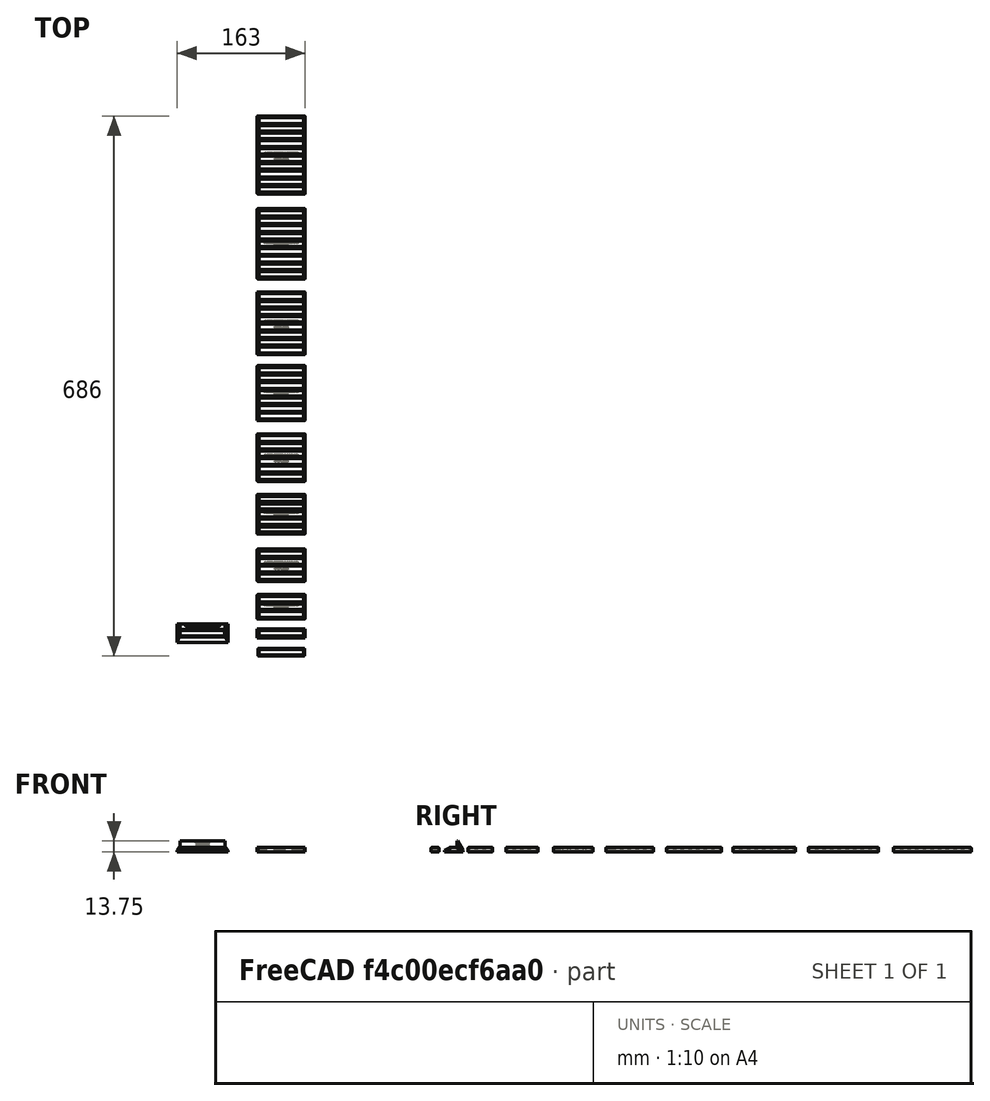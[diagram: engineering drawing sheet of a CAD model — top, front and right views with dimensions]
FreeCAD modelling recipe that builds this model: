
FCSTD DOCUMENT  (FreeCAD 0.21R33771 (Git))
Label: Game Boy Game Shelves
License: All rights reserved
LicenseURL: http://en.wikipedia.org/wiki/All_rights_reserved
objects: Sketcher::SketchObject×35, PartDesign::Pad×24, PartDesign::Pocket×14, PartDesign::Body×12, PartDesign::Chamfer×11, PartDesign::FeatureBase×11, PartDesign::Fillet×9, App::Part×3, PartDesign::ShapeBinder×1
note: 175 computed .brp shape members not serialized (recipe doc carries the construction recipe); baked Part::Feature solids carry a one-line shape summary decoded from their .brp

FEATURE [Sketcher::SketchObject] Sketch
  FullyConstrained = true
  MapMode = 5
  Support = -> [XY_Plane]
  sketch-geometry (16):
    g0: LineSegment StartX=0 StartY=0 StartZ=0 EndX=61 EndY=0 EndZ=0
    g1: LineSegment StartX=61 StartY=0 StartZ=0 EndX=61 EndY=11.7 EndZ=0
    g2: LineSegment StartX=61 StartY=11.7 StartZ=0 EndX=0 EndY=11.7 EndZ=0
    g3: LineSegment StartX=0 StartY=11.7 StartZ=0 EndX=0 EndY=0 EndZ=0
    g4: LineSegment StartX=0 StartY=0 StartZ=0 EndX=2 EndY=0 EndZ=0
    g5: LineSegment StartX=2 StartY=0 StartZ=0 EndX=2 EndY=2 EndZ=0
    g6: LineSegment StartX=2 StartY=2 StartZ=0 EndX=0 EndY=2 EndZ=0
    g7: LineSegment StartX=0 StartY=2 StartZ=0 EndX=0 EndY=0 EndZ=0
    g8: LineSegment StartX=61 StartY=11.7 StartZ=0 EndX=59 EndY=11.7 EndZ=0
    g9: LineSegment StartX=59 StartY=11.7 StartZ=0 EndX=59 EndY=9.7 EndZ=0
    g10: LineSegment StartX=59 StartY=9.7 StartZ=0 EndX=61 EndY=9.7 EndZ=0
    g11: LineSegment StartX=61 StartY=9.7 StartZ=0 EndX=61 EndY=11.7 EndZ=0
    g12: LineSegment StartX=2 StartY=2 StartZ=0 EndX=59 EndY=2 EndZ=0
    g13: LineSegment StartX=59 StartY=2 StartZ=0 EndX=59 EndY=9.7 EndZ=0
    g14: LineSegment StartX=59 StartY=9.7 StartZ=0 EndX=2 EndY=9.7 EndZ=0
    g15: LineSegment StartX=2 StartY=9.7 StartZ=0 EndX=2 EndY=2 EndZ=0
  constraints (43):
    c: Coincident(g0,g1)
    c: Coincident(g1,g2)
    c: Coincident(g2,g3)
    c: Coincident(g3,g0)
    c: Horizontal(g0)
    c: Horizontal(g2)
    c: Vertical(g1)
    c: Vertical(g3)
    c: Coincident(g0,g-1)
    c: Coincident(g4,g5)
    c: Coincident(g5,g6)
    c: Coincident(g6,g7)
    c: Coincident(g7,g4)
    c: Horizontal(g4)
    c: Horizontal(g6)
    c: Vertical(g5)
    c: Vertical(g7)
    c: Coincident(g4,g0)
    c: Coincident(g8,g9)
    c: Coincident(g9,g10)
    c: Coincident(g10,g11)
    c: Coincident(g11,g8)
    c: Horizontal(g8)
    c: Horizontal(g10)
    c: Vertical(g9)
    c: Vertical(g11)
    c: Coincident(g8,g1)
    c: Equal(g9,g10)
    c: Equal(g10,g5)
    c: Equal(g6,g5)
    c: Coincident(g12,g13)
    c: Coincident(g13,g14)
    c: Coincident(g14,g15)
    c: Coincident(g15,g12)
    c: Horizontal(g12)
    c: Horizontal(g14)
    c: Vertical(g13)
    c: Vertical(g15)
    c: Coincident(g12,g5)
    c: Coincident(g13,g9)
    c: Distance(g12) = 57
    c: Distance(g13) = 7.7
    c: Distance(g10) = 2
FEATURE [PartDesign::Pad] Pad
  Direction = (0,0,1)
  Length = 3.5
  Length2 = 10
  Profile = -> Sketch
  ReferenceAxis = -> Sketch [N_Axis]
  Type = 0
FEATURE [Sketcher::SketchObject] Sketch001
  ExternalGeometry = -> [Pad]
  FullyConstrained = true
  MapMode = 5
  Placement = pos=(0,0,0) rot=(1,0,0;3.14159rad)
  Support = -> [Pad]
  sketch-geometry (4):
    g0: LineSegment StartX=0 StartY=0 StartZ=0 EndX=61 EndY=0 EndZ=0
    g1: LineSegment StartX=61 StartY=0 StartZ=0 EndX=61 EndY=-11.7 EndZ=0
    g2: LineSegment StartX=61 StartY=-11.7 StartZ=0 EndX=0 EndY=-11.7 EndZ=0
    g3: LineSegment StartX=0 StartY=-11.7 StartZ=0 EndX=0 EndY=0 EndZ=0
  constraints (10):
    c: Coincident(g0,g1)
    c: Coincident(g1,g2)
    c: Coincident(g2,g3)
    c: Coincident(g3,g0)
    c: Horizontal(g0)
    c: Horizontal(g2)
    c: Vertical(g1)
    c: Vertical(g3)
    c: Coincident(g0,g-1)
    c: Coincident(g1,g-3)
FEATURE [PartDesign::Pad] Pad001
  BaseFeature = -> Pad
  Direction = (0,0,-1)
  Length = 2
  Length2 = 10
  Profile = -> Sketch001
  ReferenceAxis = -> Sketch001 [N_Axis]
  Refine = true
  Type = 0
FEATURE [PartDesign::Chamfer] Chamfer
  Angle = 45
  Base = -> Pad001 [Face8]
  BaseFeature = -> Pad001
  ChamferType = 1
  FlipDirection = false
  Size = 0.25
  Size2 = 3.49
  SupportTransform = false
  UseAllEdges = false
FEATURE [PartDesign::Body] Body  label="Shelf template"
  Group = -> [Sketch,Pad,Sketch001,Pad001,Chamfer]
  Origin = -> Origin
  Tip = -> Chamfer
FEATURE [PartDesign::ShapeBinder] ShapeBinder
  Support = -> [Pad001]
  TraceSupport = false
FEATURE [PartDesign::FeatureBase] Clone
  BaseFeature = -> ShapeBinder
FEATURE [PartDesign::FeatureBase] Clone001
  BaseFeature = -> ShapeBinder
FEATURE [PartDesign::FeatureBase] Clone002
  BaseFeature = -> ShapeBinder
  Placement = pos=(0,175,0) rot=(0,0,1;0rad)
FEATURE [PartDesign::FeatureBase] Clone003
  BaseFeature = -> ShapeBinder
FEATURE [PartDesign::FeatureBase] Clone004
  BaseFeature = -> ShapeBinder
FEATURE [PartDesign::FeatureBase] Clone005
  BaseFeature = -> ShapeBinder
FEATURE [PartDesign::FeatureBase] Clone006
  BaseFeature = -> ShapeBinder
FEATURE [PartDesign::FeatureBase] Clone007
  BaseFeature = -> ShapeBinder
FEATURE [Sketcher::SketchObject] Sketch002
  ExternalGeometry = -> [Clone007]
  FullyConstrained = true
  MapMode = 5
  Placement = pos=(0,0,-2) rot=(1,0,0;3.14159rad)
  Support = -> [Clone007]
  sketch-geometry (7):
    g0: LineSegment StartX=0 StartY=0 StartZ=0 EndX=61 EndY=0 EndZ=0
    g1: LineSegment StartX=61 StartY=0 StartZ=0 EndX=61 EndY=-31.1 EndZ=0
    g2: LineSegment StartX=61 StartY=-31.1 StartZ=0 EndX=0 EndY=-31.1 EndZ=0
    g3: LineSegment StartX=0 StartY=-31.1 StartZ=0 EndX=0 EndY=0 EndZ=0
    g4: LineSegment StartX=2 StartY=-2 StartZ=0 EndX=2 EndY=-11.7 EndZ=0
    g5: LineSegment StartX=2 StartY=-11.7 StartZ=0 EndX=2 EndY=-21.4 EndZ=0
    g6: LineSegment StartX=2 StartY=-21.4 StartZ=0 EndX=2 EndY=-31.1 EndZ=0
  constraints (19):
    c: Coincident(g0,g1)
    c: Coincident(g1,g2)
    c: Coincident(g2,g3)
    c: Coincident(g3,g0)
    c: Horizontal(g2)
    c: Vertical(g1)
    c: Vertical(g3)
    c: Coincident(g0,g-3)
    c: Coincident(g0,g-3)
    c: Coincident(g4,g-5)
    c: PointOnObject(g4,g-4)
    c: Vertical(g4)
    c: Coincident(g5,g4)
    c: Vertical(g5)
    c: Coincident(g6,g5)
    c: PointOnObject(g6,g2)
    c: Vertical(g6)
    c: Equal(g4,g5)
    c: Equal(g5,g6)
FEATURE [PartDesign::Pad] Pad002
  BaseFeature = -> Clone007
  Direction = (0,0,-1)
  Length = 2
  Length2 = 10
  Profile = -> Sketch002
  ReferenceAxis = -> Sketch002 [N_Axis]
  Reversed = true
  Type = 0
FEATURE [Sketcher::SketchObject] Sketch003
  ExternalGeometry = -> [Clone]
  FullyConstrained = true
  MapMode = 5
  Placement = pos=(0,0,-2) rot=(1,0,0;3.14159rad)
  Support = -> [Clone]
  sketch-geometry (8):
    g0: LineSegment StartX=0 StartY=0 StartZ=0 EndX=61 EndY=0 EndZ=0
    g1: LineSegment StartX=61 StartY=0 StartZ=0 EndX=61 EndY=-40.8 EndZ=0
    g2: LineSegment StartX=61 StartY=-40.8 StartZ=0 EndX=0 EndY=-40.8 EndZ=0
    g3: LineSegment StartX=0 StartY=-40.8 StartZ=0 EndX=0 EndY=0 EndZ=0
    g4: LineSegment StartX=2 StartY=-2 StartZ=0 EndX=2 EndY=-11.7 EndZ=0
    g5: LineSegment StartX=2 StartY=-11.7 StartZ=0 EndX=2 EndY=-21.4 EndZ=0
    g6: LineSegment StartX=2 StartY=-21.4 StartZ=0 EndX=2 EndY=-31.1 EndZ=0
    g7: LineSegment StartX=2 StartY=-31.1 StartZ=0 EndX=2 EndY=-40.8 EndZ=0
  constraints (22):
    c: Coincident(g0,g1)
    c: Coincident(g1,g2)
    c: Coincident(g2,g3)
    c: Coincident(g3,g0)
    c: Horizontal(g2)
    c: Vertical(g1)
    c: Vertical(g3)
    c: Coincident(g0,g-3)
    c: Coincident(g0,g-3)
    c: Coincident(g4,g-5)
    c: PointOnObject(g4,g-4)
    c: Vertical(g4)
    c: Coincident(g5,g4)
    c: Vertical(g5)
    c: Coincident(g6,g5)
    c: Vertical(g6)
    c: Coincident(g7,g6)
    c: PointOnObject(g7,g2)
    c: Vertical(g7)
    c: Equal(g7,g6)
    c: Equal(g6,g5)
    c: Equal(g5,g4)
FEATURE [PartDesign::Pad] Pad003
  BaseFeature = -> Clone
  Direction = (0,0,-1)
  Length = 2
  Length2 = 10
  Profile = -> Sketch003
  ReferenceAxis = -> Sketch003 [N_Axis]
  Reversed = true
  Type = 0
FEATURE [Sketcher::SketchObject] Sketch004
  ExternalGeometry = -> [Clone001]
  FullyConstrained = true
  MapMode = 5
  Placement = pos=(0,0,-2) rot=(1,0,0;3.14159rad)
  Support = -> [Clone001]
  sketch-geometry (9):
    g0: LineSegment StartX=2 StartY=-2 StartZ=0 EndX=2 EndY=-11.7 EndZ=0
    g1: LineSegment StartX=2 StartY=-11.7 StartZ=0 EndX=2 EndY=-21.4 EndZ=0
    g2: LineSegment StartX=2 StartY=-21.4 StartZ=0 EndX=2 EndY=-31.1 EndZ=0
    g3: LineSegment StartX=2 StartY=-31.1 StartZ=0 EndX=2 EndY=-40.8 EndZ=0
    g4: LineSegment StartX=2 StartY=-40.8 StartZ=0 EndX=2 EndY=-50.5 EndZ=0
    g5: LineSegment StartX=61 StartY=0 StartZ=0 EndX=0 EndY=0 EndZ=0
    g6: LineSegment StartX=0 StartY=0 StartZ=0 EndX=0 EndY=-50.5 EndZ=0
    g7: LineSegment StartX=0 StartY=-50.5 StartZ=0 EndX=61 EndY=-50.5 EndZ=0
    g8: LineSegment StartX=61 StartY=-50.5 StartZ=0 EndX=61 EndY=0 EndZ=0
  constraints (26):
    c: Coincident(g0,g-5)
    c: PointOnObject(g0,g-4)
    c: Vertical(g0)
    c: Coincident(g1,g0)
    c: Vertical(g1)
    c: Coincident(g2,g1)
    c: Vertical(g2)
    c: Coincident(g3,g2)
    c: Vertical(g3)
    c: Coincident(g4,g3)
    c: Vertical(g4)
    c: Equal(g0,g1)
    c: Equal(g1,g2)
    c: Equal(g2,g3)
    c: Equal(g3,g4)
    c: Coincident(g5,g6)
    c: Coincident(g6,g7)
    c: Coincident(g7,g8)
    c: Coincident(g8,g5)
    c: Horizontal(g5)
    c: Horizontal(g7)
    c: Vertical(g6)
    c: Vertical(g8)
    c: Coincident(g5,g-3)
    c: PointOnObject(g6,g-2)
    c: PointOnObject(g4,g7)
FEATURE [PartDesign::Pad] Pad004
  BaseFeature = -> Clone001
  Direction = (0,0,-1)
  Length = 2
  Length2 = 10
  Profile = -> Sketch004
  ReferenceAxis = -> Sketch004 [N_Axis]
  Reversed = true
  Type = 0
FEATURE [Sketcher::SketchObject] Sketch005
  ExternalGeometry = -> [Clone002]
  FullyConstrained = true
  MapMode = 5
  Placement = pos=(0,175,-2) rot=(1,0,0;3.14159rad)
  Support = -> [Clone002]
  sketch-geometry (10):
    g0: LineSegment StartX=61 StartY=0 StartZ=0 EndX=0 EndY=0 EndZ=0
    g1: LineSegment StartX=0 StartY=0 StartZ=0 EndX=0 EndY=-60.2 EndZ=0
    g2: LineSegment StartX=0 StartY=-60.2 StartZ=0 EndX=61 EndY=-60.2 EndZ=0
    g3: LineSegment StartX=61 StartY=-60.2 StartZ=0 EndX=61 EndY=0 EndZ=0
    g4: LineSegment StartX=2 StartY=-2 StartZ=0 EndX=2 EndY=-11.7 EndZ=0
    g5: LineSegment StartX=2 StartY=-11.7 StartZ=0 EndX=2 EndY=-21.4 EndZ=0
    g6: LineSegment StartX=2 StartY=-21.4 StartZ=0 EndX=2 EndY=-31.1 EndZ=0
    g7: LineSegment StartX=2 StartY=-31.1 StartZ=0 EndX=2 EndY=-40.8 EndZ=0
    g8: LineSegment StartX=2 StartY=-40.8 StartZ=0 EndX=2 EndY=-50.5 EndZ=0
    g9: LineSegment StartX=2 StartY=-50.5 StartZ=0 EndX=2 EndY=-60.2 EndZ=0
  constraints (29):
    c: Coincident(g0,g1)
    c: Coincident(g1,g2)
    c: Coincident(g2,g3)
    c: Coincident(g3,g0)
    c: Horizontal(g0)
    c: Horizontal(g2)
    c: Vertical(g1)
    c: Vertical(g3)
    c: Coincident(g0,g-3)
    c: PointOnObject(g1,g-2)
    c: Coincident(g4,g-5)
    c: PointOnObject(g4,g-4)
    c: Coincident(g5,g4)
    c: Vertical(g5)
    c: Coincident(g6,g5)
    c: Vertical(g6)
    c: Coincident(g7,g6)
    c: Vertical(g7)
    c: Coincident(g8,g7)
    c: Vertical(g8)
    c: Coincident(g9,g8)
    c: PointOnObject(g9,g2)
    c: Vertical(g9)
    c: Vertical(g4)
    c: Equal(g9,g8)
    c: Equal(g8,g7)
    c: Equal(g7,g6)
    c: Equal(g6,g5)
    c: Equal(g5,g4)
FEATURE [PartDesign::Pad] Pad005
  BaseFeature = -> Clone002
  Direction = (0,0,-1)
  Length = 2
  Length2 = 10
  Placement = pos=(0,175,0) rot=(0,0,1;0rad)
  Profile = -> Sketch005
  ReferenceAxis = -> Sketch005 [N_Axis]
  Reversed = true
  Type = 0
FEATURE [Sketcher::SketchObject] Sketch006
  ExternalGeometry = -> [Clone003]
  FullyConstrained = true
  MapMode = 5
  Placement = pos=(0,0,-2) rot=(1,0,0;3.14159rad)
  Support = -> [Clone003]
  sketch-geometry (11):
    g0: LineSegment StartX=61 StartY=0 StartZ=0 EndX=0 EndY=0 EndZ=0
    g1: LineSegment StartX=0 StartY=0 StartZ=0 EndX=0 EndY=-69.9 EndZ=0
    g2: LineSegment StartX=0 StartY=-69.9 StartZ=0 EndX=61 EndY=-69.9 EndZ=0
    g3: LineSegment StartX=61 StartY=-69.9 StartZ=0 EndX=61 EndY=0 EndZ=0
    g4: LineSegment StartX=2 StartY=-2 StartZ=0 EndX=2 EndY=-11.7 EndZ=0
    g5: LineSegment StartX=2 StartY=-11.7 StartZ=0 EndX=2 EndY=-21.4 EndZ=0
    g6: LineSegment StartX=2 StartY=-21.4 StartZ=0 EndX=2 EndY=-31.1 EndZ=0
    g7: LineSegment StartX=2 StartY=-31.1 StartZ=0 EndX=2 EndY=-40.8 EndZ=0
    g8: LineSegment StartX=2 StartY=-40.8 StartZ=0 EndX=2 EndY=-50.5 EndZ=0
    g9: LineSegment StartX=2 StartY=-50.5 StartZ=0 EndX=2 EndY=-60.2 EndZ=0
    g10: LineSegment StartX=2 StartY=-60.2 StartZ=0 EndX=2 EndY=-69.9 EndZ=0
  constraints (31):
    c: Coincident(g0,g1)
    c: Coincident(g1,g2)
    c: Coincident(g2,g3)
    c: Coincident(g3,g0)
    c: Horizontal(g2)
    c: Vertical(g1)
    c: Vertical(g3)
    c: Coincident(g0,g-3)
    c: Coincident(g-3,g0)
    c: Coincident(g4,g-5)
    c: PointOnObject(g4,g-4)
    c: Vertical(g4)
    c: Coincident(g5,g4)
    c: Vertical(g5)
    c: Coincident(g6,g5)
    c: Coincident(g7,g6)
    c: Coincident(g8,g7)
    c: Vertical(g8)
    c: Coincident(g9,g8)
    c: Vertical(g9)
    c: PointOnObject(g10,g2)
    c: Vertical(g10)
    c: Coincident(g10,g9)
    c: Vertical(g7)
    c: Vertical(g6)
    c: Equal(g4,g5)
    c: Equal(g5,g6)
    c: Equal(g6,g7)
    c: Equal(g8,g7)
    c: Equal(g9,g8)
    c: Equal(g9,g10)
FEATURE [PartDesign::Pad] Pad006
  BaseFeature = -> Clone003
  Direction = (0,0,-1)
  Length = 2
  Length2 = 10
  Profile = -> Sketch006
  ReferenceAxis = -> Sketch006 [N_Axis]
  Reversed = true
  Type = 0
FEATURE [Sketcher::SketchObject] Sketch007
  ExternalGeometry = -> [Clone004]
  FullyConstrained = true
  MapMode = 5
  Placement = pos=(0,0,-2) rot=(1,0,0;3.14159rad)
  Support = -> [Clone004]
  sketch-geometry (12):
    g0: LineSegment StartX=61 StartY=0 StartZ=0 EndX=0 EndY=0 EndZ=0
    g1: LineSegment StartX=0 StartY=0 StartZ=0 EndX=0 EndY=-79.6 EndZ=0
    g2: LineSegment StartX=0 StartY=-79.6 StartZ=0 EndX=61 EndY=-79.6 EndZ=0
    g3: LineSegment StartX=61 StartY=-79.6 StartZ=0 EndX=61 EndY=0 EndZ=0
    g4: LineSegment StartX=2 StartY=-2 StartZ=0 EndX=2 EndY=-11.7 EndZ=0
    g5: LineSegment StartX=2 StartY=-11.7 StartZ=0 EndX=2 EndY=-21.4 EndZ=0
    g6: LineSegment StartX=2 StartY=-21.4 StartZ=0 EndX=2 EndY=-31.1 EndZ=0
    g7: LineSegment StartX=2 StartY=-31.1 StartZ=0 EndX=2 EndY=-40.8 EndZ=0
    g8: LineSegment StartX=2 StartY=-40.8 StartZ=0 EndX=2 EndY=-50.5 EndZ=0
    g9: LineSegment StartX=2 StartY=-50.5 StartZ=0 EndX=2 EndY=-60.2 EndZ=0
    g10: LineSegment StartX=2 StartY=-60.2 StartZ=0 EndX=2 EndY=-69.9 EndZ=0
    g11: LineSegment StartX=2 StartY=-69.9 StartZ=0 EndX=2 EndY=-79.6 EndZ=0
  constraints (34):
    c: Coincident(g0,g1)
    c: Coincident(g1,g2)
    c: Coincident(g2,g3)
    c: Coincident(g3,g0)
    c: Horizontal(g2)
    c: Vertical(g1)
    c: Vertical(g3)
    c: Coincident(g0,g-3)
    c: Coincident(g4,g-5)
    c: PointOnObject(g4,g-4)
    c: Vertical(g4)
    c: Coincident(g5,g4)
    c: Vertical(g5)
    c: Coincident(g6,g5)
    c: Vertical(g6)
    c: Coincident(g7,g6)
    c: Vertical(g7)
    c: Coincident(g8,g7)
    c: Vertical(g8)
    c: Coincident(g9,g8)
    c: Vertical(g9)
    c: Coincident(g10,g9)
    c: Vertical(g10)
    c: Coincident(g11,g10)
    c: PointOnObject(g11,g2)
    c: Vertical(g11)
    c: Coincident(g0,g-3)
    c: Equal(g11,g10)
    c: Equal(g10,g9)
    c: Equal(g9,g8)
    c: Equal(g8,g7)
    c: Equal(g6,g5)
    c: Equal(g5,g7)
    c: Equal(g5,g4)
FEATURE [PartDesign::Pad] Pad007
  BaseFeature = -> Clone004
  Direction = (0,0,-1)
  Length = 2
  Length2 = 10
  Profile = -> Sketch007
  ReferenceAxis = -> Sketch007 [N_Axis]
  Reversed = true
  Type = 0
FEATURE [Sketcher::SketchObject] Sketch008
  ExternalGeometry = -> [Clone004]
  FullyConstrained = true
  MapMode = 5
  Placement = pos=(0,0,3.5) rot=(0,0,1;0rad)
  Support = -> [Clone004]
  sketch-geometry (44):
    g0: LineSegment StartX=0 StartY=0 StartZ=0 EndX=61 EndY=0 EndZ=0
    g1: LineSegment StartX=61 StartY=0 StartZ=0 EndX=61 EndY=79.6 EndZ=0
    g2: LineSegment StartX=61 StartY=79.6 StartZ=0 EndX=0 EndY=79.6 EndZ=0
    g3: LineSegment StartX=0 StartY=79.6 StartZ=0 EndX=0 EndY=0 EndZ=0
    g4: LineSegment StartX=59 StartY=2 StartZ=0 EndX=59 EndY=11.7 EndZ=0
    g5: LineSegment StartX=59 StartY=11.7 StartZ=0 EndX=59 EndY=21.4 EndZ=0
    g6: LineSegment StartX=59 StartY=21.4 StartZ=0 EndX=59 EndY=31.1 EndZ=0
    g7: LineSegment StartX=59 StartY=31.1 StartZ=0 EndX=59 EndY=40.8 EndZ=0
    g8: LineSegment StartX=59 StartY=40.8 StartZ=0 EndX=59 EndY=50.5 EndZ=0
    g9: LineSegment StartX=59 StartY=50.5 StartZ=0 EndX=59 EndY=60.2 EndZ=0
    g10: LineSegment StartX=59 StartY=60.2 StartZ=0 EndX=59 EndY=69.9 EndZ=0
    g11: LineSegment StartX=59 StartY=2 StartZ=0 EndX=2 EndY=2 EndZ=0
    g12: LineSegment StartX=2 StartY=2 StartZ=0 EndX=2 EndY=9.7 EndZ=0
    g13: LineSegment StartX=2 StartY=9.7 StartZ=0 EndX=59 EndY=9.7 EndZ=0
    g14: LineSegment StartX=59 StartY=9.7 StartZ=0 EndX=59 EndY=2 EndZ=0
    g15: LineSegment StartX=59 StartY=11.7 StartZ=0 EndX=2 EndY=11.7 EndZ=0
    g16: LineSegment StartX=2 StartY=11.7 StartZ=0 EndX=2 EndY=19.4 EndZ=0
    g17: LineSegment StartX=2 StartY=19.4 StartZ=0 EndX=59 EndY=19.4 EndZ=0
    g18: LineSegment StartX=59 StartY=19.4 StartZ=0 EndX=59 EndY=11.7 EndZ=0
    g19: LineSegment StartX=59 StartY=21.4 StartZ=0 EndX=2 EndY=21.4 EndZ=0
    g20: LineSegment StartX=2 StartY=21.4 StartZ=0 EndX=2 EndY=29.1 EndZ=0
    g21: LineSegment StartX=2 StartY=29.1 StartZ=0 EndX=59 EndY=29.1 EndZ=0
    g22: LineSegment StartX=59 StartY=29.1 StartZ=0 EndX=59 EndY=21.4 EndZ=0
    g23: LineSegment StartX=59 StartY=31.1 StartZ=0 EndX=2 EndY=31.1 EndZ=0
    g24: LineSegment StartX=2 StartY=31.1 StartZ=0 EndX=2 EndY=38.8 EndZ=0
    g25: LineSegment StartX=2 StartY=38.8 StartZ=0 EndX=59 EndY=38.8 EndZ=0
    g26: LineSegment StartX=59 StartY=38.8 StartZ=0 EndX=59 EndY=31.1 EndZ=0
    g27: LineSegment StartX=59 StartY=40.8 StartZ=0 EndX=2 EndY=40.8 EndZ=0
    g28: LineSegment StartX=2 StartY=40.8 StartZ=0 EndX=2 EndY=48.5 EndZ=0
    g29: LineSegment StartX=2 StartY=48.5 StartZ=0 EndX=59 EndY=48.5 EndZ=0
    g30: LineSegment StartX=59 StartY=48.5 StartZ=0 EndX=59 EndY=40.8 EndZ=0
    g31: LineSegment StartX=59 StartY=50.5 StartZ=0 EndX=2 EndY=50.5 EndZ=0
    g32: LineSegment StartX=2 StartY=50.5 StartZ=0 EndX=2 EndY=58.2 EndZ=0
    g33: LineSegment StartX=2 StartY=58.2 StartZ=0 EndX=59 EndY=58.2 EndZ=0
    g34: LineSegment StartX=59 StartY=58.2 StartZ=0 EndX=59 EndY=50.5 EndZ=0
    g35: LineSegment StartX=59 StartY=60.2 StartZ=0 EndX=2 EndY=60.2 EndZ=0
    g36: LineSegment StartX=2 StartY=60.2 StartZ=0 EndX=2 EndY=67.9 EndZ=0
    g37: LineSegment StartX=2 StartY=67.9 StartZ=0 EndX=59 EndY=67.9 EndZ=0
    g38: LineSegment StartX=59 StartY=67.9 StartZ=0 EndX=59 EndY=60.2 EndZ=0
    g39: LineSegment StartX=59 StartY=69.9 StartZ=0 EndX=59 EndY=79.6 EndZ=0
    g40: LineSegment StartX=59 StartY=69.9 StartZ=0 EndX=2 EndY=69.9 EndZ=0
    g41: LineSegment StartX=2 StartY=69.9 StartZ=0 EndX=2 EndY=77.6 EndZ=0
    g42: LineSegment StartX=2 StartY=77.6 StartZ=0 EndX=59 EndY=77.6 EndZ=0
    g43: LineSegment StartX=59 StartY=77.6 StartZ=0 EndX=59 EndY=69.9 EndZ=0
  constraints (121):
    c: Coincident(g0,g1)
    c: Coincident(g1,g2)
    c: Coincident(g2,g3)
    c: Coincident(g3,g0)
    c: Horizontal(g2)
    c: Vertical(g1)
    c: Vertical(g3)
    c: Coincident(g0,g-3)
    c: Coincident(g-3,g0)
    c: Coincident(g4,g-4)
    c: Vertical(g4)
    c: Coincident(g5,g4)
    c: Vertical(g5)
    c: Coincident(g6,g5)
    c: Vertical(g6)
    c: Coincident(g7,g6)
    c: Vertical(g7)
    c: Coincident(g8,g7)
    c: Vertical(g8)
    c: Coincident(g9,g8)
    c: Vertical(g9)
    c: Coincident(g10,g9)
    c: Vertical(g10)
    c: Equal(g10,g9)
    c: Equal(g9,g8)
    c: Equal(g8,g7)
    c: Equal(g7,g6)
    c: Equal(g6,g5)
    c: Equal(g5,g4)
    c: PointOnObject(g4,g-5)
    c: Coincident(g11,g12)
    c: Coincident(g12,g13)
    c: Coincident(g13,g14)
    c: Coincident(g14,g11)
    c: Horizontal(g11)
    c: Horizontal(g13)
    c: Vertical(g12)
    c: Vertical(g14)
    c: Coincident(g11,g4)
    c: Coincident(g12,g-6)
    c: Coincident(g15,g16)
    c: Coincident(g16,g17)
    c: Coincident(g17,g18)
    c: Coincident(g18,g15)
    c: Horizontal(g15)
    c: Horizontal(g17)
    c: Vertical(g16)
    c: Vertical(g18)
    c: Coincident(g15,g4)
    c: Coincident(g19,g20)
    c: Coincident(g20,g21)
    c: Coincident(g21,g22)
    c: Coincident(g22,g19)
    c: Horizontal(g19)
    c: Horizontal(g21)
    c: Vertical(g20)
    c: Vertical(g22)
    c: Coincident(g19,g5)
    c: Coincident(g23,g24)
    c: Coincident(g24,g25)
    c: Coincident(g25,g26)
    c: Coincident(g26,g23)
    c: Horizontal(g23)
    c: Horizontal(g25)
    c: Vertical(g24)
    c: Vertical(g26)
    c: Coincident(g23,g6)
    c: Coincident(g27,g28)
    c: Coincident(g28,g29)
    c: Coincident(g29,g30)
    c: Coincident(g30,g27)
    c: Horizontal(g27)
    c: Horizontal(g29)
    c: Vertical(g28)
    c: Vertical(g30)
    c: Coincident(g27,g7)
    c: Coincident(g31,g32)
    c: Coincident(g32,g33)
    c: Coincident(g33,g34)
    c: Coincident(g34,g31)
    c: Horizontal(g31)
    c: Horizontal(g33)
    c: Vertical(g32)
    c: Vertical(g34)
    c: Coincident(g31,g8)
    c: Coincident(g35,g36)
    c: Coincident(g36,g37)
    c: Coincident(g37,g38)
    c: Coincident(g38,g35)
    c: Horizontal(g35)
    c: Horizontal(g37)
    c: Vertical(g36)
    c: Vertical(g38)
    c: Coincident(g35,g9)
    c: Equal(g36,g32)
    c: Equal(g32,g28)
    c: Equal(g28,g24)
    c: Equal(g20,g24)
    c: Equal(g20,g16)
    c: Equal(g16,g12)
    c: Equal(g13,g15)
    c: Equal(g17,g19)
    c: Equal(g21,g23)
    c: Equal(g25,g27)
    c: Equal(g29,g31)
    c: Equal(g33,g35)
    c: Coincident(g39,g10)
    c: Vertical(g39)
    c: Equal(g39,g10)
    c: PointOnObject(g39,g2)
    c: Coincident(g40,g41)
    c: Coincident(g41,g42)
    c: Coincident(g42,g43)
    c: Coincident(g43,g40)
    c: Horizontal(g40)
    c: Horizontal(g42)
    c: Vertical(g41)
    c: Vertical(g43)
    c: Coincident(g40,g10)
    c: Equal(g41,g36)
    c: Equal(g40,g37)
FEATURE [PartDesign::Pad] Pad008
  BaseFeature = -> Pad007
  Direction = (0,0,1)
  Length = 10
  Length2 = 10
  Profile = -> Sketch008
  ReferenceAxis = -> Sketch008 [N_Axis]
  Refine = true
  Type = 3
  UpToFace = -> Pad007 [Face6]
FEATURE [Sketcher::SketchObject] Sketch009
  ExternalGeometry = -> [Clone005]
  FullyConstrained = true
  MapMode = 5
  Placement = pos=(0,0,-2) rot=(1,0,0;3.14159rad)
  Support = -> [Clone005]
  sketch-geometry (13):
    g0: LineSegment StartX=61 StartY=0 StartZ=0 EndX=0 EndY=0 EndZ=0
    g1: LineSegment StartX=0 StartY=0 StartZ=0 EndX=0 EndY=-89.3 EndZ=0
    g2: LineSegment StartX=0 StartY=-89.3 StartZ=0 EndX=61 EndY=-89.3 EndZ=0
    g3: LineSegment StartX=61 StartY=-89.3 StartZ=0 EndX=61 EndY=0 EndZ=0
    g4: LineSegment StartX=2 StartY=-2 StartZ=0 EndX=2 EndY=-11.7 EndZ=0
    g5: LineSegment StartX=2 StartY=-11.7 StartZ=0 EndX=2 EndY=-21.4 EndZ=0
    g6: LineSegment StartX=2 StartY=-21.4 StartZ=0 EndX=2 EndY=-31.1 EndZ=0
    g7: LineSegment StartX=2 StartY=-31.1 StartZ=0 EndX=2 EndY=-40.8 EndZ=0
    g8: LineSegment StartX=2 StartY=-40.8 StartZ=0 EndX=2 EndY=-50.5 EndZ=0
    g9: LineSegment StartX=2 StartY=-50.5 StartZ=0 EndX=2 EndY=-60.2 EndZ=0
    g10: LineSegment StartX=2 StartY=-60.2 StartZ=0 EndX=2 EndY=-69.9 EndZ=0
    g11: LineSegment StartX=2 StartY=-69.9 StartZ=0 EndX=2 EndY=-79.6 EndZ=0
    g12: LineSegment StartX=2 StartY=-79.6 StartZ=0 EndX=2 EndY=-89.3 EndZ=0
  constraints (38):
    c: Coincident(g0,g1)
    c: Coincident(g1,g2)
    c: Coincident(g2,g3)
    c: Coincident(g3,g0)
    c: Horizontal(g0)
    c: Horizontal(g2)
    c: Vertical(g1)
    c: Vertical(g3)
    c: Coincident(g0,g-3)
    c: PointOnObject(g1,g-2)
    c: Coincident(g4,g-5)
    c: PointOnObject(g4,g-4)
    c: Vertical(g4)
    c: Coincident(g5,g4)
    c: Vertical(g5)
    c: Coincident(g6,g5)
    c: Vertical(g6)
    c: Coincident(g7,g6)
    c: Vertical(g7)
    c: Coincident(g8,g7)
    c: Coincident(g9,g8)
    c: Vertical(g9)
    c: Coincident(g10,g9)
    c: Vertical(g10)
    c: Coincident(g11,g10)
    c: Vertical(g11)
    c: Coincident(g12,g11)
    c: PointOnObject(g12,g2)
    c: Vertical(g12)
    c: Vertical(g8)
    c: Equal(g11,g12)
    c: Equal(g11,g10)
    c: Equal(g10,g9)
    c: Equal(g9,g8)
    c: Equal(g8,g7)
    c: Equal(g7,g6)
    c: Equal(g5,g6)
    c: Equal(g5,g4)
FEATURE [PartDesign::Pad] Pad009
  BaseFeature = -> Clone005
  Direction = (0,0,-1)
  Length = 2
  Length2 = 10
  Profile = -> Sketch009
  ReferenceAxis = -> Sketch009 [N_Axis]
  Reversed = true
  Type = 0
FEATURE [Sketcher::SketchObject] Sketch010
  ExternalGeometry = -> [Clone006]
  FullyConstrained = true
  MapMode = 5
  Placement = pos=(0,0,-2) rot=(1,0,0;3.14159rad)
  Support = -> [Clone006]
  sketch-geometry (14):
    g0: LineSegment StartX=61 StartY=0 StartZ=0 EndX=0 EndY=0 EndZ=0
    g1: LineSegment StartX=0 StartY=0 StartZ=0 EndX=0 EndY=-99 EndZ=0
    g2: LineSegment StartX=0 StartY=-99 StartZ=0 EndX=61 EndY=-99 EndZ=0
    g3: LineSegment StartX=61 StartY=-99 StartZ=0 EndX=61 EndY=0 EndZ=0
    g4: LineSegment StartX=2 StartY=-2 StartZ=0 EndX=2 EndY=-11.7 EndZ=0
    g5: LineSegment StartX=2 StartY=-11.7 StartZ=0 EndX=2 EndY=-21.4 EndZ=0
    g6: LineSegment StartX=2 StartY=-21.4 StartZ=0 EndX=2 EndY=-31.1 EndZ=0
    g7: LineSegment StartX=2 StartY=-31.1 StartZ=0 EndX=2 EndY=-40.8 EndZ=0
    g8: LineSegment StartX=2 StartY=-40.8 StartZ=0 EndX=2 EndY=-50.5 EndZ=0
    g9: LineSegment StartX=2 StartY=-50.5 StartZ=0 EndX=2 EndY=-60.2 EndZ=0
    g10: LineSegment StartX=2 StartY=-60.2 StartZ=0 EndX=2 EndY=-69.9 EndZ=0
    g11: LineSegment StartX=2 StartY=-69.9 StartZ=0 EndX=2 EndY=-79.6 EndZ=0
    g12: LineSegment StartX=2 StartY=-79.6 StartZ=0 EndX=2 EndY=-89.3 EndZ=0
    g13: LineSegment StartX=2 StartY=-89.3 StartZ=0 EndX=2 EndY=-99 EndZ=0
  constraints (41):
    c: Coincident(g0,g1)
    c: Coincident(g1,g2)
    c: Coincident(g2,g3)
    c: Coincident(g3,g0)
    c: Horizontal(g0)
    c: Horizontal(g2)
    c: Vertical(g1)
    c: Vertical(g3)
    c: Coincident(g0,g-3)
    c: PointOnObject(g1,g-2)
    c: Coincident(g4,g-5)
    c: PointOnObject(g4,g-4)
    c: Vertical(g4)
    c: Coincident(g5,g4)
    c: Vertical(g5)
    c: Coincident(g6,g5)
    c: Vertical(g6)
    c: Coincident(g7,g6)
    c: Vertical(g7)
    c: Coincident(g8,g7)
    c: Vertical(g8)
    c: Coincident(g9,g8)
    c: Vertical(g9)
    c: Coincident(g10,g9)
    c: Vertical(g10)
    c: Coincident(g11,g10)
    c: Vertical(g11)
    c: Coincident(g12,g11)
    c: Vertical(g12)
    c: Coincident(g13,g12)
    c: PointOnObject(g13,g2)
    c: Vertical(g13)
    c: Equal(g13,g12)
    c: Equal(g12,g11)
    c: Equal(g11,g10)
    c: Equal(g10,g9)
    c: Equal(g8,g9)
    c: Equal(g7,g8)
    c: Equal(g6,g7)
    c: Equal(g5,g6)
    c: Equal(g5,g4)
FEATURE [PartDesign::Pad] Pad010
  BaseFeature = -> Clone006
  Direction = (0,0,-1)
  Length = 2
  Length2 = 10
  Profile = -> Sketch010
  ReferenceAxis = -> Sketch010 [N_Axis]
  Reversed = true
  Type = 0
FEATURE [Sketcher::SketchObject] Sketch011
  ExternalGeometry = -> [Clone007]
  FullyConstrained = true
  MapMode = 5
  Placement = pos=(0,0,3.5) rot=(0,0,1;0rad)
  Support = -> [Clone007]
  sketch-geometry (19):
    g0: LineSegment StartX=59 StartY=2 StartZ=0 EndX=59 EndY=11.7 EndZ=0
    g1: LineSegment StartX=59 StartY=11.7 StartZ=0 EndX=59 EndY=21.4 EndZ=0
    g2: LineSegment StartX=59 StartY=21.4 StartZ=0 EndX=59 EndY=31.1 EndZ=0
    g3: LineSegment StartX=0 StartY=0 StartZ=0 EndX=61 EndY=0 EndZ=0
    g4: LineSegment StartX=61 StartY=0 StartZ=0 EndX=61 EndY=31.1 EndZ=0
    g5: LineSegment StartX=61 StartY=31.1 StartZ=0 EndX=0 EndY=31.1 EndZ=0
    g6: LineSegment StartX=0 StartY=31.1 StartZ=0 EndX=0 EndY=0 EndZ=0
    g7: LineSegment StartX=59 StartY=2 StartZ=0 EndX=2 EndY=2 EndZ=0
    g8: LineSegment StartX=2 StartY=2 StartZ=0 EndX=2 EndY=9.7 EndZ=0
    g9: LineSegment StartX=2 StartY=9.7 StartZ=0 EndX=59 EndY=9.7 EndZ=0
    g10: LineSegment StartX=59 StartY=9.7 StartZ=0 EndX=59 EndY=2 EndZ=0
    g11: LineSegment StartX=59 StartY=11.7 StartZ=0 EndX=2 EndY=11.7 EndZ=0
    g12: LineSegment StartX=2 StartY=11.7 StartZ=0 EndX=2 EndY=19.4 EndZ=0
    g13: LineSegment StartX=2 StartY=19.4 StartZ=0 EndX=59 EndY=19.4 EndZ=0
    g14: LineSegment StartX=59 StartY=19.4 StartZ=0 EndX=59 EndY=11.7 EndZ=0
    g15: LineSegment StartX=59 StartY=21.4 StartZ=0 EndX=2 EndY=21.4 EndZ=0
    g16: LineSegment StartX=2 StartY=21.4 StartZ=0 EndX=2 EndY=29.1 EndZ=0
    g17: LineSegment StartX=2 StartY=29.1 StartZ=0 EndX=59 EndY=29.1 EndZ=0
    g18: LineSegment StartX=59 StartY=29.1 StartZ=0 EndX=59 EndY=21.4 EndZ=0
  constraints (51):
    c: Coincident(g0,g-4)
    c: PointOnObject(g0,g-5)
    c: Vertical(g0)
    c: Coincident(g1,g0)
    c: Vertical(g1)
    c: Coincident(g2,g1)
    c: Vertical(g2)
    c: Equal(g2,g1)
    c: Equal(g1,g0)
    c: Coincident(g3,g4)
    c: Coincident(g4,g5)
    c: Coincident(g5,g6)
    c: Coincident(g6,g3)
    c: Horizontal(g5)
    c: Vertical(g4)
    c: Vertical(g6)
    c: Coincident(g3,g-3)
    c: Coincident(g-3,g3)
    c: PointOnObject(g2,g5)
    c: Coincident(g7,g8)
    c: Coincident(g8,g9)
    c: Coincident(g9,g10)
    c: Coincident(g10,g7)
    c: Horizontal(g7)
    c: Horizontal(g9)
    c: Vertical(g8)
    c: Vertical(g10)
    c: Coincident(g7,g0)
    c: Coincident(g8,g-6)
    c: Coincident(g11,g12)
    c: Coincident(g12,g13)
    c: Coincident(g13,g14)
    c: Coincident(g14,g11)
    c: Horizontal(g11)
    c: Horizontal(g13)
    c: Vertical(g12)
    c: Vertical(g14)
    c: Coincident(g11,g0)
    c: Coincident(g15,g16)
    c: Coincident(g16,g17)
    c: Coincident(g17,g18)
    c: Coincident(g18,g15)
    c: Horizontal(g15)
    c: Horizontal(g17)
    c: Vertical(g16)
    c: Vertical(g18)
    c: Coincident(g15,g1)
    c: Equal(g15,g13)
    c: Equal(g11,g9)
    c: Equal(g8,g12)
    c: Equal(g12,g16)
FEATURE [PartDesign::Pad] Pad011
  BaseFeature = -> Pad002
  Direction = (0,0,1)
  Length = 10
  Length2 = 10
  Profile = -> Sketch011
  ReferenceAxis = -> Sketch011 [N_Axis]
  Refine = true
  Type = 3
  UpToFace = -> Pad002 [Face6]
FEATURE [Sketcher::SketchObject] Sketch012
  ExternalGeometry = -> [Clone]
  FullyConstrained = true
  MapMode = 5
  Placement = pos=(0,0,3.5) rot=(0,0,1;0rad)
  Support = -> [Clone]
  sketch-geometry (24):
    g0: LineSegment StartX=59 StartY=2 StartZ=0 EndX=2 EndY=2 EndZ=0
    g1: LineSegment StartX=2 StartY=2 StartZ=0 EndX=2 EndY=9.7 EndZ=0
    g2: LineSegment StartX=2 StartY=9.7 StartZ=0 EndX=59 EndY=9.7 EndZ=0
    g3: LineSegment StartX=59 StartY=9.7 StartZ=0 EndX=59 EndY=2 EndZ=0
    g4: LineSegment StartX=59 StartY=2 StartZ=0 EndX=59 EndY=11.7 EndZ=0
    g5: LineSegment StartX=59 StartY=11.7 StartZ=0 EndX=59 EndY=21.4 EndZ=0
    g6: LineSegment StartX=59 StartY=21.4 StartZ=0 EndX=59 EndY=31.1 EndZ=0
    g7: LineSegment StartX=59 StartY=31.1 StartZ=0 EndX=59 EndY=40.8 EndZ=0
    g8: LineSegment StartX=0 StartY=0 StartZ=0 EndX=61 EndY=0 EndZ=0
    g9: LineSegment StartX=61 StartY=0 StartZ=0 EndX=61 EndY=40.8 EndZ=0
    g10: LineSegment StartX=61 StartY=40.8 StartZ=0 EndX=0 EndY=40.8 EndZ=0
    g11: LineSegment StartX=0 StartY=40.8 StartZ=0 EndX=0 EndY=0 EndZ=0
    g12: LineSegment StartX=59 StartY=11.7 StartZ=0 EndX=2 EndY=11.7 EndZ=0
    g13: LineSegment StartX=2 StartY=11.7 StartZ=0 EndX=2 EndY=19.4 EndZ=0
    g14: LineSegment StartX=2 StartY=19.4 StartZ=0 EndX=59 EndY=19.4 EndZ=0
    g15: LineSegment StartX=59 StartY=19.4 StartZ=0 EndX=59 EndY=11.7 EndZ=0
    g16: LineSegment StartX=59 StartY=31.1 StartZ=0 EndX=2 EndY=31.1 EndZ=0
    g17: LineSegment StartX=2 StartY=31.1 StartZ=0 EndX=2 EndY=38.8 EndZ=0
    g18: LineSegment StartX=2 StartY=38.8 StartZ=0 EndX=59 EndY=38.8 EndZ=0
    g19: LineSegment StartX=59 StartY=38.8 StartZ=0 EndX=59 EndY=31.1 EndZ=0
    g20: LineSegment StartX=59 StartY=21.4 StartZ=0 EndX=2 EndY=21.4 EndZ=0
    g21: LineSegment StartX=2 StartY=21.4 StartZ=0 EndX=2 EndY=29.1 EndZ=0
    g22: LineSegment StartX=2 StartY=29.1 StartZ=0 EndX=59 EndY=29.1 EndZ=0
    g23: LineSegment StartX=59 StartY=29.1 StartZ=0 EndX=59 EndY=21.4 EndZ=0
  constraints (65):
    c: Coincident(g0,g1)
    c: Coincident(g1,g2)
    c: Coincident(g2,g3)
    c: Coincident(g3,g0)
    c: Horizontal(g0)
    c: Horizontal(g2)
    c: Vertical(g1)
    c: Vertical(g3)
    c: Coincident(g0,g-3)
    c: Coincident(g1,g-4)
    c: Coincident(g4,g0)
    c: PointOnObject(g4,g-5)
    c: Vertical(g4)
    c: Coincident(g5,g4)
    c: Vertical(g5)
    c: Coincident(g6,g5)
    c: Vertical(g6)
    c: Coincident(g7,g6)
    c: Vertical(g7)
    c: Equal(g7,g6)
    c: Equal(g6,g5)
    c: Equal(g5,g4)
    c: Coincident(g8,g9)
    c: Coincident(g9,g10)
    c: Coincident(g10,g11)
    c: Coincident(g11,g8)
    c: Horizontal(g10)
    c: Vertical(g9)
    c: Vertical(g11)
    c: Coincident(g8,g-6)
    c: Coincident(g-6,g8)
    c: PointOnObject(g7,g10)
    c: Coincident(g12,g13)
    c: Coincident(g13,g14)
    c: Coincident(g14,g15)
    c: Coincident(g15,g12)
    c: Horizontal(g12)
    c: Horizontal(g14)
    c: Vertical(g13)
    c: Vertical(g15)
    c: Coincident(g12,g4)
    c: Coincident(g16,g17)
    c: Coincident(g17,g18)
    c: Coincident(g18,g19)
    c: Coincident(g19,g16)
    c: Horizontal(g16)
    c: Horizontal(g18)
    c: Vertical(g17)
    c: Vertical(g19)
    c: Coincident(g16,g6)
    c: Coincident(g20,g21)
    c: Coincident(g21,g22)
    c: Coincident(g22,g23)
    c: Coincident(g23,g20)
    c: Horizontal(g20)
    c: Horizontal(g22)
    c: Vertical(g21)
    c: Vertical(g23)
    c: Coincident(g20,g5)
    c: Equal(g16,g22)
    c: Equal(g20,g14)
    c: Equal(g12,g2)
    c: Equal(g1,g13)
    c: Equal(g13,g21)
    c: Equal(g21,g17)
FEATURE [PartDesign::Pad] Pad012
  BaseFeature = -> Pad003
  Direction = (0,0,1)
  Length = 10
  Length2 = 10
  Profile = -> Sketch012
  ReferenceAxis = -> Sketch012 [N_Axis]
  Refine = true
  Type = 3
  UpToFace = -> Pad003 [Face6]
FEATURE [Sketcher::SketchObject] Sketch013
  ExternalGeometry = -> [Clone001]
  FullyConstrained = true
  MapMode = 5
  Placement = pos=(0,0,3.5) rot=(0,0,1;0rad)
  Support = -> [Clone001]
  sketch-geometry (29):
    g0: LineSegment StartX=59 StartY=2 StartZ=0 EndX=59 EndY=11.7 EndZ=0
    g1: LineSegment StartX=59 StartY=11.7 StartZ=0 EndX=59 EndY=21.4 EndZ=0
    g2: LineSegment StartX=59 StartY=21.4 StartZ=0 EndX=59 EndY=31.1 EndZ=0
    g3: LineSegment StartX=59 StartY=31.1 StartZ=0 EndX=59 EndY=40.8 EndZ=0
    g4: LineSegment StartX=59 StartY=40.8 StartZ=0 EndX=59 EndY=50.5 EndZ=0
    g5: LineSegment StartX=0 StartY=0 StartZ=0 EndX=61 EndY=0 EndZ=0
    g6: LineSegment StartX=61 StartY=0 StartZ=0 EndX=61 EndY=50.5 EndZ=0
    g7: LineSegment StartX=61 StartY=50.5 StartZ=0 EndX=0 EndY=50.5 EndZ=0
    g8: LineSegment StartX=0 StartY=50.5 StartZ=0 EndX=0 EndY=0 EndZ=0
    g9: LineSegment StartX=2 StartY=9.7 StartZ=0 EndX=59 EndY=9.7 EndZ=0
    g10: LineSegment StartX=59 StartY=9.7 StartZ=0 EndX=59 EndY=2 EndZ=0
    g11: LineSegment StartX=59 StartY=2 StartZ=0 EndX=2 EndY=2 EndZ=0
    g12: LineSegment StartX=2 StartY=2 StartZ=0 EndX=2 EndY=9.7 EndZ=0
    g13: LineSegment StartX=59 StartY=11.7 StartZ=0 EndX=2 EndY=11.7 EndZ=0
    g14: LineSegment StartX=2 StartY=11.7 StartZ=0 EndX=2 EndY=19.4 EndZ=0
    g15: LineSegment StartX=2 StartY=19.4 StartZ=0 EndX=59 EndY=19.4 EndZ=0
    g16: LineSegment StartX=59 StartY=19.4 StartZ=0 EndX=59 EndY=11.7 EndZ=0
    g17: LineSegment StartX=59 StartY=21.4 StartZ=0 EndX=2 EndY=21.4 EndZ=0
    g18: LineSegment StartX=2 StartY=21.4 StartZ=0 EndX=2 EndY=29.1 EndZ=0
    g19: LineSegment StartX=2 StartY=29.1 StartZ=0 EndX=59 EndY=29.1 EndZ=0
    g20: LineSegment StartX=59 StartY=29.1 StartZ=0 EndX=59 EndY=21.4 EndZ=0
    g21: LineSegment StartX=59 StartY=31.1 StartZ=0 EndX=2 EndY=31.1 EndZ=0
    g22: LineSegment StartX=2 StartY=31.1 StartZ=0 EndX=2 EndY=38.8 EndZ=0
    g23: LineSegment StartX=2 StartY=38.8 StartZ=0 EndX=59 EndY=38.8 EndZ=0
    g24: LineSegment StartX=59 StartY=38.8 StartZ=0 EndX=59 EndY=31.1 EndZ=0
    g25: LineSegment StartX=59 StartY=40.8 StartZ=0 EndX=2 EndY=40.8 EndZ=0
    g26: LineSegment StartX=2 StartY=40.8 StartZ=0 EndX=2 EndY=48.5 EndZ=0
    g27: LineSegment StartX=2 StartY=48.5 StartZ=0 EndX=59 EndY=48.5 EndZ=0
    g28: LineSegment StartX=59 StartY=48.5 StartZ=0 EndX=59 EndY=40.8 EndZ=0
  constraints (79):
    c: Coincident(g0,g-4)
    c: PointOnObject(g0,g-6)
    c: Vertical(g0)
    c: Coincident(g1,g0)
    c: Vertical(g1)
    c: Coincident(g2,g1)
    c: Vertical(g2)
    c: Coincident(g3,g2)
    c: Vertical(g3)
    c: Coincident(g4,g3)
    c: Vertical(g4)
    c: Coincident(g5,g6)
    c: Coincident(g6,g7)
    c: Coincident(g7,g8)
    c: Coincident(g8,g5)
    c: Horizontal(g7)
    c: Vertical(g6)
    c: Vertical(g8)
    c: Coincident(g5,g-3)
    c: Coincident(g9,g10)
    c: Coincident(g10,g11)
    c: Coincident(g11,g12)
    c: Coincident(g12,g9)
    c: Horizontal(g9)
    c: Horizontal(g11)
    c: Vertical(g10)
    c: Vertical(g12)
    c: Coincident(g9,g-5)
    c: Coincident(g10,g0)
    c: PointOnObject(g4,g7)
    c: Equal(g4,g3)
    c: Equal(g3,g2)
    c: Equal(g2,g1)
    c: Equal(g1,g0)
    c: Coincident(g-3,g5)
    c: Coincident(g13,g14)
    c: Coincident(g14,g15)
    c: Coincident(g15,g16)
    c: Coincident(g16,g13)
    c: Horizontal(g13)
    c: Horizontal(g15)
    c: Vertical(g14)
    c: Vertical(g16)
    c: Coincident(g13,g0)
    c: Coincident(g17,g18)
    c: Coincident(g18,g19)
    c: Coincident(g19,g20)
    c: Coincident(g20,g17)
    c: Horizontal(g17)
    c: Horizontal(g19)
    c: Vertical(g18)
    c: Vertical(g20)
    c: Coincident(g17,g1)
    c: Coincident(g21,g22)
    c: Coincident(g22,g23)
    c: Coincident(g23,g24)
    c: Coincident(g24,g21)
    c: Horizontal(g21)
    c: Horizontal(g23)
    c: Vertical(g22)
    c: Vertical(g24)
    c: Coincident(g21,g2)
    c: Coincident(g25,g26)
    c: Coincident(g26,g27)
    c: Coincident(g27,g28)
    c: Coincident(g28,g25)
    c: Horizontal(g25)
    c: Horizontal(g27)
    c: Vertical(g26)
    c: Vertical(g28)
    c: Coincident(g25,g3)
    c: Equal(g25,g23)
    c: Equal(g21,g19)
    c: Equal(g17,g15)
    c: Equal(g13,g9)
    c: Equal(g12,g14)
    c: Equal(g14,g18)
    c: Equal(g18,g22)
    c: Equal(g22,g26)
FEATURE [PartDesign::Pad] Pad013
  BaseFeature = -> Pad004
  Direction = (0,0,1)
  Length = 10
  Length2 = 10
  Profile = -> Sketch013
  ReferenceAxis = -> Sketch013 [N_Axis]
  Refine = true
  Type = 3
  UpToFace = -> Pad004 [Face6]
FEATURE [PartDesign::Chamfer] Chamfer002
  Angle = 45
  Base = -> Pad011 [Face18,Face17,Face16]
  BaseFeature = -> Pad011
  ChamferType = 1
  FlipDirection = false
  Size = 0.25
  Size2 = 3.49
  SupportTransform = false
  UseAllEdges = false
FEATURE [PartDesign::Chamfer] Chamfer003
  Angle = 45
  Base = -> Pad012 [Face21,Face22,Face23,Face20]
  BaseFeature = -> Pad012
  ChamferType = 1
  FlipDirection = false
  Size = 0.25
  Size2 = 3.49
  SupportTransform = false
  UseAllEdges = false
FEATURE [PartDesign::Chamfer] Chamfer004
  Angle = 45
  Base = -> Pad013 [Face26,Face25,Face24,Face23,Face22]
  BaseFeature = -> Pad013
  ChamferType = 1
  FlipDirection = false
  Size = 0.25
  Size2 = 3.49
  SupportTransform = false
  UseAllEdges = false
FEATURE [PartDesign::FeatureBase] Clone008
  BaseFeature = -> Chamfer
FEATURE [Sketcher::SketchObject] Sketch014
  ExternalGeometry = -> [Clone008]
  FullyConstrained = true
  MapMode = 5
  Placement = pos=(0,0,3.5) rot=(0,0,1;0rad)
  Support = -> [Clone008]
  sketch-geometry (16):
    g0: LineSegment StartX=0 StartY=0 StartZ=0 EndX=1 EndY=0 EndZ=0
    g1: LineSegment StartX=1 StartY=0 StartZ=0 EndX=1 EndY=1 EndZ=0
    g2: LineSegment StartX=1 StartY=1 StartZ=0 EndX=0 EndY=1 EndZ=0
    g3: LineSegment StartX=0 StartY=1 StartZ=0 EndX=0 EndY=0 EndZ=0
    g4: LineSegment StartX=61 StartY=11.7 StartZ=0 EndX=60 EndY=11.7 EndZ=0
    g5: LineSegment StartX=60 StartY=11.7 StartZ=0 EndX=60 EndY=10.7 EndZ=0
    g6: LineSegment StartX=60 StartY=10.7 StartZ=0 EndX=61 EndY=10.7 EndZ=0
    g7: LineSegment StartX=61 StartY=10.7 StartZ=0 EndX=61 EndY=11.7 EndZ=0
    g8: LineSegment StartX=1 StartY=1 StartZ=0 EndX=60 EndY=1 EndZ=0
    g9: LineSegment StartX=60 StartY=1 StartZ=0 EndX=60 EndY=10.7 EndZ=0
    g10: LineSegment StartX=60 StartY=10.7 StartZ=0 EndX=1 EndY=10.7 EndZ=0
    g11: LineSegment StartX=1 StartY=10.7 StartZ=0 EndX=1 EndY=1 EndZ=0
    g12: LineSegment StartX=61 StartY=11.7 StartZ=0 EndX=0 EndY=11.7 EndZ=0
    g13: LineSegment StartX=0 StartY=11.7 StartZ=0 EndX=0 EndY=0 EndZ=0
    g14: LineSegment StartX=0 StartY=0 StartZ=0 EndX=61 EndY=0 EndZ=0
    g15: LineSegment StartX=61 StartY=0 StartZ=0 EndX=61 EndY=11.7 EndZ=0
  constraints (42):
    c: Coincident(g0,g1)
    c: Coincident(g1,g2)
    c: Coincident(g2,g3)
    c: Coincident(g3,g0)
    c: Horizontal(g0)
    c: Horizontal(g2)
    c: Vertical(g1)
    c: Vertical(g3)
    c: Coincident(g0,g-1)
    c: Coincident(g4,g5)
    c: Coincident(g5,g6)
    c: Coincident(g6,g7)
    c: Coincident(g7,g4)
    c: Horizontal(g4)
    c: Horizontal(g6)
    c: Vertical(g5)
    c: Vertical(g7)
    c: Coincident(g4,g-3)
    c: Coincident(g8,g9)
    c: Coincident(g9,g10)
    c: Coincident(g10,g11)
    c: Coincident(g11,g8)
    c: Horizontal(g8)
    c: Horizontal(g10)
    c: Vertical(g9)
    c: Vertical(g11)
    c: Coincident(g8,g1)
    c: Coincident(g9,g5)
    c: Coincident(g12,g13)
    c: Coincident(g13,g14)
    c: Coincident(g14,g15)
    c: Coincident(g15,g12)
    c: Horizontal(g12)
    c: Horizontal(g14)
    c: Vertical(g13)
    c: Vertical(g15)
    c: Coincident(g12,g4)
    c: Coincident(g13,g0)
    c: Equal(g2,g1)
    c: Equal(g1,g6)
    c: Equal(g6,g5)
    c: Distance(g2) = 1
FEATURE [PartDesign::Pocket] Pocket
  BaseFeature = -> Clone008
  Direction = (0,0,-1)
  Length = 10
  Length2 = 5
  Profile = -> Sketch014
  ReferenceAxis = -> Sketch014 [N_Axis]
  Type = 0
FEATURE [PartDesign::Fillet] Fillet
  Base = -> Pocket [Face12,Face13,Face15,Face11,Face10]
  BaseFeature = -> Pocket
  Radius = 0.5
  SupportTransform = false
  UseAllEdges = false
FEATURE [PartDesign::Body] Body010  label="Dust Cover"
  BaseFeature = -> Chamfer
  Group = -> [Clone008,Sketch014,Pocket,Fillet]
  Origin = -> Origin013
  Placement = pos=(0,-24,0) rot=(0,0,1;0rad)
  Tip = -> Fillet
FEATURE [Sketcher::SketchObject] Sketch015
  ExternalGeometry = -> [Clone002]
  FullyConstrained = true
  MapMode = 5
  Placement = pos=(0,175,3.5) rot=(0,0,1;0rad)
  Support = -> [Clone002]
  sketch-geometry (34):
    g0: LineSegment StartX=2 StartY=9.7 StartZ=0 EndX=59 EndY=9.7 EndZ=0
    g1: LineSegment StartX=59 StartY=9.7 StartZ=0 EndX=59 EndY=2 EndZ=0
    g2: LineSegment StartX=59 StartY=2 StartZ=0 EndX=2 EndY=2 EndZ=0
    g3: LineSegment StartX=2 StartY=2 StartZ=0 EndX=2 EndY=9.7 EndZ=0
    g4: LineSegment StartX=0 StartY=0 StartZ=0 EndX=61 EndY=0 EndZ=0
    g5: LineSegment StartX=61 StartY=0 StartZ=0 EndX=61 EndY=60.2 EndZ=0
    g6: LineSegment StartX=61 StartY=60.2 StartZ=0 EndX=0 EndY=60.2 EndZ=0
    g7: LineSegment StartX=0 StartY=60.2 StartZ=0 EndX=0 EndY=0 EndZ=0
    g8: LineSegment StartX=59 StartY=2 StartZ=0 EndX=59 EndY=11.7 EndZ=0
    g9: LineSegment StartX=59 StartY=11.7 StartZ=0 EndX=59 EndY=21.4 EndZ=0
    g10: LineSegment StartX=59 StartY=21.4 StartZ=0 EndX=59 EndY=31.1 EndZ=0
    g11: LineSegment StartX=59 StartY=31.1 StartZ=0 EndX=59 EndY=40.8 EndZ=0
    g12: LineSegment StartX=59 StartY=40.8 StartZ=0 EndX=59 EndY=50.5 EndZ=0
    g13: LineSegment StartX=59 StartY=50.5 StartZ=0 EndX=59 EndY=60.2 EndZ=0
    g14: LineSegment StartX=59 StartY=11.7 StartZ=0 EndX=2 EndY=11.7 EndZ=0
    g15: LineSegment StartX=2 StartY=11.7 StartZ=0 EndX=2 EndY=19.4 EndZ=0
    g16: LineSegment StartX=2 StartY=19.4 StartZ=0 EndX=59 EndY=19.4 EndZ=0
    g17: LineSegment StartX=59 StartY=19.4 StartZ=0 EndX=59 EndY=11.7 EndZ=0
    g18: LineSegment StartX=59 StartY=21.4 StartZ=0 EndX=2 EndY=21.4 EndZ=0
    g19: LineSegment StartX=2 StartY=21.4 StartZ=0 EndX=2 EndY=29.1 EndZ=0
    g20: LineSegment StartX=2 StartY=29.1 StartZ=0 EndX=59 EndY=29.1 EndZ=0
    g21: LineSegment StartX=59 StartY=29.1 StartZ=0 EndX=59 EndY=21.4 EndZ=0
    g22: LineSegment StartX=59 StartY=31.1 StartZ=0 EndX=2 EndY=31.1 EndZ=0
    g23: LineSegment StartX=2 StartY=31.1 StartZ=0 EndX=2 EndY=38.8 EndZ=0
    g24: LineSegment StartX=2 StartY=38.8 StartZ=0 EndX=59 EndY=38.8 EndZ=0
    g25: LineSegment StartX=59 StartY=38.8 StartZ=0 EndX=59 EndY=31.1 EndZ=0
    g26: LineSegment StartX=59 StartY=40.8 StartZ=0 EndX=2 EndY=40.8 EndZ=0
    g27: LineSegment StartX=2 StartY=40.8 StartZ=0 EndX=2 EndY=48.5 EndZ=0
    g28: LineSegment StartX=2 StartY=48.5 StartZ=0 EndX=59 EndY=48.5 EndZ=0
    g29: LineSegment StartX=59 StartY=48.5 StartZ=0 EndX=59 EndY=40.8 EndZ=0
    g30: LineSegment StartX=59 StartY=50.5 StartZ=0 EndX=2 EndY=50.5 EndZ=0
    g31: LineSegment StartX=2 StartY=50.5 StartZ=0 EndX=2 EndY=58.2 EndZ=0
    g32: LineSegment StartX=2 StartY=58.2 StartZ=0 EndX=59 EndY=58.2 EndZ=0
    g33: LineSegment StartX=59 StartY=58.2 StartZ=0 EndX=59 EndY=50.5 EndZ=0
  constraints (93):
    c: Coincident(g0,g1)
    c: Coincident(g1,g2)
    c: Coincident(g2,g3)
    c: Coincident(g3,g0)
    c: Horizontal(g0)
    c: Horizontal(g2)
    c: Vertical(g1)
    c: Vertical(g3)
    c: Coincident(g0,g-5)
    c: Coincident(g1,g-4)
    c: Coincident(g4,g5)
    c: Coincident(g5,g6)
    c: Coincident(g6,g7)
    c: Coincident(g7,g4)
    c: Horizontal(g6)
    c: Vertical(g5)
    c: Vertical(g7)
    c: Coincident(g4,g-3)
    c: Coincident(g8,g1)
    c: PointOnObject(g8,g-6)
    c: Vertical(g8)
    c: Coincident(g9,g8)
    c: Vertical(g9)
    c: Coincident(g10,g9)
    c: Vertical(g10)
    c: Coincident(g11,g10)
    c: Vertical(g11)
    c: Coincident(g12,g11)
    c: Vertical(g12)
    c: Coincident(g13,g12)
    c: Vertical(g13)
    c: PointOnObject(g13,g6)
    c: Coincident(g-3,g4)
    c: Equal(g8,g9)
    c: Equal(g9,g10)
    c: Equal(g10,g11)
    c: Equal(g11,g12)
    c: Equal(g12,g13)
    c: Coincident(g14,g15)
    c: Coincident(g15,g16)
    c: Coincident(g16,g17)
    c: Coincident(g17,g14)
    c: Horizontal(g14)
    c: Horizontal(g16)
    c: Vertical(g15)
    c: Vertical(g17)
    c: Coincident(g14,g8)
    c: Coincident(g18,g19)
    c: Coincident(g19,g20)
    c: Coincident(g20,g21)
    c: Coincident(g21,g18)
    c: Horizontal(g18)
    c: Horizontal(g20)
    c: Vertical(g19)
    c: Vertical(g21)
    c: Coincident(g18,g9)
    c: Coincident(g22,g23)
    c: Coincident(g23,g24)
    c: Coincident(g24,g25)
    c: Coincident(g25,g22)
    c: Horizontal(g22)
    c: Horizontal(g24)
    c: Vertical(g23)
    c: Vertical(g25)
    c: Coincident(g22,g10)
    c: Coincident(g26,g27)
    c: Coincident(g27,g28)
    c: Coincident(g28,g29)
    c: Coincident(g29,g26)
    c: Horizontal(g26)
    c: Horizontal(g28)
    c: Vertical(g27)
    c: Vertical(g29)
    c: Coincident(g26,g11)
    c: Coincident(g30,g31)
    c: Coincident(g31,g32)
    c: Coincident(g32,g33)
    c: Coincident(g33,g30)
    c: Horizontal(g30)
    c: Horizontal(g32)
    c: Vertical(g31)
    c: Vertical(g33)
    c: Coincident(g30,g12)
    c: Equal(g30,g28)
    c: Equal(g26,g24)
    c: Equal(g18,g16)
    c: Equal(g22,g20)
    c: Equal(g14,g0)
    c: Equal(g15,g3)
    c: Equal(g15,g19)
    c: Equal(g19,g23)
    c: Equal(g23,g27)
    c: Equal(g27,g31)
FEATURE [PartDesign::Pad] Pad014
  BaseFeature = -> Pad005
  Direction = (0,0,1)
  Length = 10
  Length2 = 10
  Placement = pos=(0,175,0) rot=(0,0,1;0rad)
  Profile = -> Sketch015
  ReferenceAxis = -> Sketch015 [N_Axis]
  Refine = true
  Type = 3
  UpToFace = -> Pad005 [Face6]
FEATURE [Sketcher::SketchObject] Sketch016
  ExternalGeometry = -> [Clone003]
  FullyConstrained = true
  MapMode = 5
  Placement = pos=(0,0,3.5) rot=(0,0,1;0rad)
  Support = -> [Clone003]
  sketch-geometry (39):
    g0: LineSegment StartX=0 StartY=0 StartZ=0 EndX=61 EndY=0 EndZ=0
    g1: LineSegment StartX=61 StartY=0 StartZ=0 EndX=61 EndY=69.9 EndZ=0
    g2: LineSegment StartX=61 StartY=69.9 StartZ=0 EndX=0 EndY=69.9 EndZ=0
    g3: LineSegment StartX=0 StartY=69.9 StartZ=0 EndX=0 EndY=0 EndZ=0
    g4: LineSegment StartX=59 StartY=2 StartZ=0 EndX=59 EndY=11.7 EndZ=0
    g5: LineSegment StartX=59 StartY=11.7 StartZ=0 EndX=59 EndY=21.4 EndZ=0
    g6: LineSegment StartX=59 StartY=21.4 StartZ=0 EndX=59 EndY=31.1 EndZ=0
    g7: LineSegment StartX=59 StartY=31.1 StartZ=0 EndX=59 EndY=40.8 EndZ=0
    g8: LineSegment StartX=59 StartY=40.8 StartZ=0 EndX=59 EndY=50.5 EndZ=0
    g9: LineSegment StartX=59 StartY=50.5 StartZ=0 EndX=59 EndY=60.2 EndZ=0
    g10: LineSegment StartX=59 StartY=60.2 StartZ=0 EndX=59 EndY=69.9 EndZ=0
    g11: LineSegment StartX=59 StartY=2 StartZ=0 EndX=2 EndY=2 EndZ=0
    g12: LineSegment StartX=2 StartY=2 StartZ=0 EndX=2 EndY=9.7 EndZ=0
    g13: LineSegment StartX=2 StartY=9.7 StartZ=0 EndX=59 EndY=9.7 EndZ=0
    g14: LineSegment StartX=59 StartY=9.7 StartZ=0 EndX=59 EndY=2 EndZ=0
    g15: LineSegment StartX=59 StartY=11.7 StartZ=0 EndX=2 EndY=11.7 EndZ=0
    g16: LineSegment StartX=2 StartY=11.7 StartZ=0 EndX=2 EndY=19.4 EndZ=0
    g17: LineSegment StartX=2 StartY=19.4 StartZ=0 EndX=59 EndY=19.4 EndZ=0
    g18: LineSegment StartX=59 StartY=19.4 StartZ=0 EndX=59 EndY=11.7 EndZ=0
    g19: LineSegment StartX=59 StartY=21.4 StartZ=0 EndX=2 EndY=21.4 EndZ=0
    g20: LineSegment StartX=2 StartY=21.4 StartZ=0 EndX=2 EndY=29.1 EndZ=0
    g21: LineSegment StartX=2 StartY=29.1 StartZ=0 EndX=59 EndY=29.1 EndZ=0
    g22: LineSegment StartX=59 StartY=29.1 StartZ=0 EndX=59 EndY=21.4 EndZ=0
    g23: LineSegment StartX=59 StartY=31.1 StartZ=0 EndX=2 EndY=31.1 EndZ=0
    g24: LineSegment StartX=2 StartY=31.1 StartZ=0 EndX=2 EndY=38.8 EndZ=0
    g25: LineSegment StartX=2 StartY=38.8 StartZ=0 EndX=59 EndY=38.8 EndZ=0
    g26: LineSegment StartX=59 StartY=38.8 StartZ=0 EndX=59 EndY=31.1 EndZ=0
    g27: LineSegment StartX=59 StartY=40.8 StartZ=0 EndX=2 EndY=40.8 EndZ=0
    g28: LineSegment StartX=2 StartY=40.8 StartZ=0 EndX=2 EndY=48.5 EndZ=0
    g29: LineSegment StartX=2 StartY=48.5 StartZ=0 EndX=59 EndY=48.5 EndZ=0
    g30: LineSegment StartX=59 StartY=48.5 StartZ=0 EndX=59 EndY=40.8 EndZ=0
    g31: LineSegment StartX=59 StartY=50.5 StartZ=0 EndX=2 EndY=50.5 EndZ=0
    g32: LineSegment StartX=2 StartY=50.5 StartZ=0 EndX=2 EndY=58.2 EndZ=0
    g33: LineSegment StartX=2 StartY=58.2 StartZ=0 EndX=59 EndY=58.2 EndZ=0
    g34: LineSegment StartX=59 StartY=58.2 StartZ=0 EndX=59 EndY=50.5 EndZ=0
    g35: LineSegment StartX=59 StartY=60.2 StartZ=0 EndX=2 EndY=60.2 EndZ=0
    g36: LineSegment StartX=2 StartY=60.2 StartZ=0 EndX=2 EndY=67.9 EndZ=0
    g37: LineSegment StartX=2 StartY=67.9 StartZ=0 EndX=59 EndY=67.9 EndZ=0
    g38: LineSegment StartX=59 StartY=67.9 StartZ=0 EndX=59 EndY=60.2 EndZ=0
  constraints (107):
    c: Coincident(g0,g1)
    c: Coincident(g1,g2)
    c: Coincident(g2,g3)
    c: Coincident(g3,g0)
    c: Horizontal(g2)
    c: Vertical(g1)
    c: Vertical(g3)
    c: Coincident(g0,g-3)
    c: Coincident(g0,g-3)
    c: Coincident(g4,g-4)
    c: PointOnObject(g4,g-6)
    c: Vertical(g4)
    c: Coincident(g5,g4)
    c: Vertical(g5)
    c: Coincident(g6,g5)
    c: Vertical(g6)
    c: Coincident(g7,g6)
    c: Vertical(g7)
    c: Coincident(g8,g7)
    c: Vertical(g8)
    c: Coincident(g9,g8)
    c: Vertical(g9)
    c: Equal(g4,g5)
    c: Equal(g5,g6)
    c: Equal(g6,g7)
    c: Equal(g9,g8)
    c: Equal(g8,g7)
    c: Coincident(g10,g9)
    c: PointOnObject(g10,g2)
    c: Vertical(g10)
    c: Equal(g10,g9)
    c: Coincident(g11,g12)
    c: Coincident(g12,g13)
    c: Coincident(g13,g14)
    c: Coincident(g14,g11)
    c: Horizontal(g11)
    c: Horizontal(g13)
    c: Vertical(g12)
    c: Vertical(g14)
    c: Coincident(g11,g4)
    c: Coincident(g12,g-5)
    c: Coincident(g15,g16)
    c: Coincident(g16,g17)
    c: Coincident(g17,g18)
    c: Coincident(g18,g15)
    c: Horizontal(g15)
    c: Horizontal(g17)
    c: Vertical(g16)
    c: Vertical(g18)
    c: Coincident(g15,g4)
    c: Coincident(g19,g20)
    c: Coincident(g20,g21)
    c: Coincident(g21,g22)
    c: Coincident(g22,g19)
    c: Horizontal(g19)
    c: Horizontal(g21)
    c: Vertical(g20)
    c: Vertical(g22)
    c: Coincident(g19,g5)
    c: Coincident(g23,g24)
    c: Coincident(g24,g25)
    c: Coincident(g25,g26)
    c: Coincident(g26,g23)
    c: Horizontal(g23)
    c: Horizontal(g25)
    c: Vertical(g24)
    c: Vertical(g26)
    c: Coincident(g23,g6)
    c: Coincident(g27,g28)
    c: Coincident(g28,g29)
    c: Coincident(g29,g30)
    c: Coincident(g30,g27)
    c: Horizontal(g27)
    c: Horizontal(g29)
    c: Vertical(g28)
    c: Vertical(g30)
    c: Coincident(g27,g7)
    c: Coincident(g31,g32)
    c: Coincident(g32,g33)
    c: Coincident(g33,g34)
    c: Coincident(g34,g31)
    c: Horizontal(g31)
    c: Horizontal(g33)
    c: Vertical(g32)
    c: Vertical(g34)
    c: Coincident(g31,g8)
    c: Coincident(g35,g36)
    c: Coincident(g36,g37)
    c: Coincident(g37,g38)
    c: Coincident(g38,g35)
    c: Horizontal(g35)
    c: Horizontal(g37)
    c: Vertical(g36)
    c: Vertical(g38)
    c: Coincident(g35,g9)
    c: Equal(g35,g33)
    c: Equal(g31,g29)
    c: Equal(g27,g25)
    c: Equal(g23,g21)
    c: Equal(g19,g17)
    c: Equal(g15,g13)
    c: Equal(g12,g16)
    c: Equal(g16,g20)
    c: Equal(g20,g24)
    c: Equal(g24,g28)
    c: Equal(g28,g32)
    c: Equal(g32,g36)
FEATURE [PartDesign::Pad] Pad015
  BaseFeature = -> Pad006
  Direction = (0,0,1)
  Length = 10
  Length2 = 10
  Profile = -> Sketch016
  ReferenceAxis = -> Sketch016 [N_Axis]
  Refine = true
  Type = 3
  UpToFace = -> Pad006 [Face6]
FEATURE [Sketcher::SketchObject] Sketch017
  ExternalGeometry = -> [Clone005]
  FullyConstrained = true
  MapMode = 5
  Placement = pos=(0,0,3.5) rot=(0,0,1;0rad)
  Support = -> [Clone005]
  sketch-geometry (49):
    g0: LineSegment StartX=0 StartY=0 StartZ=0 EndX=61 EndY=0 EndZ=0
    g1: LineSegment StartX=61 StartY=0 StartZ=0 EndX=61 EndY=89.3 EndZ=0
    g2: LineSegment StartX=61 StartY=89.3 StartZ=0 EndX=0 EndY=89.3 EndZ=0
    g3: LineSegment StartX=0 StartY=89.3 StartZ=0 EndX=0 EndY=0 EndZ=0
    g4: LineSegment StartX=59 StartY=2 StartZ=0 EndX=59 EndY=11.7 EndZ=0
    g5: LineSegment StartX=59 StartY=11.7 StartZ=0 EndX=59 EndY=21.4 EndZ=0
    g6: LineSegment StartX=59 StartY=21.4 StartZ=0 EndX=59 EndY=31.1 EndZ=0
    g7: LineSegment StartX=59 StartY=31.1 StartZ=0 EndX=59 EndY=40.8 EndZ=0
    g8: LineSegment StartX=59 StartY=40.8 StartZ=0 EndX=59 EndY=50.5 EndZ=0
    g9: LineSegment StartX=59 StartY=50.5 StartZ=0 EndX=59 EndY=60.2 EndZ=0
    g10: LineSegment StartX=59 StartY=60.2 StartZ=0 EndX=59 EndY=69.9 EndZ=0
    g11: LineSegment StartX=59 StartY=69.9 StartZ=0 EndX=59 EndY=79.6 EndZ=0
    g12: LineSegment StartX=59 StartY=79.6 StartZ=0 EndX=59 EndY=89.3 EndZ=0
    g13: LineSegment StartX=59 StartY=2 StartZ=0 EndX=2 EndY=2 EndZ=0
    g14: LineSegment StartX=2 StartY=2 StartZ=0 EndX=2 EndY=9.7 EndZ=0
    g15: LineSegment StartX=2 StartY=9.7 StartZ=0 EndX=59 EndY=9.7 EndZ=0
    g16: LineSegment StartX=59 StartY=9.7 StartZ=0 EndX=59 EndY=2 EndZ=0
    g17: LineSegment StartX=59 StartY=11.7 StartZ=0 EndX=2 EndY=11.7 EndZ=0
    g18: LineSegment StartX=2 StartY=11.7 StartZ=0 EndX=2 EndY=19.4 EndZ=0
    g19: LineSegment StartX=2 StartY=19.4 StartZ=0 EndX=59 EndY=19.4 EndZ=0
    g20: LineSegment StartX=59 StartY=19.4 StartZ=0 EndX=59 EndY=11.7 EndZ=0
    g21: LineSegment StartX=59 StartY=21.4 StartZ=0 EndX=2 EndY=21.4 EndZ=0
    g22: LineSegment StartX=2 StartY=21.4 StartZ=0 EndX=2 EndY=29.1 EndZ=0
    g23: LineSegment StartX=2 StartY=29.1 StartZ=0 EndX=59 EndY=29.1 EndZ=0
    g24: LineSegment StartX=59 StartY=29.1 StartZ=0 EndX=59 EndY=21.4 EndZ=0
    g25: LineSegment StartX=59 StartY=31.1 StartZ=0 EndX=2 EndY=31.1 EndZ=0
    g26: LineSegment StartX=2 StartY=31.1 StartZ=0 EndX=2 EndY=38.8 EndZ=0
    g27: LineSegment StartX=2 StartY=38.8 StartZ=0 EndX=59 EndY=38.8 EndZ=0
    g28: LineSegment StartX=59 StartY=38.8 StartZ=0 EndX=59 EndY=31.1 EndZ=0
    g29: LineSegment StartX=59 StartY=40.8 StartZ=0 EndX=2 EndY=40.8 EndZ=0
    g30: LineSegment StartX=2 StartY=40.8 StartZ=0 EndX=2 EndY=48.5 EndZ=0
    g31: LineSegment StartX=2 StartY=48.5 StartZ=0 EndX=59 EndY=48.5 EndZ=0
    g32: LineSegment StartX=59 StartY=48.5 StartZ=0 EndX=59 EndY=40.8 EndZ=0
    g33: LineSegment StartX=59 StartY=50.5 StartZ=0 EndX=2 EndY=50.5 EndZ=0
    g34: LineSegment StartX=2 StartY=50.5 StartZ=0 EndX=2 EndY=58.2 EndZ=0
    g35: LineSegment StartX=2 StartY=58.2 StartZ=0 EndX=59 EndY=58.2 EndZ=0
    g36: LineSegment StartX=59 StartY=58.2 StartZ=0 EndX=59 EndY=50.5 EndZ=0
    g37: LineSegment StartX=59 StartY=60.2 StartZ=0 EndX=2 EndY=60.2 EndZ=0
    g38: LineSegment StartX=2 StartY=60.2 StartZ=0 EndX=2 EndY=67.9 EndZ=0
    g39: LineSegment StartX=2 StartY=67.9 StartZ=0 EndX=59 EndY=67.9 EndZ=0
    g40: LineSegment StartX=59 StartY=67.9 StartZ=0 EndX=59 EndY=60.2 EndZ=0
    g41: LineSegment StartX=59 StartY=69.9 StartZ=0 EndX=2 EndY=69.9 EndZ=0
    g42: LineSegment StartX=2 StartY=69.9 StartZ=0 EndX=2 EndY=77.6 EndZ=0
    g43: LineSegment StartX=2 StartY=77.6 StartZ=0 EndX=59 EndY=77.6 EndZ=0
    g44: LineSegment StartX=59 StartY=77.6 StartZ=0 EndX=59 EndY=69.9 EndZ=0
    g45: LineSegment StartX=59 StartY=79.6 StartZ=0 EndX=2 EndY=79.6 EndZ=0
    g46: LineSegment StartX=2 StartY=79.6 StartZ=0 EndX=2 EndY=87.3 EndZ=0
    g47: LineSegment StartX=2 StartY=87.3 StartZ=0 EndX=59 EndY=87.3 EndZ=0
    g48: LineSegment StartX=59 StartY=87.3 StartZ=0 EndX=59 EndY=79.6 EndZ=0
  constraints (135):
    c: Coincident(g0,g1)
    c: Coincident(g1,g2)
    c: Coincident(g2,g3)
    c: Coincident(g3,g0)
    c: Horizontal(g2)
    c: Vertical(g1)
    c: Vertical(g3)
    c: Coincident(g0,g-3)
    c: Coincident(g-3,g0)
    c: Coincident(g4,g-4)
    c: PointOnObject(g4,g-6)
    c: Vertical(g4)
    c: Coincident(g5,g4)
    c: Vertical(g5)
    c: Coincident(g6,g5)
    c: Vertical(g6)
    c: Coincident(g7,g6)
    c: Vertical(g7)
    c: Coincident(g8,g7)
    c: Vertical(g8)
    c: Coincident(g9,g8)
    c: Vertical(g9)
    c: Coincident(g10,g9)
    c: Vertical(g10)
    c: Coincident(g11,g10)
    c: Vertical(g11)
    c: Coincident(g12,g11)
    c: PointOnObject(g12,g2)
    c: Vertical(g12)
    c: Equal(g4,g5)
    c: Equal(g5,g6)
    c: Equal(g6,g7)
    c: Equal(g7,g8)
    c: Equal(g9,g8)
    c: Equal(g9,g10)
    c: Equal(g10,g11)
    c: Equal(g12,g11)
    c: Coincident(g13,g14)
    c: Coincident(g14,g15)
    c: Coincident(g15,g16)
    c: Coincident(g16,g13)
    c: Horizontal(g13)
    c: Horizontal(g15)
    c: Vertical(g14)
    c: Vertical(g16)
    c: Coincident(g13,g4)
    c: Coincident(g14,g-5)
    c: Coincident(g17,g18)
    c: Coincident(g18,g19)
    c: Coincident(g19,g20)
    c: Coincident(g20,g17)
    c: Horizontal(g17)
    c: Horizontal(g19)
    c: Vertical(g18)
    c: Vertical(g20)
    c: Coincident(g17,g4)
    c: Coincident(g21,g22)
    c: Coincident(g22,g23)
    c: Coincident(g23,g24)
    c: Coincident(g24,g21)
    c: Horizontal(g21)
    c: Horizontal(g23)
    c: Vertical(g22)
    c: Vertical(g24)
    c: Coincident(g21,g5)
    c: Coincident(g25,g26)
    c: Coincident(g26,g27)
    c: Coincident(g27,g28)
    c: Coincident(g28,g25)
    c: Horizontal(g25)
    c: Horizontal(g27)
    c: Vertical(g26)
    c: Vertical(g28)
    c: Coincident(g25,g6)
    c: Coincident(g29,g30)
    c: Coincident(g30,g31)
    c: Coincident(g31,g32)
    c: Coincident(g32,g29)
    c: Horizontal(g29)
    c: Horizontal(g31)
    c: Vertical(g30)
    c: Vertical(g32)
    c: Coincident(g29,g7)
    c: Coincident(g33,g34)
    c: Coincident(g34,g35)
    c: Coincident(g35,g36)
    c: Coincident(g36,g33)
    c: Horizontal(g33)
    c: Horizontal(g35)
    c: Vertical(g34)
    c: Vertical(g36)
    c: Coincident(g33,g8)
    c: Coincident(g37,g38)
    c: Coincident(g38,g39)
    c: Coincident(g39,g40)
    c: Coincident(g40,g37)
    c: Horizontal(g37)
    c: Horizontal(g39)
    c: Vertical(g38)
    c: Vertical(g40)
    c: Coincident(g37,g9)
    c: Coincident(g41,g42)
    c: Coincident(g42,g43)
    c: Coincident(g43,g44)
    c: Coincident(g44,g41)
    c: Horizontal(g41)
    c: Horizontal(g43)
    c: Vertical(g42)
    c: Vertical(g44)
    c: Coincident(g41,g10)
    c: Coincident(g45,g46)
    c: Coincident(g46,g47)
    c: Coincident(g47,g48)
    c: Coincident(g48,g45)
    c: Horizontal(g45)
    c: Horizontal(g47)
    c: Vertical(g46)
    c: Vertical(g48)
    c: Coincident(g45,g11)
    c: Equal(g45,g43)
    c: Equal(g41,g39)
    c: Equal(g37,g35)
    c: Equal(g33,g31)
    c: Equal(g29,g27)
    c: Equal(g25,g23)
    c: Equal(g21,g19)
    c: Equal(g17,g15)
    c: Equal(g14,g18)
    c: Equal(g22,g18)
    c: Equal(g26,g22)
    c: Equal(g30,g26)
    c: Equal(g34,g30)
    c: Equal(g38,g34)
    c: Equal(g38,g42)
    c: Equal(g42,g46)
FEATURE [PartDesign::Pad] Pad016
  BaseFeature = -> Pad009
  Direction = (0,0,1)
  Length = 10
  Length2 = 10
  Profile = -> Sketch017
  ReferenceAxis = -> Sketch017 [N_Axis]
  Refine = true
  Type = 3
  UpToFace = -> Pad009 [Face6]
FEATURE [Sketcher::SketchObject] Sketch018
  ExternalGeometry = -> [Clone006]
  FullyConstrained = true
  MapMode = 5
  Placement = pos=(0,0,3.5) rot=(0,0,1;0rad)
  Support = -> [Clone006]
  sketch-geometry (54):
    g0: LineSegment StartX=0 StartY=0 StartZ=0 EndX=61 EndY=0 EndZ=0
    g1: LineSegment StartX=61 StartY=0 StartZ=0 EndX=61 EndY=99 EndZ=0
    g2: LineSegment StartX=61 StartY=99 StartZ=0 EndX=0 EndY=99 EndZ=0
    g3: LineSegment StartX=0 StartY=99 StartZ=0 EndX=0 EndY=0 EndZ=0
    g4: LineSegment StartX=59 StartY=2 StartZ=0 EndX=59 EndY=11.7 EndZ=0
    g5: LineSegment StartX=59 StartY=11.7 StartZ=0 EndX=59 EndY=21.4 EndZ=0
    g6: LineSegment StartX=59 StartY=21.4 StartZ=0 EndX=59 EndY=31.1 EndZ=0
    g7: LineSegment StartX=59 StartY=31.1 StartZ=0 EndX=59 EndY=40.8 EndZ=0
    g8: LineSegment StartX=59 StartY=40.8 StartZ=0 EndX=59 EndY=50.5 EndZ=0
    g9: LineSegment StartX=59 StartY=50.5 StartZ=0 EndX=59 EndY=60.2 EndZ=0
    g10: LineSegment StartX=59 StartY=60.2 StartZ=0 EndX=59 EndY=69.9 EndZ=0
    g11: LineSegment StartX=59 StartY=69.9 StartZ=0 EndX=59 EndY=79.6 EndZ=0
    g12: LineSegment StartX=59 StartY=79.6 StartZ=0 EndX=59 EndY=89.3 EndZ=0
    g13: LineSegment StartX=59 StartY=89.3 StartZ=0 EndX=59 EndY=99 EndZ=0
    g14: LineSegment StartX=59 StartY=2 StartZ=0 EndX=2 EndY=2 EndZ=0
    g15: LineSegment StartX=2 StartY=2 StartZ=0 EndX=2 EndY=9.7 EndZ=0
    g16: LineSegment StartX=2 StartY=9.7 StartZ=0 EndX=59 EndY=9.7 EndZ=0
    g17: LineSegment StartX=59 StartY=9.7 StartZ=0 EndX=59 EndY=2 EndZ=0
    g18: LineSegment StartX=59 StartY=11.7 StartZ=0 EndX=2 EndY=11.7 EndZ=0
    g19: LineSegment StartX=2 StartY=11.7 StartZ=0 EndX=2 EndY=19.4 EndZ=0
    g20: LineSegment StartX=2 StartY=19.4 StartZ=0 EndX=59 EndY=19.4 EndZ=0
    g21: LineSegment StartX=59 StartY=19.4 StartZ=0 EndX=59 EndY=11.7 EndZ=0
    g22: LineSegment StartX=59 StartY=21.4 StartZ=0 EndX=2 EndY=21.4 EndZ=0
    g23: LineSegment StartX=2 StartY=21.4 StartZ=0 EndX=2 EndY=29.1 EndZ=0
    g24: LineSegment StartX=2 StartY=29.1 StartZ=0 EndX=59 EndY=29.1 EndZ=0
    g25: LineSegment StartX=59 StartY=29.1 StartZ=0 EndX=59 EndY=21.4 EndZ=0
    g26: LineSegment StartX=59 StartY=31.1 StartZ=0 EndX=2 EndY=31.1 EndZ=0
    g27: LineSegment StartX=2 StartY=31.1 StartZ=0 EndX=2 EndY=38.8 EndZ=0
    g28: LineSegment StartX=2 StartY=38.8 StartZ=0 EndX=59 EndY=38.8 EndZ=0
    g29: LineSegment StartX=59 StartY=38.8 StartZ=0 EndX=59 EndY=31.1 EndZ=0
    g30: LineSegment StartX=59 StartY=40.8 StartZ=0 EndX=2 EndY=40.8 EndZ=0
    g31: LineSegment StartX=2 StartY=40.8 StartZ=0 EndX=2 EndY=48.5 EndZ=0
    g32: LineSegment StartX=2 StartY=48.5 StartZ=0 EndX=59 EndY=48.5 EndZ=0
    g33: LineSegment StartX=59 StartY=48.5 StartZ=0 EndX=59 EndY=40.8 EndZ=0
    g34: LineSegment StartX=59 StartY=50.5 StartZ=0 EndX=2 EndY=50.5 EndZ=0
    g35: LineSegment StartX=2 StartY=50.5 StartZ=0 EndX=2 EndY=58.2 EndZ=0
    g36: LineSegment StartX=2 StartY=58.2 StartZ=0 EndX=59 EndY=58.2 EndZ=0
    g37: LineSegment StartX=59 StartY=58.2 StartZ=0 EndX=59 EndY=50.5 EndZ=0
    g38: LineSegment StartX=59 StartY=60.2 StartZ=0 EndX=2 EndY=60.2 EndZ=0
    g39: LineSegment StartX=2 StartY=60.2 StartZ=0 EndX=2 EndY=67.9 EndZ=0
    g40: LineSegment StartX=2 StartY=67.9 StartZ=0 EndX=59 EndY=67.9 EndZ=0
    g41: LineSegment StartX=59 StartY=67.9 StartZ=0 EndX=59 EndY=60.2 EndZ=0
    g42: LineSegment StartX=59 StartY=69.9 StartZ=0 EndX=2 EndY=69.9 EndZ=0
    g43: LineSegment StartX=2 StartY=69.9 StartZ=0 EndX=2 EndY=77.6 EndZ=0
    g44: LineSegment StartX=2 StartY=77.6 StartZ=0 EndX=59 EndY=77.6 EndZ=0
    g45: LineSegment StartX=59 StartY=77.6 StartZ=0 EndX=59 EndY=69.9 EndZ=0
    g46: LineSegment StartX=59 StartY=79.6 StartZ=0 EndX=2 EndY=79.6 EndZ=0
    g47: LineSegment StartX=2 StartY=79.6 StartZ=0 EndX=2 EndY=87.3 EndZ=0
    g48: LineSegment StartX=2 StartY=87.3 StartZ=0 EndX=59 EndY=87.3 EndZ=0
    g49: LineSegment StartX=59 StartY=87.3 StartZ=0 EndX=59 EndY=79.6 EndZ=0
    g50: LineSegment StartX=59 StartY=89.3 StartZ=0 EndX=2 EndY=89.3 EndZ=0
    g51: LineSegment StartX=2 StartY=89.3 StartZ=0 EndX=2 EndY=97 EndZ=0
    g52: LineSegment StartX=2 StartY=97 StartZ=0 EndX=59 EndY=97 EndZ=0
    g53: LineSegment StartX=59 StartY=97 StartZ=0 EndX=59 EndY=89.3 EndZ=0
  constraints (149):
    c: Coincident(g0,g1)
    c: Coincident(g1,g2)
    c: Coincident(g2,g3)
    c: Coincident(g3,g0)
    c: Horizontal(g2)
    c: Vertical(g1)
    c: Vertical(g3)
    c: Coincident(g0,g-3)
    c: Coincident(g-3,g0)
    c: Coincident(g4,g-4)
    c: PointOnObject(g4,g-6)
    c: Vertical(g4)
    c: Coincident(g5,g4)
    c: Vertical(g5)
    c: Coincident(g6,g5)
    c: Vertical(g6)
    c: Coincident(g7,g6)
    c: Vertical(g7)
    c: Coincident(g8,g7)
    c: Vertical(g8)
    c: Coincident(g9,g8)
    c: Vertical(g9)
    c: Coincident(g10,g9)
    c: Vertical(g10)
    c: Coincident(g11,g10)
    c: Vertical(g11)
    c: Coincident(g12,g11)
    c: Vertical(g12)
    c: Coincident(g13,g12)
    c: PointOnObject(g13,g2)
    c: Vertical(g13)
    c: Equal(g13,g12)
    c: Equal(g12,g11)
    c: Equal(g10,g9)
    c: Equal(g8,g7)
    c: Equal(g7,g6)
    c: Equal(g6,g5)
    c: Equal(g5,g4)
    c: Equal(g9,g8)
    c: Equal(g11,g10)
    c: Coincident(g14,g15)
    c: Coincident(g15,g16)
    c: Coincident(g16,g17)
    c: Coincident(g17,g14)
    c: Horizontal(g14)
    c: Horizontal(g16)
    c: Vertical(g15)
    c: Vertical(g17)
    c: Coincident(g14,g4)
    c: Coincident(g15,g-5)
    c: Coincident(g18,g19)
    c: Coincident(g19,g20)
    c: Coincident(g20,g21)
    c: Coincident(g21,g18)
    c: Horizontal(g18)
    c: Horizontal(g20)
    c: Vertical(g19)
    c: Vertical(g21)
    c: Coincident(g18,g4)
    c: Coincident(g22,g23)
    c: Coincident(g23,g24)
    c: Coincident(g24,g25)
    c: Coincident(g25,g22)
    c: Horizontal(g22)
    c: Horizontal(g24)
    c: Vertical(g23)
    c: Vertical(g25)
    c: Coincident(g22,g5)
    c: Coincident(g26,g27)
    c: Coincident(g27,g28)
    c: Coincident(g28,g29)
    c: Coincident(g29,g26)
    c: Horizontal(g26)
    c: Horizontal(g28)
    c: Vertical(g27)
    c: Vertical(g29)
    c: Coincident(g26,g6)
    c: Coincident(g30,g31)
    c: Coincident(g31,g32)
    c: Coincident(g32,g33)
    c: Coincident(g33,g30)
    c: Horizontal(g30)
    c: Horizontal(g32)
    c: Vertical(g31)
    c: Vertical(g33)
    c: Coincident(g30,g7)
    c: Coincident(g34,g35)
    c: Coincident(g35,g36)
    c: Coincident(g36,g37)
    c: Coincident(g37,g34)
    c: Horizontal(g34)
    c: Horizontal(g36)
    c: Vertical(g35)
    c: Vertical(g37)
    c: Coincident(g34,g8)
    c: Coincident(g38,g39)
    c: Coincident(g39,g40)
    c: Coincident(g40,g41)
    c: Coincident(g41,g38)
    c: Horizontal(g38)
    c: Horizontal(g40)
    c: Vertical(g39)
    c: Vertical(g41)
    c: Coincident(g38,g9)
    c: Coincident(g42,g43)
    c: Coincident(g43,g44)
    c: Coincident(g44,g45)
    c: Coincident(g45,g42)
    c: Horizontal(g42)
    c: Horizontal(g44)
    c: Vertical(g43)
    c: Vertical(g45)
    c: Coincident(g42,g10)
    c: Coincident(g46,g47)
    c: Coincident(g47,g48)
    c: Coincident(g48,g49)
    c: Coincident(g49,g46)
    c: Horizontal(g46)
    c: Horizontal(g48)
    c: Vertical(g47)
    c: Vertical(g49)
    c: Coincident(g46,g11)
    c: Coincident(g50,g51)
    c: Coincident(g51,g52)
    c: Coincident(g52,g53)
    c: Coincident(g53,g50)
    c: Horizontal(g50)
    c: Horizontal(g52)
    c: Vertical(g51)
    c: Vertical(g53)
    c: Coincident(g50,g12)
    c: Equal(g50,g48)
    c: Equal(g46,g44)
    c: Equal(g42,g40)
    c: Equal(g38,g36)
    c: Equal(g34,g32)
    c: Equal(g30,g28)
    c: Equal(g26,g24)
    c: Equal(g22,g20)
    c: Equal(g18,g16)
    c: Equal(g15,g19)
    c: Equal(g19,g23)
    c: Equal(g23,g27)
    c: Equal(g27,g31)
    c: Equal(g31,g35)
    c: Equal(g35,g39)
    c: Equal(g39,g43)
    c: Equal(g43,g47)
    c: Equal(g47,g51)
FEATURE [PartDesign::Pad] Pad017
  BaseFeature = -> Pad010
  Direction = (0,0,1)
  Length = 10
  Length2 = 10
  Profile = -> Sketch018
  ReferenceAxis = -> Sketch018 [N_Axis]
  Refine = true
  Type = 3
  UpToFace = -> Pad010 [Face6]
FEATURE [PartDesign::Chamfer] Chamfer005
  Angle = 45
  Base = -> Pad017 [Face46,Face45,Face44,Face47,Face48,Face43,Face49,Face51,Face50,Face42]
  BaseFeature = -> Pad017
  ChamferType = 1
  FlipDirection = false
  Size = 0.25
  Size2 = 3.49
  SupportTransform = false
  UseAllEdges = false
FEATURE [PartDesign::Chamfer] Chamfer006
  Angle = 45
  Base = -> Pad016 [Face42,Face41,Face43,Face40,Face39,Face44,Face46,Face45,Face38]
  BaseFeature = -> Pad016
  ChamferType = 1
  FlipDirection = false
  Size = 0.25
  Size2 = 3.49
  SupportTransform = false
  UseAllEdges = false
FEATURE [PartDesign::Chamfer] Chamfer007
  Angle = 45
  Base = -> Pad008 [Face41,Face40,Face39,Face38,Face37,Face35,Face34,Face36]
  BaseFeature = -> Pad008
  ChamferType = 1
  FlipDirection = false
  Size = 0.25
  Size2 = 3.49
  SupportTransform = false
  UseAllEdges = false
FEATURE [PartDesign::Chamfer] Chamfer008
  Angle = 45
  Base = -> Pad015 [Face32,Face33,Face31,Face34,Face35,Face36,Face30]
  BaseFeature = -> Pad015
  ChamferType = 1
  FlipDirection = false
  Size = 0.25
  Size2 = 3.49
  SupportTransform = false
  UseAllEdges = false
FEATURE [PartDesign::Chamfer] Chamfer009
  Angle = 45
  Base = -> Pad014 [Face28,Face27,Face29,Face31,Face26,Face30]
  BaseFeature = -> Pad014
  ChamferType = 1
  FlipDirection = false
  Placement = pos=(0,175,0) rot=(0,0,1;0rad)
  Size = 0.25
  Size2 = 3.49
  SupportTransform = false
  UseAllEdges = false
FEATURE [PartDesign::Chamfer] Chamfer010
  Angle = 45
  Base = -> Chamfer004 [Face51,Face50,Face49,Face48,Face9]
  BaseFeature = -> Chamfer004
  ChamferType = 1
  FlipDirection = false
  Size = 0.25
  Size2 = 3.49
  SupportTransform = false
  UseAllEdges = false
FEATURE [PartDesign::Fillet] Fillet001
  Base = -> Chamfer002 [Face23,Face10,Face13,Face11,Face12]
  BaseFeature = -> Chamfer002
  Radius = 0.5
  SupportTransform = false
  UseAllEdges = false
FEATURE [PartDesign::Fillet] Fillet002
  Base = -> Chamfer003 [Face27,Face11,Face12,Face13,Face10]
  BaseFeature = -> Chamfer003
  Radius = 0.5
  SupportTransform = false
  UseAllEdges = false
FEATURE [PartDesign::Fillet] Fillet003
  Base = -> Chamfer010 [Face35,Face18,Face15,Face17,Face16]
  BaseFeature = -> Chamfer010
  Radius = 0.5
  SupportTransform = false
  UseAllEdges = false
FEATURE [PartDesign::Fillet] Fillet004
  Base = -> Chamfer009 [Face35,Face11,Face12,Face13,Face10]
  BaseFeature = -> Chamfer009
  Placement = pos=(0,175,0) rot=(0,0,1;0rad)
  Radius = 0.5
  SupportTransform = false
  UseAllEdges = false
FEATURE [PartDesign::Fillet] Fillet005
  Base = -> Chamfer008 [Face39,Face13,Face10,Face12,Face11]
  BaseFeature = -> Chamfer008
  Radius = 0.5
  SupportTransform = false
  UseAllEdges = false
FEATURE [PartDesign::Fillet] Fillet006
  Base = -> Chamfer007 [Face43,Face11,Face12,Face10,Face13]
  BaseFeature = -> Chamfer007
  Radius = 0.5
  SupportTransform = false
  UseAllEdges = false
FEATURE [PartDesign::Fillet] Fillet007
  Base = -> Chamfer006 [Face47,Face10,Face13,Face12,Face11]
  BaseFeature = -> Chamfer006
  Radius = 0.5
  SupportTransform = false
  UseAllEdges = false
FEATURE [PartDesign::Fillet] Fillet008
  Base = -> Chamfer005 [Face51,Face11,Face12,Face13,Face10]
  BaseFeature = -> Chamfer005
  Radius = 0.5
  SupportTransform = false
  UseAllEdges = false
FEATURE [Sketcher::SketchObject] Sketch019  label="16 Bit VS"
  FullyConstrained = false
  Placement = pos=(8.14,0,-4) rot=(1,0,0;3.14159rad)
  sketch-geometry (860):
    g0: BSplineCurve PolesCount=2 KnotsCount=2 Degree=1 IsPeriodic=0
    g1: BSplineCurve PolesCount=2 KnotsCount=2 Degree=1 IsPeriodic=0
    g2: BSplineCurve PolesCount=2 KnotsCount=2 Degree=1 IsPeriodic=0
    g3: BSplineCurve PolesCount=2 KnotsCount=2 Degree=1 IsPeriodic=0
    g4: BSplineCurve PolesCount=2 KnotsCount=2 Degree=1 IsPeriodic=0
    g5: BSplineCurve PolesCount=2 KnotsCount=2 Degree=1 IsPeriodic=0
    g6: BSplineCurve PolesCount=2 KnotsCount=2 Degree=1 IsPeriodic=0
    g7: BSplineCurve PolesCount=2 KnotsCount=2 Degree=1 IsPeriodic=0
    g8: BSplineCurve PolesCount=2 KnotsCount=2 Degree=1 IsPeriodic=0
    g9: BSplineCurve PolesCount=2 KnotsCount=2 Degree=1 IsPeriodic=0
    g10: BSplineCurve PolesCount=2 KnotsCount=2 Degree=1 IsPeriodic=0
    g11: BSplineCurve PolesCount=2 KnotsCount=2 Degree=1 IsPeriodic=0
    g12: BSplineCurve PolesCount=2 KnotsCount=2 Degree=1 IsPeriodic=0
    g13: BSplineCurve PolesCount=2 KnotsCount=2 Degree=1 IsPeriodic=0
    g14: BSplineCurve PolesCount=2 KnotsCount=2 Degree=1 IsPeriodic=0
    g15: BSplineCurve PolesCount=2 KnotsCount=2 Degree=1 IsPeriodic=0
    g16: BSplineCurve PolesCount=2 KnotsCount=2 Degree=1 IsPeriodic=0
    g17: BSplineCurve PolesCount=2 KnotsCount=2 Degree=1 IsPeriodic=0
    g18: BSplineCurve PolesCount=2 KnotsCount=2 Degree=1 IsPeriodic=0
    g19: BSplineCurve PolesCount=2 KnotsCount=2 Degree=1 IsPeriodic=0
    g20: BSplineCurve PolesCount=2 KnotsCount=2 Degree=1 IsPeriodic=0
    g21: BSplineCurve PolesCount=2 KnotsCount=2 Degree=1 IsPeriodic=0
    g22: BSplineCurve PolesCount=2 KnotsCount=2 Degree=1 IsPeriodic=0
    g23: BSplineCurve PolesCount=2 KnotsCount=2 Degree=1 IsPeriodic=0
    g24: BSplineCurve PolesCount=2 KnotsCount=2 Degree=1 IsPeriodic=0
    g25: BSplineCurve PolesCount=2 KnotsCount=2 Degree=1 IsPeriodic=0
    g26: BSplineCurve PolesCount=2 KnotsCount=2 Degree=1 IsPeriodic=0
    g27: BSplineCurve PolesCount=2 KnotsCount=2 Degree=1 IsPeriodic=0
    g28: BSplineCurve PolesCount=2 KnotsCount=2 Degree=1 IsPeriodic=0
    g29: BSplineCurve PolesCount=2 KnotsCount=2 Degree=1 IsPeriodic=0
    g30: BSplineCurve PolesCount=2 KnotsCount=2 Degree=1 IsPeriodic=0
    g31: BSplineCurve PolesCount=2 KnotsCount=2 Degree=1 IsPeriodic=0
    g32: BSplineCurve PolesCount=2 KnotsCount=2 Degree=1 IsPeriodic=0
    g33: BSplineCurve PolesCount=2 KnotsCount=2 Degree=1 IsPeriodic=0
    g34: BSplineCurve PolesCount=2 KnotsCount=2 Degree=1 IsPeriodic=0
    g35: BSplineCurve PolesCount=2 KnotsCount=2 Degree=1 IsPeriodic=0
    g36: BSplineCurve PolesCount=2 KnotsCount=2 Degree=1 IsPeriodic=0
    g37: BSplineCurve PolesCount=2 KnotsCount=2 Degree=1 IsPeriodic=0
    g38: BSplineCurve PolesCount=2 KnotsCount=2 Degree=1 IsPeriodic=0
    g39: BSplineCurve PolesCount=2 KnotsCount=2 Degree=1 IsPeriodic=0
    g40: BSplineCurve PolesCount=2 KnotsCount=2 Degree=1 IsPeriodic=0
    g41: BSplineCurve PolesCount=2 KnotsCount=2 Degree=1 IsPeriodic=0
    g42: BSplineCurve PolesCount=2 KnotsCount=2 Degree=1 IsPeriodic=0
    g43: BSplineCurve PolesCount=2 KnotsCount=2 Degree=1 IsPeriodic=0
    g44: BSplineCurve PolesCount=2 KnotsCount=2 Degree=1 IsPeriodic=0
    g45: BSplineCurve PolesCount=2 KnotsCount=2 Degree=1 IsPeriodic=0
    g46: BSplineCurve PolesCount=2 KnotsCount=2 Degree=1 IsPeriodic=0
    g47: BSplineCurve PolesCount=2 KnotsCount=2 Degree=1 IsPeriodic=0
    g48: BSplineCurve PolesCount=2 KnotsCount=2 Degree=1 IsPeriodic=0
    g49: BSplineCurve PolesCount=2 KnotsCount=2 Degree=1 IsPeriodic=0
    g50: BSplineCurve PolesCount=2 KnotsCount=2 Degree=1 IsPeriodic=0
    g51: BSplineCurve PolesCount=2 KnotsCount=2 Degree=1 IsPeriodic=0
    g52: BSplineCurve PolesCount=2 KnotsCount=2 Degree=1 IsPeriodic=0
    g53: BSplineCurve PolesCount=2 KnotsCount=2 Degree=1 IsPeriodic=0
    g54: BSplineCurve PolesCount=2 KnotsCount=2 Degree=1 IsPeriodic=0
    g55: BSplineCurve PolesCount=2 KnotsCount=2 Degree=1 IsPeriodic=0
    g56: BSplineCurve PolesCount=2 KnotsCount=2 Degree=1 IsPeriodic=0
    g57: BSplineCurve PolesCount=2 KnotsCount=2 Degree=1 IsPeriodic=0
    g58: BSplineCurve PolesCount=2 KnotsCount=2 Degree=1 IsPeriodic=0
    g59: BSplineCurve PolesCount=2 KnotsCount=2 Degree=1 IsPeriodic=0
    g60: BSplineCurve PolesCount=2 KnotsCount=2 Degree=1 IsPeriodic=0
    g61: BSplineCurve PolesCount=2 KnotsCount=2 Degree=1 IsPeriodic=0
    g62: BSplineCurve PolesCount=2 KnotsCount=2 Degree=1 IsPeriodic=0
    g63: BSplineCurve PolesCount=2 KnotsCount=2 Degree=1 IsPeriodic=0
    g64: BSplineCurve PolesCount=2 KnotsCount=2 Degree=1 IsPeriodic=0
    g65: BSplineCurve PolesCount=2 KnotsCount=2 Degree=1 IsPeriodic=0
    g66: BSplineCurve PolesCount=2 KnotsCount=2 Degree=1 IsPeriodic=0
    g67: BSplineCurve PolesCount=2 KnotsCount=2 Degree=1 IsPeriodic=0
    g68: BSplineCurve PolesCount=2 KnotsCount=2 Degree=1 IsPeriodic=0
    g69: BSplineCurve PolesCount=2 KnotsCount=2 Degree=1 IsPeriodic=0
    g70: BSplineCurve PolesCount=2 KnotsCount=2 Degree=1 IsPeriodic=0
    g71: BSplineCurve PolesCount=2 KnotsCount=2 Degree=1 IsPeriodic=0
    g72: BSplineCurve PolesCount=2 KnotsCount=2 Degree=1 IsPeriodic=0
    g73: BSplineCurve PolesCount=2 KnotsCount=2 Degree=1 IsPeriodic=0
    g74: BSplineCurve PolesCount=2 KnotsCount=2 Degree=1 IsPeriodic=0
    g75: BSplineCurve PolesCount=2 KnotsCount=2 Degree=1 IsPeriodic=0
    g76: BSplineCurve PolesCount=2 KnotsCount=2 Degree=1 IsPeriodic=0
    g77: BSplineCurve PolesCount=2 KnotsCount=2 Degree=1 IsPeriodic=0
    g78: BSplineCurve PolesCount=2 KnotsCount=2 Degree=1 IsPeriodic=0
    g79: BSplineCurve PolesCount=2 KnotsCount=2 Degree=1 IsPeriodic=0
    g80: BSplineCurve PolesCount=2 KnotsCount=2 Degree=1 IsPeriodic=0
    g81: BSplineCurve PolesCount=2 KnotsCount=2 Degree=1 IsPeriodic=0
    g82: BSplineCurve PolesCount=2 KnotsCount=2 Degree=1 IsPeriodic=0
    g83: BSplineCurve PolesCount=2 KnotsCount=2 Degree=1 IsPeriodic=0
    g84: BSplineCurve PolesCount=2 KnotsCount=2 Degree=1 IsPeriodic=0
    g85: BSplineCurve PolesCount=2 KnotsCount=2 Degree=1 IsPeriodic=0
    g86: BSplineCurve PolesCount=2 KnotsCount=2 Degree=1 IsPeriodic=0
    g87: BSplineCurve PolesCount=2 KnotsCount=2 Degree=1 IsPeriodic=0
    g88: BSplineCurve PolesCount=2 KnotsCount=2 Degree=1 IsPeriodic=0
    g89: BSplineCurve PolesCount=2 KnotsCount=2 Degree=1 IsPeriodic=0
    g90: BSplineCurve PolesCount=2 KnotsCount=2 Degree=1 IsPeriodic=0
    g91: BSplineCurve PolesCount=2 KnotsCount=2 Degree=1 IsPeriodic=0
    g92: BSplineCurve PolesCount=2 KnotsCount=2 Degree=1 IsPeriodic=0
    g93: BSplineCurve PolesCount=2 KnotsCount=2 Degree=1 IsPeriodic=0
    g94: BSplineCurve PolesCount=2 KnotsCount=2 Degree=1 IsPeriodic=0
    g95: BSplineCurve PolesCount=2 KnotsCount=2 Degree=1 IsPeriodic=0
    g96: BSplineCurve PolesCount=2 KnotsCount=2 Degree=1 IsPeriodic=0
    g97: BSplineCurve PolesCount=2 KnotsCount=2 Degree=1 IsPeriodic=0
    g98: BSplineCurve PolesCount=2 KnotsCount=2 Degree=1 IsPeriodic=0
    g99: BSplineCurve PolesCount=2 KnotsCount=2 Degree=1 IsPeriodic=0
    g100: BSplineCurve PolesCount=2 KnotsCount=2 Degree=1 IsPeriodic=0
    g101: BSplineCurve PolesCount=2 KnotsCount=2 Degree=1 IsPeriodic=0
    g102: BSplineCurve PolesCount=2 KnotsCount=2 Degree=1 IsPeriodic=0
    g103: BSplineCurve PolesCount=2 KnotsCount=2 Degree=1 IsPeriodic=0
    g104: BSplineCurve PolesCount=2 KnotsCount=2 Degree=1 IsPeriodic=0
    g105: BSplineCurve PolesCount=2 KnotsCount=2 Degree=1 IsPeriodic=0
    g106: BSplineCurve PolesCount=2 KnotsCount=2 Degree=1 IsPeriodic=0
    g107: BSplineCurve PolesCount=2 KnotsCount=2 Degree=1 IsPeriodic=0
    g108: BSplineCurve PolesCount=2 KnotsCount=2 Degree=1 IsPeriodic=0
    g109: BSplineCurve PolesCount=2 KnotsCount=2 Degree=1 IsPeriodic=0
    g110: BSplineCurve PolesCount=2 KnotsCount=2 Degree=1 IsPeriodic=0
    g111: BSplineCurve PolesCount=2 KnotsCount=2 Degree=1 IsPeriodic=0
    g112: BSplineCurve PolesCount=2 KnotsCount=2 Degree=1 IsPeriodic=0
    g113: BSplineCurve PolesCount=2 KnotsCount=2 Degree=1 IsPeriodic=0
    g114: BSplineCurve PolesCount=2 KnotsCount=2 Degree=1 IsPeriodic=0
    g115: BSplineCurve PolesCount=2 KnotsCount=2 Degree=1 IsPeriodic=0
    g116: BSplineCurve PolesCount=2 KnotsCount=2 Degree=1 IsPeriodic=0
    g117: BSplineCurve PolesCount=2 KnotsCount=2 Degree=1 IsPeriodic=0
    g118: BSplineCurve PolesCount=2 KnotsCount=2 Degree=1 IsPeriodic=0
    g119: BSplineCurve PolesCount=2 KnotsCount=2 Degree=1 IsPeriodic=0
    g120: BSplineCurve PolesCount=2 KnotsCount=2 Degree=1 IsPeriodic=0
    g121: BSplineCurve PolesCount=2 KnotsCount=2 Degree=1 IsPeriodic=0
    g122: BSplineCurve PolesCount=2 KnotsCount=2 Degree=1 IsPeriodic=0
    g123: BSplineCurve PolesCount=2 KnotsCount=2 Degree=1 IsPeriodic=0
    g124: BSplineCurve PolesCount=2 KnotsCount=2 Degree=1 IsPeriodic=0
    g125: BSplineCurve PolesCount=2 KnotsCount=2 Degree=1 IsPeriodic=0
    g126: BSplineCurve PolesCount=2 KnotsCount=2 Degree=1 IsPeriodic=0
    g127: BSplineCurve PolesCount=2 KnotsCount=2 Degree=1 IsPeriodic=0
    g128: BSplineCurve PolesCount=2 KnotsCount=2 Degree=1 IsPeriodic=0
    g129: BSplineCurve PolesCount=2 KnotsCount=2 Degree=1 IsPeriodic=0
    g130: BSplineCurve PolesCount=2 KnotsCount=2 Degree=1 IsPeriodic=0
    g131: BSplineCurve PolesCount=2 KnotsCount=2 Degree=1 IsPeriodic=0
    g132: BSplineCurve PolesCount=2 KnotsCount=2 Degree=1 IsPeriodic=0
    g133: BSplineCurve PolesCount=2 KnotsCount=2 Degree=1 IsPeriodic=0
    g134: BSplineCurve PolesCount=2 KnotsCount=2 Degree=1 IsPeriodic=0
    g135: BSplineCurve PolesCount=2 KnotsCount=2 Degree=1 IsPeriodic=0
    g136: BSplineCurve PolesCount=2 KnotsCount=2 Degree=1 IsPeriodic=0
    g137: BSplineCurve PolesCount=2 KnotsCount=2 Degree=1 IsPeriodic=0
    g138: BSplineCurve PolesCount=2 KnotsCount=2 Degree=1 IsPeriodic=0
    g139: BSplineCurve PolesCount=2 KnotsCount=2 Degree=1 IsPeriodic=0
    g140: BSplineCurve PolesCount=2 KnotsCount=2 Degree=1 IsPeriodic=0
    g141: BSplineCurve PolesCount=2 KnotsCount=2 Degree=1 IsPeriodic=0
    g142: BSplineCurve PolesCount=2 KnotsCount=2 Degree=1 IsPeriodic=0
    g143: BSplineCurve PolesCount=2 KnotsCount=2 Degree=1 IsPeriodic=0
    g144: BSplineCurve PolesCount=2 KnotsCount=2 Degree=1 IsPeriodic=0
    g145: BSplineCurve PolesCount=2 KnotsCount=2 Degree=1 IsPeriodic=0
    g146: BSplineCurve PolesCount=2 KnotsCount=2 Degree=1 IsPeriodic=0
    g147: BSplineCurve PolesCount=2 KnotsCount=2 Degree=1 IsPeriodic=0
    g148: BSplineCurve PolesCount=2 KnotsCount=2 Degree=1 IsPeriodic=0
    g149: BSplineCurve PolesCount=2 KnotsCount=2 Degree=1 IsPeriodic=0
    g150: BSplineCurve PolesCount=2 KnotsCount=2 Degree=1 IsPeriodic=0
    g151: BSplineCurve PolesCount=2 KnotsCount=2 Degree=1 IsPeriodic=0
    g152: BSplineCurve PolesCount=2 KnotsCount=2 Degree=1 IsPeriodic=0
    g153: BSplineCurve PolesCount=2 KnotsCount=2 Degree=1 IsPeriodic=0
    g154: BSplineCurve PolesCount=2 KnotsCount=2 Degree=1 IsPeriodic=0
    g155: BSplineCurve PolesCount=2 KnotsCount=2 Degree=1 IsPeriodic=0
    g156: BSplineCurve PolesCount=2 KnotsCount=2 Degree=1 IsPeriodic=0
    g157: BSplineCurve PolesCount=2 KnotsCount=2 Degree=1 IsPeriodic=0
    g158: BSplineCurve PolesCount=2 KnotsCount=2 Degree=1 IsPeriodic=0
    g159: BSplineCurve PolesCount=2 KnotsCount=2 Degree=1 IsPeriodic=0
    g160: BSplineCurve PolesCount=2 KnotsCount=2 Degree=1 IsPeriodic=0
    g161: BSplineCurve PolesCount=2 KnotsCount=2 Degree=1 IsPeriodic=0
    g162: BSplineCurve PolesCount=2 KnotsCount=2 Degree=1 IsPeriodic=0
    g163: BSplineCurve PolesCount=2 KnotsCount=2 Degree=1 IsPeriodic=0
    g164: BSplineCurve PolesCount=2 KnotsCount=2 Degree=1 IsPeriodic=0
    g165: BSplineCurve PolesCount=2 KnotsCount=2 Degree=1 IsPeriodic=0
    g166: BSplineCurve PolesCount=2 KnotsCount=2 Degree=1 IsPeriodic=0
    g167: BSplineCurve PolesCount=2 KnotsCount=2 Degree=1 IsPeriodic=0
    g168: BSplineCurve PolesCount=2 KnotsCount=2 Degree=1 IsPeriodic=0
    g169: BSplineCurve PolesCount=2 KnotsCount=2 Degree=1 IsPeriodic=0
    g170: BSplineCurve PolesCount=2 KnotsCount=2 Degree=1 IsPeriodic=0
    g171: BSplineCurve PolesCount=2 KnotsCount=2 Degree=1 IsPeriodic=0
    g172: BSplineCurve PolesCount=2 KnotsCount=2 Degree=1 IsPeriodic=0
    g173: BSplineCurve PolesCount=2 KnotsCount=2 Degree=1 IsPeriodic=0
    g174: BSplineCurve PolesCount=2 KnotsCount=2 Degree=1 IsPeriodic=0
    g175: BSplineCurve PolesCount=2 KnotsCount=2 Degree=1 IsPeriodic=0
    g176: BSplineCurve PolesCount=2 KnotsCount=2 Degree=1 IsPeriodic=0
    g177: BSplineCurve PolesCount=2 KnotsCount=2 Degree=1 IsPeriodic=0
    g178: BSplineCurve PolesCount=2 KnotsCount=2 Degree=1 IsPeriodic=0
    g179: BSplineCurve PolesCount=2 KnotsCount=2 Degree=1 IsPeriodic=0
    g180: BSplineCurve PolesCount=2 KnotsCount=2 Degree=1 IsPeriodic=0
    g181: BSplineCurve PolesCount=2 KnotsCount=2 Degree=1 IsPeriodic=0
    g182: BSplineCurve PolesCount=2 KnotsCount=2 Degree=1 IsPeriodic=0
    g183: BSplineCurve PolesCount=2 KnotsCount=2 Degree=1 IsPeriodic=0
    g184: BSplineCurve PolesCount=2 KnotsCount=2 Degree=1 IsPeriodic=0
    g185: BSplineCurve PolesCount=2 KnotsCount=2 Degree=1 IsPeriodic=0
    g186: BSplineCurve PolesCount=2 KnotsCount=2 Degree=1 IsPeriodic=0
    g187: BSplineCurve PolesCount=2 KnotsCount=2 Degree=1 IsPeriodic=0
    g188: BSplineCurve PolesCount=2 KnotsCount=2 Degree=1 IsPeriodic=0
    g189: BSplineCurve PolesCount=2 KnotsCount=2 Degree=1 IsPeriodic=0
    g190: BSplineCurve PolesCount=2 KnotsCount=2 Degree=1 IsPeriodic=0
    g191: BSplineCurve PolesCount=2 KnotsCount=2 Degree=1 IsPeriodic=0
    g192: BSplineCurve PolesCount=2 KnotsCount=2 Degree=1 IsPeriodic=0
    g193: BSplineCurve PolesCount=2 KnotsCount=2 Degree=1 IsPeriodic=0
    g194: BSplineCurve PolesCount=2 KnotsCount=2 Degree=1 IsPeriodic=0
    g195: BSplineCurve PolesCount=2 KnotsCount=2 Degree=1 IsPeriodic=0
    g196: BSplineCurve PolesCount=2 KnotsCount=2 Degree=1 IsPeriodic=0
    g197: BSplineCurve PolesCount=2 KnotsCount=2 Degree=1 IsPeriodic=0
    g198: BSplineCurve PolesCount=2 KnotsCount=2 Degree=1 IsPeriodic=0
    g199: BSplineCurve PolesCount=2 KnotsCount=2 Degree=1 IsPeriodic=0
    g200: BSplineCurve PolesCount=2 KnotsCount=2 Degree=1 IsPeriodic=0
    g201: BSplineCurve PolesCount=2 KnotsCount=2 Degree=1 IsPeriodic=0
    g202: BSplineCurve PolesCount=2 KnotsCount=2 Degree=1 IsPeriodic=0
    g203: BSplineCurve PolesCount=2 KnotsCount=2 Degree=1 IsPeriodic=0
    g204: BSplineCurve PolesCount=2 KnotsCount=2 Degree=1 IsPeriodic=0
    g205: BSplineCurve PolesCount=2 KnotsCount=2 Degree=1 IsPeriodic=0
    g206: BSplineCurve PolesCount=2 KnotsCount=2 Degree=1 IsPeriodic=0
    g207: BSplineCurve PolesCount=2 KnotsCount=2 Degree=1 IsPeriodic=0
    g208: BSplineCurve PolesCount=2 KnotsCount=2 Degree=1 IsPeriodic=0
    g209: BSplineCurve PolesCount=2 KnotsCount=2 Degree=1 IsPeriodic=0
    g210: BSplineCurve PolesCount=2 KnotsCount=2 Degree=1 IsPeriodic=0
    g211: BSplineCurve PolesCount=2 KnotsCount=2 Degree=1 IsPeriodic=0
    g212: BSplineCurve PolesCount=2 KnotsCount=2 Degree=1 IsPeriodic=0
    g213: BSplineCurve PolesCount=2 KnotsCount=2 Degree=1 IsPeriodic=0
    g214: BSplineCurve PolesCount=2 KnotsCount=2 Degree=1 IsPeriodic=0
    g215: BSplineCurve PolesCount=2 KnotsCount=2 Degree=1 IsPeriodic=0
    g216: BSplineCurve PolesCount=2 KnotsCount=2 Degree=1 IsPeriodic=0
    g217: BSplineCurve PolesCount=2 KnotsCount=2 Degree=1 IsPeriodic=0
    g218: BSplineCurve PolesCount=2 KnotsCount=2 Degree=1 IsPeriodic=0
    g219: BSplineCurve PolesCount=2 KnotsCount=2 Degree=1 IsPeriodic=0
    g220: BSplineCurve PolesCount=2 KnotsCount=2 Degree=1 IsPeriodic=0
    g221: BSplineCurve PolesCount=2 KnotsCount=2 Degree=1 IsPeriodic=0
    g222: BSplineCurve PolesCount=2 KnotsCount=2 Degree=1 IsPeriodic=0
    g223: BSplineCurve PolesCount=2 KnotsCount=2 Degree=1 IsPeriodic=0
    g224: BSplineCurve PolesCount=2 KnotsCount=2 Degree=1 IsPeriodic=0
    g225: BSplineCurve PolesCount=2 KnotsCount=2 Degree=1 IsPeriodic=0
    g226: BSplineCurve PolesCount=2 KnotsCount=2 Degree=1 IsPeriodic=0
    g227: BSplineCurve PolesCount=2 KnotsCount=2 Degree=1 IsPeriodic=0
    g228: BSplineCurve PolesCount=2 KnotsCount=2 Degree=1 IsPeriodic=0
    g229: BSplineCurve PolesCount=2 KnotsCount=2 Degree=1 IsPeriodic=0
    g230: BSplineCurve PolesCount=2 KnotsCount=2 Degree=1 IsPeriodic=0
    g231: BSplineCurve PolesCount=2 KnotsCount=2 Degree=1 IsPeriodic=0
    g232: BSplineCurve PolesCount=2 KnotsCount=2 Degree=1 IsPeriodic=0
    g233: BSplineCurve PolesCount=2 KnotsCount=2 Degree=1 IsPeriodic=0
    g234: BSplineCurve PolesCount=2 KnotsCount=2 Degree=1 IsPeriodic=0
    g235: BSplineCurve PolesCount=2 KnotsCount=2 Degree=1 IsPeriodic=0
    g236: BSplineCurve PolesCount=2 KnotsCount=2 Degree=1 IsPeriodic=0
    g237: BSplineCurve PolesCount=2 KnotsCount=2 Degree=1 IsPeriodic=0
    g238: BSplineCurve PolesCount=2 KnotsCount=2 Degree=1 IsPeriodic=0
    g239: BSplineCurve PolesCount=2 KnotsCount=2 Degree=1 IsPeriodic=0
    g240: BSplineCurve PolesCount=2 KnotsCount=2 Degree=1 IsPeriodic=0
    g241: BSplineCurve PolesCount=2 KnotsCount=2 Degree=1 IsPeriodic=0
    g242: BSplineCurve PolesCount=2 KnotsCount=2 Degree=1 IsPeriodic=0
    g243: BSplineCurve PolesCount=2 KnotsCount=2 Degree=1 IsPeriodic=0
    g244: BSplineCurve PolesCount=2 KnotsCount=2 Degree=1 IsPeriodic=0
    g245: BSplineCurve PolesCount=2 KnotsCount=2 Degree=1 IsPeriodic=0
    g246: BSplineCurve PolesCount=2 KnotsCount=2 Degree=1 IsPeriodic=0
    g247: BSplineCurve PolesCount=2 KnotsCount=2 Degree=1 IsPeriodic=0
    g248: BSplineCurve PolesCount=2 KnotsCount=2 Degree=1 IsPeriodic=0
    g249: BSplineCurve PolesCount=2 KnotsCount=2 Degree=1 IsPeriodic=0
    g250: BSplineCurve PolesCount=2 KnotsCount=2 Degree=1 IsPeriodic=0
    g251: BSplineCurve PolesCount=2 KnotsCount=2 Degree=1 IsPeriodic=0
    g252: BSplineCurve PolesCount=2 KnotsCount=2 Degree=1 IsPeriodic=0
    g253: BSplineCurve PolesCount=2 KnotsCount=2 Degree=1 IsPeriodic=0
    g254: BSplineCurve PolesCount=2 KnotsCount=2 Degree=1 IsPeriodic=0
    g255: BSplineCurve PolesCount=2 KnotsCount=2 Degree=1 IsPeriodic=0
    g256: BSplineCurve PolesCount=2 KnotsCount=2 Degree=1 IsPeriodic=0
    g257: BSplineCurve PolesCount=2 KnotsCount=2 Degree=1 IsPeriodic=0
    g258: BSplineCurve PolesCount=2 KnotsCount=2 Degree=1 IsPeriodic=0
    g259: BSplineCurve PolesCount=2 KnotsCount=2 Degree=1 IsPeriodic=0
    g260: BSplineCurve PolesCount=2 KnotsCount=2 Degree=1 IsPeriodic=0
    g261: BSplineCurve PolesCount=2 KnotsCount=2 Degree=1 IsPeriodic=0
    g262: BSplineCurve PolesCount=2 KnotsCount=2 Degree=1 IsPeriodic=0
    g263: BSplineCurve PolesCount=2 KnotsCount=2 Degree=1 IsPeriodic=0
    g264: BSplineCurve PolesCount=2 KnotsCount=2 Degree=1 IsPeriodic=0
    g265: BSplineCurve PolesCount=2 KnotsCount=2 Degree=1 IsPeriodic=0
    g266: BSplineCurve PolesCount=2 KnotsCount=2 Degree=1 IsPeriodic=0
    g267: BSplineCurve PolesCount=2 KnotsCount=2 Degree=1 IsPeriodic=0
    g268: BSplineCurve PolesCount=2 KnotsCount=2 Degree=1 IsPeriodic=0
    g269: BSplineCurve PolesCount=2 KnotsCount=2 Degree=1 IsPeriodic=0
    g270: BSplineCurve PolesCount=2 KnotsCount=2 Degree=1 IsPeriodic=0
    g271: BSplineCurve PolesCount=2 KnotsCount=2 Degree=1 IsPeriodic=0
    g272: BSplineCurve PolesCount=2 KnotsCount=2 Degree=1 IsPeriodic=0
    g273: BSplineCurve PolesCount=2 KnotsCount=2 Degree=1 IsPeriodic=0
    g274: BSplineCurve PolesCount=2 KnotsCount=2 Degree=1 IsPeriodic=0
    g275: BSplineCurve PolesCount=2 KnotsCount=2 Degree=1 IsPeriodic=0
    g276: BSplineCurve PolesCount=2 KnotsCount=2 Degree=1 IsPeriodic=0
    g277: BSplineCurve PolesCount=2 KnotsCount=2 Degree=1 IsPeriodic=0
    g278: BSplineCurve PolesCount=2 KnotsCount=2 Degree=1 IsPeriodic=0
    g279: BSplineCurve PolesCount=2 KnotsCount=2 Degree=1 IsPeriodic=0
    g280: BSplineCurve PolesCount=2 KnotsCount=2 Degree=1 IsPeriodic=0
    g281: BSplineCurve PolesCount=2 KnotsCount=2 Degree=1 IsPeriodic=0
    g282: BSplineCurve PolesCount=2 KnotsCount=2 Degree=1 IsPeriodic=0
    g283: BSplineCurve PolesCount=2 KnotsCount=2 Degree=1 IsPeriodic=0
    g284: BSplineCurve PolesCount=2 KnotsCount=2 Degree=1 IsPeriodic=0
    g285: BSplineCurve PolesCount=2 KnotsCount=2 Degree=1 IsPeriodic=0
    g286: BSplineCurve PolesCount=2 KnotsCount=2 Degree=1 IsPeriodic=0
    g287: BSplineCurve PolesCount=2 KnotsCount=2 Degree=1 IsPeriodic=0
    g288: BSplineCurve PolesCount=2 KnotsCount=2 Degree=1 IsPeriodic=0
    g289: BSplineCurve PolesCount=2 KnotsCount=2 Degree=1 IsPeriodic=0
    g290: BSplineCurve PolesCount=2 KnotsCount=2 Degree=1 IsPeriodic=0
    g291: BSplineCurve PolesCount=2 KnotsCount=2 Degree=1 IsPeriodic=0
    g292: BSplineCurve PolesCount=2 KnotsCount=2 Degree=1 IsPeriodic=0
    g293: BSplineCurve PolesCount=2 KnotsCount=2 Degree=1 IsPeriodic=0
    g294: BSplineCurve PolesCount=2 KnotsCount=2 Degree=1 IsPeriodic=0
    g295: BSplineCurve PolesCount=2 KnotsCount=2 Degree=1 IsPeriodic=0
    g296: BSplineCurve PolesCount=2 KnotsCount=2 Degree=1 IsPeriodic=0
    g297: BSplineCurve PolesCount=2 KnotsCount=2 Degree=1 IsPeriodic=0
    g298: BSplineCurve PolesCount=2 KnotsCount=2 Degree=1 IsPeriodic=0
    g299: BSplineCurve PolesCount=2 KnotsCount=2 Degree=1 IsPeriodic=0
    g300: BSplineCurve PolesCount=2 KnotsCount=2 Degree=1 IsPeriodic=0
    g301: BSplineCurve PolesCount=2 KnotsCount=2 Degree=1 IsPeriodic=0
    g302: BSplineCurve PolesCount=2 KnotsCount=2 Degree=1 IsPeriodic=0
    g303: BSplineCurve PolesCount=2 KnotsCount=2 Degree=1 IsPeriodic=0
    g304: BSplineCurve PolesCount=2 KnotsCount=2 Degree=1 IsPeriodic=0
    g305: BSplineCurve PolesCount=2 KnotsCount=2 Degree=1 IsPeriodic=0
    g306: BSplineCurve PolesCount=2 KnotsCount=2 Degree=1 IsPeriodic=0
    g307: BSplineCurve PolesCount=2 KnotsCount=2 Degree=1 IsPeriodic=0
    g308: BSplineCurve PolesCount=2 KnotsCount=2 Degree=1 IsPeriodic=0
    g309: BSplineCurve PolesCount=2 KnotsCount=2 Degree=1 IsPeriodic=0
    g310: BSplineCurve PolesCount=2 KnotsCount=2 Degree=1 IsPeriodic=0
    g311: BSplineCurve PolesCount=2 KnotsCount=2 Degree=1 IsPeriodic=0
    g312: BSplineCurve PolesCount=2 KnotsCount=2 Degree=1 IsPeriodic=0
    g313: BSplineCurve PolesCount=2 KnotsCount=2 Degree=1 IsPeriodic=0
    g314: BSplineCurve PolesCount=2 KnotsCount=2 Degree=1 IsPeriodic=0
    g315: BSplineCurve PolesCount=2 KnotsCount=2 Degree=1 IsPeriodic=0
    g316: BSplineCurve PolesCount=2 KnotsCount=2 Degree=1 IsPeriodic=0
    g317: BSplineCurve PolesCount=2 KnotsCount=2 Degree=1 IsPeriodic=0
    g318: BSplineCurve PolesCount=2 KnotsCount=2 Degree=1 IsPeriodic=0
    g319: BSplineCurve PolesCount=2 KnotsCount=2 Degree=1 IsPeriodic=0
    g320: BSplineCurve PolesCount=2 KnotsCount=2 Degree=1 IsPeriodic=0
    g321: BSplineCurve PolesCount=2 KnotsCount=2 Degree=1 IsPeriodic=0
    g322: BSplineCurve PolesCount=2 KnotsCount=2 Degree=1 IsPeriodic=0
    g323: BSplineCurve PolesCount=2 KnotsCount=2 Degree=1 IsPeriodic=0
    g324: BSplineCurve PolesCount=2 KnotsCount=2 Degree=1 IsPeriodic=0
    g325: BSplineCurve PolesCount=2 KnotsCount=2 Degree=1 IsPeriodic=0
    g326: BSplineCurve PolesCount=2 KnotsCount=2 Degree=1 IsPeriodic=0
    g327: BSplineCurve PolesCount=2 KnotsCount=2 Degree=1 IsPeriodic=0
    g328: BSplineCurve PolesCount=2 KnotsCount=2 Degree=1 IsPeriodic=0
    g329: BSplineCurve PolesCount=2 KnotsCount=2 Degree=1 IsPeriodic=0
    g330: BSplineCurve PolesCount=2 KnotsCount=2 Degree=1 IsPeriodic=0
    g331: BSplineCurve PolesCount=2 KnotsCount=2 Degree=1 IsPeriodic=0
    g332: BSplineCurve PolesCount=2 KnotsCount=2 Degree=1 IsPeriodic=0
    g333: BSplineCurve PolesCount=2 KnotsCount=2 Degree=1 IsPeriodic=0
    g334: BSplineCurve PolesCount=2 KnotsCount=2 Degree=1 IsPeriodic=0
    g335: BSplineCurve PolesCount=2 KnotsCount=2 Degree=1 IsPeriodic=0
    g336: BSplineCurve PolesCount=2 KnotsCount=2 Degree=1 IsPeriodic=0
    g337: BSplineCurve PolesCount=2 KnotsCount=2 Degree=1 IsPeriodic=0
    g338: BSplineCurve PolesCount=2 KnotsCount=2 Degree=1 IsPeriodic=0
    g339: BSplineCurve PolesCount=2 KnotsCount=2 Degree=1 IsPeriodic=0
    g340: BSplineCurve PolesCount=2 KnotsCount=2 Degree=1 IsPeriodic=0
    g341: BSplineCurve PolesCount=2 KnotsCount=2 Degree=1 IsPeriodic=0
    g342: BSplineCurve PolesCount=2 KnotsCount=2 Degree=1 IsPeriodic=0
    g343: BSplineCurve PolesCount=2 KnotsCount=2 Degree=1 IsPeriodic=0
    g344: BSplineCurve PolesCount=2 KnotsCount=2 Degree=1 IsPeriodic=0
    g345: BSplineCurve PolesCount=2 KnotsCount=2 Degree=1 IsPeriodic=0
    g346: BSplineCurve PolesCount=2 KnotsCount=2 Degree=1 IsPeriodic=0
    g347: BSplineCurve PolesCount=2 KnotsCount=2 Degree=1 IsPeriodic=0
    g348: BSplineCurve PolesCount=2 KnotsCount=2 Degree=1 IsPeriodic=0
    g349: BSplineCurve PolesCount=2 KnotsCount=2 Degree=1 IsPeriodic=0
    g350: BSplineCurve PolesCount=2 KnotsCount=2 Degree=1 IsPeriodic=0
    g351: BSplineCurve PolesCount=2 KnotsCount=2 Degree=1 IsPeriodic=0
    g352: BSplineCurve PolesCount=2 KnotsCount=2 Degree=1 IsPeriodic=0
    g353: BSplineCurve PolesCount=2 KnotsCount=2 Degree=1 IsPeriodic=0
    g354: BSplineCurve PolesCount=2 KnotsCount=2 Degree=1 IsPeriodic=0
    g355: BSplineCurve PolesCount=2 KnotsCount=2 Degree=1 IsPeriodic=0
    g356: BSplineCurve PolesCount=2 KnotsCount=2 Degree=1 IsPeriodic=0
    g357: BSplineCurve PolesCount=2 KnotsCount=2 Degree=1 IsPeriodic=0
    g358: BSplineCurve PolesCount=2 KnotsCount=2 Degree=1 IsPeriodic=0
    g359: BSplineCurve PolesCount=2 KnotsCount=2 Degree=1 IsPeriodic=0
    g360: BSplineCurve PolesCount=2 KnotsCount=2 Degree=1 IsPeriodic=0
    g361: BSplineCurve PolesCount=2 KnotsCount=2 Degree=1 IsPeriodic=0
    g362: BSplineCurve PolesCount=2 KnotsCount=2 Degree=1 IsPeriodic=0
    g363: BSplineCurve PolesCount=2 KnotsCount=2 Degree=1 IsPeriodic=0
    g364: BSplineCurve PolesCount=2 KnotsCount=2 Degree=1 IsPeriodic=0
    g365: BSplineCurve PolesCount=2 KnotsCount=2 Degree=1 IsPeriodic=0
    g366: BSplineCurve PolesCount=2 KnotsCount=2 Degree=1 IsPeriodic=0
    g367: BSplineCurve PolesCount=2 KnotsCount=2 Degree=1 IsPeriodic=0
    g368: BSplineCurve PolesCount=2 KnotsCount=2 Degree=1 IsPeriodic=0
    g369: BSplineCurve PolesCount=2 KnotsCount=2 Degree=1 IsPeriodic=0
    g370: BSplineCurve PolesCount=2 KnotsCount=2 Degree=1 IsPeriodic=0
    g371: BSplineCurve PolesCount=2 KnotsCount=2 Degree=1 IsPeriodic=0
    g372: BSplineCurve PolesCount=2 KnotsCount=2 Degree=1 IsPeriodic=0
    g373: BSplineCurve PolesCount=2 KnotsCount=2 Degree=1 IsPeriodic=0
    g374: BSplineCurve PolesCount=2 KnotsCount=2 Degree=1 IsPeriodic=0
    g375: BSplineCurve PolesCount=2 KnotsCount=2 Degree=1 IsPeriodic=0
    g376: BSplineCurve PolesCount=2 KnotsCount=2 Degree=1 IsPeriodic=0
    g377: BSplineCurve PolesCount=2 KnotsCount=2 Degree=1 IsPeriodic=0
    g378: BSplineCurve PolesCount=2 KnotsCount=2 Degree=1 IsPeriodic=0
    g379: BSplineCurve PolesCount=2 KnotsCount=2 Degree=1 IsPeriodic=0
    g380: BSplineCurve PolesCount=2 KnotsCount=2 Degree=1 IsPeriodic=0
    g381: BSplineCurve PolesCount=2 KnotsCount=2 Degree=1 IsPeriodic=0
    g382: BSplineCurve PolesCount=2 KnotsCount=2 Degree=1 IsPeriodic=0
    g383: BSplineCurve PolesCount=2 KnotsCount=2 Degree=1 IsPeriodic=0
    g384: BSplineCurve PolesCount=2 KnotsCount=2 Degree=1 IsPeriodic=0
    g385: BSplineCurve PolesCount=2 KnotsCount=2 Degree=1 IsPeriodic=0
    g386: BSplineCurve PolesCount=2 KnotsCount=2 Degree=1 IsPeriodic=0
    g387: BSplineCurve PolesCount=2 KnotsCount=2 Degree=1 IsPeriodic=0
    g388: BSplineCurve PolesCount=2 KnotsCount=2 Degree=1 IsPeriodic=0
    g389: BSplineCurve PolesCount=2 KnotsCount=2 Degree=1 IsPeriodic=0
    g390: BSplineCurve PolesCount=2 KnotsCount=2 Degree=1 IsPeriodic=0
    g391: BSplineCurve PolesCount=2 KnotsCount=2 Degree=1 IsPeriodic=0
    g392: BSplineCurve PolesCount=2 KnotsCount=2 Degree=1 IsPeriodic=0
    g393: BSplineCurve PolesCount=2 KnotsCount=2 Degree=1 IsPeriodic=0
    g394: BSplineCurve PolesCount=2 KnotsCount=2 Degree=1 IsPeriodic=0
    g395: BSplineCurve PolesCount=2 KnotsCount=2 Degree=1 IsPeriodic=0
    g396: BSplineCurve PolesCount=2 KnotsCount=2 Degree=1 IsPeriodic=0
    g397: BSplineCurve PolesCount=2 KnotsCount=2 Degree=1 IsPeriodic=0
    g398: BSplineCurve PolesCount=2 KnotsCount=2 Degree=1 IsPeriodic=0
    g399: BSplineCurve PolesCount=2 KnotsCount=2 Degree=1 IsPeriodic=0
    ... +460 more geometry lines
  constraints (860):
    c: Coincident(g0,g1)
    c: Coincident(g1,g2)
    c: Coincident(g2,g3)
    c: Coincident(g3,g4)
    c: Coincident(g4,g5)
    c: Coincident(g5,g6)
    c: Coincident(g6,g7)
    c: Coincident(g7,g8)
    c: Coincident(g8,g9)
    c: Coincident(g9,g10)
    c: Coincident(g10,g11)
    c: Coincident(g11,g12)
    c: Coincident(g12,g13)
    c: Coincident(g13,g14)
    c: Coincident(g14,g15)
    c: Coincident(g15,g16)
    c: Coincident(g16,g17)
    c: Coincident(g17,g18)
    c: Coincident(g18,g19)
    c: Coincident(g19,g20)
    c: Coincident(g20,g21)
    c: Coincident(g21,g22)
    c: Coincident(g22,g23)
    c: Coincident(g23,g24)
    c: Coincident(g24,g25)
    c: Coincident(g25,g26)
    c: Coincident(g26,g27)
    c: Coincident(g27,g28)
    c: Coincident(g28,g29)
    c: Coincident(g29,g30)
    c: Coincident(g30,g31)
    c: Coincident(g31,g32)
    c: Coincident(g32,g33)
    c: Coincident(g33,g34)
    c: Coincident(g34,g35)
    c: Coincident(g35,g36)
    c: Coincident(g36,g37)
    c: Coincident(g37,g38)
    c: Coincident(g38,g39)
    c: Coincident(g39,g40)
    c: Coincident(g40,g41)
    c: Coincident(g41,g42)
    c: Coincident(g42,g43)
    c: Coincident(g43,g44)
    c: Coincident(g44,g45)
    c: Coincident(g45,g46)
    c: Coincident(g46,g47)
    c: Coincident(g47,g48)
    c: Coincident(g48,g49)
    c: Coincident(g49,g50)
    c: Coincident(g50,g51)
    c: Coincident(g51,g52)
    c: Coincident(g52,g53)
    c: Coincident(g53,g54)
    c: Coincident(g54,g55)
    c: Coincident(g55,g56)
    c: Coincident(g56,g57)
    c: Coincident(g57,g58)
    c: Coincident(g58,g59)
    c: Coincident(g59,g60)
    c: Coincident(g60,g61)
    c: Coincident(g61,g62)
    c: Coincident(g62,g63)
    c: Coincident(g63,g64)
    c: Coincident(g64,g65)
    c: Coincident(g65,g66)
    c: Coincident(g66,g67)
    c: Coincident(g67,g68)
    c: Coincident(g68,g69)
    c: Coincident(g69,g70)
    c: Coincident(g70,g71)
    c: Coincident(g71,g72)
    c: Coincident(g72,g73)
    c: Coincident(g73,g74)
    c: Coincident(g74,g75)
    c: Coincident(g75,g76)
    c: Coincident(g76,g77)
    c: Coincident(g77,g78)
    c: Coincident(g78,g79)
    c: Coincident(g79,g80)
    c: Coincident(g80,g81)
    c: Coincident(g81,g82)
    c: Coincident(g82,g83)
    c: Coincident(g83,g84)
    c: Coincident(g84,g85)
    c: Coincident(g85,g86)
    c: Coincident(g86,g87)
    c: Coincident(g87,g0)
    c: Coincident(g88,g89)
    c: Coincident(g89,g90)
    c: Coincident(g90,g91)
    c: Coincident(g91,g92)
    c: Coincident(g92,g93)
    c: Coincident(g93,g94)
    c: Coincident(g94,g95)
    c: Coincident(g95,g96)
    c: Coincident(g96,g97)
    c: Coincident(g97,g98)
    c: Coincident(g98,g99)
    c: Coincident(g99,g100)
    c: Coincident(g100,g101)
    c: Coincident(g101,g102)
    c: Coincident(g102,g103)
    c: Coincident(g103,g104)
    c: Coincident(g104,g105)
    c: Coincident(g105,g106)
    c: Coincident(g106,g107)
    c: Coincident(g107,g108)
    c: Coincident(g108,g109)
    c: Coincident(g109,g110)
    c: Coincident(g110,g111)
    c: Coincident(g111,g112)
    c: Coincident(g112,g113)
    c: Coincident(g113,g114)
    c: Coincident(g114,g115)
    c: Coincident(g115,g116)
    c: Coincident(g116,g117)
    c: Coincident(g117,g118)
    c: Coincident(g118,g119)
    c: Coincident(g119,g120)
    c: Coincident(g120,g121)
    c: Coincident(g121,g122)
    c: Coincident(g122,g123)
    c: Coincident(g123,g124)
    c: Coincident(g124,g125)
    c: Coincident(g125,g126)
    c: Coincident(g126,g127)
    c: Coincident(g127,g88)
    c: Coincident(g128,g129)
    c: Coincident(g129,g130)
    c: Coincident(g130,g131)
    c: Coincident(g131,g132)
    c: Coincident(g132,g133)
    c: Coincident(g133,g134)
    c: Coincident(g134,g135)
    c: Coincident(g135,g136)
    c: Coincident(g136,g137)
    c: Coincident(g137,g138)
    c: Coincident(g138,g139)
    c: Coincident(g139,g140)
    c: Coincident(g140,g141)
    c: Coincident(g141,g142)
    c: Coincident(g142,g143)
    c: Coincident(g143,g144)
    c: Coincident(g144,g145)
    c: Coincident(g145,g146)
    c: Coincident(g146,g147)
    c: Coincident(g147,g148)
    c: Coincident(g148,g149)
    c: Coincident(g149,g150)
    c: Coincident(g150,g151)
    c: Coincident(g151,g152)
    c: Coincident(g152,g153)
    c: Coincident(g153,g154)
    c: Coincident(g154,g155)
    c: Coincident(g155,g156)
    c: Coincident(g156,g157)
    c: Coincident(g157,g158)
    c: Coincident(g158,g159)
    c: Coincident(g159,g160)
    c: Coincident(g160,g161)
    c: Coincident(g161,g162)
    c: Coincident(g162,g163)
    c: Coincident(g163,g164)
    c: Coincident(g164,g165)
    c: Coincident(g165,g166)
    c: Coincident(g166,g167)
    c: Coincident(g167,g168)
    c: Coincident(g168,g169)
    c: Coincident(g169,g170)
    c: Coincident(g170,g171)
    c: Coincident(g171,g172)
    c: Coincident(g172,g173)
    c: Coincident(g173,g174)
    c: Coincident(g174,g175)
    c: Coincident(g175,g176)
    c: Coincident(g176,g177)
    c: Coincident(g177,g178)
    c: Coincident(g178,g179)
    c: Coincident(g179,g180)
    c: Coincident(g180,g181)
    c: Coincident(g181,g182)
    c: Coincident(g182,g183)
    c: Coincident(g183,g184)
    c: Coincident(g184,g185)
    c: Coincident(g185,g186)
    c: Coincident(g186,g187)
    c: Coincident(g187,g188)
    c: Coincident(g188,g189)
    c: Coincident(g189,g190)
    c: Coincident(g190,g191)
    c: Coincident(g191,g192)
    c: Coincident(g192,g193)
    c: Coincident(g193,g194)
    c: Coincident(g194,g195)
    c: Coincident(g195,g196)
    c: Coincident(g196,g197)
    c: Coincident(g197,g198)
    c: Coincident(g198,g199)
    c: Coincident(g199,g200)
    c: Coincident(g200,g201)
    c: Coincident(g201,g202)
    c: Coincident(g202,g203)
    c: Coincident(g203,g204)
    c: Coincident(g204,g205)
    c: Coincident(g205,g206)
    c: Coincident(g206,g207)
    c: Coincident(g207,g208)
    c: Coincident(g208,g209)
    c: Coincident(g209,g210)
    c: Coincident(g210,g211)
    c: Coincident(g211,g212)
    c: Coincident(g212,g213)
    c: Coincident(g213,g214)
    c: Coincident(g214,g215)
    c: Coincident(g215,g216)
    c: Coincident(g216,g217)
    c: Coincident(g217,g218)
    c: Coincident(g218,g219)
    c: Coincident(g219,g220)
    c: Coincident(g220,g221)
    c: Coincident(g221,g222)
    c: Coincident(g222,g223)
    c: Coincident(g223,g224)
    c: Coincident(g224,g225)
    c: Coincident(g225,g226)
    c: Coincident(g226,g227)
    c: Coincident(g227,g228)
    c: Coincident(g228,g229)
    c: Coincident(g229,g230)
    c: Coincident(g230,g231)
    c: Coincident(g231,g232)
    c: Coincident(g232,g233)
    c: Coincident(g233,g234)
    c: Coincident(g234,g235)
    c: Coincident(g235,g236)
    c: Coincident(g236,g237)
    c: Coincident(g237,g238)
    c: Coincident(g238,g239)
    c: Coincident(g239,g128)
    c: Coincident(g240,g241)
    c: Coincident(g241,g242)
    c: Coincident(g242,g243)
    c: Coincident(g243,g244)
    c: Coincident(g244,g245)
    c: Coincident(g245,g246)
    c: Coincident(g246,g247)
    c: Coincident(g247,g248)
    c: Coincident(g248,g249)
    c: Coincident(g249,g250)
    c: Coincident(g250,g251)
    c: Coincident(g251,g252)
    c: Coincident(g252,g253)
    c: Coincident(g253,g254)
    c: Coincident(g254,g255)
    c: Coincident(g255,g256)
    c: Coincident(g256,g257)
    c: Coincident(g257,g258)
    c: Coincident(g258,g259)
    c: Coincident(g259,g260)
    c: Coincident(g260,g261)
    c: Coincident(g261,g262)
    c: Coincident(g262,g263)
    c: Coincident(g263,g264)
    c: Coincident(g264,g265)
    c: Coincident(g265,g266)
    c: Coincident(g266,g267)
    c: Coincident(g267,g268)
    c: Coincident(g268,g269)
    c: Coincident(g269,g270)
    c: Coincident(g270,g271)
    c: Coincident(g271,g272)
    c: Coincident(g272,g273)
    c: Coincident(g273,g274)
    c: Coincident(g274,g275)
    c: Coincident(g275,g276)
    c: Coincident(g276,g277)
    c: Coincident(g277,g278)
    c: Coincident(g278,g279)
    c: Coincident(g279,g280)
    c: Coincident(g280,g281)
    c: Coincident(g281,g282)
    c: Coincident(g282,g283)
    c: Coincident(g283,g284)
    c: Coincident(g284,g285)
    c: Coincident(g285,g286)
    c: Coincident(g286,g287)
    c: Coincident(g287,g240)
    c: Coincident(g288,g289)
    c: Coincident(g289,g290)
    c: Coincident(g290,g291)
    c: Coincident(g291,g292)
    c: Coincident(g292,g293)
    c: Coincident(g293,g294)
    c: Coincident(g294,g295)
    c: Coincident(g295,g296)
    c: Coincident(g296,g297)
    c: Coincident(g297,g298)
    c: Coincident(g298,g299)
    c: Coincident(g299,g300)
    c: Coincident(g300,g301)
    c: Coincident(g301,g302)
    c: Coincident(g302,g303)
    c: Coincident(g303,g304)
    c: Coincident(g304,g305)
    c: Coincident(g305,g306)
    c: Coincident(g306,g307)
    c: Coincident(g307,g308)
    c: Coincident(g308,g309)
    c: Coincident(g309,g310)
    c: Coincident(g310,g311)
    c: Coincident(g311,g288)
    c: Coincident(g312,g313)
    c: Coincident(g313,g314)
    c: Coincident(g314,g315)
    c: Coincident(g315,g316)
    c: Coincident(g316,g317)
    c: Coincident(g317,g318)
    c: Coincident(g318,g319)
    c: Coincident(g319,g320)
    c: Coincident(g320,g321)
    c: Coincident(g321,g322)
    c: Coincident(g322,g323)
    c: Coincident(g323,g324)
    c: Coincident(g324,g325)
    c: Coincident(g325,g326)
    c: Coincident(g326,g327)
    c: Coincident(g327,g312)
    c: Coincident(g328,g329)
    c: Coincident(g329,g330)
    c: Coincident(g330,g331)
    c: Coincident(g331,g332)
    c: Coincident(g332,g333)
    c: Coincident(g333,g334)
    c: Coincident(g334,g335)
    c: Coincident(g335,g336)
    c: Coincident(g336,g337)
    c: Coincident(g337,g338)
    c: Coincident(g338,g339)
    c: Coincident(g339,g340)
    c: Coincident(g340,g341)
    c: Coincident(g341,g342)
    c: Coincident(g342,g343)
    c: Coincident(g343,g344)
    c: Coincident(g344,g345)
    c: Coincident(g345,g346)
    c: Coincident(g346,g347)
    c: Coincident(g347,g348)
    c: Coincident(g348,g349)
    c: Coincident(g349,g350)
    c: Coincident(g350,g351)
    c: Coincident(g351,g352)
    c: Coincident(g352,g353)
    c: Coincident(g353,g354)
    c: Coincident(g354,g355)
    c: Coincident(g355,g356)
    c: Coincident(g356,g357)
    c: Coincident(g357,g358)
    c: Coincident(g358,g359)
    c: Coincident(g359,g360)
    c: Coincident(g360,g361)
    c: Coincident(g361,g362)
    c: Coincident(g362,g363)
    c: Coincident(g363,g364)
    c: Coincident(g364,g365)
    c: Coincident(g365,g366)
    c: Coincident(g366,g367)
    c: Coincident(g367,g368)
    c: Coincident(g368,g369)
    c: Coincident(g369,g370)
    c: Coincident(g370,g371)
    c: Coincident(g371,g372)
    c: Coincident(g372,g373)
    c: Coincident(g373,g374)
    c: Coincident(g374,g375)
    c: Coincident(g375,g376)
    c: Coincident(g376,g377)
    c: Coincident(g377,g378)
    c: Coincident(g378,g379)
    c: Coincident(g379,g380)
    c: Coincident(g380,g381)
    c: Coincident(g381,g382)
    c: Coincident(g382,g383)
    c: Coincident(g383,g384)
    c: Coincident(g384,g385)
    c: Coincident(g385,g386)
    c: Coincident(g386,g387)
    c: Coincident(g387,g388)
    c: Coincident(g388,g389)
    c: Coincident(g389,g390)
    c: Coincident(g390,g391)
    c: Coincident(g391,g392)
    c: Coincident(g392,g393)
    c: Coincident(g393,g394)
    c: Coincident(g394,g395)
    c: Coincident(g395,g396)
    c: Coincident(g396,g397)
    c: Coincident(g397,g398)
    c: Coincident(g398,g399)
    c: Coincident(g399,g328)
    c: Coincident(g400,g401)
    c: Coincident(g401,g402)
    c: Coincident(g402,g403)
    c: Coincident(g403,g404)
    c: Coincident(g404,g405)
    c: Coincident(g405,g406)
    c: Coincident(g406,g407)
    c: Coincident(g407,g408)
    c: Coincident(g408,g409)
    c: Coincident(g409,g410)
    c: Coincident(g410,g411)
    c: Coincident(g411,g412)
    c: Coincident(g412,g413)
    c: Coincident(g413,g414)
    c: Coincident(g414,g415)
    c: Coincident(g415,g416)
    c: Coincident(g416,g417)
    c: Coincident(g417,g418)
    c: Coincident(g418,g419)
    c: Coincident(g419,g420)
    c: Coincident(g420,g421)
    c: Coincident(g421,g422)
    c: Coincident(g422,g423)
    c: Coincident(g423,g400)
    c: Coincident(g424,g425)
    c: Coincident(g425,g426)
    c: Coincident(g426,g427)
    c: Coincident(g427,g428)
    c: Coincident(g428,g429)
    c: Coincident(g429,g430)
    c: Coincident(g430,g431)
    c: Coincident(g431,g432)
    c: Coincident(g432,g433)
    c: Coincident(g433,g434)
    c: Coincident(g434,g435)
    c: Coincident(g435,g436)
    c: Coincident(g436,g437)
    c: Coincident(g437,g438)
    c: Coincident(g438,g439)
    c: Coincident(g439,g440)
    c: Coincident(g440,g441)
    c: Coincident(g441,g442)
    c: Coincident(g442,g443)
    c: Coincident(g443,g444)
    c: Coincident(g444,g445)
    c: Coincident(g445,g446)
    c: Coincident(g446,g447)
    c: Coincident(g447,g448)
    c: Coincident(g448,g449)
    c: Coincident(g449,g450)
    c: Coincident(g450,g451)
    c: Coincident(g451,g452)
    c: Coincident(g452,g453)
    c: Coincident(g453,g454)
    c: Coincident(g454,g455)
    c: Coincident(g455,g456)
    c: Coincident(g456,g457)
    c: Coincident(g457,g458)
    c: Coincident(g458,g459)
    c: Coincident(g459,g460)
    c: Coincident(g460,g461)
    c: Coincident(g461,g462)
    c: Coincident(g462,g463)
    c: Coincident(g463,g464)
    c: Coincident(g464,g465)
    c: Coincident(g465,g466)
    c: Coincident(g466,g467)
    c: Coincident(g467,g468)
    c: Coincident(g468,g469)
    c: Coincident(g469,g470)
    c: Coincident(g470,g471)
    c: Coincident(g471,g472)
    c: Coincident(g472,g473)
    c: Coincident(g473,g474)
    c: Coincident(g474,g475)
    c: Coincident(g475,g476)
    c: Coincident(g476,g477)
    c: Coincident(g477,g478)
    c: Coincident(g478,g479)
    c: Coincident(g479,g424)
    c: Coincident(g480,g481)
    c: Coincident(g481,g482)
    c: Coincident(g482,g483)
    c: Coincident(g483,g484)
    c: Coincident(g484,g485)
    c: Coincident(g485,g486)
    c: Coincident(g486,g487)
    c: Coincident(g487,g488)
    c: Coincident(g488,g489)
    c: Coincident(g489,g490)
    c: Coincident(g490,g491)
    c: Coincident(g491,g492)
    c: Coincident(g492,g493)
    c: Coincident(g493,g494)
    c: Coincident(g494,g495)
    c: Coincident(g495,g480)
    c: Coincident(g496,g497)
    c: Coincident(g497,g498)
    c: Coincident(g498,g499)
    c: Coincident(g499,g500)
    c: Coincident(g500,g501)
    c: Coincident(g501,g502)
    c: Coincident(g502,g503)
    c: Coincident(g503,g504)
    c: Coincident(g504,g505)
    c: Coincident(g505,g506)
    c: Coincident(g506,g507)
    c: Coincident(g507,g508)
    c: Coincident(g508,g509)
    c: Coincident(g509,g510)
    c: Coincident(g510,g511)
    c: Coincident(g511,g512)
    c: Coincident(g512,g513)
    c: Coincident(g513,g514)
    c: Coincident(g514,g515)
    c: Coincident(g515,g516)
    c: Coincident(g516,g517)
    c: Coincident(g517,g518)
    c: Coincident(g518,g519)
    c: Coincident(g519,g520)
    c: Coincident(g520,g521)
    c: Coincident(g521,g522)
    c: Coincident(g522,g523)
    c: Coincident(g523,g524)
    c: Coincident(g524,g525)
    c: Coincident(g525,g526)
    c: Coincident(g526,g527)
    c: Coincident(g527,g528)
    c: Coincident(g528,g529)
    c: Coincident(g529,g530)
    c: Coincident(g530,g531)
    c: Coincident(g531,g532)
    c: Coincident(g532,g533)
    c: Coincident(g533,g534)
    c: Coincident(g534,g535)
    c: Coincident(g535,g496)
    c: Coincident(g536,g537)
    c: Coincident(g537,g538)
    c: Coincident(g538,g539)
    c: Coincident(g539,g540)
    c: Coincident(g540,g541)
    c: Coincident(g541,g542)
    c: Coincident(g542,g543)
    c: Coincident(g543,g544)
    c: Coincident(g544,g545)
    c: Coincident(g545,g546)
    c: Coincident(g546,g547)
    c: Coincident(g547,g548)
    c: Coincident(g548,g549)
    c: Coincident(g549,g550)
    c: Coincident(g550,g551)
    c: Coincident(g551,g552)
    c: Coincident(g552,g553)
    c: Coincident(g553,g554)
    c: Coincident(g554,g555)
    c: Coincident(g555,g556)
    c: Coincident(g556,g557)
    c: Coincident(g557,g558)
    c: Coincident(g558,g559)
    c: Coincident(g559,g560)
    c: Coincident(g560,g561)
    c: Coincident(g561,g562)
    c: Coincident(g562,g563)
    c: Coincident(g563,g564)
    c: Coincident(g564,g565)
    c: Coincident(g565,g566)
    c: Coincident(g566,g567)
    c: Coincident(g567,g568)
    c: Coincident(g568,g569)
    c: Coincident(g569,g570)
    c: Coincident(g570,g571)
    c: Coincident(g571,g572)
    c: Coincident(g572,g573)
    c: Coincident(g573,g574)
    c: Coincident(g574,g575)
    c: Coincident(g575,g536)
    c: Coincident(g576,g577)
    c: Coincident(g577,g578)
    c: Coincident(g578,g579)
    c: Coincident(g579,g580)
    c: Coincident(g580,g581)
    c: Coincident(g581,g582)
    c: Coincident(g582,g583)
    c: Coincident(g583,g584)
    c: Coincident(g584,g585)
    c: Coincident(g585,g586)
    c: Coincident(g586,g587)
    c: Coincident(g587,g576)
    c: Coincident(g588,g589)
    c: Coincident(g589,g590)
    c: Coincident(g590,g591)
    c: Coincident(g591,g592)
    c: Coincident(g592,g593)
    c: Coincident(g593,g594)
    c: Coincident(g594,g595)
    c: Coincident(g595,g596)
    c: Coincident(g596,g597)
    c: Coincident(g597,g598)
    c: Coincident(g598,g599)
    c: Coincident(g599,g600)
    c: Coincident(g600,g601)
    c: Coincident(g601,g602)
    c: Coincident(g602,g603)
    c: Coincident(g603,g604)
    c: Coincident(g604,g605)
    c: Coincident(g605,g606)
    c: Coincident(g606,g607)
    c: Coincident(g607,g608)
    c: Coincident(g608,g609)
    c: Coincident(g609,g610)
    c: Coincident(g610,g611)
    c: Coincident(g611,g612)
    c: Coincident(g612,g613)
    c: Coincident(g613,g614)
    c: Coincident(g614,g615)
    c: Coincident(g615,g616)
    c: Coincident(g616,g617)
    c: Coincident(g617,g618)
    c: Coincident(g618,g619)
    c: Coincident(g619,g620)
    c: Coincident(g620,g621)
    c: Coincident(g621,g622)
    c: Coincident(g622,g623)
    c: Coincident(g623,g624)
    c: Coincident(g624,g625)
    c: Coincident(g625,g626)
    c: Coincident(g626,g627)
    c: Coincident(g627,g628)
    c: Coincident(g628,g629)
    c: Coincident(g629,g630)
    c: Coincident(g630,g631)
    c: Coincident(g631,g632)
    c: Coincident(g632,g633)
    c: Coincident(g633,g634)
    c: Coincident(g634,g635)
    c: Coincident(g635,g636)
    c: Coincident(g636,g637)
    c: Coincident(g637,g638)
    c: Coincident(g638,g639)
    c: Coincident(g639,g640)
    c: Coincident(g640,g641)
    c: Coincident(g641,g642)
    c: Coincident(g642,g643)
    c: Coincident(g643,g644)
    c: Coincident(g644,g645)
    c: Coincident(g645,g646)
    c: Coincident(g646,g647)
    c: Coincident(g647,g648)
    c: Coincident(g648,g649)
    c: Coincident(g649,g650)
    c: Coincident(g650,g651)
    c: Coincident(g651,g652)
    c: Coincident(g652,g653)
    c: Coincident(g653,g654)
    c: Coincident(g654,g655)
    c: Coincident(g655,g656)
    c: Coincident(g656,g657)
    c: Coincident(g657,g658)
    c: Coincident(g658,g659)
    c: Coincident(g659,g660)
    c: Coincident(g660,g661)
    c: Coincident(g661,g662)
    c: Coincident(g662,g663)
    c: Coincident(g663,g664)
    c: Coincident(g664,g665)
    c: Coincident(g665,g666)
    c: Coincident(g666,g667)
    c: Coincident(g667,g668)
    c: Coincident(g668,g669)
    c: Coincident(g669,g670)
    c: Coincident(g670,g671)
    c: Coincident(g671,g672)
    c: Coincident(g672,g673)
    c: Coincident(g673,g674)
    c: Coincident(g674,g675)
    c: Coincident(g675,g588)
    c: Coincident(g676,g677)
    c: Coincident(g677,g678)
    c: Coincident(g678,g679)
    c: Coincident(g679,g680)
    c: Coincident(g680,g681)
    c: Coincident(g681,g682)
    c: Coincident(g682,g683)
    c: Coincident(g683,g684)
    c: Coincident(g684,g685)
    c: Coincident(g685,g686)
    c: Coincident(g686,g687)
    c: Coincident(g687,g688)
    c: Coincident(g688,g689)
    c: Coincident(g689,g690)
    c: Coincident(g690,g691)
    c: Coincident(g691,g676)
    c: Coincident(g692,g693)
    c: Coincident(g693,g694)
    c: Coincident(g694,g695)
    c: Coincident(g695,g696)
    c: Coincident(g696,g697)
    c: Coincident(g697,g698)
    c: Coincident(g698,g699)
    c: Coincident(g699,g700)
    c: Coincident(g700,g701)
    c: Coincident(g701,g702)
    c: Coincident(g702,g703)
    c: Coincident(g703,g704)
    c: Coincident(g704,g705)
    c: Coincident(g705,g706)
    c: Coincident(g706,g707)
    c: Coincident(g707,g708)
    c: Coincident(g708,g709)
    c: Coincident(g709,g710)
    c: Coincident(g710,g711)
    c: Coincident(g711,g712)
    c: Coincident(g712,g713)
    c: Coincident(g713,g714)
    c: Coincident(g714,g715)
    c: Coincident(g715,g716)
    c: Coincident(g716,g717)
    c: Coincident(g717,g718)
    c: Coincident(g718,g719)
    c: Coincident(g719,g720)
    c: Coincident(g720,g721)
    c: Coincident(g721,g722)
    c: Coincident(g722,g723)
    c: Coincident(g723,g724)
    c: Coincident(g724,g725)
    c: Coincident(g725,g726)
    c: Coincident(g726,g727)
    c: Coincident(g727,g728)
    c: Coincident(g728,g729)
    c: Coincident(g729,g730)
    c: Coincident(g730,g731)
    c: Coincident(g731,g692)
    c: Coincident(g732,g733)
    c: Coincident(g733,g734)
    c: Coincident(g734,g735)
    c: Coincident(g735,g736)
    c: Coincident(g736,g737)
    c: Coincident(g737,g738)
    c: Coincident(g738,g739)
    c: Coincident(g739,g740)
    c: Coincident(g740,g741)
    c: Coincident(g741,g742)
    c: Coincident(g742,g743)
    c: Coincident(g743,g744)
    c: Coincident(g744,g745)
    c: Coincident(g745,g746)
    c: Coincident(g746,g747)
    c: Coincident(g747,g748)
    c: Coincident(g748,g749)
    c: Coincident(g749,g750)
    c: Coincident(g750,g751)
    c: Coincident(g751,g752)
    c: Coincident(g752,g753)
    c: Coincident(g753,g754)
    c: Coincident(g754,g755)
    c: Coincident(g755,g756)
    c: Coincident(g756,g757)
    c: Coincident(g757,g758)
    c: Coincident(g758,g759)
    c: Coincident(g759,g760)
    c: Coincident(g760,g761)
    c: Coincident(g761,g762)
    c: Coincident(g762,g763)
    c: Coincident(g763,g732)
    c: Coincident(g764,g765)
    c: Coincident(g765,g766)
    c: Coincident(g766,g767)
    c: Coincident(g767,g768)
    c: Coincident(g768,g769)
    c: Coincident(g769,g770)
    c: Coincident(g770,g771)
    c: Coincident(g771,g772)
    c: Coincident(g772,g773)
    c: Coincident(g773,g774)
    c: Coincident(g774,g775)
    c: Coincident(g775,g776)
    c: Coincident(g776,g777)
    c: Coincident(g777,g778)
    c: Coincident(g778,g779)
    c: Coincident(g779,g780)
    c: Coincident(g780,g781)
    c: Coincident(g781,g782)
    c: Coincident(g782,g783)
    c: Coincident(g783,g784)
    c: Coincident(g784,g785)
    c: Coincident(g785,g786)
    c: Coincident(g786,g787)
    c: Coincident(g787,g764)
    c: Coincident(g788,g789)
    c: Coincident(g789,g790)
    c: Coincident(g790,g791)
    c: Coincident(g791,g792)
    c: Coincident(g792,g793)
    c: Coincident(g793,g794)
    c: Coincident(g794,g795)
    c: Coincident(g795,g796)
    c: Coincident(g796,g797)
    c: Coincident(g797,g798)
    c: Coincident(g798,g799)
    c: Coincident(g799,g800)
    c: Coincident(g800,g801)
    c: Coincident(g801,g802)
    c: Coincident(g802,g803)
    c: Coincident(g803,g804)
    c: Coincident(g804,g805)
    c: Coincident(g805,g806)
    c: Coincident(g806,g807)
    c: Coincident(g807,g808)
    c: Coincident(g808,g809)
    c: Coincident(g809,g810)
    c: Coincident(g810,g811)
    c: Coincident(g811,g812)
    c: Coincident(g812,g813)
    c: Coincident(g813,g814)
    c: Coincident(g814,g815)
    c: Coincident(g815,g816)
    c: Coincident(g816,g817)
    c: Coincident(g817,g818)
    c: Coincident(g818,g819)
    c: Coincident(g819,g820)
    c: Coincident(g820,g821)
    c: Coincident(g821,g822)
    c: Coincident(g822,g823)
    c: Coincident(g823,g824)
    c: Coincident(g824,g825)
    c: Coincident(g825,g826)
    c: Coincident(g826,g827)
    c: Coincident(g827,g828)
    c: Coincident(g828,g829)
    c: Coincident(g829,g830)
    c: Coincident(g830,g831)
    c: Coincident(g831,g832)
    c: Coincident(g832,g833)
    c: Coincident(g833,g834)
    c: Coincident(g834,g835)
    c: Coincident(g835,g836)
    c: Coincident(g836,g837)
    c: Coincident(g837,g838)
    c: Coincident(g838,g839)
    c: Coincident(g839,g840)
    c: Coincident(g840,g841)
    c: Coincident(g841,g842)
    c: Coincident(g842,g843)
    c: Coincident(g843,g844)
    c: Coincident(g844,g845)
    c: Coincident(g845,g846)
    c: Coincident(g846,g847)
    c: Coincident(g847,g848)
    c: Coincident(g848,g849)
    c: Coincident(g849,g850)
    c: Coincident(g850,g851)
    c: Coincident(g851,g852)
    c: Coincident(g852,g853)
    c: Coincident(g853,g854)
    c: Coincident(g854,g855)
    c: Coincident(g855,g856)
    c: Coincident(g856,g857)
    c: Coincident(g857,g858)
    c: Coincident(g858,g859)
    c: Coincident(g859,g788)
FEATURE [Sketcher::SketchObject] Sketch021  label="16 Bit VS002"
  FullyConstrained = false
  Placement = pos=(8.14,9.25,-4) rot=(1,0,0;3.14159rad)
  sketch-geometry (860):
    g0: BSplineCurve PolesCount=2 KnotsCount=2 Degree=1 IsPeriodic=0
    g1: BSplineCurve PolesCount=2 KnotsCount=2 Degree=1 IsPeriodic=0
    g2: BSplineCurve PolesCount=2 KnotsCount=2 Degree=1 IsPeriodic=0
    g3: BSplineCurve PolesCount=2 KnotsCount=2 Degree=1 IsPeriodic=0
    g4: BSplineCurve PolesCount=2 KnotsCount=2 Degree=1 IsPeriodic=0
    g5: BSplineCurve PolesCount=2 KnotsCount=2 Degree=1 IsPeriodic=0
    g6: BSplineCurve PolesCount=2 KnotsCount=2 Degree=1 IsPeriodic=0
    g7: BSplineCurve PolesCount=2 KnotsCount=2 Degree=1 IsPeriodic=0
    g8: BSplineCurve PolesCount=2 KnotsCount=2 Degree=1 IsPeriodic=0
    g9: BSplineCurve PolesCount=2 KnotsCount=2 Degree=1 IsPeriodic=0
    g10: BSplineCurve PolesCount=2 KnotsCount=2 Degree=1 IsPeriodic=0
    g11: BSplineCurve PolesCount=2 KnotsCount=2 Degree=1 IsPeriodic=0
    g12: BSplineCurve PolesCount=2 KnotsCount=2 Degree=1 IsPeriodic=0
    g13: BSplineCurve PolesCount=2 KnotsCount=2 Degree=1 IsPeriodic=0
    g14: BSplineCurve PolesCount=2 KnotsCount=2 Degree=1 IsPeriodic=0
    g15: BSplineCurve PolesCount=2 KnotsCount=2 Degree=1 IsPeriodic=0
    g16: BSplineCurve PolesCount=2 KnotsCount=2 Degree=1 IsPeriodic=0
    g17: BSplineCurve PolesCount=2 KnotsCount=2 Degree=1 IsPeriodic=0
    g18: BSplineCurve PolesCount=2 KnotsCount=2 Degree=1 IsPeriodic=0
    g19: BSplineCurve PolesCount=2 KnotsCount=2 Degree=1 IsPeriodic=0
    g20: BSplineCurve PolesCount=2 KnotsCount=2 Degree=1 IsPeriodic=0
    g21: BSplineCurve PolesCount=2 KnotsCount=2 Degree=1 IsPeriodic=0
    g22: BSplineCurve PolesCount=2 KnotsCount=2 Degree=1 IsPeriodic=0
    g23: BSplineCurve PolesCount=2 KnotsCount=2 Degree=1 IsPeriodic=0
    g24: BSplineCurve PolesCount=2 KnotsCount=2 Degree=1 IsPeriodic=0
    g25: BSplineCurve PolesCount=2 KnotsCount=2 Degree=1 IsPeriodic=0
    g26: BSplineCurve PolesCount=2 KnotsCount=2 Degree=1 IsPeriodic=0
    g27: BSplineCurve PolesCount=2 KnotsCount=2 Degree=1 IsPeriodic=0
    g28: BSplineCurve PolesCount=2 KnotsCount=2 Degree=1 IsPeriodic=0
    g29: BSplineCurve PolesCount=2 KnotsCount=2 Degree=1 IsPeriodic=0
    g30: BSplineCurve PolesCount=2 KnotsCount=2 Degree=1 IsPeriodic=0
    g31: BSplineCurve PolesCount=2 KnotsCount=2 Degree=1 IsPeriodic=0
    g32: BSplineCurve PolesCount=2 KnotsCount=2 Degree=1 IsPeriodic=0
    g33: BSplineCurve PolesCount=2 KnotsCount=2 Degree=1 IsPeriodic=0
    g34: BSplineCurve PolesCount=2 KnotsCount=2 Degree=1 IsPeriodic=0
    g35: BSplineCurve PolesCount=2 KnotsCount=2 Degree=1 IsPeriodic=0
    g36: BSplineCurve PolesCount=2 KnotsCount=2 Degree=1 IsPeriodic=0
    g37: BSplineCurve PolesCount=2 KnotsCount=2 Degree=1 IsPeriodic=0
    g38: BSplineCurve PolesCount=2 KnotsCount=2 Degree=1 IsPeriodic=0
    g39: BSplineCurve PolesCount=2 KnotsCount=2 Degree=1 IsPeriodic=0
    g40: BSplineCurve PolesCount=2 KnotsCount=2 Degree=1 IsPeriodic=0
    g41: BSplineCurve PolesCount=2 KnotsCount=2 Degree=1 IsPeriodic=0
    g42: BSplineCurve PolesCount=2 KnotsCount=2 Degree=1 IsPeriodic=0
    g43: BSplineCurve PolesCount=2 KnotsCount=2 Degree=1 IsPeriodic=0
    g44: BSplineCurve PolesCount=2 KnotsCount=2 Degree=1 IsPeriodic=0
    g45: BSplineCurve PolesCount=2 KnotsCount=2 Degree=1 IsPeriodic=0
    g46: BSplineCurve PolesCount=2 KnotsCount=2 Degree=1 IsPeriodic=0
    g47: BSplineCurve PolesCount=2 KnotsCount=2 Degree=1 IsPeriodic=0
    g48: BSplineCurve PolesCount=2 KnotsCount=2 Degree=1 IsPeriodic=0
    g49: BSplineCurve PolesCount=2 KnotsCount=2 Degree=1 IsPeriodic=0
    g50: BSplineCurve PolesCount=2 KnotsCount=2 Degree=1 IsPeriodic=0
    g51: BSplineCurve PolesCount=2 KnotsCount=2 Degree=1 IsPeriodic=0
    g52: BSplineCurve PolesCount=2 KnotsCount=2 Degree=1 IsPeriodic=0
    g53: BSplineCurve PolesCount=2 KnotsCount=2 Degree=1 IsPeriodic=0
    g54: BSplineCurve PolesCount=2 KnotsCount=2 Degree=1 IsPeriodic=0
    g55: BSplineCurve PolesCount=2 KnotsCount=2 Degree=1 IsPeriodic=0
    g56: BSplineCurve PolesCount=2 KnotsCount=2 Degree=1 IsPeriodic=0
    g57: BSplineCurve PolesCount=2 KnotsCount=2 Degree=1 IsPeriodic=0
    g58: BSplineCurve PolesCount=2 KnotsCount=2 Degree=1 IsPeriodic=0
    g59: BSplineCurve PolesCount=2 KnotsCount=2 Degree=1 IsPeriodic=0
    g60: BSplineCurve PolesCount=2 KnotsCount=2 Degree=1 IsPeriodic=0
    g61: BSplineCurve PolesCount=2 KnotsCount=2 Degree=1 IsPeriodic=0
    g62: BSplineCurve PolesCount=2 KnotsCount=2 Degree=1 IsPeriodic=0
    g63: BSplineCurve PolesCount=2 KnotsCount=2 Degree=1 IsPeriodic=0
    g64: BSplineCurve PolesCount=2 KnotsCount=2 Degree=1 IsPeriodic=0
    g65: BSplineCurve PolesCount=2 KnotsCount=2 Degree=1 IsPeriodic=0
    g66: BSplineCurve PolesCount=2 KnotsCount=2 Degree=1 IsPeriodic=0
    g67: BSplineCurve PolesCount=2 KnotsCount=2 Degree=1 IsPeriodic=0
    g68: BSplineCurve PolesCount=2 KnotsCount=2 Degree=1 IsPeriodic=0
    g69: BSplineCurve PolesCount=2 KnotsCount=2 Degree=1 IsPeriodic=0
    g70: BSplineCurve PolesCount=2 KnotsCount=2 Degree=1 IsPeriodic=0
    g71: BSplineCurve PolesCount=2 KnotsCount=2 Degree=1 IsPeriodic=0
    g72: BSplineCurve PolesCount=2 KnotsCount=2 Degree=1 IsPeriodic=0
    g73: BSplineCurve PolesCount=2 KnotsCount=2 Degree=1 IsPeriodic=0
    g74: BSplineCurve PolesCount=2 KnotsCount=2 Degree=1 IsPeriodic=0
    g75: BSplineCurve PolesCount=2 KnotsCount=2 Degree=1 IsPeriodic=0
    g76: BSplineCurve PolesCount=2 KnotsCount=2 Degree=1 IsPeriodic=0
    g77: BSplineCurve PolesCount=2 KnotsCount=2 Degree=1 IsPeriodic=0
    g78: BSplineCurve PolesCount=2 KnotsCount=2 Degree=1 IsPeriodic=0
    g79: BSplineCurve PolesCount=2 KnotsCount=2 Degree=1 IsPeriodic=0
    g80: BSplineCurve PolesCount=2 KnotsCount=2 Degree=1 IsPeriodic=0
    g81: BSplineCurve PolesCount=2 KnotsCount=2 Degree=1 IsPeriodic=0
    g82: BSplineCurve PolesCount=2 KnotsCount=2 Degree=1 IsPeriodic=0
    g83: BSplineCurve PolesCount=2 KnotsCount=2 Degree=1 IsPeriodic=0
    g84: BSplineCurve PolesCount=2 KnotsCount=2 Degree=1 IsPeriodic=0
    g85: BSplineCurve PolesCount=2 KnotsCount=2 Degree=1 IsPeriodic=0
    g86: BSplineCurve PolesCount=2 KnotsCount=2 Degree=1 IsPeriodic=0
    g87: BSplineCurve PolesCount=2 KnotsCount=2 Degree=1 IsPeriodic=0
    g88: BSplineCurve PolesCount=2 KnotsCount=2 Degree=1 IsPeriodic=0
    g89: BSplineCurve PolesCount=2 KnotsCount=2 Degree=1 IsPeriodic=0
    g90: BSplineCurve PolesCount=2 KnotsCount=2 Degree=1 IsPeriodic=0
    g91: BSplineCurve PolesCount=2 KnotsCount=2 Degree=1 IsPeriodic=0
    g92: BSplineCurve PolesCount=2 KnotsCount=2 Degree=1 IsPeriodic=0
    g93: BSplineCurve PolesCount=2 KnotsCount=2 Degree=1 IsPeriodic=0
    g94: BSplineCurve PolesCount=2 KnotsCount=2 Degree=1 IsPeriodic=0
    g95: BSplineCurve PolesCount=2 KnotsCount=2 Degree=1 IsPeriodic=0
    g96: BSplineCurve PolesCount=2 KnotsCount=2 Degree=1 IsPeriodic=0
    g97: BSplineCurve PolesCount=2 KnotsCount=2 Degree=1 IsPeriodic=0
    g98: BSplineCurve PolesCount=2 KnotsCount=2 Degree=1 IsPeriodic=0
    g99: BSplineCurve PolesCount=2 KnotsCount=2 Degree=1 IsPeriodic=0
    g100: BSplineCurve PolesCount=2 KnotsCount=2 Degree=1 IsPeriodic=0
    g101: BSplineCurve PolesCount=2 KnotsCount=2 Degree=1 IsPeriodic=0
    g102: BSplineCurve PolesCount=2 KnotsCount=2 Degree=1 IsPeriodic=0
    g103: BSplineCurve PolesCount=2 KnotsCount=2 Degree=1 IsPeriodic=0
    g104: BSplineCurve PolesCount=2 KnotsCount=2 Degree=1 IsPeriodic=0
    g105: BSplineCurve PolesCount=2 KnotsCount=2 Degree=1 IsPeriodic=0
    g106: BSplineCurve PolesCount=2 KnotsCount=2 Degree=1 IsPeriodic=0
    g107: BSplineCurve PolesCount=2 KnotsCount=2 Degree=1 IsPeriodic=0
    g108: BSplineCurve PolesCount=2 KnotsCount=2 Degree=1 IsPeriodic=0
    g109: BSplineCurve PolesCount=2 KnotsCount=2 Degree=1 IsPeriodic=0
    g110: BSplineCurve PolesCount=2 KnotsCount=2 Degree=1 IsPeriodic=0
    g111: BSplineCurve PolesCount=2 KnotsCount=2 Degree=1 IsPeriodic=0
    g112: BSplineCurve PolesCount=2 KnotsCount=2 Degree=1 IsPeriodic=0
    g113: BSplineCurve PolesCount=2 KnotsCount=2 Degree=1 IsPeriodic=0
    g114: BSplineCurve PolesCount=2 KnotsCount=2 Degree=1 IsPeriodic=0
    g115: BSplineCurve PolesCount=2 KnotsCount=2 Degree=1 IsPeriodic=0
    g116: BSplineCurve PolesCount=2 KnotsCount=2 Degree=1 IsPeriodic=0
    g117: BSplineCurve PolesCount=2 KnotsCount=2 Degree=1 IsPeriodic=0
    g118: BSplineCurve PolesCount=2 KnotsCount=2 Degree=1 IsPeriodic=0
    g119: BSplineCurve PolesCount=2 KnotsCount=2 Degree=1 IsPeriodic=0
    g120: BSplineCurve PolesCount=2 KnotsCount=2 Degree=1 IsPeriodic=0
    g121: BSplineCurve PolesCount=2 KnotsCount=2 Degree=1 IsPeriodic=0
    g122: BSplineCurve PolesCount=2 KnotsCount=2 Degree=1 IsPeriodic=0
    g123: BSplineCurve PolesCount=2 KnotsCount=2 Degree=1 IsPeriodic=0
    g124: BSplineCurve PolesCount=2 KnotsCount=2 Degree=1 IsPeriodic=0
    g125: BSplineCurve PolesCount=2 KnotsCount=2 Degree=1 IsPeriodic=0
    g126: BSplineCurve PolesCount=2 KnotsCount=2 Degree=1 IsPeriodic=0
    g127: BSplineCurve PolesCount=2 KnotsCount=2 Degree=1 IsPeriodic=0
    g128: BSplineCurve PolesCount=2 KnotsCount=2 Degree=1 IsPeriodic=0
    g129: BSplineCurve PolesCount=2 KnotsCount=2 Degree=1 IsPeriodic=0
    g130: BSplineCurve PolesCount=2 KnotsCount=2 Degree=1 IsPeriodic=0
    g131: BSplineCurve PolesCount=2 KnotsCount=2 Degree=1 IsPeriodic=0
    g132: BSplineCurve PolesCount=2 KnotsCount=2 Degree=1 IsPeriodic=0
    g133: BSplineCurve PolesCount=2 KnotsCount=2 Degree=1 IsPeriodic=0
    g134: BSplineCurve PolesCount=2 KnotsCount=2 Degree=1 IsPeriodic=0
    g135: BSplineCurve PolesCount=2 KnotsCount=2 Degree=1 IsPeriodic=0
    g136: BSplineCurve PolesCount=2 KnotsCount=2 Degree=1 IsPeriodic=0
    g137: BSplineCurve PolesCount=2 KnotsCount=2 Degree=1 IsPeriodic=0
    g138: BSplineCurve PolesCount=2 KnotsCount=2 Degree=1 IsPeriodic=0
    g139: BSplineCurve PolesCount=2 KnotsCount=2 Degree=1 IsPeriodic=0
    g140: BSplineCurve PolesCount=2 KnotsCount=2 Degree=1 IsPeriodic=0
    g141: BSplineCurve PolesCount=2 KnotsCount=2 Degree=1 IsPeriodic=0
    g142: BSplineCurve PolesCount=2 KnotsCount=2 Degree=1 IsPeriodic=0
    g143: BSplineCurve PolesCount=2 KnotsCount=2 Degree=1 IsPeriodic=0
    g144: BSplineCurve PolesCount=2 KnotsCount=2 Degree=1 IsPeriodic=0
    g145: BSplineCurve PolesCount=2 KnotsCount=2 Degree=1 IsPeriodic=0
    g146: BSplineCurve PolesCount=2 KnotsCount=2 Degree=1 IsPeriodic=0
    g147: BSplineCurve PolesCount=2 KnotsCount=2 Degree=1 IsPeriodic=0
    g148: BSplineCurve PolesCount=2 KnotsCount=2 Degree=1 IsPeriodic=0
    g149: BSplineCurve PolesCount=2 KnotsCount=2 Degree=1 IsPeriodic=0
    g150: BSplineCurve PolesCount=2 KnotsCount=2 Degree=1 IsPeriodic=0
    g151: BSplineCurve PolesCount=2 KnotsCount=2 Degree=1 IsPeriodic=0
    g152: BSplineCurve PolesCount=2 KnotsCount=2 Degree=1 IsPeriodic=0
    g153: BSplineCurve PolesCount=2 KnotsCount=2 Degree=1 IsPeriodic=0
    g154: BSplineCurve PolesCount=2 KnotsCount=2 Degree=1 IsPeriodic=0
    g155: BSplineCurve PolesCount=2 KnotsCount=2 Degree=1 IsPeriodic=0
    g156: BSplineCurve PolesCount=2 KnotsCount=2 Degree=1 IsPeriodic=0
    g157: BSplineCurve PolesCount=2 KnotsCount=2 Degree=1 IsPeriodic=0
    g158: BSplineCurve PolesCount=2 KnotsCount=2 Degree=1 IsPeriodic=0
    g159: BSplineCurve PolesCount=2 KnotsCount=2 Degree=1 IsPeriodic=0
    g160: BSplineCurve PolesCount=2 KnotsCount=2 Degree=1 IsPeriodic=0
    g161: BSplineCurve PolesCount=2 KnotsCount=2 Degree=1 IsPeriodic=0
    g162: BSplineCurve PolesCount=2 KnotsCount=2 Degree=1 IsPeriodic=0
    g163: BSplineCurve PolesCount=2 KnotsCount=2 Degree=1 IsPeriodic=0
    g164: BSplineCurve PolesCount=2 KnotsCount=2 Degree=1 IsPeriodic=0
    g165: BSplineCurve PolesCount=2 KnotsCount=2 Degree=1 IsPeriodic=0
    g166: BSplineCurve PolesCount=2 KnotsCount=2 Degree=1 IsPeriodic=0
    g167: BSplineCurve PolesCount=2 KnotsCount=2 Degree=1 IsPeriodic=0
    g168: BSplineCurve PolesCount=2 KnotsCount=2 Degree=1 IsPeriodic=0
    g169: BSplineCurve PolesCount=2 KnotsCount=2 Degree=1 IsPeriodic=0
    g170: BSplineCurve PolesCount=2 KnotsCount=2 Degree=1 IsPeriodic=0
    g171: BSplineCurve PolesCount=2 KnotsCount=2 Degree=1 IsPeriodic=0
    g172: BSplineCurve PolesCount=2 KnotsCount=2 Degree=1 IsPeriodic=0
    g173: BSplineCurve PolesCount=2 KnotsCount=2 Degree=1 IsPeriodic=0
    g174: BSplineCurve PolesCount=2 KnotsCount=2 Degree=1 IsPeriodic=0
    g175: BSplineCurve PolesCount=2 KnotsCount=2 Degree=1 IsPeriodic=0
    g176: BSplineCurve PolesCount=2 KnotsCount=2 Degree=1 IsPeriodic=0
    g177: BSplineCurve PolesCount=2 KnotsCount=2 Degree=1 IsPeriodic=0
    g178: BSplineCurve PolesCount=2 KnotsCount=2 Degree=1 IsPeriodic=0
    g179: BSplineCurve PolesCount=2 KnotsCount=2 Degree=1 IsPeriodic=0
    g180: BSplineCurve PolesCount=2 KnotsCount=2 Degree=1 IsPeriodic=0
    g181: BSplineCurve PolesCount=2 KnotsCount=2 Degree=1 IsPeriodic=0
    g182: BSplineCurve PolesCount=2 KnotsCount=2 Degree=1 IsPeriodic=0
    g183: BSplineCurve PolesCount=2 KnotsCount=2 Degree=1 IsPeriodic=0
    g184: BSplineCurve PolesCount=2 KnotsCount=2 Degree=1 IsPeriodic=0
    g185: BSplineCurve PolesCount=2 KnotsCount=2 Degree=1 IsPeriodic=0
    g186: BSplineCurve PolesCount=2 KnotsCount=2 Degree=1 IsPeriodic=0
    g187: BSplineCurve PolesCount=2 KnotsCount=2 Degree=1 IsPeriodic=0
    g188: BSplineCurve PolesCount=2 KnotsCount=2 Degree=1 IsPeriodic=0
    g189: BSplineCurve PolesCount=2 KnotsCount=2 Degree=1 IsPeriodic=0
    g190: BSplineCurve PolesCount=2 KnotsCount=2 Degree=1 IsPeriodic=0
    g191: BSplineCurve PolesCount=2 KnotsCount=2 Degree=1 IsPeriodic=0
    g192: BSplineCurve PolesCount=2 KnotsCount=2 Degree=1 IsPeriodic=0
    g193: BSplineCurve PolesCount=2 KnotsCount=2 Degree=1 IsPeriodic=0
    g194: BSplineCurve PolesCount=2 KnotsCount=2 Degree=1 IsPeriodic=0
    g195: BSplineCurve PolesCount=2 KnotsCount=2 Degree=1 IsPeriodic=0
    g196: BSplineCurve PolesCount=2 KnotsCount=2 Degree=1 IsPeriodic=0
    g197: BSplineCurve PolesCount=2 KnotsCount=2 Degree=1 IsPeriodic=0
    g198: BSplineCurve PolesCount=2 KnotsCount=2 Degree=1 IsPeriodic=0
    g199: BSplineCurve PolesCount=2 KnotsCount=2 Degree=1 IsPeriodic=0
    g200: BSplineCurve PolesCount=2 KnotsCount=2 Degree=1 IsPeriodic=0
    g201: BSplineCurve PolesCount=2 KnotsCount=2 Degree=1 IsPeriodic=0
    g202: BSplineCurve PolesCount=2 KnotsCount=2 Degree=1 IsPeriodic=0
    g203: BSplineCurve PolesCount=2 KnotsCount=2 Degree=1 IsPeriodic=0
    g204: BSplineCurve PolesCount=2 KnotsCount=2 Degree=1 IsPeriodic=0
    g205: BSplineCurve PolesCount=2 KnotsCount=2 Degree=1 IsPeriodic=0
    g206: BSplineCurve PolesCount=2 KnotsCount=2 Degree=1 IsPeriodic=0
    g207: BSplineCurve PolesCount=2 KnotsCount=2 Degree=1 IsPeriodic=0
    g208: BSplineCurve PolesCount=2 KnotsCount=2 Degree=1 IsPeriodic=0
    g209: BSplineCurve PolesCount=2 KnotsCount=2 Degree=1 IsPeriodic=0
    g210: BSplineCurve PolesCount=2 KnotsCount=2 Degree=1 IsPeriodic=0
    g211: BSplineCurve PolesCount=2 KnotsCount=2 Degree=1 IsPeriodic=0
    g212: BSplineCurve PolesCount=2 KnotsCount=2 Degree=1 IsPeriodic=0
    g213: BSplineCurve PolesCount=2 KnotsCount=2 Degree=1 IsPeriodic=0
    g214: BSplineCurve PolesCount=2 KnotsCount=2 Degree=1 IsPeriodic=0
    g215: BSplineCurve PolesCount=2 KnotsCount=2 Degree=1 IsPeriodic=0
    g216: BSplineCurve PolesCount=2 KnotsCount=2 Degree=1 IsPeriodic=0
    g217: BSplineCurve PolesCount=2 KnotsCount=2 Degree=1 IsPeriodic=0
    g218: BSplineCurve PolesCount=2 KnotsCount=2 Degree=1 IsPeriodic=0
    g219: BSplineCurve PolesCount=2 KnotsCount=2 Degree=1 IsPeriodic=0
    g220: BSplineCurve PolesCount=2 KnotsCount=2 Degree=1 IsPeriodic=0
    g221: BSplineCurve PolesCount=2 KnotsCount=2 Degree=1 IsPeriodic=0
    g222: BSplineCurve PolesCount=2 KnotsCount=2 Degree=1 IsPeriodic=0
    g223: BSplineCurve PolesCount=2 KnotsCount=2 Degree=1 IsPeriodic=0
    g224: BSplineCurve PolesCount=2 KnotsCount=2 Degree=1 IsPeriodic=0
    g225: BSplineCurve PolesCount=2 KnotsCount=2 Degree=1 IsPeriodic=0
    g226: BSplineCurve PolesCount=2 KnotsCount=2 Degree=1 IsPeriodic=0
    g227: BSplineCurve PolesCount=2 KnotsCount=2 Degree=1 IsPeriodic=0
    g228: BSplineCurve PolesCount=2 KnotsCount=2 Degree=1 IsPeriodic=0
    g229: BSplineCurve PolesCount=2 KnotsCount=2 Degree=1 IsPeriodic=0
    g230: BSplineCurve PolesCount=2 KnotsCount=2 Degree=1 IsPeriodic=0
    g231: BSplineCurve PolesCount=2 KnotsCount=2 Degree=1 IsPeriodic=0
    g232: BSplineCurve PolesCount=2 KnotsCount=2 Degree=1 IsPeriodic=0
    g233: BSplineCurve PolesCount=2 KnotsCount=2 Degree=1 IsPeriodic=0
    g234: BSplineCurve PolesCount=2 KnotsCount=2 Degree=1 IsPeriodic=0
    g235: BSplineCurve PolesCount=2 KnotsCount=2 Degree=1 IsPeriodic=0
    g236: BSplineCurve PolesCount=2 KnotsCount=2 Degree=1 IsPeriodic=0
    g237: BSplineCurve PolesCount=2 KnotsCount=2 Degree=1 IsPeriodic=0
    g238: BSplineCurve PolesCount=2 KnotsCount=2 Degree=1 IsPeriodic=0
    g239: BSplineCurve PolesCount=2 KnotsCount=2 Degree=1 IsPeriodic=0
    g240: BSplineCurve PolesCount=2 KnotsCount=2 Degree=1 IsPeriodic=0
    g241: BSplineCurve PolesCount=2 KnotsCount=2 Degree=1 IsPeriodic=0
    g242: BSplineCurve PolesCount=2 KnotsCount=2 Degree=1 IsPeriodic=0
    g243: BSplineCurve PolesCount=2 KnotsCount=2 Degree=1 IsPeriodic=0
    g244: BSplineCurve PolesCount=2 KnotsCount=2 Degree=1 IsPeriodic=0
    g245: BSplineCurve PolesCount=2 KnotsCount=2 Degree=1 IsPeriodic=0
    g246: BSplineCurve PolesCount=2 KnotsCount=2 Degree=1 IsPeriodic=0
    g247: BSplineCurve PolesCount=2 KnotsCount=2 Degree=1 IsPeriodic=0
    g248: BSplineCurve PolesCount=2 KnotsCount=2 Degree=1 IsPeriodic=0
    g249: BSplineCurve PolesCount=2 KnotsCount=2 Degree=1 IsPeriodic=0
    g250: BSplineCurve PolesCount=2 KnotsCount=2 Degree=1 IsPeriodic=0
    g251: BSplineCurve PolesCount=2 KnotsCount=2 Degree=1 IsPeriodic=0
    g252: BSplineCurve PolesCount=2 KnotsCount=2 Degree=1 IsPeriodic=0
    g253: BSplineCurve PolesCount=2 KnotsCount=2 Degree=1 IsPeriodic=0
    g254: BSplineCurve PolesCount=2 KnotsCount=2 Degree=1 IsPeriodic=0
    g255: BSplineCurve PolesCount=2 KnotsCount=2 Degree=1 IsPeriodic=0
    g256: BSplineCurve PolesCount=2 KnotsCount=2 Degree=1 IsPeriodic=0
    g257: BSplineCurve PolesCount=2 KnotsCount=2 Degree=1 IsPeriodic=0
    g258: BSplineCurve PolesCount=2 KnotsCount=2 Degree=1 IsPeriodic=0
    g259: BSplineCurve PolesCount=2 KnotsCount=2 Degree=1 IsPeriodic=0
    g260: BSplineCurve PolesCount=2 KnotsCount=2 Degree=1 IsPeriodic=0
    g261: BSplineCurve PolesCount=2 KnotsCount=2 Degree=1 IsPeriodic=0
    g262: BSplineCurve PolesCount=2 KnotsCount=2 Degree=1 IsPeriodic=0
    g263: BSplineCurve PolesCount=2 KnotsCount=2 Degree=1 IsPeriodic=0
    g264: BSplineCurve PolesCount=2 KnotsCount=2 Degree=1 IsPeriodic=0
    g265: BSplineCurve PolesCount=2 KnotsCount=2 Degree=1 IsPeriodic=0
    g266: BSplineCurve PolesCount=2 KnotsCount=2 Degree=1 IsPeriodic=0
    g267: BSplineCurve PolesCount=2 KnotsCount=2 Degree=1 IsPeriodic=0
    g268: BSplineCurve PolesCount=2 KnotsCount=2 Degree=1 IsPeriodic=0
    g269: BSplineCurve PolesCount=2 KnotsCount=2 Degree=1 IsPeriodic=0
    g270: BSplineCurve PolesCount=2 KnotsCount=2 Degree=1 IsPeriodic=0
    g271: BSplineCurve PolesCount=2 KnotsCount=2 Degree=1 IsPeriodic=0
    g272: BSplineCurve PolesCount=2 KnotsCount=2 Degree=1 IsPeriodic=0
    g273: BSplineCurve PolesCount=2 KnotsCount=2 Degree=1 IsPeriodic=0
    g274: BSplineCurve PolesCount=2 KnotsCount=2 Degree=1 IsPeriodic=0
    g275: BSplineCurve PolesCount=2 KnotsCount=2 Degree=1 IsPeriodic=0
    g276: BSplineCurve PolesCount=2 KnotsCount=2 Degree=1 IsPeriodic=0
    g277: BSplineCurve PolesCount=2 KnotsCount=2 Degree=1 IsPeriodic=0
    g278: BSplineCurve PolesCount=2 KnotsCount=2 Degree=1 IsPeriodic=0
    g279: BSplineCurve PolesCount=2 KnotsCount=2 Degree=1 IsPeriodic=0
    g280: BSplineCurve PolesCount=2 KnotsCount=2 Degree=1 IsPeriodic=0
    g281: BSplineCurve PolesCount=2 KnotsCount=2 Degree=1 IsPeriodic=0
    g282: BSplineCurve PolesCount=2 KnotsCount=2 Degree=1 IsPeriodic=0
    g283: BSplineCurve PolesCount=2 KnotsCount=2 Degree=1 IsPeriodic=0
    g284: BSplineCurve PolesCount=2 KnotsCount=2 Degree=1 IsPeriodic=0
    g285: BSplineCurve PolesCount=2 KnotsCount=2 Degree=1 IsPeriodic=0
    g286: BSplineCurve PolesCount=2 KnotsCount=2 Degree=1 IsPeriodic=0
    g287: BSplineCurve PolesCount=2 KnotsCount=2 Degree=1 IsPeriodic=0
    g288: BSplineCurve PolesCount=2 KnotsCount=2 Degree=1 IsPeriodic=0
    g289: BSplineCurve PolesCount=2 KnotsCount=2 Degree=1 IsPeriodic=0
    g290: BSplineCurve PolesCount=2 KnotsCount=2 Degree=1 IsPeriodic=0
    g291: BSplineCurve PolesCount=2 KnotsCount=2 Degree=1 IsPeriodic=0
    g292: BSplineCurve PolesCount=2 KnotsCount=2 Degree=1 IsPeriodic=0
    g293: BSplineCurve PolesCount=2 KnotsCount=2 Degree=1 IsPeriodic=0
    g294: BSplineCurve PolesCount=2 KnotsCount=2 Degree=1 IsPeriodic=0
    g295: BSplineCurve PolesCount=2 KnotsCount=2 Degree=1 IsPeriodic=0
    g296: BSplineCurve PolesCount=2 KnotsCount=2 Degree=1 IsPeriodic=0
    g297: BSplineCurve PolesCount=2 KnotsCount=2 Degree=1 IsPeriodic=0
    g298: BSplineCurve PolesCount=2 KnotsCount=2 Degree=1 IsPeriodic=0
    g299: BSplineCurve PolesCount=2 KnotsCount=2 Degree=1 IsPeriodic=0
    g300: BSplineCurve PolesCount=2 KnotsCount=2 Degree=1 IsPeriodic=0
    g301: BSplineCurve PolesCount=2 KnotsCount=2 Degree=1 IsPeriodic=0
    g302: BSplineCurve PolesCount=2 KnotsCount=2 Degree=1 IsPeriodic=0
    g303: BSplineCurve PolesCount=2 KnotsCount=2 Degree=1 IsPeriodic=0
    g304: BSplineCurve PolesCount=2 KnotsCount=2 Degree=1 IsPeriodic=0
    g305: BSplineCurve PolesCount=2 KnotsCount=2 Degree=1 IsPeriodic=0
    g306: BSplineCurve PolesCount=2 KnotsCount=2 Degree=1 IsPeriodic=0
    g307: BSplineCurve PolesCount=2 KnotsCount=2 Degree=1 IsPeriodic=0
    g308: BSplineCurve PolesCount=2 KnotsCount=2 Degree=1 IsPeriodic=0
    g309: BSplineCurve PolesCount=2 KnotsCount=2 Degree=1 IsPeriodic=0
    g310: BSplineCurve PolesCount=2 KnotsCount=2 Degree=1 IsPeriodic=0
    g311: BSplineCurve PolesCount=2 KnotsCount=2 Degree=1 IsPeriodic=0
    g312: BSplineCurve PolesCount=2 KnotsCount=2 Degree=1 IsPeriodic=0
    g313: BSplineCurve PolesCount=2 KnotsCount=2 Degree=1 IsPeriodic=0
    g314: BSplineCurve PolesCount=2 KnotsCount=2 Degree=1 IsPeriodic=0
    g315: BSplineCurve PolesCount=2 KnotsCount=2 Degree=1 IsPeriodic=0
    g316: BSplineCurve PolesCount=2 KnotsCount=2 Degree=1 IsPeriodic=0
    g317: BSplineCurve PolesCount=2 KnotsCount=2 Degree=1 IsPeriodic=0
    g318: BSplineCurve PolesCount=2 KnotsCount=2 Degree=1 IsPeriodic=0
    g319: BSplineCurve PolesCount=2 KnotsCount=2 Degree=1 IsPeriodic=0
    g320: BSplineCurve PolesCount=2 KnotsCount=2 Degree=1 IsPeriodic=0
    g321: BSplineCurve PolesCount=2 KnotsCount=2 Degree=1 IsPeriodic=0
    g322: BSplineCurve PolesCount=2 KnotsCount=2 Degree=1 IsPeriodic=0
    g323: BSplineCurve PolesCount=2 KnotsCount=2 Degree=1 IsPeriodic=0
    g324: BSplineCurve PolesCount=2 KnotsCount=2 Degree=1 IsPeriodic=0
    g325: BSplineCurve PolesCount=2 KnotsCount=2 Degree=1 IsPeriodic=0
    g326: BSplineCurve PolesCount=2 KnotsCount=2 Degree=1 IsPeriodic=0
    g327: BSplineCurve PolesCount=2 KnotsCount=2 Degree=1 IsPeriodic=0
    g328: BSplineCurve PolesCount=2 KnotsCount=2 Degree=1 IsPeriodic=0
    g329: BSplineCurve PolesCount=2 KnotsCount=2 Degree=1 IsPeriodic=0
    g330: BSplineCurve PolesCount=2 KnotsCount=2 Degree=1 IsPeriodic=0
    g331: BSplineCurve PolesCount=2 KnotsCount=2 Degree=1 IsPeriodic=0
    g332: BSplineCurve PolesCount=2 KnotsCount=2 Degree=1 IsPeriodic=0
    g333: BSplineCurve PolesCount=2 KnotsCount=2 Degree=1 IsPeriodic=0
    g334: BSplineCurve PolesCount=2 KnotsCount=2 Degree=1 IsPeriodic=0
    g335: BSplineCurve PolesCount=2 KnotsCount=2 Degree=1 IsPeriodic=0
    g336: BSplineCurve PolesCount=2 KnotsCount=2 Degree=1 IsPeriodic=0
    g337: BSplineCurve PolesCount=2 KnotsCount=2 Degree=1 IsPeriodic=0
    g338: BSplineCurve PolesCount=2 KnotsCount=2 Degree=1 IsPeriodic=0
    g339: BSplineCurve PolesCount=2 KnotsCount=2 Degree=1 IsPeriodic=0
    g340: BSplineCurve PolesCount=2 KnotsCount=2 Degree=1 IsPeriodic=0
    g341: BSplineCurve PolesCount=2 KnotsCount=2 Degree=1 IsPeriodic=0
    g342: BSplineCurve PolesCount=2 KnotsCount=2 Degree=1 IsPeriodic=0
    g343: BSplineCurve PolesCount=2 KnotsCount=2 Degree=1 IsPeriodic=0
    g344: BSplineCurve PolesCount=2 KnotsCount=2 Degree=1 IsPeriodic=0
    g345: BSplineCurve PolesCount=2 KnotsCount=2 Degree=1 IsPeriodic=0
    g346: BSplineCurve PolesCount=2 KnotsCount=2 Degree=1 IsPeriodic=0
    g347: BSplineCurve PolesCount=2 KnotsCount=2 Degree=1 IsPeriodic=0
    g348: BSplineCurve PolesCount=2 KnotsCount=2 Degree=1 IsPeriodic=0
    g349: BSplineCurve PolesCount=2 KnotsCount=2 Degree=1 IsPeriodic=0
    g350: BSplineCurve PolesCount=2 KnotsCount=2 Degree=1 IsPeriodic=0
    g351: BSplineCurve PolesCount=2 KnotsCount=2 Degree=1 IsPeriodic=0
    g352: BSplineCurve PolesCount=2 KnotsCount=2 Degree=1 IsPeriodic=0
    g353: BSplineCurve PolesCount=2 KnotsCount=2 Degree=1 IsPeriodic=0
    g354: BSplineCurve PolesCount=2 KnotsCount=2 Degree=1 IsPeriodic=0
    g355: BSplineCurve PolesCount=2 KnotsCount=2 Degree=1 IsPeriodic=0
    g356: BSplineCurve PolesCount=2 KnotsCount=2 Degree=1 IsPeriodic=0
    g357: BSplineCurve PolesCount=2 KnotsCount=2 Degree=1 IsPeriodic=0
    g358: BSplineCurve PolesCount=2 KnotsCount=2 Degree=1 IsPeriodic=0
    g359: BSplineCurve PolesCount=2 KnotsCount=2 Degree=1 IsPeriodic=0
    g360: BSplineCurve PolesCount=2 KnotsCount=2 Degree=1 IsPeriodic=0
    g361: BSplineCurve PolesCount=2 KnotsCount=2 Degree=1 IsPeriodic=0
    g362: BSplineCurve PolesCount=2 KnotsCount=2 Degree=1 IsPeriodic=0
    g363: BSplineCurve PolesCount=2 KnotsCount=2 Degree=1 IsPeriodic=0
    g364: BSplineCurve PolesCount=2 KnotsCount=2 Degree=1 IsPeriodic=0
    g365: BSplineCurve PolesCount=2 KnotsCount=2 Degree=1 IsPeriodic=0
    g366: BSplineCurve PolesCount=2 KnotsCount=2 Degree=1 IsPeriodic=0
    g367: BSplineCurve PolesCount=2 KnotsCount=2 Degree=1 IsPeriodic=0
    g368: BSplineCurve PolesCount=2 KnotsCount=2 Degree=1 IsPeriodic=0
    g369: BSplineCurve PolesCount=2 KnotsCount=2 Degree=1 IsPeriodic=0
    g370: BSplineCurve PolesCount=2 KnotsCount=2 Degree=1 IsPeriodic=0
    g371: BSplineCurve PolesCount=2 KnotsCount=2 Degree=1 IsPeriodic=0
    g372: BSplineCurve PolesCount=2 KnotsCount=2 Degree=1 IsPeriodic=0
    g373: BSplineCurve PolesCount=2 KnotsCount=2 Degree=1 IsPeriodic=0
    g374: BSplineCurve PolesCount=2 KnotsCount=2 Degree=1 IsPeriodic=0
    g375: BSplineCurve PolesCount=2 KnotsCount=2 Degree=1 IsPeriodic=0
    g376: BSplineCurve PolesCount=2 KnotsCount=2 Degree=1 IsPeriodic=0
    g377: BSplineCurve PolesCount=2 KnotsCount=2 Degree=1 IsPeriodic=0
    g378: BSplineCurve PolesCount=2 KnotsCount=2 Degree=1 IsPeriodic=0
    g379: BSplineCurve PolesCount=2 KnotsCount=2 Degree=1 IsPeriodic=0
    g380: BSplineCurve PolesCount=2 KnotsCount=2 Degree=1 IsPeriodic=0
    g381: BSplineCurve PolesCount=2 KnotsCount=2 Degree=1 IsPeriodic=0
    g382: BSplineCurve PolesCount=2 KnotsCount=2 Degree=1 IsPeriodic=0
    g383: BSplineCurve PolesCount=2 KnotsCount=2 Degree=1 IsPeriodic=0
    g384: BSplineCurve PolesCount=2 KnotsCount=2 Degree=1 IsPeriodic=0
    g385: BSplineCurve PolesCount=2 KnotsCount=2 Degree=1 IsPeriodic=0
    g386: BSplineCurve PolesCount=2 KnotsCount=2 Degree=1 IsPeriodic=0
    g387: BSplineCurve PolesCount=2 KnotsCount=2 Degree=1 IsPeriodic=0
    g388: BSplineCurve PolesCount=2 KnotsCount=2 Degree=1 IsPeriodic=0
    g389: BSplineCurve PolesCount=2 KnotsCount=2 Degree=1 IsPeriodic=0
    g390: BSplineCurve PolesCount=2 KnotsCount=2 Degree=1 IsPeriodic=0
    g391: BSplineCurve PolesCount=2 KnotsCount=2 Degree=1 IsPeriodic=0
    g392: BSplineCurve PolesCount=2 KnotsCount=2 Degree=1 IsPeriodic=0
    g393: BSplineCurve PolesCount=2 KnotsCount=2 Degree=1 IsPeriodic=0
    g394: BSplineCurve PolesCount=2 KnotsCount=2 Degree=1 IsPeriodic=0
    g395: BSplineCurve PolesCount=2 KnotsCount=2 Degree=1 IsPeriodic=0
    g396: BSplineCurve PolesCount=2 KnotsCount=2 Degree=1 IsPeriodic=0
    g397: BSplineCurve PolesCount=2 KnotsCount=2 Degree=1 IsPeriodic=0
    g398: BSplineCurve PolesCount=2 KnotsCount=2 Degree=1 IsPeriodic=0
    g399: BSplineCurve PolesCount=2 KnotsCount=2 Degree=1 IsPeriodic=0
    ... +460 more geometry lines
  constraints (860):
    c: Coincident(g0,g1)
    c: Coincident(g1,g2)
    c: Coincident(g2,g3)
    c: Coincident(g3,g4)
    c: Coincident(g4,g5)
    c: Coincident(g5,g6)
    c: Coincident(g6,g7)
    c: Coincident(g7,g8)
    c: Coincident(g8,g9)
    c: Coincident(g9,g10)
    c: Coincident(g10,g11)
    c: Coincident(g11,g12)
    c: Coincident(g12,g13)
    c: Coincident(g13,g14)
    c: Coincident(g14,g15)
    c: Coincident(g15,g16)
    c: Coincident(g16,g17)
    c: Coincident(g17,g18)
    c: Coincident(g18,g19)
    c: Coincident(g19,g20)
    c: Coincident(g20,g21)
    c: Coincident(g21,g22)
    c: Coincident(g22,g23)
    c: Coincident(g23,g24)
    c: Coincident(g24,g25)
    c: Coincident(g25,g26)
    c: Coincident(g26,g27)
    c: Coincident(g27,g28)
    c: Coincident(g28,g29)
    c: Coincident(g29,g30)
    c: Coincident(g30,g31)
    c: Coincident(g31,g32)
    c: Coincident(g32,g33)
    c: Coincident(g33,g34)
    c: Coincident(g34,g35)
    c: Coincident(g35,g36)
    c: Coincident(g36,g37)
    c: Coincident(g37,g38)
    c: Coincident(g38,g39)
    c: Coincident(g39,g40)
    c: Coincident(g40,g41)
    c: Coincident(g41,g42)
    c: Coincident(g42,g43)
    c: Coincident(g43,g44)
    c: Coincident(g44,g45)
    c: Coincident(g45,g46)
    c: Coincident(g46,g47)
    c: Coincident(g47,g48)
    c: Coincident(g48,g49)
    c: Coincident(g49,g50)
    c: Coincident(g50,g51)
    c: Coincident(g51,g52)
    c: Coincident(g52,g53)
    c: Coincident(g53,g54)
    c: Coincident(g54,g55)
    c: Coincident(g55,g56)
    c: Coincident(g56,g57)
    c: Coincident(g57,g58)
    c: Coincident(g58,g59)
    c: Coincident(g59,g60)
    c: Coincident(g60,g61)
    c: Coincident(g61,g62)
    c: Coincident(g62,g63)
    c: Coincident(g63,g64)
    c: Coincident(g64,g65)
    c: Coincident(g65,g66)
    c: Coincident(g66,g67)
    c: Coincident(g67,g68)
    c: Coincident(g68,g69)
    c: Coincident(g69,g70)
    c: Coincident(g70,g71)
    c: Coincident(g71,g72)
    c: Coincident(g72,g73)
    c: Coincident(g73,g74)
    c: Coincident(g74,g75)
    c: Coincident(g75,g76)
    c: Coincident(g76,g77)
    c: Coincident(g77,g78)
    c: Coincident(g78,g79)
    c: Coincident(g79,g80)
    c: Coincident(g80,g81)
    c: Coincident(g81,g82)
    c: Coincident(g82,g83)
    c: Coincident(g83,g84)
    c: Coincident(g84,g85)
    c: Coincident(g85,g86)
    c: Coincident(g86,g87)
    c: Coincident(g87,g0)
    c: Coincident(g88,g89)
    c: Coincident(g89,g90)
    c: Coincident(g90,g91)
    c: Coincident(g91,g92)
    c: Coincident(g92,g93)
    c: Coincident(g93,g94)
    c: Coincident(g94,g95)
    c: Coincident(g95,g96)
    c: Coincident(g96,g97)
    c: Coincident(g97,g98)
    c: Coincident(g98,g99)
    c: Coincident(g99,g100)
    c: Coincident(g100,g101)
    c: Coincident(g101,g102)
    c: Coincident(g102,g103)
    c: Coincident(g103,g104)
    c: Coincident(g104,g105)
    c: Coincident(g105,g106)
    c: Coincident(g106,g107)
    c: Coincident(g107,g108)
    c: Coincident(g108,g109)
    c: Coincident(g109,g110)
    c: Coincident(g110,g111)
    c: Coincident(g111,g112)
    c: Coincident(g112,g113)
    c: Coincident(g113,g114)
    c: Coincident(g114,g115)
    c: Coincident(g115,g116)
    c: Coincident(g116,g117)
    c: Coincident(g117,g118)
    c: Coincident(g118,g119)
    c: Coincident(g119,g120)
    c: Coincident(g120,g121)
    c: Coincident(g121,g122)
    c: Coincident(g122,g123)
    c: Coincident(g123,g124)
    c: Coincident(g124,g125)
    c: Coincident(g125,g126)
    c: Coincident(g126,g127)
    c: Coincident(g127,g88)
    c: Coincident(g128,g129)
    c: Coincident(g129,g130)
    c: Coincident(g130,g131)
    c: Coincident(g131,g132)
    c: Coincident(g132,g133)
    c: Coincident(g133,g134)
    c: Coincident(g134,g135)
    c: Coincident(g135,g136)
    c: Coincident(g136,g137)
    c: Coincident(g137,g138)
    c: Coincident(g138,g139)
    c: Coincident(g139,g140)
    c: Coincident(g140,g141)
    c: Coincident(g141,g142)
    c: Coincident(g142,g143)
    c: Coincident(g143,g144)
    c: Coincident(g144,g145)
    c: Coincident(g145,g146)
    c: Coincident(g146,g147)
    c: Coincident(g147,g148)
    c: Coincident(g148,g149)
    c: Coincident(g149,g150)
    c: Coincident(g150,g151)
    c: Coincident(g151,g152)
    c: Coincident(g152,g153)
    c: Coincident(g153,g154)
    c: Coincident(g154,g155)
    c: Coincident(g155,g156)
    c: Coincident(g156,g157)
    c: Coincident(g157,g158)
    c: Coincident(g158,g159)
    c: Coincident(g159,g160)
    c: Coincident(g160,g161)
    c: Coincident(g161,g162)
    c: Coincident(g162,g163)
    c: Coincident(g163,g164)
    c: Coincident(g164,g165)
    c: Coincident(g165,g166)
    c: Coincident(g166,g167)
    c: Coincident(g167,g168)
    c: Coincident(g168,g169)
    c: Coincident(g169,g170)
    c: Coincident(g170,g171)
    c: Coincident(g171,g172)
    c: Coincident(g172,g173)
    c: Coincident(g173,g174)
    c: Coincident(g174,g175)
    c: Coincident(g175,g176)
    c: Coincident(g176,g177)
    c: Coincident(g177,g178)
    c: Coincident(g178,g179)
    c: Coincident(g179,g180)
    c: Coincident(g180,g181)
    c: Coincident(g181,g182)
    c: Coincident(g182,g183)
    c: Coincident(g183,g184)
    c: Coincident(g184,g185)
    c: Coincident(g185,g186)
    c: Coincident(g186,g187)
    c: Coincident(g187,g188)
    c: Coincident(g188,g189)
    c: Coincident(g189,g190)
    c: Coincident(g190,g191)
    c: Coincident(g191,g192)
    c: Coincident(g192,g193)
    c: Coincident(g193,g194)
    c: Coincident(g194,g195)
    c: Coincident(g195,g196)
    c: Coincident(g196,g197)
    c: Coincident(g197,g198)
    c: Coincident(g198,g199)
    c: Coincident(g199,g200)
    c: Coincident(g200,g201)
    c: Coincident(g201,g202)
    c: Coincident(g202,g203)
    c: Coincident(g203,g204)
    c: Coincident(g204,g205)
    c: Coincident(g205,g206)
    c: Coincident(g206,g207)
    c: Coincident(g207,g208)
    c: Coincident(g208,g209)
    c: Coincident(g209,g210)
    c: Coincident(g210,g211)
    c: Coincident(g211,g212)
    c: Coincident(g212,g213)
    c: Coincident(g213,g214)
    c: Coincident(g214,g215)
    c: Coincident(g215,g216)
    c: Coincident(g216,g217)
    c: Coincident(g217,g218)
    c: Coincident(g218,g219)
    c: Coincident(g219,g220)
    c: Coincident(g220,g221)
    c: Coincident(g221,g222)
    c: Coincident(g222,g223)
    c: Coincident(g223,g224)
    c: Coincident(g224,g225)
    c: Coincident(g225,g226)
    c: Coincident(g226,g227)
    c: Coincident(g227,g228)
    c: Coincident(g228,g229)
    c: Coincident(g229,g230)
    c: Coincident(g230,g231)
    c: Coincident(g231,g232)
    c: Coincident(g232,g233)
    c: Coincident(g233,g234)
    c: Coincident(g234,g235)
    c: Coincident(g235,g236)
    c: Coincident(g236,g237)
    c: Coincident(g237,g238)
    c: Coincident(g238,g239)
    c: Coincident(g239,g128)
    c: Coincident(g240,g241)
    c: Coincident(g241,g242)
    c: Coincident(g242,g243)
    c: Coincident(g243,g244)
    c: Coincident(g244,g245)
    c: Coincident(g245,g246)
    c: Coincident(g246,g247)
    c: Coincident(g247,g248)
    c: Coincident(g248,g249)
    c: Coincident(g249,g250)
    c: Coincident(g250,g251)
    c: Coincident(g251,g252)
    c: Coincident(g252,g253)
    c: Coincident(g253,g254)
    c: Coincident(g254,g255)
    c: Coincident(g255,g256)
    c: Coincident(g256,g257)
    c: Coincident(g257,g258)
    c: Coincident(g258,g259)
    c: Coincident(g259,g260)
    c: Coincident(g260,g261)
    c: Coincident(g261,g262)
    c: Coincident(g262,g263)
    c: Coincident(g263,g264)
    c: Coincident(g264,g265)
    c: Coincident(g265,g266)
    c: Coincident(g266,g267)
    c: Coincident(g267,g268)
    c: Coincident(g268,g269)
    c: Coincident(g269,g270)
    c: Coincident(g270,g271)
    c: Coincident(g271,g272)
    c: Coincident(g272,g273)
    c: Coincident(g273,g274)
    c: Coincident(g274,g275)
    c: Coincident(g275,g276)
    c: Coincident(g276,g277)
    c: Coincident(g277,g278)
    c: Coincident(g278,g279)
    c: Coincident(g279,g280)
    c: Coincident(g280,g281)
    c: Coincident(g281,g282)
    c: Coincident(g282,g283)
    c: Coincident(g283,g284)
    c: Coincident(g284,g285)
    c: Coincident(g285,g286)
    c: Coincident(g286,g287)
    c: Coincident(g287,g240)
    c: Coincident(g288,g289)
    c: Coincident(g289,g290)
    c: Coincident(g290,g291)
    c: Coincident(g291,g292)
    c: Coincident(g292,g293)
    c: Coincident(g293,g294)
    c: Coincident(g294,g295)
    c: Coincident(g295,g296)
    c: Coincident(g296,g297)
    c: Coincident(g297,g298)
    c: Coincident(g298,g299)
    c: Coincident(g299,g300)
    c: Coincident(g300,g301)
    c: Coincident(g301,g302)
    c: Coincident(g302,g303)
    c: Coincident(g303,g304)
    c: Coincident(g304,g305)
    c: Coincident(g305,g306)
    c: Coincident(g306,g307)
    c: Coincident(g307,g308)
    c: Coincident(g308,g309)
    c: Coincident(g309,g310)
    c: Coincident(g310,g311)
    c: Coincident(g311,g288)
    c: Coincident(g312,g313)
    c: Coincident(g313,g314)
    c: Coincident(g314,g315)
    c: Coincident(g315,g316)
    c: Coincident(g316,g317)
    c: Coincident(g317,g318)
    c: Coincident(g318,g319)
    c: Coincident(g319,g320)
    c: Coincident(g320,g321)
    c: Coincident(g321,g322)
    c: Coincident(g322,g323)
    c: Coincident(g323,g324)
    c: Coincident(g324,g325)
    c: Coincident(g325,g326)
    c: Coincident(g326,g327)
    c: Coincident(g327,g312)
    c: Coincident(g328,g329)
    c: Coincident(g329,g330)
    c: Coincident(g330,g331)
    c: Coincident(g331,g332)
    c: Coincident(g332,g333)
    c: Coincident(g333,g334)
    c: Coincident(g334,g335)
    c: Coincident(g335,g336)
    c: Coincident(g336,g337)
    c: Coincident(g337,g338)
    c: Coincident(g338,g339)
    c: Coincident(g339,g340)
    c: Coincident(g340,g341)
    c: Coincident(g341,g342)
    c: Coincident(g342,g343)
    c: Coincident(g343,g344)
    c: Coincident(g344,g345)
    c: Coincident(g345,g346)
    c: Coincident(g346,g347)
    c: Coincident(g347,g348)
    c: Coincident(g348,g349)
    c: Coincident(g349,g350)
    c: Coincident(g350,g351)
    c: Coincident(g351,g352)
    c: Coincident(g352,g353)
    c: Coincident(g353,g354)
    c: Coincident(g354,g355)
    c: Coincident(g355,g356)
    c: Coincident(g356,g357)
    c: Coincident(g357,g358)
    c: Coincident(g358,g359)
    c: Coincident(g359,g360)
    c: Coincident(g360,g361)
    c: Coincident(g361,g362)
    c: Coincident(g362,g363)
    c: Coincident(g363,g364)
    c: Coincident(g364,g365)
    c: Coincident(g365,g366)
    c: Coincident(g366,g367)
    c: Coincident(g367,g368)
    c: Coincident(g368,g369)
    c: Coincident(g369,g370)
    c: Coincident(g370,g371)
    c: Coincident(g371,g372)
    c: Coincident(g372,g373)
    c: Coincident(g373,g374)
    c: Coincident(g374,g375)
    c: Coincident(g375,g376)
    c: Coincident(g376,g377)
    c: Coincident(g377,g378)
    c: Coincident(g378,g379)
    c: Coincident(g379,g380)
    c: Coincident(g380,g381)
    c: Coincident(g381,g382)
    c: Coincident(g382,g383)
    c: Coincident(g383,g384)
    c: Coincident(g384,g385)
    c: Coincident(g385,g386)
    c: Coincident(g386,g387)
    c: Coincident(g387,g388)
    c: Coincident(g388,g389)
    c: Coincident(g389,g390)
    c: Coincident(g390,g391)
    c: Coincident(g391,g392)
    c: Coincident(g392,g393)
    c: Coincident(g393,g394)
    c: Coincident(g394,g395)
    c: Coincident(g395,g396)
    c: Coincident(g396,g397)
    c: Coincident(g397,g398)
    c: Coincident(g398,g399)
    c: Coincident(g399,g328)
    c: Coincident(g400,g401)
    c: Coincident(g401,g402)
    c: Coincident(g402,g403)
    c: Coincident(g403,g404)
    c: Coincident(g404,g405)
    c: Coincident(g405,g406)
    c: Coincident(g406,g407)
    c: Coincident(g407,g408)
    c: Coincident(g408,g409)
    c: Coincident(g409,g410)
    c: Coincident(g410,g411)
    c: Coincident(g411,g412)
    c: Coincident(g412,g413)
    c: Coincident(g413,g414)
    c: Coincident(g414,g415)
    c: Coincident(g415,g416)
    c: Coincident(g416,g417)
    c: Coincident(g417,g418)
    c: Coincident(g418,g419)
    c: Coincident(g419,g420)
    c: Coincident(g420,g421)
    c: Coincident(g421,g422)
    c: Coincident(g422,g423)
    c: Coincident(g423,g400)
    c: Coincident(g424,g425)
    c: Coincident(g425,g426)
    c: Coincident(g426,g427)
    c: Coincident(g427,g428)
    c: Coincident(g428,g429)
    c: Coincident(g429,g430)
    c: Coincident(g430,g431)
    c: Coincident(g431,g432)
    c: Coincident(g432,g433)
    c: Coincident(g433,g434)
    c: Coincident(g434,g435)
    c: Coincident(g435,g436)
    c: Coincident(g436,g437)
    c: Coincident(g437,g438)
    c: Coincident(g438,g439)
    c: Coincident(g439,g440)
    c: Coincident(g440,g441)
    c: Coincident(g441,g442)
    c: Coincident(g442,g443)
    c: Coincident(g443,g444)
    c: Coincident(g444,g445)
    c: Coincident(g445,g446)
    c: Coincident(g446,g447)
    c: Coincident(g447,g448)
    c: Coincident(g448,g449)
    c: Coincident(g449,g450)
    c: Coincident(g450,g451)
    c: Coincident(g451,g452)
    c: Coincident(g452,g453)
    c: Coincident(g453,g454)
    c: Coincident(g454,g455)
    c: Coincident(g455,g456)
    c: Coincident(g456,g457)
    c: Coincident(g457,g458)
    c: Coincident(g458,g459)
    c: Coincident(g459,g460)
    c: Coincident(g460,g461)
    c: Coincident(g461,g462)
    c: Coincident(g462,g463)
    c: Coincident(g463,g464)
    c: Coincident(g464,g465)
    c: Coincident(g465,g466)
    c: Coincident(g466,g467)
    c: Coincident(g467,g468)
    c: Coincident(g468,g469)
    c: Coincident(g469,g470)
    c: Coincident(g470,g471)
    c: Coincident(g471,g472)
    c: Coincident(g472,g473)
    c: Coincident(g473,g474)
    c: Coincident(g474,g475)
    c: Coincident(g475,g476)
    c: Coincident(g476,g477)
    c: Coincident(g477,g478)
    c: Coincident(g478,g479)
    c: Coincident(g479,g424)
    c: Coincident(g480,g481)
    c: Coincident(g481,g482)
    c: Coincident(g482,g483)
    c: Coincident(g483,g484)
    c: Coincident(g484,g485)
    c: Coincident(g485,g486)
    c: Coincident(g486,g487)
    c: Coincident(g487,g488)
    c: Coincident(g488,g489)
    c: Coincident(g489,g490)
    c: Coincident(g490,g491)
    c: Coincident(g491,g492)
    c: Coincident(g492,g493)
    c: Coincident(g493,g494)
    c: Coincident(g494,g495)
    c: Coincident(g495,g480)
    c: Coincident(g496,g497)
    c: Coincident(g497,g498)
    c: Coincident(g498,g499)
    c: Coincident(g499,g500)
    c: Coincident(g500,g501)
    c: Coincident(g501,g502)
    c: Coincident(g502,g503)
    c: Coincident(g503,g504)
    c: Coincident(g504,g505)
    c: Coincident(g505,g506)
    c: Coincident(g506,g507)
    c: Coincident(g507,g508)
    c: Coincident(g508,g509)
    c: Coincident(g509,g510)
    c: Coincident(g510,g511)
    c: Coincident(g511,g512)
    c: Coincident(g512,g513)
    c: Coincident(g513,g514)
    c: Coincident(g514,g515)
    c: Coincident(g515,g516)
    c: Coincident(g516,g517)
    c: Coincident(g517,g518)
    c: Coincident(g518,g519)
    c: Coincident(g519,g520)
    c: Coincident(g520,g521)
    c: Coincident(g521,g522)
    c: Coincident(g522,g523)
    c: Coincident(g523,g524)
    c: Coincident(g524,g525)
    c: Coincident(g525,g526)
    c: Coincident(g526,g527)
    c: Coincident(g527,g528)
    c: Coincident(g528,g529)
    c: Coincident(g529,g530)
    c: Coincident(g530,g531)
    c: Coincident(g531,g532)
    c: Coincident(g532,g533)
    c: Coincident(g533,g534)
    c: Coincident(g534,g535)
    c: Coincident(g535,g496)
    c: Coincident(g536,g537)
    c: Coincident(g537,g538)
    c: Coincident(g538,g539)
    c: Coincident(g539,g540)
    c: Coincident(g540,g541)
    c: Coincident(g541,g542)
    c: Coincident(g542,g543)
    c: Coincident(g543,g544)
    c: Coincident(g544,g545)
    c: Coincident(g545,g546)
    c: Coincident(g546,g547)
    c: Coincident(g547,g548)
    c: Coincident(g548,g549)
    c: Coincident(g549,g550)
    c: Coincident(g550,g551)
    c: Coincident(g551,g552)
    c: Coincident(g552,g553)
    c: Coincident(g553,g554)
    c: Coincident(g554,g555)
    c: Coincident(g555,g556)
    c: Coincident(g556,g557)
    c: Coincident(g557,g558)
    c: Coincident(g558,g559)
    c: Coincident(g559,g560)
    c: Coincident(g560,g561)
    c: Coincident(g561,g562)
    c: Coincident(g562,g563)
    c: Coincident(g563,g564)
    c: Coincident(g564,g565)
    c: Coincident(g565,g566)
    c: Coincident(g566,g567)
    c: Coincident(g567,g568)
    c: Coincident(g568,g569)
    c: Coincident(g569,g570)
    c: Coincident(g570,g571)
    c: Coincident(g571,g572)
    c: Coincident(g572,g573)
    c: Coincident(g573,g574)
    c: Coincident(g574,g575)
    c: Coincident(g575,g536)
    c: Coincident(g576,g577)
    c: Coincident(g577,g578)
    c: Coincident(g578,g579)
    c: Coincident(g579,g580)
    c: Coincident(g580,g581)
    c: Coincident(g581,g582)
    c: Coincident(g582,g583)
    c: Coincident(g583,g584)
    c: Coincident(g584,g585)
    c: Coincident(g585,g586)
    c: Coincident(g586,g587)
    c: Coincident(g587,g576)
    c: Coincident(g588,g589)
    c: Coincident(g589,g590)
    c: Coincident(g590,g591)
    c: Coincident(g591,g592)
    c: Coincident(g592,g593)
    c: Coincident(g593,g594)
    c: Coincident(g594,g595)
    c: Coincident(g595,g596)
    c: Coincident(g596,g597)
    c: Coincident(g597,g598)
    c: Coincident(g598,g599)
    c: Coincident(g599,g600)
    c: Coincident(g600,g601)
    c: Coincident(g601,g602)
    c: Coincident(g602,g603)
    c: Coincident(g603,g604)
    c: Coincident(g604,g605)
    c: Coincident(g605,g606)
    c: Coincident(g606,g607)
    c: Coincident(g607,g608)
    c: Coincident(g608,g609)
    c: Coincident(g609,g610)
    c: Coincident(g610,g611)
    c: Coincident(g611,g612)
    c: Coincident(g612,g613)
    c: Coincident(g613,g614)
    c: Coincident(g614,g615)
    c: Coincident(g615,g616)
    c: Coincident(g616,g617)
    c: Coincident(g617,g618)
    c: Coincident(g618,g619)
    c: Coincident(g619,g620)
    c: Coincident(g620,g621)
    c: Coincident(g621,g622)
    c: Coincident(g622,g623)
    c: Coincident(g623,g624)
    c: Coincident(g624,g625)
    c: Coincident(g625,g626)
    c: Coincident(g626,g627)
    c: Coincident(g627,g628)
    c: Coincident(g628,g629)
    c: Coincident(g629,g630)
    c: Coincident(g630,g631)
    c: Coincident(g631,g632)
    c: Coincident(g632,g633)
    c: Coincident(g633,g634)
    c: Coincident(g634,g635)
    c: Coincident(g635,g636)
    c: Coincident(g636,g637)
    c: Coincident(g637,g638)
    c: Coincident(g638,g639)
    c: Coincident(g639,g640)
    c: Coincident(g640,g641)
    c: Coincident(g641,g642)
    c: Coincident(g642,g643)
    c: Coincident(g643,g644)
    c: Coincident(g644,g645)
    c: Coincident(g645,g646)
    c: Coincident(g646,g647)
    c: Coincident(g647,g648)
    c: Coincident(g648,g649)
    c: Coincident(g649,g650)
    c: Coincident(g650,g651)
    c: Coincident(g651,g652)
    c: Coincident(g652,g653)
    c: Coincident(g653,g654)
    c: Coincident(g654,g655)
    c: Coincident(g655,g656)
    c: Coincident(g656,g657)
    c: Coincident(g657,g658)
    c: Coincident(g658,g659)
    c: Coincident(g659,g660)
    c: Coincident(g660,g661)
    c: Coincident(g661,g662)
    c: Coincident(g662,g663)
    c: Coincident(g663,g664)
    c: Coincident(g664,g665)
    c: Coincident(g665,g666)
    c: Coincident(g666,g667)
    c: Coincident(g667,g668)
    c: Coincident(g668,g669)
    c: Coincident(g669,g670)
    c: Coincident(g670,g671)
    c: Coincident(g671,g672)
    c: Coincident(g672,g673)
    c: Coincident(g673,g674)
    c: Coincident(g674,g675)
    c: Coincident(g675,g588)
    c: Coincident(g676,g677)
    c: Coincident(g677,g678)
    c: Coincident(g678,g679)
    c: Coincident(g679,g680)
    c: Coincident(g680,g681)
    c: Coincident(g681,g682)
    c: Coincident(g682,g683)
    c: Coincident(g683,g684)
    c: Coincident(g684,g685)
    c: Coincident(g685,g686)
    c: Coincident(g686,g687)
    c: Coincident(g687,g688)
    c: Coincident(g688,g689)
    c: Coincident(g689,g690)
    c: Coincident(g690,g691)
    c: Coincident(g691,g676)
    c: Coincident(g692,g693)
    c: Coincident(g693,g694)
    c: Coincident(g694,g695)
    c: Coincident(g695,g696)
    c: Coincident(g696,g697)
    c: Coincident(g697,g698)
    c: Coincident(g698,g699)
    c: Coincident(g699,g700)
    c: Coincident(g700,g701)
    c: Coincident(g701,g702)
    c: Coincident(g702,g703)
    c: Coincident(g703,g704)
    c: Coincident(g704,g705)
    c: Coincident(g705,g706)
    c: Coincident(g706,g707)
    c: Coincident(g707,g708)
    c: Coincident(g708,g709)
    c: Coincident(g709,g710)
    c: Coincident(g710,g711)
    c: Coincident(g711,g712)
    c: Coincident(g712,g713)
    c: Coincident(g713,g714)
    c: Coincident(g714,g715)
    c: Coincident(g715,g716)
    c: Coincident(g716,g717)
    c: Coincident(g717,g718)
    c: Coincident(g718,g719)
    c: Coincident(g719,g720)
    c: Coincident(g720,g721)
    c: Coincident(g721,g722)
    c: Coincident(g722,g723)
    c: Coincident(g723,g724)
    c: Coincident(g724,g725)
    c: Coincident(g725,g726)
    c: Coincident(g726,g727)
    c: Coincident(g727,g728)
    c: Coincident(g728,g729)
    c: Coincident(g729,g730)
    c: Coincident(g730,g731)
    c: Coincident(g731,g692)
    c: Coincident(g732,g733)
    c: Coincident(g733,g734)
    c: Coincident(g734,g735)
    c: Coincident(g735,g736)
    c: Coincident(g736,g737)
    c: Coincident(g737,g738)
    c: Coincident(g738,g739)
    c: Coincident(g739,g740)
    c: Coincident(g740,g741)
    c: Coincident(g741,g742)
    c: Coincident(g742,g743)
    c: Coincident(g743,g744)
    c: Coincident(g744,g745)
    c: Coincident(g745,g746)
    c: Coincident(g746,g747)
    c: Coincident(g747,g748)
    c: Coincident(g748,g749)
    c: Coincident(g749,g750)
    c: Coincident(g750,g751)
    c: Coincident(g751,g752)
    c: Coincident(g752,g753)
    c: Coincident(g753,g754)
    c: Coincident(g754,g755)
    c: Coincident(g755,g756)
    c: Coincident(g756,g757)
    c: Coincident(g757,g758)
    c: Coincident(g758,g759)
    c: Coincident(g759,g760)
    c: Coincident(g760,g761)
    c: Coincident(g761,g762)
    c: Coincident(g762,g763)
    c: Coincident(g763,g732)
    c: Coincident(g764,g765)
    c: Coincident(g765,g766)
    c: Coincident(g766,g767)
    c: Coincident(g767,g768)
    c: Coincident(g768,g769)
    c: Coincident(g769,g770)
    c: Coincident(g770,g771)
    c: Coincident(g771,g772)
    c: Coincident(g772,g773)
    c: Coincident(g773,g774)
    c: Coincident(g774,g775)
    c: Coincident(g775,g776)
    c: Coincident(g776,g777)
    c: Coincident(g777,g778)
    c: Coincident(g778,g779)
    c: Coincident(g779,g780)
    c: Coincident(g780,g781)
    c: Coincident(g781,g782)
    c: Coincident(g782,g783)
    c: Coincident(g783,g784)
    c: Coincident(g784,g785)
    c: Coincident(g785,g786)
    c: Coincident(g786,g787)
    c: Coincident(g787,g764)
    c: Coincident(g788,g789)
    c: Coincident(g789,g790)
    c: Coincident(g790,g791)
    c: Coincident(g791,g792)
    c: Coincident(g792,g793)
    c: Coincident(g793,g794)
    c: Coincident(g794,g795)
    c: Coincident(g795,g796)
    c: Coincident(g796,g797)
    c: Coincident(g797,g798)
    c: Coincident(g798,g799)
    c: Coincident(g799,g800)
    c: Coincident(g800,g801)
    c: Coincident(g801,g802)
    c: Coincident(g802,g803)
    c: Coincident(g803,g804)
    c: Coincident(g804,g805)
    c: Coincident(g805,g806)
    c: Coincident(g806,g807)
    c: Coincident(g807,g808)
    c: Coincident(g808,g809)
    c: Coincident(g809,g810)
    c: Coincident(g810,g811)
    c: Coincident(g811,g812)
    c: Coincident(g812,g813)
    c: Coincident(g813,g814)
    c: Coincident(g814,g815)
    c: Coincident(g815,g816)
    c: Coincident(g816,g817)
    c: Coincident(g817,g818)
    c: Coincident(g818,g819)
    c: Coincident(g819,g820)
    c: Coincident(g820,g821)
    c: Coincident(g821,g822)
    c: Coincident(g822,g823)
    c: Coincident(g823,g824)
    c: Coincident(g824,g825)
    c: Coincident(g825,g826)
    c: Coincident(g826,g827)
    c: Coincident(g827,g828)
    c: Coincident(g828,g829)
    c: Coincident(g829,g830)
    c: Coincident(g830,g831)
    c: Coincident(g831,g832)
    c: Coincident(g832,g833)
    c: Coincident(g833,g834)
    c: Coincident(g834,g835)
    c: Coincident(g835,g836)
    c: Coincident(g836,g837)
    c: Coincident(g837,g838)
    c: Coincident(g838,g839)
    c: Coincident(g839,g840)
    c: Coincident(g840,g841)
    c: Coincident(g841,g842)
    c: Coincident(g842,g843)
    c: Coincident(g843,g844)
    c: Coincident(g844,g845)
    c: Coincident(g845,g846)
    c: Coincident(g846,g847)
    c: Coincident(g847,g848)
    c: Coincident(g848,g849)
    c: Coincident(g849,g850)
    c: Coincident(g850,g851)
    c: Coincident(g851,g852)
    c: Coincident(g852,g853)
    c: Coincident(g853,g854)
    c: Coincident(g854,g855)
    c: Coincident(g855,g856)
    c: Coincident(g856,g857)
    c: Coincident(g857,g858)
    c: Coincident(g858,g859)
    c: Coincident(g859,g788)
FEATURE [PartDesign::Pocket] Pocket001
  BaseFeature = -> Fillet001
  Direction = (0,0,1)
  Length = 0
  Length2 = 5
  Offset = 0.5
  Profile = -> Sketch021
  ReferenceAxis = -> Sketch021 [N_Axis]
  Type = 3
  UpToFace = -> Fillet001 [Face51]
FEATURE [PartDesign::Body] Body009  label="x3 Shelf"
  BaseFeature = -> ShapeBinder
  Group = -> [Clone007,Sketch002,Pad002,Sketch011,Pad011,Chamfer002,Fillet001,Sketch021,Pocket001]
  Origin = -> Origin012
  Placement = pos=(0,24,0) rot=(0,0,1;0rad)
  Tip = -> Pocket001
FEATURE [Sketcher::SketchObject] Sketch022  label="16 Bit VS003"
  FullyConstrained = false
  Placement = pos=(8.14,14,-4) rot=(1,0,0;3.14159rad)
  sketch-geometry (860):
    g0: BSplineCurve PolesCount=2 KnotsCount=2 Degree=1 IsPeriodic=0
    g1: BSplineCurve PolesCount=2 KnotsCount=2 Degree=1 IsPeriodic=0
    g2: BSplineCurve PolesCount=2 KnotsCount=2 Degree=1 IsPeriodic=0
    g3: BSplineCurve PolesCount=2 KnotsCount=2 Degree=1 IsPeriodic=0
    g4: BSplineCurve PolesCount=2 KnotsCount=2 Degree=1 IsPeriodic=0
    g5: BSplineCurve PolesCount=2 KnotsCount=2 Degree=1 IsPeriodic=0
    g6: BSplineCurve PolesCount=2 KnotsCount=2 Degree=1 IsPeriodic=0
    g7: BSplineCurve PolesCount=2 KnotsCount=2 Degree=1 IsPeriodic=0
    g8: BSplineCurve PolesCount=2 KnotsCount=2 Degree=1 IsPeriodic=0
    g9: BSplineCurve PolesCount=2 KnotsCount=2 Degree=1 IsPeriodic=0
    g10: BSplineCurve PolesCount=2 KnotsCount=2 Degree=1 IsPeriodic=0
    g11: BSplineCurve PolesCount=2 KnotsCount=2 Degree=1 IsPeriodic=0
    g12: BSplineCurve PolesCount=2 KnotsCount=2 Degree=1 IsPeriodic=0
    g13: BSplineCurve PolesCount=2 KnotsCount=2 Degree=1 IsPeriodic=0
    g14: BSplineCurve PolesCount=2 KnotsCount=2 Degree=1 IsPeriodic=0
    g15: BSplineCurve PolesCount=2 KnotsCount=2 Degree=1 IsPeriodic=0
    g16: BSplineCurve PolesCount=2 KnotsCount=2 Degree=1 IsPeriodic=0
    g17: BSplineCurve PolesCount=2 KnotsCount=2 Degree=1 IsPeriodic=0
    g18: BSplineCurve PolesCount=2 KnotsCount=2 Degree=1 IsPeriodic=0
    g19: BSplineCurve PolesCount=2 KnotsCount=2 Degree=1 IsPeriodic=0
    g20: BSplineCurve PolesCount=2 KnotsCount=2 Degree=1 IsPeriodic=0
    g21: BSplineCurve PolesCount=2 KnotsCount=2 Degree=1 IsPeriodic=0
    g22: BSplineCurve PolesCount=2 KnotsCount=2 Degree=1 IsPeriodic=0
    g23: BSplineCurve PolesCount=2 KnotsCount=2 Degree=1 IsPeriodic=0
    g24: BSplineCurve PolesCount=2 KnotsCount=2 Degree=1 IsPeriodic=0
    g25: BSplineCurve PolesCount=2 KnotsCount=2 Degree=1 IsPeriodic=0
    g26: BSplineCurve PolesCount=2 KnotsCount=2 Degree=1 IsPeriodic=0
    g27: BSplineCurve PolesCount=2 KnotsCount=2 Degree=1 IsPeriodic=0
    g28: BSplineCurve PolesCount=2 KnotsCount=2 Degree=1 IsPeriodic=0
    g29: BSplineCurve PolesCount=2 KnotsCount=2 Degree=1 IsPeriodic=0
    g30: BSplineCurve PolesCount=2 KnotsCount=2 Degree=1 IsPeriodic=0
    g31: BSplineCurve PolesCount=2 KnotsCount=2 Degree=1 IsPeriodic=0
    g32: BSplineCurve PolesCount=2 KnotsCount=2 Degree=1 IsPeriodic=0
    g33: BSplineCurve PolesCount=2 KnotsCount=2 Degree=1 IsPeriodic=0
    g34: BSplineCurve PolesCount=2 KnotsCount=2 Degree=1 IsPeriodic=0
    g35: BSplineCurve PolesCount=2 KnotsCount=2 Degree=1 IsPeriodic=0
    g36: BSplineCurve PolesCount=2 KnotsCount=2 Degree=1 IsPeriodic=0
    g37: BSplineCurve PolesCount=2 KnotsCount=2 Degree=1 IsPeriodic=0
    g38: BSplineCurve PolesCount=2 KnotsCount=2 Degree=1 IsPeriodic=0
    g39: BSplineCurve PolesCount=2 KnotsCount=2 Degree=1 IsPeriodic=0
    g40: BSplineCurve PolesCount=2 KnotsCount=2 Degree=1 IsPeriodic=0
    g41: BSplineCurve PolesCount=2 KnotsCount=2 Degree=1 IsPeriodic=0
    g42: BSplineCurve PolesCount=2 KnotsCount=2 Degree=1 IsPeriodic=0
    g43: BSplineCurve PolesCount=2 KnotsCount=2 Degree=1 IsPeriodic=0
    g44: BSplineCurve PolesCount=2 KnotsCount=2 Degree=1 IsPeriodic=0
    g45: BSplineCurve PolesCount=2 KnotsCount=2 Degree=1 IsPeriodic=0
    g46: BSplineCurve PolesCount=2 KnotsCount=2 Degree=1 IsPeriodic=0
    g47: BSplineCurve PolesCount=2 KnotsCount=2 Degree=1 IsPeriodic=0
    g48: BSplineCurve PolesCount=2 KnotsCount=2 Degree=1 IsPeriodic=0
    g49: BSplineCurve PolesCount=2 KnotsCount=2 Degree=1 IsPeriodic=0
    g50: BSplineCurve PolesCount=2 KnotsCount=2 Degree=1 IsPeriodic=0
    g51: BSplineCurve PolesCount=2 KnotsCount=2 Degree=1 IsPeriodic=0
    g52: BSplineCurve PolesCount=2 KnotsCount=2 Degree=1 IsPeriodic=0
    g53: BSplineCurve PolesCount=2 KnotsCount=2 Degree=1 IsPeriodic=0
    g54: BSplineCurve PolesCount=2 KnotsCount=2 Degree=1 IsPeriodic=0
    g55: BSplineCurve PolesCount=2 KnotsCount=2 Degree=1 IsPeriodic=0
    g56: BSplineCurve PolesCount=2 KnotsCount=2 Degree=1 IsPeriodic=0
    g57: BSplineCurve PolesCount=2 KnotsCount=2 Degree=1 IsPeriodic=0
    g58: BSplineCurve PolesCount=2 KnotsCount=2 Degree=1 IsPeriodic=0
    g59: BSplineCurve PolesCount=2 KnotsCount=2 Degree=1 IsPeriodic=0
    g60: BSplineCurve PolesCount=2 KnotsCount=2 Degree=1 IsPeriodic=0
    g61: BSplineCurve PolesCount=2 KnotsCount=2 Degree=1 IsPeriodic=0
    g62: BSplineCurve PolesCount=2 KnotsCount=2 Degree=1 IsPeriodic=0
    g63: BSplineCurve PolesCount=2 KnotsCount=2 Degree=1 IsPeriodic=0
    g64: BSplineCurve PolesCount=2 KnotsCount=2 Degree=1 IsPeriodic=0
    g65: BSplineCurve PolesCount=2 KnotsCount=2 Degree=1 IsPeriodic=0
    g66: BSplineCurve PolesCount=2 KnotsCount=2 Degree=1 IsPeriodic=0
    g67: BSplineCurve PolesCount=2 KnotsCount=2 Degree=1 IsPeriodic=0
    g68: BSplineCurve PolesCount=2 KnotsCount=2 Degree=1 IsPeriodic=0
    g69: BSplineCurve PolesCount=2 KnotsCount=2 Degree=1 IsPeriodic=0
    g70: BSplineCurve PolesCount=2 KnotsCount=2 Degree=1 IsPeriodic=0
    g71: BSplineCurve PolesCount=2 KnotsCount=2 Degree=1 IsPeriodic=0
    g72: BSplineCurve PolesCount=2 KnotsCount=2 Degree=1 IsPeriodic=0
    g73: BSplineCurve PolesCount=2 KnotsCount=2 Degree=1 IsPeriodic=0
    g74: BSplineCurve PolesCount=2 KnotsCount=2 Degree=1 IsPeriodic=0
    g75: BSplineCurve PolesCount=2 KnotsCount=2 Degree=1 IsPeriodic=0
    g76: BSplineCurve PolesCount=2 KnotsCount=2 Degree=1 IsPeriodic=0
    g77: BSplineCurve PolesCount=2 KnotsCount=2 Degree=1 IsPeriodic=0
    g78: BSplineCurve PolesCount=2 KnotsCount=2 Degree=1 IsPeriodic=0
    g79: BSplineCurve PolesCount=2 KnotsCount=2 Degree=1 IsPeriodic=0
    g80: BSplineCurve PolesCount=2 KnotsCount=2 Degree=1 IsPeriodic=0
    g81: BSplineCurve PolesCount=2 KnotsCount=2 Degree=1 IsPeriodic=0
    g82: BSplineCurve PolesCount=2 KnotsCount=2 Degree=1 IsPeriodic=0
    g83: BSplineCurve PolesCount=2 KnotsCount=2 Degree=1 IsPeriodic=0
    g84: BSplineCurve PolesCount=2 KnotsCount=2 Degree=1 IsPeriodic=0
    g85: BSplineCurve PolesCount=2 KnotsCount=2 Degree=1 IsPeriodic=0
    g86: BSplineCurve PolesCount=2 KnotsCount=2 Degree=1 IsPeriodic=0
    g87: BSplineCurve PolesCount=2 KnotsCount=2 Degree=1 IsPeriodic=0
    g88: BSplineCurve PolesCount=2 KnotsCount=2 Degree=1 IsPeriodic=0
    g89: BSplineCurve PolesCount=2 KnotsCount=2 Degree=1 IsPeriodic=0
    g90: BSplineCurve PolesCount=2 KnotsCount=2 Degree=1 IsPeriodic=0
    g91: BSplineCurve PolesCount=2 KnotsCount=2 Degree=1 IsPeriodic=0
    g92: BSplineCurve PolesCount=2 KnotsCount=2 Degree=1 IsPeriodic=0
    g93: BSplineCurve PolesCount=2 KnotsCount=2 Degree=1 IsPeriodic=0
    g94: BSplineCurve PolesCount=2 KnotsCount=2 Degree=1 IsPeriodic=0
    g95: BSplineCurve PolesCount=2 KnotsCount=2 Degree=1 IsPeriodic=0
    g96: BSplineCurve PolesCount=2 KnotsCount=2 Degree=1 IsPeriodic=0
    g97: BSplineCurve PolesCount=2 KnotsCount=2 Degree=1 IsPeriodic=0
    g98: BSplineCurve PolesCount=2 KnotsCount=2 Degree=1 IsPeriodic=0
    g99: BSplineCurve PolesCount=2 KnotsCount=2 Degree=1 IsPeriodic=0
    g100: BSplineCurve PolesCount=2 KnotsCount=2 Degree=1 IsPeriodic=0
    g101: BSplineCurve PolesCount=2 KnotsCount=2 Degree=1 IsPeriodic=0
    g102: BSplineCurve PolesCount=2 KnotsCount=2 Degree=1 IsPeriodic=0
    g103: BSplineCurve PolesCount=2 KnotsCount=2 Degree=1 IsPeriodic=0
    g104: BSplineCurve PolesCount=2 KnotsCount=2 Degree=1 IsPeriodic=0
    g105: BSplineCurve PolesCount=2 KnotsCount=2 Degree=1 IsPeriodic=0
    g106: BSplineCurve PolesCount=2 KnotsCount=2 Degree=1 IsPeriodic=0
    g107: BSplineCurve PolesCount=2 KnotsCount=2 Degree=1 IsPeriodic=0
    g108: BSplineCurve PolesCount=2 KnotsCount=2 Degree=1 IsPeriodic=0
    g109: BSplineCurve PolesCount=2 KnotsCount=2 Degree=1 IsPeriodic=0
    g110: BSplineCurve PolesCount=2 KnotsCount=2 Degree=1 IsPeriodic=0
    g111: BSplineCurve PolesCount=2 KnotsCount=2 Degree=1 IsPeriodic=0
    g112: BSplineCurve PolesCount=2 KnotsCount=2 Degree=1 IsPeriodic=0
    g113: BSplineCurve PolesCount=2 KnotsCount=2 Degree=1 IsPeriodic=0
    g114: BSplineCurve PolesCount=2 KnotsCount=2 Degree=1 IsPeriodic=0
    g115: BSplineCurve PolesCount=2 KnotsCount=2 Degree=1 IsPeriodic=0
    g116: BSplineCurve PolesCount=2 KnotsCount=2 Degree=1 IsPeriodic=0
    g117: BSplineCurve PolesCount=2 KnotsCount=2 Degree=1 IsPeriodic=0
    g118: BSplineCurve PolesCount=2 KnotsCount=2 Degree=1 IsPeriodic=0
    g119: BSplineCurve PolesCount=2 KnotsCount=2 Degree=1 IsPeriodic=0
    g120: BSplineCurve PolesCount=2 KnotsCount=2 Degree=1 IsPeriodic=0
    g121: BSplineCurve PolesCount=2 KnotsCount=2 Degree=1 IsPeriodic=0
    g122: BSplineCurve PolesCount=2 KnotsCount=2 Degree=1 IsPeriodic=0
    g123: BSplineCurve PolesCount=2 KnotsCount=2 Degree=1 IsPeriodic=0
    g124: BSplineCurve PolesCount=2 KnotsCount=2 Degree=1 IsPeriodic=0
    g125: BSplineCurve PolesCount=2 KnotsCount=2 Degree=1 IsPeriodic=0
    g126: BSplineCurve PolesCount=2 KnotsCount=2 Degree=1 IsPeriodic=0
    g127: BSplineCurve PolesCount=2 KnotsCount=2 Degree=1 IsPeriodic=0
    g128: BSplineCurve PolesCount=2 KnotsCount=2 Degree=1 IsPeriodic=0
    g129: BSplineCurve PolesCount=2 KnotsCount=2 Degree=1 IsPeriodic=0
    g130: BSplineCurve PolesCount=2 KnotsCount=2 Degree=1 IsPeriodic=0
    g131: BSplineCurve PolesCount=2 KnotsCount=2 Degree=1 IsPeriodic=0
    g132: BSplineCurve PolesCount=2 KnotsCount=2 Degree=1 IsPeriodic=0
    g133: BSplineCurve PolesCount=2 KnotsCount=2 Degree=1 IsPeriodic=0
    g134: BSplineCurve PolesCount=2 KnotsCount=2 Degree=1 IsPeriodic=0
    g135: BSplineCurve PolesCount=2 KnotsCount=2 Degree=1 IsPeriodic=0
    g136: BSplineCurve PolesCount=2 KnotsCount=2 Degree=1 IsPeriodic=0
    g137: BSplineCurve PolesCount=2 KnotsCount=2 Degree=1 IsPeriodic=0
    g138: BSplineCurve PolesCount=2 KnotsCount=2 Degree=1 IsPeriodic=0
    g139: BSplineCurve PolesCount=2 KnotsCount=2 Degree=1 IsPeriodic=0
    g140: BSplineCurve PolesCount=2 KnotsCount=2 Degree=1 IsPeriodic=0
    g141: BSplineCurve PolesCount=2 KnotsCount=2 Degree=1 IsPeriodic=0
    g142: BSplineCurve PolesCount=2 KnotsCount=2 Degree=1 IsPeriodic=0
    g143: BSplineCurve PolesCount=2 KnotsCount=2 Degree=1 IsPeriodic=0
    g144: BSplineCurve PolesCount=2 KnotsCount=2 Degree=1 IsPeriodic=0
    g145: BSplineCurve PolesCount=2 KnotsCount=2 Degree=1 IsPeriodic=0
    g146: BSplineCurve PolesCount=2 KnotsCount=2 Degree=1 IsPeriodic=0
    g147: BSplineCurve PolesCount=2 KnotsCount=2 Degree=1 IsPeriodic=0
    g148: BSplineCurve PolesCount=2 KnotsCount=2 Degree=1 IsPeriodic=0
    g149: BSplineCurve PolesCount=2 KnotsCount=2 Degree=1 IsPeriodic=0
    g150: BSplineCurve PolesCount=2 KnotsCount=2 Degree=1 IsPeriodic=0
    g151: BSplineCurve PolesCount=2 KnotsCount=2 Degree=1 IsPeriodic=0
    g152: BSplineCurve PolesCount=2 KnotsCount=2 Degree=1 IsPeriodic=0
    g153: BSplineCurve PolesCount=2 KnotsCount=2 Degree=1 IsPeriodic=0
    g154: BSplineCurve PolesCount=2 KnotsCount=2 Degree=1 IsPeriodic=0
    g155: BSplineCurve PolesCount=2 KnotsCount=2 Degree=1 IsPeriodic=0
    g156: BSplineCurve PolesCount=2 KnotsCount=2 Degree=1 IsPeriodic=0
    g157: BSplineCurve PolesCount=2 KnotsCount=2 Degree=1 IsPeriodic=0
    g158: BSplineCurve PolesCount=2 KnotsCount=2 Degree=1 IsPeriodic=0
    g159: BSplineCurve PolesCount=2 KnotsCount=2 Degree=1 IsPeriodic=0
    g160: BSplineCurve PolesCount=2 KnotsCount=2 Degree=1 IsPeriodic=0
    g161: BSplineCurve PolesCount=2 KnotsCount=2 Degree=1 IsPeriodic=0
    g162: BSplineCurve PolesCount=2 KnotsCount=2 Degree=1 IsPeriodic=0
    g163: BSplineCurve PolesCount=2 KnotsCount=2 Degree=1 IsPeriodic=0
    g164: BSplineCurve PolesCount=2 KnotsCount=2 Degree=1 IsPeriodic=0
    g165: BSplineCurve PolesCount=2 KnotsCount=2 Degree=1 IsPeriodic=0
    g166: BSplineCurve PolesCount=2 KnotsCount=2 Degree=1 IsPeriodic=0
    g167: BSplineCurve PolesCount=2 KnotsCount=2 Degree=1 IsPeriodic=0
    g168: BSplineCurve PolesCount=2 KnotsCount=2 Degree=1 IsPeriodic=0
    g169: BSplineCurve PolesCount=2 KnotsCount=2 Degree=1 IsPeriodic=0
    g170: BSplineCurve PolesCount=2 KnotsCount=2 Degree=1 IsPeriodic=0
    g171: BSplineCurve PolesCount=2 KnotsCount=2 Degree=1 IsPeriodic=0
    g172: BSplineCurve PolesCount=2 KnotsCount=2 Degree=1 IsPeriodic=0
    g173: BSplineCurve PolesCount=2 KnotsCount=2 Degree=1 IsPeriodic=0
    g174: BSplineCurve PolesCount=2 KnotsCount=2 Degree=1 IsPeriodic=0
    g175: BSplineCurve PolesCount=2 KnotsCount=2 Degree=1 IsPeriodic=0
    g176: BSplineCurve PolesCount=2 KnotsCount=2 Degree=1 IsPeriodic=0
    g177: BSplineCurve PolesCount=2 KnotsCount=2 Degree=1 IsPeriodic=0
    g178: BSplineCurve PolesCount=2 KnotsCount=2 Degree=1 IsPeriodic=0
    g179: BSplineCurve PolesCount=2 KnotsCount=2 Degree=1 IsPeriodic=0
    g180: BSplineCurve PolesCount=2 KnotsCount=2 Degree=1 IsPeriodic=0
    g181: BSplineCurve PolesCount=2 KnotsCount=2 Degree=1 IsPeriodic=0
    g182: BSplineCurve PolesCount=2 KnotsCount=2 Degree=1 IsPeriodic=0
    g183: BSplineCurve PolesCount=2 KnotsCount=2 Degree=1 IsPeriodic=0
    g184: BSplineCurve PolesCount=2 KnotsCount=2 Degree=1 IsPeriodic=0
    g185: BSplineCurve PolesCount=2 KnotsCount=2 Degree=1 IsPeriodic=0
    g186: BSplineCurve PolesCount=2 KnotsCount=2 Degree=1 IsPeriodic=0
    g187: BSplineCurve PolesCount=2 KnotsCount=2 Degree=1 IsPeriodic=0
    g188: BSplineCurve PolesCount=2 KnotsCount=2 Degree=1 IsPeriodic=0
    g189: BSplineCurve PolesCount=2 KnotsCount=2 Degree=1 IsPeriodic=0
    g190: BSplineCurve PolesCount=2 KnotsCount=2 Degree=1 IsPeriodic=0
    g191: BSplineCurve PolesCount=2 KnotsCount=2 Degree=1 IsPeriodic=0
    g192: BSplineCurve PolesCount=2 KnotsCount=2 Degree=1 IsPeriodic=0
    g193: BSplineCurve PolesCount=2 KnotsCount=2 Degree=1 IsPeriodic=0
    g194: BSplineCurve PolesCount=2 KnotsCount=2 Degree=1 IsPeriodic=0
    g195: BSplineCurve PolesCount=2 KnotsCount=2 Degree=1 IsPeriodic=0
    g196: BSplineCurve PolesCount=2 KnotsCount=2 Degree=1 IsPeriodic=0
    g197: BSplineCurve PolesCount=2 KnotsCount=2 Degree=1 IsPeriodic=0
    g198: BSplineCurve PolesCount=2 KnotsCount=2 Degree=1 IsPeriodic=0
    g199: BSplineCurve PolesCount=2 KnotsCount=2 Degree=1 IsPeriodic=0
    g200: BSplineCurve PolesCount=2 KnotsCount=2 Degree=1 IsPeriodic=0
    g201: BSplineCurve PolesCount=2 KnotsCount=2 Degree=1 IsPeriodic=0
    g202: BSplineCurve PolesCount=2 KnotsCount=2 Degree=1 IsPeriodic=0
    g203: BSplineCurve PolesCount=2 KnotsCount=2 Degree=1 IsPeriodic=0
    g204: BSplineCurve PolesCount=2 KnotsCount=2 Degree=1 IsPeriodic=0
    g205: BSplineCurve PolesCount=2 KnotsCount=2 Degree=1 IsPeriodic=0
    g206: BSplineCurve PolesCount=2 KnotsCount=2 Degree=1 IsPeriodic=0
    g207: BSplineCurve PolesCount=2 KnotsCount=2 Degree=1 IsPeriodic=0
    g208: BSplineCurve PolesCount=2 KnotsCount=2 Degree=1 IsPeriodic=0
    g209: BSplineCurve PolesCount=2 KnotsCount=2 Degree=1 IsPeriodic=0
    g210: BSplineCurve PolesCount=2 KnotsCount=2 Degree=1 IsPeriodic=0
    g211: BSplineCurve PolesCount=2 KnotsCount=2 Degree=1 IsPeriodic=0
    g212: BSplineCurve PolesCount=2 KnotsCount=2 Degree=1 IsPeriodic=0
    g213: BSplineCurve PolesCount=2 KnotsCount=2 Degree=1 IsPeriodic=0
    g214: BSplineCurve PolesCount=2 KnotsCount=2 Degree=1 IsPeriodic=0
    g215: BSplineCurve PolesCount=2 KnotsCount=2 Degree=1 IsPeriodic=0
    g216: BSplineCurve PolesCount=2 KnotsCount=2 Degree=1 IsPeriodic=0
    g217: BSplineCurve PolesCount=2 KnotsCount=2 Degree=1 IsPeriodic=0
    g218: BSplineCurve PolesCount=2 KnotsCount=2 Degree=1 IsPeriodic=0
    g219: BSplineCurve PolesCount=2 KnotsCount=2 Degree=1 IsPeriodic=0
    g220: BSplineCurve PolesCount=2 KnotsCount=2 Degree=1 IsPeriodic=0
    g221: BSplineCurve PolesCount=2 KnotsCount=2 Degree=1 IsPeriodic=0
    g222: BSplineCurve PolesCount=2 KnotsCount=2 Degree=1 IsPeriodic=0
    g223: BSplineCurve PolesCount=2 KnotsCount=2 Degree=1 IsPeriodic=0
    g224: BSplineCurve PolesCount=2 KnotsCount=2 Degree=1 IsPeriodic=0
    g225: BSplineCurve PolesCount=2 KnotsCount=2 Degree=1 IsPeriodic=0
    g226: BSplineCurve PolesCount=2 KnotsCount=2 Degree=1 IsPeriodic=0
    g227: BSplineCurve PolesCount=2 KnotsCount=2 Degree=1 IsPeriodic=0
    g228: BSplineCurve PolesCount=2 KnotsCount=2 Degree=1 IsPeriodic=0
    g229: BSplineCurve PolesCount=2 KnotsCount=2 Degree=1 IsPeriodic=0
    g230: BSplineCurve PolesCount=2 KnotsCount=2 Degree=1 IsPeriodic=0
    g231: BSplineCurve PolesCount=2 KnotsCount=2 Degree=1 IsPeriodic=0
    g232: BSplineCurve PolesCount=2 KnotsCount=2 Degree=1 IsPeriodic=0
    g233: BSplineCurve PolesCount=2 KnotsCount=2 Degree=1 IsPeriodic=0
    g234: BSplineCurve PolesCount=2 KnotsCount=2 Degree=1 IsPeriodic=0
    g235: BSplineCurve PolesCount=2 KnotsCount=2 Degree=1 IsPeriodic=0
    g236: BSplineCurve PolesCount=2 KnotsCount=2 Degree=1 IsPeriodic=0
    g237: BSplineCurve PolesCount=2 KnotsCount=2 Degree=1 IsPeriodic=0
    g238: BSplineCurve PolesCount=2 KnotsCount=2 Degree=1 IsPeriodic=0
    g239: BSplineCurve PolesCount=2 KnotsCount=2 Degree=1 IsPeriodic=0
    g240: BSplineCurve PolesCount=2 KnotsCount=2 Degree=1 IsPeriodic=0
    g241: BSplineCurve PolesCount=2 KnotsCount=2 Degree=1 IsPeriodic=0
    g242: BSplineCurve PolesCount=2 KnotsCount=2 Degree=1 IsPeriodic=0
    g243: BSplineCurve PolesCount=2 KnotsCount=2 Degree=1 IsPeriodic=0
    g244: BSplineCurve PolesCount=2 KnotsCount=2 Degree=1 IsPeriodic=0
    g245: BSplineCurve PolesCount=2 KnotsCount=2 Degree=1 IsPeriodic=0
    g246: BSplineCurve PolesCount=2 KnotsCount=2 Degree=1 IsPeriodic=0
    g247: BSplineCurve PolesCount=2 KnotsCount=2 Degree=1 IsPeriodic=0
    g248: BSplineCurve PolesCount=2 KnotsCount=2 Degree=1 IsPeriodic=0
    g249: BSplineCurve PolesCount=2 KnotsCount=2 Degree=1 IsPeriodic=0
    g250: BSplineCurve PolesCount=2 KnotsCount=2 Degree=1 IsPeriodic=0
    g251: BSplineCurve PolesCount=2 KnotsCount=2 Degree=1 IsPeriodic=0
    g252: BSplineCurve PolesCount=2 KnotsCount=2 Degree=1 IsPeriodic=0
    g253: BSplineCurve PolesCount=2 KnotsCount=2 Degree=1 IsPeriodic=0
    g254: BSplineCurve PolesCount=2 KnotsCount=2 Degree=1 IsPeriodic=0
    g255: BSplineCurve PolesCount=2 KnotsCount=2 Degree=1 IsPeriodic=0
    g256: BSplineCurve PolesCount=2 KnotsCount=2 Degree=1 IsPeriodic=0
    g257: BSplineCurve PolesCount=2 KnotsCount=2 Degree=1 IsPeriodic=0
    g258: BSplineCurve PolesCount=2 KnotsCount=2 Degree=1 IsPeriodic=0
    g259: BSplineCurve PolesCount=2 KnotsCount=2 Degree=1 IsPeriodic=0
    g260: BSplineCurve PolesCount=2 KnotsCount=2 Degree=1 IsPeriodic=0
    g261: BSplineCurve PolesCount=2 KnotsCount=2 Degree=1 IsPeriodic=0
    g262: BSplineCurve PolesCount=2 KnotsCount=2 Degree=1 IsPeriodic=0
    g263: BSplineCurve PolesCount=2 KnotsCount=2 Degree=1 IsPeriodic=0
    g264: BSplineCurve PolesCount=2 KnotsCount=2 Degree=1 IsPeriodic=0
    g265: BSplineCurve PolesCount=2 KnotsCount=2 Degree=1 IsPeriodic=0
    g266: BSplineCurve PolesCount=2 KnotsCount=2 Degree=1 IsPeriodic=0
    g267: BSplineCurve PolesCount=2 KnotsCount=2 Degree=1 IsPeriodic=0
    g268: BSplineCurve PolesCount=2 KnotsCount=2 Degree=1 IsPeriodic=0
    g269: BSplineCurve PolesCount=2 KnotsCount=2 Degree=1 IsPeriodic=0
    g270: BSplineCurve PolesCount=2 KnotsCount=2 Degree=1 IsPeriodic=0
    g271: BSplineCurve PolesCount=2 KnotsCount=2 Degree=1 IsPeriodic=0
    g272: BSplineCurve PolesCount=2 KnotsCount=2 Degree=1 IsPeriodic=0
    g273: BSplineCurve PolesCount=2 KnotsCount=2 Degree=1 IsPeriodic=0
    g274: BSplineCurve PolesCount=2 KnotsCount=2 Degree=1 IsPeriodic=0
    g275: BSplineCurve PolesCount=2 KnotsCount=2 Degree=1 IsPeriodic=0
    g276: BSplineCurve PolesCount=2 KnotsCount=2 Degree=1 IsPeriodic=0
    g277: BSplineCurve PolesCount=2 KnotsCount=2 Degree=1 IsPeriodic=0
    g278: BSplineCurve PolesCount=2 KnotsCount=2 Degree=1 IsPeriodic=0
    g279: BSplineCurve PolesCount=2 KnotsCount=2 Degree=1 IsPeriodic=0
    g280: BSplineCurve PolesCount=2 KnotsCount=2 Degree=1 IsPeriodic=0
    g281: BSplineCurve PolesCount=2 KnotsCount=2 Degree=1 IsPeriodic=0
    g282: BSplineCurve PolesCount=2 KnotsCount=2 Degree=1 IsPeriodic=0
    g283: BSplineCurve PolesCount=2 KnotsCount=2 Degree=1 IsPeriodic=0
    g284: BSplineCurve PolesCount=2 KnotsCount=2 Degree=1 IsPeriodic=0
    g285: BSplineCurve PolesCount=2 KnotsCount=2 Degree=1 IsPeriodic=0
    g286: BSplineCurve PolesCount=2 KnotsCount=2 Degree=1 IsPeriodic=0
    g287: BSplineCurve PolesCount=2 KnotsCount=2 Degree=1 IsPeriodic=0
    g288: BSplineCurve PolesCount=2 KnotsCount=2 Degree=1 IsPeriodic=0
    g289: BSplineCurve PolesCount=2 KnotsCount=2 Degree=1 IsPeriodic=0
    g290: BSplineCurve PolesCount=2 KnotsCount=2 Degree=1 IsPeriodic=0
    g291: BSplineCurve PolesCount=2 KnotsCount=2 Degree=1 IsPeriodic=0
    g292: BSplineCurve PolesCount=2 KnotsCount=2 Degree=1 IsPeriodic=0
    g293: BSplineCurve PolesCount=2 KnotsCount=2 Degree=1 IsPeriodic=0
    g294: BSplineCurve PolesCount=2 KnotsCount=2 Degree=1 IsPeriodic=0
    g295: BSplineCurve PolesCount=2 KnotsCount=2 Degree=1 IsPeriodic=0
    g296: BSplineCurve PolesCount=2 KnotsCount=2 Degree=1 IsPeriodic=0
    g297: BSplineCurve PolesCount=2 KnotsCount=2 Degree=1 IsPeriodic=0
    g298: BSplineCurve PolesCount=2 KnotsCount=2 Degree=1 IsPeriodic=0
    g299: BSplineCurve PolesCount=2 KnotsCount=2 Degree=1 IsPeriodic=0
    g300: BSplineCurve PolesCount=2 KnotsCount=2 Degree=1 IsPeriodic=0
    g301: BSplineCurve PolesCount=2 KnotsCount=2 Degree=1 IsPeriodic=0
    g302: BSplineCurve PolesCount=2 KnotsCount=2 Degree=1 IsPeriodic=0
    g303: BSplineCurve PolesCount=2 KnotsCount=2 Degree=1 IsPeriodic=0
    g304: BSplineCurve PolesCount=2 KnotsCount=2 Degree=1 IsPeriodic=0
    g305: BSplineCurve PolesCount=2 KnotsCount=2 Degree=1 IsPeriodic=0
    g306: BSplineCurve PolesCount=2 KnotsCount=2 Degree=1 IsPeriodic=0
    g307: BSplineCurve PolesCount=2 KnotsCount=2 Degree=1 IsPeriodic=0
    g308: BSplineCurve PolesCount=2 KnotsCount=2 Degree=1 IsPeriodic=0
    g309: BSplineCurve PolesCount=2 KnotsCount=2 Degree=1 IsPeriodic=0
    g310: BSplineCurve PolesCount=2 KnotsCount=2 Degree=1 IsPeriodic=0
    g311: BSplineCurve PolesCount=2 KnotsCount=2 Degree=1 IsPeriodic=0
    g312: BSplineCurve PolesCount=2 KnotsCount=2 Degree=1 IsPeriodic=0
    g313: BSplineCurve PolesCount=2 KnotsCount=2 Degree=1 IsPeriodic=0
    g314: BSplineCurve PolesCount=2 KnotsCount=2 Degree=1 IsPeriodic=0
    g315: BSplineCurve PolesCount=2 KnotsCount=2 Degree=1 IsPeriodic=0
    g316: BSplineCurve PolesCount=2 KnotsCount=2 Degree=1 IsPeriodic=0
    g317: BSplineCurve PolesCount=2 KnotsCount=2 Degree=1 IsPeriodic=0
    g318: BSplineCurve PolesCount=2 KnotsCount=2 Degree=1 IsPeriodic=0
    g319: BSplineCurve PolesCount=2 KnotsCount=2 Degree=1 IsPeriodic=0
    g320: BSplineCurve PolesCount=2 KnotsCount=2 Degree=1 IsPeriodic=0
    g321: BSplineCurve PolesCount=2 KnotsCount=2 Degree=1 IsPeriodic=0
    g322: BSplineCurve PolesCount=2 KnotsCount=2 Degree=1 IsPeriodic=0
    g323: BSplineCurve PolesCount=2 KnotsCount=2 Degree=1 IsPeriodic=0
    g324: BSplineCurve PolesCount=2 KnotsCount=2 Degree=1 IsPeriodic=0
    g325: BSplineCurve PolesCount=2 KnotsCount=2 Degree=1 IsPeriodic=0
    g326: BSplineCurve PolesCount=2 KnotsCount=2 Degree=1 IsPeriodic=0
    g327: BSplineCurve PolesCount=2 KnotsCount=2 Degree=1 IsPeriodic=0
    g328: BSplineCurve PolesCount=2 KnotsCount=2 Degree=1 IsPeriodic=0
    g329: BSplineCurve PolesCount=2 KnotsCount=2 Degree=1 IsPeriodic=0
    g330: BSplineCurve PolesCount=2 KnotsCount=2 Degree=1 IsPeriodic=0
    g331: BSplineCurve PolesCount=2 KnotsCount=2 Degree=1 IsPeriodic=0
    g332: BSplineCurve PolesCount=2 KnotsCount=2 Degree=1 IsPeriodic=0
    g333: BSplineCurve PolesCount=2 KnotsCount=2 Degree=1 IsPeriodic=0
    g334: BSplineCurve PolesCount=2 KnotsCount=2 Degree=1 IsPeriodic=0
    g335: BSplineCurve PolesCount=2 KnotsCount=2 Degree=1 IsPeriodic=0
    g336: BSplineCurve PolesCount=2 KnotsCount=2 Degree=1 IsPeriodic=0
    g337: BSplineCurve PolesCount=2 KnotsCount=2 Degree=1 IsPeriodic=0
    g338: BSplineCurve PolesCount=2 KnotsCount=2 Degree=1 IsPeriodic=0
    g339: BSplineCurve PolesCount=2 KnotsCount=2 Degree=1 IsPeriodic=0
    g340: BSplineCurve PolesCount=2 KnotsCount=2 Degree=1 IsPeriodic=0
    g341: BSplineCurve PolesCount=2 KnotsCount=2 Degree=1 IsPeriodic=0
    g342: BSplineCurve PolesCount=2 KnotsCount=2 Degree=1 IsPeriodic=0
    g343: BSplineCurve PolesCount=2 KnotsCount=2 Degree=1 IsPeriodic=0
    g344: BSplineCurve PolesCount=2 KnotsCount=2 Degree=1 IsPeriodic=0
    g345: BSplineCurve PolesCount=2 KnotsCount=2 Degree=1 IsPeriodic=0
    g346: BSplineCurve PolesCount=2 KnotsCount=2 Degree=1 IsPeriodic=0
    g347: BSplineCurve PolesCount=2 KnotsCount=2 Degree=1 IsPeriodic=0
    g348: BSplineCurve PolesCount=2 KnotsCount=2 Degree=1 IsPeriodic=0
    g349: BSplineCurve PolesCount=2 KnotsCount=2 Degree=1 IsPeriodic=0
    g350: BSplineCurve PolesCount=2 KnotsCount=2 Degree=1 IsPeriodic=0
    g351: BSplineCurve PolesCount=2 KnotsCount=2 Degree=1 IsPeriodic=0
    g352: BSplineCurve PolesCount=2 KnotsCount=2 Degree=1 IsPeriodic=0
    g353: BSplineCurve PolesCount=2 KnotsCount=2 Degree=1 IsPeriodic=0
    g354: BSplineCurve PolesCount=2 KnotsCount=2 Degree=1 IsPeriodic=0
    g355: BSplineCurve PolesCount=2 KnotsCount=2 Degree=1 IsPeriodic=0
    g356: BSplineCurve PolesCount=2 KnotsCount=2 Degree=1 IsPeriodic=0
    g357: BSplineCurve PolesCount=2 KnotsCount=2 Degree=1 IsPeriodic=0
    g358: BSplineCurve PolesCount=2 KnotsCount=2 Degree=1 IsPeriodic=0
    g359: BSplineCurve PolesCount=2 KnotsCount=2 Degree=1 IsPeriodic=0
    g360: BSplineCurve PolesCount=2 KnotsCount=2 Degree=1 IsPeriodic=0
    g361: BSplineCurve PolesCount=2 KnotsCount=2 Degree=1 IsPeriodic=0
    g362: BSplineCurve PolesCount=2 KnotsCount=2 Degree=1 IsPeriodic=0
    g363: BSplineCurve PolesCount=2 KnotsCount=2 Degree=1 IsPeriodic=0
    g364: BSplineCurve PolesCount=2 KnotsCount=2 Degree=1 IsPeriodic=0
    g365: BSplineCurve PolesCount=2 KnotsCount=2 Degree=1 IsPeriodic=0
    g366: BSplineCurve PolesCount=2 KnotsCount=2 Degree=1 IsPeriodic=0
    g367: BSplineCurve PolesCount=2 KnotsCount=2 Degree=1 IsPeriodic=0
    g368: BSplineCurve PolesCount=2 KnotsCount=2 Degree=1 IsPeriodic=0
    g369: BSplineCurve PolesCount=2 KnotsCount=2 Degree=1 IsPeriodic=0
    g370: BSplineCurve PolesCount=2 KnotsCount=2 Degree=1 IsPeriodic=0
    g371: BSplineCurve PolesCount=2 KnotsCount=2 Degree=1 IsPeriodic=0
    g372: BSplineCurve PolesCount=2 KnotsCount=2 Degree=1 IsPeriodic=0
    g373: BSplineCurve PolesCount=2 KnotsCount=2 Degree=1 IsPeriodic=0
    g374: BSplineCurve PolesCount=2 KnotsCount=2 Degree=1 IsPeriodic=0
    g375: BSplineCurve PolesCount=2 KnotsCount=2 Degree=1 IsPeriodic=0
    g376: BSplineCurve PolesCount=2 KnotsCount=2 Degree=1 IsPeriodic=0
    g377: BSplineCurve PolesCount=2 KnotsCount=2 Degree=1 IsPeriodic=0
    g378: BSplineCurve PolesCount=2 KnotsCount=2 Degree=1 IsPeriodic=0
    g379: BSplineCurve PolesCount=2 KnotsCount=2 Degree=1 IsPeriodic=0
    g380: BSplineCurve PolesCount=2 KnotsCount=2 Degree=1 IsPeriodic=0
    g381: BSplineCurve PolesCount=2 KnotsCount=2 Degree=1 IsPeriodic=0
    g382: BSplineCurve PolesCount=2 KnotsCount=2 Degree=1 IsPeriodic=0
    g383: BSplineCurve PolesCount=2 KnotsCount=2 Degree=1 IsPeriodic=0
    g384: BSplineCurve PolesCount=2 KnotsCount=2 Degree=1 IsPeriodic=0
    g385: BSplineCurve PolesCount=2 KnotsCount=2 Degree=1 IsPeriodic=0
    g386: BSplineCurve PolesCount=2 KnotsCount=2 Degree=1 IsPeriodic=0
    g387: BSplineCurve PolesCount=2 KnotsCount=2 Degree=1 IsPeriodic=0
    g388: BSplineCurve PolesCount=2 KnotsCount=2 Degree=1 IsPeriodic=0
    g389: BSplineCurve PolesCount=2 KnotsCount=2 Degree=1 IsPeriodic=0
    g390: BSplineCurve PolesCount=2 KnotsCount=2 Degree=1 IsPeriodic=0
    g391: BSplineCurve PolesCount=2 KnotsCount=2 Degree=1 IsPeriodic=0
    g392: BSplineCurve PolesCount=2 KnotsCount=2 Degree=1 IsPeriodic=0
    g393: BSplineCurve PolesCount=2 KnotsCount=2 Degree=1 IsPeriodic=0
    g394: BSplineCurve PolesCount=2 KnotsCount=2 Degree=1 IsPeriodic=0
    g395: BSplineCurve PolesCount=2 KnotsCount=2 Degree=1 IsPeriodic=0
    g396: BSplineCurve PolesCount=2 KnotsCount=2 Degree=1 IsPeriodic=0
    g397: BSplineCurve PolesCount=2 KnotsCount=2 Degree=1 IsPeriodic=0
    g398: BSplineCurve PolesCount=2 KnotsCount=2 Degree=1 IsPeriodic=0
    g399: BSplineCurve PolesCount=2 KnotsCount=2 Degree=1 IsPeriodic=0
    ... +460 more geometry lines
  constraints (860):
    c: Coincident(g0,g1)
    c: Coincident(g1,g2)
    c: Coincident(g2,g3)
    c: Coincident(g3,g4)
    c: Coincident(g4,g5)
    c: Coincident(g5,g6)
    c: Coincident(g6,g7)
    c: Coincident(g7,g8)
    c: Coincident(g8,g9)
    c: Coincident(g9,g10)
    c: Coincident(g10,g11)
    c: Coincident(g11,g12)
    c: Coincident(g12,g13)
    c: Coincident(g13,g14)
    c: Coincident(g14,g15)
    c: Coincident(g15,g16)
    c: Coincident(g16,g17)
    c: Coincident(g17,g18)
    c: Coincident(g18,g19)
    c: Coincident(g19,g20)
    c: Coincident(g20,g21)
    c: Coincident(g21,g22)
    c: Coincident(g22,g23)
    c: Coincident(g23,g24)
    c: Coincident(g24,g25)
    c: Coincident(g25,g26)
    c: Coincident(g26,g27)
    c: Coincident(g27,g28)
    c: Coincident(g28,g29)
    c: Coincident(g29,g30)
    c: Coincident(g30,g31)
    c: Coincident(g31,g32)
    c: Coincident(g32,g33)
    c: Coincident(g33,g34)
    c: Coincident(g34,g35)
    c: Coincident(g35,g36)
    c: Coincident(g36,g37)
    c: Coincident(g37,g38)
    c: Coincident(g38,g39)
    c: Coincident(g39,g40)
    c: Coincident(g40,g41)
    c: Coincident(g41,g42)
    c: Coincident(g42,g43)
    c: Coincident(g43,g44)
    c: Coincident(g44,g45)
    c: Coincident(g45,g46)
    c: Coincident(g46,g47)
    c: Coincident(g47,g48)
    c: Coincident(g48,g49)
    c: Coincident(g49,g50)
    c: Coincident(g50,g51)
    c: Coincident(g51,g52)
    c: Coincident(g52,g53)
    c: Coincident(g53,g54)
    c: Coincident(g54,g55)
    c: Coincident(g55,g56)
    c: Coincident(g56,g57)
    c: Coincident(g57,g58)
    c: Coincident(g58,g59)
    c: Coincident(g59,g60)
    c: Coincident(g60,g61)
    c: Coincident(g61,g62)
    c: Coincident(g62,g63)
    c: Coincident(g63,g64)
    c: Coincident(g64,g65)
    c: Coincident(g65,g66)
    c: Coincident(g66,g67)
    c: Coincident(g67,g68)
    c: Coincident(g68,g69)
    c: Coincident(g69,g70)
    c: Coincident(g70,g71)
    c: Coincident(g71,g72)
    c: Coincident(g72,g73)
    c: Coincident(g73,g74)
    c: Coincident(g74,g75)
    c: Coincident(g75,g76)
    c: Coincident(g76,g77)
    c: Coincident(g77,g78)
    c: Coincident(g78,g79)
    c: Coincident(g79,g80)
    c: Coincident(g80,g81)
    c: Coincident(g81,g82)
    c: Coincident(g82,g83)
    c: Coincident(g83,g84)
    c: Coincident(g84,g85)
    c: Coincident(g85,g86)
    c: Coincident(g86,g87)
    c: Coincident(g87,g0)
    c: Coincident(g88,g89)
    c: Coincident(g89,g90)
    c: Coincident(g90,g91)
    c: Coincident(g91,g92)
    c: Coincident(g92,g93)
    c: Coincident(g93,g94)
    c: Coincident(g94,g95)
    c: Coincident(g95,g96)
    c: Coincident(g96,g97)
    c: Coincident(g97,g98)
    c: Coincident(g98,g99)
    c: Coincident(g99,g100)
    c: Coincident(g100,g101)
    c: Coincident(g101,g102)
    c: Coincident(g102,g103)
    c: Coincident(g103,g104)
    c: Coincident(g104,g105)
    c: Coincident(g105,g106)
    c: Coincident(g106,g107)
    c: Coincident(g107,g108)
    c: Coincident(g108,g109)
    c: Coincident(g109,g110)
    c: Coincident(g110,g111)
    c: Coincident(g111,g112)
    c: Coincident(g112,g113)
    c: Coincident(g113,g114)
    c: Coincident(g114,g115)
    c: Coincident(g115,g116)
    c: Coincident(g116,g117)
    c: Coincident(g117,g118)
    c: Coincident(g118,g119)
    c: Coincident(g119,g120)
    c: Coincident(g120,g121)
    c: Coincident(g121,g122)
    c: Coincident(g122,g123)
    c: Coincident(g123,g124)
    c: Coincident(g124,g125)
    c: Coincident(g125,g126)
    c: Coincident(g126,g127)
    c: Coincident(g127,g88)
    c: Coincident(g128,g129)
    c: Coincident(g129,g130)
    c: Coincident(g130,g131)
    c: Coincident(g131,g132)
    c: Coincident(g132,g133)
    c: Coincident(g133,g134)
    c: Coincident(g134,g135)
    c: Coincident(g135,g136)
    c: Coincident(g136,g137)
    c: Coincident(g137,g138)
    c: Coincident(g138,g139)
    c: Coincident(g139,g140)
    c: Coincident(g140,g141)
    c: Coincident(g141,g142)
    c: Coincident(g142,g143)
    c: Coincident(g143,g144)
    c: Coincident(g144,g145)
    c: Coincident(g145,g146)
    c: Coincident(g146,g147)
    c: Coincident(g147,g148)
    c: Coincident(g148,g149)
    c: Coincident(g149,g150)
    c: Coincident(g150,g151)
    c: Coincident(g151,g152)
    c: Coincident(g152,g153)
    c: Coincident(g153,g154)
    c: Coincident(g154,g155)
    c: Coincident(g155,g156)
    c: Coincident(g156,g157)
    c: Coincident(g157,g158)
    c: Coincident(g158,g159)
    c: Coincident(g159,g160)
    c: Coincident(g160,g161)
    c: Coincident(g161,g162)
    c: Coincident(g162,g163)
    c: Coincident(g163,g164)
    c: Coincident(g164,g165)
    c: Coincident(g165,g166)
    c: Coincident(g166,g167)
    c: Coincident(g167,g168)
    c: Coincident(g168,g169)
    c: Coincident(g169,g170)
    c: Coincident(g170,g171)
    c: Coincident(g171,g172)
    c: Coincident(g172,g173)
    c: Coincident(g173,g174)
    c: Coincident(g174,g175)
    c: Coincident(g175,g176)
    c: Coincident(g176,g177)
    c: Coincident(g177,g178)
    c: Coincident(g178,g179)
    c: Coincident(g179,g180)
    c: Coincident(g180,g181)
    c: Coincident(g181,g182)
    c: Coincident(g182,g183)
    c: Coincident(g183,g184)
    c: Coincident(g184,g185)
    c: Coincident(g185,g186)
    c: Coincident(g186,g187)
    c: Coincident(g187,g188)
    c: Coincident(g188,g189)
    c: Coincident(g189,g190)
    c: Coincident(g190,g191)
    c: Coincident(g191,g192)
    c: Coincident(g192,g193)
    c: Coincident(g193,g194)
    c: Coincident(g194,g195)
    c: Coincident(g195,g196)
    c: Coincident(g196,g197)
    c: Coincident(g197,g198)
    c: Coincident(g198,g199)
    c: Coincident(g199,g200)
    c: Coincident(g200,g201)
    c: Coincident(g201,g202)
    c: Coincident(g202,g203)
    c: Coincident(g203,g204)
    c: Coincident(g204,g205)
    c: Coincident(g205,g206)
    c: Coincident(g206,g207)
    c: Coincident(g207,g208)
    c: Coincident(g208,g209)
    c: Coincident(g209,g210)
    c: Coincident(g210,g211)
    c: Coincident(g211,g212)
    c: Coincident(g212,g213)
    c: Coincident(g213,g214)
    c: Coincident(g214,g215)
    c: Coincident(g215,g216)
    c: Coincident(g216,g217)
    c: Coincident(g217,g218)
    c: Coincident(g218,g219)
    c: Coincident(g219,g220)
    c: Coincident(g220,g221)
    c: Coincident(g221,g222)
    c: Coincident(g222,g223)
    c: Coincident(g223,g224)
    c: Coincident(g224,g225)
    c: Coincident(g225,g226)
    c: Coincident(g226,g227)
    c: Coincident(g227,g228)
    c: Coincident(g228,g229)
    c: Coincident(g229,g230)
    c: Coincident(g230,g231)
    c: Coincident(g231,g232)
    c: Coincident(g232,g233)
    c: Coincident(g233,g234)
    c: Coincident(g234,g235)
    c: Coincident(g235,g236)
    c: Coincident(g236,g237)
    c: Coincident(g237,g238)
    c: Coincident(g238,g239)
    c: Coincident(g239,g128)
    c: Coincident(g240,g241)
    c: Coincident(g241,g242)
    c: Coincident(g242,g243)
    c: Coincident(g243,g244)
    c: Coincident(g244,g245)
    c: Coincident(g245,g246)
    c: Coincident(g246,g247)
    c: Coincident(g247,g248)
    c: Coincident(g248,g249)
    c: Coincident(g249,g250)
    c: Coincident(g250,g251)
    c: Coincident(g251,g252)
    c: Coincident(g252,g253)
    c: Coincident(g253,g254)
    c: Coincident(g254,g255)
    c: Coincident(g255,g256)
    c: Coincident(g256,g257)
    c: Coincident(g257,g258)
    c: Coincident(g258,g259)
    c: Coincident(g259,g260)
    c: Coincident(g260,g261)
    c: Coincident(g261,g262)
    c: Coincident(g262,g263)
    c: Coincident(g263,g264)
    c: Coincident(g264,g265)
    c: Coincident(g265,g266)
    c: Coincident(g266,g267)
    c: Coincident(g267,g268)
    c: Coincident(g268,g269)
    c: Coincident(g269,g270)
    c: Coincident(g270,g271)
    c: Coincident(g271,g272)
    c: Coincident(g272,g273)
    c: Coincident(g273,g274)
    c: Coincident(g274,g275)
    c: Coincident(g275,g276)
    c: Coincident(g276,g277)
    c: Coincident(g277,g278)
    c: Coincident(g278,g279)
    c: Coincident(g279,g280)
    c: Coincident(g280,g281)
    c: Coincident(g281,g282)
    c: Coincident(g282,g283)
    c: Coincident(g283,g284)
    c: Coincident(g284,g285)
    c: Coincident(g285,g286)
    c: Coincident(g286,g287)
    c: Coincident(g287,g240)
    c: Coincident(g288,g289)
    c: Coincident(g289,g290)
    c: Coincident(g290,g291)
    c: Coincident(g291,g292)
    c: Coincident(g292,g293)
    c: Coincident(g293,g294)
    c: Coincident(g294,g295)
    c: Coincident(g295,g296)
    c: Coincident(g296,g297)
    c: Coincident(g297,g298)
    c: Coincident(g298,g299)
    c: Coincident(g299,g300)
    c: Coincident(g300,g301)
    c: Coincident(g301,g302)
    c: Coincident(g302,g303)
    c: Coincident(g303,g304)
    c: Coincident(g304,g305)
    c: Coincident(g305,g306)
    c: Coincident(g306,g307)
    c: Coincident(g307,g308)
    c: Coincident(g308,g309)
    c: Coincident(g309,g310)
    c: Coincident(g310,g311)
    c: Coincident(g311,g288)
    c: Coincident(g312,g313)
    c: Coincident(g313,g314)
    c: Coincident(g314,g315)
    c: Coincident(g315,g316)
    c: Coincident(g316,g317)
    c: Coincident(g317,g318)
    c: Coincident(g318,g319)
    c: Coincident(g319,g320)
    c: Coincident(g320,g321)
    c: Coincident(g321,g322)
    c: Coincident(g322,g323)
    c: Coincident(g323,g324)
    c: Coincident(g324,g325)
    c: Coincident(g325,g326)
    c: Coincident(g326,g327)
    c: Coincident(g327,g312)
    c: Coincident(g328,g329)
    c: Coincident(g329,g330)
    c: Coincident(g330,g331)
    c: Coincident(g331,g332)
    c: Coincident(g332,g333)
    c: Coincident(g333,g334)
    c: Coincident(g334,g335)
    c: Coincident(g335,g336)
    c: Coincident(g336,g337)
    c: Coincident(g337,g338)
    c: Coincident(g338,g339)
    c: Coincident(g339,g340)
    c: Coincident(g340,g341)
    c: Coincident(g341,g342)
    c: Coincident(g342,g343)
    c: Coincident(g343,g344)
    c: Coincident(g344,g345)
    c: Coincident(g345,g346)
    c: Coincident(g346,g347)
    c: Coincident(g347,g348)
    c: Coincident(g348,g349)
    c: Coincident(g349,g350)
    c: Coincident(g350,g351)
    c: Coincident(g351,g352)
    c: Coincident(g352,g353)
    c: Coincident(g353,g354)
    c: Coincident(g354,g355)
    c: Coincident(g355,g356)
    c: Coincident(g356,g357)
    c: Coincident(g357,g358)
    c: Coincident(g358,g359)
    c: Coincident(g359,g360)
    c: Coincident(g360,g361)
    c: Coincident(g361,g362)
    c: Coincident(g362,g363)
    c: Coincident(g363,g364)
    c: Coincident(g364,g365)
    c: Coincident(g365,g366)
    c: Coincident(g366,g367)
    c: Coincident(g367,g368)
    c: Coincident(g368,g369)
    c: Coincident(g369,g370)
    c: Coincident(g370,g371)
    c: Coincident(g371,g372)
    c: Coincident(g372,g373)
    c: Coincident(g373,g374)
    c: Coincident(g374,g375)
    c: Coincident(g375,g376)
    c: Coincident(g376,g377)
    c: Coincident(g377,g378)
    c: Coincident(g378,g379)
    c: Coincident(g379,g380)
    c: Coincident(g380,g381)
    c: Coincident(g381,g382)
    c: Coincident(g382,g383)
    c: Coincident(g383,g384)
    c: Coincident(g384,g385)
    c: Coincident(g385,g386)
    c: Coincident(g386,g387)
    c: Coincident(g387,g388)
    c: Coincident(g388,g389)
    c: Coincident(g389,g390)
    c: Coincident(g390,g391)
    c: Coincident(g391,g392)
    c: Coincident(g392,g393)
    c: Coincident(g393,g394)
    c: Coincident(g394,g395)
    c: Coincident(g395,g396)
    c: Coincident(g396,g397)
    c: Coincident(g397,g398)
    c: Coincident(g398,g399)
    c: Coincident(g399,g328)
    c: Coincident(g400,g401)
    c: Coincident(g401,g402)
    c: Coincident(g402,g403)
    c: Coincident(g403,g404)
    c: Coincident(g404,g405)
    c: Coincident(g405,g406)
    c: Coincident(g406,g407)
    c: Coincident(g407,g408)
    c: Coincident(g408,g409)
    c: Coincident(g409,g410)
    c: Coincident(g410,g411)
    c: Coincident(g411,g412)
    c: Coincident(g412,g413)
    c: Coincident(g413,g414)
    c: Coincident(g414,g415)
    c: Coincident(g415,g416)
    c: Coincident(g416,g417)
    c: Coincident(g417,g418)
    c: Coincident(g418,g419)
    c: Coincident(g419,g420)
    c: Coincident(g420,g421)
    c: Coincident(g421,g422)
    c: Coincident(g422,g423)
    c: Coincident(g423,g400)
    c: Coincident(g424,g425)
    c: Coincident(g425,g426)
    c: Coincident(g426,g427)
    c: Coincident(g427,g428)
    c: Coincident(g428,g429)
    c: Coincident(g429,g430)
    c: Coincident(g430,g431)
    c: Coincident(g431,g432)
    c: Coincident(g432,g433)
    c: Coincident(g433,g434)
    c: Coincident(g434,g435)
    c: Coincident(g435,g436)
    c: Coincident(g436,g437)
    c: Coincident(g437,g438)
    c: Coincident(g438,g439)
    c: Coincident(g439,g440)
    c: Coincident(g440,g441)
    c: Coincident(g441,g442)
    c: Coincident(g442,g443)
    c: Coincident(g443,g444)
    c: Coincident(g444,g445)
    c: Coincident(g445,g446)
    c: Coincident(g446,g447)
    c: Coincident(g447,g448)
    c: Coincident(g448,g449)
    c: Coincident(g449,g450)
    c: Coincident(g450,g451)
    c: Coincident(g451,g452)
    c: Coincident(g452,g453)
    c: Coincident(g453,g454)
    c: Coincident(g454,g455)
    c: Coincident(g455,g456)
    c: Coincident(g456,g457)
    c: Coincident(g457,g458)
    c: Coincident(g458,g459)
    c: Coincident(g459,g460)
    c: Coincident(g460,g461)
    c: Coincident(g461,g462)
    c: Coincident(g462,g463)
    c: Coincident(g463,g464)
    c: Coincident(g464,g465)
    c: Coincident(g465,g466)
    c: Coincident(g466,g467)
    c: Coincident(g467,g468)
    c: Coincident(g468,g469)
    c: Coincident(g469,g470)
    c: Coincident(g470,g471)
    c: Coincident(g471,g472)
    c: Coincident(g472,g473)
    c: Coincident(g473,g474)
    c: Coincident(g474,g475)
    c: Coincident(g475,g476)
    c: Coincident(g476,g477)
    c: Coincident(g477,g478)
    c: Coincident(g478,g479)
    c: Coincident(g479,g424)
    c: Coincident(g480,g481)
    c: Coincident(g481,g482)
    c: Coincident(g482,g483)
    c: Coincident(g483,g484)
    c: Coincident(g484,g485)
    c: Coincident(g485,g486)
    c: Coincident(g486,g487)
    c: Coincident(g487,g488)
    c: Coincident(g488,g489)
    c: Coincident(g489,g490)
    c: Coincident(g490,g491)
    c: Coincident(g491,g492)
    c: Coincident(g492,g493)
    c: Coincident(g493,g494)
    c: Coincident(g494,g495)
    c: Coincident(g495,g480)
    c: Coincident(g496,g497)
    c: Coincident(g497,g498)
    c: Coincident(g498,g499)
    c: Coincident(g499,g500)
    c: Coincident(g500,g501)
    c: Coincident(g501,g502)
    c: Coincident(g502,g503)
    c: Coincident(g503,g504)
    c: Coincident(g504,g505)
    c: Coincident(g505,g506)
    c: Coincident(g506,g507)
    c: Coincident(g507,g508)
    c: Coincident(g508,g509)
    c: Coincident(g509,g510)
    c: Coincident(g510,g511)
    c: Coincident(g511,g512)
    c: Coincident(g512,g513)
    c: Coincident(g513,g514)
    c: Coincident(g514,g515)
    c: Coincident(g515,g516)
    c: Coincident(g516,g517)
    c: Coincident(g517,g518)
    c: Coincident(g518,g519)
    c: Coincident(g519,g520)
    c: Coincident(g520,g521)
    c: Coincident(g521,g522)
    c: Coincident(g522,g523)
    c: Coincident(g523,g524)
    c: Coincident(g524,g525)
    c: Coincident(g525,g526)
    c: Coincident(g526,g527)
    c: Coincident(g527,g528)
    c: Coincident(g528,g529)
    c: Coincident(g529,g530)
    c: Coincident(g530,g531)
    c: Coincident(g531,g532)
    c: Coincident(g532,g533)
    c: Coincident(g533,g534)
    c: Coincident(g534,g535)
    c: Coincident(g535,g496)
    c: Coincident(g536,g537)
    c: Coincident(g537,g538)
    c: Coincident(g538,g539)
    c: Coincident(g539,g540)
    c: Coincident(g540,g541)
    c: Coincident(g541,g542)
    c: Coincident(g542,g543)
    c: Coincident(g543,g544)
    c: Coincident(g544,g545)
    c: Coincident(g545,g546)
    c: Coincident(g546,g547)
    c: Coincident(g547,g548)
    c: Coincident(g548,g549)
    c: Coincident(g549,g550)
    c: Coincident(g550,g551)
    c: Coincident(g551,g552)
    c: Coincident(g552,g553)
    c: Coincident(g553,g554)
    c: Coincident(g554,g555)
    c: Coincident(g555,g556)
    c: Coincident(g556,g557)
    c: Coincident(g557,g558)
    c: Coincident(g558,g559)
    c: Coincident(g559,g560)
    c: Coincident(g560,g561)
    c: Coincident(g561,g562)
    c: Coincident(g562,g563)
    c: Coincident(g563,g564)
    c: Coincident(g564,g565)
    c: Coincident(g565,g566)
    c: Coincident(g566,g567)
    c: Coincident(g567,g568)
    c: Coincident(g568,g569)
    c: Coincident(g569,g570)
    c: Coincident(g570,g571)
    c: Coincident(g571,g572)
    c: Coincident(g572,g573)
    c: Coincident(g573,g574)
    c: Coincident(g574,g575)
    c: Coincident(g575,g536)
    c: Coincident(g576,g577)
    c: Coincident(g577,g578)
    c: Coincident(g578,g579)
    c: Coincident(g579,g580)
    c: Coincident(g580,g581)
    c: Coincident(g581,g582)
    c: Coincident(g582,g583)
    c: Coincident(g583,g584)
    c: Coincident(g584,g585)
    c: Coincident(g585,g586)
    c: Coincident(g586,g587)
    c: Coincident(g587,g576)
    c: Coincident(g588,g589)
    c: Coincident(g589,g590)
    c: Coincident(g590,g591)
    c: Coincident(g591,g592)
    c: Coincident(g592,g593)
    c: Coincident(g593,g594)
    c: Coincident(g594,g595)
    c: Coincident(g595,g596)
    c: Coincident(g596,g597)
    c: Coincident(g597,g598)
    c: Coincident(g598,g599)
    c: Coincident(g599,g600)
    c: Coincident(g600,g601)
    c: Coincident(g601,g602)
    c: Coincident(g602,g603)
    c: Coincident(g603,g604)
    c: Coincident(g604,g605)
    c: Coincident(g605,g606)
    c: Coincident(g606,g607)
    c: Coincident(g607,g608)
    c: Coincident(g608,g609)
    c: Coincident(g609,g610)
    c: Coincident(g610,g611)
    c: Coincident(g611,g612)
    c: Coincident(g612,g613)
    c: Coincident(g613,g614)
    c: Coincident(g614,g615)
    c: Coincident(g615,g616)
    c: Coincident(g616,g617)
    c: Coincident(g617,g618)
    c: Coincident(g618,g619)
    c: Coincident(g619,g620)
    c: Coincident(g620,g621)
    c: Coincident(g621,g622)
    c: Coincident(g622,g623)
    c: Coincident(g623,g624)
    c: Coincident(g624,g625)
    c: Coincident(g625,g626)
    c: Coincident(g626,g627)
    c: Coincident(g627,g628)
    c: Coincident(g628,g629)
    c: Coincident(g629,g630)
    c: Coincident(g630,g631)
    c: Coincident(g631,g632)
    c: Coincident(g632,g633)
    c: Coincident(g633,g634)
    c: Coincident(g634,g635)
    c: Coincident(g635,g636)
    c: Coincident(g636,g637)
    c: Coincident(g637,g638)
    c: Coincident(g638,g639)
    c: Coincident(g639,g640)
    c: Coincident(g640,g641)
    c: Coincident(g641,g642)
    c: Coincident(g642,g643)
    c: Coincident(g643,g644)
    c: Coincident(g644,g645)
    c: Coincident(g645,g646)
    c: Coincident(g646,g647)
    c: Coincident(g647,g648)
    c: Coincident(g648,g649)
    c: Coincident(g649,g650)
    c: Coincident(g650,g651)
    c: Coincident(g651,g652)
    c: Coincident(g652,g653)
    c: Coincident(g653,g654)
    c: Coincident(g654,g655)
    c: Coincident(g655,g656)
    c: Coincident(g656,g657)
    c: Coincident(g657,g658)
    c: Coincident(g658,g659)
    c: Coincident(g659,g660)
    c: Coincident(g660,g661)
    c: Coincident(g661,g662)
    c: Coincident(g662,g663)
    c: Coincident(g663,g664)
    c: Coincident(g664,g665)
    c: Coincident(g665,g666)
    c: Coincident(g666,g667)
    c: Coincident(g667,g668)
    c: Coincident(g668,g669)
    c: Coincident(g669,g670)
    c: Coincident(g670,g671)
    c: Coincident(g671,g672)
    c: Coincident(g672,g673)
    c: Coincident(g673,g674)
    c: Coincident(g674,g675)
    c: Coincident(g675,g588)
    c: Coincident(g676,g677)
    c: Coincident(g677,g678)
    c: Coincident(g678,g679)
    c: Coincident(g679,g680)
    c: Coincident(g680,g681)
    c: Coincident(g681,g682)
    c: Coincident(g682,g683)
    c: Coincident(g683,g684)
    c: Coincident(g684,g685)
    c: Coincident(g685,g686)
    c: Coincident(g686,g687)
    c: Coincident(g687,g688)
    c: Coincident(g688,g689)
    c: Coincident(g689,g690)
    c: Coincident(g690,g691)
    c: Coincident(g691,g676)
    c: Coincident(g692,g693)
    c: Coincident(g693,g694)
    c: Coincident(g694,g695)
    c: Coincident(g695,g696)
    c: Coincident(g696,g697)
    c: Coincident(g697,g698)
    c: Coincident(g698,g699)
    c: Coincident(g699,g700)
    c: Coincident(g700,g701)
    c: Coincident(g701,g702)
    c: Coincident(g702,g703)
    c: Coincident(g703,g704)
    c: Coincident(g704,g705)
    c: Coincident(g705,g706)
    c: Coincident(g706,g707)
    c: Coincident(g707,g708)
    c: Coincident(g708,g709)
    c: Coincident(g709,g710)
    c: Coincident(g710,g711)
    c: Coincident(g711,g712)
    c: Coincident(g712,g713)
    c: Coincident(g713,g714)
    c: Coincident(g714,g715)
    c: Coincident(g715,g716)
    c: Coincident(g716,g717)
    c: Coincident(g717,g718)
    c: Coincident(g718,g719)
    c: Coincident(g719,g720)
    c: Coincident(g720,g721)
    c: Coincident(g721,g722)
    c: Coincident(g722,g723)
    c: Coincident(g723,g724)
    c: Coincident(g724,g725)
    c: Coincident(g725,g726)
    c: Coincident(g726,g727)
    c: Coincident(g727,g728)
    c: Coincident(g728,g729)
    c: Coincident(g729,g730)
    c: Coincident(g730,g731)
    c: Coincident(g731,g692)
    c: Coincident(g732,g733)
    c: Coincident(g733,g734)
    c: Coincident(g734,g735)
    c: Coincident(g735,g736)
    c: Coincident(g736,g737)
    c: Coincident(g737,g738)
    c: Coincident(g738,g739)
    c: Coincident(g739,g740)
    c: Coincident(g740,g741)
    c: Coincident(g741,g742)
    c: Coincident(g742,g743)
    c: Coincident(g743,g744)
    c: Coincident(g744,g745)
    c: Coincident(g745,g746)
    c: Coincident(g746,g747)
    c: Coincident(g747,g748)
    c: Coincident(g748,g749)
    c: Coincident(g749,g750)
    c: Coincident(g750,g751)
    c: Coincident(g751,g752)
    c: Coincident(g752,g753)
    c: Coincident(g753,g754)
    c: Coincident(g754,g755)
    c: Coincident(g755,g756)
    c: Coincident(g756,g757)
    c: Coincident(g757,g758)
    c: Coincident(g758,g759)
    c: Coincident(g759,g760)
    c: Coincident(g760,g761)
    c: Coincident(g761,g762)
    c: Coincident(g762,g763)
    c: Coincident(g763,g732)
    c: Coincident(g764,g765)
    c: Coincident(g765,g766)
    c: Coincident(g766,g767)
    c: Coincident(g767,g768)
    c: Coincident(g768,g769)
    c: Coincident(g769,g770)
    c: Coincident(g770,g771)
    c: Coincident(g771,g772)
    c: Coincident(g772,g773)
    c: Coincident(g773,g774)
    c: Coincident(g774,g775)
    c: Coincident(g775,g776)
    c: Coincident(g776,g777)
    c: Coincident(g777,g778)
    c: Coincident(g778,g779)
    c: Coincident(g779,g780)
    c: Coincident(g780,g781)
    c: Coincident(g781,g782)
    c: Coincident(g782,g783)
    c: Coincident(g783,g784)
    c: Coincident(g784,g785)
    c: Coincident(g785,g786)
    c: Coincident(g786,g787)
    c: Coincident(g787,g764)
    c: Coincident(g788,g789)
    c: Coincident(g789,g790)
    c: Coincident(g790,g791)
    c: Coincident(g791,g792)
    c: Coincident(g792,g793)
    c: Coincident(g793,g794)
    c: Coincident(g794,g795)
    c: Coincident(g795,g796)
    c: Coincident(g796,g797)
    c: Coincident(g797,g798)
    c: Coincident(g798,g799)
    c: Coincident(g799,g800)
    c: Coincident(g800,g801)
    c: Coincident(g801,g802)
    c: Coincident(g802,g803)
    c: Coincident(g803,g804)
    c: Coincident(g804,g805)
    c: Coincident(g805,g806)
    c: Coincident(g806,g807)
    c: Coincident(g807,g808)
    c: Coincident(g808,g809)
    c: Coincident(g809,g810)
    c: Coincident(g810,g811)
    c: Coincident(g811,g812)
    c: Coincident(g812,g813)
    c: Coincident(g813,g814)
    c: Coincident(g814,g815)
    c: Coincident(g815,g816)
    c: Coincident(g816,g817)
    c: Coincident(g817,g818)
    c: Coincident(g818,g819)
    c: Coincident(g819,g820)
    c: Coincident(g820,g821)
    c: Coincident(g821,g822)
    c: Coincident(g822,g823)
    c: Coincident(g823,g824)
    c: Coincident(g824,g825)
    c: Coincident(g825,g826)
    c: Coincident(g826,g827)
    c: Coincident(g827,g828)
    c: Coincident(g828,g829)
    c: Coincident(g829,g830)
    c: Coincident(g830,g831)
    c: Coincident(g831,g832)
    c: Coincident(g832,g833)
    c: Coincident(g833,g834)
    c: Coincident(g834,g835)
    c: Coincident(g835,g836)
    c: Coincident(g836,g837)
    c: Coincident(g837,g838)
    c: Coincident(g838,g839)
    c: Coincident(g839,g840)
    c: Coincident(g840,g841)
    c: Coincident(g841,g842)
    c: Coincident(g842,g843)
    c: Coincident(g843,g844)
    c: Coincident(g844,g845)
    c: Coincident(g845,g846)
    c: Coincident(g846,g847)
    c: Coincident(g847,g848)
    c: Coincident(g848,g849)
    c: Coincident(g849,g850)
    c: Coincident(g850,g851)
    c: Coincident(g851,g852)
    c: Coincident(g852,g853)
    c: Coincident(g853,g854)
    c: Coincident(g854,g855)
    c: Coincident(g855,g856)
    c: Coincident(g856,g857)
    c: Coincident(g857,g858)
    c: Coincident(g858,g859)
    c: Coincident(g859,g788)
FEATURE [Sketcher::SketchObject] Sketch023  label="16 Bit VS004"
  FullyConstrained = false
  Placement = pos=(8.14,18.75,-4) rot=(1,0,0;3.14159rad)
  sketch-geometry (860):
    g0: BSplineCurve PolesCount=2 KnotsCount=2 Degree=1 IsPeriodic=0
    g1: BSplineCurve PolesCount=2 KnotsCount=2 Degree=1 IsPeriodic=0
    g2: BSplineCurve PolesCount=2 KnotsCount=2 Degree=1 IsPeriodic=0
    g3: BSplineCurve PolesCount=2 KnotsCount=2 Degree=1 IsPeriodic=0
    g4: BSplineCurve PolesCount=2 KnotsCount=2 Degree=1 IsPeriodic=0
    g5: BSplineCurve PolesCount=2 KnotsCount=2 Degree=1 IsPeriodic=0
    g6: BSplineCurve PolesCount=2 KnotsCount=2 Degree=1 IsPeriodic=0
    g7: BSplineCurve PolesCount=2 KnotsCount=2 Degree=1 IsPeriodic=0
    g8: BSplineCurve PolesCount=2 KnotsCount=2 Degree=1 IsPeriodic=0
    g9: BSplineCurve PolesCount=2 KnotsCount=2 Degree=1 IsPeriodic=0
    g10: BSplineCurve PolesCount=2 KnotsCount=2 Degree=1 IsPeriodic=0
    g11: BSplineCurve PolesCount=2 KnotsCount=2 Degree=1 IsPeriodic=0
    g12: BSplineCurve PolesCount=2 KnotsCount=2 Degree=1 IsPeriodic=0
    g13: BSplineCurve PolesCount=2 KnotsCount=2 Degree=1 IsPeriodic=0
    g14: BSplineCurve PolesCount=2 KnotsCount=2 Degree=1 IsPeriodic=0
    g15: BSplineCurve PolesCount=2 KnotsCount=2 Degree=1 IsPeriodic=0
    g16: BSplineCurve PolesCount=2 KnotsCount=2 Degree=1 IsPeriodic=0
    g17: BSplineCurve PolesCount=2 KnotsCount=2 Degree=1 IsPeriodic=0
    g18: BSplineCurve PolesCount=2 KnotsCount=2 Degree=1 IsPeriodic=0
    g19: BSplineCurve PolesCount=2 KnotsCount=2 Degree=1 IsPeriodic=0
    g20: BSplineCurve PolesCount=2 KnotsCount=2 Degree=1 IsPeriodic=0
    g21: BSplineCurve PolesCount=2 KnotsCount=2 Degree=1 IsPeriodic=0
    g22: BSplineCurve PolesCount=2 KnotsCount=2 Degree=1 IsPeriodic=0
    g23: BSplineCurve PolesCount=2 KnotsCount=2 Degree=1 IsPeriodic=0
    g24: BSplineCurve PolesCount=2 KnotsCount=2 Degree=1 IsPeriodic=0
    g25: BSplineCurve PolesCount=2 KnotsCount=2 Degree=1 IsPeriodic=0
    g26: BSplineCurve PolesCount=2 KnotsCount=2 Degree=1 IsPeriodic=0
    g27: BSplineCurve PolesCount=2 KnotsCount=2 Degree=1 IsPeriodic=0
    g28: BSplineCurve PolesCount=2 KnotsCount=2 Degree=1 IsPeriodic=0
    g29: BSplineCurve PolesCount=2 KnotsCount=2 Degree=1 IsPeriodic=0
    g30: BSplineCurve PolesCount=2 KnotsCount=2 Degree=1 IsPeriodic=0
    g31: BSplineCurve PolesCount=2 KnotsCount=2 Degree=1 IsPeriodic=0
    g32: BSplineCurve PolesCount=2 KnotsCount=2 Degree=1 IsPeriodic=0
    g33: BSplineCurve PolesCount=2 KnotsCount=2 Degree=1 IsPeriodic=0
    g34: BSplineCurve PolesCount=2 KnotsCount=2 Degree=1 IsPeriodic=0
    g35: BSplineCurve PolesCount=2 KnotsCount=2 Degree=1 IsPeriodic=0
    g36: BSplineCurve PolesCount=2 KnotsCount=2 Degree=1 IsPeriodic=0
    g37: BSplineCurve PolesCount=2 KnotsCount=2 Degree=1 IsPeriodic=0
    g38: BSplineCurve PolesCount=2 KnotsCount=2 Degree=1 IsPeriodic=0
    g39: BSplineCurve PolesCount=2 KnotsCount=2 Degree=1 IsPeriodic=0
    g40: BSplineCurve PolesCount=2 KnotsCount=2 Degree=1 IsPeriodic=0
    g41: BSplineCurve PolesCount=2 KnotsCount=2 Degree=1 IsPeriodic=0
    g42: BSplineCurve PolesCount=2 KnotsCount=2 Degree=1 IsPeriodic=0
    g43: BSplineCurve PolesCount=2 KnotsCount=2 Degree=1 IsPeriodic=0
    g44: BSplineCurve PolesCount=2 KnotsCount=2 Degree=1 IsPeriodic=0
    g45: BSplineCurve PolesCount=2 KnotsCount=2 Degree=1 IsPeriodic=0
    g46: BSplineCurve PolesCount=2 KnotsCount=2 Degree=1 IsPeriodic=0
    g47: BSplineCurve PolesCount=2 KnotsCount=2 Degree=1 IsPeriodic=0
    g48: BSplineCurve PolesCount=2 KnotsCount=2 Degree=1 IsPeriodic=0
    g49: BSplineCurve PolesCount=2 KnotsCount=2 Degree=1 IsPeriodic=0
    g50: BSplineCurve PolesCount=2 KnotsCount=2 Degree=1 IsPeriodic=0
    g51: BSplineCurve PolesCount=2 KnotsCount=2 Degree=1 IsPeriodic=0
    g52: BSplineCurve PolesCount=2 KnotsCount=2 Degree=1 IsPeriodic=0
    g53: BSplineCurve PolesCount=2 KnotsCount=2 Degree=1 IsPeriodic=0
    g54: BSplineCurve PolesCount=2 KnotsCount=2 Degree=1 IsPeriodic=0
    g55: BSplineCurve PolesCount=2 KnotsCount=2 Degree=1 IsPeriodic=0
    g56: BSplineCurve PolesCount=2 KnotsCount=2 Degree=1 IsPeriodic=0
    g57: BSplineCurve PolesCount=2 KnotsCount=2 Degree=1 IsPeriodic=0
    g58: BSplineCurve PolesCount=2 KnotsCount=2 Degree=1 IsPeriodic=0
    g59: BSplineCurve PolesCount=2 KnotsCount=2 Degree=1 IsPeriodic=0
    g60: BSplineCurve PolesCount=2 KnotsCount=2 Degree=1 IsPeriodic=0
    g61: BSplineCurve PolesCount=2 KnotsCount=2 Degree=1 IsPeriodic=0
    g62: BSplineCurve PolesCount=2 KnotsCount=2 Degree=1 IsPeriodic=0
    g63: BSplineCurve PolesCount=2 KnotsCount=2 Degree=1 IsPeriodic=0
    g64: BSplineCurve PolesCount=2 KnotsCount=2 Degree=1 IsPeriodic=0
    g65: BSplineCurve PolesCount=2 KnotsCount=2 Degree=1 IsPeriodic=0
    g66: BSplineCurve PolesCount=2 KnotsCount=2 Degree=1 IsPeriodic=0
    g67: BSplineCurve PolesCount=2 KnotsCount=2 Degree=1 IsPeriodic=0
    g68: BSplineCurve PolesCount=2 KnotsCount=2 Degree=1 IsPeriodic=0
    g69: BSplineCurve PolesCount=2 KnotsCount=2 Degree=1 IsPeriodic=0
    g70: BSplineCurve PolesCount=2 KnotsCount=2 Degree=1 IsPeriodic=0
    g71: BSplineCurve PolesCount=2 KnotsCount=2 Degree=1 IsPeriodic=0
    g72: BSplineCurve PolesCount=2 KnotsCount=2 Degree=1 IsPeriodic=0
    g73: BSplineCurve PolesCount=2 KnotsCount=2 Degree=1 IsPeriodic=0
    g74: BSplineCurve PolesCount=2 KnotsCount=2 Degree=1 IsPeriodic=0
    g75: BSplineCurve PolesCount=2 KnotsCount=2 Degree=1 IsPeriodic=0
    g76: BSplineCurve PolesCount=2 KnotsCount=2 Degree=1 IsPeriodic=0
    g77: BSplineCurve PolesCount=2 KnotsCount=2 Degree=1 IsPeriodic=0
    g78: BSplineCurve PolesCount=2 KnotsCount=2 Degree=1 IsPeriodic=0
    g79: BSplineCurve PolesCount=2 KnotsCount=2 Degree=1 IsPeriodic=0
    g80: BSplineCurve PolesCount=2 KnotsCount=2 Degree=1 IsPeriodic=0
    g81: BSplineCurve PolesCount=2 KnotsCount=2 Degree=1 IsPeriodic=0
    g82: BSplineCurve PolesCount=2 KnotsCount=2 Degree=1 IsPeriodic=0
    g83: BSplineCurve PolesCount=2 KnotsCount=2 Degree=1 IsPeriodic=0
    g84: BSplineCurve PolesCount=2 KnotsCount=2 Degree=1 IsPeriodic=0
    g85: BSplineCurve PolesCount=2 KnotsCount=2 Degree=1 IsPeriodic=0
    g86: BSplineCurve PolesCount=2 KnotsCount=2 Degree=1 IsPeriodic=0
    g87: BSplineCurve PolesCount=2 KnotsCount=2 Degree=1 IsPeriodic=0
    g88: BSplineCurve PolesCount=2 KnotsCount=2 Degree=1 IsPeriodic=0
    g89: BSplineCurve PolesCount=2 KnotsCount=2 Degree=1 IsPeriodic=0
    g90: BSplineCurve PolesCount=2 KnotsCount=2 Degree=1 IsPeriodic=0
    g91: BSplineCurve PolesCount=2 KnotsCount=2 Degree=1 IsPeriodic=0
    g92: BSplineCurve PolesCount=2 KnotsCount=2 Degree=1 IsPeriodic=0
    g93: BSplineCurve PolesCount=2 KnotsCount=2 Degree=1 IsPeriodic=0
    g94: BSplineCurve PolesCount=2 KnotsCount=2 Degree=1 IsPeriodic=0
    g95: BSplineCurve PolesCount=2 KnotsCount=2 Degree=1 IsPeriodic=0
    g96: BSplineCurve PolesCount=2 KnotsCount=2 Degree=1 IsPeriodic=0
    g97: BSplineCurve PolesCount=2 KnotsCount=2 Degree=1 IsPeriodic=0
    g98: BSplineCurve PolesCount=2 KnotsCount=2 Degree=1 IsPeriodic=0
    g99: BSplineCurve PolesCount=2 KnotsCount=2 Degree=1 IsPeriodic=0
    g100: BSplineCurve PolesCount=2 KnotsCount=2 Degree=1 IsPeriodic=0
    g101: BSplineCurve PolesCount=2 KnotsCount=2 Degree=1 IsPeriodic=0
    g102: BSplineCurve PolesCount=2 KnotsCount=2 Degree=1 IsPeriodic=0
    g103: BSplineCurve PolesCount=2 KnotsCount=2 Degree=1 IsPeriodic=0
    g104: BSplineCurve PolesCount=2 KnotsCount=2 Degree=1 IsPeriodic=0
    g105: BSplineCurve PolesCount=2 KnotsCount=2 Degree=1 IsPeriodic=0
    g106: BSplineCurve PolesCount=2 KnotsCount=2 Degree=1 IsPeriodic=0
    g107: BSplineCurve PolesCount=2 KnotsCount=2 Degree=1 IsPeriodic=0
    g108: BSplineCurve PolesCount=2 KnotsCount=2 Degree=1 IsPeriodic=0
    g109: BSplineCurve PolesCount=2 KnotsCount=2 Degree=1 IsPeriodic=0
    g110: BSplineCurve PolesCount=2 KnotsCount=2 Degree=1 IsPeriodic=0
    g111: BSplineCurve PolesCount=2 KnotsCount=2 Degree=1 IsPeriodic=0
    g112: BSplineCurve PolesCount=2 KnotsCount=2 Degree=1 IsPeriodic=0
    g113: BSplineCurve PolesCount=2 KnotsCount=2 Degree=1 IsPeriodic=0
    g114: BSplineCurve PolesCount=2 KnotsCount=2 Degree=1 IsPeriodic=0
    g115: BSplineCurve PolesCount=2 KnotsCount=2 Degree=1 IsPeriodic=0
    g116: BSplineCurve PolesCount=2 KnotsCount=2 Degree=1 IsPeriodic=0
    g117: BSplineCurve PolesCount=2 KnotsCount=2 Degree=1 IsPeriodic=0
    g118: BSplineCurve PolesCount=2 KnotsCount=2 Degree=1 IsPeriodic=0
    g119: BSplineCurve PolesCount=2 KnotsCount=2 Degree=1 IsPeriodic=0
    g120: BSplineCurve PolesCount=2 KnotsCount=2 Degree=1 IsPeriodic=0
    g121: BSplineCurve PolesCount=2 KnotsCount=2 Degree=1 IsPeriodic=0
    g122: BSplineCurve PolesCount=2 KnotsCount=2 Degree=1 IsPeriodic=0
    g123: BSplineCurve PolesCount=2 KnotsCount=2 Degree=1 IsPeriodic=0
    g124: BSplineCurve PolesCount=2 KnotsCount=2 Degree=1 IsPeriodic=0
    g125: BSplineCurve PolesCount=2 KnotsCount=2 Degree=1 IsPeriodic=0
    g126: BSplineCurve PolesCount=2 KnotsCount=2 Degree=1 IsPeriodic=0
    g127: BSplineCurve PolesCount=2 KnotsCount=2 Degree=1 IsPeriodic=0
    g128: BSplineCurve PolesCount=2 KnotsCount=2 Degree=1 IsPeriodic=0
    g129: BSplineCurve PolesCount=2 KnotsCount=2 Degree=1 IsPeriodic=0
    g130: BSplineCurve PolesCount=2 KnotsCount=2 Degree=1 IsPeriodic=0
    g131: BSplineCurve PolesCount=2 KnotsCount=2 Degree=1 IsPeriodic=0
    g132: BSplineCurve PolesCount=2 KnotsCount=2 Degree=1 IsPeriodic=0
    g133: BSplineCurve PolesCount=2 KnotsCount=2 Degree=1 IsPeriodic=0
    g134: BSplineCurve PolesCount=2 KnotsCount=2 Degree=1 IsPeriodic=0
    g135: BSplineCurve PolesCount=2 KnotsCount=2 Degree=1 IsPeriodic=0
    g136: BSplineCurve PolesCount=2 KnotsCount=2 Degree=1 IsPeriodic=0
    g137: BSplineCurve PolesCount=2 KnotsCount=2 Degree=1 IsPeriodic=0
    g138: BSplineCurve PolesCount=2 KnotsCount=2 Degree=1 IsPeriodic=0
    g139: BSplineCurve PolesCount=2 KnotsCount=2 Degree=1 IsPeriodic=0
    g140: BSplineCurve PolesCount=2 KnotsCount=2 Degree=1 IsPeriodic=0
    g141: BSplineCurve PolesCount=2 KnotsCount=2 Degree=1 IsPeriodic=0
    g142: BSplineCurve PolesCount=2 KnotsCount=2 Degree=1 IsPeriodic=0
    g143: BSplineCurve PolesCount=2 KnotsCount=2 Degree=1 IsPeriodic=0
    g144: BSplineCurve PolesCount=2 KnotsCount=2 Degree=1 IsPeriodic=0
    g145: BSplineCurve PolesCount=2 KnotsCount=2 Degree=1 IsPeriodic=0
    g146: BSplineCurve PolesCount=2 KnotsCount=2 Degree=1 IsPeriodic=0
    g147: BSplineCurve PolesCount=2 KnotsCount=2 Degree=1 IsPeriodic=0
    g148: BSplineCurve PolesCount=2 KnotsCount=2 Degree=1 IsPeriodic=0
    g149: BSplineCurve PolesCount=2 KnotsCount=2 Degree=1 IsPeriodic=0
    g150: BSplineCurve PolesCount=2 KnotsCount=2 Degree=1 IsPeriodic=0
    g151: BSplineCurve PolesCount=2 KnotsCount=2 Degree=1 IsPeriodic=0
    g152: BSplineCurve PolesCount=2 KnotsCount=2 Degree=1 IsPeriodic=0
    g153: BSplineCurve PolesCount=2 KnotsCount=2 Degree=1 IsPeriodic=0
    g154: BSplineCurve PolesCount=2 KnotsCount=2 Degree=1 IsPeriodic=0
    g155: BSplineCurve PolesCount=2 KnotsCount=2 Degree=1 IsPeriodic=0
    g156: BSplineCurve PolesCount=2 KnotsCount=2 Degree=1 IsPeriodic=0
    g157: BSplineCurve PolesCount=2 KnotsCount=2 Degree=1 IsPeriodic=0
    g158: BSplineCurve PolesCount=2 KnotsCount=2 Degree=1 IsPeriodic=0
    g159: BSplineCurve PolesCount=2 KnotsCount=2 Degree=1 IsPeriodic=0
    g160: BSplineCurve PolesCount=2 KnotsCount=2 Degree=1 IsPeriodic=0
    g161: BSplineCurve PolesCount=2 KnotsCount=2 Degree=1 IsPeriodic=0
    g162: BSplineCurve PolesCount=2 KnotsCount=2 Degree=1 IsPeriodic=0
    g163: BSplineCurve PolesCount=2 KnotsCount=2 Degree=1 IsPeriodic=0
    g164: BSplineCurve PolesCount=2 KnotsCount=2 Degree=1 IsPeriodic=0
    g165: BSplineCurve PolesCount=2 KnotsCount=2 Degree=1 IsPeriodic=0
    g166: BSplineCurve PolesCount=2 KnotsCount=2 Degree=1 IsPeriodic=0
    g167: BSplineCurve PolesCount=2 KnotsCount=2 Degree=1 IsPeriodic=0
    g168: BSplineCurve PolesCount=2 KnotsCount=2 Degree=1 IsPeriodic=0
    g169: BSplineCurve PolesCount=2 KnotsCount=2 Degree=1 IsPeriodic=0
    g170: BSplineCurve PolesCount=2 KnotsCount=2 Degree=1 IsPeriodic=0
    g171: BSplineCurve PolesCount=2 KnotsCount=2 Degree=1 IsPeriodic=0
    g172: BSplineCurve PolesCount=2 KnotsCount=2 Degree=1 IsPeriodic=0
    g173: BSplineCurve PolesCount=2 KnotsCount=2 Degree=1 IsPeriodic=0
    g174: BSplineCurve PolesCount=2 KnotsCount=2 Degree=1 IsPeriodic=0
    g175: BSplineCurve PolesCount=2 KnotsCount=2 Degree=1 IsPeriodic=0
    g176: BSplineCurve PolesCount=2 KnotsCount=2 Degree=1 IsPeriodic=0
    g177: BSplineCurve PolesCount=2 KnotsCount=2 Degree=1 IsPeriodic=0
    g178: BSplineCurve PolesCount=2 KnotsCount=2 Degree=1 IsPeriodic=0
    g179: BSplineCurve PolesCount=2 KnotsCount=2 Degree=1 IsPeriodic=0
    g180: BSplineCurve PolesCount=2 KnotsCount=2 Degree=1 IsPeriodic=0
    g181: BSplineCurve PolesCount=2 KnotsCount=2 Degree=1 IsPeriodic=0
    g182: BSplineCurve PolesCount=2 KnotsCount=2 Degree=1 IsPeriodic=0
    g183: BSplineCurve PolesCount=2 KnotsCount=2 Degree=1 IsPeriodic=0
    g184: BSplineCurve PolesCount=2 KnotsCount=2 Degree=1 IsPeriodic=0
    g185: BSplineCurve PolesCount=2 KnotsCount=2 Degree=1 IsPeriodic=0
    g186: BSplineCurve PolesCount=2 KnotsCount=2 Degree=1 IsPeriodic=0
    g187: BSplineCurve PolesCount=2 KnotsCount=2 Degree=1 IsPeriodic=0
    g188: BSplineCurve PolesCount=2 KnotsCount=2 Degree=1 IsPeriodic=0
    g189: BSplineCurve PolesCount=2 KnotsCount=2 Degree=1 IsPeriodic=0
    g190: BSplineCurve PolesCount=2 KnotsCount=2 Degree=1 IsPeriodic=0
    g191: BSplineCurve PolesCount=2 KnotsCount=2 Degree=1 IsPeriodic=0
    g192: BSplineCurve PolesCount=2 KnotsCount=2 Degree=1 IsPeriodic=0
    g193: BSplineCurve PolesCount=2 KnotsCount=2 Degree=1 IsPeriodic=0
    g194: BSplineCurve PolesCount=2 KnotsCount=2 Degree=1 IsPeriodic=0
    g195: BSplineCurve PolesCount=2 KnotsCount=2 Degree=1 IsPeriodic=0
    g196: BSplineCurve PolesCount=2 KnotsCount=2 Degree=1 IsPeriodic=0
    g197: BSplineCurve PolesCount=2 KnotsCount=2 Degree=1 IsPeriodic=0
    g198: BSplineCurve PolesCount=2 KnotsCount=2 Degree=1 IsPeriodic=0
    g199: BSplineCurve PolesCount=2 KnotsCount=2 Degree=1 IsPeriodic=0
    g200: BSplineCurve PolesCount=2 KnotsCount=2 Degree=1 IsPeriodic=0
    g201: BSplineCurve PolesCount=2 KnotsCount=2 Degree=1 IsPeriodic=0
    g202: BSplineCurve PolesCount=2 KnotsCount=2 Degree=1 IsPeriodic=0
    g203: BSplineCurve PolesCount=2 KnotsCount=2 Degree=1 IsPeriodic=0
    g204: BSplineCurve PolesCount=2 KnotsCount=2 Degree=1 IsPeriodic=0
    g205: BSplineCurve PolesCount=2 KnotsCount=2 Degree=1 IsPeriodic=0
    g206: BSplineCurve PolesCount=2 KnotsCount=2 Degree=1 IsPeriodic=0
    g207: BSplineCurve PolesCount=2 KnotsCount=2 Degree=1 IsPeriodic=0
    g208: BSplineCurve PolesCount=2 KnotsCount=2 Degree=1 IsPeriodic=0
    g209: BSplineCurve PolesCount=2 KnotsCount=2 Degree=1 IsPeriodic=0
    g210: BSplineCurve PolesCount=2 KnotsCount=2 Degree=1 IsPeriodic=0
    g211: BSplineCurve PolesCount=2 KnotsCount=2 Degree=1 IsPeriodic=0
    g212: BSplineCurve PolesCount=2 KnotsCount=2 Degree=1 IsPeriodic=0
    g213: BSplineCurve PolesCount=2 KnotsCount=2 Degree=1 IsPeriodic=0
    g214: BSplineCurve PolesCount=2 KnotsCount=2 Degree=1 IsPeriodic=0
    g215: BSplineCurve PolesCount=2 KnotsCount=2 Degree=1 IsPeriodic=0
    g216: BSplineCurve PolesCount=2 KnotsCount=2 Degree=1 IsPeriodic=0
    g217: BSplineCurve PolesCount=2 KnotsCount=2 Degree=1 IsPeriodic=0
    g218: BSplineCurve PolesCount=2 KnotsCount=2 Degree=1 IsPeriodic=0
    g219: BSplineCurve PolesCount=2 KnotsCount=2 Degree=1 IsPeriodic=0
    g220: BSplineCurve PolesCount=2 KnotsCount=2 Degree=1 IsPeriodic=0
    g221: BSplineCurve PolesCount=2 KnotsCount=2 Degree=1 IsPeriodic=0
    g222: BSplineCurve PolesCount=2 KnotsCount=2 Degree=1 IsPeriodic=0
    g223: BSplineCurve PolesCount=2 KnotsCount=2 Degree=1 IsPeriodic=0
    g224: BSplineCurve PolesCount=2 KnotsCount=2 Degree=1 IsPeriodic=0
    g225: BSplineCurve PolesCount=2 KnotsCount=2 Degree=1 IsPeriodic=0
    g226: BSplineCurve PolesCount=2 KnotsCount=2 Degree=1 IsPeriodic=0
    g227: BSplineCurve PolesCount=2 KnotsCount=2 Degree=1 IsPeriodic=0
    g228: BSplineCurve PolesCount=2 KnotsCount=2 Degree=1 IsPeriodic=0
    g229: BSplineCurve PolesCount=2 KnotsCount=2 Degree=1 IsPeriodic=0
    g230: BSplineCurve PolesCount=2 KnotsCount=2 Degree=1 IsPeriodic=0
    g231: BSplineCurve PolesCount=2 KnotsCount=2 Degree=1 IsPeriodic=0
    g232: BSplineCurve PolesCount=2 KnotsCount=2 Degree=1 IsPeriodic=0
    g233: BSplineCurve PolesCount=2 KnotsCount=2 Degree=1 IsPeriodic=0
    g234: BSplineCurve PolesCount=2 KnotsCount=2 Degree=1 IsPeriodic=0
    g235: BSplineCurve PolesCount=2 KnotsCount=2 Degree=1 IsPeriodic=0
    g236: BSplineCurve PolesCount=2 KnotsCount=2 Degree=1 IsPeriodic=0
    g237: BSplineCurve PolesCount=2 KnotsCount=2 Degree=1 IsPeriodic=0
    g238: BSplineCurve PolesCount=2 KnotsCount=2 Degree=1 IsPeriodic=0
    g239: BSplineCurve PolesCount=2 KnotsCount=2 Degree=1 IsPeriodic=0
    g240: BSplineCurve PolesCount=2 KnotsCount=2 Degree=1 IsPeriodic=0
    g241: BSplineCurve PolesCount=2 KnotsCount=2 Degree=1 IsPeriodic=0
    g242: BSplineCurve PolesCount=2 KnotsCount=2 Degree=1 IsPeriodic=0
    g243: BSplineCurve PolesCount=2 KnotsCount=2 Degree=1 IsPeriodic=0
    g244: BSplineCurve PolesCount=2 KnotsCount=2 Degree=1 IsPeriodic=0
    g245: BSplineCurve PolesCount=2 KnotsCount=2 Degree=1 IsPeriodic=0
    g246: BSplineCurve PolesCount=2 KnotsCount=2 Degree=1 IsPeriodic=0
    g247: BSplineCurve PolesCount=2 KnotsCount=2 Degree=1 IsPeriodic=0
    g248: BSplineCurve PolesCount=2 KnotsCount=2 Degree=1 IsPeriodic=0
    g249: BSplineCurve PolesCount=2 KnotsCount=2 Degree=1 IsPeriodic=0
    g250: BSplineCurve PolesCount=2 KnotsCount=2 Degree=1 IsPeriodic=0
    g251: BSplineCurve PolesCount=2 KnotsCount=2 Degree=1 IsPeriodic=0
    g252: BSplineCurve PolesCount=2 KnotsCount=2 Degree=1 IsPeriodic=0
    g253: BSplineCurve PolesCount=2 KnotsCount=2 Degree=1 IsPeriodic=0
    g254: BSplineCurve PolesCount=2 KnotsCount=2 Degree=1 IsPeriodic=0
    g255: BSplineCurve PolesCount=2 KnotsCount=2 Degree=1 IsPeriodic=0
    g256: BSplineCurve PolesCount=2 KnotsCount=2 Degree=1 IsPeriodic=0
    g257: BSplineCurve PolesCount=2 KnotsCount=2 Degree=1 IsPeriodic=0
    g258: BSplineCurve PolesCount=2 KnotsCount=2 Degree=1 IsPeriodic=0
    g259: BSplineCurve PolesCount=2 KnotsCount=2 Degree=1 IsPeriodic=0
    g260: BSplineCurve PolesCount=2 KnotsCount=2 Degree=1 IsPeriodic=0
    g261: BSplineCurve PolesCount=2 KnotsCount=2 Degree=1 IsPeriodic=0
    g262: BSplineCurve PolesCount=2 KnotsCount=2 Degree=1 IsPeriodic=0
    g263: BSplineCurve PolesCount=2 KnotsCount=2 Degree=1 IsPeriodic=0
    g264: BSplineCurve PolesCount=2 KnotsCount=2 Degree=1 IsPeriodic=0
    g265: BSplineCurve PolesCount=2 KnotsCount=2 Degree=1 IsPeriodic=0
    g266: BSplineCurve PolesCount=2 KnotsCount=2 Degree=1 IsPeriodic=0
    g267: BSplineCurve PolesCount=2 KnotsCount=2 Degree=1 IsPeriodic=0
    g268: BSplineCurve PolesCount=2 KnotsCount=2 Degree=1 IsPeriodic=0
    g269: BSplineCurve PolesCount=2 KnotsCount=2 Degree=1 IsPeriodic=0
    g270: BSplineCurve PolesCount=2 KnotsCount=2 Degree=1 IsPeriodic=0
    g271: BSplineCurve PolesCount=2 KnotsCount=2 Degree=1 IsPeriodic=0
    g272: BSplineCurve PolesCount=2 KnotsCount=2 Degree=1 IsPeriodic=0
    g273: BSplineCurve PolesCount=2 KnotsCount=2 Degree=1 IsPeriodic=0
    g274: BSplineCurve PolesCount=2 KnotsCount=2 Degree=1 IsPeriodic=0
    g275: BSplineCurve PolesCount=2 KnotsCount=2 Degree=1 IsPeriodic=0
    g276: BSplineCurve PolesCount=2 KnotsCount=2 Degree=1 IsPeriodic=0
    g277: BSplineCurve PolesCount=2 KnotsCount=2 Degree=1 IsPeriodic=0
    g278: BSplineCurve PolesCount=2 KnotsCount=2 Degree=1 IsPeriodic=0
    g279: BSplineCurve PolesCount=2 KnotsCount=2 Degree=1 IsPeriodic=0
    g280: BSplineCurve PolesCount=2 KnotsCount=2 Degree=1 IsPeriodic=0
    g281: BSplineCurve PolesCount=2 KnotsCount=2 Degree=1 IsPeriodic=0
    g282: BSplineCurve PolesCount=2 KnotsCount=2 Degree=1 IsPeriodic=0
    g283: BSplineCurve PolesCount=2 KnotsCount=2 Degree=1 IsPeriodic=0
    g284: BSplineCurve PolesCount=2 KnotsCount=2 Degree=1 IsPeriodic=0
    g285: BSplineCurve PolesCount=2 KnotsCount=2 Degree=1 IsPeriodic=0
    g286: BSplineCurve PolesCount=2 KnotsCount=2 Degree=1 IsPeriodic=0
    g287: BSplineCurve PolesCount=2 KnotsCount=2 Degree=1 IsPeriodic=0
    g288: BSplineCurve PolesCount=2 KnotsCount=2 Degree=1 IsPeriodic=0
    g289: BSplineCurve PolesCount=2 KnotsCount=2 Degree=1 IsPeriodic=0
    g290: BSplineCurve PolesCount=2 KnotsCount=2 Degree=1 IsPeriodic=0
    g291: BSplineCurve PolesCount=2 KnotsCount=2 Degree=1 IsPeriodic=0
    g292: BSplineCurve PolesCount=2 KnotsCount=2 Degree=1 IsPeriodic=0
    g293: BSplineCurve PolesCount=2 KnotsCount=2 Degree=1 IsPeriodic=0
    g294: BSplineCurve PolesCount=2 KnotsCount=2 Degree=1 IsPeriodic=0
    g295: BSplineCurve PolesCount=2 KnotsCount=2 Degree=1 IsPeriodic=0
    g296: BSplineCurve PolesCount=2 KnotsCount=2 Degree=1 IsPeriodic=0
    g297: BSplineCurve PolesCount=2 KnotsCount=2 Degree=1 IsPeriodic=0
    g298: BSplineCurve PolesCount=2 KnotsCount=2 Degree=1 IsPeriodic=0
    g299: BSplineCurve PolesCount=2 KnotsCount=2 Degree=1 IsPeriodic=0
    g300: BSplineCurve PolesCount=2 KnotsCount=2 Degree=1 IsPeriodic=0
    g301: BSplineCurve PolesCount=2 KnotsCount=2 Degree=1 IsPeriodic=0
    g302: BSplineCurve PolesCount=2 KnotsCount=2 Degree=1 IsPeriodic=0
    g303: BSplineCurve PolesCount=2 KnotsCount=2 Degree=1 IsPeriodic=0
    g304: BSplineCurve PolesCount=2 KnotsCount=2 Degree=1 IsPeriodic=0
    g305: BSplineCurve PolesCount=2 KnotsCount=2 Degree=1 IsPeriodic=0
    g306: BSplineCurve PolesCount=2 KnotsCount=2 Degree=1 IsPeriodic=0
    g307: BSplineCurve PolesCount=2 KnotsCount=2 Degree=1 IsPeriodic=0
    g308: BSplineCurve PolesCount=2 KnotsCount=2 Degree=1 IsPeriodic=0
    g309: BSplineCurve PolesCount=2 KnotsCount=2 Degree=1 IsPeriodic=0
    g310: BSplineCurve PolesCount=2 KnotsCount=2 Degree=1 IsPeriodic=0
    g311: BSplineCurve PolesCount=2 KnotsCount=2 Degree=1 IsPeriodic=0
    g312: BSplineCurve PolesCount=2 KnotsCount=2 Degree=1 IsPeriodic=0
    g313: BSplineCurve PolesCount=2 KnotsCount=2 Degree=1 IsPeriodic=0
    g314: BSplineCurve PolesCount=2 KnotsCount=2 Degree=1 IsPeriodic=0
    g315: BSplineCurve PolesCount=2 KnotsCount=2 Degree=1 IsPeriodic=0
    g316: BSplineCurve PolesCount=2 KnotsCount=2 Degree=1 IsPeriodic=0
    g317: BSplineCurve PolesCount=2 KnotsCount=2 Degree=1 IsPeriodic=0
    g318: BSplineCurve PolesCount=2 KnotsCount=2 Degree=1 IsPeriodic=0
    g319: BSplineCurve PolesCount=2 KnotsCount=2 Degree=1 IsPeriodic=0
    g320: BSplineCurve PolesCount=2 KnotsCount=2 Degree=1 IsPeriodic=0
    g321: BSplineCurve PolesCount=2 KnotsCount=2 Degree=1 IsPeriodic=0
    g322: BSplineCurve PolesCount=2 KnotsCount=2 Degree=1 IsPeriodic=0
    g323: BSplineCurve PolesCount=2 KnotsCount=2 Degree=1 IsPeriodic=0
    g324: BSplineCurve PolesCount=2 KnotsCount=2 Degree=1 IsPeriodic=0
    g325: BSplineCurve PolesCount=2 KnotsCount=2 Degree=1 IsPeriodic=0
    g326: BSplineCurve PolesCount=2 KnotsCount=2 Degree=1 IsPeriodic=0
    g327: BSplineCurve PolesCount=2 KnotsCount=2 Degree=1 IsPeriodic=0
    g328: BSplineCurve PolesCount=2 KnotsCount=2 Degree=1 IsPeriodic=0
    g329: BSplineCurve PolesCount=2 KnotsCount=2 Degree=1 IsPeriodic=0
    g330: BSplineCurve PolesCount=2 KnotsCount=2 Degree=1 IsPeriodic=0
    g331: BSplineCurve PolesCount=2 KnotsCount=2 Degree=1 IsPeriodic=0
    g332: BSplineCurve PolesCount=2 KnotsCount=2 Degree=1 IsPeriodic=0
    g333: BSplineCurve PolesCount=2 KnotsCount=2 Degree=1 IsPeriodic=0
    g334: BSplineCurve PolesCount=2 KnotsCount=2 Degree=1 IsPeriodic=0
    g335: BSplineCurve PolesCount=2 KnotsCount=2 Degree=1 IsPeriodic=0
    g336: BSplineCurve PolesCount=2 KnotsCount=2 Degree=1 IsPeriodic=0
    g337: BSplineCurve PolesCount=2 KnotsCount=2 Degree=1 IsPeriodic=0
    g338: BSplineCurve PolesCount=2 KnotsCount=2 Degree=1 IsPeriodic=0
    g339: BSplineCurve PolesCount=2 KnotsCount=2 Degree=1 IsPeriodic=0
    g340: BSplineCurve PolesCount=2 KnotsCount=2 Degree=1 IsPeriodic=0
    g341: BSplineCurve PolesCount=2 KnotsCount=2 Degree=1 IsPeriodic=0
    g342: BSplineCurve PolesCount=2 KnotsCount=2 Degree=1 IsPeriodic=0
    g343: BSplineCurve PolesCount=2 KnotsCount=2 Degree=1 IsPeriodic=0
    g344: BSplineCurve PolesCount=2 KnotsCount=2 Degree=1 IsPeriodic=0
    g345: BSplineCurve PolesCount=2 KnotsCount=2 Degree=1 IsPeriodic=0
    g346: BSplineCurve PolesCount=2 KnotsCount=2 Degree=1 IsPeriodic=0
    g347: BSplineCurve PolesCount=2 KnotsCount=2 Degree=1 IsPeriodic=0
    g348: BSplineCurve PolesCount=2 KnotsCount=2 Degree=1 IsPeriodic=0
    g349: BSplineCurve PolesCount=2 KnotsCount=2 Degree=1 IsPeriodic=0
    g350: BSplineCurve PolesCount=2 KnotsCount=2 Degree=1 IsPeriodic=0
    g351: BSplineCurve PolesCount=2 KnotsCount=2 Degree=1 IsPeriodic=0
    g352: BSplineCurve PolesCount=2 KnotsCount=2 Degree=1 IsPeriodic=0
    g353: BSplineCurve PolesCount=2 KnotsCount=2 Degree=1 IsPeriodic=0
    g354: BSplineCurve PolesCount=2 KnotsCount=2 Degree=1 IsPeriodic=0
    g355: BSplineCurve PolesCount=2 KnotsCount=2 Degree=1 IsPeriodic=0
    g356: BSplineCurve PolesCount=2 KnotsCount=2 Degree=1 IsPeriodic=0
    g357: BSplineCurve PolesCount=2 KnotsCount=2 Degree=1 IsPeriodic=0
    g358: BSplineCurve PolesCount=2 KnotsCount=2 Degree=1 IsPeriodic=0
    g359: BSplineCurve PolesCount=2 KnotsCount=2 Degree=1 IsPeriodic=0
    g360: BSplineCurve PolesCount=2 KnotsCount=2 Degree=1 IsPeriodic=0
    g361: BSplineCurve PolesCount=2 KnotsCount=2 Degree=1 IsPeriodic=0
    g362: BSplineCurve PolesCount=2 KnotsCount=2 Degree=1 IsPeriodic=0
    g363: BSplineCurve PolesCount=2 KnotsCount=2 Degree=1 IsPeriodic=0
    g364: BSplineCurve PolesCount=2 KnotsCount=2 Degree=1 IsPeriodic=0
    g365: BSplineCurve PolesCount=2 KnotsCount=2 Degree=1 IsPeriodic=0
    g366: BSplineCurve PolesCount=2 KnotsCount=2 Degree=1 IsPeriodic=0
    g367: BSplineCurve PolesCount=2 KnotsCount=2 Degree=1 IsPeriodic=0
    g368: BSplineCurve PolesCount=2 KnotsCount=2 Degree=1 IsPeriodic=0
    g369: BSplineCurve PolesCount=2 KnotsCount=2 Degree=1 IsPeriodic=0
    g370: BSplineCurve PolesCount=2 KnotsCount=2 Degree=1 IsPeriodic=0
    g371: BSplineCurve PolesCount=2 KnotsCount=2 Degree=1 IsPeriodic=0
    g372: BSplineCurve PolesCount=2 KnotsCount=2 Degree=1 IsPeriodic=0
    g373: BSplineCurve PolesCount=2 KnotsCount=2 Degree=1 IsPeriodic=0
    g374: BSplineCurve PolesCount=2 KnotsCount=2 Degree=1 IsPeriodic=0
    g375: BSplineCurve PolesCount=2 KnotsCount=2 Degree=1 IsPeriodic=0
    g376: BSplineCurve PolesCount=2 KnotsCount=2 Degree=1 IsPeriodic=0
    g377: BSplineCurve PolesCount=2 KnotsCount=2 Degree=1 IsPeriodic=0
    g378: BSplineCurve PolesCount=2 KnotsCount=2 Degree=1 IsPeriodic=0
    g379: BSplineCurve PolesCount=2 KnotsCount=2 Degree=1 IsPeriodic=0
    g380: BSplineCurve PolesCount=2 KnotsCount=2 Degree=1 IsPeriodic=0
    g381: BSplineCurve PolesCount=2 KnotsCount=2 Degree=1 IsPeriodic=0
    g382: BSplineCurve PolesCount=2 KnotsCount=2 Degree=1 IsPeriodic=0
    g383: BSplineCurve PolesCount=2 KnotsCount=2 Degree=1 IsPeriodic=0
    g384: BSplineCurve PolesCount=2 KnotsCount=2 Degree=1 IsPeriodic=0
    g385: BSplineCurve PolesCount=2 KnotsCount=2 Degree=1 IsPeriodic=0
    g386: BSplineCurve PolesCount=2 KnotsCount=2 Degree=1 IsPeriodic=0
    g387: BSplineCurve PolesCount=2 KnotsCount=2 Degree=1 IsPeriodic=0
    g388: BSplineCurve PolesCount=2 KnotsCount=2 Degree=1 IsPeriodic=0
    g389: BSplineCurve PolesCount=2 KnotsCount=2 Degree=1 IsPeriodic=0
    g390: BSplineCurve PolesCount=2 KnotsCount=2 Degree=1 IsPeriodic=0
    g391: BSplineCurve PolesCount=2 KnotsCount=2 Degree=1 IsPeriodic=0
    g392: BSplineCurve PolesCount=2 KnotsCount=2 Degree=1 IsPeriodic=0
    g393: BSplineCurve PolesCount=2 KnotsCount=2 Degree=1 IsPeriodic=0
    g394: BSplineCurve PolesCount=2 KnotsCount=2 Degree=1 IsPeriodic=0
    g395: BSplineCurve PolesCount=2 KnotsCount=2 Degree=1 IsPeriodic=0
    g396: BSplineCurve PolesCount=2 KnotsCount=2 Degree=1 IsPeriodic=0
    g397: BSplineCurve PolesCount=2 KnotsCount=2 Degree=1 IsPeriodic=0
    g398: BSplineCurve PolesCount=2 KnotsCount=2 Degree=1 IsPeriodic=0
    g399: BSplineCurve PolesCount=2 KnotsCount=2 Degree=1 IsPeriodic=0
    ... +460 more geometry lines
  constraints (860):
    c: Coincident(g0,g1)
    c: Coincident(g1,g2)
    c: Coincident(g2,g3)
    c: Coincident(g3,g4)
    c: Coincident(g4,g5)
    c: Coincident(g5,g6)
    c: Coincident(g6,g7)
    c: Coincident(g7,g8)
    c: Coincident(g8,g9)
    c: Coincident(g9,g10)
    c: Coincident(g10,g11)
    c: Coincident(g11,g12)
    c: Coincident(g12,g13)
    c: Coincident(g13,g14)
    c: Coincident(g14,g15)
    c: Coincident(g15,g16)
    c: Coincident(g16,g17)
    c: Coincident(g17,g18)
    c: Coincident(g18,g19)
    c: Coincident(g19,g20)
    c: Coincident(g20,g21)
    c: Coincident(g21,g22)
    c: Coincident(g22,g23)
    c: Coincident(g23,g24)
    c: Coincident(g24,g25)
    c: Coincident(g25,g26)
    c: Coincident(g26,g27)
    c: Coincident(g27,g28)
    c: Coincident(g28,g29)
    c: Coincident(g29,g30)
    c: Coincident(g30,g31)
    c: Coincident(g31,g32)
    c: Coincident(g32,g33)
    c: Coincident(g33,g34)
    c: Coincident(g34,g35)
    c: Coincident(g35,g36)
    c: Coincident(g36,g37)
    c: Coincident(g37,g38)
    c: Coincident(g38,g39)
    c: Coincident(g39,g40)
    c: Coincident(g40,g41)
    c: Coincident(g41,g42)
    c: Coincident(g42,g43)
    c: Coincident(g43,g44)
    c: Coincident(g44,g45)
    c: Coincident(g45,g46)
    c: Coincident(g46,g47)
    c: Coincident(g47,g48)
    c: Coincident(g48,g49)
    c: Coincident(g49,g50)
    c: Coincident(g50,g51)
    c: Coincident(g51,g52)
    c: Coincident(g52,g53)
    c: Coincident(g53,g54)
    c: Coincident(g54,g55)
    c: Coincident(g55,g56)
    c: Coincident(g56,g57)
    c: Coincident(g57,g58)
    c: Coincident(g58,g59)
    c: Coincident(g59,g60)
    c: Coincident(g60,g61)
    c: Coincident(g61,g62)
    c: Coincident(g62,g63)
    c: Coincident(g63,g64)
    c: Coincident(g64,g65)
    c: Coincident(g65,g66)
    c: Coincident(g66,g67)
    c: Coincident(g67,g68)
    c: Coincident(g68,g69)
    c: Coincident(g69,g70)
    c: Coincident(g70,g71)
    c: Coincident(g71,g72)
    c: Coincident(g72,g73)
    c: Coincident(g73,g74)
    c: Coincident(g74,g75)
    c: Coincident(g75,g76)
    c: Coincident(g76,g77)
    c: Coincident(g77,g78)
    c: Coincident(g78,g79)
    c: Coincident(g79,g80)
    c: Coincident(g80,g81)
    c: Coincident(g81,g82)
    c: Coincident(g82,g83)
    c: Coincident(g83,g84)
    c: Coincident(g84,g85)
    c: Coincident(g85,g86)
    c: Coincident(g86,g87)
    c: Coincident(g87,g0)
    c: Coincident(g88,g89)
    c: Coincident(g89,g90)
    c: Coincident(g90,g91)
    c: Coincident(g91,g92)
    c: Coincident(g92,g93)
    c: Coincident(g93,g94)
    c: Coincident(g94,g95)
    c: Coincident(g95,g96)
    c: Coincident(g96,g97)
    c: Coincident(g97,g98)
    c: Coincident(g98,g99)
    c: Coincident(g99,g100)
    c: Coincident(g100,g101)
    c: Coincident(g101,g102)
    c: Coincident(g102,g103)
    c: Coincident(g103,g104)
    c: Coincident(g104,g105)
    c: Coincident(g105,g106)
    c: Coincident(g106,g107)
    c: Coincident(g107,g108)
    c: Coincident(g108,g109)
    c: Coincident(g109,g110)
    c: Coincident(g110,g111)
    c: Coincident(g111,g112)
    c: Coincident(g112,g113)
    c: Coincident(g113,g114)
    c: Coincident(g114,g115)
    c: Coincident(g115,g116)
    c: Coincident(g116,g117)
    c: Coincident(g117,g118)
    c: Coincident(g118,g119)
    c: Coincident(g119,g120)
    c: Coincident(g120,g121)
    c: Coincident(g121,g122)
    c: Coincident(g122,g123)
    c: Coincident(g123,g124)
    c: Coincident(g124,g125)
    c: Coincident(g125,g126)
    c: Coincident(g126,g127)
    c: Coincident(g127,g88)
    c: Coincident(g128,g129)
    c: Coincident(g129,g130)
    c: Coincident(g130,g131)
    c: Coincident(g131,g132)
    c: Coincident(g132,g133)
    c: Coincident(g133,g134)
    c: Coincident(g134,g135)
    c: Coincident(g135,g136)
    c: Coincident(g136,g137)
    c: Coincident(g137,g138)
    c: Coincident(g138,g139)
    c: Coincident(g139,g140)
    c: Coincident(g140,g141)
    c: Coincident(g141,g142)
    c: Coincident(g142,g143)
    c: Coincident(g143,g144)
    c: Coincident(g144,g145)
    c: Coincident(g145,g146)
    c: Coincident(g146,g147)
    c: Coincident(g147,g148)
    c: Coincident(g148,g149)
    c: Coincident(g149,g150)
    c: Coincident(g150,g151)
    c: Coincident(g151,g152)
    c: Coincident(g152,g153)
    c: Coincident(g153,g154)
    c: Coincident(g154,g155)
    c: Coincident(g155,g156)
    c: Coincident(g156,g157)
    c: Coincident(g157,g158)
    c: Coincident(g158,g159)
    c: Coincident(g159,g160)
    c: Coincident(g160,g161)
    c: Coincident(g161,g162)
    c: Coincident(g162,g163)
    c: Coincident(g163,g164)
    c: Coincident(g164,g165)
    c: Coincident(g165,g166)
    c: Coincident(g166,g167)
    c: Coincident(g167,g168)
    c: Coincident(g168,g169)
    c: Coincident(g169,g170)
    c: Coincident(g170,g171)
    c: Coincident(g171,g172)
    c: Coincident(g172,g173)
    c: Coincident(g173,g174)
    c: Coincident(g174,g175)
    c: Coincident(g175,g176)
    c: Coincident(g176,g177)
    c: Coincident(g177,g178)
    c: Coincident(g178,g179)
    c: Coincident(g179,g180)
    c: Coincident(g180,g181)
    c: Coincident(g181,g182)
    c: Coincident(g182,g183)
    c: Coincident(g183,g184)
    c: Coincident(g184,g185)
    c: Coincident(g185,g186)
    c: Coincident(g186,g187)
    c: Coincident(g187,g188)
    c: Coincident(g188,g189)
    c: Coincident(g189,g190)
    c: Coincident(g190,g191)
    c: Coincident(g191,g192)
    c: Coincident(g192,g193)
    c: Coincident(g193,g194)
    c: Coincident(g194,g195)
    c: Coincident(g195,g196)
    c: Coincident(g196,g197)
    c: Coincident(g197,g198)
    c: Coincident(g198,g199)
    c: Coincident(g199,g200)
    c: Coincident(g200,g201)
    c: Coincident(g201,g202)
    c: Coincident(g202,g203)
    c: Coincident(g203,g204)
    c: Coincident(g204,g205)
    c: Coincident(g205,g206)
    c: Coincident(g206,g207)
    c: Coincident(g207,g208)
    c: Coincident(g208,g209)
    c: Coincident(g209,g210)
    c: Coincident(g210,g211)
    c: Coincident(g211,g212)
    c: Coincident(g212,g213)
    c: Coincident(g213,g214)
    c: Coincident(g214,g215)
    c: Coincident(g215,g216)
    c: Coincident(g216,g217)
    c: Coincident(g217,g218)
    c: Coincident(g218,g219)
    c: Coincident(g219,g220)
    c: Coincident(g220,g221)
    c: Coincident(g221,g222)
    c: Coincident(g222,g223)
    c: Coincident(g223,g224)
    c: Coincident(g224,g225)
    c: Coincident(g225,g226)
    c: Coincident(g226,g227)
    c: Coincident(g227,g228)
    c: Coincident(g228,g229)
    c: Coincident(g229,g230)
    c: Coincident(g230,g231)
    c: Coincident(g231,g232)
    c: Coincident(g232,g233)
    c: Coincident(g233,g234)
    c: Coincident(g234,g235)
    c: Coincident(g235,g236)
    c: Coincident(g236,g237)
    c: Coincident(g237,g238)
    c: Coincident(g238,g239)
    c: Coincident(g239,g128)
    c: Coincident(g240,g241)
    c: Coincident(g241,g242)
    c: Coincident(g242,g243)
    c: Coincident(g243,g244)
    c: Coincident(g244,g245)
    c: Coincident(g245,g246)
    c: Coincident(g246,g247)
    c: Coincident(g247,g248)
    c: Coincident(g248,g249)
    c: Coincident(g249,g250)
    c: Coincident(g250,g251)
    c: Coincident(g251,g252)
    c: Coincident(g252,g253)
    c: Coincident(g253,g254)
    c: Coincident(g254,g255)
    c: Coincident(g255,g256)
    c: Coincident(g256,g257)
    c: Coincident(g257,g258)
    c: Coincident(g258,g259)
    c: Coincident(g259,g260)
    c: Coincident(g260,g261)
    c: Coincident(g261,g262)
    c: Coincident(g262,g263)
    c: Coincident(g263,g264)
    c: Coincident(g264,g265)
    c: Coincident(g265,g266)
    c: Coincident(g266,g267)
    c: Coincident(g267,g268)
    c: Coincident(g268,g269)
    c: Coincident(g269,g270)
    c: Coincident(g270,g271)
    c: Coincident(g271,g272)
    c: Coincident(g272,g273)
    c: Coincident(g273,g274)
    c: Coincident(g274,g275)
    c: Coincident(g275,g276)
    c: Coincident(g276,g277)
    c: Coincident(g277,g278)
    c: Coincident(g278,g279)
    c: Coincident(g279,g280)
    c: Coincident(g280,g281)
    c: Coincident(g281,g282)
    c: Coincident(g282,g283)
    c: Coincident(g283,g284)
    c: Coincident(g284,g285)
    c: Coincident(g285,g286)
    c: Coincident(g286,g287)
    c: Coincident(g287,g240)
    c: Coincident(g288,g289)
    c: Coincident(g289,g290)
    c: Coincident(g290,g291)
    c: Coincident(g291,g292)
    c: Coincident(g292,g293)
    c: Coincident(g293,g294)
    c: Coincident(g294,g295)
    c: Coincident(g295,g296)
    c: Coincident(g296,g297)
    c: Coincident(g297,g298)
    c: Coincident(g298,g299)
    c: Coincident(g299,g300)
    c: Coincident(g300,g301)
    c: Coincident(g301,g302)
    c: Coincident(g302,g303)
    c: Coincident(g303,g304)
    c: Coincident(g304,g305)
    c: Coincident(g305,g306)
    c: Coincident(g306,g307)
    c: Coincident(g307,g308)
    c: Coincident(g308,g309)
    c: Coincident(g309,g310)
    c: Coincident(g310,g311)
    c: Coincident(g311,g288)
    c: Coincident(g312,g313)
    c: Coincident(g313,g314)
    c: Coincident(g314,g315)
    c: Coincident(g315,g316)
    c: Coincident(g316,g317)
    c: Coincident(g317,g318)
    c: Coincident(g318,g319)
    c: Coincident(g319,g320)
    c: Coincident(g320,g321)
    c: Coincident(g321,g322)
    c: Coincident(g322,g323)
    c: Coincident(g323,g324)
    c: Coincident(g324,g325)
    c: Coincident(g325,g326)
    c: Coincident(g326,g327)
    c: Coincident(g327,g312)
    c: Coincident(g328,g329)
    c: Coincident(g329,g330)
    c: Coincident(g330,g331)
    c: Coincident(g331,g332)
    c: Coincident(g332,g333)
    c: Coincident(g333,g334)
    c: Coincident(g334,g335)
    c: Coincident(g335,g336)
    c: Coincident(g336,g337)
    c: Coincident(g337,g338)
    c: Coincident(g338,g339)
    c: Coincident(g339,g340)
    c: Coincident(g340,g341)
    c: Coincident(g341,g342)
    c: Coincident(g342,g343)
    c: Coincident(g343,g344)
    c: Coincident(g344,g345)
    c: Coincident(g345,g346)
    c: Coincident(g346,g347)
    c: Coincident(g347,g348)
    c: Coincident(g348,g349)
    c: Coincident(g349,g350)
    c: Coincident(g350,g351)
    c: Coincident(g351,g352)
    c: Coincident(g352,g353)
    c: Coincident(g353,g354)
    c: Coincident(g354,g355)
    c: Coincident(g355,g356)
    c: Coincident(g356,g357)
    c: Coincident(g357,g358)
    c: Coincident(g358,g359)
    c: Coincident(g359,g360)
    c: Coincident(g360,g361)
    c: Coincident(g361,g362)
    c: Coincident(g362,g363)
    c: Coincident(g363,g364)
    c: Coincident(g364,g365)
    c: Coincident(g365,g366)
    c: Coincident(g366,g367)
    c: Coincident(g367,g368)
    c: Coincident(g368,g369)
    c: Coincident(g369,g370)
    c: Coincident(g370,g371)
    c: Coincident(g371,g372)
    c: Coincident(g372,g373)
    c: Coincident(g373,g374)
    c: Coincident(g374,g375)
    c: Coincident(g375,g376)
    c: Coincident(g376,g377)
    c: Coincident(g377,g378)
    c: Coincident(g378,g379)
    c: Coincident(g379,g380)
    c: Coincident(g380,g381)
    c: Coincident(g381,g382)
    c: Coincident(g382,g383)
    c: Coincident(g383,g384)
    c: Coincident(g384,g385)
    c: Coincident(g385,g386)
    c: Coincident(g386,g387)
    c: Coincident(g387,g388)
    c: Coincident(g388,g389)
    c: Coincident(g389,g390)
    c: Coincident(g390,g391)
    c: Coincident(g391,g392)
    c: Coincident(g392,g393)
    c: Coincident(g393,g394)
    c: Coincident(g394,g395)
    c: Coincident(g395,g396)
    c: Coincident(g396,g397)
    c: Coincident(g397,g398)
    c: Coincident(g398,g399)
    c: Coincident(g399,g328)
    c: Coincident(g400,g401)
    c: Coincident(g401,g402)
    c: Coincident(g402,g403)
    c: Coincident(g403,g404)
    c: Coincident(g404,g405)
    c: Coincident(g405,g406)
    c: Coincident(g406,g407)
    c: Coincident(g407,g408)
    c: Coincident(g408,g409)
    c: Coincident(g409,g410)
    c: Coincident(g410,g411)
    c: Coincident(g411,g412)
    c: Coincident(g412,g413)
    c: Coincident(g413,g414)
    c: Coincident(g414,g415)
    c: Coincident(g415,g416)
    c: Coincident(g416,g417)
    c: Coincident(g417,g418)
    c: Coincident(g418,g419)
    c: Coincident(g419,g420)
    c: Coincident(g420,g421)
    c: Coincident(g421,g422)
    c: Coincident(g422,g423)
    c: Coincident(g423,g400)
    c: Coincident(g424,g425)
    c: Coincident(g425,g426)
    c: Coincident(g426,g427)
    c: Coincident(g427,g428)
    c: Coincident(g428,g429)
    c: Coincident(g429,g430)
    c: Coincident(g430,g431)
    c: Coincident(g431,g432)
    c: Coincident(g432,g433)
    c: Coincident(g433,g434)
    c: Coincident(g434,g435)
    c: Coincident(g435,g436)
    c: Coincident(g436,g437)
    c: Coincident(g437,g438)
    c: Coincident(g438,g439)
    c: Coincident(g439,g440)
    c: Coincident(g440,g441)
    c: Coincident(g441,g442)
    c: Coincident(g442,g443)
    c: Coincident(g443,g444)
    c: Coincident(g444,g445)
    c: Coincident(g445,g446)
    c: Coincident(g446,g447)
    c: Coincident(g447,g448)
    c: Coincident(g448,g449)
    c: Coincident(g449,g450)
    c: Coincident(g450,g451)
    c: Coincident(g451,g452)
    c: Coincident(g452,g453)
    c: Coincident(g453,g454)
    c: Coincident(g454,g455)
    c: Coincident(g455,g456)
    c: Coincident(g456,g457)
    c: Coincident(g457,g458)
    c: Coincident(g458,g459)
    c: Coincident(g459,g460)
    c: Coincident(g460,g461)
    c: Coincident(g461,g462)
    c: Coincident(g462,g463)
    c: Coincident(g463,g464)
    c: Coincident(g464,g465)
    c: Coincident(g465,g466)
    c: Coincident(g466,g467)
    c: Coincident(g467,g468)
    c: Coincident(g468,g469)
    c: Coincident(g469,g470)
    c: Coincident(g470,g471)
    c: Coincident(g471,g472)
    c: Coincident(g472,g473)
    c: Coincident(g473,g474)
    c: Coincident(g474,g475)
    c: Coincident(g475,g476)
    c: Coincident(g476,g477)
    c: Coincident(g477,g478)
    c: Coincident(g478,g479)
    c: Coincident(g479,g424)
    c: Coincident(g480,g481)
    c: Coincident(g481,g482)
    c: Coincident(g482,g483)
    c: Coincident(g483,g484)
    c: Coincident(g484,g485)
    c: Coincident(g485,g486)
    c: Coincident(g486,g487)
    c: Coincident(g487,g488)
    c: Coincident(g488,g489)
    c: Coincident(g489,g490)
    c: Coincident(g490,g491)
    c: Coincident(g491,g492)
    c: Coincident(g492,g493)
    c: Coincident(g493,g494)
    c: Coincident(g494,g495)
    c: Coincident(g495,g480)
    c: Coincident(g496,g497)
    c: Coincident(g497,g498)
    c: Coincident(g498,g499)
    c: Coincident(g499,g500)
    c: Coincident(g500,g501)
    c: Coincident(g501,g502)
    c: Coincident(g502,g503)
    c: Coincident(g503,g504)
    c: Coincident(g504,g505)
    c: Coincident(g505,g506)
    c: Coincident(g506,g507)
    c: Coincident(g507,g508)
    c: Coincident(g508,g509)
    c: Coincident(g509,g510)
    c: Coincident(g510,g511)
    c: Coincident(g511,g512)
    c: Coincident(g512,g513)
    c: Coincident(g513,g514)
    c: Coincident(g514,g515)
    c: Coincident(g515,g516)
    c: Coincident(g516,g517)
    c: Coincident(g517,g518)
    c: Coincident(g518,g519)
    c: Coincident(g519,g520)
    c: Coincident(g520,g521)
    c: Coincident(g521,g522)
    c: Coincident(g522,g523)
    c: Coincident(g523,g524)
    c: Coincident(g524,g525)
    c: Coincident(g525,g526)
    c: Coincident(g526,g527)
    c: Coincident(g527,g528)
    c: Coincident(g528,g529)
    c: Coincident(g529,g530)
    c: Coincident(g530,g531)
    c: Coincident(g531,g532)
    c: Coincident(g532,g533)
    c: Coincident(g533,g534)
    c: Coincident(g534,g535)
    c: Coincident(g535,g496)
    c: Coincident(g536,g537)
    c: Coincident(g537,g538)
    c: Coincident(g538,g539)
    c: Coincident(g539,g540)
    c: Coincident(g540,g541)
    c: Coincident(g541,g542)
    c: Coincident(g542,g543)
    c: Coincident(g543,g544)
    c: Coincident(g544,g545)
    c: Coincident(g545,g546)
    c: Coincident(g546,g547)
    c: Coincident(g547,g548)
    c: Coincident(g548,g549)
    c: Coincident(g549,g550)
    c: Coincident(g550,g551)
    c: Coincident(g551,g552)
    c: Coincident(g552,g553)
    c: Coincident(g553,g554)
    c: Coincident(g554,g555)
    c: Coincident(g555,g556)
    c: Coincident(g556,g557)
    c: Coincident(g557,g558)
    c: Coincident(g558,g559)
    c: Coincident(g559,g560)
    c: Coincident(g560,g561)
    c: Coincident(g561,g562)
    c: Coincident(g562,g563)
    c: Coincident(g563,g564)
    c: Coincident(g564,g565)
    c: Coincident(g565,g566)
    c: Coincident(g566,g567)
    c: Coincident(g567,g568)
    c: Coincident(g568,g569)
    c: Coincident(g569,g570)
    c: Coincident(g570,g571)
    c: Coincident(g571,g572)
    c: Coincident(g572,g573)
    c: Coincident(g573,g574)
    c: Coincident(g574,g575)
    c: Coincident(g575,g536)
    c: Coincident(g576,g577)
    c: Coincident(g577,g578)
    c: Coincident(g578,g579)
    c: Coincident(g579,g580)
    c: Coincident(g580,g581)
    c: Coincident(g581,g582)
    c: Coincident(g582,g583)
    c: Coincident(g583,g584)
    c: Coincident(g584,g585)
    c: Coincident(g585,g586)
    c: Coincident(g586,g587)
    c: Coincident(g587,g576)
    c: Coincident(g588,g589)
    c: Coincident(g589,g590)
    c: Coincident(g590,g591)
    c: Coincident(g591,g592)
    c: Coincident(g592,g593)
    c: Coincident(g593,g594)
    c: Coincident(g594,g595)
    c: Coincident(g595,g596)
    c: Coincident(g596,g597)
    c: Coincident(g597,g598)
    c: Coincident(g598,g599)
    c: Coincident(g599,g600)
    c: Coincident(g600,g601)
    c: Coincident(g601,g602)
    c: Coincident(g602,g603)
    c: Coincident(g603,g604)
    c: Coincident(g604,g605)
    c: Coincident(g605,g606)
    c: Coincident(g606,g607)
    c: Coincident(g607,g608)
    c: Coincident(g608,g609)
    c: Coincident(g609,g610)
    c: Coincident(g610,g611)
    c: Coincident(g611,g612)
    c: Coincident(g612,g613)
    c: Coincident(g613,g614)
    c: Coincident(g614,g615)
    c: Coincident(g615,g616)
    c: Coincident(g616,g617)
    c: Coincident(g617,g618)
    c: Coincident(g618,g619)
    c: Coincident(g619,g620)
    c: Coincident(g620,g621)
    c: Coincident(g621,g622)
    c: Coincident(g622,g623)
    c: Coincident(g623,g624)
    c: Coincident(g624,g625)
    c: Coincident(g625,g626)
    c: Coincident(g626,g627)
    c: Coincident(g627,g628)
    c: Coincident(g628,g629)
    c: Coincident(g629,g630)
    c: Coincident(g630,g631)
    c: Coincident(g631,g632)
    c: Coincident(g632,g633)
    c: Coincident(g633,g634)
    c: Coincident(g634,g635)
    c: Coincident(g635,g636)
    c: Coincident(g636,g637)
    c: Coincident(g637,g638)
    c: Coincident(g638,g639)
    c: Coincident(g639,g640)
    c: Coincident(g640,g641)
    c: Coincident(g641,g642)
    c: Coincident(g642,g643)
    c: Coincident(g643,g644)
    c: Coincident(g644,g645)
    c: Coincident(g645,g646)
    c: Coincident(g646,g647)
    c: Coincident(g647,g648)
    c: Coincident(g648,g649)
    c: Coincident(g649,g650)
    c: Coincident(g650,g651)
    c: Coincident(g651,g652)
    c: Coincident(g652,g653)
    c: Coincident(g653,g654)
    c: Coincident(g654,g655)
    c: Coincident(g655,g656)
    c: Coincident(g656,g657)
    c: Coincident(g657,g658)
    c: Coincident(g658,g659)
    c: Coincident(g659,g660)
    c: Coincident(g660,g661)
    c: Coincident(g661,g662)
    c: Coincident(g662,g663)
    c: Coincident(g663,g664)
    c: Coincident(g664,g665)
    c: Coincident(g665,g666)
    c: Coincident(g666,g667)
    c: Coincident(g667,g668)
    c: Coincident(g668,g669)
    c: Coincident(g669,g670)
    c: Coincident(g670,g671)
    c: Coincident(g671,g672)
    c: Coincident(g672,g673)
    c: Coincident(g673,g674)
    c: Coincident(g674,g675)
    c: Coincident(g675,g588)
    c: Coincident(g676,g677)
    c: Coincident(g677,g678)
    c: Coincident(g678,g679)
    c: Coincident(g679,g680)
    c: Coincident(g680,g681)
    c: Coincident(g681,g682)
    c: Coincident(g682,g683)
    c: Coincident(g683,g684)
    c: Coincident(g684,g685)
    c: Coincident(g685,g686)
    c: Coincident(g686,g687)
    c: Coincident(g687,g688)
    c: Coincident(g688,g689)
    c: Coincident(g689,g690)
    c: Coincident(g690,g691)
    c: Coincident(g691,g676)
    c: Coincident(g692,g693)
    c: Coincident(g693,g694)
    c: Coincident(g694,g695)
    c: Coincident(g695,g696)
    c: Coincident(g696,g697)
    c: Coincident(g697,g698)
    c: Coincident(g698,g699)
    c: Coincident(g699,g700)
    c: Coincident(g700,g701)
    c: Coincident(g701,g702)
    c: Coincident(g702,g703)
    c: Coincident(g703,g704)
    c: Coincident(g704,g705)
    c: Coincident(g705,g706)
    c: Coincident(g706,g707)
    c: Coincident(g707,g708)
    c: Coincident(g708,g709)
    c: Coincident(g709,g710)
    c: Coincident(g710,g711)
    c: Coincident(g711,g712)
    c: Coincident(g712,g713)
    c: Coincident(g713,g714)
    c: Coincident(g714,g715)
    c: Coincident(g715,g716)
    c: Coincident(g716,g717)
    c: Coincident(g717,g718)
    c: Coincident(g718,g719)
    c: Coincident(g719,g720)
    c: Coincident(g720,g721)
    c: Coincident(g721,g722)
    c: Coincident(g722,g723)
    c: Coincident(g723,g724)
    c: Coincident(g724,g725)
    c: Coincident(g725,g726)
    c: Coincident(g726,g727)
    c: Coincident(g727,g728)
    c: Coincident(g728,g729)
    c: Coincident(g729,g730)
    c: Coincident(g730,g731)
    c: Coincident(g731,g692)
    c: Coincident(g732,g733)
    c: Coincident(g733,g734)
    c: Coincident(g734,g735)
    c: Coincident(g735,g736)
    c: Coincident(g736,g737)
    c: Coincident(g737,g738)
    c: Coincident(g738,g739)
    c: Coincident(g739,g740)
    c: Coincident(g740,g741)
    c: Coincident(g741,g742)
    c: Coincident(g742,g743)
    c: Coincident(g743,g744)
    c: Coincident(g744,g745)
    c: Coincident(g745,g746)
    c: Coincident(g746,g747)
    c: Coincident(g747,g748)
    c: Coincident(g748,g749)
    c: Coincident(g749,g750)
    c: Coincident(g750,g751)
    c: Coincident(g751,g752)
    c: Coincident(g752,g753)
    c: Coincident(g753,g754)
    c: Coincident(g754,g755)
    c: Coincident(g755,g756)
    c: Coincident(g756,g757)
    c: Coincident(g757,g758)
    c: Coincident(g758,g759)
    c: Coincident(g759,g760)
    c: Coincident(g760,g761)
    c: Coincident(g761,g762)
    c: Coincident(g762,g763)
    c: Coincident(g763,g732)
    c: Coincident(g764,g765)
    c: Coincident(g765,g766)
    c: Coincident(g766,g767)
    c: Coincident(g767,g768)
    c: Coincident(g768,g769)
    c: Coincident(g769,g770)
    c: Coincident(g770,g771)
    c: Coincident(g771,g772)
    c: Coincident(g772,g773)
    c: Coincident(g773,g774)
    c: Coincident(g774,g775)
    c: Coincident(g775,g776)
    c: Coincident(g776,g777)
    c: Coincident(g777,g778)
    c: Coincident(g778,g779)
    c: Coincident(g779,g780)
    c: Coincident(g780,g781)
    c: Coincident(g781,g782)
    c: Coincident(g782,g783)
    c: Coincident(g783,g784)
    c: Coincident(g784,g785)
    c: Coincident(g785,g786)
    c: Coincident(g786,g787)
    c: Coincident(g787,g764)
    c: Coincident(g788,g789)
    c: Coincident(g789,g790)
    c: Coincident(g790,g791)
    c: Coincident(g791,g792)
    c: Coincident(g792,g793)
    c: Coincident(g793,g794)
    c: Coincident(g794,g795)
    c: Coincident(g795,g796)
    c: Coincident(g796,g797)
    c: Coincident(g797,g798)
    c: Coincident(g798,g799)
    c: Coincident(g799,g800)
    c: Coincident(g800,g801)
    c: Coincident(g801,g802)
    c: Coincident(g802,g803)
    c: Coincident(g803,g804)
    c: Coincident(g804,g805)
    c: Coincident(g805,g806)
    c: Coincident(g806,g807)
    c: Coincident(g807,g808)
    c: Coincident(g808,g809)
    c: Coincident(g809,g810)
    c: Coincident(g810,g811)
    c: Coincident(g811,g812)
    c: Coincident(g812,g813)
    c: Coincident(g813,g814)
    c: Coincident(g814,g815)
    c: Coincident(g815,g816)
    c: Coincident(g816,g817)
    c: Coincident(g817,g818)
    c: Coincident(g818,g819)
    c: Coincident(g819,g820)
    c: Coincident(g820,g821)
    c: Coincident(g821,g822)
    c: Coincident(g822,g823)
    c: Coincident(g823,g824)
    c: Coincident(g824,g825)
    c: Coincident(g825,g826)
    c: Coincident(g826,g827)
    c: Coincident(g827,g828)
    c: Coincident(g828,g829)
    c: Coincident(g829,g830)
    c: Coincident(g830,g831)
    c: Coincident(g831,g832)
    c: Coincident(g832,g833)
    c: Coincident(g833,g834)
    c: Coincident(g834,g835)
    c: Coincident(g835,g836)
    c: Coincident(g836,g837)
    c: Coincident(g837,g838)
    c: Coincident(g838,g839)
    c: Coincident(g839,g840)
    c: Coincident(g840,g841)
    c: Coincident(g841,g842)
    c: Coincident(g842,g843)
    c: Coincident(g843,g844)
    c: Coincident(g844,g845)
    c: Coincident(g845,g846)
    c: Coincident(g846,g847)
    c: Coincident(g847,g848)
    c: Coincident(g848,g849)
    c: Coincident(g849,g850)
    c: Coincident(g850,g851)
    c: Coincident(g851,g852)
    c: Coincident(g852,g853)
    c: Coincident(g853,g854)
    c: Coincident(g854,g855)
    c: Coincident(g855,g856)
    c: Coincident(g856,g857)
    c: Coincident(g857,g858)
    c: Coincident(g858,g859)
    c: Coincident(g859,g788)
FEATURE [Sketcher::SketchObject] Sketch024  label="16 Bit VS005"
  FullyConstrained = false
  Placement = pos=(8.14,198.5,-10) rot=(1,0,0;3.14159rad)
  sketch-geometry (860):
    g0: BSplineCurve PolesCount=2 KnotsCount=2 Degree=1 IsPeriodic=0
    g1: BSplineCurve PolesCount=2 KnotsCount=2 Degree=1 IsPeriodic=0
    g2: BSplineCurve PolesCount=2 KnotsCount=2 Degree=1 IsPeriodic=0
    g3: BSplineCurve PolesCount=2 KnotsCount=2 Degree=1 IsPeriodic=0
    g4: BSplineCurve PolesCount=2 KnotsCount=2 Degree=1 IsPeriodic=0
    g5: BSplineCurve PolesCount=2 KnotsCount=2 Degree=1 IsPeriodic=0
    g6: BSplineCurve PolesCount=2 KnotsCount=2 Degree=1 IsPeriodic=0
    g7: BSplineCurve PolesCount=2 KnotsCount=2 Degree=1 IsPeriodic=0
    g8: BSplineCurve PolesCount=2 KnotsCount=2 Degree=1 IsPeriodic=0
    g9: BSplineCurve PolesCount=2 KnotsCount=2 Degree=1 IsPeriodic=0
    g10: BSplineCurve PolesCount=2 KnotsCount=2 Degree=1 IsPeriodic=0
    g11: BSplineCurve PolesCount=2 KnotsCount=2 Degree=1 IsPeriodic=0
    g12: BSplineCurve PolesCount=2 KnotsCount=2 Degree=1 IsPeriodic=0
    g13: BSplineCurve PolesCount=2 KnotsCount=2 Degree=1 IsPeriodic=0
    g14: BSplineCurve PolesCount=2 KnotsCount=2 Degree=1 IsPeriodic=0
    g15: BSplineCurve PolesCount=2 KnotsCount=2 Degree=1 IsPeriodic=0
    g16: BSplineCurve PolesCount=2 KnotsCount=2 Degree=1 IsPeriodic=0
    g17: BSplineCurve PolesCount=2 KnotsCount=2 Degree=1 IsPeriodic=0
    g18: BSplineCurve PolesCount=2 KnotsCount=2 Degree=1 IsPeriodic=0
    g19: BSplineCurve PolesCount=2 KnotsCount=2 Degree=1 IsPeriodic=0
    g20: BSplineCurve PolesCount=2 KnotsCount=2 Degree=1 IsPeriodic=0
    g21: BSplineCurve PolesCount=2 KnotsCount=2 Degree=1 IsPeriodic=0
    g22: BSplineCurve PolesCount=2 KnotsCount=2 Degree=1 IsPeriodic=0
    g23: BSplineCurve PolesCount=2 KnotsCount=2 Degree=1 IsPeriodic=0
    g24: BSplineCurve PolesCount=2 KnotsCount=2 Degree=1 IsPeriodic=0
    g25: BSplineCurve PolesCount=2 KnotsCount=2 Degree=1 IsPeriodic=0
    g26: BSplineCurve PolesCount=2 KnotsCount=2 Degree=1 IsPeriodic=0
    g27: BSplineCurve PolesCount=2 KnotsCount=2 Degree=1 IsPeriodic=0
    g28: BSplineCurve PolesCount=2 KnotsCount=2 Degree=1 IsPeriodic=0
    g29: BSplineCurve PolesCount=2 KnotsCount=2 Degree=1 IsPeriodic=0
    g30: BSplineCurve PolesCount=2 KnotsCount=2 Degree=1 IsPeriodic=0
    g31: BSplineCurve PolesCount=2 KnotsCount=2 Degree=1 IsPeriodic=0
    g32: BSplineCurve PolesCount=2 KnotsCount=2 Degree=1 IsPeriodic=0
    g33: BSplineCurve PolesCount=2 KnotsCount=2 Degree=1 IsPeriodic=0
    g34: BSplineCurve PolesCount=2 KnotsCount=2 Degree=1 IsPeriodic=0
    g35: BSplineCurve PolesCount=2 KnotsCount=2 Degree=1 IsPeriodic=0
    g36: BSplineCurve PolesCount=2 KnotsCount=2 Degree=1 IsPeriodic=0
    g37: BSplineCurve PolesCount=2 KnotsCount=2 Degree=1 IsPeriodic=0
    g38: BSplineCurve PolesCount=2 KnotsCount=2 Degree=1 IsPeriodic=0
    g39: BSplineCurve PolesCount=2 KnotsCount=2 Degree=1 IsPeriodic=0
    g40: BSplineCurve PolesCount=2 KnotsCount=2 Degree=1 IsPeriodic=0
    g41: BSplineCurve PolesCount=2 KnotsCount=2 Degree=1 IsPeriodic=0
    g42: BSplineCurve PolesCount=2 KnotsCount=2 Degree=1 IsPeriodic=0
    g43: BSplineCurve PolesCount=2 KnotsCount=2 Degree=1 IsPeriodic=0
    g44: BSplineCurve PolesCount=2 KnotsCount=2 Degree=1 IsPeriodic=0
    g45: BSplineCurve PolesCount=2 KnotsCount=2 Degree=1 IsPeriodic=0
    g46: BSplineCurve PolesCount=2 KnotsCount=2 Degree=1 IsPeriodic=0
    g47: BSplineCurve PolesCount=2 KnotsCount=2 Degree=1 IsPeriodic=0
    g48: BSplineCurve PolesCount=2 KnotsCount=2 Degree=1 IsPeriodic=0
    g49: BSplineCurve PolesCount=2 KnotsCount=2 Degree=1 IsPeriodic=0
    g50: BSplineCurve PolesCount=2 KnotsCount=2 Degree=1 IsPeriodic=0
    g51: BSplineCurve PolesCount=2 KnotsCount=2 Degree=1 IsPeriodic=0
    g52: BSplineCurve PolesCount=2 KnotsCount=2 Degree=1 IsPeriodic=0
    g53: BSplineCurve PolesCount=2 KnotsCount=2 Degree=1 IsPeriodic=0
    g54: BSplineCurve PolesCount=2 KnotsCount=2 Degree=1 IsPeriodic=0
    g55: BSplineCurve PolesCount=2 KnotsCount=2 Degree=1 IsPeriodic=0
    g56: BSplineCurve PolesCount=2 KnotsCount=2 Degree=1 IsPeriodic=0
    g57: BSplineCurve PolesCount=2 KnotsCount=2 Degree=1 IsPeriodic=0
    g58: BSplineCurve PolesCount=2 KnotsCount=2 Degree=1 IsPeriodic=0
    g59: BSplineCurve PolesCount=2 KnotsCount=2 Degree=1 IsPeriodic=0
    g60: BSplineCurve PolesCount=2 KnotsCount=2 Degree=1 IsPeriodic=0
    g61: BSplineCurve PolesCount=2 KnotsCount=2 Degree=1 IsPeriodic=0
    g62: BSplineCurve PolesCount=2 KnotsCount=2 Degree=1 IsPeriodic=0
    g63: BSplineCurve PolesCount=2 KnotsCount=2 Degree=1 IsPeriodic=0
    g64: BSplineCurve PolesCount=2 KnotsCount=2 Degree=1 IsPeriodic=0
    g65: BSplineCurve PolesCount=2 KnotsCount=2 Degree=1 IsPeriodic=0
    g66: BSplineCurve PolesCount=2 KnotsCount=2 Degree=1 IsPeriodic=0
    g67: BSplineCurve PolesCount=2 KnotsCount=2 Degree=1 IsPeriodic=0
    g68: BSplineCurve PolesCount=2 KnotsCount=2 Degree=1 IsPeriodic=0
    g69: BSplineCurve PolesCount=2 KnotsCount=2 Degree=1 IsPeriodic=0
    g70: BSplineCurve PolesCount=2 KnotsCount=2 Degree=1 IsPeriodic=0
    g71: BSplineCurve PolesCount=2 KnotsCount=2 Degree=1 IsPeriodic=0
    g72: BSplineCurve PolesCount=2 KnotsCount=2 Degree=1 IsPeriodic=0
    g73: BSplineCurve PolesCount=2 KnotsCount=2 Degree=1 IsPeriodic=0
    g74: BSplineCurve PolesCount=2 KnotsCount=2 Degree=1 IsPeriodic=0
    g75: BSplineCurve PolesCount=2 KnotsCount=2 Degree=1 IsPeriodic=0
    g76: BSplineCurve PolesCount=2 KnotsCount=2 Degree=1 IsPeriodic=0
    g77: BSplineCurve PolesCount=2 KnotsCount=2 Degree=1 IsPeriodic=0
    g78: BSplineCurve PolesCount=2 KnotsCount=2 Degree=1 IsPeriodic=0
    g79: BSplineCurve PolesCount=2 KnotsCount=2 Degree=1 IsPeriodic=0
    g80: BSplineCurve PolesCount=2 KnotsCount=2 Degree=1 IsPeriodic=0
    g81: BSplineCurve PolesCount=2 KnotsCount=2 Degree=1 IsPeriodic=0
    g82: BSplineCurve PolesCount=2 KnotsCount=2 Degree=1 IsPeriodic=0
    g83: BSplineCurve PolesCount=2 KnotsCount=2 Degree=1 IsPeriodic=0
    g84: BSplineCurve PolesCount=2 KnotsCount=2 Degree=1 IsPeriodic=0
    g85: BSplineCurve PolesCount=2 KnotsCount=2 Degree=1 IsPeriodic=0
    g86: BSplineCurve PolesCount=2 KnotsCount=2 Degree=1 IsPeriodic=0
    g87: BSplineCurve PolesCount=2 KnotsCount=2 Degree=1 IsPeriodic=0
    g88: BSplineCurve PolesCount=2 KnotsCount=2 Degree=1 IsPeriodic=0
    g89: BSplineCurve PolesCount=2 KnotsCount=2 Degree=1 IsPeriodic=0
    g90: BSplineCurve PolesCount=2 KnotsCount=2 Degree=1 IsPeriodic=0
    g91: BSplineCurve PolesCount=2 KnotsCount=2 Degree=1 IsPeriodic=0
    g92: BSplineCurve PolesCount=2 KnotsCount=2 Degree=1 IsPeriodic=0
    g93: BSplineCurve PolesCount=2 KnotsCount=2 Degree=1 IsPeriodic=0
    g94: BSplineCurve PolesCount=2 KnotsCount=2 Degree=1 IsPeriodic=0
    g95: BSplineCurve PolesCount=2 KnotsCount=2 Degree=1 IsPeriodic=0
    g96: BSplineCurve PolesCount=2 KnotsCount=2 Degree=1 IsPeriodic=0
    g97: BSplineCurve PolesCount=2 KnotsCount=2 Degree=1 IsPeriodic=0
    g98: BSplineCurve PolesCount=2 KnotsCount=2 Degree=1 IsPeriodic=0
    g99: BSplineCurve PolesCount=2 KnotsCount=2 Degree=1 IsPeriodic=0
    g100: BSplineCurve PolesCount=2 KnotsCount=2 Degree=1 IsPeriodic=0
    g101: BSplineCurve PolesCount=2 KnotsCount=2 Degree=1 IsPeriodic=0
    g102: BSplineCurve PolesCount=2 KnotsCount=2 Degree=1 IsPeriodic=0
    g103: BSplineCurve PolesCount=2 KnotsCount=2 Degree=1 IsPeriodic=0
    g104: BSplineCurve PolesCount=2 KnotsCount=2 Degree=1 IsPeriodic=0
    g105: BSplineCurve PolesCount=2 KnotsCount=2 Degree=1 IsPeriodic=0
    g106: BSplineCurve PolesCount=2 KnotsCount=2 Degree=1 IsPeriodic=0
    g107: BSplineCurve PolesCount=2 KnotsCount=2 Degree=1 IsPeriodic=0
    g108: BSplineCurve PolesCount=2 KnotsCount=2 Degree=1 IsPeriodic=0
    g109: BSplineCurve PolesCount=2 KnotsCount=2 Degree=1 IsPeriodic=0
    g110: BSplineCurve PolesCount=2 KnotsCount=2 Degree=1 IsPeriodic=0
    g111: BSplineCurve PolesCount=2 KnotsCount=2 Degree=1 IsPeriodic=0
    g112: BSplineCurve PolesCount=2 KnotsCount=2 Degree=1 IsPeriodic=0
    g113: BSplineCurve PolesCount=2 KnotsCount=2 Degree=1 IsPeriodic=0
    g114: BSplineCurve PolesCount=2 KnotsCount=2 Degree=1 IsPeriodic=0
    g115: BSplineCurve PolesCount=2 KnotsCount=2 Degree=1 IsPeriodic=0
    g116: BSplineCurve PolesCount=2 KnotsCount=2 Degree=1 IsPeriodic=0
    g117: BSplineCurve PolesCount=2 KnotsCount=2 Degree=1 IsPeriodic=0
    g118: BSplineCurve PolesCount=2 KnotsCount=2 Degree=1 IsPeriodic=0
    g119: BSplineCurve PolesCount=2 KnotsCount=2 Degree=1 IsPeriodic=0
    g120: BSplineCurve PolesCount=2 KnotsCount=2 Degree=1 IsPeriodic=0
    g121: BSplineCurve PolesCount=2 KnotsCount=2 Degree=1 IsPeriodic=0
    g122: BSplineCurve PolesCount=2 KnotsCount=2 Degree=1 IsPeriodic=0
    g123: BSplineCurve PolesCount=2 KnotsCount=2 Degree=1 IsPeriodic=0
    g124: BSplineCurve PolesCount=2 KnotsCount=2 Degree=1 IsPeriodic=0
    g125: BSplineCurve PolesCount=2 KnotsCount=2 Degree=1 IsPeriodic=0
    g126: BSplineCurve PolesCount=2 KnotsCount=2 Degree=1 IsPeriodic=0
    g127: BSplineCurve PolesCount=2 KnotsCount=2 Degree=1 IsPeriodic=0
    g128: BSplineCurve PolesCount=2 KnotsCount=2 Degree=1 IsPeriodic=0
    g129: BSplineCurve PolesCount=2 KnotsCount=2 Degree=1 IsPeriodic=0
    g130: BSplineCurve PolesCount=2 KnotsCount=2 Degree=1 IsPeriodic=0
    g131: BSplineCurve PolesCount=2 KnotsCount=2 Degree=1 IsPeriodic=0
    g132: BSplineCurve PolesCount=2 KnotsCount=2 Degree=1 IsPeriodic=0
    g133: BSplineCurve PolesCount=2 KnotsCount=2 Degree=1 IsPeriodic=0
    g134: BSplineCurve PolesCount=2 KnotsCount=2 Degree=1 IsPeriodic=0
    g135: BSplineCurve PolesCount=2 KnotsCount=2 Degree=1 IsPeriodic=0
    g136: BSplineCurve PolesCount=2 KnotsCount=2 Degree=1 IsPeriodic=0
    g137: BSplineCurve PolesCount=2 KnotsCount=2 Degree=1 IsPeriodic=0
    g138: BSplineCurve PolesCount=2 KnotsCount=2 Degree=1 IsPeriodic=0
    g139: BSplineCurve PolesCount=2 KnotsCount=2 Degree=1 IsPeriodic=0
    g140: BSplineCurve PolesCount=2 KnotsCount=2 Degree=1 IsPeriodic=0
    g141: BSplineCurve PolesCount=2 KnotsCount=2 Degree=1 IsPeriodic=0
    g142: BSplineCurve PolesCount=2 KnotsCount=2 Degree=1 IsPeriodic=0
    g143: BSplineCurve PolesCount=2 KnotsCount=2 Degree=1 IsPeriodic=0
    g144: BSplineCurve PolesCount=2 KnotsCount=2 Degree=1 IsPeriodic=0
    g145: BSplineCurve PolesCount=2 KnotsCount=2 Degree=1 IsPeriodic=0
    g146: BSplineCurve PolesCount=2 KnotsCount=2 Degree=1 IsPeriodic=0
    g147: BSplineCurve PolesCount=2 KnotsCount=2 Degree=1 IsPeriodic=0
    g148: BSplineCurve PolesCount=2 KnotsCount=2 Degree=1 IsPeriodic=0
    g149: BSplineCurve PolesCount=2 KnotsCount=2 Degree=1 IsPeriodic=0
    g150: BSplineCurve PolesCount=2 KnotsCount=2 Degree=1 IsPeriodic=0
    g151: BSplineCurve PolesCount=2 KnotsCount=2 Degree=1 IsPeriodic=0
    g152: BSplineCurve PolesCount=2 KnotsCount=2 Degree=1 IsPeriodic=0
    g153: BSplineCurve PolesCount=2 KnotsCount=2 Degree=1 IsPeriodic=0
    g154: BSplineCurve PolesCount=2 KnotsCount=2 Degree=1 IsPeriodic=0
    g155: BSplineCurve PolesCount=2 KnotsCount=2 Degree=1 IsPeriodic=0
    g156: BSplineCurve PolesCount=2 KnotsCount=2 Degree=1 IsPeriodic=0
    g157: BSplineCurve PolesCount=2 KnotsCount=2 Degree=1 IsPeriodic=0
    g158: BSplineCurve PolesCount=2 KnotsCount=2 Degree=1 IsPeriodic=0
    g159: BSplineCurve PolesCount=2 KnotsCount=2 Degree=1 IsPeriodic=0
    g160: BSplineCurve PolesCount=2 KnotsCount=2 Degree=1 IsPeriodic=0
    g161: BSplineCurve PolesCount=2 KnotsCount=2 Degree=1 IsPeriodic=0
    g162: BSplineCurve PolesCount=2 KnotsCount=2 Degree=1 IsPeriodic=0
    g163: BSplineCurve PolesCount=2 KnotsCount=2 Degree=1 IsPeriodic=0
    g164: BSplineCurve PolesCount=2 KnotsCount=2 Degree=1 IsPeriodic=0
    g165: BSplineCurve PolesCount=2 KnotsCount=2 Degree=1 IsPeriodic=0
    g166: BSplineCurve PolesCount=2 KnotsCount=2 Degree=1 IsPeriodic=0
    g167: BSplineCurve PolesCount=2 KnotsCount=2 Degree=1 IsPeriodic=0
    g168: BSplineCurve PolesCount=2 KnotsCount=2 Degree=1 IsPeriodic=0
    g169: BSplineCurve PolesCount=2 KnotsCount=2 Degree=1 IsPeriodic=0
    g170: BSplineCurve PolesCount=2 KnotsCount=2 Degree=1 IsPeriodic=0
    g171: BSplineCurve PolesCount=2 KnotsCount=2 Degree=1 IsPeriodic=0
    g172: BSplineCurve PolesCount=2 KnotsCount=2 Degree=1 IsPeriodic=0
    g173: BSplineCurve PolesCount=2 KnotsCount=2 Degree=1 IsPeriodic=0
    g174: BSplineCurve PolesCount=2 KnotsCount=2 Degree=1 IsPeriodic=0
    g175: BSplineCurve PolesCount=2 KnotsCount=2 Degree=1 IsPeriodic=0
    g176: BSplineCurve PolesCount=2 KnotsCount=2 Degree=1 IsPeriodic=0
    g177: BSplineCurve PolesCount=2 KnotsCount=2 Degree=1 IsPeriodic=0
    g178: BSplineCurve PolesCount=2 KnotsCount=2 Degree=1 IsPeriodic=0
    g179: BSplineCurve PolesCount=2 KnotsCount=2 Degree=1 IsPeriodic=0
    g180: BSplineCurve PolesCount=2 KnotsCount=2 Degree=1 IsPeriodic=0
    g181: BSplineCurve PolesCount=2 KnotsCount=2 Degree=1 IsPeriodic=0
    g182: BSplineCurve PolesCount=2 KnotsCount=2 Degree=1 IsPeriodic=0
    g183: BSplineCurve PolesCount=2 KnotsCount=2 Degree=1 IsPeriodic=0
    g184: BSplineCurve PolesCount=2 KnotsCount=2 Degree=1 IsPeriodic=0
    g185: BSplineCurve PolesCount=2 KnotsCount=2 Degree=1 IsPeriodic=0
    g186: BSplineCurve PolesCount=2 KnotsCount=2 Degree=1 IsPeriodic=0
    g187: BSplineCurve PolesCount=2 KnotsCount=2 Degree=1 IsPeriodic=0
    g188: BSplineCurve PolesCount=2 KnotsCount=2 Degree=1 IsPeriodic=0
    g189: BSplineCurve PolesCount=2 KnotsCount=2 Degree=1 IsPeriodic=0
    g190: BSplineCurve PolesCount=2 KnotsCount=2 Degree=1 IsPeriodic=0
    g191: BSplineCurve PolesCount=2 KnotsCount=2 Degree=1 IsPeriodic=0
    g192: BSplineCurve PolesCount=2 KnotsCount=2 Degree=1 IsPeriodic=0
    g193: BSplineCurve PolesCount=2 KnotsCount=2 Degree=1 IsPeriodic=0
    g194: BSplineCurve PolesCount=2 KnotsCount=2 Degree=1 IsPeriodic=0
    g195: BSplineCurve PolesCount=2 KnotsCount=2 Degree=1 IsPeriodic=0
    g196: BSplineCurve PolesCount=2 KnotsCount=2 Degree=1 IsPeriodic=0
    g197: BSplineCurve PolesCount=2 KnotsCount=2 Degree=1 IsPeriodic=0
    g198: BSplineCurve PolesCount=2 KnotsCount=2 Degree=1 IsPeriodic=0
    g199: BSplineCurve PolesCount=2 KnotsCount=2 Degree=1 IsPeriodic=0
    g200: BSplineCurve PolesCount=2 KnotsCount=2 Degree=1 IsPeriodic=0
    g201: BSplineCurve PolesCount=2 KnotsCount=2 Degree=1 IsPeriodic=0
    g202: BSplineCurve PolesCount=2 KnotsCount=2 Degree=1 IsPeriodic=0
    g203: BSplineCurve PolesCount=2 KnotsCount=2 Degree=1 IsPeriodic=0
    g204: BSplineCurve PolesCount=2 KnotsCount=2 Degree=1 IsPeriodic=0
    g205: BSplineCurve PolesCount=2 KnotsCount=2 Degree=1 IsPeriodic=0
    g206: BSplineCurve PolesCount=2 KnotsCount=2 Degree=1 IsPeriodic=0
    g207: BSplineCurve PolesCount=2 KnotsCount=2 Degree=1 IsPeriodic=0
    g208: BSplineCurve PolesCount=2 KnotsCount=2 Degree=1 IsPeriodic=0
    g209: BSplineCurve PolesCount=2 KnotsCount=2 Degree=1 IsPeriodic=0
    g210: BSplineCurve PolesCount=2 KnotsCount=2 Degree=1 IsPeriodic=0
    g211: BSplineCurve PolesCount=2 KnotsCount=2 Degree=1 IsPeriodic=0
    g212: BSplineCurve PolesCount=2 KnotsCount=2 Degree=1 IsPeriodic=0
    g213: BSplineCurve PolesCount=2 KnotsCount=2 Degree=1 IsPeriodic=0
    g214: BSplineCurve PolesCount=2 KnotsCount=2 Degree=1 IsPeriodic=0
    g215: BSplineCurve PolesCount=2 KnotsCount=2 Degree=1 IsPeriodic=0
    g216: BSplineCurve PolesCount=2 KnotsCount=2 Degree=1 IsPeriodic=0
    g217: BSplineCurve PolesCount=2 KnotsCount=2 Degree=1 IsPeriodic=0
    g218: BSplineCurve PolesCount=2 KnotsCount=2 Degree=1 IsPeriodic=0
    g219: BSplineCurve PolesCount=2 KnotsCount=2 Degree=1 IsPeriodic=0
    g220: BSplineCurve PolesCount=2 KnotsCount=2 Degree=1 IsPeriodic=0
    g221: BSplineCurve PolesCount=2 KnotsCount=2 Degree=1 IsPeriodic=0
    g222: BSplineCurve PolesCount=2 KnotsCount=2 Degree=1 IsPeriodic=0
    g223: BSplineCurve PolesCount=2 KnotsCount=2 Degree=1 IsPeriodic=0
    g224: BSplineCurve PolesCount=2 KnotsCount=2 Degree=1 IsPeriodic=0
    g225: BSplineCurve PolesCount=2 KnotsCount=2 Degree=1 IsPeriodic=0
    g226: BSplineCurve PolesCount=2 KnotsCount=2 Degree=1 IsPeriodic=0
    g227: BSplineCurve PolesCount=2 KnotsCount=2 Degree=1 IsPeriodic=0
    g228: BSplineCurve PolesCount=2 KnotsCount=2 Degree=1 IsPeriodic=0
    g229: BSplineCurve PolesCount=2 KnotsCount=2 Degree=1 IsPeriodic=0
    g230: BSplineCurve PolesCount=2 KnotsCount=2 Degree=1 IsPeriodic=0
    g231: BSplineCurve PolesCount=2 KnotsCount=2 Degree=1 IsPeriodic=0
    g232: BSplineCurve PolesCount=2 KnotsCount=2 Degree=1 IsPeriodic=0
    g233: BSplineCurve PolesCount=2 KnotsCount=2 Degree=1 IsPeriodic=0
    g234: BSplineCurve PolesCount=2 KnotsCount=2 Degree=1 IsPeriodic=0
    g235: BSplineCurve PolesCount=2 KnotsCount=2 Degree=1 IsPeriodic=0
    g236: BSplineCurve PolesCount=2 KnotsCount=2 Degree=1 IsPeriodic=0
    g237: BSplineCurve PolesCount=2 KnotsCount=2 Degree=1 IsPeriodic=0
    g238: BSplineCurve PolesCount=2 KnotsCount=2 Degree=1 IsPeriodic=0
    g239: BSplineCurve PolesCount=2 KnotsCount=2 Degree=1 IsPeriodic=0
    g240: BSplineCurve PolesCount=2 KnotsCount=2 Degree=1 IsPeriodic=0
    g241: BSplineCurve PolesCount=2 KnotsCount=2 Degree=1 IsPeriodic=0
    g242: BSplineCurve PolesCount=2 KnotsCount=2 Degree=1 IsPeriodic=0
    g243: BSplineCurve PolesCount=2 KnotsCount=2 Degree=1 IsPeriodic=0
    g244: BSplineCurve PolesCount=2 KnotsCount=2 Degree=1 IsPeriodic=0
    g245: BSplineCurve PolesCount=2 KnotsCount=2 Degree=1 IsPeriodic=0
    g246: BSplineCurve PolesCount=2 KnotsCount=2 Degree=1 IsPeriodic=0
    g247: BSplineCurve PolesCount=2 KnotsCount=2 Degree=1 IsPeriodic=0
    g248: BSplineCurve PolesCount=2 KnotsCount=2 Degree=1 IsPeriodic=0
    g249: BSplineCurve PolesCount=2 KnotsCount=2 Degree=1 IsPeriodic=0
    g250: BSplineCurve PolesCount=2 KnotsCount=2 Degree=1 IsPeriodic=0
    g251: BSplineCurve PolesCount=2 KnotsCount=2 Degree=1 IsPeriodic=0
    g252: BSplineCurve PolesCount=2 KnotsCount=2 Degree=1 IsPeriodic=0
    g253: BSplineCurve PolesCount=2 KnotsCount=2 Degree=1 IsPeriodic=0
    g254: BSplineCurve PolesCount=2 KnotsCount=2 Degree=1 IsPeriodic=0
    g255: BSplineCurve PolesCount=2 KnotsCount=2 Degree=1 IsPeriodic=0
    g256: BSplineCurve PolesCount=2 KnotsCount=2 Degree=1 IsPeriodic=0
    g257: BSplineCurve PolesCount=2 KnotsCount=2 Degree=1 IsPeriodic=0
    g258: BSplineCurve PolesCount=2 KnotsCount=2 Degree=1 IsPeriodic=0
    g259: BSplineCurve PolesCount=2 KnotsCount=2 Degree=1 IsPeriodic=0
    g260: BSplineCurve PolesCount=2 KnotsCount=2 Degree=1 IsPeriodic=0
    g261: BSplineCurve PolesCount=2 KnotsCount=2 Degree=1 IsPeriodic=0
    g262: BSplineCurve PolesCount=2 KnotsCount=2 Degree=1 IsPeriodic=0
    g263: BSplineCurve PolesCount=2 KnotsCount=2 Degree=1 IsPeriodic=0
    g264: BSplineCurve PolesCount=2 KnotsCount=2 Degree=1 IsPeriodic=0
    g265: BSplineCurve PolesCount=2 KnotsCount=2 Degree=1 IsPeriodic=0
    g266: BSplineCurve PolesCount=2 KnotsCount=2 Degree=1 IsPeriodic=0
    g267: BSplineCurve PolesCount=2 KnotsCount=2 Degree=1 IsPeriodic=0
    g268: BSplineCurve PolesCount=2 KnotsCount=2 Degree=1 IsPeriodic=0
    g269: BSplineCurve PolesCount=2 KnotsCount=2 Degree=1 IsPeriodic=0
    g270: BSplineCurve PolesCount=2 KnotsCount=2 Degree=1 IsPeriodic=0
    g271: BSplineCurve PolesCount=2 KnotsCount=2 Degree=1 IsPeriodic=0
    g272: BSplineCurve PolesCount=2 KnotsCount=2 Degree=1 IsPeriodic=0
    g273: BSplineCurve PolesCount=2 KnotsCount=2 Degree=1 IsPeriodic=0
    g274: BSplineCurve PolesCount=2 KnotsCount=2 Degree=1 IsPeriodic=0
    g275: BSplineCurve PolesCount=2 KnotsCount=2 Degree=1 IsPeriodic=0
    g276: BSplineCurve PolesCount=2 KnotsCount=2 Degree=1 IsPeriodic=0
    g277: BSplineCurve PolesCount=2 KnotsCount=2 Degree=1 IsPeriodic=0
    g278: BSplineCurve PolesCount=2 KnotsCount=2 Degree=1 IsPeriodic=0
    g279: BSplineCurve PolesCount=2 KnotsCount=2 Degree=1 IsPeriodic=0
    g280: BSplineCurve PolesCount=2 KnotsCount=2 Degree=1 IsPeriodic=0
    g281: BSplineCurve PolesCount=2 KnotsCount=2 Degree=1 IsPeriodic=0
    g282: BSplineCurve PolesCount=2 KnotsCount=2 Degree=1 IsPeriodic=0
    g283: BSplineCurve PolesCount=2 KnotsCount=2 Degree=1 IsPeriodic=0
    g284: BSplineCurve PolesCount=2 KnotsCount=2 Degree=1 IsPeriodic=0
    g285: BSplineCurve PolesCount=2 KnotsCount=2 Degree=1 IsPeriodic=0
    g286: BSplineCurve PolesCount=2 KnotsCount=2 Degree=1 IsPeriodic=0
    g287: BSplineCurve PolesCount=2 KnotsCount=2 Degree=1 IsPeriodic=0
    g288: BSplineCurve PolesCount=2 KnotsCount=2 Degree=1 IsPeriodic=0
    g289: BSplineCurve PolesCount=2 KnotsCount=2 Degree=1 IsPeriodic=0
    g290: BSplineCurve PolesCount=2 KnotsCount=2 Degree=1 IsPeriodic=0
    g291: BSplineCurve PolesCount=2 KnotsCount=2 Degree=1 IsPeriodic=0
    g292: BSplineCurve PolesCount=2 KnotsCount=2 Degree=1 IsPeriodic=0
    g293: BSplineCurve PolesCount=2 KnotsCount=2 Degree=1 IsPeriodic=0
    g294: BSplineCurve PolesCount=2 KnotsCount=2 Degree=1 IsPeriodic=0
    g295: BSplineCurve PolesCount=2 KnotsCount=2 Degree=1 IsPeriodic=0
    g296: BSplineCurve PolesCount=2 KnotsCount=2 Degree=1 IsPeriodic=0
    g297: BSplineCurve PolesCount=2 KnotsCount=2 Degree=1 IsPeriodic=0
    g298: BSplineCurve PolesCount=2 KnotsCount=2 Degree=1 IsPeriodic=0
    g299: BSplineCurve PolesCount=2 KnotsCount=2 Degree=1 IsPeriodic=0
    g300: BSplineCurve PolesCount=2 KnotsCount=2 Degree=1 IsPeriodic=0
    g301: BSplineCurve PolesCount=2 KnotsCount=2 Degree=1 IsPeriodic=0
    g302: BSplineCurve PolesCount=2 KnotsCount=2 Degree=1 IsPeriodic=0
    g303: BSplineCurve PolesCount=2 KnotsCount=2 Degree=1 IsPeriodic=0
    g304: BSplineCurve PolesCount=2 KnotsCount=2 Degree=1 IsPeriodic=0
    g305: BSplineCurve PolesCount=2 KnotsCount=2 Degree=1 IsPeriodic=0
    g306: BSplineCurve PolesCount=2 KnotsCount=2 Degree=1 IsPeriodic=0
    g307: BSplineCurve PolesCount=2 KnotsCount=2 Degree=1 IsPeriodic=0
    g308: BSplineCurve PolesCount=2 KnotsCount=2 Degree=1 IsPeriodic=0
    g309: BSplineCurve PolesCount=2 KnotsCount=2 Degree=1 IsPeriodic=0
    g310: BSplineCurve PolesCount=2 KnotsCount=2 Degree=1 IsPeriodic=0
    g311: BSplineCurve PolesCount=2 KnotsCount=2 Degree=1 IsPeriodic=0
    g312: BSplineCurve PolesCount=2 KnotsCount=2 Degree=1 IsPeriodic=0
    g313: BSplineCurve PolesCount=2 KnotsCount=2 Degree=1 IsPeriodic=0
    g314: BSplineCurve PolesCount=2 KnotsCount=2 Degree=1 IsPeriodic=0
    g315: BSplineCurve PolesCount=2 KnotsCount=2 Degree=1 IsPeriodic=0
    g316: BSplineCurve PolesCount=2 KnotsCount=2 Degree=1 IsPeriodic=0
    g317: BSplineCurve PolesCount=2 KnotsCount=2 Degree=1 IsPeriodic=0
    g318: BSplineCurve PolesCount=2 KnotsCount=2 Degree=1 IsPeriodic=0
    g319: BSplineCurve PolesCount=2 KnotsCount=2 Degree=1 IsPeriodic=0
    g320: BSplineCurve PolesCount=2 KnotsCount=2 Degree=1 IsPeriodic=0
    g321: BSplineCurve PolesCount=2 KnotsCount=2 Degree=1 IsPeriodic=0
    g322: BSplineCurve PolesCount=2 KnotsCount=2 Degree=1 IsPeriodic=0
    g323: BSplineCurve PolesCount=2 KnotsCount=2 Degree=1 IsPeriodic=0
    g324: BSplineCurve PolesCount=2 KnotsCount=2 Degree=1 IsPeriodic=0
    g325: BSplineCurve PolesCount=2 KnotsCount=2 Degree=1 IsPeriodic=0
    g326: BSplineCurve PolesCount=2 KnotsCount=2 Degree=1 IsPeriodic=0
    g327: BSplineCurve PolesCount=2 KnotsCount=2 Degree=1 IsPeriodic=0
    g328: BSplineCurve PolesCount=2 KnotsCount=2 Degree=1 IsPeriodic=0
    g329: BSplineCurve PolesCount=2 KnotsCount=2 Degree=1 IsPeriodic=0
    g330: BSplineCurve PolesCount=2 KnotsCount=2 Degree=1 IsPeriodic=0
    g331: BSplineCurve PolesCount=2 KnotsCount=2 Degree=1 IsPeriodic=0
    g332: BSplineCurve PolesCount=2 KnotsCount=2 Degree=1 IsPeriodic=0
    g333: BSplineCurve PolesCount=2 KnotsCount=2 Degree=1 IsPeriodic=0
    g334: BSplineCurve PolesCount=2 KnotsCount=2 Degree=1 IsPeriodic=0
    g335: BSplineCurve PolesCount=2 KnotsCount=2 Degree=1 IsPeriodic=0
    g336: BSplineCurve PolesCount=2 KnotsCount=2 Degree=1 IsPeriodic=0
    g337: BSplineCurve PolesCount=2 KnotsCount=2 Degree=1 IsPeriodic=0
    g338: BSplineCurve PolesCount=2 KnotsCount=2 Degree=1 IsPeriodic=0
    g339: BSplineCurve PolesCount=2 KnotsCount=2 Degree=1 IsPeriodic=0
    g340: BSplineCurve PolesCount=2 KnotsCount=2 Degree=1 IsPeriodic=0
    g341: BSplineCurve PolesCount=2 KnotsCount=2 Degree=1 IsPeriodic=0
    g342: BSplineCurve PolesCount=2 KnotsCount=2 Degree=1 IsPeriodic=0
    g343: BSplineCurve PolesCount=2 KnotsCount=2 Degree=1 IsPeriodic=0
    g344: BSplineCurve PolesCount=2 KnotsCount=2 Degree=1 IsPeriodic=0
    g345: BSplineCurve PolesCount=2 KnotsCount=2 Degree=1 IsPeriodic=0
    g346: BSplineCurve PolesCount=2 KnotsCount=2 Degree=1 IsPeriodic=0
    g347: BSplineCurve PolesCount=2 KnotsCount=2 Degree=1 IsPeriodic=0
    g348: BSplineCurve PolesCount=2 KnotsCount=2 Degree=1 IsPeriodic=0
    g349: BSplineCurve PolesCount=2 KnotsCount=2 Degree=1 IsPeriodic=0
    g350: BSplineCurve PolesCount=2 KnotsCount=2 Degree=1 IsPeriodic=0
    g351: BSplineCurve PolesCount=2 KnotsCount=2 Degree=1 IsPeriodic=0
    g352: BSplineCurve PolesCount=2 KnotsCount=2 Degree=1 IsPeriodic=0
    g353: BSplineCurve PolesCount=2 KnotsCount=2 Degree=1 IsPeriodic=0
    g354: BSplineCurve PolesCount=2 KnotsCount=2 Degree=1 IsPeriodic=0
    g355: BSplineCurve PolesCount=2 KnotsCount=2 Degree=1 IsPeriodic=0
    g356: BSplineCurve PolesCount=2 KnotsCount=2 Degree=1 IsPeriodic=0
    g357: BSplineCurve PolesCount=2 KnotsCount=2 Degree=1 IsPeriodic=0
    g358: BSplineCurve PolesCount=2 KnotsCount=2 Degree=1 IsPeriodic=0
    g359: BSplineCurve PolesCount=2 KnotsCount=2 Degree=1 IsPeriodic=0
    g360: BSplineCurve PolesCount=2 KnotsCount=2 Degree=1 IsPeriodic=0
    g361: BSplineCurve PolesCount=2 KnotsCount=2 Degree=1 IsPeriodic=0
    g362: BSplineCurve PolesCount=2 KnotsCount=2 Degree=1 IsPeriodic=0
    g363: BSplineCurve PolesCount=2 KnotsCount=2 Degree=1 IsPeriodic=0
    g364: BSplineCurve PolesCount=2 KnotsCount=2 Degree=1 IsPeriodic=0
    g365: BSplineCurve PolesCount=2 KnotsCount=2 Degree=1 IsPeriodic=0
    g366: BSplineCurve PolesCount=2 KnotsCount=2 Degree=1 IsPeriodic=0
    g367: BSplineCurve PolesCount=2 KnotsCount=2 Degree=1 IsPeriodic=0
    g368: BSplineCurve PolesCount=2 KnotsCount=2 Degree=1 IsPeriodic=0
    g369: BSplineCurve PolesCount=2 KnotsCount=2 Degree=1 IsPeriodic=0
    g370: BSplineCurve PolesCount=2 KnotsCount=2 Degree=1 IsPeriodic=0
    g371: BSplineCurve PolesCount=2 KnotsCount=2 Degree=1 IsPeriodic=0
    g372: BSplineCurve PolesCount=2 KnotsCount=2 Degree=1 IsPeriodic=0
    g373: BSplineCurve PolesCount=2 KnotsCount=2 Degree=1 IsPeriodic=0
    g374: BSplineCurve PolesCount=2 KnotsCount=2 Degree=1 IsPeriodic=0
    g375: BSplineCurve PolesCount=2 KnotsCount=2 Degree=1 IsPeriodic=0
    g376: BSplineCurve PolesCount=2 KnotsCount=2 Degree=1 IsPeriodic=0
    g377: BSplineCurve PolesCount=2 KnotsCount=2 Degree=1 IsPeriodic=0
    g378: BSplineCurve PolesCount=2 KnotsCount=2 Degree=1 IsPeriodic=0
    g379: BSplineCurve PolesCount=2 KnotsCount=2 Degree=1 IsPeriodic=0
    g380: BSplineCurve PolesCount=2 KnotsCount=2 Degree=1 IsPeriodic=0
    g381: BSplineCurve PolesCount=2 KnotsCount=2 Degree=1 IsPeriodic=0
    g382: BSplineCurve PolesCount=2 KnotsCount=2 Degree=1 IsPeriodic=0
    g383: BSplineCurve PolesCount=2 KnotsCount=2 Degree=1 IsPeriodic=0
    g384: BSplineCurve PolesCount=2 KnotsCount=2 Degree=1 IsPeriodic=0
    g385: BSplineCurve PolesCount=2 KnotsCount=2 Degree=1 IsPeriodic=0
    g386: BSplineCurve PolesCount=2 KnotsCount=2 Degree=1 IsPeriodic=0
    g387: BSplineCurve PolesCount=2 KnotsCount=2 Degree=1 IsPeriodic=0
    g388: BSplineCurve PolesCount=2 KnotsCount=2 Degree=1 IsPeriodic=0
    g389: BSplineCurve PolesCount=2 KnotsCount=2 Degree=1 IsPeriodic=0
    g390: BSplineCurve PolesCount=2 KnotsCount=2 Degree=1 IsPeriodic=0
    g391: BSplineCurve PolesCount=2 KnotsCount=2 Degree=1 IsPeriodic=0
    g392: BSplineCurve PolesCount=2 KnotsCount=2 Degree=1 IsPeriodic=0
    g393: BSplineCurve PolesCount=2 KnotsCount=2 Degree=1 IsPeriodic=0
    g394: BSplineCurve PolesCount=2 KnotsCount=2 Degree=1 IsPeriodic=0
    g395: BSplineCurve PolesCount=2 KnotsCount=2 Degree=1 IsPeriodic=0
    g396: BSplineCurve PolesCount=2 KnotsCount=2 Degree=1 IsPeriodic=0
    g397: BSplineCurve PolesCount=2 KnotsCount=2 Degree=1 IsPeriodic=0
    g398: BSplineCurve PolesCount=2 KnotsCount=2 Degree=1 IsPeriodic=0
    g399: BSplineCurve PolesCount=2 KnotsCount=2 Degree=1 IsPeriodic=0
    ... +460 more geometry lines
  constraints (860):
    c: Coincident(g0,g1)
    c: Coincident(g1,g2)
    c: Coincident(g2,g3)
    c: Coincident(g3,g4)
    c: Coincident(g4,g5)
    c: Coincident(g5,g6)
    c: Coincident(g6,g7)
    c: Coincident(g7,g8)
    c: Coincident(g8,g9)
    c: Coincident(g9,g10)
    c: Coincident(g10,g11)
    c: Coincident(g11,g12)
    c: Coincident(g12,g13)
    c: Coincident(g13,g14)
    c: Coincident(g14,g15)
    c: Coincident(g15,g16)
    c: Coincident(g16,g17)
    c: Coincident(g17,g18)
    c: Coincident(g18,g19)
    c: Coincident(g19,g20)
    c: Coincident(g20,g21)
    c: Coincident(g21,g22)
    c: Coincident(g22,g23)
    c: Coincident(g23,g24)
    c: Coincident(g24,g25)
    c: Coincident(g25,g26)
    c: Coincident(g26,g27)
    c: Coincident(g27,g28)
    c: Coincident(g28,g29)
    c: Coincident(g29,g30)
    c: Coincident(g30,g31)
    c: Coincident(g31,g32)
    c: Coincident(g32,g33)
    c: Coincident(g33,g34)
    c: Coincident(g34,g35)
    c: Coincident(g35,g36)
    c: Coincident(g36,g37)
    c: Coincident(g37,g38)
    c: Coincident(g38,g39)
    c: Coincident(g39,g40)
    c: Coincident(g40,g41)
    c: Coincident(g41,g42)
    c: Coincident(g42,g43)
    c: Coincident(g43,g44)
    c: Coincident(g44,g45)
    c: Coincident(g45,g46)
    c: Coincident(g46,g47)
    c: Coincident(g47,g48)
    c: Coincident(g48,g49)
    c: Coincident(g49,g50)
    c: Coincident(g50,g51)
    c: Coincident(g51,g52)
    c: Coincident(g52,g53)
    c: Coincident(g53,g54)
    c: Coincident(g54,g55)
    c: Coincident(g55,g56)
    c: Coincident(g56,g57)
    c: Coincident(g57,g58)
    c: Coincident(g58,g59)
    c: Coincident(g59,g60)
    c: Coincident(g60,g61)
    c: Coincident(g61,g62)
    c: Coincident(g62,g63)
    c: Coincident(g63,g64)
    c: Coincident(g64,g65)
    c: Coincident(g65,g66)
    c: Coincident(g66,g67)
    c: Coincident(g67,g68)
    c: Coincident(g68,g69)
    c: Coincident(g69,g70)
    c: Coincident(g70,g71)
    c: Coincident(g71,g72)
    c: Coincident(g72,g73)
    c: Coincident(g73,g74)
    c: Coincident(g74,g75)
    c: Coincident(g75,g76)
    c: Coincident(g76,g77)
    c: Coincident(g77,g78)
    c: Coincident(g78,g79)
    c: Coincident(g79,g80)
    c: Coincident(g80,g81)
    c: Coincident(g81,g82)
    c: Coincident(g82,g83)
    c: Coincident(g83,g84)
    c: Coincident(g84,g85)
    c: Coincident(g85,g86)
    c: Coincident(g86,g87)
    c: Coincident(g87,g0)
    c: Coincident(g88,g89)
    c: Coincident(g89,g90)
    c: Coincident(g90,g91)
    c: Coincident(g91,g92)
    c: Coincident(g92,g93)
    c: Coincident(g93,g94)
    c: Coincident(g94,g95)
    c: Coincident(g95,g96)
    c: Coincident(g96,g97)
    c: Coincident(g97,g98)
    c: Coincident(g98,g99)
    c: Coincident(g99,g100)
    c: Coincident(g100,g101)
    c: Coincident(g101,g102)
    c: Coincident(g102,g103)
    c: Coincident(g103,g104)
    c: Coincident(g104,g105)
    c: Coincident(g105,g106)
    c: Coincident(g106,g107)
    c: Coincident(g107,g108)
    c: Coincident(g108,g109)
    c: Coincident(g109,g110)
    c: Coincident(g110,g111)
    c: Coincident(g111,g112)
    c: Coincident(g112,g113)
    c: Coincident(g113,g114)
    c: Coincident(g114,g115)
    c: Coincident(g115,g116)
    c: Coincident(g116,g117)
    c: Coincident(g117,g118)
    c: Coincident(g118,g119)
    c: Coincident(g119,g120)
    c: Coincident(g120,g121)
    c: Coincident(g121,g122)
    c: Coincident(g122,g123)
    c: Coincident(g123,g124)
    c: Coincident(g124,g125)
    c: Coincident(g125,g126)
    c: Coincident(g126,g127)
    c: Coincident(g127,g88)
    c: Coincident(g128,g129)
    c: Coincident(g129,g130)
    c: Coincident(g130,g131)
    c: Coincident(g131,g132)
    c: Coincident(g132,g133)
    c: Coincident(g133,g134)
    c: Coincident(g134,g135)
    c: Coincident(g135,g136)
    c: Coincident(g136,g137)
    c: Coincident(g137,g138)
    c: Coincident(g138,g139)
    c: Coincident(g139,g140)
    c: Coincident(g140,g141)
    c: Coincident(g141,g142)
    c: Coincident(g142,g143)
    c: Coincident(g143,g144)
    c: Coincident(g144,g145)
    c: Coincident(g145,g146)
    c: Coincident(g146,g147)
    c: Coincident(g147,g148)
    c: Coincident(g148,g149)
    c: Coincident(g149,g150)
    c: Coincident(g150,g151)
    c: Coincident(g151,g152)
    c: Coincident(g152,g153)
    c: Coincident(g153,g154)
    c: Coincident(g154,g155)
    c: Coincident(g155,g156)
    c: Coincident(g156,g157)
    c: Coincident(g157,g158)
    c: Coincident(g158,g159)
    c: Coincident(g159,g160)
    c: Coincident(g160,g161)
    c: Coincident(g161,g162)
    c: Coincident(g162,g163)
    c: Coincident(g163,g164)
    c: Coincident(g164,g165)
    c: Coincident(g165,g166)
    c: Coincident(g166,g167)
    c: Coincident(g167,g168)
    c: Coincident(g168,g169)
    c: Coincident(g169,g170)
    c: Coincident(g170,g171)
    c: Coincident(g171,g172)
    c: Coincident(g172,g173)
    c: Coincident(g173,g174)
    c: Coincident(g174,g175)
    c: Coincident(g175,g176)
    c: Coincident(g176,g177)
    c: Coincident(g177,g178)
    c: Coincident(g178,g179)
    c: Coincident(g179,g180)
    c: Coincident(g180,g181)
    c: Coincident(g181,g182)
    c: Coincident(g182,g183)
    c: Coincident(g183,g184)
    c: Coincident(g184,g185)
    c: Coincident(g185,g186)
    c: Coincident(g186,g187)
    c: Coincident(g187,g188)
    c: Coincident(g188,g189)
    c: Coincident(g189,g190)
    c: Coincident(g190,g191)
    c: Coincident(g191,g192)
    c: Coincident(g192,g193)
    c: Coincident(g193,g194)
    c: Coincident(g194,g195)
    c: Coincident(g195,g196)
    c: Coincident(g196,g197)
    c: Coincident(g197,g198)
    c: Coincident(g198,g199)
    c: Coincident(g199,g200)
    c: Coincident(g200,g201)
    c: Coincident(g201,g202)
    c: Coincident(g202,g203)
    c: Coincident(g203,g204)
    c: Coincident(g204,g205)
    c: Coincident(g205,g206)
    c: Coincident(g206,g207)
    c: Coincident(g207,g208)
    c: Coincident(g208,g209)
    c: Coincident(g209,g210)
    c: Coincident(g210,g211)
    c: Coincident(g211,g212)
    c: Coincident(g212,g213)
    c: Coincident(g213,g214)
    c: Coincident(g214,g215)
    c: Coincident(g215,g216)
    c: Coincident(g216,g217)
    c: Coincident(g217,g218)
    c: Coincident(g218,g219)
    c: Coincident(g219,g220)
    c: Coincident(g220,g221)
    c: Coincident(g221,g222)
    c: Coincident(g222,g223)
    c: Coincident(g223,g224)
    c: Coincident(g224,g225)
    c: Coincident(g225,g226)
    c: Coincident(g226,g227)
    c: Coincident(g227,g228)
    c: Coincident(g228,g229)
    c: Coincident(g229,g230)
    c: Coincident(g230,g231)
    c: Coincident(g231,g232)
    c: Coincident(g232,g233)
    c: Coincident(g233,g234)
    c: Coincident(g234,g235)
    c: Coincident(g235,g236)
    c: Coincident(g236,g237)
    c: Coincident(g237,g238)
    c: Coincident(g238,g239)
    c: Coincident(g239,g128)
    c: Coincident(g240,g241)
    c: Coincident(g241,g242)
    c: Coincident(g242,g243)
    c: Coincident(g243,g244)
    c: Coincident(g244,g245)
    c: Coincident(g245,g246)
    c: Coincident(g246,g247)
    c: Coincident(g247,g248)
    c: Coincident(g248,g249)
    c: Coincident(g249,g250)
    c: Coincident(g250,g251)
    c: Coincident(g251,g252)
    c: Coincident(g252,g253)
    c: Coincident(g253,g254)
    c: Coincident(g254,g255)
    c: Coincident(g255,g256)
    c: Coincident(g256,g257)
    c: Coincident(g257,g258)
    c: Coincident(g258,g259)
    c: Coincident(g259,g260)
    c: Coincident(g260,g261)
    c: Coincident(g261,g262)
    c: Coincident(g262,g263)
    c: Coincident(g263,g264)
    c: Coincident(g264,g265)
    c: Coincident(g265,g266)
    c: Coincident(g266,g267)
    c: Coincident(g267,g268)
    c: Coincident(g268,g269)
    c: Coincident(g269,g270)
    c: Coincident(g270,g271)
    c: Coincident(g271,g272)
    c: Coincident(g272,g273)
    c: Coincident(g273,g274)
    c: Coincident(g274,g275)
    c: Coincident(g275,g276)
    c: Coincident(g276,g277)
    c: Coincident(g277,g278)
    c: Coincident(g278,g279)
    c: Coincident(g279,g280)
    c: Coincident(g280,g281)
    c: Coincident(g281,g282)
    c: Coincident(g282,g283)
    c: Coincident(g283,g284)
    c: Coincident(g284,g285)
    c: Coincident(g285,g286)
    c: Coincident(g286,g287)
    c: Coincident(g287,g240)
    c: Coincident(g288,g289)
    c: Coincident(g289,g290)
    c: Coincident(g290,g291)
    c: Coincident(g291,g292)
    c: Coincident(g292,g293)
    c: Coincident(g293,g294)
    c: Coincident(g294,g295)
    c: Coincident(g295,g296)
    c: Coincident(g296,g297)
    c: Coincident(g297,g298)
    c: Coincident(g298,g299)
    c: Coincident(g299,g300)
    c: Coincident(g300,g301)
    c: Coincident(g301,g302)
    c: Coincident(g302,g303)
    c: Coincident(g303,g304)
    c: Coincident(g304,g305)
    c: Coincident(g305,g306)
    c: Coincident(g306,g307)
    c: Coincident(g307,g308)
    c: Coincident(g308,g309)
    c: Coincident(g309,g310)
    c: Coincident(g310,g311)
    c: Coincident(g311,g288)
    c: Coincident(g312,g313)
    c: Coincident(g313,g314)
    c: Coincident(g314,g315)
    c: Coincident(g315,g316)
    c: Coincident(g316,g317)
    c: Coincident(g317,g318)
    c: Coincident(g318,g319)
    c: Coincident(g319,g320)
    c: Coincident(g320,g321)
    c: Coincident(g321,g322)
    c: Coincident(g322,g323)
    c: Coincident(g323,g324)
    c: Coincident(g324,g325)
    c: Coincident(g325,g326)
    c: Coincident(g326,g327)
    c: Coincident(g327,g312)
    c: Coincident(g328,g329)
    c: Coincident(g329,g330)
    c: Coincident(g330,g331)
    c: Coincident(g331,g332)
    c: Coincident(g332,g333)
    c: Coincident(g333,g334)
    c: Coincident(g334,g335)
    c: Coincident(g335,g336)
    c: Coincident(g336,g337)
    c: Coincident(g337,g338)
    c: Coincident(g338,g339)
    c: Coincident(g339,g340)
    c: Coincident(g340,g341)
    c: Coincident(g341,g342)
    c: Coincident(g342,g343)
    c: Coincident(g343,g344)
    c: Coincident(g344,g345)
    c: Coincident(g345,g346)
    c: Coincident(g346,g347)
    c: Coincident(g347,g348)
    c: Coincident(g348,g349)
    c: Coincident(g349,g350)
    c: Coincident(g350,g351)
    c: Coincident(g351,g352)
    c: Coincident(g352,g353)
    c: Coincident(g353,g354)
    c: Coincident(g354,g355)
    c: Coincident(g355,g356)
    c: Coincident(g356,g357)
    c: Coincident(g357,g358)
    c: Coincident(g358,g359)
    c: Coincident(g359,g360)
    c: Coincident(g360,g361)
    c: Coincident(g361,g362)
    c: Coincident(g362,g363)
    c: Coincident(g363,g364)
    c: Coincident(g364,g365)
    c: Coincident(g365,g366)
    c: Coincident(g366,g367)
    c: Coincident(g367,g368)
    c: Coincident(g368,g369)
    c: Coincident(g369,g370)
    c: Coincident(g370,g371)
    c: Coincident(g371,g372)
    c: Coincident(g372,g373)
    c: Coincident(g373,g374)
    c: Coincident(g374,g375)
    c: Coincident(g375,g376)
    c: Coincident(g376,g377)
    c: Coincident(g377,g378)
    c: Coincident(g378,g379)
    c: Coincident(g379,g380)
    c: Coincident(g380,g381)
    c: Coincident(g381,g382)
    c: Coincident(g382,g383)
    c: Coincident(g383,g384)
    c: Coincident(g384,g385)
    c: Coincident(g385,g386)
    c: Coincident(g386,g387)
    c: Coincident(g387,g388)
    c: Coincident(g388,g389)
    c: Coincident(g389,g390)
    c: Coincident(g390,g391)
    c: Coincident(g391,g392)
    c: Coincident(g392,g393)
    c: Coincident(g393,g394)
    c: Coincident(g394,g395)
    c: Coincident(g395,g396)
    c: Coincident(g396,g397)
    c: Coincident(g397,g398)
    c: Coincident(g398,g399)
    c: Coincident(g399,g328)
    c: Coincident(g400,g401)
    c: Coincident(g401,g402)
    c: Coincident(g402,g403)
    c: Coincident(g403,g404)
    c: Coincident(g404,g405)
    c: Coincident(g405,g406)
    c: Coincident(g406,g407)
    c: Coincident(g407,g408)
    c: Coincident(g408,g409)
    c: Coincident(g409,g410)
    c: Coincident(g410,g411)
    c: Coincident(g411,g412)
    c: Coincident(g412,g413)
    c: Coincident(g413,g414)
    c: Coincident(g414,g415)
    c: Coincident(g415,g416)
    c: Coincident(g416,g417)
    c: Coincident(g417,g418)
    c: Coincident(g418,g419)
    c: Coincident(g419,g420)
    c: Coincident(g420,g421)
    c: Coincident(g421,g422)
    c: Coincident(g422,g423)
    c: Coincident(g423,g400)
    c: Coincident(g424,g425)
    c: Coincident(g425,g426)
    c: Coincident(g426,g427)
    c: Coincident(g427,g428)
    c: Coincident(g428,g429)
    c: Coincident(g429,g430)
    c: Coincident(g430,g431)
    c: Coincident(g431,g432)
    c: Coincident(g432,g433)
    c: Coincident(g433,g434)
    c: Coincident(g434,g435)
    c: Coincident(g435,g436)
    c: Coincident(g436,g437)
    c: Coincident(g437,g438)
    c: Coincident(g438,g439)
    c: Coincident(g439,g440)
    c: Coincident(g440,g441)
    c: Coincident(g441,g442)
    c: Coincident(g442,g443)
    c: Coincident(g443,g444)
    c: Coincident(g444,g445)
    c: Coincident(g445,g446)
    c: Coincident(g446,g447)
    c: Coincident(g447,g448)
    c: Coincident(g448,g449)
    c: Coincident(g449,g450)
    c: Coincident(g450,g451)
    c: Coincident(g451,g452)
    c: Coincident(g452,g453)
    c: Coincident(g453,g454)
    c: Coincident(g454,g455)
    c: Coincident(g455,g456)
    c: Coincident(g456,g457)
    c: Coincident(g457,g458)
    c: Coincident(g458,g459)
    c: Coincident(g459,g460)
    c: Coincident(g460,g461)
    c: Coincident(g461,g462)
    c: Coincident(g462,g463)
    c: Coincident(g463,g464)
    c: Coincident(g464,g465)
    c: Coincident(g465,g466)
    c: Coincident(g466,g467)
    c: Coincident(g467,g468)
    c: Coincident(g468,g469)
    c: Coincident(g469,g470)
    c: Coincident(g470,g471)
    c: Coincident(g471,g472)
    c: Coincident(g472,g473)
    c: Coincident(g473,g474)
    c: Coincident(g474,g475)
    c: Coincident(g475,g476)
    c: Coincident(g476,g477)
    c: Coincident(g477,g478)
    c: Coincident(g478,g479)
    c: Coincident(g479,g424)
    c: Coincident(g480,g481)
    c: Coincident(g481,g482)
    c: Coincident(g482,g483)
    c: Coincident(g483,g484)
    c: Coincident(g484,g485)
    c: Coincident(g485,g486)
    c: Coincident(g486,g487)
    c: Coincident(g487,g488)
    c: Coincident(g488,g489)
    c: Coincident(g489,g490)
    c: Coincident(g490,g491)
    c: Coincident(g491,g492)
    c: Coincident(g492,g493)
    c: Coincident(g493,g494)
    c: Coincident(g494,g495)
    c: Coincident(g495,g480)
    c: Coincident(g496,g497)
    c: Coincident(g497,g498)
    c: Coincident(g498,g499)
    c: Coincident(g499,g500)
    c: Coincident(g500,g501)
    c: Coincident(g501,g502)
    c: Coincident(g502,g503)
    c: Coincident(g503,g504)
    c: Coincident(g504,g505)
    c: Coincident(g505,g506)
    c: Coincident(g506,g507)
    c: Coincident(g507,g508)
    c: Coincident(g508,g509)
    c: Coincident(g509,g510)
    c: Coincident(g510,g511)
    c: Coincident(g511,g512)
    c: Coincident(g512,g513)
    c: Coincident(g513,g514)
    c: Coincident(g514,g515)
    c: Coincident(g515,g516)
    c: Coincident(g516,g517)
    c: Coincident(g517,g518)
    c: Coincident(g518,g519)
    c: Coincident(g519,g520)
    c: Coincident(g520,g521)
    c: Coincident(g521,g522)
    c: Coincident(g522,g523)
    c: Coincident(g523,g524)
    c: Coincident(g524,g525)
    c: Coincident(g525,g526)
    c: Coincident(g526,g527)
    c: Coincident(g527,g528)
    c: Coincident(g528,g529)
    c: Coincident(g529,g530)
    c: Coincident(g530,g531)
    c: Coincident(g531,g532)
    c: Coincident(g532,g533)
    c: Coincident(g533,g534)
    c: Coincident(g534,g535)
    c: Coincident(g535,g496)
    c: Coincident(g536,g537)
    c: Coincident(g537,g538)
    c: Coincident(g538,g539)
    c: Coincident(g539,g540)
    c: Coincident(g540,g541)
    c: Coincident(g541,g542)
    c: Coincident(g542,g543)
    c: Coincident(g543,g544)
    c: Coincident(g544,g545)
    c: Coincident(g545,g546)
    c: Coincident(g546,g547)
    c: Coincident(g547,g548)
    c: Coincident(g548,g549)
    c: Coincident(g549,g550)
    c: Coincident(g550,g551)
    c: Coincident(g551,g552)
    c: Coincident(g552,g553)
    c: Coincident(g553,g554)
    c: Coincident(g554,g555)
    c: Coincident(g555,g556)
    c: Coincident(g556,g557)
    c: Coincident(g557,g558)
    c: Coincident(g558,g559)
    c: Coincident(g559,g560)
    c: Coincident(g560,g561)
    c: Coincident(g561,g562)
    c: Coincident(g562,g563)
    c: Coincident(g563,g564)
    c: Coincident(g564,g565)
    c: Coincident(g565,g566)
    c: Coincident(g566,g567)
    c: Coincident(g567,g568)
    c: Coincident(g568,g569)
    c: Coincident(g569,g570)
    c: Coincident(g570,g571)
    c: Coincident(g571,g572)
    c: Coincident(g572,g573)
    c: Coincident(g573,g574)
    c: Coincident(g574,g575)
    c: Coincident(g575,g536)
    c: Coincident(g576,g577)
    c: Coincident(g577,g578)
    c: Coincident(g578,g579)
    c: Coincident(g579,g580)
    c: Coincident(g580,g581)
    c: Coincident(g581,g582)
    c: Coincident(g582,g583)
    c: Coincident(g583,g584)
    c: Coincident(g584,g585)
    c: Coincident(g585,g586)
    c: Coincident(g586,g587)
    c: Coincident(g587,g576)
    c: Coincident(g588,g589)
    c: Coincident(g589,g590)
    c: Coincident(g590,g591)
    c: Coincident(g591,g592)
    c: Coincident(g592,g593)
    c: Coincident(g593,g594)
    c: Coincident(g594,g595)
    c: Coincident(g595,g596)
    c: Coincident(g596,g597)
    c: Coincident(g597,g598)
    c: Coincident(g598,g599)
    c: Coincident(g599,g600)
    c: Coincident(g600,g601)
    c: Coincident(g601,g602)
    c: Coincident(g602,g603)
    c: Coincident(g603,g604)
    c: Coincident(g604,g605)
    c: Coincident(g605,g606)
    c: Coincident(g606,g607)
    c: Coincident(g607,g608)
    c: Coincident(g608,g609)
    c: Coincident(g609,g610)
    c: Coincident(g610,g611)
    c: Coincident(g611,g612)
    c: Coincident(g612,g613)
    c: Coincident(g613,g614)
    c: Coincident(g614,g615)
    c: Coincident(g615,g616)
    c: Coincident(g616,g617)
    c: Coincident(g617,g618)
    c: Coincident(g618,g619)
    c: Coincident(g619,g620)
    c: Coincident(g620,g621)
    c: Coincident(g621,g622)
    c: Coincident(g622,g623)
    c: Coincident(g623,g624)
    c: Coincident(g624,g625)
    c: Coincident(g625,g626)
    c: Coincident(g626,g627)
    c: Coincident(g627,g628)
    c: Coincident(g628,g629)
    c: Coincident(g629,g630)
    c: Coincident(g630,g631)
    c: Coincident(g631,g632)
    c: Coincident(g632,g633)
    c: Coincident(g633,g634)
    c: Coincident(g634,g635)
    c: Coincident(g635,g636)
    c: Coincident(g636,g637)
    c: Coincident(g637,g638)
    c: Coincident(g638,g639)
    c: Coincident(g639,g640)
    c: Coincident(g640,g641)
    c: Coincident(g641,g642)
    c: Coincident(g642,g643)
    c: Coincident(g643,g644)
    c: Coincident(g644,g645)
    c: Coincident(g645,g646)
    c: Coincident(g646,g647)
    c: Coincident(g647,g648)
    c: Coincident(g648,g649)
    c: Coincident(g649,g650)
    c: Coincident(g650,g651)
    c: Coincident(g651,g652)
    c: Coincident(g652,g653)
    c: Coincident(g653,g654)
    c: Coincident(g654,g655)
    c: Coincident(g655,g656)
    c: Coincident(g656,g657)
    c: Coincident(g657,g658)
    c: Coincident(g658,g659)
    c: Coincident(g659,g660)
    c: Coincident(g660,g661)
    c: Coincident(g661,g662)
    c: Coincident(g662,g663)
    c: Coincident(g663,g664)
    c: Coincident(g664,g665)
    c: Coincident(g665,g666)
    c: Coincident(g666,g667)
    c: Coincident(g667,g668)
    c: Coincident(g668,g669)
    c: Coincident(g669,g670)
    c: Coincident(g670,g671)
    c: Coincident(g671,g672)
    c: Coincident(g672,g673)
    c: Coincident(g673,g674)
    c: Coincident(g674,g675)
    c: Coincident(g675,g588)
    c: Coincident(g676,g677)
    c: Coincident(g677,g678)
    c: Coincident(g678,g679)
    c: Coincident(g679,g680)
    c: Coincident(g680,g681)
    c: Coincident(g681,g682)
    c: Coincident(g682,g683)
    c: Coincident(g683,g684)
    c: Coincident(g684,g685)
    c: Coincident(g685,g686)
    c: Coincident(g686,g687)
    c: Coincident(g687,g688)
    c: Coincident(g688,g689)
    c: Coincident(g689,g690)
    c: Coincident(g690,g691)
    c: Coincident(g691,g676)
    c: Coincident(g692,g693)
    c: Coincident(g693,g694)
    c: Coincident(g694,g695)
    c: Coincident(g695,g696)
    c: Coincident(g696,g697)
    c: Coincident(g697,g698)
    c: Coincident(g698,g699)
    c: Coincident(g699,g700)
    c: Coincident(g700,g701)
    c: Coincident(g701,g702)
    c: Coincident(g702,g703)
    c: Coincident(g703,g704)
    c: Coincident(g704,g705)
    c: Coincident(g705,g706)
    c: Coincident(g706,g707)
    c: Coincident(g707,g708)
    c: Coincident(g708,g709)
    c: Coincident(g709,g710)
    c: Coincident(g710,g711)
    c: Coincident(g711,g712)
    c: Coincident(g712,g713)
    c: Coincident(g713,g714)
    c: Coincident(g714,g715)
    c: Coincident(g715,g716)
    c: Coincident(g716,g717)
    c: Coincident(g717,g718)
    c: Coincident(g718,g719)
    c: Coincident(g719,g720)
    c: Coincident(g720,g721)
    c: Coincident(g721,g722)
    c: Coincident(g722,g723)
    c: Coincident(g723,g724)
    c: Coincident(g724,g725)
    c: Coincident(g725,g726)
    c: Coincident(g726,g727)
    c: Coincident(g727,g728)
    c: Coincident(g728,g729)
    c: Coincident(g729,g730)
    c: Coincident(g730,g731)
    c: Coincident(g731,g692)
    c: Coincident(g732,g733)
    c: Coincident(g733,g734)
    c: Coincident(g734,g735)
    c: Coincident(g735,g736)
    c: Coincident(g736,g737)
    c: Coincident(g737,g738)
    c: Coincident(g738,g739)
    c: Coincident(g739,g740)
    c: Coincident(g740,g741)
    c: Coincident(g741,g742)
    c: Coincident(g742,g743)
    c: Coincident(g743,g744)
    c: Coincident(g744,g745)
    c: Coincident(g745,g746)
    c: Coincident(g746,g747)
    c: Coincident(g747,g748)
    c: Coincident(g748,g749)
    c: Coincident(g749,g750)
    c: Coincident(g750,g751)
    c: Coincident(g751,g752)
    c: Coincident(g752,g753)
    c: Coincident(g753,g754)
    c: Coincident(g754,g755)
    c: Coincident(g755,g756)
    c: Coincident(g756,g757)
    c: Coincident(g757,g758)
    c: Coincident(g758,g759)
    c: Coincident(g759,g760)
    c: Coincident(g760,g761)
    c: Coincident(g761,g762)
    c: Coincident(g762,g763)
    c: Coincident(g763,g732)
    c: Coincident(g764,g765)
    c: Coincident(g765,g766)
    c: Coincident(g766,g767)
    c: Coincident(g767,g768)
    c: Coincident(g768,g769)
    c: Coincident(g769,g770)
    c: Coincident(g770,g771)
    c: Coincident(g771,g772)
    c: Coincident(g772,g773)
    c: Coincident(g773,g774)
    c: Coincident(g774,g775)
    c: Coincident(g775,g776)
    c: Coincident(g776,g777)
    c: Coincident(g777,g778)
    c: Coincident(g778,g779)
    c: Coincident(g779,g780)
    c: Coincident(g780,g781)
    c: Coincident(g781,g782)
    c: Coincident(g782,g783)
    c: Coincident(g783,g784)
    c: Coincident(g784,g785)
    c: Coincident(g785,g786)
    c: Coincident(g786,g787)
    c: Coincident(g787,g764)
    c: Coincident(g788,g789)
    c: Coincident(g789,g790)
    c: Coincident(g790,g791)
    c: Coincident(g791,g792)
    c: Coincident(g792,g793)
    c: Coincident(g793,g794)
    c: Coincident(g794,g795)
    c: Coincident(g795,g796)
    c: Coincident(g796,g797)
    c: Coincident(g797,g798)
    c: Coincident(g798,g799)
    c: Coincident(g799,g800)
    c: Coincident(g800,g801)
    c: Coincident(g801,g802)
    c: Coincident(g802,g803)
    c: Coincident(g803,g804)
    c: Coincident(g804,g805)
    c: Coincident(g805,g806)
    c: Coincident(g806,g807)
    c: Coincident(g807,g808)
    c: Coincident(g808,g809)
    c: Coincident(g809,g810)
    c: Coincident(g810,g811)
    c: Coincident(g811,g812)
    c: Coincident(g812,g813)
    c: Coincident(g813,g814)
    c: Coincident(g814,g815)
    c: Coincident(g815,g816)
    c: Coincident(g816,g817)
    c: Coincident(g817,g818)
    c: Coincident(g818,g819)
    c: Coincident(g819,g820)
    c: Coincident(g820,g821)
    c: Coincident(g821,g822)
    c: Coincident(g822,g823)
    c: Coincident(g823,g824)
    c: Coincident(g824,g825)
    c: Coincident(g825,g826)
    c: Coincident(g826,g827)
    c: Coincident(g827,g828)
    c: Coincident(g828,g829)
    c: Coincident(g829,g830)
    c: Coincident(g830,g831)
    c: Coincident(g831,g832)
    c: Coincident(g832,g833)
    c: Coincident(g833,g834)
    c: Coincident(g834,g835)
    c: Coincident(g835,g836)
    c: Coincident(g836,g837)
    c: Coincident(g837,g838)
    c: Coincident(g838,g839)
    c: Coincident(g839,g840)
    c: Coincident(g840,g841)
    c: Coincident(g841,g842)
    c: Coincident(g842,g843)
    c: Coincident(g843,g844)
    c: Coincident(g844,g845)
    c: Coincident(g845,g846)
    c: Coincident(g846,g847)
    c: Coincident(g847,g848)
    c: Coincident(g848,g849)
    c: Coincident(g849,g850)
    c: Coincident(g850,g851)
    c: Coincident(g851,g852)
    c: Coincident(g852,g853)
    c: Coincident(g853,g854)
    c: Coincident(g854,g855)
    c: Coincident(g855,g856)
    c: Coincident(g856,g857)
    c: Coincident(g857,g858)
    c: Coincident(g858,g859)
    c: Coincident(g859,g788)
FEATURE [Sketcher::SketchObject] Sketch025  label="16 Bit VS006"
  FullyConstrained = false
  Placement = pos=(8.14,28.25,-10) rot=(1,0,0;3.14159rad)
  sketch-geometry (860):
    g0: BSplineCurve PolesCount=2 KnotsCount=2 Degree=1 IsPeriodic=0
    g1: BSplineCurve PolesCount=2 KnotsCount=2 Degree=1 IsPeriodic=0
    g2: BSplineCurve PolesCount=2 KnotsCount=2 Degree=1 IsPeriodic=0
    g3: BSplineCurve PolesCount=2 KnotsCount=2 Degree=1 IsPeriodic=0
    g4: BSplineCurve PolesCount=2 KnotsCount=2 Degree=1 IsPeriodic=0
    g5: BSplineCurve PolesCount=2 KnotsCount=2 Degree=1 IsPeriodic=0
    g6: BSplineCurve PolesCount=2 KnotsCount=2 Degree=1 IsPeriodic=0
    g7: BSplineCurve PolesCount=2 KnotsCount=2 Degree=1 IsPeriodic=0
    g8: BSplineCurve PolesCount=2 KnotsCount=2 Degree=1 IsPeriodic=0
    g9: BSplineCurve PolesCount=2 KnotsCount=2 Degree=1 IsPeriodic=0
    g10: BSplineCurve PolesCount=2 KnotsCount=2 Degree=1 IsPeriodic=0
    g11: BSplineCurve PolesCount=2 KnotsCount=2 Degree=1 IsPeriodic=0
    g12: BSplineCurve PolesCount=2 KnotsCount=2 Degree=1 IsPeriodic=0
    g13: BSplineCurve PolesCount=2 KnotsCount=2 Degree=1 IsPeriodic=0
    g14: BSplineCurve PolesCount=2 KnotsCount=2 Degree=1 IsPeriodic=0
    g15: BSplineCurve PolesCount=2 KnotsCount=2 Degree=1 IsPeriodic=0
    g16: BSplineCurve PolesCount=2 KnotsCount=2 Degree=1 IsPeriodic=0
    g17: BSplineCurve PolesCount=2 KnotsCount=2 Degree=1 IsPeriodic=0
    g18: BSplineCurve PolesCount=2 KnotsCount=2 Degree=1 IsPeriodic=0
    g19: BSplineCurve PolesCount=2 KnotsCount=2 Degree=1 IsPeriodic=0
    g20: BSplineCurve PolesCount=2 KnotsCount=2 Degree=1 IsPeriodic=0
    g21: BSplineCurve PolesCount=2 KnotsCount=2 Degree=1 IsPeriodic=0
    g22: BSplineCurve PolesCount=2 KnotsCount=2 Degree=1 IsPeriodic=0
    g23: BSplineCurve PolesCount=2 KnotsCount=2 Degree=1 IsPeriodic=0
    g24: BSplineCurve PolesCount=2 KnotsCount=2 Degree=1 IsPeriodic=0
    g25: BSplineCurve PolesCount=2 KnotsCount=2 Degree=1 IsPeriodic=0
    g26: BSplineCurve PolesCount=2 KnotsCount=2 Degree=1 IsPeriodic=0
    g27: BSplineCurve PolesCount=2 KnotsCount=2 Degree=1 IsPeriodic=0
    g28: BSplineCurve PolesCount=2 KnotsCount=2 Degree=1 IsPeriodic=0
    g29: BSplineCurve PolesCount=2 KnotsCount=2 Degree=1 IsPeriodic=0
    g30: BSplineCurve PolesCount=2 KnotsCount=2 Degree=1 IsPeriodic=0
    g31: BSplineCurve PolesCount=2 KnotsCount=2 Degree=1 IsPeriodic=0
    g32: BSplineCurve PolesCount=2 KnotsCount=2 Degree=1 IsPeriodic=0
    g33: BSplineCurve PolesCount=2 KnotsCount=2 Degree=1 IsPeriodic=0
    g34: BSplineCurve PolesCount=2 KnotsCount=2 Degree=1 IsPeriodic=0
    g35: BSplineCurve PolesCount=2 KnotsCount=2 Degree=1 IsPeriodic=0
    g36: BSplineCurve PolesCount=2 KnotsCount=2 Degree=1 IsPeriodic=0
    g37: BSplineCurve PolesCount=2 KnotsCount=2 Degree=1 IsPeriodic=0
    g38: BSplineCurve PolesCount=2 KnotsCount=2 Degree=1 IsPeriodic=0
    g39: BSplineCurve PolesCount=2 KnotsCount=2 Degree=1 IsPeriodic=0
    g40: BSplineCurve PolesCount=2 KnotsCount=2 Degree=1 IsPeriodic=0
    g41: BSplineCurve PolesCount=2 KnotsCount=2 Degree=1 IsPeriodic=0
    g42: BSplineCurve PolesCount=2 KnotsCount=2 Degree=1 IsPeriodic=0
    g43: BSplineCurve PolesCount=2 KnotsCount=2 Degree=1 IsPeriodic=0
    g44: BSplineCurve PolesCount=2 KnotsCount=2 Degree=1 IsPeriodic=0
    g45: BSplineCurve PolesCount=2 KnotsCount=2 Degree=1 IsPeriodic=0
    g46: BSplineCurve PolesCount=2 KnotsCount=2 Degree=1 IsPeriodic=0
    g47: BSplineCurve PolesCount=2 KnotsCount=2 Degree=1 IsPeriodic=0
    g48: BSplineCurve PolesCount=2 KnotsCount=2 Degree=1 IsPeriodic=0
    g49: BSplineCurve PolesCount=2 KnotsCount=2 Degree=1 IsPeriodic=0
    g50: BSplineCurve PolesCount=2 KnotsCount=2 Degree=1 IsPeriodic=0
    g51: BSplineCurve PolesCount=2 KnotsCount=2 Degree=1 IsPeriodic=0
    g52: BSplineCurve PolesCount=2 KnotsCount=2 Degree=1 IsPeriodic=0
    g53: BSplineCurve PolesCount=2 KnotsCount=2 Degree=1 IsPeriodic=0
    g54: BSplineCurve PolesCount=2 KnotsCount=2 Degree=1 IsPeriodic=0
    g55: BSplineCurve PolesCount=2 KnotsCount=2 Degree=1 IsPeriodic=0
    g56: BSplineCurve PolesCount=2 KnotsCount=2 Degree=1 IsPeriodic=0
    g57: BSplineCurve PolesCount=2 KnotsCount=2 Degree=1 IsPeriodic=0
    g58: BSplineCurve PolesCount=2 KnotsCount=2 Degree=1 IsPeriodic=0
    g59: BSplineCurve PolesCount=2 KnotsCount=2 Degree=1 IsPeriodic=0
    g60: BSplineCurve PolesCount=2 KnotsCount=2 Degree=1 IsPeriodic=0
    g61: BSplineCurve PolesCount=2 KnotsCount=2 Degree=1 IsPeriodic=0
    g62: BSplineCurve PolesCount=2 KnotsCount=2 Degree=1 IsPeriodic=0
    g63: BSplineCurve PolesCount=2 KnotsCount=2 Degree=1 IsPeriodic=0
    g64: BSplineCurve PolesCount=2 KnotsCount=2 Degree=1 IsPeriodic=0
    g65: BSplineCurve PolesCount=2 KnotsCount=2 Degree=1 IsPeriodic=0
    g66: BSplineCurve PolesCount=2 KnotsCount=2 Degree=1 IsPeriodic=0
    g67: BSplineCurve PolesCount=2 KnotsCount=2 Degree=1 IsPeriodic=0
    g68: BSplineCurve PolesCount=2 KnotsCount=2 Degree=1 IsPeriodic=0
    g69: BSplineCurve PolesCount=2 KnotsCount=2 Degree=1 IsPeriodic=0
    g70: BSplineCurve PolesCount=2 KnotsCount=2 Degree=1 IsPeriodic=0
    g71: BSplineCurve PolesCount=2 KnotsCount=2 Degree=1 IsPeriodic=0
    g72: BSplineCurve PolesCount=2 KnotsCount=2 Degree=1 IsPeriodic=0
    g73: BSplineCurve PolesCount=2 KnotsCount=2 Degree=1 IsPeriodic=0
    g74: BSplineCurve PolesCount=2 KnotsCount=2 Degree=1 IsPeriodic=0
    g75: BSplineCurve PolesCount=2 KnotsCount=2 Degree=1 IsPeriodic=0
    g76: BSplineCurve PolesCount=2 KnotsCount=2 Degree=1 IsPeriodic=0
    g77: BSplineCurve PolesCount=2 KnotsCount=2 Degree=1 IsPeriodic=0
    g78: BSplineCurve PolesCount=2 KnotsCount=2 Degree=1 IsPeriodic=0
    g79: BSplineCurve PolesCount=2 KnotsCount=2 Degree=1 IsPeriodic=0
    g80: BSplineCurve PolesCount=2 KnotsCount=2 Degree=1 IsPeriodic=0
    g81: BSplineCurve PolesCount=2 KnotsCount=2 Degree=1 IsPeriodic=0
    g82: BSplineCurve PolesCount=2 KnotsCount=2 Degree=1 IsPeriodic=0
    g83: BSplineCurve PolesCount=2 KnotsCount=2 Degree=1 IsPeriodic=0
    g84: BSplineCurve PolesCount=2 KnotsCount=2 Degree=1 IsPeriodic=0
    g85: BSplineCurve PolesCount=2 KnotsCount=2 Degree=1 IsPeriodic=0
    g86: BSplineCurve PolesCount=2 KnotsCount=2 Degree=1 IsPeriodic=0
    g87: BSplineCurve PolesCount=2 KnotsCount=2 Degree=1 IsPeriodic=0
    g88: BSplineCurve PolesCount=2 KnotsCount=2 Degree=1 IsPeriodic=0
    g89: BSplineCurve PolesCount=2 KnotsCount=2 Degree=1 IsPeriodic=0
    g90: BSplineCurve PolesCount=2 KnotsCount=2 Degree=1 IsPeriodic=0
    g91: BSplineCurve PolesCount=2 KnotsCount=2 Degree=1 IsPeriodic=0
    g92: BSplineCurve PolesCount=2 KnotsCount=2 Degree=1 IsPeriodic=0
    g93: BSplineCurve PolesCount=2 KnotsCount=2 Degree=1 IsPeriodic=0
    g94: BSplineCurve PolesCount=2 KnotsCount=2 Degree=1 IsPeriodic=0
    g95: BSplineCurve PolesCount=2 KnotsCount=2 Degree=1 IsPeriodic=0
    g96: BSplineCurve PolesCount=2 KnotsCount=2 Degree=1 IsPeriodic=0
    g97: BSplineCurve PolesCount=2 KnotsCount=2 Degree=1 IsPeriodic=0
    g98: BSplineCurve PolesCount=2 KnotsCount=2 Degree=1 IsPeriodic=0
    g99: BSplineCurve PolesCount=2 KnotsCount=2 Degree=1 IsPeriodic=0
    g100: BSplineCurve PolesCount=2 KnotsCount=2 Degree=1 IsPeriodic=0
    g101: BSplineCurve PolesCount=2 KnotsCount=2 Degree=1 IsPeriodic=0
    g102: BSplineCurve PolesCount=2 KnotsCount=2 Degree=1 IsPeriodic=0
    g103: BSplineCurve PolesCount=2 KnotsCount=2 Degree=1 IsPeriodic=0
    g104: BSplineCurve PolesCount=2 KnotsCount=2 Degree=1 IsPeriodic=0
    g105: BSplineCurve PolesCount=2 KnotsCount=2 Degree=1 IsPeriodic=0
    g106: BSplineCurve PolesCount=2 KnotsCount=2 Degree=1 IsPeriodic=0
    g107: BSplineCurve PolesCount=2 KnotsCount=2 Degree=1 IsPeriodic=0
    g108: BSplineCurve PolesCount=2 KnotsCount=2 Degree=1 IsPeriodic=0
    g109: BSplineCurve PolesCount=2 KnotsCount=2 Degree=1 IsPeriodic=0
    g110: BSplineCurve PolesCount=2 KnotsCount=2 Degree=1 IsPeriodic=0
    g111: BSplineCurve PolesCount=2 KnotsCount=2 Degree=1 IsPeriodic=0
    g112: BSplineCurve PolesCount=2 KnotsCount=2 Degree=1 IsPeriodic=0
    g113: BSplineCurve PolesCount=2 KnotsCount=2 Degree=1 IsPeriodic=0
    g114: BSplineCurve PolesCount=2 KnotsCount=2 Degree=1 IsPeriodic=0
    g115: BSplineCurve PolesCount=2 KnotsCount=2 Degree=1 IsPeriodic=0
    g116: BSplineCurve PolesCount=2 KnotsCount=2 Degree=1 IsPeriodic=0
    g117: BSplineCurve PolesCount=2 KnotsCount=2 Degree=1 IsPeriodic=0
    g118: BSplineCurve PolesCount=2 KnotsCount=2 Degree=1 IsPeriodic=0
    g119: BSplineCurve PolesCount=2 KnotsCount=2 Degree=1 IsPeriodic=0
    g120: BSplineCurve PolesCount=2 KnotsCount=2 Degree=1 IsPeriodic=0
    g121: BSplineCurve PolesCount=2 KnotsCount=2 Degree=1 IsPeriodic=0
    g122: BSplineCurve PolesCount=2 KnotsCount=2 Degree=1 IsPeriodic=0
    g123: BSplineCurve PolesCount=2 KnotsCount=2 Degree=1 IsPeriodic=0
    g124: BSplineCurve PolesCount=2 KnotsCount=2 Degree=1 IsPeriodic=0
    g125: BSplineCurve PolesCount=2 KnotsCount=2 Degree=1 IsPeriodic=0
    g126: BSplineCurve PolesCount=2 KnotsCount=2 Degree=1 IsPeriodic=0
    g127: BSplineCurve PolesCount=2 KnotsCount=2 Degree=1 IsPeriodic=0
    g128: BSplineCurve PolesCount=2 KnotsCount=2 Degree=1 IsPeriodic=0
    g129: BSplineCurve PolesCount=2 KnotsCount=2 Degree=1 IsPeriodic=0
    g130: BSplineCurve PolesCount=2 KnotsCount=2 Degree=1 IsPeriodic=0
    g131: BSplineCurve PolesCount=2 KnotsCount=2 Degree=1 IsPeriodic=0
    g132: BSplineCurve PolesCount=2 KnotsCount=2 Degree=1 IsPeriodic=0
    g133: BSplineCurve PolesCount=2 KnotsCount=2 Degree=1 IsPeriodic=0
    g134: BSplineCurve PolesCount=2 KnotsCount=2 Degree=1 IsPeriodic=0
    g135: BSplineCurve PolesCount=2 KnotsCount=2 Degree=1 IsPeriodic=0
    g136: BSplineCurve PolesCount=2 KnotsCount=2 Degree=1 IsPeriodic=0
    g137: BSplineCurve PolesCount=2 KnotsCount=2 Degree=1 IsPeriodic=0
    g138: BSplineCurve PolesCount=2 KnotsCount=2 Degree=1 IsPeriodic=0
    g139: BSplineCurve PolesCount=2 KnotsCount=2 Degree=1 IsPeriodic=0
    g140: BSplineCurve PolesCount=2 KnotsCount=2 Degree=1 IsPeriodic=0
    g141: BSplineCurve PolesCount=2 KnotsCount=2 Degree=1 IsPeriodic=0
    g142: BSplineCurve PolesCount=2 KnotsCount=2 Degree=1 IsPeriodic=0
    g143: BSplineCurve PolesCount=2 KnotsCount=2 Degree=1 IsPeriodic=0
    g144: BSplineCurve PolesCount=2 KnotsCount=2 Degree=1 IsPeriodic=0
    g145: BSplineCurve PolesCount=2 KnotsCount=2 Degree=1 IsPeriodic=0
    g146: BSplineCurve PolesCount=2 KnotsCount=2 Degree=1 IsPeriodic=0
    g147: BSplineCurve PolesCount=2 KnotsCount=2 Degree=1 IsPeriodic=0
    g148: BSplineCurve PolesCount=2 KnotsCount=2 Degree=1 IsPeriodic=0
    g149: BSplineCurve PolesCount=2 KnotsCount=2 Degree=1 IsPeriodic=0
    g150: BSplineCurve PolesCount=2 KnotsCount=2 Degree=1 IsPeriodic=0
    g151: BSplineCurve PolesCount=2 KnotsCount=2 Degree=1 IsPeriodic=0
    g152: BSplineCurve PolesCount=2 KnotsCount=2 Degree=1 IsPeriodic=0
    g153: BSplineCurve PolesCount=2 KnotsCount=2 Degree=1 IsPeriodic=0
    g154: BSplineCurve PolesCount=2 KnotsCount=2 Degree=1 IsPeriodic=0
    g155: BSplineCurve PolesCount=2 KnotsCount=2 Degree=1 IsPeriodic=0
    g156: BSplineCurve PolesCount=2 KnotsCount=2 Degree=1 IsPeriodic=0
    g157: BSplineCurve PolesCount=2 KnotsCount=2 Degree=1 IsPeriodic=0
    g158: BSplineCurve PolesCount=2 KnotsCount=2 Degree=1 IsPeriodic=0
    g159: BSplineCurve PolesCount=2 KnotsCount=2 Degree=1 IsPeriodic=0
    g160: BSplineCurve PolesCount=2 KnotsCount=2 Degree=1 IsPeriodic=0
    g161: BSplineCurve PolesCount=2 KnotsCount=2 Degree=1 IsPeriodic=0
    g162: BSplineCurve PolesCount=2 KnotsCount=2 Degree=1 IsPeriodic=0
    g163: BSplineCurve PolesCount=2 KnotsCount=2 Degree=1 IsPeriodic=0
    g164: BSplineCurve PolesCount=2 KnotsCount=2 Degree=1 IsPeriodic=0
    g165: BSplineCurve PolesCount=2 KnotsCount=2 Degree=1 IsPeriodic=0
    g166: BSplineCurve PolesCount=2 KnotsCount=2 Degree=1 IsPeriodic=0
    g167: BSplineCurve PolesCount=2 KnotsCount=2 Degree=1 IsPeriodic=0
    g168: BSplineCurve PolesCount=2 KnotsCount=2 Degree=1 IsPeriodic=0
    g169: BSplineCurve PolesCount=2 KnotsCount=2 Degree=1 IsPeriodic=0
    g170: BSplineCurve PolesCount=2 KnotsCount=2 Degree=1 IsPeriodic=0
    g171: BSplineCurve PolesCount=2 KnotsCount=2 Degree=1 IsPeriodic=0
    g172: BSplineCurve PolesCount=2 KnotsCount=2 Degree=1 IsPeriodic=0
    g173: BSplineCurve PolesCount=2 KnotsCount=2 Degree=1 IsPeriodic=0
    g174: BSplineCurve PolesCount=2 KnotsCount=2 Degree=1 IsPeriodic=0
    g175: BSplineCurve PolesCount=2 KnotsCount=2 Degree=1 IsPeriodic=0
    g176: BSplineCurve PolesCount=2 KnotsCount=2 Degree=1 IsPeriodic=0
    g177: BSplineCurve PolesCount=2 KnotsCount=2 Degree=1 IsPeriodic=0
    g178: BSplineCurve PolesCount=2 KnotsCount=2 Degree=1 IsPeriodic=0
    g179: BSplineCurve PolesCount=2 KnotsCount=2 Degree=1 IsPeriodic=0
    g180: BSplineCurve PolesCount=2 KnotsCount=2 Degree=1 IsPeriodic=0
    g181: BSplineCurve PolesCount=2 KnotsCount=2 Degree=1 IsPeriodic=0
    g182: BSplineCurve PolesCount=2 KnotsCount=2 Degree=1 IsPeriodic=0
    g183: BSplineCurve PolesCount=2 KnotsCount=2 Degree=1 IsPeriodic=0
    g184: BSplineCurve PolesCount=2 KnotsCount=2 Degree=1 IsPeriodic=0
    g185: BSplineCurve PolesCount=2 KnotsCount=2 Degree=1 IsPeriodic=0
    g186: BSplineCurve PolesCount=2 KnotsCount=2 Degree=1 IsPeriodic=0
    g187: BSplineCurve PolesCount=2 KnotsCount=2 Degree=1 IsPeriodic=0
    g188: BSplineCurve PolesCount=2 KnotsCount=2 Degree=1 IsPeriodic=0
    g189: BSplineCurve PolesCount=2 KnotsCount=2 Degree=1 IsPeriodic=0
    g190: BSplineCurve PolesCount=2 KnotsCount=2 Degree=1 IsPeriodic=0
    g191: BSplineCurve PolesCount=2 KnotsCount=2 Degree=1 IsPeriodic=0
    g192: BSplineCurve PolesCount=2 KnotsCount=2 Degree=1 IsPeriodic=0
    g193: BSplineCurve PolesCount=2 KnotsCount=2 Degree=1 IsPeriodic=0
    g194: BSplineCurve PolesCount=2 KnotsCount=2 Degree=1 IsPeriodic=0
    g195: BSplineCurve PolesCount=2 KnotsCount=2 Degree=1 IsPeriodic=0
    g196: BSplineCurve PolesCount=2 KnotsCount=2 Degree=1 IsPeriodic=0
    g197: BSplineCurve PolesCount=2 KnotsCount=2 Degree=1 IsPeriodic=0
    g198: BSplineCurve PolesCount=2 KnotsCount=2 Degree=1 IsPeriodic=0
    g199: BSplineCurve PolesCount=2 KnotsCount=2 Degree=1 IsPeriodic=0
    g200: BSplineCurve PolesCount=2 KnotsCount=2 Degree=1 IsPeriodic=0
    g201: BSplineCurve PolesCount=2 KnotsCount=2 Degree=1 IsPeriodic=0
    g202: BSplineCurve PolesCount=2 KnotsCount=2 Degree=1 IsPeriodic=0
    g203: BSplineCurve PolesCount=2 KnotsCount=2 Degree=1 IsPeriodic=0
    g204: BSplineCurve PolesCount=2 KnotsCount=2 Degree=1 IsPeriodic=0
    g205: BSplineCurve PolesCount=2 KnotsCount=2 Degree=1 IsPeriodic=0
    g206: BSplineCurve PolesCount=2 KnotsCount=2 Degree=1 IsPeriodic=0
    g207: BSplineCurve PolesCount=2 KnotsCount=2 Degree=1 IsPeriodic=0
    g208: BSplineCurve PolesCount=2 KnotsCount=2 Degree=1 IsPeriodic=0
    g209: BSplineCurve PolesCount=2 KnotsCount=2 Degree=1 IsPeriodic=0
    g210: BSplineCurve PolesCount=2 KnotsCount=2 Degree=1 IsPeriodic=0
    g211: BSplineCurve PolesCount=2 KnotsCount=2 Degree=1 IsPeriodic=0
    g212: BSplineCurve PolesCount=2 KnotsCount=2 Degree=1 IsPeriodic=0
    g213: BSplineCurve PolesCount=2 KnotsCount=2 Degree=1 IsPeriodic=0
    g214: BSplineCurve PolesCount=2 KnotsCount=2 Degree=1 IsPeriodic=0
    g215: BSplineCurve PolesCount=2 KnotsCount=2 Degree=1 IsPeriodic=0
    g216: BSplineCurve PolesCount=2 KnotsCount=2 Degree=1 IsPeriodic=0
    g217: BSplineCurve PolesCount=2 KnotsCount=2 Degree=1 IsPeriodic=0
    g218: BSplineCurve PolesCount=2 KnotsCount=2 Degree=1 IsPeriodic=0
    g219: BSplineCurve PolesCount=2 KnotsCount=2 Degree=1 IsPeriodic=0
    g220: BSplineCurve PolesCount=2 KnotsCount=2 Degree=1 IsPeriodic=0
    g221: BSplineCurve PolesCount=2 KnotsCount=2 Degree=1 IsPeriodic=0
    g222: BSplineCurve PolesCount=2 KnotsCount=2 Degree=1 IsPeriodic=0
    g223: BSplineCurve PolesCount=2 KnotsCount=2 Degree=1 IsPeriodic=0
    g224: BSplineCurve PolesCount=2 KnotsCount=2 Degree=1 IsPeriodic=0
    g225: BSplineCurve PolesCount=2 KnotsCount=2 Degree=1 IsPeriodic=0
    g226: BSplineCurve PolesCount=2 KnotsCount=2 Degree=1 IsPeriodic=0
    g227: BSplineCurve PolesCount=2 KnotsCount=2 Degree=1 IsPeriodic=0
    g228: BSplineCurve PolesCount=2 KnotsCount=2 Degree=1 IsPeriodic=0
    g229: BSplineCurve PolesCount=2 KnotsCount=2 Degree=1 IsPeriodic=0
    g230: BSplineCurve PolesCount=2 KnotsCount=2 Degree=1 IsPeriodic=0
    g231: BSplineCurve PolesCount=2 KnotsCount=2 Degree=1 IsPeriodic=0
    g232: BSplineCurve PolesCount=2 KnotsCount=2 Degree=1 IsPeriodic=0
    g233: BSplineCurve PolesCount=2 KnotsCount=2 Degree=1 IsPeriodic=0
    g234: BSplineCurve PolesCount=2 KnotsCount=2 Degree=1 IsPeriodic=0
    g235: BSplineCurve PolesCount=2 KnotsCount=2 Degree=1 IsPeriodic=0
    g236: BSplineCurve PolesCount=2 KnotsCount=2 Degree=1 IsPeriodic=0
    g237: BSplineCurve PolesCount=2 KnotsCount=2 Degree=1 IsPeriodic=0
    g238: BSplineCurve PolesCount=2 KnotsCount=2 Degree=1 IsPeriodic=0
    g239: BSplineCurve PolesCount=2 KnotsCount=2 Degree=1 IsPeriodic=0
    g240: BSplineCurve PolesCount=2 KnotsCount=2 Degree=1 IsPeriodic=0
    g241: BSplineCurve PolesCount=2 KnotsCount=2 Degree=1 IsPeriodic=0
    g242: BSplineCurve PolesCount=2 KnotsCount=2 Degree=1 IsPeriodic=0
    g243: BSplineCurve PolesCount=2 KnotsCount=2 Degree=1 IsPeriodic=0
    g244: BSplineCurve PolesCount=2 KnotsCount=2 Degree=1 IsPeriodic=0
    g245: BSplineCurve PolesCount=2 KnotsCount=2 Degree=1 IsPeriodic=0
    g246: BSplineCurve PolesCount=2 KnotsCount=2 Degree=1 IsPeriodic=0
    g247: BSplineCurve PolesCount=2 KnotsCount=2 Degree=1 IsPeriodic=0
    g248: BSplineCurve PolesCount=2 KnotsCount=2 Degree=1 IsPeriodic=0
    g249: BSplineCurve PolesCount=2 KnotsCount=2 Degree=1 IsPeriodic=0
    g250: BSplineCurve PolesCount=2 KnotsCount=2 Degree=1 IsPeriodic=0
    g251: BSplineCurve PolesCount=2 KnotsCount=2 Degree=1 IsPeriodic=0
    g252: BSplineCurve PolesCount=2 KnotsCount=2 Degree=1 IsPeriodic=0
    g253: BSplineCurve PolesCount=2 KnotsCount=2 Degree=1 IsPeriodic=0
    g254: BSplineCurve PolesCount=2 KnotsCount=2 Degree=1 IsPeriodic=0
    g255: BSplineCurve PolesCount=2 KnotsCount=2 Degree=1 IsPeriodic=0
    g256: BSplineCurve PolesCount=2 KnotsCount=2 Degree=1 IsPeriodic=0
    g257: BSplineCurve PolesCount=2 KnotsCount=2 Degree=1 IsPeriodic=0
    g258: BSplineCurve PolesCount=2 KnotsCount=2 Degree=1 IsPeriodic=0
    g259: BSplineCurve PolesCount=2 KnotsCount=2 Degree=1 IsPeriodic=0
    g260: BSplineCurve PolesCount=2 KnotsCount=2 Degree=1 IsPeriodic=0
    g261: BSplineCurve PolesCount=2 KnotsCount=2 Degree=1 IsPeriodic=0
    g262: BSplineCurve PolesCount=2 KnotsCount=2 Degree=1 IsPeriodic=0
    g263: BSplineCurve PolesCount=2 KnotsCount=2 Degree=1 IsPeriodic=0
    g264: BSplineCurve PolesCount=2 KnotsCount=2 Degree=1 IsPeriodic=0
    g265: BSplineCurve PolesCount=2 KnotsCount=2 Degree=1 IsPeriodic=0
    g266: BSplineCurve PolesCount=2 KnotsCount=2 Degree=1 IsPeriodic=0
    g267: BSplineCurve PolesCount=2 KnotsCount=2 Degree=1 IsPeriodic=0
    g268: BSplineCurve PolesCount=2 KnotsCount=2 Degree=1 IsPeriodic=0
    g269: BSplineCurve PolesCount=2 KnotsCount=2 Degree=1 IsPeriodic=0
    g270: BSplineCurve PolesCount=2 KnotsCount=2 Degree=1 IsPeriodic=0
    g271: BSplineCurve PolesCount=2 KnotsCount=2 Degree=1 IsPeriodic=0
    g272: BSplineCurve PolesCount=2 KnotsCount=2 Degree=1 IsPeriodic=0
    g273: BSplineCurve PolesCount=2 KnotsCount=2 Degree=1 IsPeriodic=0
    g274: BSplineCurve PolesCount=2 KnotsCount=2 Degree=1 IsPeriodic=0
    g275: BSplineCurve PolesCount=2 KnotsCount=2 Degree=1 IsPeriodic=0
    g276: BSplineCurve PolesCount=2 KnotsCount=2 Degree=1 IsPeriodic=0
    g277: BSplineCurve PolesCount=2 KnotsCount=2 Degree=1 IsPeriodic=0
    g278: BSplineCurve PolesCount=2 KnotsCount=2 Degree=1 IsPeriodic=0
    g279: BSplineCurve PolesCount=2 KnotsCount=2 Degree=1 IsPeriodic=0
    g280: BSplineCurve PolesCount=2 KnotsCount=2 Degree=1 IsPeriodic=0
    g281: BSplineCurve PolesCount=2 KnotsCount=2 Degree=1 IsPeriodic=0
    g282: BSplineCurve PolesCount=2 KnotsCount=2 Degree=1 IsPeriodic=0
    g283: BSplineCurve PolesCount=2 KnotsCount=2 Degree=1 IsPeriodic=0
    g284: BSplineCurve PolesCount=2 KnotsCount=2 Degree=1 IsPeriodic=0
    g285: BSplineCurve PolesCount=2 KnotsCount=2 Degree=1 IsPeriodic=0
    g286: BSplineCurve PolesCount=2 KnotsCount=2 Degree=1 IsPeriodic=0
    g287: BSplineCurve PolesCount=2 KnotsCount=2 Degree=1 IsPeriodic=0
    g288: BSplineCurve PolesCount=2 KnotsCount=2 Degree=1 IsPeriodic=0
    g289: BSplineCurve PolesCount=2 KnotsCount=2 Degree=1 IsPeriodic=0
    g290: BSplineCurve PolesCount=2 KnotsCount=2 Degree=1 IsPeriodic=0
    g291: BSplineCurve PolesCount=2 KnotsCount=2 Degree=1 IsPeriodic=0
    g292: BSplineCurve PolesCount=2 KnotsCount=2 Degree=1 IsPeriodic=0
    g293: BSplineCurve PolesCount=2 KnotsCount=2 Degree=1 IsPeriodic=0
    g294: BSplineCurve PolesCount=2 KnotsCount=2 Degree=1 IsPeriodic=0
    g295: BSplineCurve PolesCount=2 KnotsCount=2 Degree=1 IsPeriodic=0
    g296: BSplineCurve PolesCount=2 KnotsCount=2 Degree=1 IsPeriodic=0
    g297: BSplineCurve PolesCount=2 KnotsCount=2 Degree=1 IsPeriodic=0
    g298: BSplineCurve PolesCount=2 KnotsCount=2 Degree=1 IsPeriodic=0
    g299: BSplineCurve PolesCount=2 KnotsCount=2 Degree=1 IsPeriodic=0
    g300: BSplineCurve PolesCount=2 KnotsCount=2 Degree=1 IsPeriodic=0
    g301: BSplineCurve PolesCount=2 KnotsCount=2 Degree=1 IsPeriodic=0
    g302: BSplineCurve PolesCount=2 KnotsCount=2 Degree=1 IsPeriodic=0
    g303: BSplineCurve PolesCount=2 KnotsCount=2 Degree=1 IsPeriodic=0
    g304: BSplineCurve PolesCount=2 KnotsCount=2 Degree=1 IsPeriodic=0
    g305: BSplineCurve PolesCount=2 KnotsCount=2 Degree=1 IsPeriodic=0
    g306: BSplineCurve PolesCount=2 KnotsCount=2 Degree=1 IsPeriodic=0
    g307: BSplineCurve PolesCount=2 KnotsCount=2 Degree=1 IsPeriodic=0
    g308: BSplineCurve PolesCount=2 KnotsCount=2 Degree=1 IsPeriodic=0
    g309: BSplineCurve PolesCount=2 KnotsCount=2 Degree=1 IsPeriodic=0
    g310: BSplineCurve PolesCount=2 KnotsCount=2 Degree=1 IsPeriodic=0
    g311: BSplineCurve PolesCount=2 KnotsCount=2 Degree=1 IsPeriodic=0
    g312: BSplineCurve PolesCount=2 KnotsCount=2 Degree=1 IsPeriodic=0
    g313: BSplineCurve PolesCount=2 KnotsCount=2 Degree=1 IsPeriodic=0
    g314: BSplineCurve PolesCount=2 KnotsCount=2 Degree=1 IsPeriodic=0
    g315: BSplineCurve PolesCount=2 KnotsCount=2 Degree=1 IsPeriodic=0
    g316: BSplineCurve PolesCount=2 KnotsCount=2 Degree=1 IsPeriodic=0
    g317: BSplineCurve PolesCount=2 KnotsCount=2 Degree=1 IsPeriodic=0
    g318: BSplineCurve PolesCount=2 KnotsCount=2 Degree=1 IsPeriodic=0
    g319: BSplineCurve PolesCount=2 KnotsCount=2 Degree=1 IsPeriodic=0
    g320: BSplineCurve PolesCount=2 KnotsCount=2 Degree=1 IsPeriodic=0
    g321: BSplineCurve PolesCount=2 KnotsCount=2 Degree=1 IsPeriodic=0
    g322: BSplineCurve PolesCount=2 KnotsCount=2 Degree=1 IsPeriodic=0
    g323: BSplineCurve PolesCount=2 KnotsCount=2 Degree=1 IsPeriodic=0
    g324: BSplineCurve PolesCount=2 KnotsCount=2 Degree=1 IsPeriodic=0
    g325: BSplineCurve PolesCount=2 KnotsCount=2 Degree=1 IsPeriodic=0
    g326: BSplineCurve PolesCount=2 KnotsCount=2 Degree=1 IsPeriodic=0
    g327: BSplineCurve PolesCount=2 KnotsCount=2 Degree=1 IsPeriodic=0
    g328: BSplineCurve PolesCount=2 KnotsCount=2 Degree=1 IsPeriodic=0
    g329: BSplineCurve PolesCount=2 KnotsCount=2 Degree=1 IsPeriodic=0
    g330: BSplineCurve PolesCount=2 KnotsCount=2 Degree=1 IsPeriodic=0
    g331: BSplineCurve PolesCount=2 KnotsCount=2 Degree=1 IsPeriodic=0
    g332: BSplineCurve PolesCount=2 KnotsCount=2 Degree=1 IsPeriodic=0
    g333: BSplineCurve PolesCount=2 KnotsCount=2 Degree=1 IsPeriodic=0
    g334: BSplineCurve PolesCount=2 KnotsCount=2 Degree=1 IsPeriodic=0
    g335: BSplineCurve PolesCount=2 KnotsCount=2 Degree=1 IsPeriodic=0
    g336: BSplineCurve PolesCount=2 KnotsCount=2 Degree=1 IsPeriodic=0
    g337: BSplineCurve PolesCount=2 KnotsCount=2 Degree=1 IsPeriodic=0
    g338: BSplineCurve PolesCount=2 KnotsCount=2 Degree=1 IsPeriodic=0
    g339: BSplineCurve PolesCount=2 KnotsCount=2 Degree=1 IsPeriodic=0
    g340: BSplineCurve PolesCount=2 KnotsCount=2 Degree=1 IsPeriodic=0
    g341: BSplineCurve PolesCount=2 KnotsCount=2 Degree=1 IsPeriodic=0
    g342: BSplineCurve PolesCount=2 KnotsCount=2 Degree=1 IsPeriodic=0
    g343: BSplineCurve PolesCount=2 KnotsCount=2 Degree=1 IsPeriodic=0
    g344: BSplineCurve PolesCount=2 KnotsCount=2 Degree=1 IsPeriodic=0
    g345: BSplineCurve PolesCount=2 KnotsCount=2 Degree=1 IsPeriodic=0
    g346: BSplineCurve PolesCount=2 KnotsCount=2 Degree=1 IsPeriodic=0
    g347: BSplineCurve PolesCount=2 KnotsCount=2 Degree=1 IsPeriodic=0
    g348: BSplineCurve PolesCount=2 KnotsCount=2 Degree=1 IsPeriodic=0
    g349: BSplineCurve PolesCount=2 KnotsCount=2 Degree=1 IsPeriodic=0
    g350: BSplineCurve PolesCount=2 KnotsCount=2 Degree=1 IsPeriodic=0
    g351: BSplineCurve PolesCount=2 KnotsCount=2 Degree=1 IsPeriodic=0
    g352: BSplineCurve PolesCount=2 KnotsCount=2 Degree=1 IsPeriodic=0
    g353: BSplineCurve PolesCount=2 KnotsCount=2 Degree=1 IsPeriodic=0
    g354: BSplineCurve PolesCount=2 KnotsCount=2 Degree=1 IsPeriodic=0
    g355: BSplineCurve PolesCount=2 KnotsCount=2 Degree=1 IsPeriodic=0
    g356: BSplineCurve PolesCount=2 KnotsCount=2 Degree=1 IsPeriodic=0
    g357: BSplineCurve PolesCount=2 KnotsCount=2 Degree=1 IsPeriodic=0
    g358: BSplineCurve PolesCount=2 KnotsCount=2 Degree=1 IsPeriodic=0
    g359: BSplineCurve PolesCount=2 KnotsCount=2 Degree=1 IsPeriodic=0
    g360: BSplineCurve PolesCount=2 KnotsCount=2 Degree=1 IsPeriodic=0
    g361: BSplineCurve PolesCount=2 KnotsCount=2 Degree=1 IsPeriodic=0
    g362: BSplineCurve PolesCount=2 KnotsCount=2 Degree=1 IsPeriodic=0
    g363: BSplineCurve PolesCount=2 KnotsCount=2 Degree=1 IsPeriodic=0
    g364: BSplineCurve PolesCount=2 KnotsCount=2 Degree=1 IsPeriodic=0
    g365: BSplineCurve PolesCount=2 KnotsCount=2 Degree=1 IsPeriodic=0
    g366: BSplineCurve PolesCount=2 KnotsCount=2 Degree=1 IsPeriodic=0
    g367: BSplineCurve PolesCount=2 KnotsCount=2 Degree=1 IsPeriodic=0
    g368: BSplineCurve PolesCount=2 KnotsCount=2 Degree=1 IsPeriodic=0
    g369: BSplineCurve PolesCount=2 KnotsCount=2 Degree=1 IsPeriodic=0
    g370: BSplineCurve PolesCount=2 KnotsCount=2 Degree=1 IsPeriodic=0
    g371: BSplineCurve PolesCount=2 KnotsCount=2 Degree=1 IsPeriodic=0
    g372: BSplineCurve PolesCount=2 KnotsCount=2 Degree=1 IsPeriodic=0
    g373: BSplineCurve PolesCount=2 KnotsCount=2 Degree=1 IsPeriodic=0
    g374: BSplineCurve PolesCount=2 KnotsCount=2 Degree=1 IsPeriodic=0
    g375: BSplineCurve PolesCount=2 KnotsCount=2 Degree=1 IsPeriodic=0
    g376: BSplineCurve PolesCount=2 KnotsCount=2 Degree=1 IsPeriodic=0
    g377: BSplineCurve PolesCount=2 KnotsCount=2 Degree=1 IsPeriodic=0
    g378: BSplineCurve PolesCount=2 KnotsCount=2 Degree=1 IsPeriodic=0
    g379: BSplineCurve PolesCount=2 KnotsCount=2 Degree=1 IsPeriodic=0
    g380: BSplineCurve PolesCount=2 KnotsCount=2 Degree=1 IsPeriodic=0
    g381: BSplineCurve PolesCount=2 KnotsCount=2 Degree=1 IsPeriodic=0
    g382: BSplineCurve PolesCount=2 KnotsCount=2 Degree=1 IsPeriodic=0
    g383: BSplineCurve PolesCount=2 KnotsCount=2 Degree=1 IsPeriodic=0
    g384: BSplineCurve PolesCount=2 KnotsCount=2 Degree=1 IsPeriodic=0
    g385: BSplineCurve PolesCount=2 KnotsCount=2 Degree=1 IsPeriodic=0
    g386: BSplineCurve PolesCount=2 KnotsCount=2 Degree=1 IsPeriodic=0
    g387: BSplineCurve PolesCount=2 KnotsCount=2 Degree=1 IsPeriodic=0
    g388: BSplineCurve PolesCount=2 KnotsCount=2 Degree=1 IsPeriodic=0
    g389: BSplineCurve PolesCount=2 KnotsCount=2 Degree=1 IsPeriodic=0
    g390: BSplineCurve PolesCount=2 KnotsCount=2 Degree=1 IsPeriodic=0
    g391: BSplineCurve PolesCount=2 KnotsCount=2 Degree=1 IsPeriodic=0
    g392: BSplineCurve PolesCount=2 KnotsCount=2 Degree=1 IsPeriodic=0
    g393: BSplineCurve PolesCount=2 KnotsCount=2 Degree=1 IsPeriodic=0
    g394: BSplineCurve PolesCount=2 KnotsCount=2 Degree=1 IsPeriodic=0
    g395: BSplineCurve PolesCount=2 KnotsCount=2 Degree=1 IsPeriodic=0
    g396: BSplineCurve PolesCount=2 KnotsCount=2 Degree=1 IsPeriodic=0
    g397: BSplineCurve PolesCount=2 KnotsCount=2 Degree=1 IsPeriodic=0
    g398: BSplineCurve PolesCount=2 KnotsCount=2 Degree=1 IsPeriodic=0
    g399: BSplineCurve PolesCount=2 KnotsCount=2 Degree=1 IsPeriodic=0
    ... +460 more geometry lines
  constraints (860):
    c: Coincident(g0,g1)
    c: Coincident(g1,g2)
    c: Coincident(g2,g3)
    c: Coincident(g3,g4)
    c: Coincident(g4,g5)
    c: Coincident(g5,g6)
    c: Coincident(g6,g7)
    c: Coincident(g7,g8)
    c: Coincident(g8,g9)
    c: Coincident(g9,g10)
    c: Coincident(g10,g11)
    c: Coincident(g11,g12)
    c: Coincident(g12,g13)
    c: Coincident(g13,g14)
    c: Coincident(g14,g15)
    c: Coincident(g15,g16)
    c: Coincident(g16,g17)
    c: Coincident(g17,g18)
    c: Coincident(g18,g19)
    c: Coincident(g19,g20)
    c: Coincident(g20,g21)
    c: Coincident(g21,g22)
    c: Coincident(g22,g23)
    c: Coincident(g23,g24)
    c: Coincident(g24,g25)
    c: Coincident(g25,g26)
    c: Coincident(g26,g27)
    c: Coincident(g27,g28)
    c: Coincident(g28,g29)
    c: Coincident(g29,g30)
    c: Coincident(g30,g31)
    c: Coincident(g31,g32)
    c: Coincident(g32,g33)
    c: Coincident(g33,g34)
    c: Coincident(g34,g35)
    c: Coincident(g35,g36)
    c: Coincident(g36,g37)
    c: Coincident(g37,g38)
    c: Coincident(g38,g39)
    c: Coincident(g39,g40)
    c: Coincident(g40,g41)
    c: Coincident(g41,g42)
    c: Coincident(g42,g43)
    c: Coincident(g43,g44)
    c: Coincident(g44,g45)
    c: Coincident(g45,g46)
    c: Coincident(g46,g47)
    c: Coincident(g47,g48)
    c: Coincident(g48,g49)
    c: Coincident(g49,g50)
    c: Coincident(g50,g51)
    c: Coincident(g51,g52)
    c: Coincident(g52,g53)
    c: Coincident(g53,g54)
    c: Coincident(g54,g55)
    c: Coincident(g55,g56)
    c: Coincident(g56,g57)
    c: Coincident(g57,g58)
    c: Coincident(g58,g59)
    c: Coincident(g59,g60)
    c: Coincident(g60,g61)
    c: Coincident(g61,g62)
    c: Coincident(g62,g63)
    c: Coincident(g63,g64)
    c: Coincident(g64,g65)
    c: Coincident(g65,g66)
    c: Coincident(g66,g67)
    c: Coincident(g67,g68)
    c: Coincident(g68,g69)
    c: Coincident(g69,g70)
    c: Coincident(g70,g71)
    c: Coincident(g71,g72)
    c: Coincident(g72,g73)
    c: Coincident(g73,g74)
    c: Coincident(g74,g75)
    c: Coincident(g75,g76)
    c: Coincident(g76,g77)
    c: Coincident(g77,g78)
    c: Coincident(g78,g79)
    c: Coincident(g79,g80)
    c: Coincident(g80,g81)
    c: Coincident(g81,g82)
    c: Coincident(g82,g83)
    c: Coincident(g83,g84)
    c: Coincident(g84,g85)
    c: Coincident(g85,g86)
    c: Coincident(g86,g87)
    c: Coincident(g87,g0)
    c: Coincident(g88,g89)
    c: Coincident(g89,g90)
    c: Coincident(g90,g91)
    c: Coincident(g91,g92)
    c: Coincident(g92,g93)
    c: Coincident(g93,g94)
    c: Coincident(g94,g95)
    c: Coincident(g95,g96)
    c: Coincident(g96,g97)
    c: Coincident(g97,g98)
    c: Coincident(g98,g99)
    c: Coincident(g99,g100)
    c: Coincident(g100,g101)
    c: Coincident(g101,g102)
    c: Coincident(g102,g103)
    c: Coincident(g103,g104)
    c: Coincident(g104,g105)
    c: Coincident(g105,g106)
    c: Coincident(g106,g107)
    c: Coincident(g107,g108)
    c: Coincident(g108,g109)
    c: Coincident(g109,g110)
    c: Coincident(g110,g111)
    c: Coincident(g111,g112)
    c: Coincident(g112,g113)
    c: Coincident(g113,g114)
    c: Coincident(g114,g115)
    c: Coincident(g115,g116)
    c: Coincident(g116,g117)
    c: Coincident(g117,g118)
    c: Coincident(g118,g119)
    c: Coincident(g119,g120)
    c: Coincident(g120,g121)
    c: Coincident(g121,g122)
    c: Coincident(g122,g123)
    c: Coincident(g123,g124)
    c: Coincident(g124,g125)
    c: Coincident(g125,g126)
    c: Coincident(g126,g127)
    c: Coincident(g127,g88)
    c: Coincident(g128,g129)
    c: Coincident(g129,g130)
    c: Coincident(g130,g131)
    c: Coincident(g131,g132)
    c: Coincident(g132,g133)
    c: Coincident(g133,g134)
    c: Coincident(g134,g135)
    c: Coincident(g135,g136)
    c: Coincident(g136,g137)
    c: Coincident(g137,g138)
    c: Coincident(g138,g139)
    c: Coincident(g139,g140)
    c: Coincident(g140,g141)
    c: Coincident(g141,g142)
    c: Coincident(g142,g143)
    c: Coincident(g143,g144)
    c: Coincident(g144,g145)
    c: Coincident(g145,g146)
    c: Coincident(g146,g147)
    c: Coincident(g147,g148)
    c: Coincident(g148,g149)
    c: Coincident(g149,g150)
    c: Coincident(g150,g151)
    c: Coincident(g151,g152)
    c: Coincident(g152,g153)
    c: Coincident(g153,g154)
    c: Coincident(g154,g155)
    c: Coincident(g155,g156)
    c: Coincident(g156,g157)
    c: Coincident(g157,g158)
    c: Coincident(g158,g159)
    c: Coincident(g159,g160)
    c: Coincident(g160,g161)
    c: Coincident(g161,g162)
    c: Coincident(g162,g163)
    c: Coincident(g163,g164)
    c: Coincident(g164,g165)
    c: Coincident(g165,g166)
    c: Coincident(g166,g167)
    c: Coincident(g167,g168)
    c: Coincident(g168,g169)
    c: Coincident(g169,g170)
    c: Coincident(g170,g171)
    c: Coincident(g171,g172)
    c: Coincident(g172,g173)
    c: Coincident(g173,g174)
    c: Coincident(g174,g175)
    c: Coincident(g175,g176)
    c: Coincident(g176,g177)
    c: Coincident(g177,g178)
    c: Coincident(g178,g179)
    c: Coincident(g179,g180)
    c: Coincident(g180,g181)
    c: Coincident(g181,g182)
    c: Coincident(g182,g183)
    c: Coincident(g183,g184)
    c: Coincident(g184,g185)
    c: Coincident(g185,g186)
    c: Coincident(g186,g187)
    c: Coincident(g187,g188)
    c: Coincident(g188,g189)
    c: Coincident(g189,g190)
    c: Coincident(g190,g191)
    c: Coincident(g191,g192)
    c: Coincident(g192,g193)
    c: Coincident(g193,g194)
    c: Coincident(g194,g195)
    c: Coincident(g195,g196)
    c: Coincident(g196,g197)
    c: Coincident(g197,g198)
    c: Coincident(g198,g199)
    c: Coincident(g199,g200)
    c: Coincident(g200,g201)
    c: Coincident(g201,g202)
    c: Coincident(g202,g203)
    c: Coincident(g203,g204)
    c: Coincident(g204,g205)
    c: Coincident(g205,g206)
    c: Coincident(g206,g207)
    c: Coincident(g207,g208)
    c: Coincident(g208,g209)
    c: Coincident(g209,g210)
    c: Coincident(g210,g211)
    c: Coincident(g211,g212)
    c: Coincident(g212,g213)
    c: Coincident(g213,g214)
    c: Coincident(g214,g215)
    c: Coincident(g215,g216)
    c: Coincident(g216,g217)
    c: Coincident(g217,g218)
    c: Coincident(g218,g219)
    c: Coincident(g219,g220)
    c: Coincident(g220,g221)
    c: Coincident(g221,g222)
    c: Coincident(g222,g223)
    c: Coincident(g223,g224)
    c: Coincident(g224,g225)
    c: Coincident(g225,g226)
    c: Coincident(g226,g227)
    c: Coincident(g227,g228)
    c: Coincident(g228,g229)
    c: Coincident(g229,g230)
    c: Coincident(g230,g231)
    c: Coincident(g231,g232)
    c: Coincident(g232,g233)
    c: Coincident(g233,g234)
    c: Coincident(g234,g235)
    c: Coincident(g235,g236)
    c: Coincident(g236,g237)
    c: Coincident(g237,g238)
    c: Coincident(g238,g239)
    c: Coincident(g239,g128)
    c: Coincident(g240,g241)
    c: Coincident(g241,g242)
    c: Coincident(g242,g243)
    c: Coincident(g243,g244)
    c: Coincident(g244,g245)
    c: Coincident(g245,g246)
    c: Coincident(g246,g247)
    c: Coincident(g247,g248)
    c: Coincident(g248,g249)
    c: Coincident(g249,g250)
    c: Coincident(g250,g251)
    c: Coincident(g251,g252)
    c: Coincident(g252,g253)
    c: Coincident(g253,g254)
    c: Coincident(g254,g255)
    c: Coincident(g255,g256)
    c: Coincident(g256,g257)
    c: Coincident(g257,g258)
    c: Coincident(g258,g259)
    c: Coincident(g259,g260)
    c: Coincident(g260,g261)
    c: Coincident(g261,g262)
    c: Coincident(g262,g263)
    c: Coincident(g263,g264)
    c: Coincident(g264,g265)
    c: Coincident(g265,g266)
    c: Coincident(g266,g267)
    c: Coincident(g267,g268)
    c: Coincident(g268,g269)
    c: Coincident(g269,g270)
    c: Coincident(g270,g271)
    c: Coincident(g271,g272)
    c: Coincident(g272,g273)
    c: Coincident(g273,g274)
    c: Coincident(g274,g275)
    c: Coincident(g275,g276)
    c: Coincident(g276,g277)
    c: Coincident(g277,g278)
    c: Coincident(g278,g279)
    c: Coincident(g279,g280)
    c: Coincident(g280,g281)
    c: Coincident(g281,g282)
    c: Coincident(g282,g283)
    c: Coincident(g283,g284)
    c: Coincident(g284,g285)
    c: Coincident(g285,g286)
    c: Coincident(g286,g287)
    c: Coincident(g287,g240)
    c: Coincident(g288,g289)
    c: Coincident(g289,g290)
    c: Coincident(g290,g291)
    c: Coincident(g291,g292)
    c: Coincident(g292,g293)
    c: Coincident(g293,g294)
    c: Coincident(g294,g295)
    c: Coincident(g295,g296)
    c: Coincident(g296,g297)
    c: Coincident(g297,g298)
    c: Coincident(g298,g299)
    c: Coincident(g299,g300)
    c: Coincident(g300,g301)
    c: Coincident(g301,g302)
    c: Coincident(g302,g303)
    c: Coincident(g303,g304)
    c: Coincident(g304,g305)
    c: Coincident(g305,g306)
    c: Coincident(g306,g307)
    c: Coincident(g307,g308)
    c: Coincident(g308,g309)
    c: Coincident(g309,g310)
    c: Coincident(g310,g311)
    c: Coincident(g311,g288)
    c: Coincident(g312,g313)
    c: Coincident(g313,g314)
    c: Coincident(g314,g315)
    c: Coincident(g315,g316)
    c: Coincident(g316,g317)
    c: Coincident(g317,g318)
    c: Coincident(g318,g319)
    c: Coincident(g319,g320)
    c: Coincident(g320,g321)
    c: Coincident(g321,g322)
    c: Coincident(g322,g323)
    c: Coincident(g323,g324)
    c: Coincident(g324,g325)
    c: Coincident(g325,g326)
    c: Coincident(g326,g327)
    c: Coincident(g327,g312)
    c: Coincident(g328,g329)
    c: Coincident(g329,g330)
    c: Coincident(g330,g331)
    c: Coincident(g331,g332)
    c: Coincident(g332,g333)
    c: Coincident(g333,g334)
    c: Coincident(g334,g335)
    c: Coincident(g335,g336)
    c: Coincident(g336,g337)
    c: Coincident(g337,g338)
    c: Coincident(g338,g339)
    c: Coincident(g339,g340)
    c: Coincident(g340,g341)
    c: Coincident(g341,g342)
    c: Coincident(g342,g343)
    c: Coincident(g343,g344)
    c: Coincident(g344,g345)
    c: Coincident(g345,g346)
    c: Coincident(g346,g347)
    c: Coincident(g347,g348)
    c: Coincident(g348,g349)
    c: Coincident(g349,g350)
    c: Coincident(g350,g351)
    c: Coincident(g351,g352)
    c: Coincident(g352,g353)
    c: Coincident(g353,g354)
    c: Coincident(g354,g355)
    c: Coincident(g355,g356)
    c: Coincident(g356,g357)
    c: Coincident(g357,g358)
    c: Coincident(g358,g359)
    c: Coincident(g359,g360)
    c: Coincident(g360,g361)
    c: Coincident(g361,g362)
    c: Coincident(g362,g363)
    c: Coincident(g363,g364)
    c: Coincident(g364,g365)
    c: Coincident(g365,g366)
    c: Coincident(g366,g367)
    c: Coincident(g367,g368)
    c: Coincident(g368,g369)
    c: Coincident(g369,g370)
    c: Coincident(g370,g371)
    c: Coincident(g371,g372)
    c: Coincident(g372,g373)
    c: Coincident(g373,g374)
    c: Coincident(g374,g375)
    c: Coincident(g375,g376)
    c: Coincident(g376,g377)
    c: Coincident(g377,g378)
    c: Coincident(g378,g379)
    c: Coincident(g379,g380)
    c: Coincident(g380,g381)
    c: Coincident(g381,g382)
    c: Coincident(g382,g383)
    c: Coincident(g383,g384)
    c: Coincident(g384,g385)
    c: Coincident(g385,g386)
    c: Coincident(g386,g387)
    c: Coincident(g387,g388)
    c: Coincident(g388,g389)
    c: Coincident(g389,g390)
    c: Coincident(g390,g391)
    c: Coincident(g391,g392)
    c: Coincident(g392,g393)
    c: Coincident(g393,g394)
    c: Coincident(g394,g395)
    c: Coincident(g395,g396)
    c: Coincident(g396,g397)
    c: Coincident(g397,g398)
    c: Coincident(g398,g399)
    c: Coincident(g399,g328)
    c: Coincident(g400,g401)
    c: Coincident(g401,g402)
    c: Coincident(g402,g403)
    c: Coincident(g403,g404)
    c: Coincident(g404,g405)
    c: Coincident(g405,g406)
    c: Coincident(g406,g407)
    c: Coincident(g407,g408)
    c: Coincident(g408,g409)
    c: Coincident(g409,g410)
    c: Coincident(g410,g411)
    c: Coincident(g411,g412)
    c: Coincident(g412,g413)
    c: Coincident(g413,g414)
    c: Coincident(g414,g415)
    c: Coincident(g415,g416)
    c: Coincident(g416,g417)
    c: Coincident(g417,g418)
    c: Coincident(g418,g419)
    c: Coincident(g419,g420)
    c: Coincident(g420,g421)
    c: Coincident(g421,g422)
    c: Coincident(g422,g423)
    c: Coincident(g423,g400)
    c: Coincident(g424,g425)
    c: Coincident(g425,g426)
    c: Coincident(g426,g427)
    c: Coincident(g427,g428)
    c: Coincident(g428,g429)
    c: Coincident(g429,g430)
    c: Coincident(g430,g431)
    c: Coincident(g431,g432)
    c: Coincident(g432,g433)
    c: Coincident(g433,g434)
    c: Coincident(g434,g435)
    c: Coincident(g435,g436)
    c: Coincident(g436,g437)
    c: Coincident(g437,g438)
    c: Coincident(g438,g439)
    c: Coincident(g439,g440)
    c: Coincident(g440,g441)
    c: Coincident(g441,g442)
    c: Coincident(g442,g443)
    c: Coincident(g443,g444)
    c: Coincident(g444,g445)
    c: Coincident(g445,g446)
    c: Coincident(g446,g447)
    c: Coincident(g447,g448)
    c: Coincident(g448,g449)
    c: Coincident(g449,g450)
    c: Coincident(g450,g451)
    c: Coincident(g451,g452)
    c: Coincident(g452,g453)
    c: Coincident(g453,g454)
    c: Coincident(g454,g455)
    c: Coincident(g455,g456)
    c: Coincident(g456,g457)
    c: Coincident(g457,g458)
    c: Coincident(g458,g459)
    c: Coincident(g459,g460)
    c: Coincident(g460,g461)
    c: Coincident(g461,g462)
    c: Coincident(g462,g463)
    c: Coincident(g463,g464)
    c: Coincident(g464,g465)
    c: Coincident(g465,g466)
    c: Coincident(g466,g467)
    c: Coincident(g467,g468)
    c: Coincident(g468,g469)
    c: Coincident(g469,g470)
    c: Coincident(g470,g471)
    c: Coincident(g471,g472)
    c: Coincident(g472,g473)
    c: Coincident(g473,g474)
    c: Coincident(g474,g475)
    c: Coincident(g475,g476)
    c: Coincident(g476,g477)
    c: Coincident(g477,g478)
    c: Coincident(g478,g479)
    c: Coincident(g479,g424)
    c: Coincident(g480,g481)
    c: Coincident(g481,g482)
    c: Coincident(g482,g483)
    c: Coincident(g483,g484)
    c: Coincident(g484,g485)
    c: Coincident(g485,g486)
    c: Coincident(g486,g487)
    c: Coincident(g487,g488)
    c: Coincident(g488,g489)
    c: Coincident(g489,g490)
    c: Coincident(g490,g491)
    c: Coincident(g491,g492)
    c: Coincident(g492,g493)
    c: Coincident(g493,g494)
    c: Coincident(g494,g495)
    c: Coincident(g495,g480)
    c: Coincident(g496,g497)
    c: Coincident(g497,g498)
    c: Coincident(g498,g499)
    c: Coincident(g499,g500)
    c: Coincident(g500,g501)
    c: Coincident(g501,g502)
    c: Coincident(g502,g503)
    c: Coincident(g503,g504)
    c: Coincident(g504,g505)
    c: Coincident(g505,g506)
    c: Coincident(g506,g507)
    c: Coincident(g507,g508)
    c: Coincident(g508,g509)
    c: Coincident(g509,g510)
    c: Coincident(g510,g511)
    c: Coincident(g511,g512)
    c: Coincident(g512,g513)
    c: Coincident(g513,g514)
    c: Coincident(g514,g515)
    c: Coincident(g515,g516)
    c: Coincident(g516,g517)
    c: Coincident(g517,g518)
    c: Coincident(g518,g519)
    c: Coincident(g519,g520)
    c: Coincident(g520,g521)
    c: Coincident(g521,g522)
    c: Coincident(g522,g523)
    c: Coincident(g523,g524)
    c: Coincident(g524,g525)
    c: Coincident(g525,g526)
    c: Coincident(g526,g527)
    c: Coincident(g527,g528)
    c: Coincident(g528,g529)
    c: Coincident(g529,g530)
    c: Coincident(g530,g531)
    c: Coincident(g531,g532)
    c: Coincident(g532,g533)
    c: Coincident(g533,g534)
    c: Coincident(g534,g535)
    c: Coincident(g535,g496)
    c: Coincident(g536,g537)
    c: Coincident(g537,g538)
    c: Coincident(g538,g539)
    c: Coincident(g539,g540)
    c: Coincident(g540,g541)
    c: Coincident(g541,g542)
    c: Coincident(g542,g543)
    c: Coincident(g543,g544)
    c: Coincident(g544,g545)
    c: Coincident(g545,g546)
    c: Coincident(g546,g547)
    c: Coincident(g547,g548)
    c: Coincident(g548,g549)
    c: Coincident(g549,g550)
    c: Coincident(g550,g551)
    c: Coincident(g551,g552)
    c: Coincident(g552,g553)
    c: Coincident(g553,g554)
    c: Coincident(g554,g555)
    c: Coincident(g555,g556)
    c: Coincident(g556,g557)
    c: Coincident(g557,g558)
    c: Coincident(g558,g559)
    c: Coincident(g559,g560)
    c: Coincident(g560,g561)
    c: Coincident(g561,g562)
    c: Coincident(g562,g563)
    c: Coincident(g563,g564)
    c: Coincident(g564,g565)
    c: Coincident(g565,g566)
    c: Coincident(g566,g567)
    c: Coincident(g567,g568)
    c: Coincident(g568,g569)
    c: Coincident(g569,g570)
    c: Coincident(g570,g571)
    c: Coincident(g571,g572)
    c: Coincident(g572,g573)
    c: Coincident(g573,g574)
    c: Coincident(g574,g575)
    c: Coincident(g575,g536)
    c: Coincident(g576,g577)
    c: Coincident(g577,g578)
    c: Coincident(g578,g579)
    c: Coincident(g579,g580)
    c: Coincident(g580,g581)
    c: Coincident(g581,g582)
    c: Coincident(g582,g583)
    c: Coincident(g583,g584)
    c: Coincident(g584,g585)
    c: Coincident(g585,g586)
    c: Coincident(g586,g587)
    c: Coincident(g587,g576)
    c: Coincident(g588,g589)
    c: Coincident(g589,g590)
    c: Coincident(g590,g591)
    c: Coincident(g591,g592)
    c: Coincident(g592,g593)
    c: Coincident(g593,g594)
    c: Coincident(g594,g595)
    c: Coincident(g595,g596)
    c: Coincident(g596,g597)
    c: Coincident(g597,g598)
    c: Coincident(g598,g599)
    c: Coincident(g599,g600)
    c: Coincident(g600,g601)
    c: Coincident(g601,g602)
    c: Coincident(g602,g603)
    c: Coincident(g603,g604)
    c: Coincident(g604,g605)
    c: Coincident(g605,g606)
    c: Coincident(g606,g607)
    c: Coincident(g607,g608)
    c: Coincident(g608,g609)
    c: Coincident(g609,g610)
    c: Coincident(g610,g611)
    c: Coincident(g611,g612)
    c: Coincident(g612,g613)
    c: Coincident(g613,g614)
    c: Coincident(g614,g615)
    c: Coincident(g615,g616)
    c: Coincident(g616,g617)
    c: Coincident(g617,g618)
    c: Coincident(g618,g619)
    c: Coincident(g619,g620)
    c: Coincident(g620,g621)
    c: Coincident(g621,g622)
    c: Coincident(g622,g623)
    c: Coincident(g623,g624)
    c: Coincident(g624,g625)
    c: Coincident(g625,g626)
    c: Coincident(g626,g627)
    c: Coincident(g627,g628)
    c: Coincident(g628,g629)
    c: Coincident(g629,g630)
    c: Coincident(g630,g631)
    c: Coincident(g631,g632)
    c: Coincident(g632,g633)
    c: Coincident(g633,g634)
    c: Coincident(g634,g635)
    c: Coincident(g635,g636)
    c: Coincident(g636,g637)
    c: Coincident(g637,g638)
    c: Coincident(g638,g639)
    c: Coincident(g639,g640)
    c: Coincident(g640,g641)
    c: Coincident(g641,g642)
    c: Coincident(g642,g643)
    c: Coincident(g643,g644)
    c: Coincident(g644,g645)
    c: Coincident(g645,g646)
    c: Coincident(g646,g647)
    c: Coincident(g647,g648)
    c: Coincident(g648,g649)
    c: Coincident(g649,g650)
    c: Coincident(g650,g651)
    c: Coincident(g651,g652)
    c: Coincident(g652,g653)
    c: Coincident(g653,g654)
    c: Coincident(g654,g655)
    c: Coincident(g655,g656)
    c: Coincident(g656,g657)
    c: Coincident(g657,g658)
    c: Coincident(g658,g659)
    c: Coincident(g659,g660)
    c: Coincident(g660,g661)
    c: Coincident(g661,g662)
    c: Coincident(g662,g663)
    c: Coincident(g663,g664)
    c: Coincident(g664,g665)
    c: Coincident(g665,g666)
    c: Coincident(g666,g667)
    c: Coincident(g667,g668)
    c: Coincident(g668,g669)
    c: Coincident(g669,g670)
    c: Coincident(g670,g671)
    c: Coincident(g671,g672)
    c: Coincident(g672,g673)
    c: Coincident(g673,g674)
    c: Coincident(g674,g675)
    c: Coincident(g675,g588)
    c: Coincident(g676,g677)
    c: Coincident(g677,g678)
    c: Coincident(g678,g679)
    c: Coincident(g679,g680)
    c: Coincident(g680,g681)
    c: Coincident(g681,g682)
    c: Coincident(g682,g683)
    c: Coincident(g683,g684)
    c: Coincident(g684,g685)
    c: Coincident(g685,g686)
    c: Coincident(g686,g687)
    c: Coincident(g687,g688)
    c: Coincident(g688,g689)
    c: Coincident(g689,g690)
    c: Coincident(g690,g691)
    c: Coincident(g691,g676)
    c: Coincident(g692,g693)
    c: Coincident(g693,g694)
    c: Coincident(g694,g695)
    c: Coincident(g695,g696)
    c: Coincident(g696,g697)
    c: Coincident(g697,g698)
    c: Coincident(g698,g699)
    c: Coincident(g699,g700)
    c: Coincident(g700,g701)
    c: Coincident(g701,g702)
    c: Coincident(g702,g703)
    c: Coincident(g703,g704)
    c: Coincident(g704,g705)
    c: Coincident(g705,g706)
    c: Coincident(g706,g707)
    c: Coincident(g707,g708)
    c: Coincident(g708,g709)
    c: Coincident(g709,g710)
    c: Coincident(g710,g711)
    c: Coincident(g711,g712)
    c: Coincident(g712,g713)
    c: Coincident(g713,g714)
    c: Coincident(g714,g715)
    c: Coincident(g715,g716)
    c: Coincident(g716,g717)
    c: Coincident(g717,g718)
    c: Coincident(g718,g719)
    c: Coincident(g719,g720)
    c: Coincident(g720,g721)
    c: Coincident(g721,g722)
    c: Coincident(g722,g723)
    c: Coincident(g723,g724)
    c: Coincident(g724,g725)
    c: Coincident(g725,g726)
    c: Coincident(g726,g727)
    c: Coincident(g727,g728)
    c: Coincident(g728,g729)
    c: Coincident(g729,g730)
    c: Coincident(g730,g731)
    c: Coincident(g731,g692)
    c: Coincident(g732,g733)
    c: Coincident(g733,g734)
    c: Coincident(g734,g735)
    c: Coincident(g735,g736)
    c: Coincident(g736,g737)
    c: Coincident(g737,g738)
    c: Coincident(g738,g739)
    c: Coincident(g739,g740)
    c: Coincident(g740,g741)
    c: Coincident(g741,g742)
    c: Coincident(g742,g743)
    c: Coincident(g743,g744)
    c: Coincident(g744,g745)
    c: Coincident(g745,g746)
    c: Coincident(g746,g747)
    c: Coincident(g747,g748)
    c: Coincident(g748,g749)
    c: Coincident(g749,g750)
    c: Coincident(g750,g751)
    c: Coincident(g751,g752)
    c: Coincident(g752,g753)
    c: Coincident(g753,g754)
    c: Coincident(g754,g755)
    c: Coincident(g755,g756)
    c: Coincident(g756,g757)
    c: Coincident(g757,g758)
    c: Coincident(g758,g759)
    c: Coincident(g759,g760)
    c: Coincident(g760,g761)
    c: Coincident(g761,g762)
    c: Coincident(g762,g763)
    c: Coincident(g763,g732)
    c: Coincident(g764,g765)
    c: Coincident(g765,g766)
    c: Coincident(g766,g767)
    c: Coincident(g767,g768)
    c: Coincident(g768,g769)
    c: Coincident(g769,g770)
    c: Coincident(g770,g771)
    c: Coincident(g771,g772)
    c: Coincident(g772,g773)
    c: Coincident(g773,g774)
    c: Coincident(g774,g775)
    c: Coincident(g775,g776)
    c: Coincident(g776,g777)
    c: Coincident(g777,g778)
    c: Coincident(g778,g779)
    c: Coincident(g779,g780)
    c: Coincident(g780,g781)
    c: Coincident(g781,g782)
    c: Coincident(g782,g783)
    c: Coincident(g783,g784)
    c: Coincident(g784,g785)
    c: Coincident(g785,g786)
    c: Coincident(g786,g787)
    c: Coincident(g787,g764)
    c: Coincident(g788,g789)
    c: Coincident(g789,g790)
    c: Coincident(g790,g791)
    c: Coincident(g791,g792)
    c: Coincident(g792,g793)
    c: Coincident(g793,g794)
    c: Coincident(g794,g795)
    c: Coincident(g795,g796)
    c: Coincident(g796,g797)
    c: Coincident(g797,g798)
    c: Coincident(g798,g799)
    c: Coincident(g799,g800)
    c: Coincident(g800,g801)
    c: Coincident(g801,g802)
    c: Coincident(g802,g803)
    c: Coincident(g803,g804)
    c: Coincident(g804,g805)
    c: Coincident(g805,g806)
    c: Coincident(g806,g807)
    c: Coincident(g807,g808)
    c: Coincident(g808,g809)
    c: Coincident(g809,g810)
    c: Coincident(g810,g811)
    c: Coincident(g811,g812)
    c: Coincident(g812,g813)
    c: Coincident(g813,g814)
    c: Coincident(g814,g815)
    c: Coincident(g815,g816)
    c: Coincident(g816,g817)
    c: Coincident(g817,g818)
    c: Coincident(g818,g819)
    c: Coincident(g819,g820)
    c: Coincident(g820,g821)
    c: Coincident(g821,g822)
    c: Coincident(g822,g823)
    c: Coincident(g823,g824)
    c: Coincident(g824,g825)
    c: Coincident(g825,g826)
    c: Coincident(g826,g827)
    c: Coincident(g827,g828)
    c: Coincident(g828,g829)
    c: Coincident(g829,g830)
    c: Coincident(g830,g831)
    c: Coincident(g831,g832)
    c: Coincident(g832,g833)
    c: Coincident(g833,g834)
    c: Coincident(g834,g835)
    c: Coincident(g835,g836)
    c: Coincident(g836,g837)
    c: Coincident(g837,g838)
    c: Coincident(g838,g839)
    c: Coincident(g839,g840)
    c: Coincident(g840,g841)
    c: Coincident(g841,g842)
    c: Coincident(g842,g843)
    c: Coincident(g843,g844)
    c: Coincident(g844,g845)
    c: Coincident(g845,g846)
    c: Coincident(g846,g847)
    c: Coincident(g847,g848)
    c: Coincident(g848,g849)
    c: Coincident(g849,g850)
    c: Coincident(g850,g851)
    c: Coincident(g851,g852)
    c: Coincident(g852,g853)
    c: Coincident(g853,g854)
    c: Coincident(g854,g855)
    c: Coincident(g855,g856)
    c: Coincident(g856,g857)
    c: Coincident(g857,g858)
    c: Coincident(g858,g859)
    c: Coincident(g859,g788)
FEATURE [Sketcher::SketchObject] Sketch026  label="16 Bit VS007"
  FullyConstrained = false
  Placement = pos=(8.14,33,-10) rot=(1,0,0;3.14159rad)
  sketch-geometry (860):
    g0: BSplineCurve PolesCount=2 KnotsCount=2 Degree=1 IsPeriodic=0
    g1: BSplineCurve PolesCount=2 KnotsCount=2 Degree=1 IsPeriodic=0
    g2: BSplineCurve PolesCount=2 KnotsCount=2 Degree=1 IsPeriodic=0
    g3: BSplineCurve PolesCount=2 KnotsCount=2 Degree=1 IsPeriodic=0
    g4: BSplineCurve PolesCount=2 KnotsCount=2 Degree=1 IsPeriodic=0
    g5: BSplineCurve PolesCount=2 KnotsCount=2 Degree=1 IsPeriodic=0
    g6: BSplineCurve PolesCount=2 KnotsCount=2 Degree=1 IsPeriodic=0
    g7: BSplineCurve PolesCount=2 KnotsCount=2 Degree=1 IsPeriodic=0
    g8: BSplineCurve PolesCount=2 KnotsCount=2 Degree=1 IsPeriodic=0
    g9: BSplineCurve PolesCount=2 KnotsCount=2 Degree=1 IsPeriodic=0
    g10: BSplineCurve PolesCount=2 KnotsCount=2 Degree=1 IsPeriodic=0
    g11: BSplineCurve PolesCount=2 KnotsCount=2 Degree=1 IsPeriodic=0
    g12: BSplineCurve PolesCount=2 KnotsCount=2 Degree=1 IsPeriodic=0
    g13: BSplineCurve PolesCount=2 KnotsCount=2 Degree=1 IsPeriodic=0
    g14: BSplineCurve PolesCount=2 KnotsCount=2 Degree=1 IsPeriodic=0
    g15: BSplineCurve PolesCount=2 KnotsCount=2 Degree=1 IsPeriodic=0
    g16: BSplineCurve PolesCount=2 KnotsCount=2 Degree=1 IsPeriodic=0
    g17: BSplineCurve PolesCount=2 KnotsCount=2 Degree=1 IsPeriodic=0
    g18: BSplineCurve PolesCount=2 KnotsCount=2 Degree=1 IsPeriodic=0
    g19: BSplineCurve PolesCount=2 KnotsCount=2 Degree=1 IsPeriodic=0
    g20: BSplineCurve PolesCount=2 KnotsCount=2 Degree=1 IsPeriodic=0
    g21: BSplineCurve PolesCount=2 KnotsCount=2 Degree=1 IsPeriodic=0
    g22: BSplineCurve PolesCount=2 KnotsCount=2 Degree=1 IsPeriodic=0
    g23: BSplineCurve PolesCount=2 KnotsCount=2 Degree=1 IsPeriodic=0
    g24: BSplineCurve PolesCount=2 KnotsCount=2 Degree=1 IsPeriodic=0
    g25: BSplineCurve PolesCount=2 KnotsCount=2 Degree=1 IsPeriodic=0
    g26: BSplineCurve PolesCount=2 KnotsCount=2 Degree=1 IsPeriodic=0
    g27: BSplineCurve PolesCount=2 KnotsCount=2 Degree=1 IsPeriodic=0
    g28: BSplineCurve PolesCount=2 KnotsCount=2 Degree=1 IsPeriodic=0
    g29: BSplineCurve PolesCount=2 KnotsCount=2 Degree=1 IsPeriodic=0
    g30: BSplineCurve PolesCount=2 KnotsCount=2 Degree=1 IsPeriodic=0
    g31: BSplineCurve PolesCount=2 KnotsCount=2 Degree=1 IsPeriodic=0
    g32: BSplineCurve PolesCount=2 KnotsCount=2 Degree=1 IsPeriodic=0
    g33: BSplineCurve PolesCount=2 KnotsCount=2 Degree=1 IsPeriodic=0
    g34: BSplineCurve PolesCount=2 KnotsCount=2 Degree=1 IsPeriodic=0
    g35: BSplineCurve PolesCount=2 KnotsCount=2 Degree=1 IsPeriodic=0
    g36: BSplineCurve PolesCount=2 KnotsCount=2 Degree=1 IsPeriodic=0
    g37: BSplineCurve PolesCount=2 KnotsCount=2 Degree=1 IsPeriodic=0
    g38: BSplineCurve PolesCount=2 KnotsCount=2 Degree=1 IsPeriodic=0
    g39: BSplineCurve PolesCount=2 KnotsCount=2 Degree=1 IsPeriodic=0
    g40: BSplineCurve PolesCount=2 KnotsCount=2 Degree=1 IsPeriodic=0
    g41: BSplineCurve PolesCount=2 KnotsCount=2 Degree=1 IsPeriodic=0
    g42: BSplineCurve PolesCount=2 KnotsCount=2 Degree=1 IsPeriodic=0
    g43: BSplineCurve PolesCount=2 KnotsCount=2 Degree=1 IsPeriodic=0
    g44: BSplineCurve PolesCount=2 KnotsCount=2 Degree=1 IsPeriodic=0
    g45: BSplineCurve PolesCount=2 KnotsCount=2 Degree=1 IsPeriodic=0
    g46: BSplineCurve PolesCount=2 KnotsCount=2 Degree=1 IsPeriodic=0
    g47: BSplineCurve PolesCount=2 KnotsCount=2 Degree=1 IsPeriodic=0
    g48: BSplineCurve PolesCount=2 KnotsCount=2 Degree=1 IsPeriodic=0
    g49: BSplineCurve PolesCount=2 KnotsCount=2 Degree=1 IsPeriodic=0
    g50: BSplineCurve PolesCount=2 KnotsCount=2 Degree=1 IsPeriodic=0
    g51: BSplineCurve PolesCount=2 KnotsCount=2 Degree=1 IsPeriodic=0
    g52: BSplineCurve PolesCount=2 KnotsCount=2 Degree=1 IsPeriodic=0
    g53: BSplineCurve PolesCount=2 KnotsCount=2 Degree=1 IsPeriodic=0
    g54: BSplineCurve PolesCount=2 KnotsCount=2 Degree=1 IsPeriodic=0
    g55: BSplineCurve PolesCount=2 KnotsCount=2 Degree=1 IsPeriodic=0
    g56: BSplineCurve PolesCount=2 KnotsCount=2 Degree=1 IsPeriodic=0
    g57: BSplineCurve PolesCount=2 KnotsCount=2 Degree=1 IsPeriodic=0
    g58: BSplineCurve PolesCount=2 KnotsCount=2 Degree=1 IsPeriodic=0
    g59: BSplineCurve PolesCount=2 KnotsCount=2 Degree=1 IsPeriodic=0
    g60: BSplineCurve PolesCount=2 KnotsCount=2 Degree=1 IsPeriodic=0
    g61: BSplineCurve PolesCount=2 KnotsCount=2 Degree=1 IsPeriodic=0
    g62: BSplineCurve PolesCount=2 KnotsCount=2 Degree=1 IsPeriodic=0
    g63: BSplineCurve PolesCount=2 KnotsCount=2 Degree=1 IsPeriodic=0
    g64: BSplineCurve PolesCount=2 KnotsCount=2 Degree=1 IsPeriodic=0
    g65: BSplineCurve PolesCount=2 KnotsCount=2 Degree=1 IsPeriodic=0
    g66: BSplineCurve PolesCount=2 KnotsCount=2 Degree=1 IsPeriodic=0
    g67: BSplineCurve PolesCount=2 KnotsCount=2 Degree=1 IsPeriodic=0
    g68: BSplineCurve PolesCount=2 KnotsCount=2 Degree=1 IsPeriodic=0
    g69: BSplineCurve PolesCount=2 KnotsCount=2 Degree=1 IsPeriodic=0
    g70: BSplineCurve PolesCount=2 KnotsCount=2 Degree=1 IsPeriodic=0
    g71: BSplineCurve PolesCount=2 KnotsCount=2 Degree=1 IsPeriodic=0
    g72: BSplineCurve PolesCount=2 KnotsCount=2 Degree=1 IsPeriodic=0
    g73: BSplineCurve PolesCount=2 KnotsCount=2 Degree=1 IsPeriodic=0
    g74: BSplineCurve PolesCount=2 KnotsCount=2 Degree=1 IsPeriodic=0
    g75: BSplineCurve PolesCount=2 KnotsCount=2 Degree=1 IsPeriodic=0
    g76: BSplineCurve PolesCount=2 KnotsCount=2 Degree=1 IsPeriodic=0
    g77: BSplineCurve PolesCount=2 KnotsCount=2 Degree=1 IsPeriodic=0
    g78: BSplineCurve PolesCount=2 KnotsCount=2 Degree=1 IsPeriodic=0
    g79: BSplineCurve PolesCount=2 KnotsCount=2 Degree=1 IsPeriodic=0
    g80: BSplineCurve PolesCount=2 KnotsCount=2 Degree=1 IsPeriodic=0
    g81: BSplineCurve PolesCount=2 KnotsCount=2 Degree=1 IsPeriodic=0
    g82: BSplineCurve PolesCount=2 KnotsCount=2 Degree=1 IsPeriodic=0
    g83: BSplineCurve PolesCount=2 KnotsCount=2 Degree=1 IsPeriodic=0
    g84: BSplineCurve PolesCount=2 KnotsCount=2 Degree=1 IsPeriodic=0
    g85: BSplineCurve PolesCount=2 KnotsCount=2 Degree=1 IsPeriodic=0
    g86: BSplineCurve PolesCount=2 KnotsCount=2 Degree=1 IsPeriodic=0
    g87: BSplineCurve PolesCount=2 KnotsCount=2 Degree=1 IsPeriodic=0
    g88: BSplineCurve PolesCount=2 KnotsCount=2 Degree=1 IsPeriodic=0
    g89: BSplineCurve PolesCount=2 KnotsCount=2 Degree=1 IsPeriodic=0
    g90: BSplineCurve PolesCount=2 KnotsCount=2 Degree=1 IsPeriodic=0
    g91: BSplineCurve PolesCount=2 KnotsCount=2 Degree=1 IsPeriodic=0
    g92: BSplineCurve PolesCount=2 KnotsCount=2 Degree=1 IsPeriodic=0
    g93: BSplineCurve PolesCount=2 KnotsCount=2 Degree=1 IsPeriodic=0
    g94: BSplineCurve PolesCount=2 KnotsCount=2 Degree=1 IsPeriodic=0
    g95: BSplineCurve PolesCount=2 KnotsCount=2 Degree=1 IsPeriodic=0
    g96: BSplineCurve PolesCount=2 KnotsCount=2 Degree=1 IsPeriodic=0
    g97: BSplineCurve PolesCount=2 KnotsCount=2 Degree=1 IsPeriodic=0
    g98: BSplineCurve PolesCount=2 KnotsCount=2 Degree=1 IsPeriodic=0
    g99: BSplineCurve PolesCount=2 KnotsCount=2 Degree=1 IsPeriodic=0
    g100: BSplineCurve PolesCount=2 KnotsCount=2 Degree=1 IsPeriodic=0
    g101: BSplineCurve PolesCount=2 KnotsCount=2 Degree=1 IsPeriodic=0
    g102: BSplineCurve PolesCount=2 KnotsCount=2 Degree=1 IsPeriodic=0
    g103: BSplineCurve PolesCount=2 KnotsCount=2 Degree=1 IsPeriodic=0
    g104: BSplineCurve PolesCount=2 KnotsCount=2 Degree=1 IsPeriodic=0
    g105: BSplineCurve PolesCount=2 KnotsCount=2 Degree=1 IsPeriodic=0
    g106: BSplineCurve PolesCount=2 KnotsCount=2 Degree=1 IsPeriodic=0
    g107: BSplineCurve PolesCount=2 KnotsCount=2 Degree=1 IsPeriodic=0
    g108: BSplineCurve PolesCount=2 KnotsCount=2 Degree=1 IsPeriodic=0
    g109: BSplineCurve PolesCount=2 KnotsCount=2 Degree=1 IsPeriodic=0
    g110: BSplineCurve PolesCount=2 KnotsCount=2 Degree=1 IsPeriodic=0
    g111: BSplineCurve PolesCount=2 KnotsCount=2 Degree=1 IsPeriodic=0
    g112: BSplineCurve PolesCount=2 KnotsCount=2 Degree=1 IsPeriodic=0
    g113: BSplineCurve PolesCount=2 KnotsCount=2 Degree=1 IsPeriodic=0
    g114: BSplineCurve PolesCount=2 KnotsCount=2 Degree=1 IsPeriodic=0
    g115: BSplineCurve PolesCount=2 KnotsCount=2 Degree=1 IsPeriodic=0
    g116: BSplineCurve PolesCount=2 KnotsCount=2 Degree=1 IsPeriodic=0
    g117: BSplineCurve PolesCount=2 KnotsCount=2 Degree=1 IsPeriodic=0
    g118: BSplineCurve PolesCount=2 KnotsCount=2 Degree=1 IsPeriodic=0
    g119: BSplineCurve PolesCount=2 KnotsCount=2 Degree=1 IsPeriodic=0
    g120: BSplineCurve PolesCount=2 KnotsCount=2 Degree=1 IsPeriodic=0
    g121: BSplineCurve PolesCount=2 KnotsCount=2 Degree=1 IsPeriodic=0
    g122: BSplineCurve PolesCount=2 KnotsCount=2 Degree=1 IsPeriodic=0
    g123: BSplineCurve PolesCount=2 KnotsCount=2 Degree=1 IsPeriodic=0
    g124: BSplineCurve PolesCount=2 KnotsCount=2 Degree=1 IsPeriodic=0
    g125: BSplineCurve PolesCount=2 KnotsCount=2 Degree=1 IsPeriodic=0
    g126: BSplineCurve PolesCount=2 KnotsCount=2 Degree=1 IsPeriodic=0
    g127: BSplineCurve PolesCount=2 KnotsCount=2 Degree=1 IsPeriodic=0
    g128: BSplineCurve PolesCount=2 KnotsCount=2 Degree=1 IsPeriodic=0
    g129: BSplineCurve PolesCount=2 KnotsCount=2 Degree=1 IsPeriodic=0
    g130: BSplineCurve PolesCount=2 KnotsCount=2 Degree=1 IsPeriodic=0
    g131: BSplineCurve PolesCount=2 KnotsCount=2 Degree=1 IsPeriodic=0
    g132: BSplineCurve PolesCount=2 KnotsCount=2 Degree=1 IsPeriodic=0
    g133: BSplineCurve PolesCount=2 KnotsCount=2 Degree=1 IsPeriodic=0
    g134: BSplineCurve PolesCount=2 KnotsCount=2 Degree=1 IsPeriodic=0
    g135: BSplineCurve PolesCount=2 KnotsCount=2 Degree=1 IsPeriodic=0
    g136: BSplineCurve PolesCount=2 KnotsCount=2 Degree=1 IsPeriodic=0
    g137: BSplineCurve PolesCount=2 KnotsCount=2 Degree=1 IsPeriodic=0
    g138: BSplineCurve PolesCount=2 KnotsCount=2 Degree=1 IsPeriodic=0
    g139: BSplineCurve PolesCount=2 KnotsCount=2 Degree=1 IsPeriodic=0
    g140: BSplineCurve PolesCount=2 KnotsCount=2 Degree=1 IsPeriodic=0
    g141: BSplineCurve PolesCount=2 KnotsCount=2 Degree=1 IsPeriodic=0
    g142: BSplineCurve PolesCount=2 KnotsCount=2 Degree=1 IsPeriodic=0
    g143: BSplineCurve PolesCount=2 KnotsCount=2 Degree=1 IsPeriodic=0
    g144: BSplineCurve PolesCount=2 KnotsCount=2 Degree=1 IsPeriodic=0
    g145: BSplineCurve PolesCount=2 KnotsCount=2 Degree=1 IsPeriodic=0
    g146: BSplineCurve PolesCount=2 KnotsCount=2 Degree=1 IsPeriodic=0
    g147: BSplineCurve PolesCount=2 KnotsCount=2 Degree=1 IsPeriodic=0
    g148: BSplineCurve PolesCount=2 KnotsCount=2 Degree=1 IsPeriodic=0
    g149: BSplineCurve PolesCount=2 KnotsCount=2 Degree=1 IsPeriodic=0
    g150: BSplineCurve PolesCount=2 KnotsCount=2 Degree=1 IsPeriodic=0
    g151: BSplineCurve PolesCount=2 KnotsCount=2 Degree=1 IsPeriodic=0
    g152: BSplineCurve PolesCount=2 KnotsCount=2 Degree=1 IsPeriodic=0
    g153: BSplineCurve PolesCount=2 KnotsCount=2 Degree=1 IsPeriodic=0
    g154: BSplineCurve PolesCount=2 KnotsCount=2 Degree=1 IsPeriodic=0
    g155: BSplineCurve PolesCount=2 KnotsCount=2 Degree=1 IsPeriodic=0
    g156: BSplineCurve PolesCount=2 KnotsCount=2 Degree=1 IsPeriodic=0
    g157: BSplineCurve PolesCount=2 KnotsCount=2 Degree=1 IsPeriodic=0
    g158: BSplineCurve PolesCount=2 KnotsCount=2 Degree=1 IsPeriodic=0
    g159: BSplineCurve PolesCount=2 KnotsCount=2 Degree=1 IsPeriodic=0
    g160: BSplineCurve PolesCount=2 KnotsCount=2 Degree=1 IsPeriodic=0
    g161: BSplineCurve PolesCount=2 KnotsCount=2 Degree=1 IsPeriodic=0
    g162: BSplineCurve PolesCount=2 KnotsCount=2 Degree=1 IsPeriodic=0
    g163: BSplineCurve PolesCount=2 KnotsCount=2 Degree=1 IsPeriodic=0
    g164: BSplineCurve PolesCount=2 KnotsCount=2 Degree=1 IsPeriodic=0
    g165: BSplineCurve PolesCount=2 KnotsCount=2 Degree=1 IsPeriodic=0
    g166: BSplineCurve PolesCount=2 KnotsCount=2 Degree=1 IsPeriodic=0
    g167: BSplineCurve PolesCount=2 KnotsCount=2 Degree=1 IsPeriodic=0
    g168: BSplineCurve PolesCount=2 KnotsCount=2 Degree=1 IsPeriodic=0
    g169: BSplineCurve PolesCount=2 KnotsCount=2 Degree=1 IsPeriodic=0
    g170: BSplineCurve PolesCount=2 KnotsCount=2 Degree=1 IsPeriodic=0
    g171: BSplineCurve PolesCount=2 KnotsCount=2 Degree=1 IsPeriodic=0
    g172: BSplineCurve PolesCount=2 KnotsCount=2 Degree=1 IsPeriodic=0
    g173: BSplineCurve PolesCount=2 KnotsCount=2 Degree=1 IsPeriodic=0
    g174: BSplineCurve PolesCount=2 KnotsCount=2 Degree=1 IsPeriodic=0
    g175: BSplineCurve PolesCount=2 KnotsCount=2 Degree=1 IsPeriodic=0
    g176: BSplineCurve PolesCount=2 KnotsCount=2 Degree=1 IsPeriodic=0
    g177: BSplineCurve PolesCount=2 KnotsCount=2 Degree=1 IsPeriodic=0
    g178: BSplineCurve PolesCount=2 KnotsCount=2 Degree=1 IsPeriodic=0
    g179: BSplineCurve PolesCount=2 KnotsCount=2 Degree=1 IsPeriodic=0
    g180: BSplineCurve PolesCount=2 KnotsCount=2 Degree=1 IsPeriodic=0
    g181: BSplineCurve PolesCount=2 KnotsCount=2 Degree=1 IsPeriodic=0
    g182: BSplineCurve PolesCount=2 KnotsCount=2 Degree=1 IsPeriodic=0
    g183: BSplineCurve PolesCount=2 KnotsCount=2 Degree=1 IsPeriodic=0
    g184: BSplineCurve PolesCount=2 KnotsCount=2 Degree=1 IsPeriodic=0
    g185: BSplineCurve PolesCount=2 KnotsCount=2 Degree=1 IsPeriodic=0
    g186: BSplineCurve PolesCount=2 KnotsCount=2 Degree=1 IsPeriodic=0
    g187: BSplineCurve PolesCount=2 KnotsCount=2 Degree=1 IsPeriodic=0
    g188: BSplineCurve PolesCount=2 KnotsCount=2 Degree=1 IsPeriodic=0
    g189: BSplineCurve PolesCount=2 KnotsCount=2 Degree=1 IsPeriodic=0
    g190: BSplineCurve PolesCount=2 KnotsCount=2 Degree=1 IsPeriodic=0
    g191: BSplineCurve PolesCount=2 KnotsCount=2 Degree=1 IsPeriodic=0
    g192: BSplineCurve PolesCount=2 KnotsCount=2 Degree=1 IsPeriodic=0
    g193: BSplineCurve PolesCount=2 KnotsCount=2 Degree=1 IsPeriodic=0
    g194: BSplineCurve PolesCount=2 KnotsCount=2 Degree=1 IsPeriodic=0
    g195: BSplineCurve PolesCount=2 KnotsCount=2 Degree=1 IsPeriodic=0
    g196: BSplineCurve PolesCount=2 KnotsCount=2 Degree=1 IsPeriodic=0
    g197: BSplineCurve PolesCount=2 KnotsCount=2 Degree=1 IsPeriodic=0
    g198: BSplineCurve PolesCount=2 KnotsCount=2 Degree=1 IsPeriodic=0
    g199: BSplineCurve PolesCount=2 KnotsCount=2 Degree=1 IsPeriodic=0
    g200: BSplineCurve PolesCount=2 KnotsCount=2 Degree=1 IsPeriodic=0
    g201: BSplineCurve PolesCount=2 KnotsCount=2 Degree=1 IsPeriodic=0
    g202: BSplineCurve PolesCount=2 KnotsCount=2 Degree=1 IsPeriodic=0
    g203: BSplineCurve PolesCount=2 KnotsCount=2 Degree=1 IsPeriodic=0
    g204: BSplineCurve PolesCount=2 KnotsCount=2 Degree=1 IsPeriodic=0
    g205: BSplineCurve PolesCount=2 KnotsCount=2 Degree=1 IsPeriodic=0
    g206: BSplineCurve PolesCount=2 KnotsCount=2 Degree=1 IsPeriodic=0
    g207: BSplineCurve PolesCount=2 KnotsCount=2 Degree=1 IsPeriodic=0
    g208: BSplineCurve PolesCount=2 KnotsCount=2 Degree=1 IsPeriodic=0
    g209: BSplineCurve PolesCount=2 KnotsCount=2 Degree=1 IsPeriodic=0
    g210: BSplineCurve PolesCount=2 KnotsCount=2 Degree=1 IsPeriodic=0
    g211: BSplineCurve PolesCount=2 KnotsCount=2 Degree=1 IsPeriodic=0
    g212: BSplineCurve PolesCount=2 KnotsCount=2 Degree=1 IsPeriodic=0
    g213: BSplineCurve PolesCount=2 KnotsCount=2 Degree=1 IsPeriodic=0
    g214: BSplineCurve PolesCount=2 KnotsCount=2 Degree=1 IsPeriodic=0
    g215: BSplineCurve PolesCount=2 KnotsCount=2 Degree=1 IsPeriodic=0
    g216: BSplineCurve PolesCount=2 KnotsCount=2 Degree=1 IsPeriodic=0
    g217: BSplineCurve PolesCount=2 KnotsCount=2 Degree=1 IsPeriodic=0
    g218: BSplineCurve PolesCount=2 KnotsCount=2 Degree=1 IsPeriodic=0
    g219: BSplineCurve PolesCount=2 KnotsCount=2 Degree=1 IsPeriodic=0
    g220: BSplineCurve PolesCount=2 KnotsCount=2 Degree=1 IsPeriodic=0
    g221: BSplineCurve PolesCount=2 KnotsCount=2 Degree=1 IsPeriodic=0
    g222: BSplineCurve PolesCount=2 KnotsCount=2 Degree=1 IsPeriodic=0
    g223: BSplineCurve PolesCount=2 KnotsCount=2 Degree=1 IsPeriodic=0
    g224: BSplineCurve PolesCount=2 KnotsCount=2 Degree=1 IsPeriodic=0
    g225: BSplineCurve PolesCount=2 KnotsCount=2 Degree=1 IsPeriodic=0
    g226: BSplineCurve PolesCount=2 KnotsCount=2 Degree=1 IsPeriodic=0
    g227: BSplineCurve PolesCount=2 KnotsCount=2 Degree=1 IsPeriodic=0
    g228: BSplineCurve PolesCount=2 KnotsCount=2 Degree=1 IsPeriodic=0
    g229: BSplineCurve PolesCount=2 KnotsCount=2 Degree=1 IsPeriodic=0
    g230: BSplineCurve PolesCount=2 KnotsCount=2 Degree=1 IsPeriodic=0
    g231: BSplineCurve PolesCount=2 KnotsCount=2 Degree=1 IsPeriodic=0
    g232: BSplineCurve PolesCount=2 KnotsCount=2 Degree=1 IsPeriodic=0
    g233: BSplineCurve PolesCount=2 KnotsCount=2 Degree=1 IsPeriodic=0
    g234: BSplineCurve PolesCount=2 KnotsCount=2 Degree=1 IsPeriodic=0
    g235: BSplineCurve PolesCount=2 KnotsCount=2 Degree=1 IsPeriodic=0
    g236: BSplineCurve PolesCount=2 KnotsCount=2 Degree=1 IsPeriodic=0
    g237: BSplineCurve PolesCount=2 KnotsCount=2 Degree=1 IsPeriodic=0
    g238: BSplineCurve PolesCount=2 KnotsCount=2 Degree=1 IsPeriodic=0
    g239: BSplineCurve PolesCount=2 KnotsCount=2 Degree=1 IsPeriodic=0
    g240: BSplineCurve PolesCount=2 KnotsCount=2 Degree=1 IsPeriodic=0
    g241: BSplineCurve PolesCount=2 KnotsCount=2 Degree=1 IsPeriodic=0
    g242: BSplineCurve PolesCount=2 KnotsCount=2 Degree=1 IsPeriodic=0
    g243: BSplineCurve PolesCount=2 KnotsCount=2 Degree=1 IsPeriodic=0
    g244: BSplineCurve PolesCount=2 KnotsCount=2 Degree=1 IsPeriodic=0
    g245: BSplineCurve PolesCount=2 KnotsCount=2 Degree=1 IsPeriodic=0
    g246: BSplineCurve PolesCount=2 KnotsCount=2 Degree=1 IsPeriodic=0
    g247: BSplineCurve PolesCount=2 KnotsCount=2 Degree=1 IsPeriodic=0
    g248: BSplineCurve PolesCount=2 KnotsCount=2 Degree=1 IsPeriodic=0
    g249: BSplineCurve PolesCount=2 KnotsCount=2 Degree=1 IsPeriodic=0
    g250: BSplineCurve PolesCount=2 KnotsCount=2 Degree=1 IsPeriodic=0
    g251: BSplineCurve PolesCount=2 KnotsCount=2 Degree=1 IsPeriodic=0
    g252: BSplineCurve PolesCount=2 KnotsCount=2 Degree=1 IsPeriodic=0
    g253: BSplineCurve PolesCount=2 KnotsCount=2 Degree=1 IsPeriodic=0
    g254: BSplineCurve PolesCount=2 KnotsCount=2 Degree=1 IsPeriodic=0
    g255: BSplineCurve PolesCount=2 KnotsCount=2 Degree=1 IsPeriodic=0
    g256: BSplineCurve PolesCount=2 KnotsCount=2 Degree=1 IsPeriodic=0
    g257: BSplineCurve PolesCount=2 KnotsCount=2 Degree=1 IsPeriodic=0
    g258: BSplineCurve PolesCount=2 KnotsCount=2 Degree=1 IsPeriodic=0
    g259: BSplineCurve PolesCount=2 KnotsCount=2 Degree=1 IsPeriodic=0
    g260: BSplineCurve PolesCount=2 KnotsCount=2 Degree=1 IsPeriodic=0
    g261: BSplineCurve PolesCount=2 KnotsCount=2 Degree=1 IsPeriodic=0
    g262: BSplineCurve PolesCount=2 KnotsCount=2 Degree=1 IsPeriodic=0
    g263: BSplineCurve PolesCount=2 KnotsCount=2 Degree=1 IsPeriodic=0
    g264: BSplineCurve PolesCount=2 KnotsCount=2 Degree=1 IsPeriodic=0
    g265: BSplineCurve PolesCount=2 KnotsCount=2 Degree=1 IsPeriodic=0
    g266: BSplineCurve PolesCount=2 KnotsCount=2 Degree=1 IsPeriodic=0
    g267: BSplineCurve PolesCount=2 KnotsCount=2 Degree=1 IsPeriodic=0
    g268: BSplineCurve PolesCount=2 KnotsCount=2 Degree=1 IsPeriodic=0
    g269: BSplineCurve PolesCount=2 KnotsCount=2 Degree=1 IsPeriodic=0
    g270: BSplineCurve PolesCount=2 KnotsCount=2 Degree=1 IsPeriodic=0
    g271: BSplineCurve PolesCount=2 KnotsCount=2 Degree=1 IsPeriodic=0
    g272: BSplineCurve PolesCount=2 KnotsCount=2 Degree=1 IsPeriodic=0
    g273: BSplineCurve PolesCount=2 KnotsCount=2 Degree=1 IsPeriodic=0
    g274: BSplineCurve PolesCount=2 KnotsCount=2 Degree=1 IsPeriodic=0
    g275: BSplineCurve PolesCount=2 KnotsCount=2 Degree=1 IsPeriodic=0
    g276: BSplineCurve PolesCount=2 KnotsCount=2 Degree=1 IsPeriodic=0
    g277: BSplineCurve PolesCount=2 KnotsCount=2 Degree=1 IsPeriodic=0
    g278: BSplineCurve PolesCount=2 KnotsCount=2 Degree=1 IsPeriodic=0
    g279: BSplineCurve PolesCount=2 KnotsCount=2 Degree=1 IsPeriodic=0
    g280: BSplineCurve PolesCount=2 KnotsCount=2 Degree=1 IsPeriodic=0
    g281: BSplineCurve PolesCount=2 KnotsCount=2 Degree=1 IsPeriodic=0
    g282: BSplineCurve PolesCount=2 KnotsCount=2 Degree=1 IsPeriodic=0
    g283: BSplineCurve PolesCount=2 KnotsCount=2 Degree=1 IsPeriodic=0
    g284: BSplineCurve PolesCount=2 KnotsCount=2 Degree=1 IsPeriodic=0
    g285: BSplineCurve PolesCount=2 KnotsCount=2 Degree=1 IsPeriodic=0
    g286: BSplineCurve PolesCount=2 KnotsCount=2 Degree=1 IsPeriodic=0
    g287: BSplineCurve PolesCount=2 KnotsCount=2 Degree=1 IsPeriodic=0
    g288: BSplineCurve PolesCount=2 KnotsCount=2 Degree=1 IsPeriodic=0
    g289: BSplineCurve PolesCount=2 KnotsCount=2 Degree=1 IsPeriodic=0
    g290: BSplineCurve PolesCount=2 KnotsCount=2 Degree=1 IsPeriodic=0
    g291: BSplineCurve PolesCount=2 KnotsCount=2 Degree=1 IsPeriodic=0
    g292: BSplineCurve PolesCount=2 KnotsCount=2 Degree=1 IsPeriodic=0
    g293: BSplineCurve PolesCount=2 KnotsCount=2 Degree=1 IsPeriodic=0
    g294: BSplineCurve PolesCount=2 KnotsCount=2 Degree=1 IsPeriodic=0
    g295: BSplineCurve PolesCount=2 KnotsCount=2 Degree=1 IsPeriodic=0
    g296: BSplineCurve PolesCount=2 KnotsCount=2 Degree=1 IsPeriodic=0
    g297: BSplineCurve PolesCount=2 KnotsCount=2 Degree=1 IsPeriodic=0
    g298: BSplineCurve PolesCount=2 KnotsCount=2 Degree=1 IsPeriodic=0
    g299: BSplineCurve PolesCount=2 KnotsCount=2 Degree=1 IsPeriodic=0
    g300: BSplineCurve PolesCount=2 KnotsCount=2 Degree=1 IsPeriodic=0
    g301: BSplineCurve PolesCount=2 KnotsCount=2 Degree=1 IsPeriodic=0
    g302: BSplineCurve PolesCount=2 KnotsCount=2 Degree=1 IsPeriodic=0
    g303: BSplineCurve PolesCount=2 KnotsCount=2 Degree=1 IsPeriodic=0
    g304: BSplineCurve PolesCount=2 KnotsCount=2 Degree=1 IsPeriodic=0
    g305: BSplineCurve PolesCount=2 KnotsCount=2 Degree=1 IsPeriodic=0
    g306: BSplineCurve PolesCount=2 KnotsCount=2 Degree=1 IsPeriodic=0
    g307: BSplineCurve PolesCount=2 KnotsCount=2 Degree=1 IsPeriodic=0
    g308: BSplineCurve PolesCount=2 KnotsCount=2 Degree=1 IsPeriodic=0
    g309: BSplineCurve PolesCount=2 KnotsCount=2 Degree=1 IsPeriodic=0
    g310: BSplineCurve PolesCount=2 KnotsCount=2 Degree=1 IsPeriodic=0
    g311: BSplineCurve PolesCount=2 KnotsCount=2 Degree=1 IsPeriodic=0
    g312: BSplineCurve PolesCount=2 KnotsCount=2 Degree=1 IsPeriodic=0
    g313: BSplineCurve PolesCount=2 KnotsCount=2 Degree=1 IsPeriodic=0
    g314: BSplineCurve PolesCount=2 KnotsCount=2 Degree=1 IsPeriodic=0
    g315: BSplineCurve PolesCount=2 KnotsCount=2 Degree=1 IsPeriodic=0
    g316: BSplineCurve PolesCount=2 KnotsCount=2 Degree=1 IsPeriodic=0
    g317: BSplineCurve PolesCount=2 KnotsCount=2 Degree=1 IsPeriodic=0
    g318: BSplineCurve PolesCount=2 KnotsCount=2 Degree=1 IsPeriodic=0
    g319: BSplineCurve PolesCount=2 KnotsCount=2 Degree=1 IsPeriodic=0
    g320: BSplineCurve PolesCount=2 KnotsCount=2 Degree=1 IsPeriodic=0
    g321: BSplineCurve PolesCount=2 KnotsCount=2 Degree=1 IsPeriodic=0
    g322: BSplineCurve PolesCount=2 KnotsCount=2 Degree=1 IsPeriodic=0
    g323: BSplineCurve PolesCount=2 KnotsCount=2 Degree=1 IsPeriodic=0
    g324: BSplineCurve PolesCount=2 KnotsCount=2 Degree=1 IsPeriodic=0
    g325: BSplineCurve PolesCount=2 KnotsCount=2 Degree=1 IsPeriodic=0
    g326: BSplineCurve PolesCount=2 KnotsCount=2 Degree=1 IsPeriodic=0
    g327: BSplineCurve PolesCount=2 KnotsCount=2 Degree=1 IsPeriodic=0
    g328: BSplineCurve PolesCount=2 KnotsCount=2 Degree=1 IsPeriodic=0
    g329: BSplineCurve PolesCount=2 KnotsCount=2 Degree=1 IsPeriodic=0
    g330: BSplineCurve PolesCount=2 KnotsCount=2 Degree=1 IsPeriodic=0
    g331: BSplineCurve PolesCount=2 KnotsCount=2 Degree=1 IsPeriodic=0
    g332: BSplineCurve PolesCount=2 KnotsCount=2 Degree=1 IsPeriodic=0
    g333: BSplineCurve PolesCount=2 KnotsCount=2 Degree=1 IsPeriodic=0
    g334: BSplineCurve PolesCount=2 KnotsCount=2 Degree=1 IsPeriodic=0
    g335: BSplineCurve PolesCount=2 KnotsCount=2 Degree=1 IsPeriodic=0
    g336: BSplineCurve PolesCount=2 KnotsCount=2 Degree=1 IsPeriodic=0
    g337: BSplineCurve PolesCount=2 KnotsCount=2 Degree=1 IsPeriodic=0
    g338: BSplineCurve PolesCount=2 KnotsCount=2 Degree=1 IsPeriodic=0
    g339: BSplineCurve PolesCount=2 KnotsCount=2 Degree=1 IsPeriodic=0
    g340: BSplineCurve PolesCount=2 KnotsCount=2 Degree=1 IsPeriodic=0
    g341: BSplineCurve PolesCount=2 KnotsCount=2 Degree=1 IsPeriodic=0
    g342: BSplineCurve PolesCount=2 KnotsCount=2 Degree=1 IsPeriodic=0
    g343: BSplineCurve PolesCount=2 KnotsCount=2 Degree=1 IsPeriodic=0
    g344: BSplineCurve PolesCount=2 KnotsCount=2 Degree=1 IsPeriodic=0
    g345: BSplineCurve PolesCount=2 KnotsCount=2 Degree=1 IsPeriodic=0
    g346: BSplineCurve PolesCount=2 KnotsCount=2 Degree=1 IsPeriodic=0
    g347: BSplineCurve PolesCount=2 KnotsCount=2 Degree=1 IsPeriodic=0
    g348: BSplineCurve PolesCount=2 KnotsCount=2 Degree=1 IsPeriodic=0
    g349: BSplineCurve PolesCount=2 KnotsCount=2 Degree=1 IsPeriodic=0
    g350: BSplineCurve PolesCount=2 KnotsCount=2 Degree=1 IsPeriodic=0
    g351: BSplineCurve PolesCount=2 KnotsCount=2 Degree=1 IsPeriodic=0
    g352: BSplineCurve PolesCount=2 KnotsCount=2 Degree=1 IsPeriodic=0
    g353: BSplineCurve PolesCount=2 KnotsCount=2 Degree=1 IsPeriodic=0
    g354: BSplineCurve PolesCount=2 KnotsCount=2 Degree=1 IsPeriodic=0
    g355: BSplineCurve PolesCount=2 KnotsCount=2 Degree=1 IsPeriodic=0
    g356: BSplineCurve PolesCount=2 KnotsCount=2 Degree=1 IsPeriodic=0
    g357: BSplineCurve PolesCount=2 KnotsCount=2 Degree=1 IsPeriodic=0
    g358: BSplineCurve PolesCount=2 KnotsCount=2 Degree=1 IsPeriodic=0
    g359: BSplineCurve PolesCount=2 KnotsCount=2 Degree=1 IsPeriodic=0
    g360: BSplineCurve PolesCount=2 KnotsCount=2 Degree=1 IsPeriodic=0
    g361: BSplineCurve PolesCount=2 KnotsCount=2 Degree=1 IsPeriodic=0
    g362: BSplineCurve PolesCount=2 KnotsCount=2 Degree=1 IsPeriodic=0
    g363: BSplineCurve PolesCount=2 KnotsCount=2 Degree=1 IsPeriodic=0
    g364: BSplineCurve PolesCount=2 KnotsCount=2 Degree=1 IsPeriodic=0
    g365: BSplineCurve PolesCount=2 KnotsCount=2 Degree=1 IsPeriodic=0
    g366: BSplineCurve PolesCount=2 KnotsCount=2 Degree=1 IsPeriodic=0
    g367: BSplineCurve PolesCount=2 KnotsCount=2 Degree=1 IsPeriodic=0
    g368: BSplineCurve PolesCount=2 KnotsCount=2 Degree=1 IsPeriodic=0
    g369: BSplineCurve PolesCount=2 KnotsCount=2 Degree=1 IsPeriodic=0
    g370: BSplineCurve PolesCount=2 KnotsCount=2 Degree=1 IsPeriodic=0
    g371: BSplineCurve PolesCount=2 KnotsCount=2 Degree=1 IsPeriodic=0
    g372: BSplineCurve PolesCount=2 KnotsCount=2 Degree=1 IsPeriodic=0
    g373: BSplineCurve PolesCount=2 KnotsCount=2 Degree=1 IsPeriodic=0
    g374: BSplineCurve PolesCount=2 KnotsCount=2 Degree=1 IsPeriodic=0
    g375: BSplineCurve PolesCount=2 KnotsCount=2 Degree=1 IsPeriodic=0
    g376: BSplineCurve PolesCount=2 KnotsCount=2 Degree=1 IsPeriodic=0
    g377: BSplineCurve PolesCount=2 KnotsCount=2 Degree=1 IsPeriodic=0
    g378: BSplineCurve PolesCount=2 KnotsCount=2 Degree=1 IsPeriodic=0
    g379: BSplineCurve PolesCount=2 KnotsCount=2 Degree=1 IsPeriodic=0
    g380: BSplineCurve PolesCount=2 KnotsCount=2 Degree=1 IsPeriodic=0
    g381: BSplineCurve PolesCount=2 KnotsCount=2 Degree=1 IsPeriodic=0
    g382: BSplineCurve PolesCount=2 KnotsCount=2 Degree=1 IsPeriodic=0
    g383: BSplineCurve PolesCount=2 KnotsCount=2 Degree=1 IsPeriodic=0
    g384: BSplineCurve PolesCount=2 KnotsCount=2 Degree=1 IsPeriodic=0
    g385: BSplineCurve PolesCount=2 KnotsCount=2 Degree=1 IsPeriodic=0
    g386: BSplineCurve PolesCount=2 KnotsCount=2 Degree=1 IsPeriodic=0
    g387: BSplineCurve PolesCount=2 KnotsCount=2 Degree=1 IsPeriodic=0
    g388: BSplineCurve PolesCount=2 KnotsCount=2 Degree=1 IsPeriodic=0
    g389: BSplineCurve PolesCount=2 KnotsCount=2 Degree=1 IsPeriodic=0
    g390: BSplineCurve PolesCount=2 KnotsCount=2 Degree=1 IsPeriodic=0
    g391: BSplineCurve PolesCount=2 KnotsCount=2 Degree=1 IsPeriodic=0
    g392: BSplineCurve PolesCount=2 KnotsCount=2 Degree=1 IsPeriodic=0
    g393: BSplineCurve PolesCount=2 KnotsCount=2 Degree=1 IsPeriodic=0
    g394: BSplineCurve PolesCount=2 KnotsCount=2 Degree=1 IsPeriodic=0
    g395: BSplineCurve PolesCount=2 KnotsCount=2 Degree=1 IsPeriodic=0
    g396: BSplineCurve PolesCount=2 KnotsCount=2 Degree=1 IsPeriodic=0
    g397: BSplineCurve PolesCount=2 KnotsCount=2 Degree=1 IsPeriodic=0
    g398: BSplineCurve PolesCount=2 KnotsCount=2 Degree=1 IsPeriodic=0
    g399: BSplineCurve PolesCount=2 KnotsCount=2 Degree=1 IsPeriodic=0
    ... +460 more geometry lines
  constraints (860):
    c: Coincident(g0,g1)
    c: Coincident(g1,g2)
    c: Coincident(g2,g3)
    c: Coincident(g3,g4)
    c: Coincident(g4,g5)
    c: Coincident(g5,g6)
    c: Coincident(g6,g7)
    c: Coincident(g7,g8)
    c: Coincident(g8,g9)
    c: Coincident(g9,g10)
    c: Coincident(g10,g11)
    c: Coincident(g11,g12)
    c: Coincident(g12,g13)
    c: Coincident(g13,g14)
    c: Coincident(g14,g15)
    c: Coincident(g15,g16)
    c: Coincident(g16,g17)
    c: Coincident(g17,g18)
    c: Coincident(g18,g19)
    c: Coincident(g19,g20)
    c: Coincident(g20,g21)
    c: Coincident(g21,g22)
    c: Coincident(g22,g23)
    c: Coincident(g23,g24)
    c: Coincident(g24,g25)
    c: Coincident(g25,g26)
    c: Coincident(g26,g27)
    c: Coincident(g27,g28)
    c: Coincident(g28,g29)
    c: Coincident(g29,g30)
    c: Coincident(g30,g31)
    c: Coincident(g31,g32)
    c: Coincident(g32,g33)
    c: Coincident(g33,g34)
    c: Coincident(g34,g35)
    c: Coincident(g35,g36)
    c: Coincident(g36,g37)
    c: Coincident(g37,g38)
    c: Coincident(g38,g39)
    c: Coincident(g39,g40)
    c: Coincident(g40,g41)
    c: Coincident(g41,g42)
    c: Coincident(g42,g43)
    c: Coincident(g43,g44)
    c: Coincident(g44,g45)
    c: Coincident(g45,g46)
    c: Coincident(g46,g47)
    c: Coincident(g47,g48)
    c: Coincident(g48,g49)
    c: Coincident(g49,g50)
    c: Coincident(g50,g51)
    c: Coincident(g51,g52)
    c: Coincident(g52,g53)
    c: Coincident(g53,g54)
    c: Coincident(g54,g55)
    c: Coincident(g55,g56)
    c: Coincident(g56,g57)
    c: Coincident(g57,g58)
    c: Coincident(g58,g59)
    c: Coincident(g59,g60)
    c: Coincident(g60,g61)
    c: Coincident(g61,g62)
    c: Coincident(g62,g63)
    c: Coincident(g63,g64)
    c: Coincident(g64,g65)
    c: Coincident(g65,g66)
    c: Coincident(g66,g67)
    c: Coincident(g67,g68)
    c: Coincident(g68,g69)
    c: Coincident(g69,g70)
    c: Coincident(g70,g71)
    c: Coincident(g71,g72)
    c: Coincident(g72,g73)
    c: Coincident(g73,g74)
    c: Coincident(g74,g75)
    c: Coincident(g75,g76)
    c: Coincident(g76,g77)
    c: Coincident(g77,g78)
    c: Coincident(g78,g79)
    c: Coincident(g79,g80)
    c: Coincident(g80,g81)
    c: Coincident(g81,g82)
    c: Coincident(g82,g83)
    c: Coincident(g83,g84)
    c: Coincident(g84,g85)
    c: Coincident(g85,g86)
    c: Coincident(g86,g87)
    c: Coincident(g87,g0)
    c: Coincident(g88,g89)
    c: Coincident(g89,g90)
    c: Coincident(g90,g91)
    c: Coincident(g91,g92)
    c: Coincident(g92,g93)
    c: Coincident(g93,g94)
    c: Coincident(g94,g95)
    c: Coincident(g95,g96)
    c: Coincident(g96,g97)
    c: Coincident(g97,g98)
    c: Coincident(g98,g99)
    c: Coincident(g99,g100)
    c: Coincident(g100,g101)
    c: Coincident(g101,g102)
    c: Coincident(g102,g103)
    c: Coincident(g103,g104)
    c: Coincident(g104,g105)
    c: Coincident(g105,g106)
    c: Coincident(g106,g107)
    c: Coincident(g107,g108)
    c: Coincident(g108,g109)
    c: Coincident(g109,g110)
    c: Coincident(g110,g111)
    c: Coincident(g111,g112)
    c: Coincident(g112,g113)
    c: Coincident(g113,g114)
    c: Coincident(g114,g115)
    c: Coincident(g115,g116)
    c: Coincident(g116,g117)
    c: Coincident(g117,g118)
    c: Coincident(g118,g119)
    c: Coincident(g119,g120)
    c: Coincident(g120,g121)
    c: Coincident(g121,g122)
    c: Coincident(g122,g123)
    c: Coincident(g123,g124)
    c: Coincident(g124,g125)
    c: Coincident(g125,g126)
    c: Coincident(g126,g127)
    c: Coincident(g127,g88)
    c: Coincident(g128,g129)
    c: Coincident(g129,g130)
    c: Coincident(g130,g131)
    c: Coincident(g131,g132)
    c: Coincident(g132,g133)
    c: Coincident(g133,g134)
    c: Coincident(g134,g135)
    c: Coincident(g135,g136)
    c: Coincident(g136,g137)
    c: Coincident(g137,g138)
    c: Coincident(g138,g139)
    c: Coincident(g139,g140)
    c: Coincident(g140,g141)
    c: Coincident(g141,g142)
    c: Coincident(g142,g143)
    c: Coincident(g143,g144)
    c: Coincident(g144,g145)
    c: Coincident(g145,g146)
    c: Coincident(g146,g147)
    c: Coincident(g147,g148)
    c: Coincident(g148,g149)
    c: Coincident(g149,g150)
    c: Coincident(g150,g151)
    c: Coincident(g151,g152)
    c: Coincident(g152,g153)
    c: Coincident(g153,g154)
    c: Coincident(g154,g155)
    c: Coincident(g155,g156)
    c: Coincident(g156,g157)
    c: Coincident(g157,g158)
    c: Coincident(g158,g159)
    c: Coincident(g159,g160)
    c: Coincident(g160,g161)
    c: Coincident(g161,g162)
    c: Coincident(g162,g163)
    c: Coincident(g163,g164)
    c: Coincident(g164,g165)
    c: Coincident(g165,g166)
    c: Coincident(g166,g167)
    c: Coincident(g167,g168)
    c: Coincident(g168,g169)
    c: Coincident(g169,g170)
    c: Coincident(g170,g171)
    c: Coincident(g171,g172)
    c: Coincident(g172,g173)
    c: Coincident(g173,g174)
    c: Coincident(g174,g175)
    c: Coincident(g175,g176)
    c: Coincident(g176,g177)
    c: Coincident(g177,g178)
    c: Coincident(g178,g179)
    c: Coincident(g179,g180)
    c: Coincident(g180,g181)
    c: Coincident(g181,g182)
    c: Coincident(g182,g183)
    c: Coincident(g183,g184)
    c: Coincident(g184,g185)
    c: Coincident(g185,g186)
    c: Coincident(g186,g187)
    c: Coincident(g187,g188)
    c: Coincident(g188,g189)
    c: Coincident(g189,g190)
    c: Coincident(g190,g191)
    c: Coincident(g191,g192)
    c: Coincident(g192,g193)
    c: Coincident(g193,g194)
    c: Coincident(g194,g195)
    c: Coincident(g195,g196)
    c: Coincident(g196,g197)
    c: Coincident(g197,g198)
    c: Coincident(g198,g199)
    c: Coincident(g199,g200)
    c: Coincident(g200,g201)
    c: Coincident(g201,g202)
    c: Coincident(g202,g203)
    c: Coincident(g203,g204)
    c: Coincident(g204,g205)
    c: Coincident(g205,g206)
    c: Coincident(g206,g207)
    c: Coincident(g207,g208)
    c: Coincident(g208,g209)
    c: Coincident(g209,g210)
    c: Coincident(g210,g211)
    c: Coincident(g211,g212)
    c: Coincident(g212,g213)
    c: Coincident(g213,g214)
    c: Coincident(g214,g215)
    c: Coincident(g215,g216)
    c: Coincident(g216,g217)
    c: Coincident(g217,g218)
    c: Coincident(g218,g219)
    c: Coincident(g219,g220)
    c: Coincident(g220,g221)
    c: Coincident(g221,g222)
    c: Coincident(g222,g223)
    c: Coincident(g223,g224)
    c: Coincident(g224,g225)
    c: Coincident(g225,g226)
    c: Coincident(g226,g227)
    c: Coincident(g227,g228)
    c: Coincident(g228,g229)
    c: Coincident(g229,g230)
    c: Coincident(g230,g231)
    c: Coincident(g231,g232)
    c: Coincident(g232,g233)
    c: Coincident(g233,g234)
    c: Coincident(g234,g235)
    c: Coincident(g235,g236)
    c: Coincident(g236,g237)
    c: Coincident(g237,g238)
    c: Coincident(g238,g239)
    c: Coincident(g239,g128)
    c: Coincident(g240,g241)
    c: Coincident(g241,g242)
    c: Coincident(g242,g243)
    c: Coincident(g243,g244)
    c: Coincident(g244,g245)
    c: Coincident(g245,g246)
    c: Coincident(g246,g247)
    c: Coincident(g247,g248)
    c: Coincident(g248,g249)
    c: Coincident(g249,g250)
    c: Coincident(g250,g251)
    c: Coincident(g251,g252)
    c: Coincident(g252,g253)
    c: Coincident(g253,g254)
    c: Coincident(g254,g255)
    c: Coincident(g255,g256)
    c: Coincident(g256,g257)
    c: Coincident(g257,g258)
    c: Coincident(g258,g259)
    c: Coincident(g259,g260)
    c: Coincident(g260,g261)
    c: Coincident(g261,g262)
    c: Coincident(g262,g263)
    c: Coincident(g263,g264)
    c: Coincident(g264,g265)
    c: Coincident(g265,g266)
    c: Coincident(g266,g267)
    c: Coincident(g267,g268)
    c: Coincident(g268,g269)
    c: Coincident(g269,g270)
    c: Coincident(g270,g271)
    c: Coincident(g271,g272)
    c: Coincident(g272,g273)
    c: Coincident(g273,g274)
    c: Coincident(g274,g275)
    c: Coincident(g275,g276)
    c: Coincident(g276,g277)
    c: Coincident(g277,g278)
    c: Coincident(g278,g279)
    c: Coincident(g279,g280)
    c: Coincident(g280,g281)
    c: Coincident(g281,g282)
    c: Coincident(g282,g283)
    c: Coincident(g283,g284)
    c: Coincident(g284,g285)
    c: Coincident(g285,g286)
    c: Coincident(g286,g287)
    c: Coincident(g287,g240)
    c: Coincident(g288,g289)
    c: Coincident(g289,g290)
    c: Coincident(g290,g291)
    c: Coincident(g291,g292)
    c: Coincident(g292,g293)
    c: Coincident(g293,g294)
    c: Coincident(g294,g295)
    c: Coincident(g295,g296)
    c: Coincident(g296,g297)
    c: Coincident(g297,g298)
    c: Coincident(g298,g299)
    c: Coincident(g299,g300)
    c: Coincident(g300,g301)
    c: Coincident(g301,g302)
    c: Coincident(g302,g303)
    c: Coincident(g303,g304)
    c: Coincident(g304,g305)
    c: Coincident(g305,g306)
    c: Coincident(g306,g307)
    c: Coincident(g307,g308)
    c: Coincident(g308,g309)
    c: Coincident(g309,g310)
    c: Coincident(g310,g311)
    c: Coincident(g311,g288)
    c: Coincident(g312,g313)
    c: Coincident(g313,g314)
    c: Coincident(g314,g315)
    c: Coincident(g315,g316)
    c: Coincident(g316,g317)
    c: Coincident(g317,g318)
    c: Coincident(g318,g319)
    c: Coincident(g319,g320)
    c: Coincident(g320,g321)
    c: Coincident(g321,g322)
    c: Coincident(g322,g323)
    c: Coincident(g323,g324)
    c: Coincident(g324,g325)
    c: Coincident(g325,g326)
    c: Coincident(g326,g327)
    c: Coincident(g327,g312)
    c: Coincident(g328,g329)
    c: Coincident(g329,g330)
    c: Coincident(g330,g331)
    c: Coincident(g331,g332)
    c: Coincident(g332,g333)
    c: Coincident(g333,g334)
    c: Coincident(g334,g335)
    c: Coincident(g335,g336)
    c: Coincident(g336,g337)
    c: Coincident(g337,g338)
    c: Coincident(g338,g339)
    c: Coincident(g339,g340)
    c: Coincident(g340,g341)
    c: Coincident(g341,g342)
    c: Coincident(g342,g343)
    c: Coincident(g343,g344)
    c: Coincident(g344,g345)
    c: Coincident(g345,g346)
    c: Coincident(g346,g347)
    c: Coincident(g347,g348)
    c: Coincident(g348,g349)
    c: Coincident(g349,g350)
    c: Coincident(g350,g351)
    c: Coincident(g351,g352)
    c: Coincident(g352,g353)
    c: Coincident(g353,g354)
    c: Coincident(g354,g355)
    c: Coincident(g355,g356)
    c: Coincident(g356,g357)
    c: Coincident(g357,g358)
    c: Coincident(g358,g359)
    c: Coincident(g359,g360)
    c: Coincident(g360,g361)
    c: Coincident(g361,g362)
    c: Coincident(g362,g363)
    c: Coincident(g363,g364)
    c: Coincident(g364,g365)
    c: Coincident(g365,g366)
    c: Coincident(g366,g367)
    c: Coincident(g367,g368)
    c: Coincident(g368,g369)
    c: Coincident(g369,g370)
    c: Coincident(g370,g371)
    c: Coincident(g371,g372)
    c: Coincident(g372,g373)
    c: Coincident(g373,g374)
    c: Coincident(g374,g375)
    c: Coincident(g375,g376)
    c: Coincident(g376,g377)
    c: Coincident(g377,g378)
    c: Coincident(g378,g379)
    c: Coincident(g379,g380)
    c: Coincident(g380,g381)
    c: Coincident(g381,g382)
    c: Coincident(g382,g383)
    c: Coincident(g383,g384)
    c: Coincident(g384,g385)
    c: Coincident(g385,g386)
    c: Coincident(g386,g387)
    c: Coincident(g387,g388)
    c: Coincident(g388,g389)
    c: Coincident(g389,g390)
    c: Coincident(g390,g391)
    c: Coincident(g391,g392)
    c: Coincident(g392,g393)
    c: Coincident(g393,g394)
    c: Coincident(g394,g395)
    c: Coincident(g395,g396)
    c: Coincident(g396,g397)
    c: Coincident(g397,g398)
    c: Coincident(g398,g399)
    c: Coincident(g399,g328)
    c: Coincident(g400,g401)
    c: Coincident(g401,g402)
    c: Coincident(g402,g403)
    c: Coincident(g403,g404)
    c: Coincident(g404,g405)
    c: Coincident(g405,g406)
    c: Coincident(g406,g407)
    c: Coincident(g407,g408)
    c: Coincident(g408,g409)
    c: Coincident(g409,g410)
    c: Coincident(g410,g411)
    c: Coincident(g411,g412)
    c: Coincident(g412,g413)
    c: Coincident(g413,g414)
    c: Coincident(g414,g415)
    c: Coincident(g415,g416)
    c: Coincident(g416,g417)
    c: Coincident(g417,g418)
    c: Coincident(g418,g419)
    c: Coincident(g419,g420)
    c: Coincident(g420,g421)
    c: Coincident(g421,g422)
    c: Coincident(g422,g423)
    c: Coincident(g423,g400)
    c: Coincident(g424,g425)
    c: Coincident(g425,g426)
    c: Coincident(g426,g427)
    c: Coincident(g427,g428)
    c: Coincident(g428,g429)
    c: Coincident(g429,g430)
    c: Coincident(g430,g431)
    c: Coincident(g431,g432)
    c: Coincident(g432,g433)
    c: Coincident(g433,g434)
    c: Coincident(g434,g435)
    c: Coincident(g435,g436)
    c: Coincident(g436,g437)
    c: Coincident(g437,g438)
    c: Coincident(g438,g439)
    c: Coincident(g439,g440)
    c: Coincident(g440,g441)
    c: Coincident(g441,g442)
    c: Coincident(g442,g443)
    c: Coincident(g443,g444)
    c: Coincident(g444,g445)
    c: Coincident(g445,g446)
    c: Coincident(g446,g447)
    c: Coincident(g447,g448)
    c: Coincident(g448,g449)
    c: Coincident(g449,g450)
    c: Coincident(g450,g451)
    c: Coincident(g451,g452)
    c: Coincident(g452,g453)
    c: Coincident(g453,g454)
    c: Coincident(g454,g455)
    c: Coincident(g455,g456)
    c: Coincident(g456,g457)
    c: Coincident(g457,g458)
    c: Coincident(g458,g459)
    c: Coincident(g459,g460)
    c: Coincident(g460,g461)
    c: Coincident(g461,g462)
    c: Coincident(g462,g463)
    c: Coincident(g463,g464)
    c: Coincident(g464,g465)
    c: Coincident(g465,g466)
    c: Coincident(g466,g467)
    c: Coincident(g467,g468)
    c: Coincident(g468,g469)
    c: Coincident(g469,g470)
    c: Coincident(g470,g471)
    c: Coincident(g471,g472)
    c: Coincident(g472,g473)
    c: Coincident(g473,g474)
    c: Coincident(g474,g475)
    c: Coincident(g475,g476)
    c: Coincident(g476,g477)
    c: Coincident(g477,g478)
    c: Coincident(g478,g479)
    c: Coincident(g479,g424)
    c: Coincident(g480,g481)
    c: Coincident(g481,g482)
    c: Coincident(g482,g483)
    c: Coincident(g483,g484)
    c: Coincident(g484,g485)
    c: Coincident(g485,g486)
    c: Coincident(g486,g487)
    c: Coincident(g487,g488)
    c: Coincident(g488,g489)
    c: Coincident(g489,g490)
    c: Coincident(g490,g491)
    c: Coincident(g491,g492)
    c: Coincident(g492,g493)
    c: Coincident(g493,g494)
    c: Coincident(g494,g495)
    c: Coincident(g495,g480)
    c: Coincident(g496,g497)
    c: Coincident(g497,g498)
    c: Coincident(g498,g499)
    c: Coincident(g499,g500)
    c: Coincident(g500,g501)
    c: Coincident(g501,g502)
    c: Coincident(g502,g503)
    c: Coincident(g503,g504)
    c: Coincident(g504,g505)
    c: Coincident(g505,g506)
    c: Coincident(g506,g507)
    c: Coincident(g507,g508)
    c: Coincident(g508,g509)
    c: Coincident(g509,g510)
    c: Coincident(g510,g511)
    c: Coincident(g511,g512)
    c: Coincident(g512,g513)
    c: Coincident(g513,g514)
    c: Coincident(g514,g515)
    c: Coincident(g515,g516)
    c: Coincident(g516,g517)
    c: Coincident(g517,g518)
    c: Coincident(g518,g519)
    c: Coincident(g519,g520)
    c: Coincident(g520,g521)
    c: Coincident(g521,g522)
    c: Coincident(g522,g523)
    c: Coincident(g523,g524)
    c: Coincident(g524,g525)
    c: Coincident(g525,g526)
    c: Coincident(g526,g527)
    c: Coincident(g527,g528)
    c: Coincident(g528,g529)
    c: Coincident(g529,g530)
    c: Coincident(g530,g531)
    c: Coincident(g531,g532)
    c: Coincident(g532,g533)
    c: Coincident(g533,g534)
    c: Coincident(g534,g535)
    c: Coincident(g535,g496)
    c: Coincident(g536,g537)
    c: Coincident(g537,g538)
    c: Coincident(g538,g539)
    c: Coincident(g539,g540)
    c: Coincident(g540,g541)
    c: Coincident(g541,g542)
    c: Coincident(g542,g543)
    c: Coincident(g543,g544)
    c: Coincident(g544,g545)
    c: Coincident(g545,g546)
    c: Coincident(g546,g547)
    c: Coincident(g547,g548)
    c: Coincident(g548,g549)
    c: Coincident(g549,g550)
    c: Coincident(g550,g551)
    c: Coincident(g551,g552)
    c: Coincident(g552,g553)
    c: Coincident(g553,g554)
    c: Coincident(g554,g555)
    c: Coincident(g555,g556)
    c: Coincident(g556,g557)
    c: Coincident(g557,g558)
    c: Coincident(g558,g559)
    c: Coincident(g559,g560)
    c: Coincident(g560,g561)
    c: Coincident(g561,g562)
    c: Coincident(g562,g563)
    c: Coincident(g563,g564)
    c: Coincident(g564,g565)
    c: Coincident(g565,g566)
    c: Coincident(g566,g567)
    c: Coincident(g567,g568)
    c: Coincident(g568,g569)
    c: Coincident(g569,g570)
    c: Coincident(g570,g571)
    c: Coincident(g571,g572)
    c: Coincident(g572,g573)
    c: Coincident(g573,g574)
    c: Coincident(g574,g575)
    c: Coincident(g575,g536)
    c: Coincident(g576,g577)
    c: Coincident(g577,g578)
    c: Coincident(g578,g579)
    c: Coincident(g579,g580)
    c: Coincident(g580,g581)
    c: Coincident(g581,g582)
    c: Coincident(g582,g583)
    c: Coincident(g583,g584)
    c: Coincident(g584,g585)
    c: Coincident(g585,g586)
    c: Coincident(g586,g587)
    c: Coincident(g587,g576)
    c: Coincident(g588,g589)
    c: Coincident(g589,g590)
    c: Coincident(g590,g591)
    c: Coincident(g591,g592)
    c: Coincident(g592,g593)
    c: Coincident(g593,g594)
    c: Coincident(g594,g595)
    c: Coincident(g595,g596)
    c: Coincident(g596,g597)
    c: Coincident(g597,g598)
    c: Coincident(g598,g599)
    c: Coincident(g599,g600)
    c: Coincident(g600,g601)
    c: Coincident(g601,g602)
    c: Coincident(g602,g603)
    c: Coincident(g603,g604)
    c: Coincident(g604,g605)
    c: Coincident(g605,g606)
    c: Coincident(g606,g607)
    c: Coincident(g607,g608)
    c: Coincident(g608,g609)
    c: Coincident(g609,g610)
    c: Coincident(g610,g611)
    c: Coincident(g611,g612)
    c: Coincident(g612,g613)
    c: Coincident(g613,g614)
    c: Coincident(g614,g615)
    c: Coincident(g615,g616)
    c: Coincident(g616,g617)
    c: Coincident(g617,g618)
    c: Coincident(g618,g619)
    c: Coincident(g619,g620)
    c: Coincident(g620,g621)
    c: Coincident(g621,g622)
    c: Coincident(g622,g623)
    c: Coincident(g623,g624)
    c: Coincident(g624,g625)
    c: Coincident(g625,g626)
    c: Coincident(g626,g627)
    c: Coincident(g627,g628)
    c: Coincident(g628,g629)
    c: Coincident(g629,g630)
    c: Coincident(g630,g631)
    c: Coincident(g631,g632)
    c: Coincident(g632,g633)
    c: Coincident(g633,g634)
    c: Coincident(g634,g635)
    c: Coincident(g635,g636)
    c: Coincident(g636,g637)
    c: Coincident(g637,g638)
    c: Coincident(g638,g639)
    c: Coincident(g639,g640)
    c: Coincident(g640,g641)
    c: Coincident(g641,g642)
    c: Coincident(g642,g643)
    c: Coincident(g643,g644)
    c: Coincident(g644,g645)
    c: Coincident(g645,g646)
    c: Coincident(g646,g647)
    c: Coincident(g647,g648)
    c: Coincident(g648,g649)
    c: Coincident(g649,g650)
    c: Coincident(g650,g651)
    c: Coincident(g651,g652)
    c: Coincident(g652,g653)
    c: Coincident(g653,g654)
    c: Coincident(g654,g655)
    c: Coincident(g655,g656)
    c: Coincident(g656,g657)
    c: Coincident(g657,g658)
    c: Coincident(g658,g659)
    c: Coincident(g659,g660)
    c: Coincident(g660,g661)
    c: Coincident(g661,g662)
    c: Coincident(g662,g663)
    c: Coincident(g663,g664)
    c: Coincident(g664,g665)
    c: Coincident(g665,g666)
    c: Coincident(g666,g667)
    c: Coincident(g667,g668)
    c: Coincident(g668,g669)
    c: Coincident(g669,g670)
    c: Coincident(g670,g671)
    c: Coincident(g671,g672)
    c: Coincident(g672,g673)
    c: Coincident(g673,g674)
    c: Coincident(g674,g675)
    c: Coincident(g675,g588)
    c: Coincident(g676,g677)
    c: Coincident(g677,g678)
    c: Coincident(g678,g679)
    c: Coincident(g679,g680)
    c: Coincident(g680,g681)
    c: Coincident(g681,g682)
    c: Coincident(g682,g683)
    c: Coincident(g683,g684)
    c: Coincident(g684,g685)
    c: Coincident(g685,g686)
    c: Coincident(g686,g687)
    c: Coincident(g687,g688)
    c: Coincident(g688,g689)
    c: Coincident(g689,g690)
    c: Coincident(g690,g691)
    c: Coincident(g691,g676)
    c: Coincident(g692,g693)
    c: Coincident(g693,g694)
    c: Coincident(g694,g695)
    c: Coincident(g695,g696)
    c: Coincident(g696,g697)
    c: Coincident(g697,g698)
    c: Coincident(g698,g699)
    c: Coincident(g699,g700)
    c: Coincident(g700,g701)
    c: Coincident(g701,g702)
    c: Coincident(g702,g703)
    c: Coincident(g703,g704)
    c: Coincident(g704,g705)
    c: Coincident(g705,g706)
    c: Coincident(g706,g707)
    c: Coincident(g707,g708)
    c: Coincident(g708,g709)
    c: Coincident(g709,g710)
    c: Coincident(g710,g711)
    c: Coincident(g711,g712)
    c: Coincident(g712,g713)
    c: Coincident(g713,g714)
    c: Coincident(g714,g715)
    c: Coincident(g715,g716)
    c: Coincident(g716,g717)
    c: Coincident(g717,g718)
    c: Coincident(g718,g719)
    c: Coincident(g719,g720)
    c: Coincident(g720,g721)
    c: Coincident(g721,g722)
    c: Coincident(g722,g723)
    c: Coincident(g723,g724)
    c: Coincident(g724,g725)
    c: Coincident(g725,g726)
    c: Coincident(g726,g727)
    c: Coincident(g727,g728)
    c: Coincident(g728,g729)
    c: Coincident(g729,g730)
    c: Coincident(g730,g731)
    c: Coincident(g731,g692)
    c: Coincident(g732,g733)
    c: Coincident(g733,g734)
    c: Coincident(g734,g735)
    c: Coincident(g735,g736)
    c: Coincident(g736,g737)
    c: Coincident(g737,g738)
    c: Coincident(g738,g739)
    c: Coincident(g739,g740)
    c: Coincident(g740,g741)
    c: Coincident(g741,g742)
    c: Coincident(g742,g743)
    c: Coincident(g743,g744)
    c: Coincident(g744,g745)
    c: Coincident(g745,g746)
    c: Coincident(g746,g747)
    c: Coincident(g747,g748)
    c: Coincident(g748,g749)
    c: Coincident(g749,g750)
    c: Coincident(g750,g751)
    c: Coincident(g751,g752)
    c: Coincident(g752,g753)
    c: Coincident(g753,g754)
    c: Coincident(g754,g755)
    c: Coincident(g755,g756)
    c: Coincident(g756,g757)
    c: Coincident(g757,g758)
    c: Coincident(g758,g759)
    c: Coincident(g759,g760)
    c: Coincident(g760,g761)
    c: Coincident(g761,g762)
    c: Coincident(g762,g763)
    c: Coincident(g763,g732)
    c: Coincident(g764,g765)
    c: Coincident(g765,g766)
    c: Coincident(g766,g767)
    c: Coincident(g767,g768)
    c: Coincident(g768,g769)
    c: Coincident(g769,g770)
    c: Coincident(g770,g771)
    c: Coincident(g771,g772)
    c: Coincident(g772,g773)
    c: Coincident(g773,g774)
    c: Coincident(g774,g775)
    c: Coincident(g775,g776)
    c: Coincident(g776,g777)
    c: Coincident(g777,g778)
    c: Coincident(g778,g779)
    c: Coincident(g779,g780)
    c: Coincident(g780,g781)
    c: Coincident(g781,g782)
    c: Coincident(g782,g783)
    c: Coincident(g783,g784)
    c: Coincident(g784,g785)
    c: Coincident(g785,g786)
    c: Coincident(g786,g787)
    c: Coincident(g787,g764)
    c: Coincident(g788,g789)
    c: Coincident(g789,g790)
    c: Coincident(g790,g791)
    c: Coincident(g791,g792)
    c: Coincident(g792,g793)
    c: Coincident(g793,g794)
    c: Coincident(g794,g795)
    c: Coincident(g795,g796)
    c: Coincident(g796,g797)
    c: Coincident(g797,g798)
    c: Coincident(g798,g799)
    c: Coincident(g799,g800)
    c: Coincident(g800,g801)
    c: Coincident(g801,g802)
    c: Coincident(g802,g803)
    c: Coincident(g803,g804)
    c: Coincident(g804,g805)
    c: Coincident(g805,g806)
    c: Coincident(g806,g807)
    c: Coincident(g807,g808)
    c: Coincident(g808,g809)
    c: Coincident(g809,g810)
    c: Coincident(g810,g811)
    c: Coincident(g811,g812)
    c: Coincident(g812,g813)
    c: Coincident(g813,g814)
    c: Coincident(g814,g815)
    c: Coincident(g815,g816)
    c: Coincident(g816,g817)
    c: Coincident(g817,g818)
    c: Coincident(g818,g819)
    c: Coincident(g819,g820)
    c: Coincident(g820,g821)
    c: Coincident(g821,g822)
    c: Coincident(g822,g823)
    c: Coincident(g823,g824)
    c: Coincident(g824,g825)
    c: Coincident(g825,g826)
    c: Coincident(g826,g827)
    c: Coincident(g827,g828)
    c: Coincident(g828,g829)
    c: Coincident(g829,g830)
    c: Coincident(g830,g831)
    c: Coincident(g831,g832)
    c: Coincident(g832,g833)
    c: Coincident(g833,g834)
    c: Coincident(g834,g835)
    c: Coincident(g835,g836)
    c: Coincident(g836,g837)
    c: Coincident(g837,g838)
    c: Coincident(g838,g839)
    c: Coincident(g839,g840)
    c: Coincident(g840,g841)
    c: Coincident(g841,g842)
    c: Coincident(g842,g843)
    c: Coincident(g843,g844)
    c: Coincident(g844,g845)
    c: Coincident(g845,g846)
    c: Coincident(g846,g847)
    c: Coincident(g847,g848)
    c: Coincident(g848,g849)
    c: Coincident(g849,g850)
    c: Coincident(g850,g851)
    c: Coincident(g851,g852)
    c: Coincident(g852,g853)
    c: Coincident(g853,g854)
    c: Coincident(g854,g855)
    c: Coincident(g855,g856)
    c: Coincident(g856,g857)
    c: Coincident(g857,g858)
    c: Coincident(g858,g859)
    c: Coincident(g859,g788)
FEATURE [Sketcher::SketchObject] Sketch027  label="16 Bit VS008"
  FullyConstrained = false
  Placement = pos=(8.14,37.75,-10) rot=(1,0,0;3.14159rad)
  sketch-geometry (860):
    g0: BSplineCurve PolesCount=2 KnotsCount=2 Degree=1 IsPeriodic=0
    g1: BSplineCurve PolesCount=2 KnotsCount=2 Degree=1 IsPeriodic=0
    g2: BSplineCurve PolesCount=2 KnotsCount=2 Degree=1 IsPeriodic=0
    g3: BSplineCurve PolesCount=2 KnotsCount=2 Degree=1 IsPeriodic=0
    g4: BSplineCurve PolesCount=2 KnotsCount=2 Degree=1 IsPeriodic=0
    g5: BSplineCurve PolesCount=2 KnotsCount=2 Degree=1 IsPeriodic=0
    g6: BSplineCurve PolesCount=2 KnotsCount=2 Degree=1 IsPeriodic=0
    g7: BSplineCurve PolesCount=2 KnotsCount=2 Degree=1 IsPeriodic=0
    g8: BSplineCurve PolesCount=2 KnotsCount=2 Degree=1 IsPeriodic=0
    g9: BSplineCurve PolesCount=2 KnotsCount=2 Degree=1 IsPeriodic=0
    g10: BSplineCurve PolesCount=2 KnotsCount=2 Degree=1 IsPeriodic=0
    g11: BSplineCurve PolesCount=2 KnotsCount=2 Degree=1 IsPeriodic=0
    g12: BSplineCurve PolesCount=2 KnotsCount=2 Degree=1 IsPeriodic=0
    g13: BSplineCurve PolesCount=2 KnotsCount=2 Degree=1 IsPeriodic=0
    g14: BSplineCurve PolesCount=2 KnotsCount=2 Degree=1 IsPeriodic=0
    g15: BSplineCurve PolesCount=2 KnotsCount=2 Degree=1 IsPeriodic=0
    g16: BSplineCurve PolesCount=2 KnotsCount=2 Degree=1 IsPeriodic=0
    g17: BSplineCurve PolesCount=2 KnotsCount=2 Degree=1 IsPeriodic=0
    g18: BSplineCurve PolesCount=2 KnotsCount=2 Degree=1 IsPeriodic=0
    g19: BSplineCurve PolesCount=2 KnotsCount=2 Degree=1 IsPeriodic=0
    g20: BSplineCurve PolesCount=2 KnotsCount=2 Degree=1 IsPeriodic=0
    g21: BSplineCurve PolesCount=2 KnotsCount=2 Degree=1 IsPeriodic=0
    g22: BSplineCurve PolesCount=2 KnotsCount=2 Degree=1 IsPeriodic=0
    g23: BSplineCurve PolesCount=2 KnotsCount=2 Degree=1 IsPeriodic=0
    g24: BSplineCurve PolesCount=2 KnotsCount=2 Degree=1 IsPeriodic=0
    g25: BSplineCurve PolesCount=2 KnotsCount=2 Degree=1 IsPeriodic=0
    g26: BSplineCurve PolesCount=2 KnotsCount=2 Degree=1 IsPeriodic=0
    g27: BSplineCurve PolesCount=2 KnotsCount=2 Degree=1 IsPeriodic=0
    g28: BSplineCurve PolesCount=2 KnotsCount=2 Degree=1 IsPeriodic=0
    g29: BSplineCurve PolesCount=2 KnotsCount=2 Degree=1 IsPeriodic=0
    g30: BSplineCurve PolesCount=2 KnotsCount=2 Degree=1 IsPeriodic=0
    g31: BSplineCurve PolesCount=2 KnotsCount=2 Degree=1 IsPeriodic=0
    g32: BSplineCurve PolesCount=2 KnotsCount=2 Degree=1 IsPeriodic=0
    g33: BSplineCurve PolesCount=2 KnotsCount=2 Degree=1 IsPeriodic=0
    g34: BSplineCurve PolesCount=2 KnotsCount=2 Degree=1 IsPeriodic=0
    g35: BSplineCurve PolesCount=2 KnotsCount=2 Degree=1 IsPeriodic=0
    g36: BSplineCurve PolesCount=2 KnotsCount=2 Degree=1 IsPeriodic=0
    g37: BSplineCurve PolesCount=2 KnotsCount=2 Degree=1 IsPeriodic=0
    g38: BSplineCurve PolesCount=2 KnotsCount=2 Degree=1 IsPeriodic=0
    g39: BSplineCurve PolesCount=2 KnotsCount=2 Degree=1 IsPeriodic=0
    g40: BSplineCurve PolesCount=2 KnotsCount=2 Degree=1 IsPeriodic=0
    g41: BSplineCurve PolesCount=2 KnotsCount=2 Degree=1 IsPeriodic=0
    g42: BSplineCurve PolesCount=2 KnotsCount=2 Degree=1 IsPeriodic=0
    g43: BSplineCurve PolesCount=2 KnotsCount=2 Degree=1 IsPeriodic=0
    g44: BSplineCurve PolesCount=2 KnotsCount=2 Degree=1 IsPeriodic=0
    g45: BSplineCurve PolesCount=2 KnotsCount=2 Degree=1 IsPeriodic=0
    g46: BSplineCurve PolesCount=2 KnotsCount=2 Degree=1 IsPeriodic=0
    g47: BSplineCurve PolesCount=2 KnotsCount=2 Degree=1 IsPeriodic=0
    g48: BSplineCurve PolesCount=2 KnotsCount=2 Degree=1 IsPeriodic=0
    g49: BSplineCurve PolesCount=2 KnotsCount=2 Degree=1 IsPeriodic=0
    g50: BSplineCurve PolesCount=2 KnotsCount=2 Degree=1 IsPeriodic=0
    g51: BSplineCurve PolesCount=2 KnotsCount=2 Degree=1 IsPeriodic=0
    g52: BSplineCurve PolesCount=2 KnotsCount=2 Degree=1 IsPeriodic=0
    g53: BSplineCurve PolesCount=2 KnotsCount=2 Degree=1 IsPeriodic=0
    g54: BSplineCurve PolesCount=2 KnotsCount=2 Degree=1 IsPeriodic=0
    g55: BSplineCurve PolesCount=2 KnotsCount=2 Degree=1 IsPeriodic=0
    g56: BSplineCurve PolesCount=2 KnotsCount=2 Degree=1 IsPeriodic=0
    g57: BSplineCurve PolesCount=2 KnotsCount=2 Degree=1 IsPeriodic=0
    g58: BSplineCurve PolesCount=2 KnotsCount=2 Degree=1 IsPeriodic=0
    g59: BSplineCurve PolesCount=2 KnotsCount=2 Degree=1 IsPeriodic=0
    g60: BSplineCurve PolesCount=2 KnotsCount=2 Degree=1 IsPeriodic=0
    g61: BSplineCurve PolesCount=2 KnotsCount=2 Degree=1 IsPeriodic=0
    g62: BSplineCurve PolesCount=2 KnotsCount=2 Degree=1 IsPeriodic=0
    g63: BSplineCurve PolesCount=2 KnotsCount=2 Degree=1 IsPeriodic=0
    g64: BSplineCurve PolesCount=2 KnotsCount=2 Degree=1 IsPeriodic=0
    g65: BSplineCurve PolesCount=2 KnotsCount=2 Degree=1 IsPeriodic=0
    g66: BSplineCurve PolesCount=2 KnotsCount=2 Degree=1 IsPeriodic=0
    g67: BSplineCurve PolesCount=2 KnotsCount=2 Degree=1 IsPeriodic=0
    g68: BSplineCurve PolesCount=2 KnotsCount=2 Degree=1 IsPeriodic=0
    g69: BSplineCurve PolesCount=2 KnotsCount=2 Degree=1 IsPeriodic=0
    g70: BSplineCurve PolesCount=2 KnotsCount=2 Degree=1 IsPeriodic=0
    g71: BSplineCurve PolesCount=2 KnotsCount=2 Degree=1 IsPeriodic=0
    g72: BSplineCurve PolesCount=2 KnotsCount=2 Degree=1 IsPeriodic=0
    g73: BSplineCurve PolesCount=2 KnotsCount=2 Degree=1 IsPeriodic=0
    g74: BSplineCurve PolesCount=2 KnotsCount=2 Degree=1 IsPeriodic=0
    g75: BSplineCurve PolesCount=2 KnotsCount=2 Degree=1 IsPeriodic=0
    g76: BSplineCurve PolesCount=2 KnotsCount=2 Degree=1 IsPeriodic=0
    g77: BSplineCurve PolesCount=2 KnotsCount=2 Degree=1 IsPeriodic=0
    g78: BSplineCurve PolesCount=2 KnotsCount=2 Degree=1 IsPeriodic=0
    g79: BSplineCurve PolesCount=2 KnotsCount=2 Degree=1 IsPeriodic=0
    g80: BSplineCurve PolesCount=2 KnotsCount=2 Degree=1 IsPeriodic=0
    g81: BSplineCurve PolesCount=2 KnotsCount=2 Degree=1 IsPeriodic=0
    g82: BSplineCurve PolesCount=2 KnotsCount=2 Degree=1 IsPeriodic=0
    g83: BSplineCurve PolesCount=2 KnotsCount=2 Degree=1 IsPeriodic=0
    g84: BSplineCurve PolesCount=2 KnotsCount=2 Degree=1 IsPeriodic=0
    g85: BSplineCurve PolesCount=2 KnotsCount=2 Degree=1 IsPeriodic=0
    g86: BSplineCurve PolesCount=2 KnotsCount=2 Degree=1 IsPeriodic=0
    g87: BSplineCurve PolesCount=2 KnotsCount=2 Degree=1 IsPeriodic=0
    g88: BSplineCurve PolesCount=2 KnotsCount=2 Degree=1 IsPeriodic=0
    g89: BSplineCurve PolesCount=2 KnotsCount=2 Degree=1 IsPeriodic=0
    g90: BSplineCurve PolesCount=2 KnotsCount=2 Degree=1 IsPeriodic=0
    g91: BSplineCurve PolesCount=2 KnotsCount=2 Degree=1 IsPeriodic=0
    g92: BSplineCurve PolesCount=2 KnotsCount=2 Degree=1 IsPeriodic=0
    g93: BSplineCurve PolesCount=2 KnotsCount=2 Degree=1 IsPeriodic=0
    g94: BSplineCurve PolesCount=2 KnotsCount=2 Degree=1 IsPeriodic=0
    g95: BSplineCurve PolesCount=2 KnotsCount=2 Degree=1 IsPeriodic=0
    g96: BSplineCurve PolesCount=2 KnotsCount=2 Degree=1 IsPeriodic=0
    g97: BSplineCurve PolesCount=2 KnotsCount=2 Degree=1 IsPeriodic=0
    g98: BSplineCurve PolesCount=2 KnotsCount=2 Degree=1 IsPeriodic=0
    g99: BSplineCurve PolesCount=2 KnotsCount=2 Degree=1 IsPeriodic=0
    g100: BSplineCurve PolesCount=2 KnotsCount=2 Degree=1 IsPeriodic=0
    g101: BSplineCurve PolesCount=2 KnotsCount=2 Degree=1 IsPeriodic=0
    g102: BSplineCurve PolesCount=2 KnotsCount=2 Degree=1 IsPeriodic=0
    g103: BSplineCurve PolesCount=2 KnotsCount=2 Degree=1 IsPeriodic=0
    g104: BSplineCurve PolesCount=2 KnotsCount=2 Degree=1 IsPeriodic=0
    g105: BSplineCurve PolesCount=2 KnotsCount=2 Degree=1 IsPeriodic=0
    g106: BSplineCurve PolesCount=2 KnotsCount=2 Degree=1 IsPeriodic=0
    g107: BSplineCurve PolesCount=2 KnotsCount=2 Degree=1 IsPeriodic=0
    g108: BSplineCurve PolesCount=2 KnotsCount=2 Degree=1 IsPeriodic=0
    g109: BSplineCurve PolesCount=2 KnotsCount=2 Degree=1 IsPeriodic=0
    g110: BSplineCurve PolesCount=2 KnotsCount=2 Degree=1 IsPeriodic=0
    g111: BSplineCurve PolesCount=2 KnotsCount=2 Degree=1 IsPeriodic=0
    g112: BSplineCurve PolesCount=2 KnotsCount=2 Degree=1 IsPeriodic=0
    g113: BSplineCurve PolesCount=2 KnotsCount=2 Degree=1 IsPeriodic=0
    g114: BSplineCurve PolesCount=2 KnotsCount=2 Degree=1 IsPeriodic=0
    g115: BSplineCurve PolesCount=2 KnotsCount=2 Degree=1 IsPeriodic=0
    g116: BSplineCurve PolesCount=2 KnotsCount=2 Degree=1 IsPeriodic=0
    g117: BSplineCurve PolesCount=2 KnotsCount=2 Degree=1 IsPeriodic=0
    g118: BSplineCurve PolesCount=2 KnotsCount=2 Degree=1 IsPeriodic=0
    g119: BSplineCurve PolesCount=2 KnotsCount=2 Degree=1 IsPeriodic=0
    g120: BSplineCurve PolesCount=2 KnotsCount=2 Degree=1 IsPeriodic=0
    g121: BSplineCurve PolesCount=2 KnotsCount=2 Degree=1 IsPeriodic=0
    g122: BSplineCurve PolesCount=2 KnotsCount=2 Degree=1 IsPeriodic=0
    g123: BSplineCurve PolesCount=2 KnotsCount=2 Degree=1 IsPeriodic=0
    g124: BSplineCurve PolesCount=2 KnotsCount=2 Degree=1 IsPeriodic=0
    g125: BSplineCurve PolesCount=2 KnotsCount=2 Degree=1 IsPeriodic=0
    g126: BSplineCurve PolesCount=2 KnotsCount=2 Degree=1 IsPeriodic=0
    g127: BSplineCurve PolesCount=2 KnotsCount=2 Degree=1 IsPeriodic=0
    g128: BSplineCurve PolesCount=2 KnotsCount=2 Degree=1 IsPeriodic=0
    g129: BSplineCurve PolesCount=2 KnotsCount=2 Degree=1 IsPeriodic=0
    g130: BSplineCurve PolesCount=2 KnotsCount=2 Degree=1 IsPeriodic=0
    g131: BSplineCurve PolesCount=2 KnotsCount=2 Degree=1 IsPeriodic=0
    g132: BSplineCurve PolesCount=2 KnotsCount=2 Degree=1 IsPeriodic=0
    g133: BSplineCurve PolesCount=2 KnotsCount=2 Degree=1 IsPeriodic=0
    g134: BSplineCurve PolesCount=2 KnotsCount=2 Degree=1 IsPeriodic=0
    g135: BSplineCurve PolesCount=2 KnotsCount=2 Degree=1 IsPeriodic=0
    g136: BSplineCurve PolesCount=2 KnotsCount=2 Degree=1 IsPeriodic=0
    g137: BSplineCurve PolesCount=2 KnotsCount=2 Degree=1 IsPeriodic=0
    g138: BSplineCurve PolesCount=2 KnotsCount=2 Degree=1 IsPeriodic=0
    g139: BSplineCurve PolesCount=2 KnotsCount=2 Degree=1 IsPeriodic=0
    g140: BSplineCurve PolesCount=2 KnotsCount=2 Degree=1 IsPeriodic=0
    g141: BSplineCurve PolesCount=2 KnotsCount=2 Degree=1 IsPeriodic=0
    g142: BSplineCurve PolesCount=2 KnotsCount=2 Degree=1 IsPeriodic=0
    g143: BSplineCurve PolesCount=2 KnotsCount=2 Degree=1 IsPeriodic=0
    g144: BSplineCurve PolesCount=2 KnotsCount=2 Degree=1 IsPeriodic=0
    g145: BSplineCurve PolesCount=2 KnotsCount=2 Degree=1 IsPeriodic=0
    g146: BSplineCurve PolesCount=2 KnotsCount=2 Degree=1 IsPeriodic=0
    g147: BSplineCurve PolesCount=2 KnotsCount=2 Degree=1 IsPeriodic=0
    g148: BSplineCurve PolesCount=2 KnotsCount=2 Degree=1 IsPeriodic=0
    g149: BSplineCurve PolesCount=2 KnotsCount=2 Degree=1 IsPeriodic=0
    g150: BSplineCurve PolesCount=2 KnotsCount=2 Degree=1 IsPeriodic=0
    g151: BSplineCurve PolesCount=2 KnotsCount=2 Degree=1 IsPeriodic=0
    g152: BSplineCurve PolesCount=2 KnotsCount=2 Degree=1 IsPeriodic=0
    g153: BSplineCurve PolesCount=2 KnotsCount=2 Degree=1 IsPeriodic=0
    g154: BSplineCurve PolesCount=2 KnotsCount=2 Degree=1 IsPeriodic=0
    g155: BSplineCurve PolesCount=2 KnotsCount=2 Degree=1 IsPeriodic=0
    g156: BSplineCurve PolesCount=2 KnotsCount=2 Degree=1 IsPeriodic=0
    g157: BSplineCurve PolesCount=2 KnotsCount=2 Degree=1 IsPeriodic=0
    g158: BSplineCurve PolesCount=2 KnotsCount=2 Degree=1 IsPeriodic=0
    g159: BSplineCurve PolesCount=2 KnotsCount=2 Degree=1 IsPeriodic=0
    g160: BSplineCurve PolesCount=2 KnotsCount=2 Degree=1 IsPeriodic=0
    g161: BSplineCurve PolesCount=2 KnotsCount=2 Degree=1 IsPeriodic=0
    g162: BSplineCurve PolesCount=2 KnotsCount=2 Degree=1 IsPeriodic=0
    g163: BSplineCurve PolesCount=2 KnotsCount=2 Degree=1 IsPeriodic=0
    g164: BSplineCurve PolesCount=2 KnotsCount=2 Degree=1 IsPeriodic=0
    g165: BSplineCurve PolesCount=2 KnotsCount=2 Degree=1 IsPeriodic=0
    g166: BSplineCurve PolesCount=2 KnotsCount=2 Degree=1 IsPeriodic=0
    g167: BSplineCurve PolesCount=2 KnotsCount=2 Degree=1 IsPeriodic=0
    g168: BSplineCurve PolesCount=2 KnotsCount=2 Degree=1 IsPeriodic=0
    g169: BSplineCurve PolesCount=2 KnotsCount=2 Degree=1 IsPeriodic=0
    g170: BSplineCurve PolesCount=2 KnotsCount=2 Degree=1 IsPeriodic=0
    g171: BSplineCurve PolesCount=2 KnotsCount=2 Degree=1 IsPeriodic=0
    g172: BSplineCurve PolesCount=2 KnotsCount=2 Degree=1 IsPeriodic=0
    g173: BSplineCurve PolesCount=2 KnotsCount=2 Degree=1 IsPeriodic=0
    g174: BSplineCurve PolesCount=2 KnotsCount=2 Degree=1 IsPeriodic=0
    g175: BSplineCurve PolesCount=2 KnotsCount=2 Degree=1 IsPeriodic=0
    g176: BSplineCurve PolesCount=2 KnotsCount=2 Degree=1 IsPeriodic=0
    g177: BSplineCurve PolesCount=2 KnotsCount=2 Degree=1 IsPeriodic=0
    g178: BSplineCurve PolesCount=2 KnotsCount=2 Degree=1 IsPeriodic=0
    g179: BSplineCurve PolesCount=2 KnotsCount=2 Degree=1 IsPeriodic=0
    g180: BSplineCurve PolesCount=2 KnotsCount=2 Degree=1 IsPeriodic=0
    g181: BSplineCurve PolesCount=2 KnotsCount=2 Degree=1 IsPeriodic=0
    g182: BSplineCurve PolesCount=2 KnotsCount=2 Degree=1 IsPeriodic=0
    g183: BSplineCurve PolesCount=2 KnotsCount=2 Degree=1 IsPeriodic=0
    g184: BSplineCurve PolesCount=2 KnotsCount=2 Degree=1 IsPeriodic=0
    g185: BSplineCurve PolesCount=2 KnotsCount=2 Degree=1 IsPeriodic=0
    g186: BSplineCurve PolesCount=2 KnotsCount=2 Degree=1 IsPeriodic=0
    g187: BSplineCurve PolesCount=2 KnotsCount=2 Degree=1 IsPeriodic=0
    g188: BSplineCurve PolesCount=2 KnotsCount=2 Degree=1 IsPeriodic=0
    g189: BSplineCurve PolesCount=2 KnotsCount=2 Degree=1 IsPeriodic=0
    g190: BSplineCurve PolesCount=2 KnotsCount=2 Degree=1 IsPeriodic=0
    g191: BSplineCurve PolesCount=2 KnotsCount=2 Degree=1 IsPeriodic=0
    g192: BSplineCurve PolesCount=2 KnotsCount=2 Degree=1 IsPeriodic=0
    g193: BSplineCurve PolesCount=2 KnotsCount=2 Degree=1 IsPeriodic=0
    g194: BSplineCurve PolesCount=2 KnotsCount=2 Degree=1 IsPeriodic=0
    g195: BSplineCurve PolesCount=2 KnotsCount=2 Degree=1 IsPeriodic=0
    g196: BSplineCurve PolesCount=2 KnotsCount=2 Degree=1 IsPeriodic=0
    g197: BSplineCurve PolesCount=2 KnotsCount=2 Degree=1 IsPeriodic=0
    g198: BSplineCurve PolesCount=2 KnotsCount=2 Degree=1 IsPeriodic=0
    g199: BSplineCurve PolesCount=2 KnotsCount=2 Degree=1 IsPeriodic=0
    g200: BSplineCurve PolesCount=2 KnotsCount=2 Degree=1 IsPeriodic=0
    g201: BSplineCurve PolesCount=2 KnotsCount=2 Degree=1 IsPeriodic=0
    g202: BSplineCurve PolesCount=2 KnotsCount=2 Degree=1 IsPeriodic=0
    g203: BSplineCurve PolesCount=2 KnotsCount=2 Degree=1 IsPeriodic=0
    g204: BSplineCurve PolesCount=2 KnotsCount=2 Degree=1 IsPeriodic=0
    g205: BSplineCurve PolesCount=2 KnotsCount=2 Degree=1 IsPeriodic=0
    g206: BSplineCurve PolesCount=2 KnotsCount=2 Degree=1 IsPeriodic=0
    g207: BSplineCurve PolesCount=2 KnotsCount=2 Degree=1 IsPeriodic=0
    g208: BSplineCurve PolesCount=2 KnotsCount=2 Degree=1 IsPeriodic=0
    g209: BSplineCurve PolesCount=2 KnotsCount=2 Degree=1 IsPeriodic=0
    g210: BSplineCurve PolesCount=2 KnotsCount=2 Degree=1 IsPeriodic=0
    g211: BSplineCurve PolesCount=2 KnotsCount=2 Degree=1 IsPeriodic=0
    g212: BSplineCurve PolesCount=2 KnotsCount=2 Degree=1 IsPeriodic=0
    g213: BSplineCurve PolesCount=2 KnotsCount=2 Degree=1 IsPeriodic=0
    g214: BSplineCurve PolesCount=2 KnotsCount=2 Degree=1 IsPeriodic=0
    g215: BSplineCurve PolesCount=2 KnotsCount=2 Degree=1 IsPeriodic=0
    g216: BSplineCurve PolesCount=2 KnotsCount=2 Degree=1 IsPeriodic=0
    g217: BSplineCurve PolesCount=2 KnotsCount=2 Degree=1 IsPeriodic=0
    g218: BSplineCurve PolesCount=2 KnotsCount=2 Degree=1 IsPeriodic=0
    g219: BSplineCurve PolesCount=2 KnotsCount=2 Degree=1 IsPeriodic=0
    g220: BSplineCurve PolesCount=2 KnotsCount=2 Degree=1 IsPeriodic=0
    g221: BSplineCurve PolesCount=2 KnotsCount=2 Degree=1 IsPeriodic=0
    g222: BSplineCurve PolesCount=2 KnotsCount=2 Degree=1 IsPeriodic=0
    g223: BSplineCurve PolesCount=2 KnotsCount=2 Degree=1 IsPeriodic=0
    g224: BSplineCurve PolesCount=2 KnotsCount=2 Degree=1 IsPeriodic=0
    g225: BSplineCurve PolesCount=2 KnotsCount=2 Degree=1 IsPeriodic=0
    g226: BSplineCurve PolesCount=2 KnotsCount=2 Degree=1 IsPeriodic=0
    g227: BSplineCurve PolesCount=2 KnotsCount=2 Degree=1 IsPeriodic=0
    g228: BSplineCurve PolesCount=2 KnotsCount=2 Degree=1 IsPeriodic=0
    g229: BSplineCurve PolesCount=2 KnotsCount=2 Degree=1 IsPeriodic=0
    g230: BSplineCurve PolesCount=2 KnotsCount=2 Degree=1 IsPeriodic=0
    g231: BSplineCurve PolesCount=2 KnotsCount=2 Degree=1 IsPeriodic=0
    g232: BSplineCurve PolesCount=2 KnotsCount=2 Degree=1 IsPeriodic=0
    g233: BSplineCurve PolesCount=2 KnotsCount=2 Degree=1 IsPeriodic=0
    g234: BSplineCurve PolesCount=2 KnotsCount=2 Degree=1 IsPeriodic=0
    g235: BSplineCurve PolesCount=2 KnotsCount=2 Degree=1 IsPeriodic=0
    g236: BSplineCurve PolesCount=2 KnotsCount=2 Degree=1 IsPeriodic=0
    g237: BSplineCurve PolesCount=2 KnotsCount=2 Degree=1 IsPeriodic=0
    g238: BSplineCurve PolesCount=2 KnotsCount=2 Degree=1 IsPeriodic=0
    g239: BSplineCurve PolesCount=2 KnotsCount=2 Degree=1 IsPeriodic=0
    g240: BSplineCurve PolesCount=2 KnotsCount=2 Degree=1 IsPeriodic=0
    g241: BSplineCurve PolesCount=2 KnotsCount=2 Degree=1 IsPeriodic=0
    g242: BSplineCurve PolesCount=2 KnotsCount=2 Degree=1 IsPeriodic=0
    g243: BSplineCurve PolesCount=2 KnotsCount=2 Degree=1 IsPeriodic=0
    g244: BSplineCurve PolesCount=2 KnotsCount=2 Degree=1 IsPeriodic=0
    g245: BSplineCurve PolesCount=2 KnotsCount=2 Degree=1 IsPeriodic=0
    g246: BSplineCurve PolesCount=2 KnotsCount=2 Degree=1 IsPeriodic=0
    g247: BSplineCurve PolesCount=2 KnotsCount=2 Degree=1 IsPeriodic=0
    g248: BSplineCurve PolesCount=2 KnotsCount=2 Degree=1 IsPeriodic=0
    g249: BSplineCurve PolesCount=2 KnotsCount=2 Degree=1 IsPeriodic=0
    g250: BSplineCurve PolesCount=2 KnotsCount=2 Degree=1 IsPeriodic=0
    g251: BSplineCurve PolesCount=2 KnotsCount=2 Degree=1 IsPeriodic=0
    g252: BSplineCurve PolesCount=2 KnotsCount=2 Degree=1 IsPeriodic=0
    g253: BSplineCurve PolesCount=2 KnotsCount=2 Degree=1 IsPeriodic=0
    g254: BSplineCurve PolesCount=2 KnotsCount=2 Degree=1 IsPeriodic=0
    g255: BSplineCurve PolesCount=2 KnotsCount=2 Degree=1 IsPeriodic=0
    g256: BSplineCurve PolesCount=2 KnotsCount=2 Degree=1 IsPeriodic=0
    g257: BSplineCurve PolesCount=2 KnotsCount=2 Degree=1 IsPeriodic=0
    g258: BSplineCurve PolesCount=2 KnotsCount=2 Degree=1 IsPeriodic=0
    g259: BSplineCurve PolesCount=2 KnotsCount=2 Degree=1 IsPeriodic=0
    g260: BSplineCurve PolesCount=2 KnotsCount=2 Degree=1 IsPeriodic=0
    g261: BSplineCurve PolesCount=2 KnotsCount=2 Degree=1 IsPeriodic=0
    g262: BSplineCurve PolesCount=2 KnotsCount=2 Degree=1 IsPeriodic=0
    g263: BSplineCurve PolesCount=2 KnotsCount=2 Degree=1 IsPeriodic=0
    g264: BSplineCurve PolesCount=2 KnotsCount=2 Degree=1 IsPeriodic=0
    g265: BSplineCurve PolesCount=2 KnotsCount=2 Degree=1 IsPeriodic=0
    g266: BSplineCurve PolesCount=2 KnotsCount=2 Degree=1 IsPeriodic=0
    g267: BSplineCurve PolesCount=2 KnotsCount=2 Degree=1 IsPeriodic=0
    g268: BSplineCurve PolesCount=2 KnotsCount=2 Degree=1 IsPeriodic=0
    g269: BSplineCurve PolesCount=2 KnotsCount=2 Degree=1 IsPeriodic=0
    g270: BSplineCurve PolesCount=2 KnotsCount=2 Degree=1 IsPeriodic=0
    g271: BSplineCurve PolesCount=2 KnotsCount=2 Degree=1 IsPeriodic=0
    g272: BSplineCurve PolesCount=2 KnotsCount=2 Degree=1 IsPeriodic=0
    g273: BSplineCurve PolesCount=2 KnotsCount=2 Degree=1 IsPeriodic=0
    g274: BSplineCurve PolesCount=2 KnotsCount=2 Degree=1 IsPeriodic=0
    g275: BSplineCurve PolesCount=2 KnotsCount=2 Degree=1 IsPeriodic=0
    g276: BSplineCurve PolesCount=2 KnotsCount=2 Degree=1 IsPeriodic=0
    g277: BSplineCurve PolesCount=2 KnotsCount=2 Degree=1 IsPeriodic=0
    g278: BSplineCurve PolesCount=2 KnotsCount=2 Degree=1 IsPeriodic=0
    g279: BSplineCurve PolesCount=2 KnotsCount=2 Degree=1 IsPeriodic=0
    g280: BSplineCurve PolesCount=2 KnotsCount=2 Degree=1 IsPeriodic=0
    g281: BSplineCurve PolesCount=2 KnotsCount=2 Degree=1 IsPeriodic=0
    g282: BSplineCurve PolesCount=2 KnotsCount=2 Degree=1 IsPeriodic=0
    g283: BSplineCurve PolesCount=2 KnotsCount=2 Degree=1 IsPeriodic=0
    g284: BSplineCurve PolesCount=2 KnotsCount=2 Degree=1 IsPeriodic=0
    g285: BSplineCurve PolesCount=2 KnotsCount=2 Degree=1 IsPeriodic=0
    g286: BSplineCurve PolesCount=2 KnotsCount=2 Degree=1 IsPeriodic=0
    g287: BSplineCurve PolesCount=2 KnotsCount=2 Degree=1 IsPeriodic=0
    g288: BSplineCurve PolesCount=2 KnotsCount=2 Degree=1 IsPeriodic=0
    g289: BSplineCurve PolesCount=2 KnotsCount=2 Degree=1 IsPeriodic=0
    g290: BSplineCurve PolesCount=2 KnotsCount=2 Degree=1 IsPeriodic=0
    g291: BSplineCurve PolesCount=2 KnotsCount=2 Degree=1 IsPeriodic=0
    g292: BSplineCurve PolesCount=2 KnotsCount=2 Degree=1 IsPeriodic=0
    g293: BSplineCurve PolesCount=2 KnotsCount=2 Degree=1 IsPeriodic=0
    g294: BSplineCurve PolesCount=2 KnotsCount=2 Degree=1 IsPeriodic=0
    g295: BSplineCurve PolesCount=2 KnotsCount=2 Degree=1 IsPeriodic=0
    g296: BSplineCurve PolesCount=2 KnotsCount=2 Degree=1 IsPeriodic=0
    g297: BSplineCurve PolesCount=2 KnotsCount=2 Degree=1 IsPeriodic=0
    g298: BSplineCurve PolesCount=2 KnotsCount=2 Degree=1 IsPeriodic=0
    g299: BSplineCurve PolesCount=2 KnotsCount=2 Degree=1 IsPeriodic=0
    g300: BSplineCurve PolesCount=2 KnotsCount=2 Degree=1 IsPeriodic=0
    g301: BSplineCurve PolesCount=2 KnotsCount=2 Degree=1 IsPeriodic=0
    g302: BSplineCurve PolesCount=2 KnotsCount=2 Degree=1 IsPeriodic=0
    g303: BSplineCurve PolesCount=2 KnotsCount=2 Degree=1 IsPeriodic=0
    g304: BSplineCurve PolesCount=2 KnotsCount=2 Degree=1 IsPeriodic=0
    g305: BSplineCurve PolesCount=2 KnotsCount=2 Degree=1 IsPeriodic=0
    g306: BSplineCurve PolesCount=2 KnotsCount=2 Degree=1 IsPeriodic=0
    g307: BSplineCurve PolesCount=2 KnotsCount=2 Degree=1 IsPeriodic=0
    g308: BSplineCurve PolesCount=2 KnotsCount=2 Degree=1 IsPeriodic=0
    g309: BSplineCurve PolesCount=2 KnotsCount=2 Degree=1 IsPeriodic=0
    g310: BSplineCurve PolesCount=2 KnotsCount=2 Degree=1 IsPeriodic=0
    g311: BSplineCurve PolesCount=2 KnotsCount=2 Degree=1 IsPeriodic=0
    g312: BSplineCurve PolesCount=2 KnotsCount=2 Degree=1 IsPeriodic=0
    g313: BSplineCurve PolesCount=2 KnotsCount=2 Degree=1 IsPeriodic=0
    g314: BSplineCurve PolesCount=2 KnotsCount=2 Degree=1 IsPeriodic=0
    g315: BSplineCurve PolesCount=2 KnotsCount=2 Degree=1 IsPeriodic=0
    g316: BSplineCurve PolesCount=2 KnotsCount=2 Degree=1 IsPeriodic=0
    g317: BSplineCurve PolesCount=2 KnotsCount=2 Degree=1 IsPeriodic=0
    g318: BSplineCurve PolesCount=2 KnotsCount=2 Degree=1 IsPeriodic=0
    g319: BSplineCurve PolesCount=2 KnotsCount=2 Degree=1 IsPeriodic=0
    g320: BSplineCurve PolesCount=2 KnotsCount=2 Degree=1 IsPeriodic=0
    g321: BSplineCurve PolesCount=2 KnotsCount=2 Degree=1 IsPeriodic=0
    g322: BSplineCurve PolesCount=2 KnotsCount=2 Degree=1 IsPeriodic=0
    g323: BSplineCurve PolesCount=2 KnotsCount=2 Degree=1 IsPeriodic=0
    g324: BSplineCurve PolesCount=2 KnotsCount=2 Degree=1 IsPeriodic=0
    g325: BSplineCurve PolesCount=2 KnotsCount=2 Degree=1 IsPeriodic=0
    g326: BSplineCurve PolesCount=2 KnotsCount=2 Degree=1 IsPeriodic=0
    g327: BSplineCurve PolesCount=2 KnotsCount=2 Degree=1 IsPeriodic=0
    g328: BSplineCurve PolesCount=2 KnotsCount=2 Degree=1 IsPeriodic=0
    g329: BSplineCurve PolesCount=2 KnotsCount=2 Degree=1 IsPeriodic=0
    g330: BSplineCurve PolesCount=2 KnotsCount=2 Degree=1 IsPeriodic=0
    g331: BSplineCurve PolesCount=2 KnotsCount=2 Degree=1 IsPeriodic=0
    g332: BSplineCurve PolesCount=2 KnotsCount=2 Degree=1 IsPeriodic=0
    g333: BSplineCurve PolesCount=2 KnotsCount=2 Degree=1 IsPeriodic=0
    g334: BSplineCurve PolesCount=2 KnotsCount=2 Degree=1 IsPeriodic=0
    g335: BSplineCurve PolesCount=2 KnotsCount=2 Degree=1 IsPeriodic=0
    g336: BSplineCurve PolesCount=2 KnotsCount=2 Degree=1 IsPeriodic=0
    g337: BSplineCurve PolesCount=2 KnotsCount=2 Degree=1 IsPeriodic=0
    g338: BSplineCurve PolesCount=2 KnotsCount=2 Degree=1 IsPeriodic=0
    g339: BSplineCurve PolesCount=2 KnotsCount=2 Degree=1 IsPeriodic=0
    g340: BSplineCurve PolesCount=2 KnotsCount=2 Degree=1 IsPeriodic=0
    g341: BSplineCurve PolesCount=2 KnotsCount=2 Degree=1 IsPeriodic=0
    g342: BSplineCurve PolesCount=2 KnotsCount=2 Degree=1 IsPeriodic=0
    g343: BSplineCurve PolesCount=2 KnotsCount=2 Degree=1 IsPeriodic=0
    g344: BSplineCurve PolesCount=2 KnotsCount=2 Degree=1 IsPeriodic=0
    g345: BSplineCurve PolesCount=2 KnotsCount=2 Degree=1 IsPeriodic=0
    g346: BSplineCurve PolesCount=2 KnotsCount=2 Degree=1 IsPeriodic=0
    g347: BSplineCurve PolesCount=2 KnotsCount=2 Degree=1 IsPeriodic=0
    g348: BSplineCurve PolesCount=2 KnotsCount=2 Degree=1 IsPeriodic=0
    g349: BSplineCurve PolesCount=2 KnotsCount=2 Degree=1 IsPeriodic=0
    g350: BSplineCurve PolesCount=2 KnotsCount=2 Degree=1 IsPeriodic=0
    g351: BSplineCurve PolesCount=2 KnotsCount=2 Degree=1 IsPeriodic=0
    g352: BSplineCurve PolesCount=2 KnotsCount=2 Degree=1 IsPeriodic=0
    g353: BSplineCurve PolesCount=2 KnotsCount=2 Degree=1 IsPeriodic=0
    g354: BSplineCurve PolesCount=2 KnotsCount=2 Degree=1 IsPeriodic=0
    g355: BSplineCurve PolesCount=2 KnotsCount=2 Degree=1 IsPeriodic=0
    g356: BSplineCurve PolesCount=2 KnotsCount=2 Degree=1 IsPeriodic=0
    g357: BSplineCurve PolesCount=2 KnotsCount=2 Degree=1 IsPeriodic=0
    g358: BSplineCurve PolesCount=2 KnotsCount=2 Degree=1 IsPeriodic=0
    g359: BSplineCurve PolesCount=2 KnotsCount=2 Degree=1 IsPeriodic=0
    g360: BSplineCurve PolesCount=2 KnotsCount=2 Degree=1 IsPeriodic=0
    g361: BSplineCurve PolesCount=2 KnotsCount=2 Degree=1 IsPeriodic=0
    g362: BSplineCurve PolesCount=2 KnotsCount=2 Degree=1 IsPeriodic=0
    g363: BSplineCurve PolesCount=2 KnotsCount=2 Degree=1 IsPeriodic=0
    g364: BSplineCurve PolesCount=2 KnotsCount=2 Degree=1 IsPeriodic=0
    g365: BSplineCurve PolesCount=2 KnotsCount=2 Degree=1 IsPeriodic=0
    g366: BSplineCurve PolesCount=2 KnotsCount=2 Degree=1 IsPeriodic=0
    g367: BSplineCurve PolesCount=2 KnotsCount=2 Degree=1 IsPeriodic=0
    g368: BSplineCurve PolesCount=2 KnotsCount=2 Degree=1 IsPeriodic=0
    g369: BSplineCurve PolesCount=2 KnotsCount=2 Degree=1 IsPeriodic=0
    g370: BSplineCurve PolesCount=2 KnotsCount=2 Degree=1 IsPeriodic=0
    g371: BSplineCurve PolesCount=2 KnotsCount=2 Degree=1 IsPeriodic=0
    g372: BSplineCurve PolesCount=2 KnotsCount=2 Degree=1 IsPeriodic=0
    g373: BSplineCurve PolesCount=2 KnotsCount=2 Degree=1 IsPeriodic=0
    g374: BSplineCurve PolesCount=2 KnotsCount=2 Degree=1 IsPeriodic=0
    g375: BSplineCurve PolesCount=2 KnotsCount=2 Degree=1 IsPeriodic=0
    g376: BSplineCurve PolesCount=2 KnotsCount=2 Degree=1 IsPeriodic=0
    g377: BSplineCurve PolesCount=2 KnotsCount=2 Degree=1 IsPeriodic=0
    g378: BSplineCurve PolesCount=2 KnotsCount=2 Degree=1 IsPeriodic=0
    g379: BSplineCurve PolesCount=2 KnotsCount=2 Degree=1 IsPeriodic=0
    g380: BSplineCurve PolesCount=2 KnotsCount=2 Degree=1 IsPeriodic=0
    g381: BSplineCurve PolesCount=2 KnotsCount=2 Degree=1 IsPeriodic=0
    g382: BSplineCurve PolesCount=2 KnotsCount=2 Degree=1 IsPeriodic=0
    g383: BSplineCurve PolesCount=2 KnotsCount=2 Degree=1 IsPeriodic=0
    g384: BSplineCurve PolesCount=2 KnotsCount=2 Degree=1 IsPeriodic=0
    g385: BSplineCurve PolesCount=2 KnotsCount=2 Degree=1 IsPeriodic=0
    g386: BSplineCurve PolesCount=2 KnotsCount=2 Degree=1 IsPeriodic=0
    g387: BSplineCurve PolesCount=2 KnotsCount=2 Degree=1 IsPeriodic=0
    g388: BSplineCurve PolesCount=2 KnotsCount=2 Degree=1 IsPeriodic=0
    g389: BSplineCurve PolesCount=2 KnotsCount=2 Degree=1 IsPeriodic=0
    g390: BSplineCurve PolesCount=2 KnotsCount=2 Degree=1 IsPeriodic=0
    g391: BSplineCurve PolesCount=2 KnotsCount=2 Degree=1 IsPeriodic=0
    g392: BSplineCurve PolesCount=2 KnotsCount=2 Degree=1 IsPeriodic=0
    g393: BSplineCurve PolesCount=2 KnotsCount=2 Degree=1 IsPeriodic=0
    g394: BSplineCurve PolesCount=2 KnotsCount=2 Degree=1 IsPeriodic=0
    g395: BSplineCurve PolesCount=2 KnotsCount=2 Degree=1 IsPeriodic=0
    g396: BSplineCurve PolesCount=2 KnotsCount=2 Degree=1 IsPeriodic=0
    g397: BSplineCurve PolesCount=2 KnotsCount=2 Degree=1 IsPeriodic=0
    g398: BSplineCurve PolesCount=2 KnotsCount=2 Degree=1 IsPeriodic=0
    g399: BSplineCurve PolesCount=2 KnotsCount=2 Degree=1 IsPeriodic=0
    ... +460 more geometry lines
  constraints (860):
    c: Coincident(g0,g1)
    c: Coincident(g1,g2)
    c: Coincident(g2,g3)
    c: Coincident(g3,g4)
    c: Coincident(g4,g5)
    c: Coincident(g5,g6)
    c: Coincident(g6,g7)
    c: Coincident(g7,g8)
    c: Coincident(g8,g9)
    c: Coincident(g9,g10)
    c: Coincident(g10,g11)
    c: Coincident(g11,g12)
    c: Coincident(g12,g13)
    c: Coincident(g13,g14)
    c: Coincident(g14,g15)
    c: Coincident(g15,g16)
    c: Coincident(g16,g17)
    c: Coincident(g17,g18)
    c: Coincident(g18,g19)
    c: Coincident(g19,g20)
    c: Coincident(g20,g21)
    c: Coincident(g21,g22)
    c: Coincident(g22,g23)
    c: Coincident(g23,g24)
    c: Coincident(g24,g25)
    c: Coincident(g25,g26)
    c: Coincident(g26,g27)
    c: Coincident(g27,g28)
    c: Coincident(g28,g29)
    c: Coincident(g29,g30)
    c: Coincident(g30,g31)
    c: Coincident(g31,g32)
    c: Coincident(g32,g33)
    c: Coincident(g33,g34)
    c: Coincident(g34,g35)
    c: Coincident(g35,g36)
    c: Coincident(g36,g37)
    c: Coincident(g37,g38)
    c: Coincident(g38,g39)
    c: Coincident(g39,g40)
    c: Coincident(g40,g41)
    c: Coincident(g41,g42)
    c: Coincident(g42,g43)
    c: Coincident(g43,g44)
    c: Coincident(g44,g45)
    c: Coincident(g45,g46)
    c: Coincident(g46,g47)
    c: Coincident(g47,g48)
    c: Coincident(g48,g49)
    c: Coincident(g49,g50)
    c: Coincident(g50,g51)
    c: Coincident(g51,g52)
    c: Coincident(g52,g53)
    c: Coincident(g53,g54)
    c: Coincident(g54,g55)
    c: Coincident(g55,g56)
    c: Coincident(g56,g57)
    c: Coincident(g57,g58)
    c: Coincident(g58,g59)
    c: Coincident(g59,g60)
    c: Coincident(g60,g61)
    c: Coincident(g61,g62)
    c: Coincident(g62,g63)
    c: Coincident(g63,g64)
    c: Coincident(g64,g65)
    c: Coincident(g65,g66)
    c: Coincident(g66,g67)
    c: Coincident(g67,g68)
    c: Coincident(g68,g69)
    c: Coincident(g69,g70)
    c: Coincident(g70,g71)
    c: Coincident(g71,g72)
    c: Coincident(g72,g73)
    c: Coincident(g73,g74)
    c: Coincident(g74,g75)
    c: Coincident(g75,g76)
    c: Coincident(g76,g77)
    c: Coincident(g77,g78)
    c: Coincident(g78,g79)
    c: Coincident(g79,g80)
    c: Coincident(g80,g81)
    c: Coincident(g81,g82)
    c: Coincident(g82,g83)
    c: Coincident(g83,g84)
    c: Coincident(g84,g85)
    c: Coincident(g85,g86)
    c: Coincident(g86,g87)
    c: Coincident(g87,g0)
    c: Coincident(g88,g89)
    c: Coincident(g89,g90)
    c: Coincident(g90,g91)
    c: Coincident(g91,g92)
    c: Coincident(g92,g93)
    c: Coincident(g93,g94)
    c: Coincident(g94,g95)
    c: Coincident(g95,g96)
    c: Coincident(g96,g97)
    c: Coincident(g97,g98)
    c: Coincident(g98,g99)
    c: Coincident(g99,g100)
    c: Coincident(g100,g101)
    c: Coincident(g101,g102)
    c: Coincident(g102,g103)
    c: Coincident(g103,g104)
    c: Coincident(g104,g105)
    c: Coincident(g105,g106)
    c: Coincident(g106,g107)
    c: Coincident(g107,g108)
    c: Coincident(g108,g109)
    c: Coincident(g109,g110)
    c: Coincident(g110,g111)
    c: Coincident(g111,g112)
    c: Coincident(g112,g113)
    c: Coincident(g113,g114)
    c: Coincident(g114,g115)
    c: Coincident(g115,g116)
    c: Coincident(g116,g117)
    c: Coincident(g117,g118)
    c: Coincident(g118,g119)
    c: Coincident(g119,g120)
    c: Coincident(g120,g121)
    c: Coincident(g121,g122)
    c: Coincident(g122,g123)
    c: Coincident(g123,g124)
    c: Coincident(g124,g125)
    c: Coincident(g125,g126)
    c: Coincident(g126,g127)
    c: Coincident(g127,g88)
    c: Coincident(g128,g129)
    c: Coincident(g129,g130)
    c: Coincident(g130,g131)
    c: Coincident(g131,g132)
    c: Coincident(g132,g133)
    c: Coincident(g133,g134)
    c: Coincident(g134,g135)
    c: Coincident(g135,g136)
    c: Coincident(g136,g137)
    c: Coincident(g137,g138)
    c: Coincident(g138,g139)
    c: Coincident(g139,g140)
    c: Coincident(g140,g141)
    c: Coincident(g141,g142)
    c: Coincident(g142,g143)
    c: Coincident(g143,g144)
    c: Coincident(g144,g145)
    c: Coincident(g145,g146)
    c: Coincident(g146,g147)
    c: Coincident(g147,g148)
    c: Coincident(g148,g149)
    c: Coincident(g149,g150)
    c: Coincident(g150,g151)
    c: Coincident(g151,g152)
    c: Coincident(g152,g153)
    c: Coincident(g153,g154)
    c: Coincident(g154,g155)
    c: Coincident(g155,g156)
    c: Coincident(g156,g157)
    c: Coincident(g157,g158)
    c: Coincident(g158,g159)
    c: Coincident(g159,g160)
    c: Coincident(g160,g161)
    c: Coincident(g161,g162)
    c: Coincident(g162,g163)
    c: Coincident(g163,g164)
    c: Coincident(g164,g165)
    c: Coincident(g165,g166)
    c: Coincident(g166,g167)
    c: Coincident(g167,g168)
    c: Coincident(g168,g169)
    c: Coincident(g169,g170)
    c: Coincident(g170,g171)
    c: Coincident(g171,g172)
    c: Coincident(g172,g173)
    c: Coincident(g173,g174)
    c: Coincident(g174,g175)
    c: Coincident(g175,g176)
    c: Coincident(g176,g177)
    c: Coincident(g177,g178)
    c: Coincident(g178,g179)
    c: Coincident(g179,g180)
    c: Coincident(g180,g181)
    c: Coincident(g181,g182)
    c: Coincident(g182,g183)
    c: Coincident(g183,g184)
    c: Coincident(g184,g185)
    c: Coincident(g185,g186)
    c: Coincident(g186,g187)
    c: Coincident(g187,g188)
    c: Coincident(g188,g189)
    c: Coincident(g189,g190)
    c: Coincident(g190,g191)
    c: Coincident(g191,g192)
    c: Coincident(g192,g193)
    c: Coincident(g193,g194)
    c: Coincident(g194,g195)
    c: Coincident(g195,g196)
    c: Coincident(g196,g197)
    c: Coincident(g197,g198)
    c: Coincident(g198,g199)
    c: Coincident(g199,g200)
    c: Coincident(g200,g201)
    c: Coincident(g201,g202)
    c: Coincident(g202,g203)
    c: Coincident(g203,g204)
    c: Coincident(g204,g205)
    c: Coincident(g205,g206)
    c: Coincident(g206,g207)
    c: Coincident(g207,g208)
    c: Coincident(g208,g209)
    c: Coincident(g209,g210)
    c: Coincident(g210,g211)
    c: Coincident(g211,g212)
    c: Coincident(g212,g213)
    c: Coincident(g213,g214)
    c: Coincident(g214,g215)
    c: Coincident(g215,g216)
    c: Coincident(g216,g217)
    c: Coincident(g217,g218)
    c: Coincident(g218,g219)
    c: Coincident(g219,g220)
    c: Coincident(g220,g221)
    c: Coincident(g221,g222)
    c: Coincident(g222,g223)
    c: Coincident(g223,g224)
    c: Coincident(g224,g225)
    c: Coincident(g225,g226)
    c: Coincident(g226,g227)
    c: Coincident(g227,g228)
    c: Coincident(g228,g229)
    c: Coincident(g229,g230)
    c: Coincident(g230,g231)
    c: Coincident(g231,g232)
    c: Coincident(g232,g233)
    c: Coincident(g233,g234)
    c: Coincident(g234,g235)
    c: Coincident(g235,g236)
    c: Coincident(g236,g237)
    c: Coincident(g237,g238)
    c: Coincident(g238,g239)
    c: Coincident(g239,g128)
    c: Coincident(g240,g241)
    c: Coincident(g241,g242)
    c: Coincident(g242,g243)
    c: Coincident(g243,g244)
    c: Coincident(g244,g245)
    c: Coincident(g245,g246)
    c: Coincident(g246,g247)
    c: Coincident(g247,g248)
    c: Coincident(g248,g249)
    c: Coincident(g249,g250)
    c: Coincident(g250,g251)
    c: Coincident(g251,g252)
    c: Coincident(g252,g253)
    c: Coincident(g253,g254)
    c: Coincident(g254,g255)
    c: Coincident(g255,g256)
    c: Coincident(g256,g257)
    c: Coincident(g257,g258)
    c: Coincident(g258,g259)
    c: Coincident(g259,g260)
    c: Coincident(g260,g261)
    c: Coincident(g261,g262)
    c: Coincident(g262,g263)
    c: Coincident(g263,g264)
    c: Coincident(g264,g265)
    c: Coincident(g265,g266)
    c: Coincident(g266,g267)
    c: Coincident(g267,g268)
    c: Coincident(g268,g269)
    c: Coincident(g269,g270)
    c: Coincident(g270,g271)
    c: Coincident(g271,g272)
    c: Coincident(g272,g273)
    c: Coincident(g273,g274)
    c: Coincident(g274,g275)
    c: Coincident(g275,g276)
    c: Coincident(g276,g277)
    c: Coincident(g277,g278)
    c: Coincident(g278,g279)
    c: Coincident(g279,g280)
    c: Coincident(g280,g281)
    c: Coincident(g281,g282)
    c: Coincident(g282,g283)
    c: Coincident(g283,g284)
    c: Coincident(g284,g285)
    c: Coincident(g285,g286)
    c: Coincident(g286,g287)
    c: Coincident(g287,g240)
    c: Coincident(g288,g289)
    c: Coincident(g289,g290)
    c: Coincident(g290,g291)
    c: Coincident(g291,g292)
    c: Coincident(g292,g293)
    c: Coincident(g293,g294)
    c: Coincident(g294,g295)
    c: Coincident(g295,g296)
    c: Coincident(g296,g297)
    c: Coincident(g297,g298)
    c: Coincident(g298,g299)
    c: Coincident(g299,g300)
    c: Coincident(g300,g301)
    c: Coincident(g301,g302)
    c: Coincident(g302,g303)
    c: Coincident(g303,g304)
    c: Coincident(g304,g305)
    c: Coincident(g305,g306)
    c: Coincident(g306,g307)
    c: Coincident(g307,g308)
    c: Coincident(g308,g309)
    c: Coincident(g309,g310)
    c: Coincident(g310,g311)
    c: Coincident(g311,g288)
    c: Coincident(g312,g313)
    c: Coincident(g313,g314)
    c: Coincident(g314,g315)
    c: Coincident(g315,g316)
    c: Coincident(g316,g317)
    c: Coincident(g317,g318)
    c: Coincident(g318,g319)
    c: Coincident(g319,g320)
    c: Coincident(g320,g321)
    c: Coincident(g321,g322)
    c: Coincident(g322,g323)
    c: Coincident(g323,g324)
    c: Coincident(g324,g325)
    c: Coincident(g325,g326)
    c: Coincident(g326,g327)
    c: Coincident(g327,g312)
    c: Coincident(g328,g329)
    c: Coincident(g329,g330)
    c: Coincident(g330,g331)
    c: Coincident(g331,g332)
    c: Coincident(g332,g333)
    c: Coincident(g333,g334)
    c: Coincident(g334,g335)
    c: Coincident(g335,g336)
    c: Coincident(g336,g337)
    c: Coincident(g337,g338)
    c: Coincident(g338,g339)
    c: Coincident(g339,g340)
    c: Coincident(g340,g341)
    c: Coincident(g341,g342)
    c: Coincident(g342,g343)
    c: Coincident(g343,g344)
    c: Coincident(g344,g345)
    c: Coincident(g345,g346)
    c: Coincident(g346,g347)
    c: Coincident(g347,g348)
    c: Coincident(g348,g349)
    c: Coincident(g349,g350)
    c: Coincident(g350,g351)
    c: Coincident(g351,g352)
    c: Coincident(g352,g353)
    c: Coincident(g353,g354)
    c: Coincident(g354,g355)
    c: Coincident(g355,g356)
    c: Coincident(g356,g357)
    c: Coincident(g357,g358)
    c: Coincident(g358,g359)
    c: Coincident(g359,g360)
    c: Coincident(g360,g361)
    c: Coincident(g361,g362)
    c: Coincident(g362,g363)
    c: Coincident(g363,g364)
    c: Coincident(g364,g365)
    c: Coincident(g365,g366)
    c: Coincident(g366,g367)
    c: Coincident(g367,g368)
    c: Coincident(g368,g369)
    c: Coincident(g369,g370)
    c: Coincident(g370,g371)
    c: Coincident(g371,g372)
    c: Coincident(g372,g373)
    c: Coincident(g373,g374)
    c: Coincident(g374,g375)
    c: Coincident(g375,g376)
    c: Coincident(g376,g377)
    c: Coincident(g377,g378)
    c: Coincident(g378,g379)
    c: Coincident(g379,g380)
    c: Coincident(g380,g381)
    c: Coincident(g381,g382)
    c: Coincident(g382,g383)
    c: Coincident(g383,g384)
    c: Coincident(g384,g385)
    c: Coincident(g385,g386)
    c: Coincident(g386,g387)
    c: Coincident(g387,g388)
    c: Coincident(g388,g389)
    c: Coincident(g389,g390)
    c: Coincident(g390,g391)
    c: Coincident(g391,g392)
    c: Coincident(g392,g393)
    c: Coincident(g393,g394)
    c: Coincident(g394,g395)
    c: Coincident(g395,g396)
    c: Coincident(g396,g397)
    c: Coincident(g397,g398)
    c: Coincident(g398,g399)
    c: Coincident(g399,g328)
    c: Coincident(g400,g401)
    c: Coincident(g401,g402)
    c: Coincident(g402,g403)
    c: Coincident(g403,g404)
    c: Coincident(g404,g405)
    c: Coincident(g405,g406)
    c: Coincident(g406,g407)
    c: Coincident(g407,g408)
    c: Coincident(g408,g409)
    c: Coincident(g409,g410)
    c: Coincident(g410,g411)
    c: Coincident(g411,g412)
    c: Coincident(g412,g413)
    c: Coincident(g413,g414)
    c: Coincident(g414,g415)
    c: Coincident(g415,g416)
    c: Coincident(g416,g417)
    c: Coincident(g417,g418)
    c: Coincident(g418,g419)
    c: Coincident(g419,g420)
    c: Coincident(g420,g421)
    c: Coincident(g421,g422)
    c: Coincident(g422,g423)
    c: Coincident(g423,g400)
    c: Coincident(g424,g425)
    c: Coincident(g425,g426)
    c: Coincident(g426,g427)
    c: Coincident(g427,g428)
    c: Coincident(g428,g429)
    c: Coincident(g429,g430)
    c: Coincident(g430,g431)
    c: Coincident(g431,g432)
    c: Coincident(g432,g433)
    c: Coincident(g433,g434)
    c: Coincident(g434,g435)
    c: Coincident(g435,g436)
    c: Coincident(g436,g437)
    c: Coincident(g437,g438)
    c: Coincident(g438,g439)
    c: Coincident(g439,g440)
    c: Coincident(g440,g441)
    c: Coincident(g441,g442)
    c: Coincident(g442,g443)
    c: Coincident(g443,g444)
    c: Coincident(g444,g445)
    c: Coincident(g445,g446)
    c: Coincident(g446,g447)
    c: Coincident(g447,g448)
    c: Coincident(g448,g449)
    c: Coincident(g449,g450)
    c: Coincident(g450,g451)
    c: Coincident(g451,g452)
    c: Coincident(g452,g453)
    c: Coincident(g453,g454)
    c: Coincident(g454,g455)
    c: Coincident(g455,g456)
    c: Coincident(g456,g457)
    c: Coincident(g457,g458)
    c: Coincident(g458,g459)
    c: Coincident(g459,g460)
    c: Coincident(g460,g461)
    c: Coincident(g461,g462)
    c: Coincident(g462,g463)
    c: Coincident(g463,g464)
    c: Coincident(g464,g465)
    c: Coincident(g465,g466)
    c: Coincident(g466,g467)
    c: Coincident(g467,g468)
    c: Coincident(g468,g469)
    c: Coincident(g469,g470)
    c: Coincident(g470,g471)
    c: Coincident(g471,g472)
    c: Coincident(g472,g473)
    c: Coincident(g473,g474)
    c: Coincident(g474,g475)
    c: Coincident(g475,g476)
    c: Coincident(g476,g477)
    c: Coincident(g477,g478)
    c: Coincident(g478,g479)
    c: Coincident(g479,g424)
    c: Coincident(g480,g481)
    c: Coincident(g481,g482)
    c: Coincident(g482,g483)
    c: Coincident(g483,g484)
    c: Coincident(g484,g485)
    c: Coincident(g485,g486)
    c: Coincident(g486,g487)
    c: Coincident(g487,g488)
    c: Coincident(g488,g489)
    c: Coincident(g489,g490)
    c: Coincident(g490,g491)
    c: Coincident(g491,g492)
    c: Coincident(g492,g493)
    c: Coincident(g493,g494)
    c: Coincident(g494,g495)
    c: Coincident(g495,g480)
    c: Coincident(g496,g497)
    c: Coincident(g497,g498)
    c: Coincident(g498,g499)
    c: Coincident(g499,g500)
    c: Coincident(g500,g501)
    c: Coincident(g501,g502)
    c: Coincident(g502,g503)
    c: Coincident(g503,g504)
    c: Coincident(g504,g505)
    c: Coincident(g505,g506)
    c: Coincident(g506,g507)
    c: Coincident(g507,g508)
    c: Coincident(g508,g509)
    c: Coincident(g509,g510)
    c: Coincident(g510,g511)
    c: Coincident(g511,g512)
    c: Coincident(g512,g513)
    c: Coincident(g513,g514)
    c: Coincident(g514,g515)
    c: Coincident(g515,g516)
    c: Coincident(g516,g517)
    c: Coincident(g517,g518)
    c: Coincident(g518,g519)
    c: Coincident(g519,g520)
    c: Coincident(g520,g521)
    c: Coincident(g521,g522)
    c: Coincident(g522,g523)
    c: Coincident(g523,g524)
    c: Coincident(g524,g525)
    c: Coincident(g525,g526)
    c: Coincident(g526,g527)
    c: Coincident(g527,g528)
    c: Coincident(g528,g529)
    c: Coincident(g529,g530)
    c: Coincident(g530,g531)
    c: Coincident(g531,g532)
    c: Coincident(g532,g533)
    c: Coincident(g533,g534)
    c: Coincident(g534,g535)
    c: Coincident(g535,g496)
    c: Coincident(g536,g537)
    c: Coincident(g537,g538)
    c: Coincident(g538,g539)
    c: Coincident(g539,g540)
    c: Coincident(g540,g541)
    c: Coincident(g541,g542)
    c: Coincident(g542,g543)
    c: Coincident(g543,g544)
    c: Coincident(g544,g545)
    c: Coincident(g545,g546)
    c: Coincident(g546,g547)
    c: Coincident(g547,g548)
    c: Coincident(g548,g549)
    c: Coincident(g549,g550)
    c: Coincident(g550,g551)
    c: Coincident(g551,g552)
    c: Coincident(g552,g553)
    c: Coincident(g553,g554)
    c: Coincident(g554,g555)
    c: Coincident(g555,g556)
    c: Coincident(g556,g557)
    c: Coincident(g557,g558)
    c: Coincident(g558,g559)
    c: Coincident(g559,g560)
    c: Coincident(g560,g561)
    c: Coincident(g561,g562)
    c: Coincident(g562,g563)
    c: Coincident(g563,g564)
    c: Coincident(g564,g565)
    c: Coincident(g565,g566)
    c: Coincident(g566,g567)
    c: Coincident(g567,g568)
    c: Coincident(g568,g569)
    c: Coincident(g569,g570)
    c: Coincident(g570,g571)
    c: Coincident(g571,g572)
    c: Coincident(g572,g573)
    c: Coincident(g573,g574)
    c: Coincident(g574,g575)
    c: Coincident(g575,g536)
    c: Coincident(g576,g577)
    c: Coincident(g577,g578)
    c: Coincident(g578,g579)
    c: Coincident(g579,g580)
    c: Coincident(g580,g581)
    c: Coincident(g581,g582)
    c: Coincident(g582,g583)
    c: Coincident(g583,g584)
    c: Coincident(g584,g585)
    c: Coincident(g585,g586)
    c: Coincident(g586,g587)
    c: Coincident(g587,g576)
    c: Coincident(g588,g589)
    c: Coincident(g589,g590)
    c: Coincident(g590,g591)
    c: Coincident(g591,g592)
    c: Coincident(g592,g593)
    c: Coincident(g593,g594)
    c: Coincident(g594,g595)
    c: Coincident(g595,g596)
    c: Coincident(g596,g597)
    c: Coincident(g597,g598)
    c: Coincident(g598,g599)
    c: Coincident(g599,g600)
    c: Coincident(g600,g601)
    c: Coincident(g601,g602)
    c: Coincident(g602,g603)
    c: Coincident(g603,g604)
    c: Coincident(g604,g605)
    c: Coincident(g605,g606)
    c: Coincident(g606,g607)
    c: Coincident(g607,g608)
    c: Coincident(g608,g609)
    c: Coincident(g609,g610)
    c: Coincident(g610,g611)
    c: Coincident(g611,g612)
    c: Coincident(g612,g613)
    c: Coincident(g613,g614)
    c: Coincident(g614,g615)
    c: Coincident(g615,g616)
    c: Coincident(g616,g617)
    c: Coincident(g617,g618)
    c: Coincident(g618,g619)
    c: Coincident(g619,g620)
    c: Coincident(g620,g621)
    c: Coincident(g621,g622)
    c: Coincident(g622,g623)
    c: Coincident(g623,g624)
    c: Coincident(g624,g625)
    c: Coincident(g625,g626)
    c: Coincident(g626,g627)
    c: Coincident(g627,g628)
    c: Coincident(g628,g629)
    c: Coincident(g629,g630)
    c: Coincident(g630,g631)
    c: Coincident(g631,g632)
    c: Coincident(g632,g633)
    c: Coincident(g633,g634)
    c: Coincident(g634,g635)
    c: Coincident(g635,g636)
    c: Coincident(g636,g637)
    c: Coincident(g637,g638)
    c: Coincident(g638,g639)
    c: Coincident(g639,g640)
    c: Coincident(g640,g641)
    c: Coincident(g641,g642)
    c: Coincident(g642,g643)
    c: Coincident(g643,g644)
    c: Coincident(g644,g645)
    c: Coincident(g645,g646)
    c: Coincident(g646,g647)
    c: Coincident(g647,g648)
    c: Coincident(g648,g649)
    c: Coincident(g649,g650)
    c: Coincident(g650,g651)
    c: Coincident(g651,g652)
    c: Coincident(g652,g653)
    c: Coincident(g653,g654)
    c: Coincident(g654,g655)
    c: Coincident(g655,g656)
    c: Coincident(g656,g657)
    c: Coincident(g657,g658)
    c: Coincident(g658,g659)
    c: Coincident(g659,g660)
    c: Coincident(g660,g661)
    c: Coincident(g661,g662)
    c: Coincident(g662,g663)
    c: Coincident(g663,g664)
    c: Coincident(g664,g665)
    c: Coincident(g665,g666)
    c: Coincident(g666,g667)
    c: Coincident(g667,g668)
    c: Coincident(g668,g669)
    c: Coincident(g669,g670)
    c: Coincident(g670,g671)
    c: Coincident(g671,g672)
    c: Coincident(g672,g673)
    c: Coincident(g673,g674)
    c: Coincident(g674,g675)
    c: Coincident(g675,g588)
    c: Coincident(g676,g677)
    c: Coincident(g677,g678)
    c: Coincident(g678,g679)
    c: Coincident(g679,g680)
    c: Coincident(g680,g681)
    c: Coincident(g681,g682)
    c: Coincident(g682,g683)
    c: Coincident(g683,g684)
    c: Coincident(g684,g685)
    c: Coincident(g685,g686)
    c: Coincident(g686,g687)
    c: Coincident(g687,g688)
    c: Coincident(g688,g689)
    c: Coincident(g689,g690)
    c: Coincident(g690,g691)
    c: Coincident(g691,g676)
    c: Coincident(g692,g693)
    c: Coincident(g693,g694)
    c: Coincident(g694,g695)
    c: Coincident(g695,g696)
    c: Coincident(g696,g697)
    c: Coincident(g697,g698)
    c: Coincident(g698,g699)
    c: Coincident(g699,g700)
    c: Coincident(g700,g701)
    c: Coincident(g701,g702)
    c: Coincident(g702,g703)
    c: Coincident(g703,g704)
    c: Coincident(g704,g705)
    c: Coincident(g705,g706)
    c: Coincident(g706,g707)
    c: Coincident(g707,g708)
    c: Coincident(g708,g709)
    c: Coincident(g709,g710)
    c: Coincident(g710,g711)
    c: Coincident(g711,g712)
    c: Coincident(g712,g713)
    c: Coincident(g713,g714)
    c: Coincident(g714,g715)
    c: Coincident(g715,g716)
    c: Coincident(g716,g717)
    c: Coincident(g717,g718)
    c: Coincident(g718,g719)
    c: Coincident(g719,g720)
    c: Coincident(g720,g721)
    c: Coincident(g721,g722)
    c: Coincident(g722,g723)
    c: Coincident(g723,g724)
    c: Coincident(g724,g725)
    c: Coincident(g725,g726)
    c: Coincident(g726,g727)
    c: Coincident(g727,g728)
    c: Coincident(g728,g729)
    c: Coincident(g729,g730)
    c: Coincident(g730,g731)
    c: Coincident(g731,g692)
    c: Coincident(g732,g733)
    c: Coincident(g733,g734)
    c: Coincident(g734,g735)
    c: Coincident(g735,g736)
    c: Coincident(g736,g737)
    c: Coincident(g737,g738)
    c: Coincident(g738,g739)
    c: Coincident(g739,g740)
    c: Coincident(g740,g741)
    c: Coincident(g741,g742)
    c: Coincident(g742,g743)
    c: Coincident(g743,g744)
    c: Coincident(g744,g745)
    c: Coincident(g745,g746)
    c: Coincident(g746,g747)
    c: Coincident(g747,g748)
    c: Coincident(g748,g749)
    c: Coincident(g749,g750)
    c: Coincident(g750,g751)
    c: Coincident(g751,g752)
    c: Coincident(g752,g753)
    c: Coincident(g753,g754)
    c: Coincident(g754,g755)
    c: Coincident(g755,g756)
    c: Coincident(g756,g757)
    c: Coincident(g757,g758)
    c: Coincident(g758,g759)
    c: Coincident(g759,g760)
    c: Coincident(g760,g761)
    c: Coincident(g761,g762)
    c: Coincident(g762,g763)
    c: Coincident(g763,g732)
    c: Coincident(g764,g765)
    c: Coincident(g765,g766)
    c: Coincident(g766,g767)
    c: Coincident(g767,g768)
    c: Coincident(g768,g769)
    c: Coincident(g769,g770)
    c: Coincident(g770,g771)
    c: Coincident(g771,g772)
    c: Coincident(g772,g773)
    c: Coincident(g773,g774)
    c: Coincident(g774,g775)
    c: Coincident(g775,g776)
    c: Coincident(g776,g777)
    c: Coincident(g777,g778)
    c: Coincident(g778,g779)
    c: Coincident(g779,g780)
    c: Coincident(g780,g781)
    c: Coincident(g781,g782)
    c: Coincident(g782,g783)
    c: Coincident(g783,g784)
    c: Coincident(g784,g785)
    c: Coincident(g785,g786)
    c: Coincident(g786,g787)
    c: Coincident(g787,g764)
    c: Coincident(g788,g789)
    c: Coincident(g789,g790)
    c: Coincident(g790,g791)
    c: Coincident(g791,g792)
    c: Coincident(g792,g793)
    c: Coincident(g793,g794)
    c: Coincident(g794,g795)
    c: Coincident(g795,g796)
    c: Coincident(g796,g797)
    c: Coincident(g797,g798)
    c: Coincident(g798,g799)
    c: Coincident(g799,g800)
    c: Coincident(g800,g801)
    c: Coincident(g801,g802)
    c: Coincident(g802,g803)
    c: Coincident(g803,g804)
    c: Coincident(g804,g805)
    c: Coincident(g805,g806)
    c: Coincident(g806,g807)
    c: Coincident(g807,g808)
    c: Coincident(g808,g809)
    c: Coincident(g809,g810)
    c: Coincident(g810,g811)
    c: Coincident(g811,g812)
    c: Coincident(g812,g813)
    c: Coincident(g813,g814)
    c: Coincident(g814,g815)
    c: Coincident(g815,g816)
    c: Coincident(g816,g817)
    c: Coincident(g817,g818)
    c: Coincident(g818,g819)
    c: Coincident(g819,g820)
    c: Coincident(g820,g821)
    c: Coincident(g821,g822)
    c: Coincident(g822,g823)
    c: Coincident(g823,g824)
    c: Coincident(g824,g825)
    c: Coincident(g825,g826)
    c: Coincident(g826,g827)
    c: Coincident(g827,g828)
    c: Coincident(g828,g829)
    c: Coincident(g829,g830)
    c: Coincident(g830,g831)
    c: Coincident(g831,g832)
    c: Coincident(g832,g833)
    c: Coincident(g833,g834)
    c: Coincident(g834,g835)
    c: Coincident(g835,g836)
    c: Coincident(g836,g837)
    c: Coincident(g837,g838)
    c: Coincident(g838,g839)
    c: Coincident(g839,g840)
    c: Coincident(g840,g841)
    c: Coincident(g841,g842)
    c: Coincident(g842,g843)
    c: Coincident(g843,g844)
    c: Coincident(g844,g845)
    c: Coincident(g845,g846)
    c: Coincident(g846,g847)
    c: Coincident(g847,g848)
    c: Coincident(g848,g849)
    c: Coincident(g849,g850)
    c: Coincident(g850,g851)
    c: Coincident(g851,g852)
    c: Coincident(g852,g853)
    c: Coincident(g853,g854)
    c: Coincident(g854,g855)
    c: Coincident(g855,g856)
    c: Coincident(g856,g857)
    c: Coincident(g857,g858)
    c: Coincident(g858,g859)
    c: Coincident(g859,g788)
FEATURE [Sketcher::SketchObject] Sketch028  label="16 Bit VS009"
  FullyConstrained = false
  Placement = pos=(8.14,42.5,-10) rot=(1,0,0;3.14159rad)
  sketch-geometry (860):
    g0: BSplineCurve PolesCount=2 KnotsCount=2 Degree=1 IsPeriodic=0
    g1: BSplineCurve PolesCount=2 KnotsCount=2 Degree=1 IsPeriodic=0
    g2: BSplineCurve PolesCount=2 KnotsCount=2 Degree=1 IsPeriodic=0
    g3: BSplineCurve PolesCount=2 KnotsCount=2 Degree=1 IsPeriodic=0
    g4: BSplineCurve PolesCount=2 KnotsCount=2 Degree=1 IsPeriodic=0
    g5: BSplineCurve PolesCount=2 KnotsCount=2 Degree=1 IsPeriodic=0
    g6: BSplineCurve PolesCount=2 KnotsCount=2 Degree=1 IsPeriodic=0
    g7: BSplineCurve PolesCount=2 KnotsCount=2 Degree=1 IsPeriodic=0
    g8: BSplineCurve PolesCount=2 KnotsCount=2 Degree=1 IsPeriodic=0
    g9: BSplineCurve PolesCount=2 KnotsCount=2 Degree=1 IsPeriodic=0
    g10: BSplineCurve PolesCount=2 KnotsCount=2 Degree=1 IsPeriodic=0
    g11: BSplineCurve PolesCount=2 KnotsCount=2 Degree=1 IsPeriodic=0
    g12: BSplineCurve PolesCount=2 KnotsCount=2 Degree=1 IsPeriodic=0
    g13: BSplineCurve PolesCount=2 KnotsCount=2 Degree=1 IsPeriodic=0
    g14: BSplineCurve PolesCount=2 KnotsCount=2 Degree=1 IsPeriodic=0
    g15: BSplineCurve PolesCount=2 KnotsCount=2 Degree=1 IsPeriodic=0
    g16: BSplineCurve PolesCount=2 KnotsCount=2 Degree=1 IsPeriodic=0
    g17: BSplineCurve PolesCount=2 KnotsCount=2 Degree=1 IsPeriodic=0
    g18: BSplineCurve PolesCount=2 KnotsCount=2 Degree=1 IsPeriodic=0
    g19: BSplineCurve PolesCount=2 KnotsCount=2 Degree=1 IsPeriodic=0
    g20: BSplineCurve PolesCount=2 KnotsCount=2 Degree=1 IsPeriodic=0
    g21: BSplineCurve PolesCount=2 KnotsCount=2 Degree=1 IsPeriodic=0
    g22: BSplineCurve PolesCount=2 KnotsCount=2 Degree=1 IsPeriodic=0
    g23: BSplineCurve PolesCount=2 KnotsCount=2 Degree=1 IsPeriodic=0
    g24: BSplineCurve PolesCount=2 KnotsCount=2 Degree=1 IsPeriodic=0
    g25: BSplineCurve PolesCount=2 KnotsCount=2 Degree=1 IsPeriodic=0
    g26: BSplineCurve PolesCount=2 KnotsCount=2 Degree=1 IsPeriodic=0
    g27: BSplineCurve PolesCount=2 KnotsCount=2 Degree=1 IsPeriodic=0
    g28: BSplineCurve PolesCount=2 KnotsCount=2 Degree=1 IsPeriodic=0
    g29: BSplineCurve PolesCount=2 KnotsCount=2 Degree=1 IsPeriodic=0
    g30: BSplineCurve PolesCount=2 KnotsCount=2 Degree=1 IsPeriodic=0
    g31: BSplineCurve PolesCount=2 KnotsCount=2 Degree=1 IsPeriodic=0
    g32: BSplineCurve PolesCount=2 KnotsCount=2 Degree=1 IsPeriodic=0
    g33: BSplineCurve PolesCount=2 KnotsCount=2 Degree=1 IsPeriodic=0
    g34: BSplineCurve PolesCount=2 KnotsCount=2 Degree=1 IsPeriodic=0
    g35: BSplineCurve PolesCount=2 KnotsCount=2 Degree=1 IsPeriodic=0
    g36: BSplineCurve PolesCount=2 KnotsCount=2 Degree=1 IsPeriodic=0
    g37: BSplineCurve PolesCount=2 KnotsCount=2 Degree=1 IsPeriodic=0
    g38: BSplineCurve PolesCount=2 KnotsCount=2 Degree=1 IsPeriodic=0
    g39: BSplineCurve PolesCount=2 KnotsCount=2 Degree=1 IsPeriodic=0
    g40: BSplineCurve PolesCount=2 KnotsCount=2 Degree=1 IsPeriodic=0
    g41: BSplineCurve PolesCount=2 KnotsCount=2 Degree=1 IsPeriodic=0
    g42: BSplineCurve PolesCount=2 KnotsCount=2 Degree=1 IsPeriodic=0
    g43: BSplineCurve PolesCount=2 KnotsCount=2 Degree=1 IsPeriodic=0
    g44: BSplineCurve PolesCount=2 KnotsCount=2 Degree=1 IsPeriodic=0
    g45: BSplineCurve PolesCount=2 KnotsCount=2 Degree=1 IsPeriodic=0
    g46: BSplineCurve PolesCount=2 KnotsCount=2 Degree=1 IsPeriodic=0
    g47: BSplineCurve PolesCount=2 KnotsCount=2 Degree=1 IsPeriodic=0
    g48: BSplineCurve PolesCount=2 KnotsCount=2 Degree=1 IsPeriodic=0
    g49: BSplineCurve PolesCount=2 KnotsCount=2 Degree=1 IsPeriodic=0
    g50: BSplineCurve PolesCount=2 KnotsCount=2 Degree=1 IsPeriodic=0
    g51: BSplineCurve PolesCount=2 KnotsCount=2 Degree=1 IsPeriodic=0
    g52: BSplineCurve PolesCount=2 KnotsCount=2 Degree=1 IsPeriodic=0
    g53: BSplineCurve PolesCount=2 KnotsCount=2 Degree=1 IsPeriodic=0
    g54: BSplineCurve PolesCount=2 KnotsCount=2 Degree=1 IsPeriodic=0
    g55: BSplineCurve PolesCount=2 KnotsCount=2 Degree=1 IsPeriodic=0
    g56: BSplineCurve PolesCount=2 KnotsCount=2 Degree=1 IsPeriodic=0
    g57: BSplineCurve PolesCount=2 KnotsCount=2 Degree=1 IsPeriodic=0
    g58: BSplineCurve PolesCount=2 KnotsCount=2 Degree=1 IsPeriodic=0
    g59: BSplineCurve PolesCount=2 KnotsCount=2 Degree=1 IsPeriodic=0
    g60: BSplineCurve PolesCount=2 KnotsCount=2 Degree=1 IsPeriodic=0
    g61: BSplineCurve PolesCount=2 KnotsCount=2 Degree=1 IsPeriodic=0
    g62: BSplineCurve PolesCount=2 KnotsCount=2 Degree=1 IsPeriodic=0
    g63: BSplineCurve PolesCount=2 KnotsCount=2 Degree=1 IsPeriodic=0
    g64: BSplineCurve PolesCount=2 KnotsCount=2 Degree=1 IsPeriodic=0
    g65: BSplineCurve PolesCount=2 KnotsCount=2 Degree=1 IsPeriodic=0
    g66: BSplineCurve PolesCount=2 KnotsCount=2 Degree=1 IsPeriodic=0
    g67: BSplineCurve PolesCount=2 KnotsCount=2 Degree=1 IsPeriodic=0
    g68: BSplineCurve PolesCount=2 KnotsCount=2 Degree=1 IsPeriodic=0
    g69: BSplineCurve PolesCount=2 KnotsCount=2 Degree=1 IsPeriodic=0
    g70: BSplineCurve PolesCount=2 KnotsCount=2 Degree=1 IsPeriodic=0
    g71: BSplineCurve PolesCount=2 KnotsCount=2 Degree=1 IsPeriodic=0
    g72: BSplineCurve PolesCount=2 KnotsCount=2 Degree=1 IsPeriodic=0
    g73: BSplineCurve PolesCount=2 KnotsCount=2 Degree=1 IsPeriodic=0
    g74: BSplineCurve PolesCount=2 KnotsCount=2 Degree=1 IsPeriodic=0
    g75: BSplineCurve PolesCount=2 KnotsCount=2 Degree=1 IsPeriodic=0
    g76: BSplineCurve PolesCount=2 KnotsCount=2 Degree=1 IsPeriodic=0
    g77: BSplineCurve PolesCount=2 KnotsCount=2 Degree=1 IsPeriodic=0
    g78: BSplineCurve PolesCount=2 KnotsCount=2 Degree=1 IsPeriodic=0
    g79: BSplineCurve PolesCount=2 KnotsCount=2 Degree=1 IsPeriodic=0
    g80: BSplineCurve PolesCount=2 KnotsCount=2 Degree=1 IsPeriodic=0
    g81: BSplineCurve PolesCount=2 KnotsCount=2 Degree=1 IsPeriodic=0
    g82: BSplineCurve PolesCount=2 KnotsCount=2 Degree=1 IsPeriodic=0
    g83: BSplineCurve PolesCount=2 KnotsCount=2 Degree=1 IsPeriodic=0
    g84: BSplineCurve PolesCount=2 KnotsCount=2 Degree=1 IsPeriodic=0
    g85: BSplineCurve PolesCount=2 KnotsCount=2 Degree=1 IsPeriodic=0
    g86: BSplineCurve PolesCount=2 KnotsCount=2 Degree=1 IsPeriodic=0
    g87: BSplineCurve PolesCount=2 KnotsCount=2 Degree=1 IsPeriodic=0
    g88: BSplineCurve PolesCount=2 KnotsCount=2 Degree=1 IsPeriodic=0
    g89: BSplineCurve PolesCount=2 KnotsCount=2 Degree=1 IsPeriodic=0
    g90: BSplineCurve PolesCount=2 KnotsCount=2 Degree=1 IsPeriodic=0
    g91: BSplineCurve PolesCount=2 KnotsCount=2 Degree=1 IsPeriodic=0
    g92: BSplineCurve PolesCount=2 KnotsCount=2 Degree=1 IsPeriodic=0
    g93: BSplineCurve PolesCount=2 KnotsCount=2 Degree=1 IsPeriodic=0
    g94: BSplineCurve PolesCount=2 KnotsCount=2 Degree=1 IsPeriodic=0
    g95: BSplineCurve PolesCount=2 KnotsCount=2 Degree=1 IsPeriodic=0
    g96: BSplineCurve PolesCount=2 KnotsCount=2 Degree=1 IsPeriodic=0
    g97: BSplineCurve PolesCount=2 KnotsCount=2 Degree=1 IsPeriodic=0
    g98: BSplineCurve PolesCount=2 KnotsCount=2 Degree=1 IsPeriodic=0
    g99: BSplineCurve PolesCount=2 KnotsCount=2 Degree=1 IsPeriodic=0
    g100: BSplineCurve PolesCount=2 KnotsCount=2 Degree=1 IsPeriodic=0
    g101: BSplineCurve PolesCount=2 KnotsCount=2 Degree=1 IsPeriodic=0
    g102: BSplineCurve PolesCount=2 KnotsCount=2 Degree=1 IsPeriodic=0
    g103: BSplineCurve PolesCount=2 KnotsCount=2 Degree=1 IsPeriodic=0
    g104: BSplineCurve PolesCount=2 KnotsCount=2 Degree=1 IsPeriodic=0
    g105: BSplineCurve PolesCount=2 KnotsCount=2 Degree=1 IsPeriodic=0
    g106: BSplineCurve PolesCount=2 KnotsCount=2 Degree=1 IsPeriodic=0
    g107: BSplineCurve PolesCount=2 KnotsCount=2 Degree=1 IsPeriodic=0
    g108: BSplineCurve PolesCount=2 KnotsCount=2 Degree=1 IsPeriodic=0
    g109: BSplineCurve PolesCount=2 KnotsCount=2 Degree=1 IsPeriodic=0
    g110: BSplineCurve PolesCount=2 KnotsCount=2 Degree=1 IsPeriodic=0
    g111: BSplineCurve PolesCount=2 KnotsCount=2 Degree=1 IsPeriodic=0
    g112: BSplineCurve PolesCount=2 KnotsCount=2 Degree=1 IsPeriodic=0
    g113: BSplineCurve PolesCount=2 KnotsCount=2 Degree=1 IsPeriodic=0
    g114: BSplineCurve PolesCount=2 KnotsCount=2 Degree=1 IsPeriodic=0
    g115: BSplineCurve PolesCount=2 KnotsCount=2 Degree=1 IsPeriodic=0
    g116: BSplineCurve PolesCount=2 KnotsCount=2 Degree=1 IsPeriodic=0
    g117: BSplineCurve PolesCount=2 KnotsCount=2 Degree=1 IsPeriodic=0
    g118: BSplineCurve PolesCount=2 KnotsCount=2 Degree=1 IsPeriodic=0
    g119: BSplineCurve PolesCount=2 KnotsCount=2 Degree=1 IsPeriodic=0
    g120: BSplineCurve PolesCount=2 KnotsCount=2 Degree=1 IsPeriodic=0
    g121: BSplineCurve PolesCount=2 KnotsCount=2 Degree=1 IsPeriodic=0
    g122: BSplineCurve PolesCount=2 KnotsCount=2 Degree=1 IsPeriodic=0
    g123: BSplineCurve PolesCount=2 KnotsCount=2 Degree=1 IsPeriodic=0
    g124: BSplineCurve PolesCount=2 KnotsCount=2 Degree=1 IsPeriodic=0
    g125: BSplineCurve PolesCount=2 KnotsCount=2 Degree=1 IsPeriodic=0
    g126: BSplineCurve PolesCount=2 KnotsCount=2 Degree=1 IsPeriodic=0
    g127: BSplineCurve PolesCount=2 KnotsCount=2 Degree=1 IsPeriodic=0
    g128: BSplineCurve PolesCount=2 KnotsCount=2 Degree=1 IsPeriodic=0
    g129: BSplineCurve PolesCount=2 KnotsCount=2 Degree=1 IsPeriodic=0
    g130: BSplineCurve PolesCount=2 KnotsCount=2 Degree=1 IsPeriodic=0
    g131: BSplineCurve PolesCount=2 KnotsCount=2 Degree=1 IsPeriodic=0
    g132: BSplineCurve PolesCount=2 KnotsCount=2 Degree=1 IsPeriodic=0
    g133: BSplineCurve PolesCount=2 KnotsCount=2 Degree=1 IsPeriodic=0
    g134: BSplineCurve PolesCount=2 KnotsCount=2 Degree=1 IsPeriodic=0
    g135: BSplineCurve PolesCount=2 KnotsCount=2 Degree=1 IsPeriodic=0
    g136: BSplineCurve PolesCount=2 KnotsCount=2 Degree=1 IsPeriodic=0
    g137: BSplineCurve PolesCount=2 KnotsCount=2 Degree=1 IsPeriodic=0
    g138: BSplineCurve PolesCount=2 KnotsCount=2 Degree=1 IsPeriodic=0
    g139: BSplineCurve PolesCount=2 KnotsCount=2 Degree=1 IsPeriodic=0
    g140: BSplineCurve PolesCount=2 KnotsCount=2 Degree=1 IsPeriodic=0
    g141: BSplineCurve PolesCount=2 KnotsCount=2 Degree=1 IsPeriodic=0
    g142: BSplineCurve PolesCount=2 KnotsCount=2 Degree=1 IsPeriodic=0
    g143: BSplineCurve PolesCount=2 KnotsCount=2 Degree=1 IsPeriodic=0
    g144: BSplineCurve PolesCount=2 KnotsCount=2 Degree=1 IsPeriodic=0
    g145: BSplineCurve PolesCount=2 KnotsCount=2 Degree=1 IsPeriodic=0
    g146: BSplineCurve PolesCount=2 KnotsCount=2 Degree=1 IsPeriodic=0
    g147: BSplineCurve PolesCount=2 KnotsCount=2 Degree=1 IsPeriodic=0
    g148: BSplineCurve PolesCount=2 KnotsCount=2 Degree=1 IsPeriodic=0
    g149: BSplineCurve PolesCount=2 KnotsCount=2 Degree=1 IsPeriodic=0
    g150: BSplineCurve PolesCount=2 KnotsCount=2 Degree=1 IsPeriodic=0
    g151: BSplineCurve PolesCount=2 KnotsCount=2 Degree=1 IsPeriodic=0
    g152: BSplineCurve PolesCount=2 KnotsCount=2 Degree=1 IsPeriodic=0
    g153: BSplineCurve PolesCount=2 KnotsCount=2 Degree=1 IsPeriodic=0
    g154: BSplineCurve PolesCount=2 KnotsCount=2 Degree=1 IsPeriodic=0
    g155: BSplineCurve PolesCount=2 KnotsCount=2 Degree=1 IsPeriodic=0
    g156: BSplineCurve PolesCount=2 KnotsCount=2 Degree=1 IsPeriodic=0
    g157: BSplineCurve PolesCount=2 KnotsCount=2 Degree=1 IsPeriodic=0
    g158: BSplineCurve PolesCount=2 KnotsCount=2 Degree=1 IsPeriodic=0
    g159: BSplineCurve PolesCount=2 KnotsCount=2 Degree=1 IsPeriodic=0
    g160: BSplineCurve PolesCount=2 KnotsCount=2 Degree=1 IsPeriodic=0
    g161: BSplineCurve PolesCount=2 KnotsCount=2 Degree=1 IsPeriodic=0
    g162: BSplineCurve PolesCount=2 KnotsCount=2 Degree=1 IsPeriodic=0
    g163: BSplineCurve PolesCount=2 KnotsCount=2 Degree=1 IsPeriodic=0
    g164: BSplineCurve PolesCount=2 KnotsCount=2 Degree=1 IsPeriodic=0
    g165: BSplineCurve PolesCount=2 KnotsCount=2 Degree=1 IsPeriodic=0
    g166: BSplineCurve PolesCount=2 KnotsCount=2 Degree=1 IsPeriodic=0
    g167: BSplineCurve PolesCount=2 KnotsCount=2 Degree=1 IsPeriodic=0
    g168: BSplineCurve PolesCount=2 KnotsCount=2 Degree=1 IsPeriodic=0
    g169: BSplineCurve PolesCount=2 KnotsCount=2 Degree=1 IsPeriodic=0
    g170: BSplineCurve PolesCount=2 KnotsCount=2 Degree=1 IsPeriodic=0
    g171: BSplineCurve PolesCount=2 KnotsCount=2 Degree=1 IsPeriodic=0
    g172: BSplineCurve PolesCount=2 KnotsCount=2 Degree=1 IsPeriodic=0
    g173: BSplineCurve PolesCount=2 KnotsCount=2 Degree=1 IsPeriodic=0
    g174: BSplineCurve PolesCount=2 KnotsCount=2 Degree=1 IsPeriodic=0
    g175: BSplineCurve PolesCount=2 KnotsCount=2 Degree=1 IsPeriodic=0
    g176: BSplineCurve PolesCount=2 KnotsCount=2 Degree=1 IsPeriodic=0
    g177: BSplineCurve PolesCount=2 KnotsCount=2 Degree=1 IsPeriodic=0
    g178: BSplineCurve PolesCount=2 KnotsCount=2 Degree=1 IsPeriodic=0
    g179: BSplineCurve PolesCount=2 KnotsCount=2 Degree=1 IsPeriodic=0
    g180: BSplineCurve PolesCount=2 KnotsCount=2 Degree=1 IsPeriodic=0
    g181: BSplineCurve PolesCount=2 KnotsCount=2 Degree=1 IsPeriodic=0
    g182: BSplineCurve PolesCount=2 KnotsCount=2 Degree=1 IsPeriodic=0
    g183: BSplineCurve PolesCount=2 KnotsCount=2 Degree=1 IsPeriodic=0
    g184: BSplineCurve PolesCount=2 KnotsCount=2 Degree=1 IsPeriodic=0
    g185: BSplineCurve PolesCount=2 KnotsCount=2 Degree=1 IsPeriodic=0
    g186: BSplineCurve PolesCount=2 KnotsCount=2 Degree=1 IsPeriodic=0
    g187: BSplineCurve PolesCount=2 KnotsCount=2 Degree=1 IsPeriodic=0
    g188: BSplineCurve PolesCount=2 KnotsCount=2 Degree=1 IsPeriodic=0
    g189: BSplineCurve PolesCount=2 KnotsCount=2 Degree=1 IsPeriodic=0
    g190: BSplineCurve PolesCount=2 KnotsCount=2 Degree=1 IsPeriodic=0
    g191: BSplineCurve PolesCount=2 KnotsCount=2 Degree=1 IsPeriodic=0
    g192: BSplineCurve PolesCount=2 KnotsCount=2 Degree=1 IsPeriodic=0
    g193: BSplineCurve PolesCount=2 KnotsCount=2 Degree=1 IsPeriodic=0
    g194: BSplineCurve PolesCount=2 KnotsCount=2 Degree=1 IsPeriodic=0
    g195: BSplineCurve PolesCount=2 KnotsCount=2 Degree=1 IsPeriodic=0
    g196: BSplineCurve PolesCount=2 KnotsCount=2 Degree=1 IsPeriodic=0
    g197: BSplineCurve PolesCount=2 KnotsCount=2 Degree=1 IsPeriodic=0
    g198: BSplineCurve PolesCount=2 KnotsCount=2 Degree=1 IsPeriodic=0
    g199: BSplineCurve PolesCount=2 KnotsCount=2 Degree=1 IsPeriodic=0
    g200: BSplineCurve PolesCount=2 KnotsCount=2 Degree=1 IsPeriodic=0
    g201: BSplineCurve PolesCount=2 KnotsCount=2 Degree=1 IsPeriodic=0
    g202: BSplineCurve PolesCount=2 KnotsCount=2 Degree=1 IsPeriodic=0
    g203: BSplineCurve PolesCount=2 KnotsCount=2 Degree=1 IsPeriodic=0
    g204: BSplineCurve PolesCount=2 KnotsCount=2 Degree=1 IsPeriodic=0
    g205: BSplineCurve PolesCount=2 KnotsCount=2 Degree=1 IsPeriodic=0
    g206: BSplineCurve PolesCount=2 KnotsCount=2 Degree=1 IsPeriodic=0
    g207: BSplineCurve PolesCount=2 KnotsCount=2 Degree=1 IsPeriodic=0
    g208: BSplineCurve PolesCount=2 KnotsCount=2 Degree=1 IsPeriodic=0
    g209: BSplineCurve PolesCount=2 KnotsCount=2 Degree=1 IsPeriodic=0
    g210: BSplineCurve PolesCount=2 KnotsCount=2 Degree=1 IsPeriodic=0
    g211: BSplineCurve PolesCount=2 KnotsCount=2 Degree=1 IsPeriodic=0
    g212: BSplineCurve PolesCount=2 KnotsCount=2 Degree=1 IsPeriodic=0
    g213: BSplineCurve PolesCount=2 KnotsCount=2 Degree=1 IsPeriodic=0
    g214: BSplineCurve PolesCount=2 KnotsCount=2 Degree=1 IsPeriodic=0
    g215: BSplineCurve PolesCount=2 KnotsCount=2 Degree=1 IsPeriodic=0
    g216: BSplineCurve PolesCount=2 KnotsCount=2 Degree=1 IsPeriodic=0
    g217: BSplineCurve PolesCount=2 KnotsCount=2 Degree=1 IsPeriodic=0
    g218: BSplineCurve PolesCount=2 KnotsCount=2 Degree=1 IsPeriodic=0
    g219: BSplineCurve PolesCount=2 KnotsCount=2 Degree=1 IsPeriodic=0
    g220: BSplineCurve PolesCount=2 KnotsCount=2 Degree=1 IsPeriodic=0
    g221: BSplineCurve PolesCount=2 KnotsCount=2 Degree=1 IsPeriodic=0
    g222: BSplineCurve PolesCount=2 KnotsCount=2 Degree=1 IsPeriodic=0
    g223: BSplineCurve PolesCount=2 KnotsCount=2 Degree=1 IsPeriodic=0
    g224: BSplineCurve PolesCount=2 KnotsCount=2 Degree=1 IsPeriodic=0
    g225: BSplineCurve PolesCount=2 KnotsCount=2 Degree=1 IsPeriodic=0
    g226: BSplineCurve PolesCount=2 KnotsCount=2 Degree=1 IsPeriodic=0
    g227: BSplineCurve PolesCount=2 KnotsCount=2 Degree=1 IsPeriodic=0
    g228: BSplineCurve PolesCount=2 KnotsCount=2 Degree=1 IsPeriodic=0
    g229: BSplineCurve PolesCount=2 KnotsCount=2 Degree=1 IsPeriodic=0
    g230: BSplineCurve PolesCount=2 KnotsCount=2 Degree=1 IsPeriodic=0
    g231: BSplineCurve PolesCount=2 KnotsCount=2 Degree=1 IsPeriodic=0
    g232: BSplineCurve PolesCount=2 KnotsCount=2 Degree=1 IsPeriodic=0
    g233: BSplineCurve PolesCount=2 KnotsCount=2 Degree=1 IsPeriodic=0
    g234: BSplineCurve PolesCount=2 KnotsCount=2 Degree=1 IsPeriodic=0
    g235: BSplineCurve PolesCount=2 KnotsCount=2 Degree=1 IsPeriodic=0
    g236: BSplineCurve PolesCount=2 KnotsCount=2 Degree=1 IsPeriodic=0
    g237: BSplineCurve PolesCount=2 KnotsCount=2 Degree=1 IsPeriodic=0
    g238: BSplineCurve PolesCount=2 KnotsCount=2 Degree=1 IsPeriodic=0
    g239: BSplineCurve PolesCount=2 KnotsCount=2 Degree=1 IsPeriodic=0
    g240: BSplineCurve PolesCount=2 KnotsCount=2 Degree=1 IsPeriodic=0
    g241: BSplineCurve PolesCount=2 KnotsCount=2 Degree=1 IsPeriodic=0
    g242: BSplineCurve PolesCount=2 KnotsCount=2 Degree=1 IsPeriodic=0
    g243: BSplineCurve PolesCount=2 KnotsCount=2 Degree=1 IsPeriodic=0
    g244: BSplineCurve PolesCount=2 KnotsCount=2 Degree=1 IsPeriodic=0
    g245: BSplineCurve PolesCount=2 KnotsCount=2 Degree=1 IsPeriodic=0
    g246: BSplineCurve PolesCount=2 KnotsCount=2 Degree=1 IsPeriodic=0
    g247: BSplineCurve PolesCount=2 KnotsCount=2 Degree=1 IsPeriodic=0
    g248: BSplineCurve PolesCount=2 KnotsCount=2 Degree=1 IsPeriodic=0
    g249: BSplineCurve PolesCount=2 KnotsCount=2 Degree=1 IsPeriodic=0
    g250: BSplineCurve PolesCount=2 KnotsCount=2 Degree=1 IsPeriodic=0
    g251: BSplineCurve PolesCount=2 KnotsCount=2 Degree=1 IsPeriodic=0
    g252: BSplineCurve PolesCount=2 KnotsCount=2 Degree=1 IsPeriodic=0
    g253: BSplineCurve PolesCount=2 KnotsCount=2 Degree=1 IsPeriodic=0
    g254: BSplineCurve PolesCount=2 KnotsCount=2 Degree=1 IsPeriodic=0
    g255: BSplineCurve PolesCount=2 KnotsCount=2 Degree=1 IsPeriodic=0
    g256: BSplineCurve PolesCount=2 KnotsCount=2 Degree=1 IsPeriodic=0
    g257: BSplineCurve PolesCount=2 KnotsCount=2 Degree=1 IsPeriodic=0
    g258: BSplineCurve PolesCount=2 KnotsCount=2 Degree=1 IsPeriodic=0
    g259: BSplineCurve PolesCount=2 KnotsCount=2 Degree=1 IsPeriodic=0
    g260: BSplineCurve PolesCount=2 KnotsCount=2 Degree=1 IsPeriodic=0
    g261: BSplineCurve PolesCount=2 KnotsCount=2 Degree=1 IsPeriodic=0
    g262: BSplineCurve PolesCount=2 KnotsCount=2 Degree=1 IsPeriodic=0
    g263: BSplineCurve PolesCount=2 KnotsCount=2 Degree=1 IsPeriodic=0
    g264: BSplineCurve PolesCount=2 KnotsCount=2 Degree=1 IsPeriodic=0
    g265: BSplineCurve PolesCount=2 KnotsCount=2 Degree=1 IsPeriodic=0
    g266: BSplineCurve PolesCount=2 KnotsCount=2 Degree=1 IsPeriodic=0
    g267: BSplineCurve PolesCount=2 KnotsCount=2 Degree=1 IsPeriodic=0
    g268: BSplineCurve PolesCount=2 KnotsCount=2 Degree=1 IsPeriodic=0
    g269: BSplineCurve PolesCount=2 KnotsCount=2 Degree=1 IsPeriodic=0
    g270: BSplineCurve PolesCount=2 KnotsCount=2 Degree=1 IsPeriodic=0
    g271: BSplineCurve PolesCount=2 KnotsCount=2 Degree=1 IsPeriodic=0
    g272: BSplineCurve PolesCount=2 KnotsCount=2 Degree=1 IsPeriodic=0
    g273: BSplineCurve PolesCount=2 KnotsCount=2 Degree=1 IsPeriodic=0
    g274: BSplineCurve PolesCount=2 KnotsCount=2 Degree=1 IsPeriodic=0
    g275: BSplineCurve PolesCount=2 KnotsCount=2 Degree=1 IsPeriodic=0
    g276: BSplineCurve PolesCount=2 KnotsCount=2 Degree=1 IsPeriodic=0
    g277: BSplineCurve PolesCount=2 KnotsCount=2 Degree=1 IsPeriodic=0
    g278: BSplineCurve PolesCount=2 KnotsCount=2 Degree=1 IsPeriodic=0
    g279: BSplineCurve PolesCount=2 KnotsCount=2 Degree=1 IsPeriodic=0
    g280: BSplineCurve PolesCount=2 KnotsCount=2 Degree=1 IsPeriodic=0
    g281: BSplineCurve PolesCount=2 KnotsCount=2 Degree=1 IsPeriodic=0
    g282: BSplineCurve PolesCount=2 KnotsCount=2 Degree=1 IsPeriodic=0
    g283: BSplineCurve PolesCount=2 KnotsCount=2 Degree=1 IsPeriodic=0
    g284: BSplineCurve PolesCount=2 KnotsCount=2 Degree=1 IsPeriodic=0
    g285: BSplineCurve PolesCount=2 KnotsCount=2 Degree=1 IsPeriodic=0
    g286: BSplineCurve PolesCount=2 KnotsCount=2 Degree=1 IsPeriodic=0
    g287: BSplineCurve PolesCount=2 KnotsCount=2 Degree=1 IsPeriodic=0
    g288: BSplineCurve PolesCount=2 KnotsCount=2 Degree=1 IsPeriodic=0
    g289: BSplineCurve PolesCount=2 KnotsCount=2 Degree=1 IsPeriodic=0
    g290: BSplineCurve PolesCount=2 KnotsCount=2 Degree=1 IsPeriodic=0
    g291: BSplineCurve PolesCount=2 KnotsCount=2 Degree=1 IsPeriodic=0
    g292: BSplineCurve PolesCount=2 KnotsCount=2 Degree=1 IsPeriodic=0
    g293: BSplineCurve PolesCount=2 KnotsCount=2 Degree=1 IsPeriodic=0
    g294: BSplineCurve PolesCount=2 KnotsCount=2 Degree=1 IsPeriodic=0
    g295: BSplineCurve PolesCount=2 KnotsCount=2 Degree=1 IsPeriodic=0
    g296: BSplineCurve PolesCount=2 KnotsCount=2 Degree=1 IsPeriodic=0
    g297: BSplineCurve PolesCount=2 KnotsCount=2 Degree=1 IsPeriodic=0
    g298: BSplineCurve PolesCount=2 KnotsCount=2 Degree=1 IsPeriodic=0
    g299: BSplineCurve PolesCount=2 KnotsCount=2 Degree=1 IsPeriodic=0
    g300: BSplineCurve PolesCount=2 KnotsCount=2 Degree=1 IsPeriodic=0
    g301: BSplineCurve PolesCount=2 KnotsCount=2 Degree=1 IsPeriodic=0
    g302: BSplineCurve PolesCount=2 KnotsCount=2 Degree=1 IsPeriodic=0
    g303: BSplineCurve PolesCount=2 KnotsCount=2 Degree=1 IsPeriodic=0
    g304: BSplineCurve PolesCount=2 KnotsCount=2 Degree=1 IsPeriodic=0
    g305: BSplineCurve PolesCount=2 KnotsCount=2 Degree=1 IsPeriodic=0
    g306: BSplineCurve PolesCount=2 KnotsCount=2 Degree=1 IsPeriodic=0
    g307: BSplineCurve PolesCount=2 KnotsCount=2 Degree=1 IsPeriodic=0
    g308: BSplineCurve PolesCount=2 KnotsCount=2 Degree=1 IsPeriodic=0
    g309: BSplineCurve PolesCount=2 KnotsCount=2 Degree=1 IsPeriodic=0
    g310: BSplineCurve PolesCount=2 KnotsCount=2 Degree=1 IsPeriodic=0
    g311: BSplineCurve PolesCount=2 KnotsCount=2 Degree=1 IsPeriodic=0
    g312: BSplineCurve PolesCount=2 KnotsCount=2 Degree=1 IsPeriodic=0
    g313: BSplineCurve PolesCount=2 KnotsCount=2 Degree=1 IsPeriodic=0
    g314: BSplineCurve PolesCount=2 KnotsCount=2 Degree=1 IsPeriodic=0
    g315: BSplineCurve PolesCount=2 KnotsCount=2 Degree=1 IsPeriodic=0
    g316: BSplineCurve PolesCount=2 KnotsCount=2 Degree=1 IsPeriodic=0
    g317: BSplineCurve PolesCount=2 KnotsCount=2 Degree=1 IsPeriodic=0
    g318: BSplineCurve PolesCount=2 KnotsCount=2 Degree=1 IsPeriodic=0
    g319: BSplineCurve PolesCount=2 KnotsCount=2 Degree=1 IsPeriodic=0
    g320: BSplineCurve PolesCount=2 KnotsCount=2 Degree=1 IsPeriodic=0
    g321: BSplineCurve PolesCount=2 KnotsCount=2 Degree=1 IsPeriodic=0
    g322: BSplineCurve PolesCount=2 KnotsCount=2 Degree=1 IsPeriodic=0
    g323: BSplineCurve PolesCount=2 KnotsCount=2 Degree=1 IsPeriodic=0
    g324: BSplineCurve PolesCount=2 KnotsCount=2 Degree=1 IsPeriodic=0
    g325: BSplineCurve PolesCount=2 KnotsCount=2 Degree=1 IsPeriodic=0
    g326: BSplineCurve PolesCount=2 KnotsCount=2 Degree=1 IsPeriodic=0
    g327: BSplineCurve PolesCount=2 KnotsCount=2 Degree=1 IsPeriodic=0
    g328: BSplineCurve PolesCount=2 KnotsCount=2 Degree=1 IsPeriodic=0
    g329: BSplineCurve PolesCount=2 KnotsCount=2 Degree=1 IsPeriodic=0
    g330: BSplineCurve PolesCount=2 KnotsCount=2 Degree=1 IsPeriodic=0
    g331: BSplineCurve PolesCount=2 KnotsCount=2 Degree=1 IsPeriodic=0
    g332: BSplineCurve PolesCount=2 KnotsCount=2 Degree=1 IsPeriodic=0
    g333: BSplineCurve PolesCount=2 KnotsCount=2 Degree=1 IsPeriodic=0
    g334: BSplineCurve PolesCount=2 KnotsCount=2 Degree=1 IsPeriodic=0
    g335: BSplineCurve PolesCount=2 KnotsCount=2 Degree=1 IsPeriodic=0
    g336: BSplineCurve PolesCount=2 KnotsCount=2 Degree=1 IsPeriodic=0
    g337: BSplineCurve PolesCount=2 KnotsCount=2 Degree=1 IsPeriodic=0
    g338: BSplineCurve PolesCount=2 KnotsCount=2 Degree=1 IsPeriodic=0
    g339: BSplineCurve PolesCount=2 KnotsCount=2 Degree=1 IsPeriodic=0
    g340: BSplineCurve PolesCount=2 KnotsCount=2 Degree=1 IsPeriodic=0
    g341: BSplineCurve PolesCount=2 KnotsCount=2 Degree=1 IsPeriodic=0
    g342: BSplineCurve PolesCount=2 KnotsCount=2 Degree=1 IsPeriodic=0
    g343: BSplineCurve PolesCount=2 KnotsCount=2 Degree=1 IsPeriodic=0
    g344: BSplineCurve PolesCount=2 KnotsCount=2 Degree=1 IsPeriodic=0
    g345: BSplineCurve PolesCount=2 KnotsCount=2 Degree=1 IsPeriodic=0
    g346: BSplineCurve PolesCount=2 KnotsCount=2 Degree=1 IsPeriodic=0
    g347: BSplineCurve PolesCount=2 KnotsCount=2 Degree=1 IsPeriodic=0
    g348: BSplineCurve PolesCount=2 KnotsCount=2 Degree=1 IsPeriodic=0
    g349: BSplineCurve PolesCount=2 KnotsCount=2 Degree=1 IsPeriodic=0
    g350: BSplineCurve PolesCount=2 KnotsCount=2 Degree=1 IsPeriodic=0
    g351: BSplineCurve PolesCount=2 KnotsCount=2 Degree=1 IsPeriodic=0
    g352: BSplineCurve PolesCount=2 KnotsCount=2 Degree=1 IsPeriodic=0
    g353: BSplineCurve PolesCount=2 KnotsCount=2 Degree=1 IsPeriodic=0
    g354: BSplineCurve PolesCount=2 KnotsCount=2 Degree=1 IsPeriodic=0
    g355: BSplineCurve PolesCount=2 KnotsCount=2 Degree=1 IsPeriodic=0
    g356: BSplineCurve PolesCount=2 KnotsCount=2 Degree=1 IsPeriodic=0
    g357: BSplineCurve PolesCount=2 KnotsCount=2 Degree=1 IsPeriodic=0
    g358: BSplineCurve PolesCount=2 KnotsCount=2 Degree=1 IsPeriodic=0
    g359: BSplineCurve PolesCount=2 KnotsCount=2 Degree=1 IsPeriodic=0
    g360: BSplineCurve PolesCount=2 KnotsCount=2 Degree=1 IsPeriodic=0
    g361: BSplineCurve PolesCount=2 KnotsCount=2 Degree=1 IsPeriodic=0
    g362: BSplineCurve PolesCount=2 KnotsCount=2 Degree=1 IsPeriodic=0
    g363: BSplineCurve PolesCount=2 KnotsCount=2 Degree=1 IsPeriodic=0
    g364: BSplineCurve PolesCount=2 KnotsCount=2 Degree=1 IsPeriodic=0
    g365: BSplineCurve PolesCount=2 KnotsCount=2 Degree=1 IsPeriodic=0
    g366: BSplineCurve PolesCount=2 KnotsCount=2 Degree=1 IsPeriodic=0
    g367: BSplineCurve PolesCount=2 KnotsCount=2 Degree=1 IsPeriodic=0
    g368: BSplineCurve PolesCount=2 KnotsCount=2 Degree=1 IsPeriodic=0
    g369: BSplineCurve PolesCount=2 KnotsCount=2 Degree=1 IsPeriodic=0
    g370: BSplineCurve PolesCount=2 KnotsCount=2 Degree=1 IsPeriodic=0
    g371: BSplineCurve PolesCount=2 KnotsCount=2 Degree=1 IsPeriodic=0
    g372: BSplineCurve PolesCount=2 KnotsCount=2 Degree=1 IsPeriodic=0
    g373: BSplineCurve PolesCount=2 KnotsCount=2 Degree=1 IsPeriodic=0
    g374: BSplineCurve PolesCount=2 KnotsCount=2 Degree=1 IsPeriodic=0
    g375: BSplineCurve PolesCount=2 KnotsCount=2 Degree=1 IsPeriodic=0
    g376: BSplineCurve PolesCount=2 KnotsCount=2 Degree=1 IsPeriodic=0
    g377: BSplineCurve PolesCount=2 KnotsCount=2 Degree=1 IsPeriodic=0
    g378: BSplineCurve PolesCount=2 KnotsCount=2 Degree=1 IsPeriodic=0
    g379: BSplineCurve PolesCount=2 KnotsCount=2 Degree=1 IsPeriodic=0
    g380: BSplineCurve PolesCount=2 KnotsCount=2 Degree=1 IsPeriodic=0
    g381: BSplineCurve PolesCount=2 KnotsCount=2 Degree=1 IsPeriodic=0
    g382: BSplineCurve PolesCount=2 KnotsCount=2 Degree=1 IsPeriodic=0
    g383: BSplineCurve PolesCount=2 KnotsCount=2 Degree=1 IsPeriodic=0
    g384: BSplineCurve PolesCount=2 KnotsCount=2 Degree=1 IsPeriodic=0
    g385: BSplineCurve PolesCount=2 KnotsCount=2 Degree=1 IsPeriodic=0
    g386: BSplineCurve PolesCount=2 KnotsCount=2 Degree=1 IsPeriodic=0
    g387: BSplineCurve PolesCount=2 KnotsCount=2 Degree=1 IsPeriodic=0
    g388: BSplineCurve PolesCount=2 KnotsCount=2 Degree=1 IsPeriodic=0
    g389: BSplineCurve PolesCount=2 KnotsCount=2 Degree=1 IsPeriodic=0
    g390: BSplineCurve PolesCount=2 KnotsCount=2 Degree=1 IsPeriodic=0
    g391: BSplineCurve PolesCount=2 KnotsCount=2 Degree=1 IsPeriodic=0
    g392: BSplineCurve PolesCount=2 KnotsCount=2 Degree=1 IsPeriodic=0
    g393: BSplineCurve PolesCount=2 KnotsCount=2 Degree=1 IsPeriodic=0
    g394: BSplineCurve PolesCount=2 KnotsCount=2 Degree=1 IsPeriodic=0
    g395: BSplineCurve PolesCount=2 KnotsCount=2 Degree=1 IsPeriodic=0
    g396: BSplineCurve PolesCount=2 KnotsCount=2 Degree=1 IsPeriodic=0
    g397: BSplineCurve PolesCount=2 KnotsCount=2 Degree=1 IsPeriodic=0
    g398: BSplineCurve PolesCount=2 KnotsCount=2 Degree=1 IsPeriodic=0
    g399: BSplineCurve PolesCount=2 KnotsCount=2 Degree=1 IsPeriodic=0
    ... +460 more geometry lines
  constraints (860):
    c: Coincident(g0,g1)
    c: Coincident(g1,g2)
    c: Coincident(g2,g3)
    c: Coincident(g3,g4)
    c: Coincident(g4,g5)
    c: Coincident(g5,g6)
    c: Coincident(g6,g7)
    c: Coincident(g7,g8)
    c: Coincident(g8,g9)
    c: Coincident(g9,g10)
    c: Coincident(g10,g11)
    c: Coincident(g11,g12)
    c: Coincident(g12,g13)
    c: Coincident(g13,g14)
    c: Coincident(g14,g15)
    c: Coincident(g15,g16)
    c: Coincident(g16,g17)
    c: Coincident(g17,g18)
    c: Coincident(g18,g19)
    c: Coincident(g19,g20)
    c: Coincident(g20,g21)
    c: Coincident(g21,g22)
    c: Coincident(g22,g23)
    c: Coincident(g23,g24)
    c: Coincident(g24,g25)
    c: Coincident(g25,g26)
    c: Coincident(g26,g27)
    c: Coincident(g27,g28)
    c: Coincident(g28,g29)
    c: Coincident(g29,g30)
    c: Coincident(g30,g31)
    c: Coincident(g31,g32)
    c: Coincident(g32,g33)
    c: Coincident(g33,g34)
    c: Coincident(g34,g35)
    c: Coincident(g35,g36)
    c: Coincident(g36,g37)
    c: Coincident(g37,g38)
    c: Coincident(g38,g39)
    c: Coincident(g39,g40)
    c: Coincident(g40,g41)
    c: Coincident(g41,g42)
    c: Coincident(g42,g43)
    c: Coincident(g43,g44)
    c: Coincident(g44,g45)
    c: Coincident(g45,g46)
    c: Coincident(g46,g47)
    c: Coincident(g47,g48)
    c: Coincident(g48,g49)
    c: Coincident(g49,g50)
    c: Coincident(g50,g51)
    c: Coincident(g51,g52)
    c: Coincident(g52,g53)
    c: Coincident(g53,g54)
    c: Coincident(g54,g55)
    c: Coincident(g55,g56)
    c: Coincident(g56,g57)
    c: Coincident(g57,g58)
    c: Coincident(g58,g59)
    c: Coincident(g59,g60)
    c: Coincident(g60,g61)
    c: Coincident(g61,g62)
    c: Coincident(g62,g63)
    c: Coincident(g63,g64)
    c: Coincident(g64,g65)
    c: Coincident(g65,g66)
    c: Coincident(g66,g67)
    c: Coincident(g67,g68)
    c: Coincident(g68,g69)
    c: Coincident(g69,g70)
    c: Coincident(g70,g71)
    c: Coincident(g71,g72)
    c: Coincident(g72,g73)
    c: Coincident(g73,g74)
    c: Coincident(g74,g75)
    c: Coincident(g75,g76)
    c: Coincident(g76,g77)
    c: Coincident(g77,g78)
    c: Coincident(g78,g79)
    c: Coincident(g79,g80)
    c: Coincident(g80,g81)
    c: Coincident(g81,g82)
    c: Coincident(g82,g83)
    c: Coincident(g83,g84)
    c: Coincident(g84,g85)
    c: Coincident(g85,g86)
    c: Coincident(g86,g87)
    c: Coincident(g87,g0)
    c: Coincident(g88,g89)
    c: Coincident(g89,g90)
    c: Coincident(g90,g91)
    c: Coincident(g91,g92)
    c: Coincident(g92,g93)
    c: Coincident(g93,g94)
    c: Coincident(g94,g95)
    c: Coincident(g95,g96)
    c: Coincident(g96,g97)
    c: Coincident(g97,g98)
    c: Coincident(g98,g99)
    c: Coincident(g99,g100)
    c: Coincident(g100,g101)
    c: Coincident(g101,g102)
    c: Coincident(g102,g103)
    c: Coincident(g103,g104)
    c: Coincident(g104,g105)
    c: Coincident(g105,g106)
    c: Coincident(g106,g107)
    c: Coincident(g107,g108)
    c: Coincident(g108,g109)
    c: Coincident(g109,g110)
    c: Coincident(g110,g111)
    c: Coincident(g111,g112)
    c: Coincident(g112,g113)
    c: Coincident(g113,g114)
    c: Coincident(g114,g115)
    c: Coincident(g115,g116)
    c: Coincident(g116,g117)
    c: Coincident(g117,g118)
    c: Coincident(g118,g119)
    c: Coincident(g119,g120)
    c: Coincident(g120,g121)
    c: Coincident(g121,g122)
    c: Coincident(g122,g123)
    c: Coincident(g123,g124)
    c: Coincident(g124,g125)
    c: Coincident(g125,g126)
    c: Coincident(g126,g127)
    c: Coincident(g127,g88)
    c: Coincident(g128,g129)
    c: Coincident(g129,g130)
    c: Coincident(g130,g131)
    c: Coincident(g131,g132)
    c: Coincident(g132,g133)
    c: Coincident(g133,g134)
    c: Coincident(g134,g135)
    c: Coincident(g135,g136)
    c: Coincident(g136,g137)
    c: Coincident(g137,g138)
    c: Coincident(g138,g139)
    c: Coincident(g139,g140)
    c: Coincident(g140,g141)
    c: Coincident(g141,g142)
    c: Coincident(g142,g143)
    c: Coincident(g143,g144)
    c: Coincident(g144,g145)
    c: Coincident(g145,g146)
    c: Coincident(g146,g147)
    c: Coincident(g147,g148)
    c: Coincident(g148,g149)
    c: Coincident(g149,g150)
    c: Coincident(g150,g151)
    c: Coincident(g151,g152)
    c: Coincident(g152,g153)
    c: Coincident(g153,g154)
    c: Coincident(g154,g155)
    c: Coincident(g155,g156)
    c: Coincident(g156,g157)
    c: Coincident(g157,g158)
    c: Coincident(g158,g159)
    c: Coincident(g159,g160)
    c: Coincident(g160,g161)
    c: Coincident(g161,g162)
    c: Coincident(g162,g163)
    c: Coincident(g163,g164)
    c: Coincident(g164,g165)
    c: Coincident(g165,g166)
    c: Coincident(g166,g167)
    c: Coincident(g167,g168)
    c: Coincident(g168,g169)
    c: Coincident(g169,g170)
    c: Coincident(g170,g171)
    c: Coincident(g171,g172)
    c: Coincident(g172,g173)
    c: Coincident(g173,g174)
    c: Coincident(g174,g175)
    c: Coincident(g175,g176)
    c: Coincident(g176,g177)
    c: Coincident(g177,g178)
    c: Coincident(g178,g179)
    c: Coincident(g179,g180)
    c: Coincident(g180,g181)
    c: Coincident(g181,g182)
    c: Coincident(g182,g183)
    c: Coincident(g183,g184)
    c: Coincident(g184,g185)
    c: Coincident(g185,g186)
    c: Coincident(g186,g187)
    c: Coincident(g187,g188)
    c: Coincident(g188,g189)
    c: Coincident(g189,g190)
    c: Coincident(g190,g191)
    c: Coincident(g191,g192)
    c: Coincident(g192,g193)
    c: Coincident(g193,g194)
    c: Coincident(g194,g195)
    c: Coincident(g195,g196)
    c: Coincident(g196,g197)
    c: Coincident(g197,g198)
    c: Coincident(g198,g199)
    c: Coincident(g199,g200)
    c: Coincident(g200,g201)
    c: Coincident(g201,g202)
    c: Coincident(g202,g203)
    c: Coincident(g203,g204)
    c: Coincident(g204,g205)
    c: Coincident(g205,g206)
    c: Coincident(g206,g207)
    c: Coincident(g207,g208)
    c: Coincident(g208,g209)
    c: Coincident(g209,g210)
    c: Coincident(g210,g211)
    c: Coincident(g211,g212)
    c: Coincident(g212,g213)
    c: Coincident(g213,g214)
    c: Coincident(g214,g215)
    c: Coincident(g215,g216)
    c: Coincident(g216,g217)
    c: Coincident(g217,g218)
    c: Coincident(g218,g219)
    c: Coincident(g219,g220)
    c: Coincident(g220,g221)
    c: Coincident(g221,g222)
    c: Coincident(g222,g223)
    c: Coincident(g223,g224)
    c: Coincident(g224,g225)
    c: Coincident(g225,g226)
    c: Coincident(g226,g227)
    c: Coincident(g227,g228)
    c: Coincident(g228,g229)
    c: Coincident(g229,g230)
    c: Coincident(g230,g231)
    c: Coincident(g231,g232)
    c: Coincident(g232,g233)
    c: Coincident(g233,g234)
    c: Coincident(g234,g235)
    c: Coincident(g235,g236)
    c: Coincident(g236,g237)
    c: Coincident(g237,g238)
    c: Coincident(g238,g239)
    c: Coincident(g239,g128)
    c: Coincident(g240,g241)
    c: Coincident(g241,g242)
    c: Coincident(g242,g243)
    c: Coincident(g243,g244)
    c: Coincident(g244,g245)
    c: Coincident(g245,g246)
    c: Coincident(g246,g247)
    c: Coincident(g247,g248)
    c: Coincident(g248,g249)
    c: Coincident(g249,g250)
    c: Coincident(g250,g251)
    c: Coincident(g251,g252)
    c: Coincident(g252,g253)
    c: Coincident(g253,g254)
    c: Coincident(g254,g255)
    c: Coincident(g255,g256)
    c: Coincident(g256,g257)
    c: Coincident(g257,g258)
    c: Coincident(g258,g259)
    c: Coincident(g259,g260)
    c: Coincident(g260,g261)
    c: Coincident(g261,g262)
    c: Coincident(g262,g263)
    c: Coincident(g263,g264)
    c: Coincident(g264,g265)
    c: Coincident(g265,g266)
    c: Coincident(g266,g267)
    c: Coincident(g267,g268)
    c: Coincident(g268,g269)
    c: Coincident(g269,g270)
    c: Coincident(g270,g271)
    c: Coincident(g271,g272)
    c: Coincident(g272,g273)
    c: Coincident(g273,g274)
    c: Coincident(g274,g275)
    c: Coincident(g275,g276)
    c: Coincident(g276,g277)
    c: Coincident(g277,g278)
    c: Coincident(g278,g279)
    c: Coincident(g279,g280)
    c: Coincident(g280,g281)
    c: Coincident(g281,g282)
    c: Coincident(g282,g283)
    c: Coincident(g283,g284)
    c: Coincident(g284,g285)
    c: Coincident(g285,g286)
    c: Coincident(g286,g287)
    c: Coincident(g287,g240)
    c: Coincident(g288,g289)
    c: Coincident(g289,g290)
    c: Coincident(g290,g291)
    c: Coincident(g291,g292)
    c: Coincident(g292,g293)
    c: Coincident(g293,g294)
    c: Coincident(g294,g295)
    c: Coincident(g295,g296)
    c: Coincident(g296,g297)
    c: Coincident(g297,g298)
    c: Coincident(g298,g299)
    c: Coincident(g299,g300)
    c: Coincident(g300,g301)
    c: Coincident(g301,g302)
    c: Coincident(g302,g303)
    c: Coincident(g303,g304)
    c: Coincident(g304,g305)
    c: Coincident(g305,g306)
    c: Coincident(g306,g307)
    c: Coincident(g307,g308)
    c: Coincident(g308,g309)
    c: Coincident(g309,g310)
    c: Coincident(g310,g311)
    c: Coincident(g311,g288)
    c: Coincident(g312,g313)
    c: Coincident(g313,g314)
    c: Coincident(g314,g315)
    c: Coincident(g315,g316)
    c: Coincident(g316,g317)
    c: Coincident(g317,g318)
    c: Coincident(g318,g319)
    c: Coincident(g319,g320)
    c: Coincident(g320,g321)
    c: Coincident(g321,g322)
    c: Coincident(g322,g323)
    c: Coincident(g323,g324)
    c: Coincident(g324,g325)
    c: Coincident(g325,g326)
    c: Coincident(g326,g327)
    c: Coincident(g327,g312)
    c: Coincident(g328,g329)
    c: Coincident(g329,g330)
    c: Coincident(g330,g331)
    c: Coincident(g331,g332)
    c: Coincident(g332,g333)
    c: Coincident(g333,g334)
    c: Coincident(g334,g335)
    c: Coincident(g335,g336)
    c: Coincident(g336,g337)
    c: Coincident(g337,g338)
    c: Coincident(g338,g339)
    c: Coincident(g339,g340)
    c: Coincident(g340,g341)
    c: Coincident(g341,g342)
    c: Coincident(g342,g343)
    c: Coincident(g343,g344)
    c: Coincident(g344,g345)
    c: Coincident(g345,g346)
    c: Coincident(g346,g347)
    c: Coincident(g347,g348)
    c: Coincident(g348,g349)
    c: Coincident(g349,g350)
    c: Coincident(g350,g351)
    c: Coincident(g351,g352)
    c: Coincident(g352,g353)
    c: Coincident(g353,g354)
    c: Coincident(g354,g355)
    c: Coincident(g355,g356)
    c: Coincident(g356,g357)
    c: Coincident(g357,g358)
    c: Coincident(g358,g359)
    c: Coincident(g359,g360)
    c: Coincident(g360,g361)
    c: Coincident(g361,g362)
    c: Coincident(g362,g363)
    c: Coincident(g363,g364)
    c: Coincident(g364,g365)
    c: Coincident(g365,g366)
    c: Coincident(g366,g367)
    c: Coincident(g367,g368)
    c: Coincident(g368,g369)
    c: Coincident(g369,g370)
    c: Coincident(g370,g371)
    c: Coincident(g371,g372)
    c: Coincident(g372,g373)
    c: Coincident(g373,g374)
    c: Coincident(g374,g375)
    c: Coincident(g375,g376)
    c: Coincident(g376,g377)
    c: Coincident(g377,g378)
    c: Coincident(g378,g379)
    c: Coincident(g379,g380)
    c: Coincident(g380,g381)
    c: Coincident(g381,g382)
    c: Coincident(g382,g383)
    c: Coincident(g383,g384)
    c: Coincident(g384,g385)
    c: Coincident(g385,g386)
    c: Coincident(g386,g387)
    c: Coincident(g387,g388)
    c: Coincident(g388,g389)
    c: Coincident(g389,g390)
    c: Coincident(g390,g391)
    c: Coincident(g391,g392)
    c: Coincident(g392,g393)
    c: Coincident(g393,g394)
    c: Coincident(g394,g395)
    c: Coincident(g395,g396)
    c: Coincident(g396,g397)
    c: Coincident(g397,g398)
    c: Coincident(g398,g399)
    c: Coincident(g399,g328)
    c: Coincident(g400,g401)
    c: Coincident(g401,g402)
    c: Coincident(g402,g403)
    c: Coincident(g403,g404)
    c: Coincident(g404,g405)
    c: Coincident(g405,g406)
    c: Coincident(g406,g407)
    c: Coincident(g407,g408)
    c: Coincident(g408,g409)
    c: Coincident(g409,g410)
    c: Coincident(g410,g411)
    c: Coincident(g411,g412)
    c: Coincident(g412,g413)
    c: Coincident(g413,g414)
    c: Coincident(g414,g415)
    c: Coincident(g415,g416)
    c: Coincident(g416,g417)
    c: Coincident(g417,g418)
    c: Coincident(g418,g419)
    c: Coincident(g419,g420)
    c: Coincident(g420,g421)
    c: Coincident(g421,g422)
    c: Coincident(g422,g423)
    c: Coincident(g423,g400)
    c: Coincident(g424,g425)
    c: Coincident(g425,g426)
    c: Coincident(g426,g427)
    c: Coincident(g427,g428)
    c: Coincident(g428,g429)
    c: Coincident(g429,g430)
    c: Coincident(g430,g431)
    c: Coincident(g431,g432)
    c: Coincident(g432,g433)
    c: Coincident(g433,g434)
    c: Coincident(g434,g435)
    c: Coincident(g435,g436)
    c: Coincident(g436,g437)
    c: Coincident(g437,g438)
    c: Coincident(g438,g439)
    c: Coincident(g439,g440)
    c: Coincident(g440,g441)
    c: Coincident(g441,g442)
    c: Coincident(g442,g443)
    c: Coincident(g443,g444)
    c: Coincident(g444,g445)
    c: Coincident(g445,g446)
    c: Coincident(g446,g447)
    c: Coincident(g447,g448)
    c: Coincident(g448,g449)
    c: Coincident(g449,g450)
    c: Coincident(g450,g451)
    c: Coincident(g451,g452)
    c: Coincident(g452,g453)
    c: Coincident(g453,g454)
    c: Coincident(g454,g455)
    c: Coincident(g455,g456)
    c: Coincident(g456,g457)
    c: Coincident(g457,g458)
    c: Coincident(g458,g459)
    c: Coincident(g459,g460)
    c: Coincident(g460,g461)
    c: Coincident(g461,g462)
    c: Coincident(g462,g463)
    c: Coincident(g463,g464)
    c: Coincident(g464,g465)
    c: Coincident(g465,g466)
    c: Coincident(g466,g467)
    c: Coincident(g467,g468)
    c: Coincident(g468,g469)
    c: Coincident(g469,g470)
    c: Coincident(g470,g471)
    c: Coincident(g471,g472)
    c: Coincident(g472,g473)
    c: Coincident(g473,g474)
    c: Coincident(g474,g475)
    c: Coincident(g475,g476)
    c: Coincident(g476,g477)
    c: Coincident(g477,g478)
    c: Coincident(g478,g479)
    c: Coincident(g479,g424)
    c: Coincident(g480,g481)
    c: Coincident(g481,g482)
    c: Coincident(g482,g483)
    c: Coincident(g483,g484)
    c: Coincident(g484,g485)
    c: Coincident(g485,g486)
    c: Coincident(g486,g487)
    c: Coincident(g487,g488)
    c: Coincident(g488,g489)
    c: Coincident(g489,g490)
    c: Coincident(g490,g491)
    c: Coincident(g491,g492)
    c: Coincident(g492,g493)
    c: Coincident(g493,g494)
    c: Coincident(g494,g495)
    c: Coincident(g495,g480)
    c: Coincident(g496,g497)
    c: Coincident(g497,g498)
    c: Coincident(g498,g499)
    c: Coincident(g499,g500)
    c: Coincident(g500,g501)
    c: Coincident(g501,g502)
    c: Coincident(g502,g503)
    c: Coincident(g503,g504)
    c: Coincident(g504,g505)
    c: Coincident(g505,g506)
    c: Coincident(g506,g507)
    c: Coincident(g507,g508)
    c: Coincident(g508,g509)
    c: Coincident(g509,g510)
    c: Coincident(g510,g511)
    c: Coincident(g511,g512)
    c: Coincident(g512,g513)
    c: Coincident(g513,g514)
    c: Coincident(g514,g515)
    c: Coincident(g515,g516)
    c: Coincident(g516,g517)
    c: Coincident(g517,g518)
    c: Coincident(g518,g519)
    c: Coincident(g519,g520)
    c: Coincident(g520,g521)
    c: Coincident(g521,g522)
    c: Coincident(g522,g523)
    c: Coincident(g523,g524)
    c: Coincident(g524,g525)
    c: Coincident(g525,g526)
    c: Coincident(g526,g527)
    c: Coincident(g527,g528)
    c: Coincident(g528,g529)
    c: Coincident(g529,g530)
    c: Coincident(g530,g531)
    c: Coincident(g531,g532)
    c: Coincident(g532,g533)
    c: Coincident(g533,g534)
    c: Coincident(g534,g535)
    c: Coincident(g535,g496)
    c: Coincident(g536,g537)
    c: Coincident(g537,g538)
    c: Coincident(g538,g539)
    c: Coincident(g539,g540)
    c: Coincident(g540,g541)
    c: Coincident(g541,g542)
    c: Coincident(g542,g543)
    c: Coincident(g543,g544)
    c: Coincident(g544,g545)
    c: Coincident(g545,g546)
    c: Coincident(g546,g547)
    c: Coincident(g547,g548)
    c: Coincident(g548,g549)
    c: Coincident(g549,g550)
    c: Coincident(g550,g551)
    c: Coincident(g551,g552)
    c: Coincident(g552,g553)
    c: Coincident(g553,g554)
    c: Coincident(g554,g555)
    c: Coincident(g555,g556)
    c: Coincident(g556,g557)
    c: Coincident(g557,g558)
    c: Coincident(g558,g559)
    c: Coincident(g559,g560)
    c: Coincident(g560,g561)
    c: Coincident(g561,g562)
    c: Coincident(g562,g563)
    c: Coincident(g563,g564)
    c: Coincident(g564,g565)
    c: Coincident(g565,g566)
    c: Coincident(g566,g567)
    c: Coincident(g567,g568)
    c: Coincident(g568,g569)
    c: Coincident(g569,g570)
    c: Coincident(g570,g571)
    c: Coincident(g571,g572)
    c: Coincident(g572,g573)
    c: Coincident(g573,g574)
    c: Coincident(g574,g575)
    c: Coincident(g575,g536)
    c: Coincident(g576,g577)
    c: Coincident(g577,g578)
    c: Coincident(g578,g579)
    c: Coincident(g579,g580)
    c: Coincident(g580,g581)
    c: Coincident(g581,g582)
    c: Coincident(g582,g583)
    c: Coincident(g583,g584)
    c: Coincident(g584,g585)
    c: Coincident(g585,g586)
    c: Coincident(g586,g587)
    c: Coincident(g587,g576)
    c: Coincident(g588,g589)
    c: Coincident(g589,g590)
    c: Coincident(g590,g591)
    c: Coincident(g591,g592)
    c: Coincident(g592,g593)
    c: Coincident(g593,g594)
    c: Coincident(g594,g595)
    c: Coincident(g595,g596)
    c: Coincident(g596,g597)
    c: Coincident(g597,g598)
    c: Coincident(g598,g599)
    c: Coincident(g599,g600)
    c: Coincident(g600,g601)
    c: Coincident(g601,g602)
    c: Coincident(g602,g603)
    c: Coincident(g603,g604)
    c: Coincident(g604,g605)
    c: Coincident(g605,g606)
    c: Coincident(g606,g607)
    c: Coincident(g607,g608)
    c: Coincident(g608,g609)
    c: Coincident(g609,g610)
    c: Coincident(g610,g611)
    c: Coincident(g611,g612)
    c: Coincident(g612,g613)
    c: Coincident(g613,g614)
    c: Coincident(g614,g615)
    c: Coincident(g615,g616)
    c: Coincident(g616,g617)
    c: Coincident(g617,g618)
    c: Coincident(g618,g619)
    c: Coincident(g619,g620)
    c: Coincident(g620,g621)
    c: Coincident(g621,g622)
    c: Coincident(g622,g623)
    c: Coincident(g623,g624)
    c: Coincident(g624,g625)
    c: Coincident(g625,g626)
    c: Coincident(g626,g627)
    c: Coincident(g627,g628)
    c: Coincident(g628,g629)
    c: Coincident(g629,g630)
    c: Coincident(g630,g631)
    c: Coincident(g631,g632)
    c: Coincident(g632,g633)
    c: Coincident(g633,g634)
    c: Coincident(g634,g635)
    c: Coincident(g635,g636)
    c: Coincident(g636,g637)
    c: Coincident(g637,g638)
    c: Coincident(g638,g639)
    c: Coincident(g639,g640)
    c: Coincident(g640,g641)
    c: Coincident(g641,g642)
    c: Coincident(g642,g643)
    c: Coincident(g643,g644)
    c: Coincident(g644,g645)
    c: Coincident(g645,g646)
    c: Coincident(g646,g647)
    c: Coincident(g647,g648)
    c: Coincident(g648,g649)
    c: Coincident(g649,g650)
    c: Coincident(g650,g651)
    c: Coincident(g651,g652)
    c: Coincident(g652,g653)
    c: Coincident(g653,g654)
    c: Coincident(g654,g655)
    c: Coincident(g655,g656)
    c: Coincident(g656,g657)
    c: Coincident(g657,g658)
    c: Coincident(g658,g659)
    c: Coincident(g659,g660)
    c: Coincident(g660,g661)
    c: Coincident(g661,g662)
    c: Coincident(g662,g663)
    c: Coincident(g663,g664)
    c: Coincident(g664,g665)
    c: Coincident(g665,g666)
    c: Coincident(g666,g667)
    c: Coincident(g667,g668)
    c: Coincident(g668,g669)
    c: Coincident(g669,g670)
    c: Coincident(g670,g671)
    c: Coincident(g671,g672)
    c: Coincident(g672,g673)
    c: Coincident(g673,g674)
    c: Coincident(g674,g675)
    c: Coincident(g675,g588)
    c: Coincident(g676,g677)
    c: Coincident(g677,g678)
    c: Coincident(g678,g679)
    c: Coincident(g679,g680)
    c: Coincident(g680,g681)
    c: Coincident(g681,g682)
    c: Coincident(g682,g683)
    c: Coincident(g683,g684)
    c: Coincident(g684,g685)
    c: Coincident(g685,g686)
    c: Coincident(g686,g687)
    c: Coincident(g687,g688)
    c: Coincident(g688,g689)
    c: Coincident(g689,g690)
    c: Coincident(g690,g691)
    c: Coincident(g691,g676)
    c: Coincident(g692,g693)
    c: Coincident(g693,g694)
    c: Coincident(g694,g695)
    c: Coincident(g695,g696)
    c: Coincident(g696,g697)
    c: Coincident(g697,g698)
    c: Coincident(g698,g699)
    c: Coincident(g699,g700)
    c: Coincident(g700,g701)
    c: Coincident(g701,g702)
    c: Coincident(g702,g703)
    c: Coincident(g703,g704)
    c: Coincident(g704,g705)
    c: Coincident(g705,g706)
    c: Coincident(g706,g707)
    c: Coincident(g707,g708)
    c: Coincident(g708,g709)
    c: Coincident(g709,g710)
    c: Coincident(g710,g711)
    c: Coincident(g711,g712)
    c: Coincident(g712,g713)
    c: Coincident(g713,g714)
    c: Coincident(g714,g715)
    c: Coincident(g715,g716)
    c: Coincident(g716,g717)
    c: Coincident(g717,g718)
    c: Coincident(g718,g719)
    c: Coincident(g719,g720)
    c: Coincident(g720,g721)
    c: Coincident(g721,g722)
    c: Coincident(g722,g723)
    c: Coincident(g723,g724)
    c: Coincident(g724,g725)
    c: Coincident(g725,g726)
    c: Coincident(g726,g727)
    c: Coincident(g727,g728)
    c: Coincident(g728,g729)
    c: Coincident(g729,g730)
    c: Coincident(g730,g731)
    c: Coincident(g731,g692)
    c: Coincident(g732,g733)
    c: Coincident(g733,g734)
    c: Coincident(g734,g735)
    c: Coincident(g735,g736)
    c: Coincident(g736,g737)
    c: Coincident(g737,g738)
    c: Coincident(g738,g739)
    c: Coincident(g739,g740)
    c: Coincident(g740,g741)
    c: Coincident(g741,g742)
    c: Coincident(g742,g743)
    c: Coincident(g743,g744)
    c: Coincident(g744,g745)
    c: Coincident(g745,g746)
    c: Coincident(g746,g747)
    c: Coincident(g747,g748)
    c: Coincident(g748,g749)
    c: Coincident(g749,g750)
    c: Coincident(g750,g751)
    c: Coincident(g751,g752)
    c: Coincident(g752,g753)
    c: Coincident(g753,g754)
    c: Coincident(g754,g755)
    c: Coincident(g755,g756)
    c: Coincident(g756,g757)
    c: Coincident(g757,g758)
    c: Coincident(g758,g759)
    c: Coincident(g759,g760)
    c: Coincident(g760,g761)
    c: Coincident(g761,g762)
    c: Coincident(g762,g763)
    c: Coincident(g763,g732)
    c: Coincident(g764,g765)
    c: Coincident(g765,g766)
    c: Coincident(g766,g767)
    c: Coincident(g767,g768)
    c: Coincident(g768,g769)
    c: Coincident(g769,g770)
    c: Coincident(g770,g771)
    c: Coincident(g771,g772)
    c: Coincident(g772,g773)
    c: Coincident(g773,g774)
    c: Coincident(g774,g775)
    c: Coincident(g775,g776)
    c: Coincident(g776,g777)
    c: Coincident(g777,g778)
    c: Coincident(g778,g779)
    c: Coincident(g779,g780)
    c: Coincident(g780,g781)
    c: Coincident(g781,g782)
    c: Coincident(g782,g783)
    c: Coincident(g783,g784)
    c: Coincident(g784,g785)
    c: Coincident(g785,g786)
    c: Coincident(g786,g787)
    c: Coincident(g787,g764)
    c: Coincident(g788,g789)
    c: Coincident(g789,g790)
    c: Coincident(g790,g791)
    c: Coincident(g791,g792)
    c: Coincident(g792,g793)
    c: Coincident(g793,g794)
    c: Coincident(g794,g795)
    c: Coincident(g795,g796)
    c: Coincident(g796,g797)
    c: Coincident(g797,g798)
    c: Coincident(g798,g799)
    c: Coincident(g799,g800)
    c: Coincident(g800,g801)
    c: Coincident(g801,g802)
    c: Coincident(g802,g803)
    c: Coincident(g803,g804)
    c: Coincident(g804,g805)
    c: Coincident(g805,g806)
    c: Coincident(g806,g807)
    c: Coincident(g807,g808)
    c: Coincident(g808,g809)
    c: Coincident(g809,g810)
    c: Coincident(g810,g811)
    c: Coincident(g811,g812)
    c: Coincident(g812,g813)
    c: Coincident(g813,g814)
    c: Coincident(g814,g815)
    c: Coincident(g815,g816)
    c: Coincident(g816,g817)
    c: Coincident(g817,g818)
    c: Coincident(g818,g819)
    c: Coincident(g819,g820)
    c: Coincident(g820,g821)
    c: Coincident(g821,g822)
    c: Coincident(g822,g823)
    c: Coincident(g823,g824)
    c: Coincident(g824,g825)
    c: Coincident(g825,g826)
    c: Coincident(g826,g827)
    c: Coincident(g827,g828)
    c: Coincident(g828,g829)
    c: Coincident(g829,g830)
    c: Coincident(g830,g831)
    c: Coincident(g831,g832)
    c: Coincident(g832,g833)
    c: Coincident(g833,g834)
    c: Coincident(g834,g835)
    c: Coincident(g835,g836)
    c: Coincident(g836,g837)
    c: Coincident(g837,g838)
    c: Coincident(g838,g839)
    c: Coincident(g839,g840)
    c: Coincident(g840,g841)
    c: Coincident(g841,g842)
    c: Coincident(g842,g843)
    c: Coincident(g843,g844)
    c: Coincident(g844,g845)
    c: Coincident(g845,g846)
    c: Coincident(g846,g847)
    c: Coincident(g847,g848)
    c: Coincident(g848,g849)
    c: Coincident(g849,g850)
    c: Coincident(g850,g851)
    c: Coincident(g851,g852)
    c: Coincident(g852,g853)
    c: Coincident(g853,g854)
    c: Coincident(g854,g855)
    c: Coincident(g855,g856)
    c: Coincident(g856,g857)
    c: Coincident(g857,g858)
    c: Coincident(g858,g859)
    c: Coincident(g859,g788)
FEATURE [PartDesign::Pocket] Pocket002
  BaseFeature = -> Fillet002
  Direction = (0,0,1)
  Length = 0
  Length2 = 5
  Offset = 0.5
  Profile = -> Sketch022
  ReferenceAxis = -> Sketch022 [N_Axis]
  Type = 3
  UpToFace = -> Fillet002 [Face59]
FEATURE [PartDesign::Body] Body002  label="x4 Shelf"
  BaseFeature = -> ShapeBinder
  Group = -> [Clone,Sketch003,Pad003,Sketch012,Pad012,Chamfer003,Fillet002,Sketch022,Pocket002]
  Origin = -> Origin004
  Placement = pos=(0,72,0) rot=(0,0,1;0rad)
  Tip = -> Pocket002
FEATURE [PartDesign::Pocket] Pocket003
  BaseFeature = -> Fillet003
  Direction = (0,0,1)
  Length = 0
  Length2 = 5
  Offset = 0.5
  Profile = -> Sketch023
  ReferenceAxis = -> Sketch023 [N_Axis]
  Type = 3
  UpToFace = -> Fillet003 [Face84]
FEATURE [PartDesign::Body] Body003  label="x5 Shelf"
  BaseFeature = -> ShapeBinder
  Group = -> [Clone001,Sketch004,Pad004,Sketch013,Pad013,Chamfer004,Chamfer010,Fillet003,Sketch023,Pocket003]
  Origin = -> Origin005
  Placement = pos=(0,132,0) rot=(0,0,1;0rad)
  Tip = -> Pocket003
FEATURE [PartDesign::Pocket] Pocket004
  BaseFeature = -> Fillet004
  Direction = (0,0,1)
  Length = 0
  Length2 = 5
  Offset = 0.5
  Placement = pos=(0,175,0) rot=(0,0,1;0rad)
  Profile = -> Sketch024
  ReferenceAxis = -> Sketch024 [N_Axis]
  Type = 3
  UpToFace = -> Fillet004 [Face78]
FEATURE [PartDesign::Body] Body004  label="x6 Shelf"
  BaseFeature = -> ShapeBinder
  Group = -> [Clone002,Sketch005,Pad005,Sketch015,Pad014,Chamfer009,Fillet004,Sketch024,Pocket004]
  Origin = -> Origin006
  Placement = pos=(0,24,0) rot=(0,0,1;0rad)
  Tip = -> Pocket004
FEATURE [PartDesign::Pocket] Pocket005
  BaseFeature = -> Fillet005
  Direction = (0,0,1)
  Length = 0
  Length2 = 5
  Offset = 0.5
  Profile = -> Sketch025
  ReferenceAxis = -> Sketch025 [N_Axis]
  Type = 3
  UpToFace = -> Fillet005 [Face87]
FEATURE [PartDesign::Body] Body005  label="x7 Shelf"
  BaseFeature = -> ShapeBinder
  Group = -> [Clone003,Sketch006,Pad006,Sketch016,Pad015,Chamfer008,Fillet005,Sketch025,Pocket005]
  Origin = -> Origin007
  Placement = pos=(0,276,0) rot=(0,0,1;0rad)
  Tip = -> Pocket005
FEATURE [PartDesign::Pocket] Pocket006
  BaseFeature = -> Fillet006
  Direction = (0,0,1)
  Length = 0
  Length2 = 5
  Offset = 0.5
  Profile = -> Sketch026
  ReferenceAxis = -> Sketch026 [N_Axis]
  Type = 3
  UpToFace = -> Fillet006 [Face96]
FEATURE [PartDesign::Body] Body006  label="x8 Shelf"
  BaseFeature = -> ShapeBinder
  Group = -> [Clone004,Sketch007,Pad007,Sketch008,Pad008,Chamfer007,Fillet006,Sketch026,Pocket006]
  Origin = -> Origin008
  Placement = pos=(0,360,0) rot=(0,0,1;0rad)
  Tip = -> Pocket006
FEATURE [PartDesign::Pocket] Pocket007
  BaseFeature = -> Fillet007
  Direction = (0,0,1)
  Length = 0
  Length2 = 5
  Offset = 0.5
  Profile = -> Sketch027
  ReferenceAxis = -> Sketch027 [N_Axis]
  Type = 3
  UpToFace = -> Fillet007 [Face105]
FEATURE [PartDesign::Body] Body007  label="x9 Shelf"
  BaseFeature = -> ShapeBinder
  Group = -> [Clone005,Sketch009,Pad009,Sketch017,Pad016,Chamfer006,Fillet007,Sketch027,Pocket007]
  Origin = -> Origin009
  Placement = pos=(0,456,0) rot=(0,0,1;0rad)
  Tip = -> Pocket007
FEATURE [PartDesign::Pocket] Pocket008
  BaseFeature = -> Fillet008
  Direction = (0,0,1)
  Length = 0
  Length2 = 5
  Offset = 0.5
  Profile = -> Sketch028
  ReferenceAxis = -> Sketch028 [N_Axis]
  Type = 3
  UpToFace = -> Fillet008 [Face114]
FEATURE [PartDesign::Body] Body008  label="x10 Shelf"
  BaseFeature = -> ShapeBinder
  Group = -> [Clone006,Sketch010,Pad010,Sketch018,Pad017,Chamfer005,Fillet008,Sketch028,Pocket008]
  Origin = -> Origin010
  Placement = pos=(0,564,0) rot=(0,0,1;0rad)
  Tip = -> Pocket008
FEATURE [App::Part] Part001  label="GB Shelf-"
  Group = -> [Body009,Body002,Body003,Body004,Body005,Body006,Body007,Body008]
  Origin = -> Origin011
FEATURE [PartDesign::FeatureBase] Clone009
  BaseFeature = -> ShapeBinder
FEATURE [PartDesign::Body] Body011
  BaseFeature = -> ShapeBinder
  Group = -> [Clone009]
  Origin = -> Origin015
  Placement = pos=(100,0,0) rot=(0,0,1;0rad)
  Tip = -> Clone009
FEATURE [App::Part] Part002  label="GB Display-"
  Group = -> [Body011]
  Origin = -> Origin014
FEATURE [PartDesign::FeatureBase] Clone010
  BaseFeature = -> ShapeBinder
FEATURE [Sketcher::SketchObject] Sketch029
  ExternalGeometry = -> [Clone010]
  FullyConstrained = true
  MapMode = 5
  Placement = pos=(0,0,-2) rot=(1,0,0;3.14159rad)
  Support = -> [Clone010]
  sketch-geometry (12):
    g0: LineSegment StartX=0 StartY=-5.85 StartZ=0 EndX=0 EndY=5.85 EndZ=0
    g1: LineSegment StartX=61 StartY=-5.85 StartZ=0 EndX=61 EndY=-17.55 EndZ=0
    g2: LineSegment StartX=0 StartY=5.85 StartZ=0 EndX=61 EndY=5.85 EndZ=0
    g3: LineSegment StartX=61 StartY=5.85 StartZ=0 EndX=61 EndY=-17.55 EndZ=0
    g4: LineSegment StartX=61 StartY=-17.55 StartZ=0 EndX=0 EndY=-17.55 EndZ=0
    g5: LineSegment StartX=0 StartY=-17.55 StartZ=0 EndX=0 EndY=5.85 EndZ=0
    g6: LineSegment StartX=-2 StartY=5.85 StartZ=0 EndX=63 EndY=5.85 EndZ=0
    g7: LineSegment StartX=63 StartY=5.85 StartZ=0 EndX=63 EndY=-17.55 EndZ=0
    g8: LineSegment StartX=63 StartY=-17.55 StartZ=0 EndX=-2 EndY=-17.55 EndZ=0
    g9: LineSegment StartX=-2 StartY=-17.55 StartZ=0 EndX=-2 EndY=5.85 EndZ=0
    g10: LineSegment StartX=0 StartY=0 StartZ=0 EndX=-2 EndY=0 EndZ=0
    g11: LineSegment StartX=61 StartY=0 StartZ=0 EndX=63 EndY=0 EndZ=0
  constraints (34):
    c: Vertical(g0)
    c: Symmetric(g-3,g-3,g0)
    c: Equal(g-3,g0)
    c: Vertical(g1)
    c: Equal(g1,g-4)
    c: Symmetric(g-4,g-4,g1)
    c: Coincident(g2,g3)
    c: Coincident(g3,g4)
    c: Coincident(g4,g5)
    c: Coincident(g5,g2)
    c: Horizontal(g2)
    c: Horizontal(g4)
    c: Vertical(g3)
    c: Vertical(g5)
    c: Coincident(g2,g0)
    c: Coincident(g3,g1)
    c: Horizontal(g6)
    c: Coincident(g7,g6)
    c: Vertical(g7)
    c: Coincident(g8,g7)
    c: Horizontal(g8)
    c: Coincident(g9,g8)
    c: Coincident(g9,g6)
    c: Vertical(g9)
    c: PointOnObject(g0,g6)
    c: PointOnObject(g1,g8)
    c: Coincident(g10,g-3)
    c: PointOnObject(g10,g9)
    c: Horizontal(g10)
    c: Coincident(g11,g-4)
    c: PointOnObject(g11,g7)
    c: Horizontal(g11)
    c: Equal(g10,g11)
    c: Distance(g11) = 2
FEATURE [PartDesign::Pad] Pad018
  BaseFeature = -> Clone010
  Direction = (0,0,-1)
  Length = 2
  Length2 = 10
  Profile = -> Sketch029
  ReferenceAxis = -> Sketch029 [N_Axis]
  Reversed = true
  Type = 0
FEATURE [PartDesign::Pad] Pad019
  BaseFeature = -> Pad018
  Direction = (0,0,1)
  Length = 10
  Length2 = 10
  Profile = -> Clone010 [Face1]
  Refine = true
  Type = 3
  UpToFace = -> Pad018 [Face6]
FEATURE [Sketcher::SketchObject] Sketch031
  ExternalGeometry = -> [Pad019]
  FullyConstrained = true
  MapMode = 5
  Placement = pos=(63,0,0) rot=(0.57735,0.57735,0.57735;2.0944rad)
  Support = -> [Pad019]
  sketch-geometry (5):
    g0: LineSegment StartX=9.7 StartY=3.5 StartZ=0 EndX=9.7 EndY=11.75 EndZ=0
    g1: LineSegment StartX=9.7 StartY=11.75 StartZ=0 EndX=10.7 EndY=11.75 EndZ=0
    g2: LineSegment StartX=10.7 StartY=11.75 StartZ=0 EndX=17.55 EndY=0 EndZ=0
    g3: LineSegment StartX=17.55 StartY=0 StartZ=0 EndX=9.7 EndY=0 EndZ=0
    g4: LineSegment StartX=9.7 StartY=0 StartZ=0 EndX=9.7 EndY=3.5 EndZ=0
  constraints (13):
    c: Coincident(g0,g-3)
    c: Vertical(g0)
    c: Coincident(g1,g0)
    c: Horizontal(g1)
    c: Coincident(g2,g1)
    c: Coincident(g2,g-4)
    c: Coincident(g3,g2)
    c: PointOnObject(g3,g-1)
    c: Coincident(g4,g3)
    c: Coincident(g4,g0)
    c: Vertical(g4)
    c: Distance(g1) = 1
    c: Distance(g0) = 8.25
FEATURE [PartDesign::Pad] Pad020
  BaseFeature = -> Pad019
  Direction = (1,0,0)
  Length = 10
  Length2 = 10
  Profile = -> Sketch031
  ReferenceAxis = -> Sketch031 [N_Axis]
  Refine = true
  Type = 3
  UpToFace = -> Pad019 [Face2]
FEATURE [Sketcher::SketchObject] Sketch032
  ExternalGeometry = -> [Pad020]
  FullyConstrained = true
  MapMode = 5
  Placement = pos=(-2,-2e-16,-4e-16) rot=(0.57735,-0.57735,-0.57735;2.0944rad)
  Support = -> [Pad020]
  sketch-geometry (4):
    g0: LineSegment StartX=-2 StartY=3.5 StartZ=0 EndX=-1 EndY=3.5 EndZ=0
    g1: LineSegment StartX=-1 StartY=3.5 StartZ=0 EndX=5.85 EndY=0 EndZ=0
    g2: LineSegment StartX=5.85 StartY=0 StartZ=0 EndX=-2 EndY=0 EndZ=0
    g3: LineSegment StartX=-2 StartY=0 StartZ=0 EndX=-2 EndY=3.5 EndZ=0
  constraints (10):
    c: Coincident(g0,g-3)
    c: Horizontal(g0)
    c: Coincident(g1,g0)
    c: Coincident(g1,g-4)
    c: Coincident(g2,g1)
    c: PointOnObject(g2,g-1)
    c: Coincident(g3,g2)
    c: Coincident(g3,g0)
    c: Vertical(g3)
    c: Distance(g0) = 1
FEATURE [PartDesign::Pad] Pad021
  BaseFeature = -> Pad020
  Direction = (-1,1e-16,-1e-16)
  Length = 10
  Length2 = 10
  Profile = -> Sketch032
  ReferenceAxis = -> Sketch032 [N_Axis]
  Type = 3
  UpToFace = -> Pad020 [Face16]
FEATURE [PartDesign::Pocket] Pocket009
  BaseFeature = -> Pad021
  Direction = (1,0,0)
  Length = 100
  Length2 = 5
  Profile = -> Pad021 [Face17]
  Refine = true
  Type = 0
FEATURE [Sketcher::SketchObject] Sketch033
  ExternalGeometry = -> [Pocket009]
  FullyConstrained = true
  MapMode = 5
  Placement = pos=(0,-5.85,0) rot=(1,0,0;1.5708rad)
  Support = -> [Pocket009]
  sketch-geometry (10):
    g0: LineSegment StartX=59 StartY=3.5 StartZ=0 EndX=60 EndY=3.5 EndZ=0
    g1: LineSegment StartX=60 StartY=3.5 StartZ=0 EndX=63 EndY=3.6e-15 EndZ=0
    g2: LineSegment StartX=59 StartY=11.75 StartZ=0 EndX=63 EndY=11.75 EndZ=0
    g3: LineSegment StartX=63 StartY=11.75 StartZ=0 EndX=63 EndY=3.6e-15 EndZ=0
    g4: LineSegment StartX=-2 StartY=0 StartZ=0 EndX=-2 EndY=11.75 EndZ=0
    g5: LineSegment StartX=2 StartY=3.5 StartZ=0 EndX=1 EndY=3.5 EndZ=0
    g6: LineSegment StartX=-2 StartY=0 StartZ=0 EndX=1 EndY=3.5 EndZ=0
    g7: LineSegment StartX=2 StartY=11.75 StartZ=0 EndX=-2 EndY=11.75 EndZ=0
    g8: LineSegment StartX=59 StartY=3.5 StartZ=0 EndX=59 EndY=11.75 EndZ=0
    g9: LineSegment StartX=2 StartY=3.5 StartZ=0 EndX=2 EndY=11.75 EndZ=0
  constraints (24):
    c: Coincident(g0,g-3)
    c: Horizontal(g0)
    c: Coincident(g1,g0)
    c: Coincident(g1,g-4)
    c: Horizontal(g2)
    c: Coincident(g3,g2)
    c: Coincident(g3,g1)
    c: Coincident(g-5,g2)
    c: Distance(g0) = 1
    c: Coincident(g4,g-6)
    c: Coincident(g4,g-5)
    c: Horizontal(g5)
    c: Coincident(g6,g4)
    c: Coincident(g6,g5)
    c: Coincident(g7,g4)
    c: Equal(g5,g0)
    c: Coincident(g5,g-7)
    c: Coincident(g8,g0)
    c: Vertical(g8)
    c: Coincident(g9,g5)
    c: PointOnObject(g9,g-5)
    c: Vertical(g9)
    c: Coincident(g7,g9)
    c: Coincident(g8,g2)
FEATURE [PartDesign::Pocket] Pocket010
  BaseFeature = -> Pocket009
  Direction = (0,1,-2e-16)
  Length = 100
  Length2 = 5
  Profile = -> Sketch033
  ReferenceAxis = -> Sketch033 [N_Axis]
  Type = 0
FEATURE [PartDesign::Pad] Pad022
  BaseFeature = -> Pocket010
  Direction = (0,-1,0)
  Length = 10
  Length2 = 10
  Profile = -> Pocket010 [Face16]
  Refine = true
  Type = 0
FEATURE [PartDesign::Pad] Pad023
  BaseFeature = -> Pad022
  Direction = (0,-1,0)
  Length = 10
  Length2 = 10
  Profile = -> Pad022 [Face12]
  Refine = true
  Type = 0
FEATURE [PartDesign::Chamfer] Chamfer011
  Angle = 45
  Base = -> Pad023 [Face17]
  BaseFeature = -> Pad023
  ChamferType = 1
  FlipDirection = false
  Refine = true
  Size = 0.25
  Size2 = 3.49
  SupportTransform = false
  UseAllEdges = false
FEATURE [Sketcher::SketchObject] Sketch034  label="16 Bit VS010"
  FullyConstrained = false
  Placement = pos=(52.85,15.99,14.05) rot=(0,0.498284,0.867014;3.14159rad)
  sketch-geometry (860):
    g0: BSplineCurve PolesCount=2 KnotsCount=2 Degree=1 IsPeriodic=0
    g1: BSplineCurve PolesCount=2 KnotsCount=2 Degree=1 IsPeriodic=0
    g2: BSplineCurve PolesCount=2 KnotsCount=2 Degree=1 IsPeriodic=0
    g3: BSplineCurve PolesCount=2 KnotsCount=2 Degree=1 IsPeriodic=0
    g4: BSplineCurve PolesCount=2 KnotsCount=2 Degree=1 IsPeriodic=0
    g5: BSplineCurve PolesCount=2 KnotsCount=2 Degree=1 IsPeriodic=0
    g6: BSplineCurve PolesCount=2 KnotsCount=2 Degree=1 IsPeriodic=0
    g7: BSplineCurve PolesCount=2 KnotsCount=2 Degree=1 IsPeriodic=0
    g8: BSplineCurve PolesCount=2 KnotsCount=2 Degree=1 IsPeriodic=0
    g9: BSplineCurve PolesCount=2 KnotsCount=2 Degree=1 IsPeriodic=0
    g10: BSplineCurve PolesCount=2 KnotsCount=2 Degree=1 IsPeriodic=0
    g11: BSplineCurve PolesCount=2 KnotsCount=2 Degree=1 IsPeriodic=0
    g12: BSplineCurve PolesCount=2 KnotsCount=2 Degree=1 IsPeriodic=0
    g13: BSplineCurve PolesCount=2 KnotsCount=2 Degree=1 IsPeriodic=0
    g14: BSplineCurve PolesCount=2 KnotsCount=2 Degree=1 IsPeriodic=0
    g15: BSplineCurve PolesCount=2 KnotsCount=2 Degree=1 IsPeriodic=0
    g16: BSplineCurve PolesCount=2 KnotsCount=2 Degree=1 IsPeriodic=0
    g17: BSplineCurve PolesCount=2 KnotsCount=2 Degree=1 IsPeriodic=0
    g18: BSplineCurve PolesCount=2 KnotsCount=2 Degree=1 IsPeriodic=0
    g19: BSplineCurve PolesCount=2 KnotsCount=2 Degree=1 IsPeriodic=0
    g20: BSplineCurve PolesCount=2 KnotsCount=2 Degree=1 IsPeriodic=0
    g21: BSplineCurve PolesCount=2 KnotsCount=2 Degree=1 IsPeriodic=0
    g22: BSplineCurve PolesCount=2 KnotsCount=2 Degree=1 IsPeriodic=0
    g23: BSplineCurve PolesCount=2 KnotsCount=2 Degree=1 IsPeriodic=0
    g24: BSplineCurve PolesCount=2 KnotsCount=2 Degree=1 IsPeriodic=0
    g25: BSplineCurve PolesCount=2 KnotsCount=2 Degree=1 IsPeriodic=0
    g26: BSplineCurve PolesCount=2 KnotsCount=2 Degree=1 IsPeriodic=0
    g27: BSplineCurve PolesCount=2 KnotsCount=2 Degree=1 IsPeriodic=0
    g28: BSplineCurve PolesCount=2 KnotsCount=2 Degree=1 IsPeriodic=0
    g29: BSplineCurve PolesCount=2 KnotsCount=2 Degree=1 IsPeriodic=0
    g30: BSplineCurve PolesCount=2 KnotsCount=2 Degree=1 IsPeriodic=0
    g31: BSplineCurve PolesCount=2 KnotsCount=2 Degree=1 IsPeriodic=0
    g32: BSplineCurve PolesCount=2 KnotsCount=2 Degree=1 IsPeriodic=0
    g33: BSplineCurve PolesCount=2 KnotsCount=2 Degree=1 IsPeriodic=0
    g34: BSplineCurve PolesCount=2 KnotsCount=2 Degree=1 IsPeriodic=0
    g35: BSplineCurve PolesCount=2 KnotsCount=2 Degree=1 IsPeriodic=0
    g36: BSplineCurve PolesCount=2 KnotsCount=2 Degree=1 IsPeriodic=0
    g37: BSplineCurve PolesCount=2 KnotsCount=2 Degree=1 IsPeriodic=0
    g38: BSplineCurve PolesCount=2 KnotsCount=2 Degree=1 IsPeriodic=0
    g39: BSplineCurve PolesCount=2 KnotsCount=2 Degree=1 IsPeriodic=0
    g40: BSplineCurve PolesCount=2 KnotsCount=2 Degree=1 IsPeriodic=0
    g41: BSplineCurve PolesCount=2 KnotsCount=2 Degree=1 IsPeriodic=0
    g42: BSplineCurve PolesCount=2 KnotsCount=2 Degree=1 IsPeriodic=0
    g43: BSplineCurve PolesCount=2 KnotsCount=2 Degree=1 IsPeriodic=0
    g44: BSplineCurve PolesCount=2 KnotsCount=2 Degree=1 IsPeriodic=0
    g45: BSplineCurve PolesCount=2 KnotsCount=2 Degree=1 IsPeriodic=0
    g46: BSplineCurve PolesCount=2 KnotsCount=2 Degree=1 IsPeriodic=0
    g47: BSplineCurve PolesCount=2 KnotsCount=2 Degree=1 IsPeriodic=0
    g48: BSplineCurve PolesCount=2 KnotsCount=2 Degree=1 IsPeriodic=0
    g49: BSplineCurve PolesCount=2 KnotsCount=2 Degree=1 IsPeriodic=0
    g50: BSplineCurve PolesCount=2 KnotsCount=2 Degree=1 IsPeriodic=0
    g51: BSplineCurve PolesCount=2 KnotsCount=2 Degree=1 IsPeriodic=0
    g52: BSplineCurve PolesCount=2 KnotsCount=2 Degree=1 IsPeriodic=0
    g53: BSplineCurve PolesCount=2 KnotsCount=2 Degree=1 IsPeriodic=0
    g54: BSplineCurve PolesCount=2 KnotsCount=2 Degree=1 IsPeriodic=0
    g55: BSplineCurve PolesCount=2 KnotsCount=2 Degree=1 IsPeriodic=0
    g56: BSplineCurve PolesCount=2 KnotsCount=2 Degree=1 IsPeriodic=0
    g57: BSplineCurve PolesCount=2 KnotsCount=2 Degree=1 IsPeriodic=0
    g58: BSplineCurve PolesCount=2 KnotsCount=2 Degree=1 IsPeriodic=0
    g59: BSplineCurve PolesCount=2 KnotsCount=2 Degree=1 IsPeriodic=0
    g60: BSplineCurve PolesCount=2 KnotsCount=2 Degree=1 IsPeriodic=0
    g61: BSplineCurve PolesCount=2 KnotsCount=2 Degree=1 IsPeriodic=0
    g62: BSplineCurve PolesCount=2 KnotsCount=2 Degree=1 IsPeriodic=0
    g63: BSplineCurve PolesCount=2 KnotsCount=2 Degree=1 IsPeriodic=0
    g64: BSplineCurve PolesCount=2 KnotsCount=2 Degree=1 IsPeriodic=0
    g65: BSplineCurve PolesCount=2 KnotsCount=2 Degree=1 IsPeriodic=0
    g66: BSplineCurve PolesCount=2 KnotsCount=2 Degree=1 IsPeriodic=0
    g67: BSplineCurve PolesCount=2 KnotsCount=2 Degree=1 IsPeriodic=0
    g68: BSplineCurve PolesCount=2 KnotsCount=2 Degree=1 IsPeriodic=0
    g69: BSplineCurve PolesCount=2 KnotsCount=2 Degree=1 IsPeriodic=0
    g70: BSplineCurve PolesCount=2 KnotsCount=2 Degree=1 IsPeriodic=0
    g71: BSplineCurve PolesCount=2 KnotsCount=2 Degree=1 IsPeriodic=0
    g72: BSplineCurve PolesCount=2 KnotsCount=2 Degree=1 IsPeriodic=0
    g73: BSplineCurve PolesCount=2 KnotsCount=2 Degree=1 IsPeriodic=0
    g74: BSplineCurve PolesCount=2 KnotsCount=2 Degree=1 IsPeriodic=0
    g75: BSplineCurve PolesCount=2 KnotsCount=2 Degree=1 IsPeriodic=0
    g76: BSplineCurve PolesCount=2 KnotsCount=2 Degree=1 IsPeriodic=0
    g77: BSplineCurve PolesCount=2 KnotsCount=2 Degree=1 IsPeriodic=0
    g78: BSplineCurve PolesCount=2 KnotsCount=2 Degree=1 IsPeriodic=0
    g79: BSplineCurve PolesCount=2 KnotsCount=2 Degree=1 IsPeriodic=0
    g80: BSplineCurve PolesCount=2 KnotsCount=2 Degree=1 IsPeriodic=0
    g81: BSplineCurve PolesCount=2 KnotsCount=2 Degree=1 IsPeriodic=0
    g82: BSplineCurve PolesCount=2 KnotsCount=2 Degree=1 IsPeriodic=0
    g83: BSplineCurve PolesCount=2 KnotsCount=2 Degree=1 IsPeriodic=0
    g84: BSplineCurve PolesCount=2 KnotsCount=2 Degree=1 IsPeriodic=0
    g85: BSplineCurve PolesCount=2 KnotsCount=2 Degree=1 IsPeriodic=0
    g86: BSplineCurve PolesCount=2 KnotsCount=2 Degree=1 IsPeriodic=0
    g87: BSplineCurve PolesCount=2 KnotsCount=2 Degree=1 IsPeriodic=0
    g88: BSplineCurve PolesCount=2 KnotsCount=2 Degree=1 IsPeriodic=0
    g89: BSplineCurve PolesCount=2 KnotsCount=2 Degree=1 IsPeriodic=0
    g90: BSplineCurve PolesCount=2 KnotsCount=2 Degree=1 IsPeriodic=0
    g91: BSplineCurve PolesCount=2 KnotsCount=2 Degree=1 IsPeriodic=0
    g92: BSplineCurve PolesCount=2 KnotsCount=2 Degree=1 IsPeriodic=0
    g93: BSplineCurve PolesCount=2 KnotsCount=2 Degree=1 IsPeriodic=0
    g94: BSplineCurve PolesCount=2 KnotsCount=2 Degree=1 IsPeriodic=0
    g95: BSplineCurve PolesCount=2 KnotsCount=2 Degree=1 IsPeriodic=0
    g96: BSplineCurve PolesCount=2 KnotsCount=2 Degree=1 IsPeriodic=0
    g97: BSplineCurve PolesCount=2 KnotsCount=2 Degree=1 IsPeriodic=0
    g98: BSplineCurve PolesCount=2 KnotsCount=2 Degree=1 IsPeriodic=0
    g99: BSplineCurve PolesCount=2 KnotsCount=2 Degree=1 IsPeriodic=0
    g100: BSplineCurve PolesCount=2 KnotsCount=2 Degree=1 IsPeriodic=0
    g101: BSplineCurve PolesCount=2 KnotsCount=2 Degree=1 IsPeriodic=0
    g102: BSplineCurve PolesCount=2 KnotsCount=2 Degree=1 IsPeriodic=0
    g103: BSplineCurve PolesCount=2 KnotsCount=2 Degree=1 IsPeriodic=0
    g104: BSplineCurve PolesCount=2 KnotsCount=2 Degree=1 IsPeriodic=0
    g105: BSplineCurve PolesCount=2 KnotsCount=2 Degree=1 IsPeriodic=0
    g106: BSplineCurve PolesCount=2 KnotsCount=2 Degree=1 IsPeriodic=0
    g107: BSplineCurve PolesCount=2 KnotsCount=2 Degree=1 IsPeriodic=0
    g108: BSplineCurve PolesCount=2 KnotsCount=2 Degree=1 IsPeriodic=0
    g109: BSplineCurve PolesCount=2 KnotsCount=2 Degree=1 IsPeriodic=0
    g110: BSplineCurve PolesCount=2 KnotsCount=2 Degree=1 IsPeriodic=0
    g111: BSplineCurve PolesCount=2 KnotsCount=2 Degree=1 IsPeriodic=0
    g112: BSplineCurve PolesCount=2 KnotsCount=2 Degree=1 IsPeriodic=0
    g113: BSplineCurve PolesCount=2 KnotsCount=2 Degree=1 IsPeriodic=0
    g114: BSplineCurve PolesCount=2 KnotsCount=2 Degree=1 IsPeriodic=0
    g115: BSplineCurve PolesCount=2 KnotsCount=2 Degree=1 IsPeriodic=0
    g116: BSplineCurve PolesCount=2 KnotsCount=2 Degree=1 IsPeriodic=0
    g117: BSplineCurve PolesCount=2 KnotsCount=2 Degree=1 IsPeriodic=0
    g118: BSplineCurve PolesCount=2 KnotsCount=2 Degree=1 IsPeriodic=0
    g119: BSplineCurve PolesCount=2 KnotsCount=2 Degree=1 IsPeriodic=0
    g120: BSplineCurve PolesCount=2 KnotsCount=2 Degree=1 IsPeriodic=0
    g121: BSplineCurve PolesCount=2 KnotsCount=2 Degree=1 IsPeriodic=0
    g122: BSplineCurve PolesCount=2 KnotsCount=2 Degree=1 IsPeriodic=0
    g123: BSplineCurve PolesCount=2 KnotsCount=2 Degree=1 IsPeriodic=0
    g124: BSplineCurve PolesCount=2 KnotsCount=2 Degree=1 IsPeriodic=0
    g125: BSplineCurve PolesCount=2 KnotsCount=2 Degree=1 IsPeriodic=0
    g126: BSplineCurve PolesCount=2 KnotsCount=2 Degree=1 IsPeriodic=0
    g127: BSplineCurve PolesCount=2 KnotsCount=2 Degree=1 IsPeriodic=0
    g128: BSplineCurve PolesCount=2 KnotsCount=2 Degree=1 IsPeriodic=0
    g129: BSplineCurve PolesCount=2 KnotsCount=2 Degree=1 IsPeriodic=0
    g130: BSplineCurve PolesCount=2 KnotsCount=2 Degree=1 IsPeriodic=0
    g131: BSplineCurve PolesCount=2 KnotsCount=2 Degree=1 IsPeriodic=0
    g132: BSplineCurve PolesCount=2 KnotsCount=2 Degree=1 IsPeriodic=0
    g133: BSplineCurve PolesCount=2 KnotsCount=2 Degree=1 IsPeriodic=0
    g134: BSplineCurve PolesCount=2 KnotsCount=2 Degree=1 IsPeriodic=0
    g135: BSplineCurve PolesCount=2 KnotsCount=2 Degree=1 IsPeriodic=0
    g136: BSplineCurve PolesCount=2 KnotsCount=2 Degree=1 IsPeriodic=0
    g137: BSplineCurve PolesCount=2 KnotsCount=2 Degree=1 IsPeriodic=0
    g138: BSplineCurve PolesCount=2 KnotsCount=2 Degree=1 IsPeriodic=0
    g139: BSplineCurve PolesCount=2 KnotsCount=2 Degree=1 IsPeriodic=0
    g140: BSplineCurve PolesCount=2 KnotsCount=2 Degree=1 IsPeriodic=0
    g141: BSplineCurve PolesCount=2 KnotsCount=2 Degree=1 IsPeriodic=0
    g142: BSplineCurve PolesCount=2 KnotsCount=2 Degree=1 IsPeriodic=0
    g143: BSplineCurve PolesCount=2 KnotsCount=2 Degree=1 IsPeriodic=0
    g144: BSplineCurve PolesCount=2 KnotsCount=2 Degree=1 IsPeriodic=0
    g145: BSplineCurve PolesCount=2 KnotsCount=2 Degree=1 IsPeriodic=0
    g146: BSplineCurve PolesCount=2 KnotsCount=2 Degree=1 IsPeriodic=0
    g147: BSplineCurve PolesCount=2 KnotsCount=2 Degree=1 IsPeriodic=0
    g148: BSplineCurve PolesCount=2 KnotsCount=2 Degree=1 IsPeriodic=0
    g149: BSplineCurve PolesCount=2 KnotsCount=2 Degree=1 IsPeriodic=0
    g150: BSplineCurve PolesCount=2 KnotsCount=2 Degree=1 IsPeriodic=0
    g151: BSplineCurve PolesCount=2 KnotsCount=2 Degree=1 IsPeriodic=0
    g152: BSplineCurve PolesCount=2 KnotsCount=2 Degree=1 IsPeriodic=0
    g153: BSplineCurve PolesCount=2 KnotsCount=2 Degree=1 IsPeriodic=0
    g154: BSplineCurve PolesCount=2 KnotsCount=2 Degree=1 IsPeriodic=0
    g155: BSplineCurve PolesCount=2 KnotsCount=2 Degree=1 IsPeriodic=0
    g156: BSplineCurve PolesCount=2 KnotsCount=2 Degree=1 IsPeriodic=0
    g157: BSplineCurve PolesCount=2 KnotsCount=2 Degree=1 IsPeriodic=0
    g158: BSplineCurve PolesCount=2 KnotsCount=2 Degree=1 IsPeriodic=0
    g159: BSplineCurve PolesCount=2 KnotsCount=2 Degree=1 IsPeriodic=0
    g160: BSplineCurve PolesCount=2 KnotsCount=2 Degree=1 IsPeriodic=0
    g161: BSplineCurve PolesCount=2 KnotsCount=2 Degree=1 IsPeriodic=0
    g162: BSplineCurve PolesCount=2 KnotsCount=2 Degree=1 IsPeriodic=0
    g163: BSplineCurve PolesCount=2 KnotsCount=2 Degree=1 IsPeriodic=0
    g164: BSplineCurve PolesCount=2 KnotsCount=2 Degree=1 IsPeriodic=0
    g165: BSplineCurve PolesCount=2 KnotsCount=2 Degree=1 IsPeriodic=0
    g166: BSplineCurve PolesCount=2 KnotsCount=2 Degree=1 IsPeriodic=0
    g167: BSplineCurve PolesCount=2 KnotsCount=2 Degree=1 IsPeriodic=0
    g168: BSplineCurve PolesCount=2 KnotsCount=2 Degree=1 IsPeriodic=0
    g169: BSplineCurve PolesCount=2 KnotsCount=2 Degree=1 IsPeriodic=0
    g170: BSplineCurve PolesCount=2 KnotsCount=2 Degree=1 IsPeriodic=0
    g171: BSplineCurve PolesCount=2 KnotsCount=2 Degree=1 IsPeriodic=0
    g172: BSplineCurve PolesCount=2 KnotsCount=2 Degree=1 IsPeriodic=0
    g173: BSplineCurve PolesCount=2 KnotsCount=2 Degree=1 IsPeriodic=0
    g174: BSplineCurve PolesCount=2 KnotsCount=2 Degree=1 IsPeriodic=0
    g175: BSplineCurve PolesCount=2 KnotsCount=2 Degree=1 IsPeriodic=0
    g176: BSplineCurve PolesCount=2 KnotsCount=2 Degree=1 IsPeriodic=0
    g177: BSplineCurve PolesCount=2 KnotsCount=2 Degree=1 IsPeriodic=0
    g178: BSplineCurve PolesCount=2 KnotsCount=2 Degree=1 IsPeriodic=0
    g179: BSplineCurve PolesCount=2 KnotsCount=2 Degree=1 IsPeriodic=0
    g180: BSplineCurve PolesCount=2 KnotsCount=2 Degree=1 IsPeriodic=0
    g181: BSplineCurve PolesCount=2 KnotsCount=2 Degree=1 IsPeriodic=0
    g182: BSplineCurve PolesCount=2 KnotsCount=2 Degree=1 IsPeriodic=0
    g183: BSplineCurve PolesCount=2 KnotsCount=2 Degree=1 IsPeriodic=0
    g184: BSplineCurve PolesCount=2 KnotsCount=2 Degree=1 IsPeriodic=0
    g185: BSplineCurve PolesCount=2 KnotsCount=2 Degree=1 IsPeriodic=0
    g186: BSplineCurve PolesCount=2 KnotsCount=2 Degree=1 IsPeriodic=0
    g187: BSplineCurve PolesCount=2 KnotsCount=2 Degree=1 IsPeriodic=0
    g188: BSplineCurve PolesCount=2 KnotsCount=2 Degree=1 IsPeriodic=0
    g189: BSplineCurve PolesCount=2 KnotsCount=2 Degree=1 IsPeriodic=0
    g190: BSplineCurve PolesCount=2 KnotsCount=2 Degree=1 IsPeriodic=0
    g191: BSplineCurve PolesCount=2 KnotsCount=2 Degree=1 IsPeriodic=0
    g192: BSplineCurve PolesCount=2 KnotsCount=2 Degree=1 IsPeriodic=0
    g193: BSplineCurve PolesCount=2 KnotsCount=2 Degree=1 IsPeriodic=0
    g194: BSplineCurve PolesCount=2 KnotsCount=2 Degree=1 IsPeriodic=0
    g195: BSplineCurve PolesCount=2 KnotsCount=2 Degree=1 IsPeriodic=0
    g196: BSplineCurve PolesCount=2 KnotsCount=2 Degree=1 IsPeriodic=0
    g197: BSplineCurve PolesCount=2 KnotsCount=2 Degree=1 IsPeriodic=0
    g198: BSplineCurve PolesCount=2 KnotsCount=2 Degree=1 IsPeriodic=0
    g199: BSplineCurve PolesCount=2 KnotsCount=2 Degree=1 IsPeriodic=0
    g200: BSplineCurve PolesCount=2 KnotsCount=2 Degree=1 IsPeriodic=0
    g201: BSplineCurve PolesCount=2 KnotsCount=2 Degree=1 IsPeriodic=0
    g202: BSplineCurve PolesCount=2 KnotsCount=2 Degree=1 IsPeriodic=0
    g203: BSplineCurve PolesCount=2 KnotsCount=2 Degree=1 IsPeriodic=0
    g204: BSplineCurve PolesCount=2 KnotsCount=2 Degree=1 IsPeriodic=0
    g205: BSplineCurve PolesCount=2 KnotsCount=2 Degree=1 IsPeriodic=0
    g206: BSplineCurve PolesCount=2 KnotsCount=2 Degree=1 IsPeriodic=0
    g207: BSplineCurve PolesCount=2 KnotsCount=2 Degree=1 IsPeriodic=0
    g208: BSplineCurve PolesCount=2 KnotsCount=2 Degree=1 IsPeriodic=0
    g209: BSplineCurve PolesCount=2 KnotsCount=2 Degree=1 IsPeriodic=0
    g210: BSplineCurve PolesCount=2 KnotsCount=2 Degree=1 IsPeriodic=0
    g211: BSplineCurve PolesCount=2 KnotsCount=2 Degree=1 IsPeriodic=0
    g212: BSplineCurve PolesCount=2 KnotsCount=2 Degree=1 IsPeriodic=0
    g213: BSplineCurve PolesCount=2 KnotsCount=2 Degree=1 IsPeriodic=0
    g214: BSplineCurve PolesCount=2 KnotsCount=2 Degree=1 IsPeriodic=0
    g215: BSplineCurve PolesCount=2 KnotsCount=2 Degree=1 IsPeriodic=0
    g216: BSplineCurve PolesCount=2 KnotsCount=2 Degree=1 IsPeriodic=0
    g217: BSplineCurve PolesCount=2 KnotsCount=2 Degree=1 IsPeriodic=0
    g218: BSplineCurve PolesCount=2 KnotsCount=2 Degree=1 IsPeriodic=0
    g219: BSplineCurve PolesCount=2 KnotsCount=2 Degree=1 IsPeriodic=0
    g220: BSplineCurve PolesCount=2 KnotsCount=2 Degree=1 IsPeriodic=0
    g221: BSplineCurve PolesCount=2 KnotsCount=2 Degree=1 IsPeriodic=0
    g222: BSplineCurve PolesCount=2 KnotsCount=2 Degree=1 IsPeriodic=0
    g223: BSplineCurve PolesCount=2 KnotsCount=2 Degree=1 IsPeriodic=0
    g224: BSplineCurve PolesCount=2 KnotsCount=2 Degree=1 IsPeriodic=0
    g225: BSplineCurve PolesCount=2 KnotsCount=2 Degree=1 IsPeriodic=0
    g226: BSplineCurve PolesCount=2 KnotsCount=2 Degree=1 IsPeriodic=0
    g227: BSplineCurve PolesCount=2 KnotsCount=2 Degree=1 IsPeriodic=0
    g228: BSplineCurve PolesCount=2 KnotsCount=2 Degree=1 IsPeriodic=0
    g229: BSplineCurve PolesCount=2 KnotsCount=2 Degree=1 IsPeriodic=0
    g230: BSplineCurve PolesCount=2 KnotsCount=2 Degree=1 IsPeriodic=0
    g231: BSplineCurve PolesCount=2 KnotsCount=2 Degree=1 IsPeriodic=0
    g232: BSplineCurve PolesCount=2 KnotsCount=2 Degree=1 IsPeriodic=0
    g233: BSplineCurve PolesCount=2 KnotsCount=2 Degree=1 IsPeriodic=0
    g234: BSplineCurve PolesCount=2 KnotsCount=2 Degree=1 IsPeriodic=0
    g235: BSplineCurve PolesCount=2 KnotsCount=2 Degree=1 IsPeriodic=0
    g236: BSplineCurve PolesCount=2 KnotsCount=2 Degree=1 IsPeriodic=0
    g237: BSplineCurve PolesCount=2 KnotsCount=2 Degree=1 IsPeriodic=0
    g238: BSplineCurve PolesCount=2 KnotsCount=2 Degree=1 IsPeriodic=0
    g239: BSplineCurve PolesCount=2 KnotsCount=2 Degree=1 IsPeriodic=0
    g240: BSplineCurve PolesCount=2 KnotsCount=2 Degree=1 IsPeriodic=0
    g241: BSplineCurve PolesCount=2 KnotsCount=2 Degree=1 IsPeriodic=0
    g242: BSplineCurve PolesCount=2 KnotsCount=2 Degree=1 IsPeriodic=0
    g243: BSplineCurve PolesCount=2 KnotsCount=2 Degree=1 IsPeriodic=0
    g244: BSplineCurve PolesCount=2 KnotsCount=2 Degree=1 IsPeriodic=0
    g245: BSplineCurve PolesCount=2 KnotsCount=2 Degree=1 IsPeriodic=0
    g246: BSplineCurve PolesCount=2 KnotsCount=2 Degree=1 IsPeriodic=0
    g247: BSplineCurve PolesCount=2 KnotsCount=2 Degree=1 IsPeriodic=0
    g248: BSplineCurve PolesCount=2 KnotsCount=2 Degree=1 IsPeriodic=0
    g249: BSplineCurve PolesCount=2 KnotsCount=2 Degree=1 IsPeriodic=0
    g250: BSplineCurve PolesCount=2 KnotsCount=2 Degree=1 IsPeriodic=0
    g251: BSplineCurve PolesCount=2 KnotsCount=2 Degree=1 IsPeriodic=0
    g252: BSplineCurve PolesCount=2 KnotsCount=2 Degree=1 IsPeriodic=0
    g253: BSplineCurve PolesCount=2 KnotsCount=2 Degree=1 IsPeriodic=0
    g254: BSplineCurve PolesCount=2 KnotsCount=2 Degree=1 IsPeriodic=0
    g255: BSplineCurve PolesCount=2 KnotsCount=2 Degree=1 IsPeriodic=0
    g256: BSplineCurve PolesCount=2 KnotsCount=2 Degree=1 IsPeriodic=0
    g257: BSplineCurve PolesCount=2 KnotsCount=2 Degree=1 IsPeriodic=0
    g258: BSplineCurve PolesCount=2 KnotsCount=2 Degree=1 IsPeriodic=0
    g259: BSplineCurve PolesCount=2 KnotsCount=2 Degree=1 IsPeriodic=0
    g260: BSplineCurve PolesCount=2 KnotsCount=2 Degree=1 IsPeriodic=0
    g261: BSplineCurve PolesCount=2 KnotsCount=2 Degree=1 IsPeriodic=0
    g262: BSplineCurve PolesCount=2 KnotsCount=2 Degree=1 IsPeriodic=0
    g263: BSplineCurve PolesCount=2 KnotsCount=2 Degree=1 IsPeriodic=0
    g264: BSplineCurve PolesCount=2 KnotsCount=2 Degree=1 IsPeriodic=0
    g265: BSplineCurve PolesCount=2 KnotsCount=2 Degree=1 IsPeriodic=0
    g266: BSplineCurve PolesCount=2 KnotsCount=2 Degree=1 IsPeriodic=0
    g267: BSplineCurve PolesCount=2 KnotsCount=2 Degree=1 IsPeriodic=0
    g268: BSplineCurve PolesCount=2 KnotsCount=2 Degree=1 IsPeriodic=0
    g269: BSplineCurve PolesCount=2 KnotsCount=2 Degree=1 IsPeriodic=0
    g270: BSplineCurve PolesCount=2 KnotsCount=2 Degree=1 IsPeriodic=0
    g271: BSplineCurve PolesCount=2 KnotsCount=2 Degree=1 IsPeriodic=0
    g272: BSplineCurve PolesCount=2 KnotsCount=2 Degree=1 IsPeriodic=0
    g273: BSplineCurve PolesCount=2 KnotsCount=2 Degree=1 IsPeriodic=0
    g274: BSplineCurve PolesCount=2 KnotsCount=2 Degree=1 IsPeriodic=0
    g275: BSplineCurve PolesCount=2 KnotsCount=2 Degree=1 IsPeriodic=0
    g276: BSplineCurve PolesCount=2 KnotsCount=2 Degree=1 IsPeriodic=0
    g277: BSplineCurve PolesCount=2 KnotsCount=2 Degree=1 IsPeriodic=0
    g278: BSplineCurve PolesCount=2 KnotsCount=2 Degree=1 IsPeriodic=0
    g279: BSplineCurve PolesCount=2 KnotsCount=2 Degree=1 IsPeriodic=0
    g280: BSplineCurve PolesCount=2 KnotsCount=2 Degree=1 IsPeriodic=0
    g281: BSplineCurve PolesCount=2 KnotsCount=2 Degree=1 IsPeriodic=0
    g282: BSplineCurve PolesCount=2 KnotsCount=2 Degree=1 IsPeriodic=0
    g283: BSplineCurve PolesCount=2 KnotsCount=2 Degree=1 IsPeriodic=0
    g284: BSplineCurve PolesCount=2 KnotsCount=2 Degree=1 IsPeriodic=0
    g285: BSplineCurve PolesCount=2 KnotsCount=2 Degree=1 IsPeriodic=0
    g286: BSplineCurve PolesCount=2 KnotsCount=2 Degree=1 IsPeriodic=0
    g287: BSplineCurve PolesCount=2 KnotsCount=2 Degree=1 IsPeriodic=0
    g288: BSplineCurve PolesCount=2 KnotsCount=2 Degree=1 IsPeriodic=0
    g289: BSplineCurve PolesCount=2 KnotsCount=2 Degree=1 IsPeriodic=0
    g290: BSplineCurve PolesCount=2 KnotsCount=2 Degree=1 IsPeriodic=0
    g291: BSplineCurve PolesCount=2 KnotsCount=2 Degree=1 IsPeriodic=0
    g292: BSplineCurve PolesCount=2 KnotsCount=2 Degree=1 IsPeriodic=0
    g293: BSplineCurve PolesCount=2 KnotsCount=2 Degree=1 IsPeriodic=0
    g294: BSplineCurve PolesCount=2 KnotsCount=2 Degree=1 IsPeriodic=0
    g295: BSplineCurve PolesCount=2 KnotsCount=2 Degree=1 IsPeriodic=0
    g296: BSplineCurve PolesCount=2 KnotsCount=2 Degree=1 IsPeriodic=0
    g297: BSplineCurve PolesCount=2 KnotsCount=2 Degree=1 IsPeriodic=0
    g298: BSplineCurve PolesCount=2 KnotsCount=2 Degree=1 IsPeriodic=0
    g299: BSplineCurve PolesCount=2 KnotsCount=2 Degree=1 IsPeriodic=0
    g300: BSplineCurve PolesCount=2 KnotsCount=2 Degree=1 IsPeriodic=0
    g301: BSplineCurve PolesCount=2 KnotsCount=2 Degree=1 IsPeriodic=0
    g302: BSplineCurve PolesCount=2 KnotsCount=2 Degree=1 IsPeriodic=0
    g303: BSplineCurve PolesCount=2 KnotsCount=2 Degree=1 IsPeriodic=0
    g304: BSplineCurve PolesCount=2 KnotsCount=2 Degree=1 IsPeriodic=0
    g305: BSplineCurve PolesCount=2 KnotsCount=2 Degree=1 IsPeriodic=0
    g306: BSplineCurve PolesCount=2 KnotsCount=2 Degree=1 IsPeriodic=0
    g307: BSplineCurve PolesCount=2 KnotsCount=2 Degree=1 IsPeriodic=0
    g308: BSplineCurve PolesCount=2 KnotsCount=2 Degree=1 IsPeriodic=0
    g309: BSplineCurve PolesCount=2 KnotsCount=2 Degree=1 IsPeriodic=0
    g310: BSplineCurve PolesCount=2 KnotsCount=2 Degree=1 IsPeriodic=0
    g311: BSplineCurve PolesCount=2 KnotsCount=2 Degree=1 IsPeriodic=0
    g312: BSplineCurve PolesCount=2 KnotsCount=2 Degree=1 IsPeriodic=0
    g313: BSplineCurve PolesCount=2 KnotsCount=2 Degree=1 IsPeriodic=0
    g314: BSplineCurve PolesCount=2 KnotsCount=2 Degree=1 IsPeriodic=0
    g315: BSplineCurve PolesCount=2 KnotsCount=2 Degree=1 IsPeriodic=0
    g316: BSplineCurve PolesCount=2 KnotsCount=2 Degree=1 IsPeriodic=0
    g317: BSplineCurve PolesCount=2 KnotsCount=2 Degree=1 IsPeriodic=0
    g318: BSplineCurve PolesCount=2 KnotsCount=2 Degree=1 IsPeriodic=0
    g319: BSplineCurve PolesCount=2 KnotsCount=2 Degree=1 IsPeriodic=0
    g320: BSplineCurve PolesCount=2 KnotsCount=2 Degree=1 IsPeriodic=0
    g321: BSplineCurve PolesCount=2 KnotsCount=2 Degree=1 IsPeriodic=0
    g322: BSplineCurve PolesCount=2 KnotsCount=2 Degree=1 IsPeriodic=0
    g323: BSplineCurve PolesCount=2 KnotsCount=2 Degree=1 IsPeriodic=0
    g324: BSplineCurve PolesCount=2 KnotsCount=2 Degree=1 IsPeriodic=0
    g325: BSplineCurve PolesCount=2 KnotsCount=2 Degree=1 IsPeriodic=0
    g326: BSplineCurve PolesCount=2 KnotsCount=2 Degree=1 IsPeriodic=0
    g327: BSplineCurve PolesCount=2 KnotsCount=2 Degree=1 IsPeriodic=0
    g328: BSplineCurve PolesCount=2 KnotsCount=2 Degree=1 IsPeriodic=0
    g329: BSplineCurve PolesCount=2 KnotsCount=2 Degree=1 IsPeriodic=0
    g330: BSplineCurve PolesCount=2 KnotsCount=2 Degree=1 IsPeriodic=0
    g331: BSplineCurve PolesCount=2 KnotsCount=2 Degree=1 IsPeriodic=0
    g332: BSplineCurve PolesCount=2 KnotsCount=2 Degree=1 IsPeriodic=0
    g333: BSplineCurve PolesCount=2 KnotsCount=2 Degree=1 IsPeriodic=0
    g334: BSplineCurve PolesCount=2 KnotsCount=2 Degree=1 IsPeriodic=0
    g335: BSplineCurve PolesCount=2 KnotsCount=2 Degree=1 IsPeriodic=0
    g336: BSplineCurve PolesCount=2 KnotsCount=2 Degree=1 IsPeriodic=0
    g337: BSplineCurve PolesCount=2 KnotsCount=2 Degree=1 IsPeriodic=0
    g338: BSplineCurve PolesCount=2 KnotsCount=2 Degree=1 IsPeriodic=0
    g339: BSplineCurve PolesCount=2 KnotsCount=2 Degree=1 IsPeriodic=0
    g340: BSplineCurve PolesCount=2 KnotsCount=2 Degree=1 IsPeriodic=0
    g341: BSplineCurve PolesCount=2 KnotsCount=2 Degree=1 IsPeriodic=0
    g342: BSplineCurve PolesCount=2 KnotsCount=2 Degree=1 IsPeriodic=0
    g343: BSplineCurve PolesCount=2 KnotsCount=2 Degree=1 IsPeriodic=0
    g344: BSplineCurve PolesCount=2 KnotsCount=2 Degree=1 IsPeriodic=0
    g345: BSplineCurve PolesCount=2 KnotsCount=2 Degree=1 IsPeriodic=0
    g346: BSplineCurve PolesCount=2 KnotsCount=2 Degree=1 IsPeriodic=0
    g347: BSplineCurve PolesCount=2 KnotsCount=2 Degree=1 IsPeriodic=0
    g348: BSplineCurve PolesCount=2 KnotsCount=2 Degree=1 IsPeriodic=0
    g349: BSplineCurve PolesCount=2 KnotsCount=2 Degree=1 IsPeriodic=0
    g350: BSplineCurve PolesCount=2 KnotsCount=2 Degree=1 IsPeriodic=0
    g351: BSplineCurve PolesCount=2 KnotsCount=2 Degree=1 IsPeriodic=0
    g352: BSplineCurve PolesCount=2 KnotsCount=2 Degree=1 IsPeriodic=0
    g353: BSplineCurve PolesCount=2 KnotsCount=2 Degree=1 IsPeriodic=0
    g354: BSplineCurve PolesCount=2 KnotsCount=2 Degree=1 IsPeriodic=0
    g355: BSplineCurve PolesCount=2 KnotsCount=2 Degree=1 IsPeriodic=0
    g356: BSplineCurve PolesCount=2 KnotsCount=2 Degree=1 IsPeriodic=0
    g357: BSplineCurve PolesCount=2 KnotsCount=2 Degree=1 IsPeriodic=0
    g358: BSplineCurve PolesCount=2 KnotsCount=2 Degree=1 IsPeriodic=0
    g359: BSplineCurve PolesCount=2 KnotsCount=2 Degree=1 IsPeriodic=0
    g360: BSplineCurve PolesCount=2 KnotsCount=2 Degree=1 IsPeriodic=0
    g361: BSplineCurve PolesCount=2 KnotsCount=2 Degree=1 IsPeriodic=0
    g362: BSplineCurve PolesCount=2 KnotsCount=2 Degree=1 IsPeriodic=0
    g363: BSplineCurve PolesCount=2 KnotsCount=2 Degree=1 IsPeriodic=0
    g364: BSplineCurve PolesCount=2 KnotsCount=2 Degree=1 IsPeriodic=0
    g365: BSplineCurve PolesCount=2 KnotsCount=2 Degree=1 IsPeriodic=0
    g366: BSplineCurve PolesCount=2 KnotsCount=2 Degree=1 IsPeriodic=0
    g367: BSplineCurve PolesCount=2 KnotsCount=2 Degree=1 IsPeriodic=0
    g368: BSplineCurve PolesCount=2 KnotsCount=2 Degree=1 IsPeriodic=0
    g369: BSplineCurve PolesCount=2 KnotsCount=2 Degree=1 IsPeriodic=0
    g370: BSplineCurve PolesCount=2 KnotsCount=2 Degree=1 IsPeriodic=0
    g371: BSplineCurve PolesCount=2 KnotsCount=2 Degree=1 IsPeriodic=0
    g372: BSplineCurve PolesCount=2 KnotsCount=2 Degree=1 IsPeriodic=0
    g373: BSplineCurve PolesCount=2 KnotsCount=2 Degree=1 IsPeriodic=0
    g374: BSplineCurve PolesCount=2 KnotsCount=2 Degree=1 IsPeriodic=0
    g375: BSplineCurve PolesCount=2 KnotsCount=2 Degree=1 IsPeriodic=0
    g376: BSplineCurve PolesCount=2 KnotsCount=2 Degree=1 IsPeriodic=0
    g377: BSplineCurve PolesCount=2 KnotsCount=2 Degree=1 IsPeriodic=0
    g378: BSplineCurve PolesCount=2 KnotsCount=2 Degree=1 IsPeriodic=0
    g379: BSplineCurve PolesCount=2 KnotsCount=2 Degree=1 IsPeriodic=0
    g380: BSplineCurve PolesCount=2 KnotsCount=2 Degree=1 IsPeriodic=0
    g381: BSplineCurve PolesCount=2 KnotsCount=2 Degree=1 IsPeriodic=0
    g382: BSplineCurve PolesCount=2 KnotsCount=2 Degree=1 IsPeriodic=0
    g383: BSplineCurve PolesCount=2 KnotsCount=2 Degree=1 IsPeriodic=0
    g384: BSplineCurve PolesCount=2 KnotsCount=2 Degree=1 IsPeriodic=0
    g385: BSplineCurve PolesCount=2 KnotsCount=2 Degree=1 IsPeriodic=0
    g386: BSplineCurve PolesCount=2 KnotsCount=2 Degree=1 IsPeriodic=0
    g387: BSplineCurve PolesCount=2 KnotsCount=2 Degree=1 IsPeriodic=0
    g388: BSplineCurve PolesCount=2 KnotsCount=2 Degree=1 IsPeriodic=0
    g389: BSplineCurve PolesCount=2 KnotsCount=2 Degree=1 IsPeriodic=0
    g390: BSplineCurve PolesCount=2 KnotsCount=2 Degree=1 IsPeriodic=0
    g391: BSplineCurve PolesCount=2 KnotsCount=2 Degree=1 IsPeriodic=0
    g392: BSplineCurve PolesCount=2 KnotsCount=2 Degree=1 IsPeriodic=0
    g393: BSplineCurve PolesCount=2 KnotsCount=2 Degree=1 IsPeriodic=0
    g394: BSplineCurve PolesCount=2 KnotsCount=2 Degree=1 IsPeriodic=0
    g395: BSplineCurve PolesCount=2 KnotsCount=2 Degree=1 IsPeriodic=0
    g396: BSplineCurve PolesCount=2 KnotsCount=2 Degree=1 IsPeriodic=0
    g397: BSplineCurve PolesCount=2 KnotsCount=2 Degree=1 IsPeriodic=0
    g398: BSplineCurve PolesCount=2 KnotsCount=2 Degree=1 IsPeriodic=0
    g399: BSplineCurve PolesCount=2 KnotsCount=2 Degree=1 IsPeriodic=0
    ... +460 more geometry lines
  constraints (860):
    c: Coincident(g0,g1)
    c: Coincident(g1,g2)
    c: Coincident(g2,g3)
    c: Coincident(g3,g4)
    c: Coincident(g4,g5)
    c: Coincident(g5,g6)
    c: Coincident(g6,g7)
    c: Coincident(g7,g8)
    c: Coincident(g8,g9)
    c: Coincident(g9,g10)
    c: Coincident(g10,g11)
    c: Coincident(g11,g12)
    c: Coincident(g12,g13)
    c: Coincident(g13,g14)
    c: Coincident(g14,g15)
    c: Coincident(g15,g16)
    c: Coincident(g16,g17)
    c: Coincident(g17,g18)
    c: Coincident(g18,g19)
    c: Coincident(g19,g20)
    c: Coincident(g20,g21)
    c: Coincident(g21,g22)
    c: Coincident(g22,g23)
    c: Coincident(g23,g24)
    c: Coincident(g24,g25)
    c: Coincident(g25,g26)
    c: Coincident(g26,g27)
    c: Coincident(g27,g28)
    c: Coincident(g28,g29)
    c: Coincident(g29,g30)
    c: Coincident(g30,g31)
    c: Coincident(g31,g32)
    c: Coincident(g32,g33)
    c: Coincident(g33,g34)
    c: Coincident(g34,g35)
    c: Coincident(g35,g36)
    c: Coincident(g36,g37)
    c: Coincident(g37,g38)
    c: Coincident(g38,g39)
    c: Coincident(g39,g40)
    c: Coincident(g40,g41)
    c: Coincident(g41,g42)
    c: Coincident(g42,g43)
    c: Coincident(g43,g44)
    c: Coincident(g44,g45)
    c: Coincident(g45,g46)
    c: Coincident(g46,g47)
    c: Coincident(g47,g48)
    c: Coincident(g48,g49)
    c: Coincident(g49,g50)
    c: Coincident(g50,g51)
    c: Coincident(g51,g52)
    c: Coincident(g52,g53)
    c: Coincident(g53,g54)
    c: Coincident(g54,g55)
    c: Coincident(g55,g56)
    c: Coincident(g56,g57)
    c: Coincident(g57,g58)
    c: Coincident(g58,g59)
    c: Coincident(g59,g60)
    c: Coincident(g60,g61)
    c: Coincident(g61,g62)
    c: Coincident(g62,g63)
    c: Coincident(g63,g64)
    c: Coincident(g64,g65)
    c: Coincident(g65,g66)
    c: Coincident(g66,g67)
    c: Coincident(g67,g68)
    c: Coincident(g68,g69)
    c: Coincident(g69,g70)
    c: Coincident(g70,g71)
    c: Coincident(g71,g72)
    c: Coincident(g72,g73)
    c: Coincident(g73,g74)
    c: Coincident(g74,g75)
    c: Coincident(g75,g76)
    c: Coincident(g76,g77)
    c: Coincident(g77,g78)
    c: Coincident(g78,g79)
    c: Coincident(g79,g80)
    c: Coincident(g80,g81)
    c: Coincident(g81,g82)
    c: Coincident(g82,g83)
    c: Coincident(g83,g84)
    c: Coincident(g84,g85)
    c: Coincident(g85,g86)
    c: Coincident(g86,g87)
    c: Coincident(g87,g0)
    c: Coincident(g88,g89)
    c: Coincident(g89,g90)
    c: Coincident(g90,g91)
    c: Coincident(g91,g92)
    c: Coincident(g92,g93)
    c: Coincident(g93,g94)
    c: Coincident(g94,g95)
    c: Coincident(g95,g96)
    c: Coincident(g96,g97)
    c: Coincident(g97,g98)
    c: Coincident(g98,g99)
    c: Coincident(g99,g100)
    c: Coincident(g100,g101)
    c: Coincident(g101,g102)
    c: Coincident(g102,g103)
    c: Coincident(g103,g104)
    c: Coincident(g104,g105)
    c: Coincident(g105,g106)
    c: Coincident(g106,g107)
    c: Coincident(g107,g108)
    c: Coincident(g108,g109)
    c: Coincident(g109,g110)
    c: Coincident(g110,g111)
    c: Coincident(g111,g112)
    c: Coincident(g112,g113)
    c: Coincident(g113,g114)
    c: Coincident(g114,g115)
    c: Coincident(g115,g116)
    c: Coincident(g116,g117)
    c: Coincident(g117,g118)
    c: Coincident(g118,g119)
    c: Coincident(g119,g120)
    c: Coincident(g120,g121)
    c: Coincident(g121,g122)
    c: Coincident(g122,g123)
    c: Coincident(g123,g124)
    c: Coincident(g124,g125)
    c: Coincident(g125,g126)
    c: Coincident(g126,g127)
    c: Coincident(g127,g88)
    c: Coincident(g128,g129)
    c: Coincident(g129,g130)
    c: Coincident(g130,g131)
    c: Coincident(g131,g132)
    c: Coincident(g132,g133)
    c: Coincident(g133,g134)
    c: Coincident(g134,g135)
    c: Coincident(g135,g136)
    c: Coincident(g136,g137)
    c: Coincident(g137,g138)
    c: Coincident(g138,g139)
    c: Coincident(g139,g140)
    c: Coincident(g140,g141)
    c: Coincident(g141,g142)
    c: Coincident(g142,g143)
    c: Coincident(g143,g144)
    c: Coincident(g144,g145)
    c: Coincident(g145,g146)
    c: Coincident(g146,g147)
    c: Coincident(g147,g148)
    c: Coincident(g148,g149)
    c: Coincident(g149,g150)
    c: Coincident(g150,g151)
    c: Coincident(g151,g152)
    c: Coincident(g152,g153)
    c: Coincident(g153,g154)
    c: Coincident(g154,g155)
    c: Coincident(g155,g156)
    c: Coincident(g156,g157)
    c: Coincident(g157,g158)
    c: Coincident(g158,g159)
    c: Coincident(g159,g160)
    c: Coincident(g160,g161)
    c: Coincident(g161,g162)
    c: Coincident(g162,g163)
    c: Coincident(g163,g164)
    c: Coincident(g164,g165)
    c: Coincident(g165,g166)
    c: Coincident(g166,g167)
    c: Coincident(g167,g168)
    c: Coincident(g168,g169)
    c: Coincident(g169,g170)
    c: Coincident(g170,g171)
    c: Coincident(g171,g172)
    c: Coincident(g172,g173)
    c: Coincident(g173,g174)
    c: Coincident(g174,g175)
    c: Coincident(g175,g176)
    c: Coincident(g176,g177)
    c: Coincident(g177,g178)
    c: Coincident(g178,g179)
    c: Coincident(g179,g180)
    c: Coincident(g180,g181)
    c: Coincident(g181,g182)
    c: Coincident(g182,g183)
    c: Coincident(g183,g184)
    c: Coincident(g184,g185)
    c: Coincident(g185,g186)
    c: Coincident(g186,g187)
    c: Coincident(g187,g188)
    c: Coincident(g188,g189)
    c: Coincident(g189,g190)
    c: Coincident(g190,g191)
    c: Coincident(g191,g192)
    c: Coincident(g192,g193)
    c: Coincident(g193,g194)
    c: Coincident(g194,g195)
    c: Coincident(g195,g196)
    c: Coincident(g196,g197)
    c: Coincident(g197,g198)
    c: Coincident(g198,g199)
    c: Coincident(g199,g200)
    c: Coincident(g200,g201)
    c: Coincident(g201,g202)
    c: Coincident(g202,g203)
    c: Coincident(g203,g204)
    c: Coincident(g204,g205)
    c: Coincident(g205,g206)
    c: Coincident(g206,g207)
    c: Coincident(g207,g208)
    c: Coincident(g208,g209)
    c: Coincident(g209,g210)
    c: Coincident(g210,g211)
    c: Coincident(g211,g212)
    c: Coincident(g212,g213)
    c: Coincident(g213,g214)
    c: Coincident(g214,g215)
    c: Coincident(g215,g216)
    c: Coincident(g216,g217)
    c: Coincident(g217,g218)
    c: Coincident(g218,g219)
    c: Coincident(g219,g220)
    c: Coincident(g220,g221)
    c: Coincident(g221,g222)
    c: Coincident(g222,g223)
    c: Coincident(g223,g224)
    c: Coincident(g224,g225)
    c: Coincident(g225,g226)
    c: Coincident(g226,g227)
    c: Coincident(g227,g228)
    c: Coincident(g228,g229)
    c: Coincident(g229,g230)
    c: Coincident(g230,g231)
    c: Coincident(g231,g232)
    c: Coincident(g232,g233)
    c: Coincident(g233,g234)
    c: Coincident(g234,g235)
    c: Coincident(g235,g236)
    c: Coincident(g236,g237)
    c: Coincident(g237,g238)
    c: Coincident(g238,g239)
    c: Coincident(g239,g128)
    c: Coincident(g240,g241)
    c: Coincident(g241,g242)
    c: Coincident(g242,g243)
    c: Coincident(g243,g244)
    c: Coincident(g244,g245)
    c: Coincident(g245,g246)
    c: Coincident(g246,g247)
    c: Coincident(g247,g248)
    c: Coincident(g248,g249)
    c: Coincident(g249,g250)
    c: Coincident(g250,g251)
    c: Coincident(g251,g252)
    c: Coincident(g252,g253)
    c: Coincident(g253,g254)
    c: Coincident(g254,g255)
    c: Coincident(g255,g256)
    c: Coincident(g256,g257)
    c: Coincident(g257,g258)
    c: Coincident(g258,g259)
    c: Coincident(g259,g260)
    c: Coincident(g260,g261)
    c: Coincident(g261,g262)
    c: Coincident(g262,g263)
    c: Coincident(g263,g264)
    c: Coincident(g264,g265)
    c: Coincident(g265,g266)
    c: Coincident(g266,g267)
    c: Coincident(g267,g268)
    c: Coincident(g268,g269)
    c: Coincident(g269,g270)
    c: Coincident(g270,g271)
    c: Coincident(g271,g272)
    c: Coincident(g272,g273)
    c: Coincident(g273,g274)
    c: Coincident(g274,g275)
    c: Coincident(g275,g276)
    c: Coincident(g276,g277)
    c: Coincident(g277,g278)
    c: Coincident(g278,g279)
    c: Coincident(g279,g280)
    c: Coincident(g280,g281)
    c: Coincident(g281,g282)
    c: Coincident(g282,g283)
    c: Coincident(g283,g284)
    c: Coincident(g284,g285)
    c: Coincident(g285,g286)
    c: Coincident(g286,g287)
    c: Coincident(g287,g240)
    c: Coincident(g288,g289)
    c: Coincident(g289,g290)
    c: Coincident(g290,g291)
    c: Coincident(g291,g292)
    c: Coincident(g292,g293)
    c: Coincident(g293,g294)
    c: Coincident(g294,g295)
    c: Coincident(g295,g296)
    c: Coincident(g296,g297)
    c: Coincident(g297,g298)
    c: Coincident(g298,g299)
    c: Coincident(g299,g300)
    c: Coincident(g300,g301)
    c: Coincident(g301,g302)
    c: Coincident(g302,g303)
    c: Coincident(g303,g304)
    c: Coincident(g304,g305)
    c: Coincident(g305,g306)
    c: Coincident(g306,g307)
    c: Coincident(g307,g308)
    c: Coincident(g308,g309)
    c: Coincident(g309,g310)
    c: Coincident(g310,g311)
    c: Coincident(g311,g288)
    c: Coincident(g312,g313)
    c: Coincident(g313,g314)
    c: Coincident(g314,g315)
    c: Coincident(g315,g316)
    c: Coincident(g316,g317)
    c: Coincident(g317,g318)
    c: Coincident(g318,g319)
    c: Coincident(g319,g320)
    c: Coincident(g320,g321)
    c: Coincident(g321,g322)
    c: Coincident(g322,g323)
    c: Coincident(g323,g324)
    c: Coincident(g324,g325)
    c: Coincident(g325,g326)
    c: Coincident(g326,g327)
    c: Coincident(g327,g312)
    c: Coincident(g328,g329)
    c: Coincident(g329,g330)
    c: Coincident(g330,g331)
    c: Coincident(g331,g332)
    c: Coincident(g332,g333)
    c: Coincident(g333,g334)
    c: Coincident(g334,g335)
    c: Coincident(g335,g336)
    c: Coincident(g336,g337)
    c: Coincident(g337,g338)
    c: Coincident(g338,g339)
    c: Coincident(g339,g340)
    c: Coincident(g340,g341)
    c: Coincident(g341,g342)
    c: Coincident(g342,g343)
    c: Coincident(g343,g344)
    c: Coincident(g344,g345)
    c: Coincident(g345,g346)
    c: Coincident(g346,g347)
    c: Coincident(g347,g348)
    c: Coincident(g348,g349)
    c: Coincident(g349,g350)
    c: Coincident(g350,g351)
    c: Coincident(g351,g352)
    c: Coincident(g352,g353)
    c: Coincident(g353,g354)
    c: Coincident(g354,g355)
    c: Coincident(g355,g356)
    c: Coincident(g356,g357)
    c: Coincident(g357,g358)
    c: Coincident(g358,g359)
    c: Coincident(g359,g360)
    c: Coincident(g360,g361)
    c: Coincident(g361,g362)
    c: Coincident(g362,g363)
    c: Coincident(g363,g364)
    c: Coincident(g364,g365)
    c: Coincident(g365,g366)
    c: Coincident(g366,g367)
    c: Coincident(g367,g368)
    c: Coincident(g368,g369)
    c: Coincident(g369,g370)
    c: Coincident(g370,g371)
    c: Coincident(g371,g372)
    c: Coincident(g372,g373)
    c: Coincident(g373,g374)
    c: Coincident(g374,g375)
    c: Coincident(g375,g376)
    c: Coincident(g376,g377)
    c: Coincident(g377,g378)
    c: Coincident(g378,g379)
    c: Coincident(g379,g380)
    c: Coincident(g380,g381)
    c: Coincident(g381,g382)
    c: Coincident(g382,g383)
    c: Coincident(g383,g384)
    c: Coincident(g384,g385)
    c: Coincident(g385,g386)
    c: Coincident(g386,g387)
    c: Coincident(g387,g388)
    c: Coincident(g388,g389)
    c: Coincident(g389,g390)
    c: Coincident(g390,g391)
    c: Coincident(g391,g392)
    c: Coincident(g392,g393)
    c: Coincident(g393,g394)
    c: Coincident(g394,g395)
    c: Coincident(g395,g396)
    c: Coincident(g396,g397)
    c: Coincident(g397,g398)
    c: Coincident(g398,g399)
    c: Coincident(g399,g328)
    c: Coincident(g400,g401)
    c: Coincident(g401,g402)
    c: Coincident(g402,g403)
    c: Coincident(g403,g404)
    c: Coincident(g404,g405)
    c: Coincident(g405,g406)
    c: Coincident(g406,g407)
    c: Coincident(g407,g408)
    c: Coincident(g408,g409)
    c: Coincident(g409,g410)
    c: Coincident(g410,g411)
    c: Coincident(g411,g412)
    c: Coincident(g412,g413)
    c: Coincident(g413,g414)
    c: Coincident(g414,g415)
    c: Coincident(g415,g416)
    c: Coincident(g416,g417)
    c: Coincident(g417,g418)
    c: Coincident(g418,g419)
    c: Coincident(g419,g420)
    c: Coincident(g420,g421)
    c: Coincident(g421,g422)
    c: Coincident(g422,g423)
    c: Coincident(g423,g400)
    c: Coincident(g424,g425)
    c: Coincident(g425,g426)
    c: Coincident(g426,g427)
    c: Coincident(g427,g428)
    c: Coincident(g428,g429)
    c: Coincident(g429,g430)
    c: Coincident(g430,g431)
    c: Coincident(g431,g432)
    c: Coincident(g432,g433)
    c: Coincident(g433,g434)
    c: Coincident(g434,g435)
    c: Coincident(g435,g436)
    c: Coincident(g436,g437)
    c: Coincident(g437,g438)
    c: Coincident(g438,g439)
    c: Coincident(g439,g440)
    c: Coincident(g440,g441)
    c: Coincident(g441,g442)
    c: Coincident(g442,g443)
    c: Coincident(g443,g444)
    c: Coincident(g444,g445)
    c: Coincident(g445,g446)
    c: Coincident(g446,g447)
    c: Coincident(g447,g448)
    c: Coincident(g448,g449)
    c: Coincident(g449,g450)
    c: Coincident(g450,g451)
    c: Coincident(g451,g452)
    c: Coincident(g452,g453)
    c: Coincident(g453,g454)
    c: Coincident(g454,g455)
    c: Coincident(g455,g456)
    c: Coincident(g456,g457)
    c: Coincident(g457,g458)
    c: Coincident(g458,g459)
    c: Coincident(g459,g460)
    c: Coincident(g460,g461)
    c: Coincident(g461,g462)
    c: Coincident(g462,g463)
    c: Coincident(g463,g464)
    c: Coincident(g464,g465)
    c: Coincident(g465,g466)
    c: Coincident(g466,g467)
    c: Coincident(g467,g468)
    c: Coincident(g468,g469)
    c: Coincident(g469,g470)
    c: Coincident(g470,g471)
    c: Coincident(g471,g472)
    c: Coincident(g472,g473)
    c: Coincident(g473,g474)
    c: Coincident(g474,g475)
    c: Coincident(g475,g476)
    c: Coincident(g476,g477)
    c: Coincident(g477,g478)
    c: Coincident(g478,g479)
    c: Coincident(g479,g424)
    c: Coincident(g480,g481)
    c: Coincident(g481,g482)
    c: Coincident(g482,g483)
    c: Coincident(g483,g484)
    c: Coincident(g484,g485)
    c: Coincident(g485,g486)
    c: Coincident(g486,g487)
    c: Coincident(g487,g488)
    c: Coincident(g488,g489)
    c: Coincident(g489,g490)
    c: Coincident(g490,g491)
    c: Coincident(g491,g492)
    c: Coincident(g492,g493)
    c: Coincident(g493,g494)
    c: Coincident(g494,g495)
    c: Coincident(g495,g480)
    c: Coincident(g496,g497)
    c: Coincident(g497,g498)
    c: Coincident(g498,g499)
    c: Coincident(g499,g500)
    c: Coincident(g500,g501)
    c: Coincident(g501,g502)
    c: Coincident(g502,g503)
    c: Coincident(g503,g504)
    c: Coincident(g504,g505)
    c: Coincident(g505,g506)
    c: Coincident(g506,g507)
    c: Coincident(g507,g508)
    c: Coincident(g508,g509)
    c: Coincident(g509,g510)
    c: Coincident(g510,g511)
    c: Coincident(g511,g512)
    c: Coincident(g512,g513)
    c: Coincident(g513,g514)
    c: Coincident(g514,g515)
    c: Coincident(g515,g516)
    c: Coincident(g516,g517)
    c: Coincident(g517,g518)
    c: Coincident(g518,g519)
    c: Coincident(g519,g520)
    c: Coincident(g520,g521)
    c: Coincident(g521,g522)
    c: Coincident(g522,g523)
    c: Coincident(g523,g524)
    c: Coincident(g524,g525)
    c: Coincident(g525,g526)
    c: Coincident(g526,g527)
    c: Coincident(g527,g528)
    c: Coincident(g528,g529)
    c: Coincident(g529,g530)
    c: Coincident(g530,g531)
    c: Coincident(g531,g532)
    c: Coincident(g532,g533)
    c: Coincident(g533,g534)
    c: Coincident(g534,g535)
    c: Coincident(g535,g496)
    c: Coincident(g536,g537)
    c: Coincident(g537,g538)
    c: Coincident(g538,g539)
    c: Coincident(g539,g540)
    c: Coincident(g540,g541)
    c: Coincident(g541,g542)
    c: Coincident(g542,g543)
    c: Coincident(g543,g544)
    c: Coincident(g544,g545)
    c: Coincident(g545,g546)
    c: Coincident(g546,g547)
    c: Coincident(g547,g548)
    c: Coincident(g548,g549)
    c: Coincident(g549,g550)
    c: Coincident(g550,g551)
    c: Coincident(g551,g552)
    c: Coincident(g552,g553)
    c: Coincident(g553,g554)
    c: Coincident(g554,g555)
    c: Coincident(g555,g556)
    c: Coincident(g556,g557)
    c: Coincident(g557,g558)
    c: Coincident(g558,g559)
    c: Coincident(g559,g560)
    c: Coincident(g560,g561)
    c: Coincident(g561,g562)
    c: Coincident(g562,g563)
    c: Coincident(g563,g564)
    c: Coincident(g564,g565)
    c: Coincident(g565,g566)
    c: Coincident(g566,g567)
    c: Coincident(g567,g568)
    c: Coincident(g568,g569)
    c: Coincident(g569,g570)
    c: Coincident(g570,g571)
    c: Coincident(g571,g572)
    c: Coincident(g572,g573)
    c: Coincident(g573,g574)
    c: Coincident(g574,g575)
    c: Coincident(g575,g536)
    c: Coincident(g576,g577)
    c: Coincident(g577,g578)
    c: Coincident(g578,g579)
    c: Coincident(g579,g580)
    c: Coincident(g580,g581)
    c: Coincident(g581,g582)
    c: Coincident(g582,g583)
    c: Coincident(g583,g584)
    c: Coincident(g584,g585)
    c: Coincident(g585,g586)
    c: Coincident(g586,g587)
    c: Coincident(g587,g576)
    c: Coincident(g588,g589)
    c: Coincident(g589,g590)
    c: Coincident(g590,g591)
    c: Coincident(g591,g592)
    c: Coincident(g592,g593)
    c: Coincident(g593,g594)
    c: Coincident(g594,g595)
    c: Coincident(g595,g596)
    c: Coincident(g596,g597)
    c: Coincident(g597,g598)
    c: Coincident(g598,g599)
    c: Coincident(g599,g600)
    c: Coincident(g600,g601)
    c: Coincident(g601,g602)
    c: Coincident(g602,g603)
    c: Coincident(g603,g604)
    c: Coincident(g604,g605)
    c: Coincident(g605,g606)
    c: Coincident(g606,g607)
    c: Coincident(g607,g608)
    c: Coincident(g608,g609)
    c: Coincident(g609,g610)
    c: Coincident(g610,g611)
    c: Coincident(g611,g612)
    c: Coincident(g612,g613)
    c: Coincident(g613,g614)
    c: Coincident(g614,g615)
    c: Coincident(g615,g616)
    c: Coincident(g616,g617)
    c: Coincident(g617,g618)
    c: Coincident(g618,g619)
    c: Coincident(g619,g620)
    c: Coincident(g620,g621)
    c: Coincident(g621,g622)
    c: Coincident(g622,g623)
    c: Coincident(g623,g624)
    c: Coincident(g624,g625)
    c: Coincident(g625,g626)
    c: Coincident(g626,g627)
    c: Coincident(g627,g628)
    c: Coincident(g628,g629)
    c: Coincident(g629,g630)
    c: Coincident(g630,g631)
    c: Coincident(g631,g632)
    c: Coincident(g632,g633)
    c: Coincident(g633,g634)
    c: Coincident(g634,g635)
    c: Coincident(g635,g636)
    c: Coincident(g636,g637)
    c: Coincident(g637,g638)
    c: Coincident(g638,g639)
    c: Coincident(g639,g640)
    c: Coincident(g640,g641)
    c: Coincident(g641,g642)
    c: Coincident(g642,g643)
    c: Coincident(g643,g644)
    c: Coincident(g644,g645)
    c: Coincident(g645,g646)
    c: Coincident(g646,g647)
    c: Coincident(g647,g648)
    c: Coincident(g648,g649)
    c: Coincident(g649,g650)
    c: Coincident(g650,g651)
    c: Coincident(g651,g652)
    c: Coincident(g652,g653)
    c: Coincident(g653,g654)
    c: Coincident(g654,g655)
    c: Coincident(g655,g656)
    c: Coincident(g656,g657)
    c: Coincident(g657,g658)
    c: Coincident(g658,g659)
    c: Coincident(g659,g660)
    c: Coincident(g660,g661)
    c: Coincident(g661,g662)
    c: Coincident(g662,g663)
    c: Coincident(g663,g664)
    c: Coincident(g664,g665)
    c: Coincident(g665,g666)
    c: Coincident(g666,g667)
    c: Coincident(g667,g668)
    c: Coincident(g668,g669)
    c: Coincident(g669,g670)
    c: Coincident(g670,g671)
    c: Coincident(g671,g672)
    c: Coincident(g672,g673)
    c: Coincident(g673,g674)
    c: Coincident(g674,g675)
    c: Coincident(g675,g588)
    c: Coincident(g676,g677)
    c: Coincident(g677,g678)
    c: Coincident(g678,g679)
    c: Coincident(g679,g680)
    c: Coincident(g680,g681)
    c: Coincident(g681,g682)
    c: Coincident(g682,g683)
    c: Coincident(g683,g684)
    c: Coincident(g684,g685)
    c: Coincident(g685,g686)
    c: Coincident(g686,g687)
    c: Coincident(g687,g688)
    c: Coincident(g688,g689)
    c: Coincident(g689,g690)
    c: Coincident(g690,g691)
    c: Coincident(g691,g676)
    c: Coincident(g692,g693)
    c: Coincident(g693,g694)
    c: Coincident(g694,g695)
    c: Coincident(g695,g696)
    c: Coincident(g696,g697)
    c: Coincident(g697,g698)
    c: Coincident(g698,g699)
    c: Coincident(g699,g700)
    c: Coincident(g700,g701)
    c: Coincident(g701,g702)
    c: Coincident(g702,g703)
    c: Coincident(g703,g704)
    c: Coincident(g704,g705)
    c: Coincident(g705,g706)
    c: Coincident(g706,g707)
    c: Coincident(g707,g708)
    c: Coincident(g708,g709)
    c: Coincident(g709,g710)
    c: Coincident(g710,g711)
    c: Coincident(g711,g712)
    c: Coincident(g712,g713)
    c: Coincident(g713,g714)
    c: Coincident(g714,g715)
    c: Coincident(g715,g716)
    c: Coincident(g716,g717)
    c: Coincident(g717,g718)
    c: Coincident(g718,g719)
    c: Coincident(g719,g720)
    c: Coincident(g720,g721)
    c: Coincident(g721,g722)
    c: Coincident(g722,g723)
    c: Coincident(g723,g724)
    c: Coincident(g724,g725)
    c: Coincident(g725,g726)
    c: Coincident(g726,g727)
    c: Coincident(g727,g728)
    c: Coincident(g728,g729)
    c: Coincident(g729,g730)
    c: Coincident(g730,g731)
    c: Coincident(g731,g692)
    c: Coincident(g732,g733)
    c: Coincident(g733,g734)
    c: Coincident(g734,g735)
    c: Coincident(g735,g736)
    c: Coincident(g736,g737)
    c: Coincident(g737,g738)
    c: Coincident(g738,g739)
    c: Coincident(g739,g740)
    c: Coincident(g740,g741)
    c: Coincident(g741,g742)
    c: Coincident(g742,g743)
    c: Coincident(g743,g744)
    c: Coincident(g744,g745)
    c: Coincident(g745,g746)
    c: Coincident(g746,g747)
    c: Coincident(g747,g748)
    c: Coincident(g748,g749)
    c: Coincident(g749,g750)
    c: Coincident(g750,g751)
    c: Coincident(g751,g752)
    c: Coincident(g752,g753)
    c: Coincident(g753,g754)
    c: Coincident(g754,g755)
    c: Coincident(g755,g756)
    c: Coincident(g756,g757)
    c: Coincident(g757,g758)
    c: Coincident(g758,g759)
    c: Coincident(g759,g760)
    c: Coincident(g760,g761)
    c: Coincident(g761,g762)
    c: Coincident(g762,g763)
    c: Coincident(g763,g732)
    c: Coincident(g764,g765)
    c: Coincident(g765,g766)
    c: Coincident(g766,g767)
    c: Coincident(g767,g768)
    c: Coincident(g768,g769)
    c: Coincident(g769,g770)
    c: Coincident(g770,g771)
    c: Coincident(g771,g772)
    c: Coincident(g772,g773)
    c: Coincident(g773,g774)
    c: Coincident(g774,g775)
    c: Coincident(g775,g776)
    c: Coincident(g776,g777)
    c: Coincident(g777,g778)
    c: Coincident(g778,g779)
    c: Coincident(g779,g780)
    c: Coincident(g780,g781)
    c: Coincident(g781,g782)
    c: Coincident(g782,g783)
    c: Coincident(g783,g784)
    c: Coincident(g784,g785)
    c: Coincident(g785,g786)
    c: Coincident(g786,g787)
    c: Coincident(g787,g764)
    c: Coincident(g788,g789)
    c: Coincident(g789,g790)
    c: Coincident(g790,g791)
    c: Coincident(g791,g792)
    c: Coincident(g792,g793)
    c: Coincident(g793,g794)
    c: Coincident(g794,g795)
    c: Coincident(g795,g796)
    c: Coincident(g796,g797)
    c: Coincident(g797,g798)
    c: Coincident(g798,g799)
    c: Coincident(g799,g800)
    c: Coincident(g800,g801)
    c: Coincident(g801,g802)
    c: Coincident(g802,g803)
    c: Coincident(g803,g804)
    c: Coincident(g804,g805)
    c: Coincident(g805,g806)
    c: Coincident(g806,g807)
    c: Coincident(g807,g808)
    c: Coincident(g808,g809)
    c: Coincident(g809,g810)
    c: Coincident(g810,g811)
    c: Coincident(g811,g812)
    c: Coincident(g812,g813)
    c: Coincident(g813,g814)
    c: Coincident(g814,g815)
    c: Coincident(g815,g816)
    c: Coincident(g816,g817)
    c: Coincident(g817,g818)
    c: Coincident(g818,g819)
    c: Coincident(g819,g820)
    c: Coincident(g820,g821)
    c: Coincident(g821,g822)
    c: Coincident(g822,g823)
    c: Coincident(g823,g824)
    c: Coincident(g824,g825)
    c: Coincident(g825,g826)
    c: Coincident(g826,g827)
    c: Coincident(g827,g828)
    c: Coincident(g828,g829)
    c: Coincident(g829,g830)
    c: Coincident(g830,g831)
    c: Coincident(g831,g832)
    c: Coincident(g832,g833)
    c: Coincident(g833,g834)
    c: Coincident(g834,g835)
    c: Coincident(g835,g836)
    c: Coincident(g836,g837)
    c: Coincident(g837,g838)
    c: Coincident(g838,g839)
    c: Coincident(g839,g840)
    c: Coincident(g840,g841)
    c: Coincident(g841,g842)
    c: Coincident(g842,g843)
    c: Coincident(g843,g844)
    c: Coincident(g844,g845)
    c: Coincident(g845,g846)
    c: Coincident(g846,g847)
    c: Coincident(g847,g848)
    c: Coincident(g848,g849)
    c: Coincident(g849,g850)
    c: Coincident(g850,g851)
    c: Coincident(g851,g852)
    c: Coincident(g852,g853)
    c: Coincident(g853,g854)
    c: Coincident(g854,g855)
    c: Coincident(g855,g856)
    c: Coincident(g856,g857)
    c: Coincident(g857,g858)
    c: Coincident(g858,g859)
    c: Coincident(g859,g788)
FEATURE [Sketcher::SketchObject] Sketch035
  ExternalGeometry = -> [Chamfer011]
  FullyConstrained = true
  MapMode = 5
  Placement = pos=(59,0,0) rot=(0.57735,0.57735,0.57735;2.0944rad)
  Support = -> [Chamfer011]
  sketch-geometry (4):
    g0: LineSegment StartX=9.7 StartY=3.5 StartZ=0 EndX=10.7 EndY=3.5 EndZ=0
    g1: LineSegment StartX=10.7 StartY=3.5 StartZ=0 EndX=17.55 EndY=5.3e-15 EndZ=0
    g2: LineSegment StartX=17.55 StartY=5.3e-15 StartZ=0 EndX=17.55 EndY=3.5 EndZ=0
    g3: LineSegment StartX=17.55 StartY=3.5 StartZ=0 EndX=10.7 EndY=3.5 EndZ=0
  constraints (10):
    c: Coincident(g0,g-3)
    c: PointOnObject(g0,g-3)
    c: Distance(g0) = 1
    c: Coincident(g1,g0)
    c: Coincident(g1,g-4)
    c: Coincident(g2,g1)
    c: Vertical(g2)
    c: Coincident(g3,g2)
    c: Coincident(g3,g1)
    c: Horizontal(g3)
FEATURE [PartDesign::Pocket] Pocket011
  BaseFeature = -> Chamfer011
  Direction = (-1,0,0)
  Length = 10
  Length2 = 5
  Profile = -> Sketch035
  ReferenceAxis = -> Sketch035 [N_Axis]
  Refine = true
  Reversed = true
  Type = 0
FEATURE [Sketcher::SketchObject] Sketch036
  ExternalGeometry = -> [Pocket011]
  FullyConstrained = true
  MapMode = 5
  Placement = pos=(2,0,0) rot=(0.57735,-0.57735,-0.57735;2.0944rad)
  Support = -> [Pocket011]
  sketch-geometry (3):
    g0: LineSegment StartX=-10.7 StartY=3.5 StartZ=0 EndX=-17.55 EndY=3.5 EndZ=0
    g1: LineSegment StartX=-17.55 StartY=3.5 StartZ=0 EndX=-17.55 EndY=5.3e-15 EndZ=0
    g2: LineSegment StartX=-17.55 StartY=5.3e-15 StartZ=0 EndX=-10.7 EndY=3.5 EndZ=0
  constraints (7):
    c: Horizontal(g0)
    c: Coincident(g1,g0)
    c: Vertical(g1)
    c: Coincident(g2,g1)
    c: Coincident(g2,g0)
    c: Coincident(g0,g-3)
    c: Coincident(g-3,g1)
FEATURE [PartDesign::Pocket] Pocket012
  BaseFeature = -> Pocket011
  Direction = (1,0,0)
  Length = 10
  Length2 = 5
  Profile = -> Sketch036
  ReferenceAxis = -> Sketch036 [N_Axis]
  Refine = true
  Reversed = true
  Type = 0
FEATURE [PartDesign::Pocket] Pocket013
  BaseFeature = -> Pocket012
  Direction = (0,-0.864038,-0.503426)
  Length = 0
  Length2 = 5
  Offset = 0.5
  Profile = -> Sketch034
  ReferenceAxis = -> Sketch034 [N_Axis]
  Type = 3
  UpToFace = -> Pocket012 [Face18]
FEATURE [PartDesign::Body] Body012  label="Cart Stand"
  BaseFeature = -> ShapeBinder
  Group = -> [Clone010,Sketch029,Pad018,Pad019,Sketch031,Pad020,Sketch032,Pad021,Pocket009,Sketch033,Pocket010,Pad022,Pad023,Chamfer011,Sketch034,Sketch035,Sketch036,Pocket011,Pocket012,Pocket013]
  Origin = -> Origin016
  Placement = pos=(-100,0,0) rot=(0,0,1;0rad)
  Tip = -> Pocket013
FEATURE [App::Part] Part  label="Game Boy-"
  Group = -> [Body,ShapeBinder,Body010,Body012]
  Origin = -> Origin001
